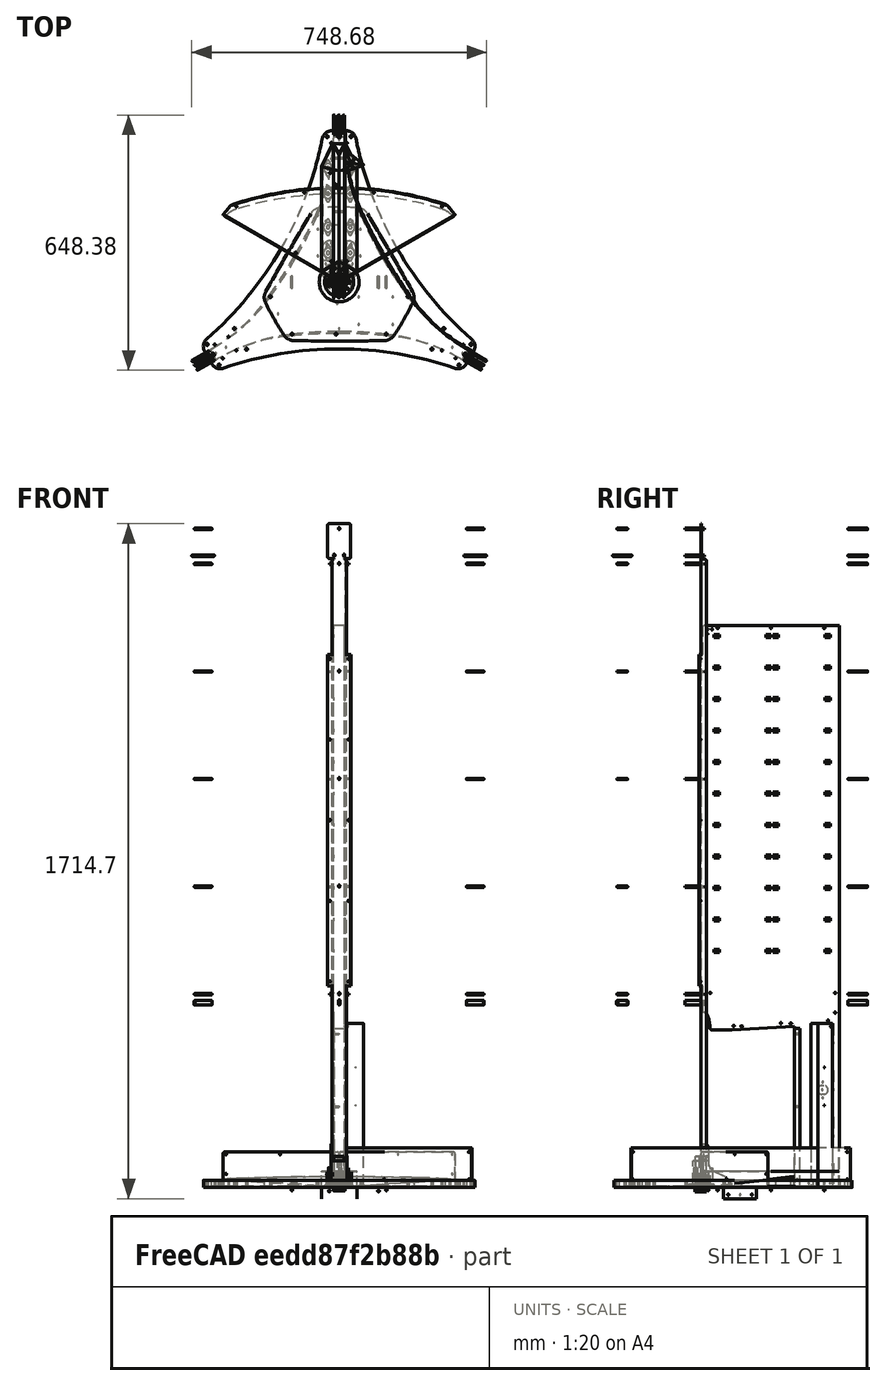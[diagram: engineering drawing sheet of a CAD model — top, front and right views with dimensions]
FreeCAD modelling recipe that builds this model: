
FCSTD DOCUMENT  (FreeCAD 1.1R38827 (Git))
Label: composit_full_size3
License: All rights reserved
LicenseURL: http://en.wikipedia.org/wiki/All_rights_reserved
objects: Part::FeaturePython×246, Sketcher::SketchObject×205, Part::Compound×101, PartDesign::SubShapeBinder×87, PartDesign::Body×73, PartDesign::Pocket×66, PartDesign::Boolean×59, App::Link×51, PartDesign::FeaturePython×49, PartDesign::CoordinateSystem×48, Part::Extrusion×45, Part::Mirroring×39, TechDraw::DrawViewDimension×38, PartDesign::Pad×37, PartDesign::Mirrored×23, App::DocumentObjectGroup×22, Part::Cylinder×18, Part::Feature×17, PartDesign::Hole×15, PartDesign::Plane×10, +28 more types
note: 1842 computed .brp shape members not serialized (recipe doc carries the construction recipe); baked Part::Feature solids carry a one-line shape summary decoded from their .brp
EXTERNAL_REF file=basin_big.FCStd obj=Spreadsheet
EXTERNAL_REF file=composit-properties.FCStd obj=Spreadsheet
EXTERNAL_REF file=module.FCStd obj=Spreadsheet
EXTERNAL_REF file=module.FCStd obj=Sketch
EXTERNAL_REF file=dropper.FCStd obj=Sketch007
EXTERNAL_REF file=dropper.FCStd obj=Sketch008
EXTERNAL_REF file=dropper.FCStd obj=Connect
EXTERNAL_REF file=hub2108.FCStd obj=Body
EXTERNAL_REF file=U-fix.FCStd obj=Body
EXTERNAL_REF file=ULY-P91-20W.FCStd obj=Sketch001
EXTERNAL_REF file=module.FCStd obj=Body
EXTERNAL_REF file=hub2108.FCStd obj=Sketch
EXTERNAL_REF file=hub2108.FCStd obj=Sketch001
EXTERNAL_REF file=U-fix.FCStd obj=Sketch002
EXTERNAL_REF file=hub2108.FCStd obj=Sketch002
EXTERNAL_REF file=hub2108.FCStd obj=Sketch003
EXTERNAL_REF file=ULZ-P02-14W.FCStd obj=Sketch
EXTERNAL_REF file=UET-VAS-060A20_12V_IP20.FCStd obj=Sketch001
EXTERNAL_REF file=composit_full_size3_composit_cut.FCStd obj=Link026
EXTERNAL_REF file=socket_fixture.FCStd obj=Sketch003
EXTERNAL_REF file=../../horec/el/horec_el3/plate_cut.FCStd obj=Clone
EXTERNAL_REF file=prima_jamb.FCStd obj=Body
EXTERNAL_REF file=filter.FCStd obj=Sketch003
EXTERNAL_REF file=filter.FCStd obj=Join
EXTERNAL_REF file=filter.FCStd obj=Join001
EXTERNAL_REF file=filter.FCStd obj=Sketch005
EXTERNAL_REF file=../../horec/el/horec_el3/plate_cut2.FCStd obj=Extrude001
EXTERNAL_REF file=filter.FCStd obj=Body003

FEATURE [Sketcher::SketchObject] Sketch
  ArcFitTolerance = 0
  FullyConstrained = true
  MakeInternals = false
  expr: Constraints[5] = <<Properties>>.endface_width
  expr: Constraints[9] = Spreadsheet.total_length
  sketch-geometry (4):
    g0: LineSegment [constr] StartX=-2.7195e-12 StartY=2.3473e-12 StartZ=0 EndX=14.5 EndY=8.37158 EndZ=0
    g1: LineSegment StartX=14.5 StartY=8.37158 StartZ=0 EndX=14.5 EndY=351.872 EndZ=0
    g2: GeomPoint [constr] X=-14.5 Y=351.872 Z=0
    g3: LineSegment StartX=14.5 StartY=351.872 StartZ=0 EndX=0 EndY=351.872 EndZ=0
  constraints (14):
    c: Coincident(g-1,g0)
    c: Coincident(g0,g1)
    c: Vertical(g1)
    c: Angle(g0) = 0.523599
    c: Symmetric(g2,g1,g-2)
    c: DistanceX(g2,g1) = 29
    c: Coincident(g3,g1)
    c: PointOnObject(g3,g-2)
    c: Horizontal(g3)
    c: DistanceY(g3) = 351.872
    c: Distance(g0,g1) = 352.17  'max_r'
    c: DistanceX(g1) = 14.5
    c: DistanceY(g1) = 8.37158
    c: Distance(g0) = 16.7432  'connection_offset'
FEATURE [Spreadsheet::Sheet] Spreadsheet  label="Properties"
  cells = B2(total_length)==22.5 mm + module#<<Properties>>.module_width + plane_middle; C2(endface_width)==29 mm; D2(rivet_d)==3.4 mm; E2(total_height)==modules_span + basin_big#<<Properties>>.height + 76 mm; F2(number_of_modules)=11; G2(module_distance_x)==2 mm; H2(modules_span)==<<module>>#<<Properties>>.module_fixture_distance_y * (number_of_modules - 1) + <<module>>#<<Properties>>.module_height; I2(top_offset)==27 mm; J2(plane_middle)==module#<<Properties>>.module_width + 25 mm + petal_offset; K2(inner_width)==endface_width - composit_properties#<<Properties>>.thickness * 2; L2(dropper_distance)==65 mm; M2(plane_width)==22.5 mm + module#<<Properties>>.module_width + plane_middle - petal_offset; N2(petal_offset)==endface_width / 2 / tan(60)
FEATURE [Part::Mirroring] Part__Mirroring  label="Sketch (Mirror #1)"
  Base = (0,0,0)
  Normal = (1,0,0)
  Source = -> Sketch
FEATURE [Part::Compound] Compound
  Links = -> [Part__Mirroring,Sketch]
FEATURE [Sketcher::SketchObject] Sketch001  label="part_main_sketch"
  ArcFitTolerance = 0
  ExternalGeometry = -> [Sketch]
  FullyConstrained = true
  MakeInternals = false
  expr: Constraints[7] = composit_properties#<<Properties>>.thickness
  sketch-geometry (3):
    g0: LineSegment StartX=0 StartY=351.872 StartZ=0 EndX=14.5 EndY=351.872 EndZ=0
    g1: LineSegment StartX=14.5 StartY=351.872 StartZ=0 EndX=14.5 EndY=4.90748 EndZ=0
    g2: LineSegment StartX=14.5 StartY=4.90748 StartZ=0 EndX=29.6554 EndY=-3.84252 EndZ=0
  constraints (9):
    c: PointOnObject(g0,g-2)
    c: Coincident(g0,g-3)
    c: Horizontal(g0)
    c: Coincident(g0,g1)
    c: PointOnObject(g1,g-3)
    c: Coincident(g1,g2)
    c: Angle(g2) = -0.523599
    c: Distance(g-3,g2) = 3
    c: Distance(g2) = 17.5
FEATURE [Part::Mirroring] Part__Mirroring001  label="part_main_sketch (Mirror #2)"
  Base = (0,0,0)
  Normal = (1,0,0)
  Source = -> Sketch001
FEATURE [Part::Compound] Compound001  label="part1_base"
  Links = -> [Part__Mirroring001,Sketch001]
FEATURE [Part::FeaturePython] Array001  label="2part_base"  # Draft array (typed FeaturePython)
  AlwaysSyncPlacement = false
  Angle = 240
  ArrayType = 1
  Axis = (0,0,1)
  Base = -> Compound
  Center = (0,0,0)
  Count = 2
  ExpandArray = false
  Fuse = false
  IntervalAxis = (0,0,0)
  IntervalX = (50,0,0)
  IntervalY = (0,50,0)
  IntervalZ = (0,0,50)
  NumberCircles = 3
  NumberPolar = 2
  NumberX = 2
  NumberY = 2
  NumberZ = 1
  PlacementList = 2 placements: [(0,0,0),(0,0,0)]
  RadialDistance = 50
  ScaleList = (2) [(1,1,1),(1,1,1)]
  Symmetry = 1
  TangentialDistance = 25
FEATURE [PartDesign::SubShapeBinder] Binder
  BindCopyOnChange = 0
  BindMode = 0
  ClaimChildren = true
  Context = -> Body [Binder.]
  Fuse = false
  MakeFace = true
  OffsetFill = false
  OffsetIntersection = false
  OffsetJoinType = 0
  OffsetOpenResult = false
  PartialLoad = false
  Relative = true
  Support = -> [Compound001]
  _Version = 2
  expr: Support = <<part1_base>>._self
FEATURE [PartDesign::SubShapeBinder] Binder001
  BindCopyOnChange = 0
  BindMode = 0
  ClaimChildren = true
  Context = -> Body001 [Binder001.]
  Fuse = false
  MakeFace = true
  OffsetFill = false
  OffsetIntersection = false
  OffsetJoinType = 0
  OffsetOpenResult = false
  PartialLoad = false
  Placement = pos=(0,0,0) rot=(0,0,1;4.18879rad)
  Relative = false
  Support = -> [Array001]
  _Version = 2
  expr: Support = <<2part_base>>._self
FEATURE [PartDesign::FeaturePython] BaseBend  # WARN: FeaturePython — macro-defined, semantics opaque (R4)
  BendSide = 1
  BendSketch = -> Binder
  MidPlane = false
  Reverse = false
  Suppressed = false
  length = 1428
  radius = 0.1
  thickness = 0.3
  expr: length = <<Properties>>.total_height
  expr: radius = composit_properties#<<Properties>>.bend_r
  expr: thickness = composit_properties#<<Properties>>.al_thickness
FEATURE [PartDesign::FeaturePython] BaseBend001  # WARN: FeaturePython — macro-defined, semantics opaque (R4)
  BendSide = 0
  BendSketch = -> Binder001
  MidPlane = false
  Reverse = false
  Suppressed = false
  length = 1428
  radius = 0.1
  thickness = 0.3
  expr: length = <<Properties>>.total_height
  expr: radius = composit_properties#<<Properties>>.bend_r
  expr: thickness = composit_properties#<<Properties>>.al_thickness
FEATURE [App::Link] Link  label="module_holes"
  LinkedObject = -> <external module.FCStd>#Sketch
  expr: LinkedObject = module#<<module_holes>>._self
FEATURE [Part::FeaturePython] LinearArray  # WARN: FeaturePython — macro-defined, semantics opaque (R4)
  Alignment = 0
  CellStart = A1
  Count = 11
  Dir = (0,-1,0)
  DirIsDriven = true
  DistributionLaw = 0
  DrivenProperty = 1
  EndInclusive = true
  ExposePlacement = false
  GeneratorMode = 1
  MarkerShape = 1
  MarkerSize = 0
  NumElements = 11
  OrientMode = 0
  Point = (0,0,0)
  PointIsDriven = true
  Reverse = false
  SpanEnd = 800
  SpanStart = 0
  Step = 80
  Type = lattice2LinearArray.LinearArray
  VSGVersion = 1
  Values = 0.0 | 80.0 | 160.0 | 240.0 | 320.0 | 400.0 | 480.0 | 560.0 | 640.0 | 720.0 | 800.0
  ValuesSource = 2
  isLattice = 1
  expr: Count = <<Properties>>.number_of_modules
  expr: SpanEnd = Step * (Count - 1)
  expr: Step = <<module>>#<<Properties>>.module_fixture_distance_y
FEATURE [Part::FeaturePython] LinearArray001  # WARN: FeaturePython — macro-defined, semantics opaque (R4)
  Alignment = 0
  CellStart = A1
  Count = 2
  Dir = (1,0,0)
  DirIsDriven = true
  DistributionLaw = 0
  DrivenProperty = 1
  EndInclusive = true
  ExposePlacement = false
  GeneratorMode = 1
  MarkerShape = 1
  MarkerSize = 0
  NumElements = 2
  OrientMode = 1
  Placement = pos=(-75,0,0) rot=(0,0,1;0rad)
  Point = (0,0,0)
  PointIsDriven = true
  Reverse = false
  SpanEnd = 150
  SpanStart = 0
  Step = 150
  Type = lattice2LinearArray.LinearArray
  VSGVersion = 1
  Values = 0.0 | 150.0
  ValuesSource = 2
  isLattice = 1
  expr: .Placement.Base.x = -SpanEnd / 2
  expr: SpanEnd = Step * (Count - 1)
  expr: Step = <<module>>#<<Properties>>.module_width + <<Properties>>.module_distance_x
FEATURE [Part::FeaturePython] Populate  label="Populate LinearArray with LinearArray001"  # WARN: FeaturePython — macro-defined, semantics opaque (R4)
  Copying = 0
  ExposePlacement = false
  MarkerShape = 1
  MarkerSize = 0
  NumElements = 22
  Object = -> LinearArray001
  OutputCompounding = 0
  PlacementsTo = -> LinearArray
  Referencing = 0
  Type = lattice2PopulateCopies.LatticePopulateCopies
  isLattice = 1
FEATURE [Part::FeaturePython] Populate001  label="Populate Populate LinearArray with LinearArray001 with module_holes"  # WARN: FeaturePython — macro-defined, semantics opaque (R4)
  Copying = 0
  ExposePlacement = false
  MarkerShape = 1
  MarkerSize = 0
  NumElements = 0
  Object = -> Link
  OutputCompounding = 1
  PlacementsTo = -> Populate
  Referencing = 0
  Type = lattice2PopulateCopies.LatticePopulateCopies
  isLattice = 0
FEATURE [Part::Extrusion] Extrude  label="modules_holes"
  Base = -> Populate001
  Dir = (0,0,1)
  DirMode = 2
  FaceMakerClass = Part::FaceMakerBullseye
  FaceMakerMode = 3
  LengthFwd = 31
  LengthRev = 0
  Placement = pos=(0,181.372,1401) rot=(0.57735,0.57735,0.57735;2.0944rad)
  Solid = true
  Symmetric = true
  expr: .Placement.Base.y = <<Properties>>.plane_middle
  expr: .Placement.Base.z = <<Properties>>.total_height - <<Properties>>.top_offset
  expr: LengthFwd = <<Properties>>.endface_width + 2 mm
FEATURE [Sketcher::SketchObject] Sketch003  label="basin_cut_sketch"
  ArcFitTolerance = 0
  ExternalGeometry = -> [Sketch]
  FullyConstrained = true
  MakeInternals = false
  Placement = pos=(0,0,0) rot=(0.57735,0.57735,0.57735;2.0944rad)
  expr: Constraints[27] = <<sink_bend_line>>.FaceAngle
  sketch-geometry (12):
    g0: LineSegment StartX=0 StartY=0 StartZ=0 EndX=238.372 EndY=0 EndZ=0
    g1: LineSegment StartX=238.372 StartY=0 StartZ=0 EndX=238.372 EndY=409.023 EndZ=0
    g2: LineSegment StartX=79.3716 StartY=400 StartZ=0 EndX=28.4155 EndY=400 EndZ=0
    g3: ArcOfCircle CenterX=28.4155 CenterY=405 CenterZ=0 NormalX=0 NormalY=0 NormalZ=1 AngleXU=0 Radius=5 StartAngle=3.17548 EndAngle=4.71239
    g4: ArcOfEllipse CenterX=9.37158 CenterY=400 CenterZ=0 NormalX=0 NormalY=0 NormalZ=1 MajorRadius=45 MinorRadius=14.1284 AngleXU=-1.5708 StartAngle=1.67835 EndAngle=3.14159
    g5: LineSegment [constr] StartX=9.37158 StartY=355 StartZ=0 EndX=9.37158 EndY=445 EndZ=0
    g6: LineSegment [constr] StartX=23.5 StartY=400 StartZ=0 EndX=-4.75684 EndY=400 EndZ=0
    g7: GeomPoint [constr] X=9.37158 Y=357.275 Z=0
    g8: GeomPoint [constr] X=9.37158 Y=442.725 Z=0
    g9: LineSegment StartX=0 StartY=0 StartZ=0 EndX=0 EndY=445 EndZ=0
    g10: LineSegment StartX=0 StartY=445 StartZ=0 EndX=9.37158 EndY=445 EndZ=0
    g11: LineSegment StartX=79.3716 StartY=400 StartZ=0 EndX=238.372 EndY=409.023 EndZ=0
  constraints (25):
    c: Coincident(g-1,g0)
    c: Horizontal(g0)
    c: Coincident(g0,g1)
    c: Vertical(g1)
    c: Horizontal(g2)
    c: Tangent(g3,g2) = 1.5708
    c: InternalAlignment(g5-g8 -> g4) x4
    c: Horizontal(g6)
    c: Tangent(g4,g3) = 1.5708
    c: Coincident(g9,g0)
    c: Coincident(g9,g10)
    c: Vertical(g9)
    c: Horizontal(g10)
    c: Tangent(g10,g4) = 1.5708
    c: DistanceX(g-3,g0) = 230
    c: DistanceY(g2) = 400
    c: DistanceY(g9) = 445
    c: DistanceX(g-3,g4) = 1
    c: Radius(g3) = 5
    c: DistanceX(g6) = 23.5
    c: PointOnObject(g4,g2)
    c: DistanceX(g-3,g2) = 71
    c: Coincident(g11,g2)
    c: Coincident(g11,g1)
    c: Angle(g11) = 0.0566865
FEATURE [Part::Extrusion] Extrude001  label="basin_cut"
  Base = -> Sketch003
  Dir = (1,0,0)
  DirMode = 2
  FaceMakerClass = Part::FaceMakerBullseye
  FaceMakerMode = 3
  LengthFwd = 30
  LengthRev = 0
  Solid = true
  Symmetric = true
FEATURE [Sketcher::SketchObject] Sketch004  label="leg_amplifier_base_sketch"
  ArcFitTolerance = 0
  ExternalGeometry = -> [Sketch003]
  FullyConstrained = true
  MakeInternals = false
  expr: Constraints[5] = <<Properties>>.endface_width / 2
  expr: Constraints[6] = composit_properties#<<Properties>>.bend_r + composit_properties#<<Properties>>.al_thickness
  expr: Constraints[7] = <<Properties>>.endface_width - composit_properties#<<Properties>>.thickness
  sketch-geometry (3):
    g0: LineSegment StartX=-11.5 StartY=-0.4 StartZ=0 EndX=14.5 EndY=-0.4 EndZ=0
    g1: LineSegment StartX=-11.5 StartY=-0.4 StartZ=0 EndX=-11.5 EndY=13 EndZ=0
    g2: LineSegment StartX=14.5 StartY=-0.4 StartZ=0 EndX=14.5 EndY=13 EndZ=0
  constraints (10):
    c: Horizontal(g0)
    c: Coincident(g1,g0)
    c: Vertical(g1)
    c: Coincident(g2,g0)
    c: Vertical(g2)
    c: DistanceX(g0) = 14.5
    c: DistanceY(g0,g-3) = 0.4
    c: DistanceX(g0,g0) = 26
    c: Horizontal(g1,g2)
    c: DistanceY(g-3,g2) = 13
FEATURE [Part::Mirroring] Part__Mirroring002  label="Sketch004 (Mirror #3)"
  Base = (0,0,0)
  Normal = (1,0,0)
  Source = -> Sketch004
FEATURE [Spreadsheet::Sheet] Spreadsheet001  label="Properties001"
  cells = B2(plane_width)==27.5 mm + module#<<Properties>>.module_width * 2 + 20 mm; C2(endface_width)==29 mm; D2(rivet_d)==3.4 mm; E2(total_height)==modules_span + basin_big#<<Properties>>.height; F2(number_of_modules)=11; G2(module_distance_x)==2 mm; H2(modules_span)==<<module>>#<<Properties>>.module_fixture_distance_y * number_of_modules + <<module>>#<<Properties>>.module_height; I2(top_offset)==30.5 mm; J2(plane_middle)==module#<<Properties>>.module_width + 25 mm; K2(inner_width)==endface_width - composit_properties#<<Properties>>.thickness * 2; L2(dropper_distance)==65 mm
FEATURE [Sketcher::SketchObject] Sketch005
  ArcFitTolerance = 0
  FullyConstrained = true
  MakeInternals = false
  expr: Constraints[5] = <<Properties001>>.endface_width
  expr: Constraints[6] = <<Properties001>>.plane_width
  sketch-geometry (4):
    g0: LineSegment [constr] StartX=5.67e-14 StartY=-9.82e-14 StartZ=0 EndX=14.5 EndY=8.37158 EndZ=0
    g1: LineSegment StartX=14.5 StartY=8.37158 StartZ=0 EndX=14.5 EndY=351.872 EndZ=0
    g2: GeomPoint [constr] X=-14.5 Y=351.872 Z=0
    g3: LineSegment StartX=14.5 StartY=351.872 StartZ=0 EndX=0 EndY=351.872 EndZ=0
  constraints (10):
    c: Coincident(g-1,g0)
    c: Coincident(g0,g1)
    c: Vertical(g1)
    c: Angle(g0) = 0.523599
    c: Symmetric(g2,g1,g-2)
    c: DistanceX(g2,g1) = 29
    c: DistanceY(g1,g1) = 343.5
    c: Coincident(g3,g1)
    c: PointOnObject(g3,g-2)
    c: Horizontal(g3)
FEATURE [Sketcher::SketchObject] Sketch006
  ArcFitTolerance = 0
  ExternalGeometry = -> [Sketch005]
  FullyConstrained = true
  MakeInternals = false
  Placement = pos=(0,0,0) rot=(0.57735,0.57735,0.57735;2.0944rad)
  sketch-geometry (12):
    g0: LineSegment StartX=0 StartY=0 StartZ=0 EndX=238.372 EndY=0 EndZ=0
    g1: LineSegment StartX=238.372 StartY=0 StartZ=0 EndX=238.372 EndY=410 EndZ=0
    g2: LineSegment StartX=238.372 StartY=410 StartZ=0 EndX=79.3716 EndY=400 EndZ=0
    g3: LineSegment StartX=79.3716 StartY=400 StartZ=0 EndX=19.9656 EndY=400 EndZ=0
    g4: ArcOfCircle CenterX=19.9656 CenterY=405 CenterZ=0 NormalX=0 NormalY=0 NormalZ=1 AngleXU=0 Radius=5 StartAngle=3.15538 EndAngle=4.71239
    g5: ArcOfEllipse CenterX=9.37158 CenterY=400 CenterZ=0 NormalX=0 NormalY=0 NormalZ=1 MajorRadius=45 MinorRadius=5.62842 AngleXU=-1.5708 StartAngle=1.6806 EndAngle=3.14159
    g6: LineSegment [constr] StartX=9.37158 StartY=355 StartZ=0 EndX=9.37158 EndY=445 EndZ=0
    g7: LineSegment [constr] StartX=15 StartY=400 StartZ=0 EndX=3.74316 EndY=400 EndZ=0
    g8: GeomPoint [constr] X=9.37158 Y=355.353 Z=0
    g9: GeomPoint [constr] X=9.37158 Y=444.647 Z=0
    g10: LineSegment StartX=0 StartY=0 StartZ=0 EndX=0 EndY=445 EndZ=0
    g11: LineSegment StartX=0 StartY=445 StartZ=0 EndX=9.37158 EndY=445 EndZ=0
  constraints (25):
    c: Coincident(g-1,g0)
    c: Horizontal(g0)
    c: Coincident(g0,g1)
    c: Vertical(g1)
    c: Coincident(g1,g2)
    c: Coincident(g2,g3)
    c: Horizontal(g3)
    c: Tangent(g4,g3) = 1.5708
    c: InternalAlignment(g6-g9 -> g5) x4
    c: Horizontal(g7)
    c: Tangent(g5,g4) = 1.5708
    c: Coincident(g10,g0)
    c: Coincident(g10,g11)
    c: Vertical(g10)
    c: Horizontal(g11)
    c: Tangent(g11,g5) = 1.5708
    c: DistanceX(g-3,g0) = 230
    c: DistanceY(g2) = 400
    c: DistanceY(g10) = 445
    c: DistanceX(g-3,g5) = 1
    c: Radius(g4) = 5
    c: DistanceX(g7) = 15
    c: PointOnObject(g5,g3)
    c: DistanceY(g1) = 410
    c: DistanceX(g-3,g2) = 71
FEATURE [Sketcher::SketchObject] Sketch007
  ArcFitTolerance = 0
  ExternalGeometry = -> [Sketch006]
  FullyConstrained = true
  MakeInternals = false
  expr: Constraints[5] = <<Properties001>>.endface_width / 2
  expr: Constraints[6] = composit_properties#<<Properties>>.bend_r + composit_properties#<<Properties>>.al_thickness
  expr: Constraints[7] = <<Properties001>>.endface_width - composit_properties#<<Properties>>.thickness
  sketch-geometry (3):
    g0: LineSegment StartX=-11.5 StartY=237.972 StartZ=0 EndX=14.5 EndY=237.972 EndZ=0
    g1: LineSegment StartX=-11.5 StartY=237.972 StartZ=0 EndX=-11.5 EndY=258.372 EndZ=0
    g2: LineSegment StartX=14.5 StartY=237.972 StartZ=0 EndX=14.5 EndY=258.372 EndZ=0
  constraints (10):
    c: Horizontal(g0)
    c: Coincident(g1,g0)
    c: Vertical(g1)
    c: Coincident(g2,g0)
    c: Vertical(g2)
    c: DistanceX(g0) = 14.5
    c: DistanceY(g0,g-3) = 0.4
    c: DistanceX(g0,g0) = 26
    c: Horizontal(g1,g2)
    c: DistanceY(g-3,g2) = 20
FEATURE [Part::FeaturePython] BaseBend003  label="BaseBend002_material_0.30ansi002"  # WARN: FeaturePython — macro-defined, semantics opaque (R4)
  BendSide = 0
  BendSketch = -> Part__Mirroring002
  MidPlane = false
  Reverse = false
  length = 403.5
  radius = 0.1
  thickness = 0.3
  expr: length = <<leg_amplifier>>.length
  expr: radius = composit_properties#<<Properties>>.bend_r
  expr: thickness = composit_properties#<<Properties>>.al_thickness
FEATURE [App::LinkGroup] CopyOnChangeGroup
  ElementList = -> [BaseBend003,Sketch007,Sketch006,Sketch005,Spreadsheet001]
  LinkMode = 1
FEATURE [App::Link] Link002  label="leg_amplifier_link"
  BendSketch = -> Part__Mirroring002
  LinkCopyOnChange = 2
  LinkCopyOnChangeGroup = -> CopyOnChangeGroup
  LinkCopyOnChangeSource = -> BaseBend002
  LinkCopyOnChangeTouched = true
  LinkPlacement = pos=(206.436,-119.186,0) rot=(0,0,1;4.18879rad)
  LinkedObject = -> BaseBend003
  Placement = pos=(206.436,-119.186,0) rot=(0,0,1;4.18879rad)
  expr: .LinkPlacement.Base.x = (<<Properties>>.petal_offset + 230 mm) * cos(-30)
  expr: .LinkPlacement.Base.y = (<<Properties>>.petal_offset + 230 mm) * sin(-30)
FEATURE [Part::Compound] Compound008
  Links = -> [Sketch004]
FEATURE [Part::FeaturePython] BaseBend002  label="leg_amplifier"  # WARN: FeaturePython — macro-defined, semantics opaque (R4)
  BendSide = 1
  BendSketch = -> Compound008
  MidPlane = false
  Placement = pos=(0,238.372,0) rot=(0,0,1;0rad)
  Reverse = false
  length = 403.5
  radius = 0.1
  thickness = 0.3
  expr: .Placement.Base.y = <<Properties>>.petal_offset + 230 mm
  expr: radius = composit_properties#<<Properties>>.bend_r
  expr: thickness = composit_properties#<<Properties>>.al_thickness
FEATURE [Part::Compound] Compound006  label="mirror_compound"
  Links = -> [BaseBend002]
  Placement = pos=(0,0,0) rot=(0,0,1;2.0944rad)
FEATURE [Part::Compound] Compound007  label="part2_fuse1"
  Links = -> [Link002,Compound006]
  expr: Links = list(<<leg_amplifier_link>>._self; <<mirror_compound>>._self)
FEATURE [App::DocumentObjectGroup] Group006  label="composit_cut"
FEATURE [App::DocumentObjectGroup] Group007  label="PP_cut"
FEATURE [App::DocumentObjectGroup] Group008  label="plywood_cut"
FEATURE [App::DocumentObjectGroup] Group002  label="cut"
  Group = -> [Group006,Group007,Group008]
FEATURE [Sketcher::SketchObject] Sketch008  label="pillar_base_sketch"
  ArcFitTolerance = 0
  FullyConstrained = true
  MakeInternals = false
  sketch-geometry (5):
    g0: LineSegment StartX=-18.3 StartY=19 StartZ=0 EndX=-18.3 EndY=-4.62e-14 EndZ=0
    g1: LineSegment StartX=-18.3 StartY=-4.62e-14 StartZ=0 EndX=18.3 EndY=-4.62e-14 EndZ=0
    g2: LineSegment StartX=18.3 StartY=-4.62e-14 StartZ=0 EndX=18.3 EndY=19 EndZ=0
    g3: LineSegment [constr] StartX=18.3 StartY=19 StartZ=0 EndX=-18.3 EndY=19 EndZ=0
    g4: GeomPoint [constr] X=8.6e-15 Y=9.5 Z=0
  constraints (13):
    c: Coincident(g0,g1)
    c: Coincident(g1,g2)
    c: Coincident(g2,g3)
    c: Coincident(g3,g0)
    c: Horizontal(g1)
    c: Horizontal(g3)
    c: Vertical(g0)
    c: Vertical(g2)
    c: Symmetric(g1,g0,g4)
    c: PointOnObject(g4,g-2)
    c: PointOnObject(g1,g-1)
    c: DistanceX(g1,g1) = 36.6  'width'
    c: DistanceY(g2,g2) = 19  'length'
FEATURE [PartDesign::SubShapeBinder] Binder002
  BindCopyOnChange = 0
  BindMode = 0
  ClaimChildren = true
  Fuse = false
  MakeFace = true
  OffsetFill = false
  OffsetIntersection = false
  OffsetJoinType = 0
  OffsetOpenResult = false
  PartialLoad = false
  Relative = false
  Support = -> [Sketch008]
  _Version = 2
FEATURE [PartDesign::FeaturePython] BaseBend004  label="pillar_BaseBend"  # WARN: FeaturePython — macro-defined, semantics opaque (R4)
  BendSide = 1
  BendSketch = -> Binder002
  MidPlane = false
  Reverse = false
  Suppressed = false
  length = 1594
  radius = 2
  thickness = 2
FEATURE [Sketcher::SketchObject] Sketch009
  ArcFitTolerance = 0
  AttachmentOffset = pos=(0,1594,0) rot=(0,0,1;0rad)
  AttachmentSupport = -> [XZ_Plane014]
  FullyConstrained = true
  MakeInternals = false
  MapMode = 5
  Placement = pos=(0,3.539e-13,1594) rot=(1,0,0;1.5708rad)
  expr: .AttachmentOffset.Base.y = BaseBend004.length
  expr: Constraints[15] = <<pillar_base_sketch>>.Constraints.width - (<<pillar_BaseBend>>.thickness + <<pillar_BaseBend>>.radius) * 2
  sketch-geometry (16):
    g0: LineSegment StartX=-14.3 StartY=0 StartZ=0 EndX=14.3 EndY=0 EndZ=0
    g1: LineSegment StartX=14.3 StartY=0 StartZ=0 EndX=14.3 EndY=2 EndZ=0
    g2: LineSegment StartX=14.3 StartY=2 StartZ=0 EndX=34.5 EndY=2 EndZ=0
    g3: LineSegment StartX=37.5 StartY=5 StartZ=0 EndX=37.5 EndY=87 EndZ=0
    g4: LineSegment StartX=34.5 StartY=90 StartZ=0 EndX=-34.5 EndY=90 EndZ=0
    g5: LineSegment StartX=-37.5 StartY=87 StartZ=0 EndX=-37.5 EndY=5 EndZ=0
    g6: LineSegment StartX=-34.5 StartY=2 StartZ=0 EndX=-14.3 EndY=2 EndZ=0
    g7: LineSegment StartX=-14.3 StartY=2 StartZ=0 EndX=-14.3 EndY=0 EndZ=0
    g8: ArcOfCircle CenterX=34.5 CenterY=5 CenterZ=0 NormalX=0 NormalY=0 NormalZ=1 AngleXU=0 Radius=3 StartAngle=4.71239 EndAngle=6.28319
    g9: GeomPoint [constr] X=37.5 Y=2 Z=0
    g10: ArcOfCircle CenterX=34.5 CenterY=87 CenterZ=0 NormalX=0 NormalY=0 NormalZ=1 AngleXU=0 Radius=3 StartAngle=1.02861e-11 EndAngle=1.5708
    g11: GeomPoint [constr] X=37.5 Y=90 Z=0
    g12: ArcOfCircle CenterX=-34.5 CenterY=87 CenterZ=0 NormalX=0 NormalY=0 NormalZ=1 AngleXU=0 Radius=3 StartAngle=1.5708 EndAngle=3.14159
    g13: GeomPoint [constr] X=-37.5 Y=90 Z=0
    g14: ArcOfCircle CenterX=-34.5 CenterY=5 CenterZ=0 NormalX=0 NormalY=0 NormalZ=1 AngleXU=0 Radius=3 StartAngle=3.14159 EndAngle=4.71239
    g15: GeomPoint [constr] X=-37.5 Y=2 Z=0
  constraints (38):
    c: PointOnObject(g0,g-1)
    c: Coincident(g0,g1)
    c: Vertical(g1)
    c: Coincident(g1,g2)
    c: Horizontal(g2)
    c: Vertical(g3)
    c: Vertical(g5)
    c: Horizontal(g6)
    c: Coincident(g6,g7)
    c: Vertical(g7)
    c: Coincident(g0,g7)
    c: Horizontal(g0)
    c: Symmetric(g6,g1,g-2)
    c: Symmetric(g11,g13,g-2)
    c: DistanceY(g1,g1) = 2
    c: DistanceX(g0,g0) = 28.6
    c: PointOnObject(g9,g2)
    c: PointOnObject(g9,g3)
    c: Tangent(g2,g8) = -1.5708
    c: Tangent(g3,g8) = -1.5708
    c: PointOnObject(g11,g3)
    c: PointOnObject(g11,g4)
    c: Tangent(g3,g10) = -1.5708
    c: Tangent(g4,g10) = -1.5708
    c: PointOnObject(g13,g4)
    c: PointOnObject(g13,g5)
    c: Tangent(g4,g12) = -1.5708
    c: Tangent(g5,g12) = -1.5708
    c: PointOnObject(g15,g5)
    c: PointOnObject(g15,g6)
    c: Tangent(g5,g14) = -1.5708
    c: Tangent(g6,g14) = -1.5708
    c: Equal(g14,g8)
    c: Equal(g14,g10)
    c: Equal(g14,g12)
    c: Radius(g14) = 3
    c: DistanceX(g13,g11) = 75
    c: DistanceY(g9,g11) = 88
FEATURE [Sketcher::SketchObject] Sketch011  label="pillar_bottom_cut_vert"
  ArcFitTolerance = 0
  AttachmentSupport = -> [XZ_Plane015]
  FullyConstrained = true
  MakeInternals = false
  MapMode = 5
  Placement = pos=(0,0,0) rot=(1,0,0;1.5708rad)
  expr: Constraints[15] = <<pillar_bottom_BaseBend>>.length
  expr: Constraints[16] = <<pillar_bottom_BaseBend>>.radius + <<pillar_bottom_BaseBend>>.thickness
  expr: Constraints[27] = <<pillar_base_sketch>>.Constraints.length - 4 mm
  sketch-geometry (15):
    g0: LineSegment StartX=-50.5 StartY=0 StartZ=0 EndX=-50.5 EndY=75 EndZ=0
    g1: LineSegment StartX=-45.5 StartY=80 StartZ=0 EndX=-40.5 EndY=80 EndZ=0
    g2: LineSegment StartX=50.5 StartY=4 StartZ=0 EndX=50.5 EndY=0 EndZ=0
    g3: LineSegment StartX=50.5 StartY=0 StartZ=0 EndX=-50.5 EndY=0 EndZ=0
    g4: ArcOfCircle CenterX=-45.5 CenterY=75 CenterZ=0 NormalX=0 NormalY=0 NormalZ=1 AngleXU=0 Radius=5 StartAngle=1.5708 EndAngle=3.14159
    g5: GeomPoint [constr] X=-50.5 Y=80 Z=0
    g6: ArcOfCircle CenterX=-40.5 CenterY=75 CenterZ=0 NormalX=0 NormalY=0 NormalZ=1 AngleXU=0 Radius=5 StartAngle=-9e-16 EndAngle=1.5708
    g7: GeomPoint [constr] X=-35.5 Y=80 Z=0
    g8: ArcOfCircle CenterX=45.5 CenterY=4 CenterZ=0 NormalX=0 NormalY=0 NormalZ=1 AngleXU=0 Radius=5 StartAngle=0 EndAngle=1.13485
    g9: GeomPoint [constr] X=50.5 Y=7.18672 Z=0
    g10: LineSegment StartX=-35.5 StartY=75 StartZ=0 EndX=-35.5 EndY=64.709 EndZ=0
    g11: LineSegment StartX=-19.6724 StartY=39.8753 StartZ=0 EndX=47.6113 EndY=8.53236 EndZ=0
    g12: ArcOfCircle CenterX=-8.10401 CenterY=64.709 CenterZ=0 NormalX=0 NormalY=0 NormalZ=1 AngleXU=0 Radius=27.396 StartAngle=3.14159 EndAngle=4.27645
    g13: GeomPoint [constr] X=-19.6724 Y=39.8753 Z=0
    g14: GeomPoint [constr] X=-13.5 Y=37 Z=0
  constraints (34):
    c: PointOnObject(g0,g-1)
    c: Vertical(g0)
    c: Horizontal(g1)
    c: Vertical(g2)
    c: Coincident(g2,g3)
    c: Coincident(g3,g0)
    c: PointOnObject(g5,g0)
    c: PointOnObject(g5,g1)
    c: Tangent(g0,g4) = 1.5708
    c: Tangent(g1,g4) = 1.5708
    c: PointOnObject(g7,g1)
    c: Tangent(g1,g6) = 1.5708
    c: PointOnObject(g9,g2)
    c: Tangent(g2,g8) = 1.5708
    c: Symmetric(g0,g2,g-2)
    c: DistanceX(g3,g3) = 101
    c: DistanceY(g2) = 4
    c: DistanceY(g5) = 80  'height'
    c: Radius(g4) = 5
    c: Radius(g8) = 5
    c: Equal(g4,g6)
    c: PointOnObject(g7,g10)
    c: PointOnObject(g9,g11)
    c: Vertical(g10)
    c: Tangent(g10,g6) = 1.5708
    c: Tangent(g12,g10) = -1.5708
    c: Tangent(g12,g11) = -1.5708
    c: DistanceX(g5,g7) = 15
    c: Tangent(g11,g8) = 1.5708
    c: Coincident(g11,g13)
    c: PointOnObject(g14,g11)
    c: DistanceY(g14) = 37
    c: DistanceX(g0,g14) = 37
    c: DistanceX(g11) = -19.6724
FEATURE [Sketcher::SketchObject] Sketch012
  ArcFitTolerance = 0
  AttachmentSupport = -> [XY_Plane015]
  FullyConstrained = true
  MakeInternals = false
  MapMode = 5
  expr: Constraints[18] = <<pillar_bottom_BaseSketch>>.Constraints.leg_length
  expr: Constraints[20] = <<pillar_bottom_BaseBend>>.radius + <<pillar_bottom_BaseBend>>.thickness
  expr: Constraints[9] = <<pillar_bottom_BaseBend>>.length
  sketch-geometry (9):
    g0: LineSegment StartX=-50.5 StartY=-4 StartZ=0 EndX=-50.5 EndY=0 EndZ=0
    g1: LineSegment StartX=-50.5 StartY=0 StartZ=0 EndX=50.5 EndY=0 EndZ=0
    g2: LineSegment StartX=50.5 StartY=0 StartZ=0 EndX=50.5 EndY=-4 EndZ=0
    g3: LineSegment StartX=29.5 StartY=-25 StartZ=0 EndX=-29.5 EndY=-25 EndZ=0
    g4: GeomPoint [constr] X=0 Y=-12.5 Z=0
    g5: ArcOfCircle CenterX=29.5 CenterY=-4 CenterZ=0 NormalX=0 NormalY=0 NormalZ=1 AngleXU=0 Radius=21 StartAngle=4.71239 EndAngle=6.28319
    g6: GeomPoint [constr] X=50.5 Y=-25 Z=0
    g7: ArcOfCircle CenterX=-29.5 CenterY=-4 CenterZ=0 NormalX=0 NormalY=0 NormalZ=1 AngleXU=0 Radius=21 StartAngle=3.14159 EndAngle=4.71239
    g8: GeomPoint [constr] X=-50.5 Y=-25 Z=0
  constraints (21):
    c: Coincident(g0,g1)
    c: Coincident(g1,g2)
    c: Horizontal(g1)
    c: Horizontal(g3)
    c: Vertical(g0)
    c: Vertical(g2)
    c: Symmetric(g1,g8,g4)
    c: PointOnObject(g4,g-2)
    c: PointOnObject(g1,g-1)
    c: DistanceX(g1,g1) = 101
    c: PointOnObject(g6,g2)
    c: PointOnObject(g6,g3)
    c: Tangent(g2,g5) = 1.5708
    c: Tangent(g3,g5) = 1.5708
    c: PointOnObject(g8,g0)
    c: PointOnObject(g8,g3)
    c: Tangent(g0,g7) = 1.5708
    c: Tangent(g3,g7) = 1.5708
    c: DistanceY(g6,g-1) = 25
    c: Equal(g7,g5)
    c: DistanceY(g2,g-1) = 4
FEATURE [Part::FeaturePython] WireFilter  # WARN: FeaturePython — macro-defined, semantics opaque (R4)
  AttacherType = Attacher::AttachEngine3D
  ClaimChildren = true
  ColorKeyCount = 8
  Colorize = true
  FaceMaker = 5
  FixNormal = false
  FollowSource = true
  InvertedFaceScale = 20
  MaxWires = 25
  Normal = (0,1,-2e-16)
  OffsetFill = false
  OffsetIntersection = false
  OffsetJoin = 0
  OffsetOpenResult = false
  Scale = (1,1,1)
  SelectEdges = false
  Source = -> Sketch011
  UniformScale = 1
  UseDefault = false
  UseSelected = true
  UseSelectedEdges = false
  Version = 0.2022.02.09
  WireOrder = [1]
FEATURE [Part::FeaturePython] WireFilter001  # WARN: FeaturePython — macro-defined, semantics opaque (R4)
  AttacherType = Attacher::AttachEngine3D
  ClaimChildren = true
  ColorKeyCount = 8
  Colorize = true
  FaceMaker = 5
  FixNormal = false
  FollowSource = true
  InvertedFaceScale = 5
  MaxWires = 25
  Normal = (0,0,1)
  OffsetFill = false
  OffsetIntersection = false
  OffsetJoin = 0
  OffsetOpenResult = false
  Scale = (1,1,1)
  SelectEdges = false
  Source = -> Sketch012
  UniformScale = 1
  UseDefault = false
  UseSelected = true
  UseSelectedEdges = false
  Version = 0.2022.02.09
  WireOrder = [1]
FEATURE [Sketcher::SketchObject] Sketch013
  ArcFitTolerance = 0
  AttachmentSupport = -> [XY_Plane016]
  FullyConstrained = true
  MakeInternals = false
  MapMode = 5
  sketch-geometry (5):
    g0: LineSegment StartX=-36 StartY=25 StartZ=0 EndX=-36 EndY=0 EndZ=0
    g1: LineSegment StartX=-36 StartY=0 StartZ=0 EndX=36 EndY=0 EndZ=0
    g2: LineSegment StartX=36 StartY=0 StartZ=0 EndX=36 EndY=25 EndZ=0
    g3: LineSegment [constr] StartX=36 StartY=25 StartZ=0 EndX=-36 EndY=25 EndZ=0
    g4: GeomPoint [constr] X=0 Y=12.5 Z=0
  constraints (13):
    c: Coincident(g0,g1)
    c: Coincident(g1,g2)
    c: Coincident(g2,g3)
    c: Coincident(g3,g0)
    c: Horizontal(g1)
    c: Horizontal(g3)
    c: Vertical(g0)
    c: Vertical(g2)
    c: Symmetric(g1,g0,g4)
    c: PointOnObject(g4,g-2)
    c: PointOnObject(g1,g-1)
    c: DistanceY(g2,g2) = 25
    c: DistanceX(g1,g1) = 72
FEATURE [PartDesign::FeaturePython] BaseBend006  # WARN: FeaturePython — macro-defined, semantics opaque (R4)
  BendSide = 1
  BendSketch = -> Sketch013
  MidPlane = false
  Reverse = false
  Suppressed = false
  length = 84
  radius = 2
  thickness = 2
FEATURE [PartDesign::FeaturePython] Bend  # WARN: FeaturePython — macro-defined, semantics opaque (R4)
  AutoMiter = true
  BaseFeature = -> BaseBend006
  BendType = 1
  LengthList = [70]
  LengthSpec = 1
  NonperforationMaxLength = 5
  Perforate = false
  PerforationAngle = 0
  PerforationInitialLength = 5
  PerforationMaxLength = 5
  ReliefFactor = 0.7
  Suppressed = false
  UseReliefFactor = false
  angle = 90
  baseObject = -> BaseBend006 [Edge26]
  bendAList = [90]
  extend1 = 0
  extend2 = 0
  gap1 = 0
  gap2 = 0
  invert = true
  kfactor = 0.5
  length = 70
  maxExtendDist = 5
  minGap = 0.1
  minReliefGap = 1
  miterangle1 = 0
  miterangle2 = 0
  offset = 0
  radius = 2
  reliefType = 0
  reliefd = 1
  reliefw = 0.8
  sketchflip = false
  sketchinvert = false
  unfold = false
  expr: radius = BaseBend006.radius
FEATURE [Sketcher::SketchObject] Sketch014  label="basement_bottom_sketch"
  ArcFitTolerance = 0
  FullyConstrained = true
  MakeInternals = false
  sketch-geometry (4):
    g0: LineSegment [constr] StartX=0 StartY=0 StartZ=0 EndX=147.224 EndY=85 EndZ=0
    g1: ArcOfCircle CenterX=930.111 CenterY=537 CenterZ=0 NormalX=0 NormalY=0 NormalZ=1 AngleXU=0 Radius=904 StartAngle=3.33435 EndAngle=3.66519
    g2: ArcOfCircle CenterX=18.317 CenterY=359.033 CenterZ=0 NormalX=0 NormalY=0 NormalZ=1 AngleXU=0 Radius=25 StartAngle=0.19276 EndAngle=1.51982
    g3: ArcOfCircle CenterX=0 CenterY=0 CenterZ=0 NormalX=0 NormalY=0 NormalZ=1 AngleXU=0 Radius=384.5 StartAngle=1.51982 EndAngle=1.5708
  constraints (13):
    c: Coincident(g0,g-1)
    c: Angle(g0) = 0.523599
    c: Coincident(g1,g0)
    c: PointOnObject(g1,g0)
    c: Tangent(g2,g1) = 1.5708
    c: Distance(g0) = 170  'min_r'
    c: Radius(g2) = 25
    c: PointOnObject(g3,g-2)
    c: PointOnObject(g3,g-2)
    c: Tangent(g3,g2) = -1.5708
    c: PointOnObject(g3,g-1)
    c: DistanceY(g3) = 384.5  'outer_r'
    c: Radius(g1) = 904
FEATURE [Sketcher::SketchObject] Sketch015  label="basement_sketch"
  ArcFitTolerance = 0
  FullyConstrained = true
  MakeInternals = false
  sketch-geometry (4):
    g0: LineSegment [constr] StartX=0 StartY=0 StartZ=0 EndX=219.104 EndY=126.5 EndZ=0
    g1: ArcOfCircle CenterX=-472.335 CenterY=-272.703 CenterZ=0 NormalX=0 NormalY=0 NormalZ=1 AngleXU=0 Radius=798.406 StartAngle=0.523599 EndAngle=0.870893
    g2: ArcOfCircle CenterX=12 CenterY=302.433 CenterZ=0 NormalX=0 NormalY=0 NormalZ=1 AngleXU=0 Radius=46.5 StartAngle=0.870893 EndAngle=1.53114
    g3: ArcOfCircle CenterX=0 CenterY=0 CenterZ=0 NormalX=0 NormalY=0 NormalZ=1 AngleXU=0 Radius=349.171 StartAngle=1.53114 EndAngle=1.5708
  constraints (13):
    c: Coincident(g1,g0)
    c: Angle(g0) = 0.523599
    c: Radius(g1) = 798.406
    c: Radius(g2) = 46.5
    c: Radius(g3) = 349.171  'max_r'
    c: Coincident(g3,g0)
    c: Coincident(g3,g-1)
    c: Tangent(g2,g1) = -1.5708
    c: Tangent(g3,g2) = -1.5708
    c: PointOnObject(g3,g-2)
    c: Distance(g0) = 253  'min_r'
    c: DistanceX(g2) = 12
    c: PointOnObject(g1,g0)
FEATURE [Part::Mirroring] Part__Mirroring003  label="Sketch014 (Mirror #4)"
  Base = (0,0,0)
  Normal = (1,0,0)
  Source = -> Sketch014
FEATURE [Part::Compound] Compound009
  Links = -> [Part__Mirroring003,Sketch014]
FEATURE [Part::FeaturePython] Array002  label="basement_bottom_2d"  # Draft array (typed FeaturePython)
  AlwaysSyncPlacement = false
  Angle = 360
  ArrayType = 1
  Axis = (0,0,1)
  Base = -> Compound009
  Center = (0,0,0)
  Count = 3
  ExpandArray = false
  Fuse = false
  IntervalAxis = (0,0,0)
  IntervalX = (50,0,0)
  IntervalY = (0,50,0)
  IntervalZ = (0,0,50)
  NumberCircles = 3
  NumberPolar = 3
  NumberX = 2
  NumberY = 2
  NumberZ = 1
  PlacementList = 3 placements: [(0,0,0),(0,0,0),(0,0,0)]
  RadialDistance = 50
  ScaleList = (3) [(1,1,1),(1,1,1),(1,1,1)]
  Symmetry = 1
  TangentialDistance = 25
FEATURE [Part::Mirroring] Part__Mirroring004  label="Sketch015 (Mirror #5)"
  Base = (0,0,0)
  Normal = (1,0,0)
  Source = -> Sketch015
FEATURE [PartDesign::SubShapeBinder] Binder003
  BindCopyOnChange = 0
  BindMode = 0
  ClaimChildren = true
  Context = -> Body007 [Binder003.]
  Fuse = false
  MakeFace = true
  OffsetFill = false
  OffsetIntersection = false
  OffsetJoinType = 0
  OffsetOpenResult = false
  PartialLoad = false
  Relative = false
  Support = -> [Array002]
  _Version = 2
FEATURE [PartDesign::SubShapeBinder] Binder004
  BindCopyOnChange = 0
  BindMode = 0
  ClaimChildren = true
  Context = -> Body009 [Binder004.]
  Fuse = false
  MakeFace = true
  Offset = 2
  OffsetFill = false
  OffsetIntersection = false
  OffsetJoinType = 0
  OffsetOpenResult = false
  PartialLoad = false
  Relative = false
  Support = -> [Array002]
  _Version = 2
FEATURE [PartDesign::SubShapeBinder] Binder005
  BindCopyOnChange = 0
  BindMode = 0
  ClaimChildren = true
  Context = -> Body006 [Binder005.]
  Fuse = false
  MakeFace = true
  OffsetFill = false
  OffsetIntersection = false
  OffsetJoinType = 0
  OffsetOpenResult = false
  PartialLoad = false
  Relative = false
  Support = -> [Array003]
  _Version = 2
FEATURE [PartDesign::SubShapeBinder] Binder006
  BindCopyOnChange = 0
  BindMode = 0
  ClaimChildren = true
  Context = -> Body008 [Binder006.]
  Fuse = false
  MakeFace = true
  Offset = 2
  OffsetFill = false
  OffsetIntersection = false
  OffsetJoinType = 0
  OffsetOpenResult = false
  PartialLoad = false
  Relative = false
  Support = -> [Array003]
  _Version = 2
FEATURE [Part::Compound] Compound010
  Links = -> [Sketch015,Part__Mirroring004]
FEATURE [Part::FeaturePython] Array003  label="basement_top_2d"  # Draft array (typed FeaturePython)
  AlwaysSyncPlacement = false
  Angle = 360
  ArrayType = 1
  Axis = (0,0,1)
  Base = -> Compound010
  Center = (0,0,0)
  Count = 3
  ExpandArray = false
  Fuse = false
  IntervalAxis = (0,0,0)
  IntervalX = (50,0,0)
  IntervalY = (0,50,0)
  IntervalZ = (0,0,50)
  NumberCircles = 3
  NumberPolar = 3
  NumberX = 2
  NumberY = 2
  NumberZ = 1
  PlacementList = 3 placements: [(0,0,0),(0,0,0),(0,0,0)]
  RadialDistance = 50
  ScaleList = (3) [(1,1,1),(1,1,1),(1,1,1)]
  Symmetry = 1
  TangentialDistance = 25
FEATURE [PartDesign::Pad] Pad001
  Direction = (0,0,1)
  Length = 18
  Length2 = 10
  Profile = -> Binder005
  Refine = true
  Suppressed = false
  Type = 0
FEATURE [PartDesign::Pad] Pad002
  Direction = (0,0,1)
  Length = 18
  Length2 = 10
  Profile = -> Binder003
  Suppressed = false
  Type = 0
FEATURE [PartDesign::Pad] Pad003
  Direction = (0,0,1)
  Length = 3
  Length2 = 10
  Profile = -> Binder006
  Suppressed = false
  Type = 0
FEATURE [PartDesign::Pad] Pad004
  Direction = (0,0,1)
  Length = 3
  Length2 = 10
  Profile = -> Binder004
  Suppressed = false
  Type = 0
FEATURE [PartDesign::SubShapeBinder] Binder007
  BindCopyOnChange = 0
  BindMode = 0
  ClaimChildren = true
  Fuse = false
  MakeFace = true
  OffsetFill = false
  OffsetIntersection = false
  OffsetJoinType = 0
  OffsetOpenResult = false
  PartialLoad = false
  Relative = false
  Support = -> [Compound011]
  _Version = 2
FEATURE [PartDesign::SubShapeBinder] Binder009  label="dropper_base"
  BindCopyOnChange = 0
  BindMode = 0
  ClaimChildren = true
  Fuse = false
  MakeFace = true
  OffsetFill = false
  OffsetIntersection = false
  OffsetJoinType = 0
  OffsetOpenResult = false
  PartialLoad = false
  Relative = true
  Support = -> [<external dropper.FCStd>#Sketch007]
  _Version = 2
  expr: Support = dropper#<<base>>._self
FEATURE [PartDesign::SubShapeBinder] Binder010  label="dropper_feed"
  BindCopyOnChange = 0
  BindMode = 0
  ClaimChildren = false
  Fuse = false
  MakeFace = true
  OffsetFill = false
  OffsetIntersection = false
  OffsetJoinType = 0
  OffsetOpenResult = false
  PartialLoad = false
  Relative = true
  Support = -> [<external dropper.FCStd>#Sketch008]
  _Version = 2
  expr: Support = dropper#<<feed>>._self
FEATURE [PartDesign::SubShapeBinder] Binder011  label="dropper_fix"
  BindCopyOnChange = 0
  BindMode = 0
  ClaimChildren = false
  Fuse = false
  MakeFace = true
  Offset = 0.5
  OffsetFill = false
  OffsetIntersection = false
  OffsetJoinType = 0
  OffsetOpenResult = false
  PartialLoad = false
  Relative = true
  Support = -> [<external dropper.FCStd>#Connect]
  _Version = 2
  expr: Support = dropper#<<fix>>._self
FEATURE [Part::FeaturePython] LinearArray002  # WARN: FeaturePython — macro-defined, semantics opaque (R4)
  Alignment = 0
  CellStart = A1
  Count = 2
  Dir = (1,0,0)
  DirIsDriven = true
  DistributionLaw = 0
  DrivenProperty = 1
  EndInclusive = true
  ExposePlacement = false
  GeneratorMode = 0
  MarkerShape = 1
  MarkerSize = 0
  NumElements = 2
  OrientMode = 1
  Placement = pos=(-32.5,0,0) rot=(0,0,1;0rad)
  Point = (0,0,0)
  PointIsDriven = true
  Reverse = false
  SpanEnd = 65
  SpanStart = 0
  Step = 65
  Type = lattice2LinearArray.LinearArray
  VSGVersion = 1
  Values = 0.0 | 65.0
  ValuesSource = 2
  isLattice = 1
  expr: .Placement.Base.x = -SpanEnd / 2
FEATURE [Part::FeaturePython] LinearArray003  # WARN: FeaturePython — macro-defined, semantics opaque (R4)
  Alignment = 0
  CellStart = A1
  Count = 2
  Dir = (1,0,0)
  DirIsDriven = true
  DistributionLaw = 0
  DrivenProperty = 1
  EndInclusive = true
  ExposePlacement = false
  GeneratorMode = 0
  MarkerShape = 1
  MarkerSize = 0
  NumElements = 2
  OrientMode = 1
  Placement = pos=(0,-75,0) rot=(0,0,1;1.5708rad)
  Point = (0,0,0)
  PointIsDriven = true
  Reverse = false
  SpanEnd = 150
  SpanStart = 0
  Step = 150
  Type = lattice2LinearArray.LinearArray
  VSGVersion = 1
  Values = 0.0 | 150.0
  ValuesSource = 2
  isLattice = 1
  expr: .Placement.Base.y = -SpanEnd / 2
FEATURE [Part::FeaturePython] LinearArray004  # WARN: FeaturePython — macro-defined, semantics opaque (R4)
  Alignment = 0
  CellStart = A1
  Count = 2
  Dir = (1,0,0)
  DirIsDriven = true
  DistributionLaw = 0
  DrivenProperty = 1
  EndInclusive = true
  ExposePlacement = false
  GeneratorMode = 0
  MarkerShape = 1
  MarkerSize = 0
  NumElements = 2
  OrientMode = 1
  Placement = pos=(-28.3,0,0) rot=(0,0,1;0rad)
  Point = (0,0,0)
  PointIsDriven = true
  Reverse = false
  SpanEnd = 56.6
  SpanStart = 0
  Step = 56.6
  Type = lattice2LinearArray.LinearArray
  VSGVersion = 1
  Values = 0.0 | 56.6
  ValuesSource = 2
  isLattice = 1
  expr: .Placement.Base.x = -SpanEnd / 2
  expr: SpanEnd = <<Properties>>.endface_width + dropper#<<base>>.Constraints.r * 2 + 4 mm
FEATURE [Part::FeaturePython] Populate002  label="Populate LinearArray004 with LinearArray003"  # WARN: FeaturePython — macro-defined, semantics opaque (R4)
  Copying = 0
  ExposePlacement = false
  MarkerShape = 1
  MarkerSize = 0
  NumElements = 4
  Object = -> LinearArray003
  OutputCompounding = 0
  PlacementsTo = -> LinearArray004
  Referencing = 0
  Type = lattice2PopulateCopies.LatticePopulateCopies
  isLattice = 1
FEATURE [Part::FeaturePython] Populate003  label="droppers placements"  # WARN: FeaturePython — macro-defined, semantics opaque (R4)
  Copying = 0
  ExposePlacement = false
  MarkerShape = 1
  MarkerSize = 0
  NumElements = 8
  Object = -> LinearArray002
  OutputCompounding = 0
  PlacementsTo = -> Populate002
  Referencing = 0
  Type = lattice2PopulateCopies.LatticePopulateCopies
  isLattice = 1
FEATURE [Part::FeaturePython] Populate004  label="populate dropper_fix"  # WARN: FeaturePython — macro-defined, semantics opaque (R4)
  Copying = 0
  ExposePlacement = false
  MarkerShape = 1
  MarkerSize = 0
  NumElements = 0
  Object = -> Binder011
  OutputCompounding = 1
  PlacementsTo = -> Populate003
  Referencing = 0
  Type = lattice2PopulateCopies.LatticePopulateCopies
  isLattice = 0
FEATURE [Part::FeaturePython] Populate005  label="Populate droppers placements with dropper_feed"  # WARN: FeaturePython — macro-defined, semantics opaque (R4)
  Copying = 0
  ExposePlacement = false
  MarkerShape = 1
  MarkerSize = 0
  NumElements = 0
  Object = -> Binder010
  OutputCompounding = 1
  PlacementsTo = -> Populate003
  Referencing = 0
  Type = lattice2PopulateCopies.LatticePopulateCopies
  isLattice = 0
FEATURE [Part::FeaturePython] Populate006  label="Populate droppers placements with dropper_base"  # WARN: FeaturePython — macro-defined, semantics opaque (R4)
  Copying = 0
  ExposePlacement = false
  MarkerShape = 1
  MarkerSize = 0
  NumElements = 0
  Object = -> Binder009
  OutputCompounding = 1
  PlacementsTo = -> Populate003
  Referencing = 0
  Type = lattice2PopulateCopies.LatticePopulateCopies
  isLattice = 0
FEATURE [Part::FeaturePython] Clone005  label="Populate droppers placements with dropper_base001"  # Draft clone (typed FeaturePython)
  AttacherType = Attacher::AttachEngine3D
  Fuse = false
  Objects = -> [Populate006]
  Placement = pos=(0,181.372,0) rot=(0,0,1;0rad)
  Scale = (1,1,1)
  expr: .Placement.Base.y = <<Properties>>.plane_middle
FEATURE [Sketcher::SketchObject] Sketch002  label="dropper_fix_sketch"
  ArcFitTolerance = 0
  ExternalGeometry = -> [Sketch,Clone005]
  FullyConstrained = true
  MakeInternals = false
  expr: Constraints[15] = composit_properties#<<Properties>>.thickness
  expr: Constraints[9] = 2 mm + <<dropper>>#<<base>>.Constraints.r * 2 + 2 mm
  sketch-geometry (8):
    g0: LineSegment StartX=42.1 StartY=292.046 StartZ=0 EndX=42.1 EndY=27.7705 EndZ=0
    g1: LineSegment StartX=0 StartY=348.872 StartZ=0 EndX=14.5 EndY=348.872 EndZ=0
    g2: LineSegment StartX=14.5 StartY=348.872 StartZ=0 EndX=42.1 EndY=292.046 EndZ=0
    g3: LineSegment StartX=0 StartY=0 StartZ=0 EndX=17 EndY=9.81495 EndZ=0
    g4: LineSegment StartX=17 StartY=9.81495 StartZ=0 EndX=15.5 EndY=12.413 EndZ=0
    g5: LineSegment StartX=15.5 StartY=12.413 StartZ=0 EndX=42.1 EndY=27.7705 EndZ=0
    g6: LineSegment [constr] StartX=28.3 StartY=288.872 StartZ=0 EndX=40.7133 EndY=294.901 EndZ=0
    g7: LineSegment [constr] StartX=28.3 StartY=288.872 StartZ=0 EndX=42.1 EndY=288.872 EndZ=0
  constraints (24):
    c: PointOnObject(g1,g-2)
    c: Coincident(g2,g0)
    c: Vertical(g0)
    c: Coincident(g3,g-1)
    c: Coincident(g5,g0)
    c: Coincident(g1,g2)
    c: Horizontal(g1)
    c: PointOnObject(g1,g-3)
    c: DistanceY(g1,g-3) = 3
    c: DistanceX(g-3,g5) = 27.6
    c: Coincident(g3,g4)
    c: PointOnObject(g-3,g3)
    c: Coincident(g4,g5)
    c: Perpendicular(g4,g3)
    c: Perpendicular(g5,g4)
    c: Distance(g4) = 3
    c: DistanceX(g-3,g4) = 1
    c: PointOnObject(g6,g2)
    c: PointOnObject(g7,g0)
    c: Perpendicular(g0,g7)
    c: Perpendicular(g2,g6)
    c: Equal(g7,g6)
    c: Coincident(g7,g-4)
    c: Coincident(g7,g6)
FEATURE [Part::Mirroring] Part__Mirroring005  label="dropper_fix_sketch (Mirror #6)"
  Base = (0,0,0)
  Normal = (1,0,0)
  Source = -> Sketch002
FEATURE [Part::Compound] Compound011  label="dropper_fix_base"
  Links = -> [Sketch002,Part__Mirroring005]
FEATURE [PartDesign::Pad] Pad005
  Direction = (0,0,1)
  Length = 3
  Length2 = 10
  Profile = -> Binder007
  Suppressed = false
  Type = 0
FEATURE [Sketcher::SketchObject] Sketch016
  ArcFitTolerance = 0
  ExternalGeometry = -> [Sketch002]
  FullyConstrained = true
  MakeInternals = false
  expr: Constraints[21] = composit_properties#<<Properties>>.thickness
  sketch-geometry (8):
    g0: LineSegment StartX=1.5 StartY=0.866025 StartZ=0 EndX=45.1 EndY=26.0385 EndZ=0
    g1: LineSegment StartX=45.1 StartY=26.0385 StartZ=0 EndX=45.1 EndY=292.736 EndZ=0
    g2: LineSegment StartX=45.1 StartY=292.736 StartZ=0 EndX=16.378 EndY=351.872 EndZ=0
    g3: LineSegment StartX=16.378 StartY=351.872 StartZ=0 EndX=0 EndY=351.872 EndZ=0
    g4: LineSegment [constr] StartX=14.5 StartY=351.872 StartZ=0 EndX=14.5 EndY=348.872 EndZ=0
    g5: LineSegment [constr] StartX=14.5 StartY=348.872 StartZ=0 EndX=17.1985 EndY=350.182 EndZ=0
    g6: LineSegment [constr] StartX=42.1 StartY=27.7705 StartZ=0 EndX=43.6 EndY=25.1725 EndZ=0
    g7: LineSegment [constr] StartX=42.1 StartY=27.7705 StartZ=0 EndX=45.1 EndY=27.7705 EndZ=0
  constraints (25):
    c: Coincident(g0,g1)
    c: Vertical(g1)
    c: Coincident(g1,g2)
    c: Coincident(g2,g3)
    c: PointOnObject(g3,g-2)
    c: Horizontal(g3)
    c: PointOnObject(g4,g3)
    c: Coincident(g4,g-4)
    c: Vertical(g4)
    c: Coincident(g4,g5)
    c: PointOnObject(g5,g2)
    c: Coincident(g-3,g6)
    c: PointOnObject(g6,g0)
    c: Coincident(g6,g7)
    c: PointOnObject(g7,g1)
    c: Horizontal(g7)
    c: Equal(g5,g4)
    c: Perpendicular(g5,g2)
    c: Perpendicular(g-4,g5)
    c: Perpendicular(g0,g6)
    c: Perpendicular(g-3,g6)
    c: DistanceY(g4,g4) = 3
    c: DistanceX(g0) = 1.5
    c: Equal(g5,g7)
    c: Equal(g7,g6)
FEATURE [Part::Mirroring] Part__Mirroring006  label="Sketch016 (Mirror #7)"
  Base = (0,0,0)
  Normal = (1,0,0)
  Source = -> Sketch016
FEATURE [Sketcher::SketchObject] Sketch017
  ArcFitTolerance = 0
  ExternalGeometry = -> [Sketch016]
  FullyConstrained = true
  MakeInternals = false
  sketch-geometry (9):
    g0: LineSegment StartX=45.1 StartY=26.0385 StartZ=0 EndX=-7.1e-15 EndY=52.077 EndZ=0
    g1: LineSegment StartX=45.1 StartY=292.736 StartZ=0 EndX=0 EndY=282.363 EndZ=0
    g2: LineSegment StartX=16.378 StartY=351.872 StartZ=0 EndX=0 EndY=325.709 EndZ=0
    g3: LineSegment [constr] StartX=0 StartY=351.872 StartZ=0 EndX=0 EndY=325.709 EndZ=0
    g4: LineSegment [constr] StartX=0 StartY=325.709 StartZ=0 EndX=23.5334 EndY=337.139 EndZ=0
    g5: LineSegment [constr] StartX=40.5682 StartY=302.066 StartZ=0 EndX=0 EndY=282.363 EndZ=0
    g6: LineSegment [constr] StartX=0 StartY=282.363 StartZ=0 EndX=45.1 EndY=282.363 EndZ=0
    g7: LineSegment [constr] StartX=22.55 StartY=13.0192 StartZ=0 EndX=-7.1e-15 EndY=52.077 EndZ=0
    g8: LineSegment [constr] StartX=-7.1e-15 StartY=52.077 StartZ=0 EndX=45.1 EndY=52.077 EndZ=0
  constraints (27):
    c: Coincident(g0,g-3)
    c: PointOnObject(g0,g-2)
    c: Coincident(g1,g-4)
    c: PointOnObject(g1,g-2)
    c: PointOnObject(g2,g-2)
    c: Coincident(g2,g-4)
    c: PointOnObject(g3,g-2)
    c: Coincident(g3,g2)
    c: Coincident(g3,g4)
    c: PointOnObject(g4,g-4)
    c: PointOnObject(g5,g-4)
    c: Coincident(g5,g1)
    c: Coincident(g5,g6)
    c: Horizontal(g6)
    c: PointOnObject(g7,g-3)
    c: Coincident(g7,g0)
    c: Coincident(g7,g8)
    c: Horizontal(g8)
    c: Vertical(g0,g8)
    c: Vertical(g8,g6)
    c: Horizontal(g3,g2)
    c: Perpendicular(g-4,g4)
    c: Perpendicular(g-4,g5)
    c: Equal(g6,g5)
    c: Equal(g4,g3)
    c: Perpendicular(g-3,g7)
    c: Equal(g7,g8)
FEATURE [Sketcher::SketchObject] Sketch018
  ArcFitTolerance = 0
  ExternalGeometry = -> [Sketch017]
  FullyConstrained = true
  MakeInternals = false
  sketch-geometry (30):
    g0: LineSegment StartX=0.05 StartY=0 StartZ=0 EndX=0.05 EndY=51.9904 EndZ=0
    g1: LineSegment StartX=0.05 StartY=51.9904 StartZ=0 EndX=44.65 EndY=26.2406 EndZ=0
    g2: LineSegment StartX=44.65 StartY=26.2406 StartZ=0 EndX=44.85 EndY=25.8942 EndZ=0
    g3: LineSegment StartX=44.85 StartY=25.8942 StartZ=0 EndX=45.1 EndY=26.0385 EndZ=0
    g4: LineSegment StartX=45.1 StartY=26.0385 StartZ=0 EndX=45.1 EndY=26.3272 EndZ=0
    g5: LineSegment StartX=45.1 StartY=26.3272 StartZ=0 EndX=44.7 EndY=26.3272 EndZ=0
    g6: LineSegment StartX=44.7 StartY=26.3272 StartZ=0 EndX=0.05 EndY=52.1059 EndZ=0
    g7: LineSegment StartX=0.05 StartY=52.1059 StartZ=0 EndX=0.05 EndY=282.323 EndZ=0
    g8: LineSegment StartX=0.05 StartY=282.323 StartZ=0 EndX=44.7 EndY=292.592 EndZ=0
    g9: LineSegment StartX=44.7 StartY=292.592 StartZ=0 EndX=45.1 EndY=292.592 EndZ=0
    g10: LineSegment StartX=45.1 StartY=292.592 StartZ=0 EndX=45.1 EndY=292.736 EndZ=0
    g11: LineSegment StartX=45.1 StartY=292.736 StartZ=0 EndX=45.0374 EndY=292.864 EndZ=0
    g12: LineSegment StartX=45.0374 StartY=292.864 StartZ=0 EndX=44.6776 EndY=292.69 EndZ=0
    g13: LineSegment StartX=44.6776 StartY=292.69 StartZ=0 EndX=0.05 EndY=282.425 EndZ=0
    g14: LineSegment StartX=0.05 StartY=282.425 StartZ=0 EndX=0.05 EndY=325.695 EndZ=0
    g15: LineSegment StartX=0.05 StartY=325.695 StartZ=0 EndX=16.1534 EndY=351.419 EndZ=0
    g16: LineSegment StartX=16.1534 StartY=351.419 StartZ=0 EndX=16.5132 EndY=351.593 EndZ=0
    g17: LineSegment StartX=16.5132 StartY=351.593 StartZ=0 EndX=16.378 EndY=351.872 EndZ=0
    g18: LineSegment StartX=16.378 StartY=351.872 StartZ=0 EndX=16.0687 EndY=351.872 EndZ=0
    g19: LineSegment StartX=16.0687 StartY=351.872 StartZ=0 EndX=16.0687 EndY=351.472 EndZ=0
    g20: LineSegment StartX=16.0687 StartY=351.472 StartZ=0 EndX=0 EndY=325.803 EndZ=0
    g21: LineSegment StartX=0.05 StartY=0 StartZ=0 EndX=0 EndY=0 EndZ=0
    g22: LineSegment [constr] StartX=0 StartY=0 StartZ=0 EndX=45.1 EndY=26.0385 EndZ=0
    g23: LineSegment [constr] StartX=45.1 StartY=26.0385 StartZ=0 EndX=45.1 EndY=292.736 EndZ=0
    g24: LineSegment [constr] StartX=45.1 StartY=292.736 StartZ=0 EndX=16.378 EndY=351.872 EndZ=0
    g25: LineSegment [constr] StartX=16.378 StartY=351.872 StartZ=0 EndX=0 EndY=351.872 EndZ=0
    g26: LineSegment [constr] StartX=-0.05 StartY=51.9904 StartZ=0 EndX=0.05 EndY=51.9904 EndZ=0
    g27: LineSegment [constr] StartX=0.05 StartY=51.9904 StartZ=0 EndX=0.1 EndY=52.077 EndZ=0
    g28: LineSegment [constr] StartX=0.05 StartY=282.425 StartZ=0 EndX=0.0724148 EndY=282.328 EndZ=0
    g29: LineSegment [constr] StartX=0.05 StartY=325.695 StartZ=0 EndX=-0.0347611 EndY=325.748 EndZ=0
  constraints (80):
    c: PointOnObject(g0,g-1)
    c: Vertical(g0)
    c: Coincident(g0,g1)
    c: Coincident(g1,g2)
    c: Coincident(g2,g3)
    c: Coincident(g3,g-5)
    c: Coincident(g3,g4)
    c: Vertical(g4)
    c: Coincident(g4,g5)
    c: Coincident(g5,g6)
    c: Coincident(g6,g7)
    c: Vertical(g7)
    c: Coincident(g7,g8)
    c: Coincident(g8,g9)
    c: Coincident(g9,g10)
    c: Coincident(g10,g-4)
    c: Vertical(g10)
    c: Coincident(g10,g11)
    c: Coincident(g11,g12)
    c: Coincident(g12,g13)
    c: Coincident(g13,g14)
    c: Vertical(g14)
    c: Coincident(g14,g15)
    c: Coincident(g15,g16)
    c: Coincident(g16,g17)
    c: Coincident(g17,g-3)
    c: Coincident(g17,g18)
    c: Horizontal(g18)
    c: Coincident(g18,g19)
    c: Vertical(g19)
    c: Coincident(g19,g20)
    c: PointOnObject(g20,g-2)
    c: Equal(g19,g16)
    c: Equal(g16,g12)
    c: Equal(g12,g9)
    c: Equal(g9,g5)
    c: Equal(g5,g2)
    c: Coincident(g21,g0)
    c: Coincident(g21,g-1)
    c: Coincident(g21,g22)
    c: Coincident(g22,g3)
    c: Coincident(g3,g23)
    c: Coincident(g23,g10)
    c: Coincident(g23,g24)
    c: Coincident(g24,g17)
    c: Coincident(g24,g25)
    c: PointOnObject(g25,g-2)
    c: Horizontal(g25)
    c: PointOnObject(g11,g24)
    c: PointOnObject(g2,g22)
    c: DistanceY(g19,g19) = 0.4
    c: Parallel(g15,g-3)
    c: Parallel(g-3,g20)
    c: Parallel(g13,g-4)
    c: Parallel(g-4,g8)
    c: Parallel(g6,g-5)
    c: Parallel(g-5,g1)
    c: Coincident(g26,g0)
    c: Coincident(g26,g27)
    c: PointOnObject(g27,g6)
    c: Symmetric(g26,g0,g-2)
    c: Vertical(g0,g6)
    c: Vertical(g7,g13)
    c: Coincident(g28,g13)
    c: PointOnObject(g28,g8)
    c: Coincident(g29,g14)
    c: PointOnObject(g29,g20)
    c: Equal(g26,g27)
    c: PointOnObject(g16,g24)
    c: Symmetric(g14,g29,g-3)
    c: DistanceX(g26,g26) = 0.1
    c: Perpendicular(g3,g2)
    c: Perpendicular(g4,g5)
    c: Equal(g27,g28)
    c: Equal(g29,g28)
    c: Perpendicular(g10,g9)
    c: Perpendicular(g11,g12)
    c: Symmetric(g0,g27,g-5)
    c: Perpendicular(g17,g16)
    c: Symmetric(g28,g13,g-4)
FEATURE [Part::Compound] Compound012
  Links = -> [Sketch016,Part__Mirroring006]
FEATURE [Part::Mirroring] Part__Mirroring007  label="Sketch018 (Mirror #8)"
  Base = (0,0,0)
  Normal = (1,0,0)
  Source = -> Sketch018
FEATURE [Part::Compound] Compound013
  Links = -> [Sketch018,Part__Mirroring007]
FEATURE [PartDesign::SubShapeBinder] Binder012
  BindCopyOnChange = 0
  BindMode = 0
  ClaimChildren = true
  Fuse = false
  MakeFace = true
  OffsetFill = false
  OffsetIntersection = false
  OffsetJoinType = 0
  OffsetOpenResult = false
  PartialLoad = false
  Placement = pos=(0,0,40) rot=(0,0,1;0rad)
  Relative = false
  Support = -> [Compound012]
  _Version = 2
FEATURE [PartDesign::SubShapeBinder] Binder013
  BindCopyOnChange = 0
  BindMode = 0
  ClaimChildren = true
  Fuse = false
  MakeFace = true
  OffsetFill = false
  OffsetIntersection = false
  OffsetJoinType = 0
  OffsetOpenResult = false
  PartialLoad = false
  Placement = pos=(0,0,40) rot=(0,0,1;0rad)
  Relative = false
  Support = -> [Compound013]
  _Version = 2
FEATURE [PartDesign::FeaturePython] BaseBend007  # WARN: FeaturePython — macro-defined, semantics opaque (R4)
  BendSide = 1
  BendSketch = -> Binder012
  MidPlane = false
  Reverse = true
  Suppressed = false
  length = 100
  radius = 0.1
  thickness = 0.3
  expr: radius = composit_properties#<<Properties>>.bend_r
  expr: thickness = composit_properties#<<Properties>>.al_thickness
FEATURE [PartDesign::FeaturePython] Bend001  # WARN: FeaturePython — macro-defined, semantics opaque (R4)
  AutoMiter = false
  BaseFeature = -> BaseBend007
  BendType = 0
  LengthList = [47]
  LengthSpec = 1
  NonperforationMaxLength = 5
  Perforate = false
  PerforationAngle = 0
  PerforationInitialLength = 5
  PerforationMaxLength = 5
  ReliefFactor = 0.7
  Suppressed = false
  UseReliefFactor = false
  angle = 90
  baseObject = -> BaseBend007 [Edge14,Edge30,Edge46,Edge62,Edge70,Edge86,Edge102,Edge116]
  bendAList = [90]
  extend1 = 0
  extend2 = 0
  gap1 = 0
  gap2 = 0
  invert = false
  kfactor = 0.5
  length = 47
  maxExtendDist = 5
  minGap = 0.1
  minReliefGap = 1
  miterangle1 = 0
  miterangle2 = 0
  offset = 0
  radius = 0.1
  reliefType = 0
  reliefd = 1
  reliefw = 0.8
  sketchflip = false
  sketchinvert = false
  unfold = false
  expr: radius = BaseBend007.radius
FEATURE [PartDesign::Pocket] Pocket002
  BaseFeature = -> Bend001
  Direction = (0,0,-1)
  Length = 5
  Length2 = 5
  Profile = -> Binder013 [Face1]
  Refine = true
  Reversed = true
  Suppressed = false
  Type = 1
FEATURE [Sketcher::SketchObject] Sketch019
  ArcFitTolerance = 0
  ExternalGeometry = -> [Sketch017]
  FullyConstrained = true
  MakeInternals = false
  expr: Constraints[12] = <<Properties>>.rivet_d
  sketch-geometry (13):
    g0: Circle [constr] CenterX=0 CenterY=325.709 CenterZ=0 NormalX=0 NormalY=0 NormalZ=1 AngleXU=0 Radius=1.7
    g1: Circle CenterX=0 CenterY=282.363 CenterZ=0 NormalX=0 NormalY=0 NormalZ=1 AngleXU=0 Radius=2
    g2: Circle CenterX=-22.55 CenterY=277.288 CenterZ=0 NormalX=0 NormalY=0 NormalZ=1 AngleXU=0 Radius=1.7
    g3: Circle CenterX=22.55 CenterY=277.288 CenterZ=0 NormalX=0 NormalY=0 NormalZ=1 AngleXU=0 Radius=1.7
    g4: Circle CenterX=0 CenterY=52.077 CenterZ=0 NormalX=0 NormalY=0 NormalZ=1 AngleXU=0 Radius=2
    g5: Circle CenterX=20 CenterY=52.077 CenterZ=0 NormalX=0 NormalY=0 NormalZ=1 AngleXU=0 Radius=1.7
    g6: Circle CenterX=10 CenterY=34.7565 CenterZ=0 NormalX=0 NormalY=0 NormalZ=1 AngleXU=0 Radius=1.7
    g7: Circle CenterX=-10 CenterY=34.7565 CenterZ=0 NormalX=0 NormalY=0 NormalZ=1 AngleXU=0 Radius=1.7
    g8: Circle CenterX=-20 CenterY=52.077 CenterZ=0 NormalX=0 NormalY=0 NormalZ=1 AngleXU=0 Radius=1.7
    g9: GeomPoint [constr] X=22.55 Y=287.549 Z=0
    g10: LineSegment [constr] StartX=0 StartY=34.7565 StartZ=0 EndX=10 EndY=34.7565 EndZ=0
    g11: LineSegment [constr] StartX=10 StartY=34.7565 StartZ=0 EndX=15 EndY=43.4167 EndZ=0
    g12: Circle CenterX=0 CenterY=325.709 CenterZ=0 NormalX=0 NormalY=0 NormalZ=1 AngleXU=0 Radius=2
  constraints (29):
    c: Coincident(g0,g-4)
    c: Coincident(g1,g-3)
    c: Coincident(g4,g-5)
    c: Symmetric(g8,g5,g-2)
    c: Symmetric(g7,g6,g-2)
    c: Symmetric(g3,g2,g-2)
    c: Equal(g0,g3)
    c: Equal(g0,g2)
    c: Equal(g0,g8)
    c: Equal(g0,g5)
    c: Equal(g0,g7)
    c: Equal(g0,g6)
    c: Diameter(g0) = 3.4
    c: Symmetric(g1,g-3,g9)
    c: Symmetric(g6,g5,g-5)
    c: PointOnObject(g10,g-2)
    c: Coincident(g10,g6)
    c: Horizontal(g10)
    c: Coincident(g10,g11)
    c: PointOnObject(g11,g-5)
    c: Perpendicular(g-5,g11)
    c: Equal(g11,g10)
    c: DistanceX(g10,g10) = 10
    c: Vertical(g3,g9)
    c: Distance(g3,g-3) = 10
    c: Coincident(g12,g0)
    c: Diameter(g12) = 4
    c: Equal(g4,g1)
    c: Equal(g1,g12)
FEATURE [PartDesign::SubShapeBinder] Binder014
  BindCopyOnChange = 0
  BindMode = 0
  ClaimChildren = true
  Context = -> Link012 [Binder014.]
  Fuse = false
  MakeFace = true
  OffsetFill = false
  OffsetIntersection = false
  OffsetJoinType = 0
  OffsetOpenResult = false
  PartialLoad = false
  Relative = true
  Support = -> [Sketch019]
  _Version = 2
FEATURE [Sketcher::SketchObject] Sketch020
  ArcFitTolerance = 0
  AttachmentSupport = -> [XY_Plane005]
  FullyConstrained = true
  MakeInternals = false
  MapMode = 5
  expr: Constraints[10] = composit_properties#<<Properties>>.bend_r + composit_properties#<<Properties>>.al_thickness
  sketch-geometry (5):
    g0: ArcOfCircle CenterX=0 CenterY=0.46188 CenterZ=0 NormalX=0 NormalY=0 NormalZ=1 AngleXU=0 Radius=5 StartAngle=0.523599 EndAngle=2.61799
    g1: LineSegment StartX=0 StartY=0 StartZ=0 EndX=4.53013 EndY=2.61547 EndZ=0
    g2: LineSegment StartX=4.53013 StartY=2.61547 StartZ=0 EndX=4.33013 EndY=2.96188 EndZ=0
    g3: LineSegment StartX=0 StartY=0 StartZ=0 EndX=-4.53013 EndY=2.61547 EndZ=0
    g4: LineSegment StartX=-4.53013 StartY=2.61547 StartZ=0 EndX=-4.33013 EndY=2.96188 EndZ=0
  constraints (13):
    c: PointOnObject(g0,g-2)
    c: Coincident(g1,g-1)
    c: Coincident(g2,g1)
    c: Coincident(g3,g1)
    c: Coincident(g4,g3)
    c: Perpendicular(g3,g4)
    c: Perpendicular(g1,g2)
    c: Tangent(g2,g0) = -1.5708
    c: Tangent(g4,g0) = 1.5708
    c: Equal(g4,g2)
    c: Distance(g2) = 0.4
    c: Diameter(g0) = 10
    c: Angle(g1,g3) = 2.0944
FEATURE [PartDesign::SubShapeBinder] Binder015
  BindCopyOnChange = 0
  BindMode = 0
  ClaimChildren = false
  Context = -> Link012 [Binder015.]
  Fuse = false
  MakeFace = true
  OffsetFill = false
  OffsetIntersection = false
  OffsetJoinType = 0
  OffsetOpenResult = false
  PartialLoad = false
  Relative = true
  Support = -> [Sketch002]
  _Version = 2
  expr: Support = <<dropper_fix_sketch>>._self
FEATURE [Sketcher::SketchObject] Sketch022  label="cap_outer_shape"
  ArcFitTolerance = 0
  AttachmentSupport = -> [YZ_Plane005]
  ExternalGeometry = -> [Binder012]
  FullyConstrained = true
  MakeInternals = false
  MapMode = 5
  Placement = pos=(0,0,0) rot=(0.57735,0.57735,0.57735;2.0944rad)
  expr: Constraints[11] = composit_properties#<<Properties>>.bend_r + composit_properties#<<Properties>>.al_thickness
  expr: Constraints[9] = composit_properties#<<Properties>>.bend_r + composit_properties#<<Properties>>.al_thickness + 0.01 mm
  sketch-geometry (5):
    g0: LineSegment StartX=351.882 StartY=40.41 StartZ=0 EndX=0 EndY=40.41 EndZ=0
    g1: LineSegment StartX=0 StartY=40.41 StartZ=0 EndX=0 EndY=0 EndZ=0
    g2: LineSegment StartX=0 StartY=0 StartZ=0 EndX=351.882 EndY=0 EndZ=0
    g3: LineSegment StartX=351.882 StartY=0 StartZ=0 EndX=351.882 EndY=40.41 EndZ=0
    g4: GeomPoint [constr] X=351.872 Y=40.4 Z=0
  constraints (14):
    c: Coincident(g0,g1)
    c: Coincident(g1,g2)
    c: Coincident(g2,g3)
    c: Coincident(g3,g0)
    c: Horizontal(g0)
    c: Horizontal(g2)
    c: Vertical(g1)
    c: Vertical(g3)
    c: Coincident(g1,g-1)
    c: DistanceY(g-3,g0) = 0.41
    c: DistanceX(g-3,g0) = 0.01
    c: DistanceY(g-3,g4) = 0.4
    c: Vertical(g-3,g4)
    c: DistanceY(g4) = 40.4  'height'
FEATURE [Part::FeaturePython] WireFilter002  # WARN: FeaturePython — macro-defined, semantics opaque (R4)
  AttacherType = Attacher::AttachEngine3D
  ClaimChildren = true
  ColorKeyCount = 8
  Colorize = true
  FaceMaker = 5
  FixNormal = false
  FollowSource = true
  InvertedFaceScale = 5
  MaxWires = 25
  Normal = (1,0,0)
  OffsetFill = false
  OffsetIntersection = false
  OffsetJoin = 0
  OffsetOpenResult = false
  Scale = (1,1,1)
  SelectEdges = false
  Source = -> Sketch022
  UniformScale = 1
  UseDefault = false
  UseSelected = true
  UseSelectedEdges = false
  Version = 0.2022.02.09
  WireOrder = [1]
FEATURE [PartDesign::SubShapeBinder] Binder016
  BindCopyOnChange = 0
  BindMode = 0
  ClaimChildren = true
  Fuse = false
  MakeFace = false
  OffsetFill = false
  OffsetIntersection = false
  OffsetJoinType = 0
  OffsetOpenResult = false
  PartialLoad = false
  Relative = false
  Support = -> [Sketch019]
  _Version = 2
FEATURE [PartDesign::SubShapeBinder] Binder018
  BindCopyOnChange = 0
  BindMode = 0
  ClaimChildren = false
  Fuse = false
  MakeFace = true
  OffsetFill = false
  OffsetIntersection = false
  OffsetJoinType = 0
  OffsetOpenResult = false
  PartialLoad = false
  Relative = false
  Support = -> [Body002[BaseBend007.Binder012.Compound012.Part__Mirroring006.Sketch016.]]
  _Version = 2
FEATURE [PartDesign::SubShapeBinder] Binder019
  BindCopyOnChange = 0
  BindMode = 0
  ClaimChildren = false
  Fuse = false
  MakeFace = false
  OffsetFill = false
  OffsetIntersection = false
  OffsetJoinType = 0
  OffsetOpenResult = false
  PartialLoad = false
  Relative = false
  Support = -> [Sketch019]
  _Version = 2
FEATURE [PartDesign::SubShapeBinder] Binder020
  BindCopyOnChange = 0
  BindMode = 0
  ClaimChildren = false
  Context = -> Link015 [Binder020.]
  Fuse = false
  MakeFace = true
  OffsetFill = false
  OffsetIntersection = false
  OffsetJoinType = 0
  OffsetOpenResult = false
  PartialLoad = false
  Relative = true
  Support = -> [Body002[BaseBend007.Binder012.Compound012.Part__Mirroring006.Sketch016.]]
  _Version = 2
FEATURE [Sketcher::SketchObject] Sketch023
  ArcFitTolerance = 0
  AttachmentSupport = -> [XY_Plane006]
  ExternalGeometry = -> [Binder020]
  FullyConstrained = true
  MakeInternals = false
  MapMode = 5
  expr: Constraints[9] = composit_properties#<<Properties>>.thickness + composit_properties#<<Properties>>.bend_r + composit_properties#<<Properties>>.al_thickness
  sketch-geometry (5):
    g0: LineSegment StartX=41.7 StartY=29.0385 StartZ=0 EndX=-41.7 EndY=29.0385 EndZ=0
    g1: LineSegment StartX=-41.7 StartY=29.0385 StartZ=0 EndX=-41.7 EndY=58.0385 EndZ=0
    g2: LineSegment StartX=-41.7 StartY=58.0385 StartZ=0 EndX=41.7 EndY=58.0385 EndZ=0
    g3: LineSegment StartX=41.7 StartY=58.0385 StartZ=0 EndX=41.7 EndY=29.0385 EndZ=0
    g4: GeomPoint [constr] X=0 Y=43.5385 Z=0
  constraints (13):
    c: Coincident(g0,g1)
    c: Coincident(g1,g2)
    c: Coincident(g2,g3)
    c: Coincident(g3,g0)
    c: Horizontal(g0)
    c: Horizontal(g2)
    c: Vertical(g1)
    c: Vertical(g3)
    c: DistanceY(g-3,g0) = 3
    c: DistanceX(g0,g-3) = 3.4
    c: PointOnObject(g4,g-2)
    c: Symmetric(g2,g0,g4)
    c: DistanceY(g3,g3) = 29
FEATURE [PartDesign::Pad] Pad007
  Direction = (0,0,1)
  Length = 0.3
  Length2 = 10
  Profile = -> Sketch023
  ReferenceAxis = -> Sketch023 [N_Axis]
  Suppressed = false
  Type = 0
  expr: Length = composit_properties#<<Properties>>.al_thickness
FEATURE [PartDesign::FeaturePython] Bend002  label="cap_inner1_bend"  # WARN: FeaturePython — macro-defined, semantics opaque (R4)
  AutoMiter = true
  BaseFeature = -> Pad007
  BendType = 0
  LengthList = [31]
  LengthSpec = 0
  NonperforationMaxLength = 5
  Perforate = false
  PerforationAngle = 0
  PerforationInitialLength = 5
  PerforationMaxLength = 5
  ReliefFactor = 0.7
  Suppressed = false
  UseReliefFactor = false
  angle = 90
  baseObject = -> Pad007 [Edge12,Edge7]
  bendAList = [90]
  extend1 = 0
  extend2 = 0
  gap1 = 0
  gap2 = 0
  invert = false
  kfactor = 0.5
  length = 31
  maxExtendDist = 5
  minGap = 0.1
  minReliefGap = 1
  miterangle1 = 0
  miterangle2 = 0
  offset = 0
  radius = 0.1
  reliefType = 0
  reliefd = 1
  reliefw = 0.8
  sketchflip = false
  sketchinvert = false
  unfold = false
  expr: length = <<cap_outer_shape>>.Constraints.height - composit_properties#<<Properties>>.thickness - composit_properties#<<Properties>>.al_thickness - composit_properties#<<Properties>>.bend_r - 6 mm
  expr: radius = BaseBend007.radius
FEATURE [Sketcher::SketchObject] Sketch024
  ArcFitTolerance = 0
  AttachmentSupport = -> [XY_Plane023]
  ExternalGeometry = -> [Binder019,Binder018]
  FullyConstrained = true
  MakeInternals = false
  MapMode = 5
  expr: Constraints[10] = composit_properties#<<Properties>>.thickness + composit_properties#<<Properties>>.al_thickness + composit_properties#<<Properties>>.bend_r
  sketch-geometry (5):
    g0: LineSegment StartX=-41.7 StartY=272.288 StartZ=0 EndX=-41.7 EndY=289.736 EndZ=0
    g1: LineSegment StartX=-41.7 StartY=289.736 StartZ=0 EndX=41.7 EndY=289.736 EndZ=0
    g2: LineSegment StartX=41.7 StartY=289.736 StartZ=0 EndX=41.7 EndY=272.288 EndZ=0
    g3: LineSegment StartX=41.7 StartY=272.288 StartZ=0 EndX=-41.7 EndY=272.288 EndZ=0
    g4: GeomPoint [constr] X=0 Y=281.012 Z=0
  constraints (13):
    c: Coincident(g0,g1)
    c: Coincident(g1,g2)
    c: Coincident(g2,g3)
    c: Coincident(g3,g0)
    c: Horizontal(g1)
    c: Horizontal(g3)
    c: Vertical(g0)
    c: Vertical(g2)
    c: Symmetric(g1,g0,g4)
    c: PointOnObject(g4,g-2)
    c: DistanceX(g1,g-4) = 3.4
    c: DistanceY(g2,g-3) = 5
    c: DistanceY(g1,g-4) = 3
FEATURE [PartDesign::FeaturePython] BaseBend008  # WARN: FeaturePython — macro-defined, semantics opaque (R4)
  BendSide = 0
  BendSketch = -> Sketch024
  MidPlane = false
  Reverse = false
  Suppressed = false
  length = 100
  radius = 0.1
  thickness = 0.3
  expr: radius = composit_properties#<<Properties>>.bend_r
  expr: thickness = composit_properties#<<Properties>>.al_thickness
FEATURE [PartDesign::Hole] Hole001
  BaseFeature = -> Bend002
  CustomThreadClearance = 0
  Depth = 25
  DepthType = 0
  Diameter = 3.4
  DrillForDepth = false
  DrillPoint = 1
  DrillPointAngle = 118
  HoleCutCountersinkAngle = 90
  HoleCutCustomValues = false
  HoleCutDepth = 0
  HoleCutDiameter = 6.1
  HoleCutType = 0
  ModelThread = false
  Profile = -> Binder016
  Reversed = true
  Suppressed = false
  Tapered = false
  TaperedAngle = 90
  ThreadClass = 0
  ThreadDepth = 25
  ThreadDepthType = 0
  ThreadDirection = 0
  ThreadFit = 0
  ThreadSize = 0
  ThreadType = 0
  Threaded = false
  UseCustomThreadClearance = false
  expr: Diameter = <<Properties>>.rivet_d
FEATURE [PartDesign::Body] Body003  label="cap_inner1_material_0.30ansi"
  AllowCompound = false
  Group = -> [Sketch023,Binder016,Binder020,Pad007,Bend002,Hole001]
  Origin = -> Origin006
  Tip = -> Hole001
FEATURE [Sketcher::SketchObject] Sketch025
  ArcFitTolerance = 0
  AttachmentSupport = -> [XY_Plane007]
  FullyConstrained = true
  MakeInternals = false
  MapMode = 5
FEATURE [Sketcher::SketchObject] Sketch026
  ArcFitTolerance = 0
  ExternalGeometry = -> [Sketch002]
  FullyConstrained = true
  MakeInternals = false
  expr: Constraints[38] = composit_properties#<<Properties>>.thickness
  sketch-geometry (16):
    g0: LineSegment [constr] StartX=42.1 StartY=27.7705 StartZ=0 EndX=42.1 EndY=292.046 EndZ=0
    g1: LineSegment [constr] StartX=14.5 StartY=348.872 StartZ=0 EndX=0 EndY=348.872 EndZ=0
    g2: LineSegment StartX=17 StartY=9.81495 StartZ=0 EndX=15.5 EndY=12.413 EndZ=0
    g3: ArcOfCircle CenterX=0 CenterY=5.53356 CenterZ=0 NormalX=0 NormalY=0 NormalZ=1 AngleXU=0 Radius=4.79221 StartAngle=4.71239 EndAngle=5.23599
    g4: LineSegment StartX=0 StartY=0 StartZ=0 EndX=2.39612 EndY=1.3834 EndZ=0
    g5: ArcOfCircle CenterX=16.8856 CenterY=13.213 CenterZ=0 NormalX=0 NormalY=0 NormalZ=1 AngleXU=0 Radius=1.6 StartAngle=0.523599 EndAngle=3.66519
    g6: LineSegment StartX=17 StartY=9.81495 StartZ=0 EndX=18.2713 EndY=14.013 EndZ=0
    g7: ArcOfCircle CenterX=37.3078 CenterY=30.5373 CenterZ=0 NormalX=0 NormalY=0 NormalZ=1 AngleXU=0 Radius=4.79221 StartAngle=5.23599 EndAngle=6.28319
    g8: LineSegment StartX=39.7039 StartY=26.3872 StartZ=0 EndX=42.1 EndY=27.7705 EndZ=0
    g9: LineSegment StartX=42.1 StartY=27.7705 StartZ=0 EndX=42.1 EndY=30.5373 EndZ=0
    g10: ArcOfCircle CenterX=29.6 CenterY=289.171 CenterZ=0 NormalX=0 NormalY=0 NormalZ=1 AngleXU=0 Radius=12.5 StartAngle=-9e-16 EndAngle=0.452137
    g11: LineSegment StartX=42.1 StartY=289.171 StartZ=0 EndX=42.1 EndY=292.046 EndZ=0
    g12: LineSegment StartX=42.1 StartY=292.046 StartZ=0 EndX=40.8439 EndY=294.632 EndZ=0
    g13: LineSegment StartX=11.5 StartY=348.872 StartZ=0 EndX=14.5 EndY=348.872 EndZ=0
    g14: LineSegment StartX=14.5 StartY=348.872 StartZ=0 EndX=15.8107 EndY=346.173 EndZ=0
    g15: ArcOfCircle CenterX=11.5 CenterY=344.079 CenterZ=0 NormalX=0 NormalY=0 NormalZ=1 AngleXU=0 Radius=4.79221 StartAngle=0.452137 EndAngle=1.5708
  constraints (42):
    c: Coincident(g0,g-4)
    c: Coincident(g0,g-5)
    c: Coincident(g1,g-5)
    c: PointOnObject(g1,g-2)
    c: Horizontal(g1)
    c: Coincident(g2,g-3)
    c: Coincident(g2,g-4)
    c: PointOnObject(g3,g-2)
    c: PointOnObject(g3,g-2)
    c: PointOnObject(g3,g-3)
    c: Coincident(g4,g-3)
    c: Coincident(g4,g3)
    c: Tangent(g4,g3)
    c: PointOnObject(g5,g-4)
    c: Coincident(g5,g2)
    c: PointOnObject(g5,g-4)
    c: Coincident(g6,g2)
    c: Coincident(g6,g5)
    c: Diameter(g5) = 3.2
    c: PointOnObject(g7,g-4)
    c: PointOnObject(g7,g0)
    c: Coincident(g8,g0)
    c: Coincident(g9,g8)
    c: Coincident(g9,g7)
    c: Tangent(g9,g7)
    c: Tangent(g8,g7) = -1.5708
    c: PointOnObject(g10,g-5)
    c: PointOnObject(g10,g0)
    c: Coincident(g11,g12)
    c: Tangent(g10,g11) = -1.5708
    c: Coincident(g11,g0)
    c: Tangent(g12,g10) = -1.5708
    c: PointOnObject(g13,g1)
    c: Coincident(g13,g1)
    c: Coincident(g13,g14)
    c: PointOnObject(g14,g-5)
    c: Tangent(g15,g13) = 1.5708
    c: Tangent(g15,g14) = 1.5708
    c: DistanceX(g13,g13) = 3
    c: Diameter(g10) = 25
    c: Equal(g3,g7)
    c: Equal(g7,g15)
FEATURE [Part::Mirroring] Part__Mirroring008  label="Sketch026 (Mirror #9)"
  Base = (0,0,0)
  Normal = (1,0,0)
  Source = -> Sketch026
FEATURE [Part::Compound] Compound014
  Links = -> [Part__Mirroring008,Sketch026]
FEATURE [PartDesign::SubShapeBinder] Binder021
  BindCopyOnChange = 0
  BindMode = 0
  ClaimChildren = true
  Fuse = false
  MakeFace = true
  OffsetFill = false
  OffsetIntersection = false
  OffsetJoinType = 0
  OffsetOpenResult = false
  PartialLoad = false
  Relative = false
  Support = -> [Compound014]
  _Version = 2
FEATURE [PartDesign::Pocket] Pocket006
  BaseFeature = -> Pad005
  Direction = (0,0,-1)
  Length = 5
  Length2 = 5
  Midplane = true
  Profile = -> Binder021
  Suppressed = false
  Type = 1
FEATURE [Sketcher::SketchObject] Sketch027
  ArcFitTolerance = 0
  AttachmentSupport = -> [XY_Plane007]
  FullyConstrained = true
  MakeInternals = false
  MapMode = 5
  sketch-geometry (1):
    g0: Circle CenterX=0 CenterY=40 CenterZ=0 NormalX=0 NormalY=0 NormalZ=1 AngleXU=0 Radius=4
  constraints (3):
    c: PointOnObject(g0,g-2)
    c: Diameter(g0) = 8
    c: DistanceY(g0) = 40
FEATURE [PartDesign::SubShapeBinder] Binder023
  BindCopyOnChange = 0
  BindMode = 0
  ClaimChildren = true
  Context = -> Body004 [Binder023.]
  Fuse = false
  MakeFace = true
  OffsetFill = false
  OffsetIntersection = false
  OffsetJoinType = 0
  OffsetOpenResult = false
  PartialLoad = false
  Relative = true
  Support = -> [Clone005]
  _Version = 2
FEATURE [Sketcher::SketchObject] Sketch028
  ArcFitTolerance = 0
  AttachmentSupport = -> [XY_Plane007]
  ExternalGeometry = -> [Binder023]
  FullyConstrained = true
  MakeInternals = false
  MapMode = 5
  expr: Constraints[9] = <<Properties>>.rivet_d
  sketch-geometry (10):
    g0: Circle CenterX=0 CenterY=59 CenterZ=0 NormalX=0 NormalY=0 NormalZ=1 AngleXU=0 Radius=1.7
    g1: Circle CenterX=0 CenterY=106.372 CenterZ=0 NormalX=0 NormalY=0 NormalZ=1 AngleXU=0 Radius=1.7
    g2: Circle CenterX=0 CenterY=181.372 CenterZ=0 NormalX=0 NormalY=0 NormalZ=1 AngleXU=0 Radius=1.7
    g3: Circle CenterX=0 CenterY=256.372 CenterZ=0 NormalX=0 NormalY=0 NormalZ=1 AngleXU=0 Radius=1.7
    g4: Circle CenterX=0 CenterY=303.743 CenterZ=0 NormalX=0 NormalY=0 NormalZ=1 AngleXU=0 Radius=1.7
    g5: LineSegment [constr] StartX=28.3 StartY=73.8716 StartZ=0 EndX=28.3 EndY=106.372 EndZ=0
    g6: LineSegment [constr] StartX=28.3 StartY=106.372 StartZ=0 EndX=28.3 EndY=138.872 EndZ=0
    g7: LineSegment [constr] StartX=28.3 StartY=138.872 StartZ=0 EndX=28.3 EndY=181.372 EndZ=0
    g8: LineSegment [constr] StartX=28.3 StartY=181.372 StartZ=0 EndX=28.3 EndY=223.872 EndZ=0
    g9: LineSegment [constr] StartX=28.3 StartY=223.872 StartZ=0 EndX=28.3 EndY=256.372 EndZ=0
  constraints (24):
    c: PointOnObject(g0,g-2)
    c: PointOnObject(g1,g-2)
    c: PointOnObject(g2,g-2)
    c: PointOnObject(g3,g-2)
    c: DistanceY(g0) = 59
    c: Equal(g0, g1-g4) x4
    c: Diameter(g0) = 3.4
    c: Coincident(g5,g-3)
    c: Vertical(g5)
    c: Coincident(g5,g6)
    c: Coincident(g6,g-4)
    c: Coincident(g6,g7)
    c: Vertical(g7)
    c: Coincident(g7,g8)
    c: Coincident(g8,g-5)
    c: Coincident(g8,g9)
    c: Vertical(g9)
    c: Equal(g5,g6)
    c: Equal(g6,g9)
    c: Equal(g7,g8)
    c: Horizontal(g2,g7)
    c: Horizontal(g1,g5)
    c: Horizontal(g3,g9)
    c: Symmetric(g0,g4,g2)
FEATURE [PartDesign::Hole] Hole003
  BaseFeature = -> Pocket006
  CustomThreadClearance = 0
  Depth = 25
  DepthType = 0
  Diameter = 3.4
  DrillForDepth = false
  DrillPoint = 1
  DrillPointAngle = 118
  HoleCutCountersinkAngle = 90
  HoleCutCustomValues = false
  HoleCutDepth = 0
  HoleCutDiameter = 6.1
  HoleCutType = 0
  ModelThread = false
  Profile = -> Sketch028
  Reversed = true
  Suppressed = false
  Tapered = false
  TaperedAngle = 90
  ThreadClass = 0
  ThreadDepth = 25
  ThreadDepthType = 0
  ThreadDirection = 0
  ThreadFit = 0
  ThreadSize = 0
  ThreadType = 0
  Threaded = false
  UseCustomThreadClearance = false
  expr: Diameter = <<Properties>>.rivet_d
FEATURE [Sketcher::SketchObject] Sketch029  label="top_connector_base_sketch"
  ArcFitTolerance = 0
  AttachmentOffset = pos=(0,0,-35) rot=(0,0,1;0rad)
  AttachmentSupport = -> [XZ_Plane024]
  FullyConstrained = true
  MakeInternals = false
  MapMode = 5
  Placement = pos=(0,35,-7.8e-15) rot=(1,0,0;1.5708rad)
  expr: .Constraints.width = <<Properties>>.inner_width
  sketch-geometry (5):
    g0: LineSegment StartX=-11.5 StartY=-13 StartZ=0 EndX=-11.5 EndY=-1.95e-14 EndZ=0
    g1: LineSegment StartX=-11.5 StartY=-1.95e-14 StartZ=0 EndX=11.5 EndY=-1.95e-14 EndZ=0
    g2: LineSegment StartX=11.5 StartY=-1.95e-14 StartZ=0 EndX=11.5 EndY=-13 EndZ=0
    g3: LineSegment [constr] StartX=11.5 StartY=-13 StartZ=0 EndX=-11.5 EndY=-13 EndZ=0
    g4: GeomPoint [constr] X=-3.6e-15 Y=-6.5 Z=0
  constraints (13):
    c: Coincident(g0,g1)
    c: Coincident(g1,g2)
    c: Coincident(g2,g3)
    c: Coincident(g3,g0)
    c: Horizontal(g1)
    c: Horizontal(g3)
    c: Vertical(g0)
    c: Vertical(g2)
    c: Symmetric(g1,g0,g4)
    c: PointOnObject(g4,g-2)
    c: PointOnObject(g1,g-1)
    c: DistanceX(g1,g1) = 23  'width'
    c: DistanceY(g2,g2) = 13  'height'
FEATURE [PartDesign::FeaturePython] BaseBend009  # WARN: FeaturePython — macro-defined, semantics opaque (R4)
  BendSide = 0
  BendSketch = -> Sketch029
  MidPlane = false
  Reverse = true
  Suppressed = false
  length = 283.743
  radius = 0.1
  thickness = 0.3
  expr: radius = composit_properties#<<Properties>>.bend_r
  expr: thickness = composit_properties#<<Properties>>.al_thickness
FEATURE [PartDesign::SubShapeBinder] Binder029
  BindCopyOnChange = 0
  BindMode = 0
  ClaimChildren = false
  Context = -> Body017 [Binder029.]
  Fuse = false
  MakeFace = true
  OffsetFill = false
  OffsetIntersection = false
  OffsetJoinType = 0
  OffsetOpenResult = false
  PartialLoad = false
  Relative = true
  Support = -> [Sketch027]
  _Version = 2
  expr: Support = Sketch027._self
FEATURE [PartDesign::SubShapeBinder] Binder030
  BindCopyOnChange = 0
  BindMode = 0
  ClaimChildren = false
  Context = -> Body017 [Binder030.]
  Fuse = false
  MakeFace = true
  OffsetFill = false
  OffsetIntersection = false
  OffsetJoinType = 0
  OffsetOpenResult = false
  PartialLoad = false
  Relative = true
  Support = -> [Sketch028]
  _Version = 2
  expr: Support = Sketch028._self
FEATURE [PartDesign::Hole] Hole004
  BaseFeature = -> BaseBend009
  CustomThreadClearance = 0
  Depth = 25
  DepthType = 0
  Diameter = 3.4
  DrillForDepth = false
  DrillPoint = 1
  DrillPointAngle = 118
  HoleCutCountersinkAngle = 90
  HoleCutCustomValues = false
  HoleCutDepth = 0
  HoleCutDiameter = 6.1
  HoleCutType = 0
  ModelThread = false
  Profile = -> Binder030
  Suppressed = false
  Tapered = false
  TaperedAngle = 90
  ThreadClass = 0
  ThreadDepth = 25
  ThreadDepthType = 0
  ThreadDirection = 0
  ThreadFit = 0
  ThreadSize = 0
  ThreadType = 0
  Threaded = false
  UseCustomThreadClearance = false
  expr: Diameter = <<Properties>>.rivet_d
FEATURE [Sketcher::SketchObject] Sketch032
  ArcFitTolerance = 0
  AttachmentSupport = -> [XZ_Plane025]
  FullyConstrained = true
  MakeInternals = false
  MapMode = 5
  Placement = pos=(0,0,0) rot=(1,0,0;1.5708rad)
  expr: Constraints[11] = <<Properties>>.inner_width
  sketch-geometry (5):
    g0: LineSegment StartX=-11.5 StartY=-12 StartZ=0 EndX=-11.5 EndY=-2.84e-14 EndZ=0
    g1: LineSegment StartX=-11.5 StartY=-2.84e-14 StartZ=0 EndX=11.5 EndY=-2.84e-14 EndZ=0
    g2: LineSegment StartX=11.5 StartY=-2.84e-14 StartZ=0 EndX=11.5 EndY=-12 EndZ=0
    g3: LineSegment [constr] StartX=11.5 StartY=-12 StartZ=0 EndX=-11.5 EndY=-12 EndZ=0
    g4: GeomPoint [constr] X=-5.1e-15 Y=-6 Z=0
  constraints (13):
    c: Coincident(g0,g1)
    c: Coincident(g1,g2)
    c: Coincident(g2,g3)
    c: Coincident(g3,g0)
    c: Horizontal(g1)
    c: Horizontal(g3)
    c: Vertical(g0)
    c: Vertical(g2)
    c: Symmetric(g1,g0,g4)
    c: PointOnObject(g4,g-2)
    c: PointOnObject(g1,g-1)
    c: DistanceX(g1,g1) = 23
    c: DistanceY(g2,g2) = 12
FEATURE [PartDesign::FeaturePython] BaseBend010  # WARN: FeaturePython — macro-defined, semantics opaque (R4)
  BendSide = 0
  BendSketch = -> Sketch032
  MidPlane = false
  Reverse = true
  Suppressed = false
  length = 35
  radius = 0.1
  thickness = 0.3
  expr: radius = composit_properties#<<Properties>>.bend_r
  expr: thickness = composit_properties#<<Properties>>.al_thickness
FEATURE [Sketcher::SketchObject] Sketch033
  ArcFitTolerance = 0
  AttachmentSupport = -> [XY_Plane025]
  FullyConstrained = true
  MakeInternals = false
  MapMode = 5
  expr: Constraints[6] = composit_properties#<<Properties>>.bend_r + composit_properties#<<Properties>>.al_thickness
  expr: Constraints[7] = <<Properties>>.inner_width / 2
  sketch-geometry (7):
    g0: LineSegment StartX=0 StartY=-1.289e-13 StartZ=0 EndX=11.1 EndY=6.40859 EndZ=0
    g1: LineSegment StartX=11.5 StartY=0 StartZ=0 EndX=0 EndY=-1.289e-13 EndZ=0
    g2: LineSegment StartX=11.1 StartY=6.40859 StartZ=0 EndX=11.1 EndY=8.33953 EndZ=0
    g3: LineSegment StartX=11.1 StartY=8.33953 StartZ=0 EndX=11.5 EndY=8.33953 EndZ=0
    g4: GeomPoint [constr] X=11.5 Y=6.63953 Z=0
    g5: LineSegment StartX=11.5 StartY=8.33953 StartZ=0 EndX=11.5 EndY=6.63953 EndZ=0
    g6: LineSegment StartX=11.5 StartY=6.63953 StartZ=0 EndX=11.5 EndY=0 EndZ=0
  constraints (18):
    c: Coincident(g-1,g0)
    c: Coincident(g0,g2)
    c: Coincident(g3,g5)
    c: PointOnObject(g6,g-1)
    c: Coincident(g6,g1)
    c: Coincident(g1,g0)
    c: DistanceX(g2,g3) = 0.4
    c: DistanceX(g1,g1) = 11.5
    c: Coincident(g2,g3)
    c: Horizontal(g3)
    c: Vertical(g2)
    c: PointOnObject(g4,g0)
    c: DistanceY(g4,g5) = 1.7
    c: Angle(g0) = 0.523599
    c: Coincident(g5,g6)
    c: Vertical(g5)
    c: Vertical(g6)
    c: Coincident(g5,g4)
FEATURE [PartDesign::Pocket] Pocket018
  BaseFeature = -> BaseBend010
  Direction = (0,0,-1)
  Length = 5
  Length2 = 5
  Profile = -> Sketch033
  ReferenceAxis = -> Sketch033 [N_Axis]
  Suppressed = false
  Type = 1
FEATURE [PartDesign::Mirrored] Mirrored001
  BaseFeature = -> Pocket018
  MirrorPlane = -> Sketch033 [V_Axis]
  Originals = -> [Pocket018]
  Suppressed = false
  TransformMode = 0
FEATURE [Sketcher::SketchObject] Sketch034
  ArcFitTolerance = 0
  AttachmentSupport = -> [YZ_Plane025]
  ExternalGeometry = -> [Sketch033]
  FullyConstrained = false
  MakeInternals = false
  MapMode = 5
  Placement = pos=(0,0,0) rot=(0.57735,0.57735,0.57735;2.0944rad)
  sketch-geometry (4):
    g0: LineSegment StartX=6.63953 StartY=-25.0734 StartZ=0 EndX=22.8156 EndY=-25.0734 EndZ=0
    g1: LineSegment StartX=22.8156 StartY=-25.0734 StartZ=0 EndX=8.57047 EndY=-0.4 EndZ=0
    g2: LineSegment StartX=6.63953 StartY=-0.4 StartZ=0 EndX=6.63953 EndY=-25.0734 EndZ=0
    g3: LineSegment StartX=6.63953 StartY=-0.4 StartZ=0 EndX=8.57047 EndY=-0.4 EndZ=0
  constraints (11):
    c: Coincident(g2,g0)
    c: Horizontal(g0)
    c: Coincident(g0,g1)
    c: Vertical(g2)
    c: Coincident(g3,g2)
    c: Coincident(g3,g1)
    c: Horizontal(g3)
    c: Angle(g1) = 2.0944
    c: DistanceY(g2) = -0.4
    c: PointOnObject(g-3,g2)
    c: PointOnObject(g-3,g1)
FEATURE [PartDesign::Pocket] Pocket019
  BaseFeature = -> Mirrored001
  Direction = (-1,0,0)
  Length = 5
  Length2 = 5
  Midplane = true
  Profile = -> Sketch034
  ReferenceAxis = -> Sketch034 [N_Axis]
  Suppressed = false
  Type = 1
FEATURE [Sketcher::SketchObject] Sketch036
  ArcFitTolerance = 0
  AttachmentSupport = -> [XY_Plane025]
  FullyConstrained = true
  MakeInternals = false
  MapMode = 5
  sketch-geometry (1):
    g0: Circle CenterX=0 CenterY=25 CenterZ=0 NormalX=0 NormalY=0 NormalZ=1 AngleXU=0 Radius=3
  constraints (3):
    c: PointOnObject(g0,g-2)
    c: DistanceY(g0) = 25
    c: Diameter(g0) = 6
FEATURE [PartDesign::Pocket] Pocket021
  BaseFeature = -> Pocket019
  Direction = (0,0,-1)
  Length = 5
  Length2 = 5
  Profile = -> Sketch036
  ReferenceAxis = -> Sketch036 [N_Axis]
  Suppressed = false
  Type = 0
FEATURE [Sketcher::SketchObject] Sketch037
  ArcFitTolerance = 0
  AttachmentSupport = -> [XY_Plane028]
  FullyConstrained = false
  MakeInternals = false
  MapMode = 5
  sketch-geometry (2):
    g0: LineSegment StartX=0 StartY=0 StartZ=0 EndX=74.4649 EndY=59.2839 EndZ=0
    g1: LineSegment StartX=0 StartY=0 StartZ=0 EndX=-93.8109 EndY=73.3435 EndZ=0
  constraints (2):
    c: Coincident(g0,g-1)
    c: Coincident(g1,g0)
FEATURE [Part::Part2DObjectPython] Line  label="sink_bend_line"  # Draft 2D object (typed FeaturePython)
  Area = 0
  AttachmentOffset = pos=(304.73,175.936,20) rot=(0,0,1;0rad)
  AttachmentSupport = -> [XY_Plane028]
  BendAngle = 6.48542
  ChamferSize = 0
  Closed = false
  End = (0,0,0)
  FaceAngle = 3.2479
  FilletRadius = 0
  Length = 352.44
  MakeFace = true
  MapMode = 5
  Placement = pos=(304.73,175.936,20) rot=(0,0,1;0rad)
  Points = (2) [(0,0,0),(-304.73,-175.936,-20)]
  Start = (304.73,175.936,20)
  Subdivisions = 0
  expr: .AttachmentOffset.Base.x = Spreadsheet.total_length * cos(30)
  expr: .AttachmentOffset.Base.y = Spreadsheet.total_length * sin(30)
  expr: BendAngle = atan2(.AttachmentOffset.Base.z; .AttachmentOffset.Base.y)
  expr: End = tuple(0; 0; 0)
  expr: FaceAngle = atan2(.AttachmentOffset.Base.z; Length)
FEATURE [PartDesign::Line] DatumLine
  AttacherType = Attacher::AttachEngineLine
  AttachmentSupport = -> [Z_Axis028]
  Length = 20
  MapMode = 29
  ResizeMode = 0
FEATURE [PartDesign::Line] DatumLine001
  AttacherType = Attacher::AttachEngineLine
  AttachmentSupport = -> [Line,X_Axis028]
  Length = 20
  MapMode = 24
  Placement = pos=(304.73,175.936,20) rot=(0.57735,-0.57735,-0.57735;2.0944rad)
  ResizeMode = 0
FEATURE [Sketcher::SketchObject] Sketch038
  ArcFitTolerance = 0
  AttachmentSupport = -> [Line]
  ExternalGeometry = -> [DatumLine001]
  FullyConstrained = false
  MakeInternals = false
  MapMode = 45
  Placement = pos=(152.365,87.9679,10) rot=(0.368581,0.6384,0.675717;2.39766rad)
  sketch-geometry (3):
    g0: LineSegment StartX=4.75e-14 StartY=4.27e-14 StartZ=0 EndX=4.75e-14 EndY=93.8582 EndZ=0
    g1: LineSegment StartX=4.75e-14 StartY=4.27e-14 StartZ=0 EndX=35.2298 EndY=3.46271 EndZ=0
    g2: ArcOfCircle CenterX=2.5 CenterY=2.75777 CenterZ=0 NormalX=0 NormalY=0 NormalZ=1 AngleXU=0 Radius=2.5 StartAngle=3.14159 EndAngle=4.81036
  constraints (9):
    c: Coincident(g0,g-1)
    c: Vertical(g0)
    c: Coincident(g1,g0)
    c: PointOnObject(g1,g-3)
    c: Angle(g-3) = 0.0979746
    c: Angle(g1,g0) = 1.47282  'bend_angle'
    c: Tangent(g2,g0) = 1.5708
    c: Tangent(g2,g1) = -1.5708
    c: Radius(g2) = 2.5
FEATURE [PartDesign::CoordinateSystem] Local_CS
  AttacherType = Attacher::AttachEngine3D
  AttachmentOffset = pos=(0,0,0) rot=(1,0,0;0.113192rad)
  AttachmentSupport = -> [XY_Plane028]
  MapMode = 5
  Placement = pos=(0,0,0) rot=(1,0,0;0.113192rad)
  expr: .AttachmentOffset.Rotation.Angle = Line.BendAngle
FEATURE [Sketcher::SketchObject] Sketch039
  ArcFitTolerance = 0
  AttachmentSupport = -> [Local_CS]
  ExternalGeometry = -> [Line,Sketch038]
  FullyConstrained = true
  MakeInternals = false
  MapMode = 5
  Placement = pos=(0,0,0) rot=(1,0,0;0.113192rad)
  sketch-geometry (3):
    g0: LineSegment StartX=2e-16 StartY=3.18954 StartZ=0 EndX=-459.172 EndY=270 EndZ=0
    g1: LineSegment StartX=2e-16 StartY=3.18954 StartZ=0 EndX=459.172 EndY=270 EndZ=0
    g2: LineSegment StartX=459.172 StartY=270 StartZ=0 EndX=-459.172 EndY=270 EndZ=0
  constraints (8):
    c: Coincident(g2,g1)
    c: DistanceY(g1) = 270
    c: Coincident(g0,g2)
    c: Symmetric(g1,g0,g-2)
    c: Coincident(g1,g0)
    c: PointOnObject(g0,g-2)
    c: Parallel(g1,g-3)
    c: PointOnObject(g-4,g1)
FEATURE [PartDesign::FeaturePython] BaseBend011  # WARN: FeaturePython — macro-defined, semantics opaque (R4)
  BendSide = 0
  BendSketch = -> Sketch039
  MidPlane = false
  Reverse = false
  Suppressed = false
  length = 100
  radius = 2
  thickness = 0.5
FEATURE [PartDesign::FeaturePython] Bend004  # WARN: FeaturePython — macro-defined, semantics opaque (R4)
  AutoMiter = false
  BaseFeature = -> BaseBend011
  BendType = 0
  LengthList = [100]
  LengthSpec = 1
  NonperforationMaxLength = 5
  Perforate = false
  PerforationAngle = 0
  PerforationInitialLength = 5
  PerforationMaxLength = 5
  ReliefFactor = 0.7
  Suppressed = false
  UseReliefFactor = false
  angle = 95.6135
  baseObject = -> BaseBend011 [Edge3,Edge8]
  bendAList = [95.6135]
  extend1 = 2
  extend2 = 0
  gap1 = 0
  gap2 = 0
  invert = true
  kfactor = 0.5
  length = 100
  maxExtendDist = 5
  minGap = 0.1
  minReliefGap = 1
  miterangle1 = 0
  miterangle2 = 0
  offset = 0
  radius = 2
  reliefType = 0
  reliefd = 1
  reliefw = 0.8
  sketchflip = false
  sketchinvert = false
  unfold = false
  expr: angle = 180 deg - Sketch038.Constraints.bend_angle
  expr: radius = BaseBend011.radius
FEATURE [Sketcher::SketchObject] Sketch040
  ArcFitTolerance = 0
  AttachmentSupport = -> [Local_CS]
  ExternalGeometry = -> [Line,Sketch038]
  FullyConstrained = true
  MakeInternals = false
  MapMode = 5
  Placement = pos=(0,0,0) rot=(1,0,0;0.113192rad)
  sketch-geometry (13):
    g0: ArcOfCircle CenterX=0 CenterY=-630 CenterZ=0 NormalX=0 NormalY=0 NormalZ=1 AngleXU=0 Radius=870 StartAngle=1.24863 EndAngle=1.89296
    g1: LineSegment [constr] StartX=0 StartY=0 StartZ=0 EndX=294.959 EndY=171.391 EndZ=0
    g2: LineSegment [constr] StartX=150.979 StartY=90.9189 StartZ=0 EndX=293.573 EndY=173.776 EndZ=0
    g3: LineSegment [constr] StartX=-294.959 StartY=171.391 StartZ=0 EndX=0 EndY=0 EndZ=0
    g4: LineSegment StartX=-294.959 StartY=171.391 StartZ=0 EndX=-464.661 EndY=270 EndZ=0
    g5: LineSegment StartX=-464.661 StartY=270 StartZ=0 EndX=464.661 EndY=270 EndZ=0
    g6: LineSegment StartX=464.661 StartY=270 StartZ=0 EndX=294.959 EndY=171.391 EndZ=0
    g7: LineSegment StartX=294.959 StartY=171.391 StartZ=0 EndX=294.075 EndY=172.911 EndZ=0
    g8: LineSegment StartX=294.075 StartY=172.911 StartZ=0 EndX=293.573 EndY=173.776 EndZ=0
    g9: LineSegment [constr] StartX=-294.959 StartY=171.391 StartZ=0 EndX=-294.959 EndY=171.391 EndZ=0
    g10: LineSegment StartX=293.573 StartY=173.776 StartZ=0 EndX=275.46 EndY=195.241 EndZ=0
    g11: LineSegment StartX=-293.573 StartY=173.776 StartZ=0 EndX=-275.46 EndY=195.241 EndZ=0
    g12: LineSegment StartX=-294.959 StartY=171.391 StartZ=0 EndX=-293.573 EndY=173.776 EndZ=0
  constraints (34):
    c: Coincident(g1,g-1)
    c: PointOnObject(g1,g-3)
    c: Coincident(g7,g1)
    c: Distance(g1) = 341.139
    c: Coincident(g2,g-4)
    c: Parallel(g2,g1)
    c: DistanceY(g0) = -630
    c: Radius(g0) = 870
    c: Coincident(g9,g3)
    c: Coincident(g3,g1)
    c: Symmetric(g9,g7,g-2)
    c: Coincident(g4,g5)
    c: Coincident(g5,g6)
    c: Parallel(g6,g2)
    c: Symmetric(g5,g4,g-2)
    c: DistanceY(g5) = 270
    c: Coincident(g2,g8)
    c: Coincident(g7,g8)
    c: Perpendicular(g1,g7)
    c: Perpendicular(g1,g8)
    c: Distance(g8) = 1
    c: Coincident(g10,g0)
    c: Coincident(g11,g0)
    c: PointOnObject(g0,g-2)
    c: Coincident(g10,g8)
    c: Coincident(g12,g9)
    c: Coincident(g4,g12)
    c: Coincident(g12,g11)
    c: Symmetric(g4,g6,g-2)
    c: Symmetric(g8,g11,g-2)
    c: Horizontal(g0,g0)
    c: Distance(g10) = 28.0862
    c: Angle(g10,g2) = 1.39626
    c: Coincident(g6,g7)
FEATURE [PartDesign::SubShapeBinder] Binder031
  BindCopyOnChange = 0
  BindMode = 0
  ClaimChildren = false
  Context = -> Part007 [Body020.Binder031.]
  Fuse = false
  MakeFace = true
  OffsetFill = false
  OffsetIntersection = false
  OffsetJoinType = 0
  OffsetOpenResult = false
  PartialLoad = false
  Relative = true
  _Version = 2
FEATURE [PartDesign::Pocket] Pocket022
  BaseFeature = -> Bend004
  Direction = (0,0.11295,-0.993601)
  Length = 2.5
  Length2 = 5
  Profile = -> Sketch040
  ReferenceAxis = -> Sketch040 [N_Axis]
  Refine = true
  Reversed = true
  Suppressed = false
  Type = 0
FEATURE [Sketcher::SketchObject] Sketch042
  ArcFitTolerance = 0
  AttachmentSupport = -> [XY_Plane028]
  FullyConstrained = true
  MakeInternals = false
  MapMode = 5
  sketch-geometry (7):
    g0: LineSegment StartX=-18.3205 StartY=-10 StartZ=0 EndX=-0.5 EndY=0.288675 EndZ=0
    g1: LineSegment StartX=18.3205 StartY=-10 StartZ=0 EndX=-18.3205 EndY=-10 EndZ=0
    g2: LineSegment [constr] StartX=1 StartY=1.5e-15 StartZ=0 EndX=-1e-16 EndY=0.57735 EndZ=0
    g3: LineSegment [constr] StartX=1.3e-15 StartY=-2.2e-15 StartZ=0 EndX=0.5 EndY=0.288675 EndZ=0
    g4: LineSegment StartX=0.5 StartY=0.288675 StartZ=0 EndX=18.3205 EndY=-10 EndZ=0
    g5: LineSegment StartX=-2.6e-15 StartY=1.1547 StartZ=0 EndX=0.5 EndY=0.288675 EndZ=0
    g6: LineSegment StartX=-0.5 StartY=0.288675 StartZ=0 EndX=-2.6e-15 EndY=1.1547 EndZ=0
  constraints (19):
    c: Coincident(g4,g1)
    c: Coincident(g1,g0)
    c: Symmetric(g4,g0,g-2)
    c: PointOnObject(g2,g-1)
    c: PointOnObject(g2,g-2)
    c: Angle(g2) = 2.61799
    c: Distance(g-1,g2) = 0.5
    c: Coincident(g3,g-1)
    c: PointOnObject(g3,g2)
    c: Angle(g3) = 0.523599
    c: PointOnObject(g2,g4)
    c: Perpendicular(g3,g5)
    c: Coincident(g4,g5)
    c: Coincident(g4,g3)
    c: PointOnObject(g5,g-2)
    c: Coincident(g6,g0)
    c: Coincident(g6,g5)
    c: Symmetric(g4,g0,g-2)
    c: DistanceY(g1) = -10
FEATURE [Sketcher::SketchObject] Sketch041
  ArcFitTolerance = 0
  AttachmentOffset = pos=(0,0,0) rot=(0,1,0;0.523599rad)
  AttachmentSupport = -> [XZ_Plane028]
  ExternalGeometry = -> [Sketch038,Sketch042,Sketch040]
  FullyConstrained = false
  MakeInternals = false
  MapMode = 5
  Placement = pos=(0,0,0) rot=(0.935113,0.250563,0.250563;1.63783rad)
  sketch-geometry (16):
    g0: LineSegment StartX=340.573 StartY=19.628 StartZ=0 EndX=340.432 EndY=22.112 EndZ=0
    g1: LineSegment [constr] StartX=175.779 StartY=12.7533 StartZ=0 EndX=340.432 EndY=22.112 EndZ=0
    g2: LineSegment StartX=0.57735 StartY=196.491 StartZ=0 EndX=638.392 EndY=196.491 EndZ=0
    g3: LineSegment StartX=638.392 StartY=196.491 StartZ=0 EndX=638.392 EndY=36.5557 EndZ=0
    g4: LineSegment StartX=638.392 StartY=36.5557 StartZ=0 EndX=340.573 EndY=19.628 EndZ=0
    g5: LineSegment StartX=340.432 StartY=22.112 StartZ=0 EndX=340.432 EndY=85 EndZ=0
    g6: LineSegment StartX=0.57735 StartY=85 StartZ=0 EndX=0.57735 EndY=196.491 EndZ=0
    g7: LineSegment StartX=335.432 StartY=90 StartZ=0 EndX=5.57735 EndY=90 EndZ=0
    g8: ArcOfCircle CenterX=5.57735 CenterY=85 CenterZ=0 NormalX=0 NormalY=0 NormalZ=1 AngleXU=0 Radius=5 StartAngle=1.5708 EndAngle=3.14159
    g9: ArcOfCircle CenterX=335.432 CenterY=85 CenterZ=0 NormalX=0 NormalY=0 NormalZ=1 AngleXU=0 Radius=5 StartAngle=2e-16 EndAngle=1.5708
    g10: GeomPoint [constr] X=340.432 Y=90 Z=0
    g11: LineSegment StartX=0.57735 StartY=0 StartZ=0 EndX=0.57735 EndY=27.6603 EndZ=0
    g12: ArcOfCircle CenterX=5 CenterY=27.6603 CenterZ=0 NormalX=0 NormalY=0 NormalZ=1 AngleXU=0 Radius=4.42265 StartAngle=3.14159 EndAngle=4.18879
    g13: ArcOfCircle CenterX=0.57735 CenterY=20 CenterZ=0 NormalX=0 NormalY=0 NormalZ=1 AngleXU=0 Radius=4.42265 StartAngle=-2.31e-14 EndAngle=1.0472
    g14: LineSegment StartX=5 StartY=20 StartZ=0 EndX=5 EndY=0 EndZ=0
    g15: LineSegment StartX=5 StartY=0 StartZ=0 EndX=0.57735 EndY=0 EndZ=0
  constraints (39):
    c: Coincident(g1,g-3)
    c: Coincident(g1,g0)
    c: Perpendicular(g-3,g1)
    c: Perpendicular(g1,g0)
    c: Coincident(g5,g0)
    c: Coincident(g6,g2)
    c: Horizontal(g2)
    c: Coincident(g2,g3)
    c: Vertical(g3)
    c: Coincident(g3,g4)
    c: Coincident(g4,g0)
    c: Parallel(g4,g1)
    c: Vertical(g5)
    c: Vertical(g6)
    c: Vertical(g6,g-4)
    c: Horizontal(g7)
    c: Tangent(g8,g7) = -1.5708
    c: Tangent(g8,g6) = 1.5708
    c: PointOnObject(g10,g5)
    c: PointOnObject(g10,g7)
    c: Tangent(g5,g9) = -1.5708
    c: Tangent(g7,g9) = -1.5708
    c: Equal(g9,g8)
    c: Coincident(g11,g-4)
    c: Vertical(g11)
    c: PointOnObject(g13,g11)
    c: PointOnObject(g14,g-1)
    c: Vertical(g14)
    c: Coincident(g15,g14)
    c: Coincident(g15,g11)
    c: Tangent(g13,g12) = 1.5708
    c: Tangent(g12,g11) = 1.5708
    c: Tangent(g14,g13) = 1.5708
    c: Equal(g13,g12)
    c: DistanceX(g14) = 5
    c: DistanceY(g13) = 20
    c: DistanceY(g7) = 90
    c: Radius(g9) = 5
    c: Coincident(g0,g-5)
FEATURE [Sketcher::SketchObject] Sketch043
  ArcFitTolerance = 0
  AttachmentSupport = -> [Local_CS]
  FullyConstrained = false
  MakeInternals = false
  MapMode = 5
  Placement = pos=(0,0,0) rot=(1,0,0;0.113192rad)
  expr: Constraints[12] = Sketch038.Constraints.bend_angle / 2
  sketch-geometry (7):
    g0: ArcOfCircle CenterX=-2.2e-14 CenterY=1.72e-14 CenterZ=0 NormalX=0 NormalY=0 NormalZ=1 AngleXU=0 Radius=19.4106 StartAngle=5.52221 EndAngle=10.1858
    g1: ArcOfCircle CenterX=17.4885 CenterY=-16.6545 CenterZ=0 NormalX=0 NormalY=0 NormalZ=1 AngleXU=0 Radius=4.73935 StartAngle=2.38062 EndAngle=3.72466
    g2: ArcOfCircle CenterX=-17.4885 CenterY=-16.6545 CenterZ=0 NormalX=0 NormalY=0 NormalZ=1 AngleXU=0 Radius=4.73935 StartAngle=5.70012 EndAngle=7.04416
    g3: LineSegment StartX=13.5322 StartY=-19.2639 StartZ=0 EndX=49.1398 EndY=-73.2508 EndZ=0
    g4: LineSegment StartX=-13.5322 StartY=-19.2639 StartZ=0 EndX=-49.1398 EndY=-73.2508 EndZ=0
    g5: LineSegment StartX=-49.1398 StartY=-73.2508 StartZ=0 EndX=49.1398 EndY=-73.2508 EndZ=0
    g6: LineSegment StartX=-86.3387 StartY=-141.994 StartZ=0 EndX=130.665 EndY=54.7259 EndZ=0
  constraints (13):
    c: Coincident(g0,g-1)
    c: Coincident(g5,g4)
    c: Coincident(g5,g3)
    c: Tangent(g3,g1) = -1.5708
    c: Tangent(g1,g0) = 1.5708
    c: Tangent(g2,g0) = 1.5708
    c: Tangent(g4,g2) = 1.5708
    c: Symmetric(g4,g3,g-2)
    c: Symmetric(g2,g1,g-2)
    c: DistanceX(g1) = 13.5322
    c: DistanceY(g1) = -19.2639
    c: Angle(g3) = -0.987729
    c: Angle(g6) = 0.736411
FEATURE [Sketcher::SketchObject] Sketch044
  ArcFitTolerance = 0
  AttachmentSupport = -> [YZ_Plane]
  ExternalGeometry = -> [Binder]
  FullyConstrained = false
  MakeInternals = false
  MapMode = 5
  Placement = pos=(0,0,0) rot=(0.57735,0.57735,0.57735;2.0944rad)
  expr: Constraints[16] = <<Properties>>.total_height
  expr: Constraints[23] = composit_properties#<<Properties>>.bend_r
  expr: Constraints[33] = <<Properties>>.petal_offset
  sketch-geometry (12):
    g0: LineSegment StartX=-41.6284 StartY=0 StartZ=0 EndX=4.96521 EndY=0 EndZ=0
    g1: LineSegment StartX=4.96521 StartY=0 StartZ=0 EndX=4.96521 EndY=512 EndZ=0
    g2: LineSegment StartX=4.96521 StartY=512 StartZ=0 EndX=-41.6284 EndY=512 EndZ=0
    g3: LineSegment StartX=-41.6284 StartY=512 StartZ=0 EndX=-41.6284 EndY=0 EndZ=0
    g4: LineSegment StartX=-41.6284 StartY=1428 StartZ=0 EndX=8.37158 EndY=1428 EndZ=0
    g5: LineSegment StartX=4.96521 StartY=1354 StartZ=0 EndX=-41.6284 EndY=1354 EndZ=0
    g6: LineSegment StartX=-41.6284 StartY=1354 StartZ=0 EndX=-41.6284 EndY=1428 EndZ=0
    g7: ArcOfCircle [constr] CenterX=4.96521 CenterY=0.1 CenterZ=0 NormalX=0 NormalY=0 NormalZ=1 AngleXU=0 Radius=0.1 StartAngle=3.66519 EndAngle=4.71239
    g8: LineSegment [constr] StartX=4.96521 StartY=0 StartZ=0 EndX=6.6679 EndY=0 EndZ=0
    g9: LineSegment [constr] StartX=4.87861 StartY=0.05 StartZ=0 EndX=2.02073 EndY=5 EndZ=0
    g10: LineSegment StartX=8.37158 StartY=1428 StartZ=0 EndX=4.96521 EndY=1424.59 EndZ=0
    g11: LineSegment StartX=4.96521 StartY=1424.59 StartZ=0 EndX=4.96521 EndY=1354 EndZ=0
  constraints (35):
    c: Coincident(g0,g1)
    c: Coincident(g1,g2)
    c: Coincident(g2,g3)
    c: Coincident(g3,g0)
    c: Horizontal(g0)
    c: Horizontal(g2)
    c: Vertical(g1)
    c: Vertical(g3)
    c: PointOnObject(g0,g-1)
    c: Coincident(g4,g10)
    c: Coincident(g11,g5)
    c: Coincident(g5,g6)
    c: Coincident(g6,g4)
    c: Horizontal(g4)
    c: Horizontal(g5)
    c: Vertical(g6)
    c: DistanceY(g4) = 1428
    c: DistanceY(g11,g10) = 74
    c: PointOnObject(g7,g-1)
    c: PointOnObject(g8,g-1)
    c: Tangent(g8,g7) = -1.5708
    c: Tangent(g9,g7) = 1.5708
    c: Angle(g9) = 2.0944
    c: Radius(g7) = 0.1
    c: PointOnObject(g-3,g9)
    c: DistanceY(g9) = 5
    c: PointOnObject(g7,g1)
    c: DistanceY(g1,g11) = 842
    c: Vertical(g2,g5)
    c: DistanceX(g4,g4) = 50
    c: Coincident(g10,g11)
    c: Vertical(g11)
    c: Angle(g10) = -2.35619
    c: DistanceX(g4) = 8.37158
    c: Vertical(g5,g1)
FEATURE [Sketcher::SketchObject] Sketch045
  ArcFitTolerance = 0
  AttachmentSupport = -> [YZ_Plane025]
  FullyConstrained = true
  MakeInternals = false
  MapMode = 5
  Placement = pos=(0,0,0) rot=(0.57735,0.57735,0.57735;2.0944rad)
  expr: Constraints[0] = <<BaseBend010>>.length
  sketch-geometry (5):
    g0: ArcOfCircle CenterX=30 CenterY=-7 CenterZ=0 NormalX=0 NormalY=0 NormalZ=1 AngleXU=0 Radius=5 StartAngle=4.71239 EndAngle=6.28319
    g1: LineSegment StartX=35 StartY=-7 StartZ=0 EndX=35 EndY=-25 EndZ=0
    g2: LineSegment StartX=30 StartY=-12 StartZ=0 EndX=0 EndY=-12 EndZ=0
    g3: LineSegment StartX=35 StartY=-25 StartZ=0 EndX=0 EndY=-25 EndZ=0
    g4: LineSegment StartX=0 StartY=-25 StartZ=0 EndX=0 EndY=-12 EndZ=0
  constraints (14):
    c: DistanceX(g0) = 35
    c: Vertical(g1)
    c: Tangent(g1,g0) = 1.5708
    c: PointOnObject(g2,g-2)
    c: Horizontal(g2)
    c: Coincident(g3,g1)
    c: PointOnObject(g3,g-2)
    c: Horizontal(g3)
    c: Coincident(g4,g3)
    c: Coincident(g4,g2)
    c: Tangent(g2,g0) = 1.5708
    c: DistanceY(g0) = -7
    c: DistanceY(g3) = -25
    c: Radius(g0) = 5
FEATURE [PartDesign::Pocket] Pocket026
  BaseFeature = -> Pocket021
  Direction = (-1,0,0)
  Length = 5
  Length2 = 5
  Midplane = true
  Profile = -> Sketch045
  ReferenceAxis = -> Sketch045 [N_Axis]
  Suppressed = false
  Type = 1
FEATURE [Part::Part2DObjectPython] Circle  label="hole3.4mm"  # Draft 2D object (typed FeaturePython)
  Area = 0
  FirstAngle = 0
  LastAngle = 0
  MakeFace = false
  Placement = pos=(0,0,0) rot=(0,0,1;1.5708rad)
  Radius = 1.7
  expr: Radius = <<Properties>>.rivet_d / 2
FEATURE [Part::FeaturePython] LinearArray005  label="leg_amplifier_fix"  # WARN: FeaturePython — macro-defined, semantics opaque (R4)
  Alignment = 0
  CellStart = A1
  Count = 3
  Dir = (1,0,0)
  DirIsDriven = true
  DistributionLaw = 0
  DrivenProperty = 1
  EndInclusive = true
  ExposePlacement = false
  GeneratorMode = 0
  MarkerShape = 1
  MarkerSize = 0
  NumElements = 3
  OrientMode = 1
  Point = (0,0,0)
  PointIsDriven = true
  Reverse = false
  SpanEnd = 390
  SpanStart = 20
  Step = 185
  Type = lattice2LinearArray.LinearArray
  VSGVersion = 1
  Values = 20.0 | 205.0 | 390.0
  ValuesSource = 2
  isLattice = 1
FEATURE [Part::FeaturePython] Populate007  label="Populate leg_amplifier_fix with hole3.4mm"  # WARN: FeaturePython — macro-defined, semantics opaque (R4)
  Copying = 0
  ExposePlacement = false
  MarkerShape = 1
  MarkerSize = 0
  NumElements = 0
  Object = -> Circle
  OutputCompounding = 1
  PlacementsTo = -> LinearArray005
  Referencing = 0
  Type = lattice2PopulateCopies.LatticePopulateCopies
  isLattice = 0
FEATURE [Part::FeaturePython] LinearArray006  label="part_connector_array"  # WARN: FeaturePython — macro-defined, semantics opaque (R4)
  Alignment = 0
  CellStart = A1
  Count = 5
  Dir = (1,0,0)
  DirIsDriven = true
  DistributionLaw = 0
  DrivenProperty = 1
  EndInclusive = true
  ExposePlacement = false
  GeneratorMode = 0
  MarkerShape = 1
  MarkerSize = 0
  NumElements = 5
  OrientMode = 1
  Point = (0,0,0)
  PointIsDriven = true
  Reverse = false
  SpanEnd = 820
  SpanStart = 0
  Step = 205
  Type = lattice2LinearArray.LinearArray
  VSGVersion = 1
  Values = 0.0 | 205.0 | 410.0 | 615.0 | 820.0
  ValuesSource = 2
  isLattice = 1
FEATURE [Part::FeaturePython] Populate008  label="Populate part_connector with hole3.4mm"  # WARN: FeaturePython — macro-defined, semantics opaque (R4)
  Copying = 0
  ExposePlacement = false
  MarkerShape = 1
  MarkerSize = 0
  NumElements = 0
  Object = -> Circle
  OutputCompounding = 1
  PlacementsTo = -> LinearArray006
  Referencing = 0
  Type = lattice2PopulateCopies.LatticePopulateCopies
  isLattice = 0
FEATURE [Part::Extrusion] Extrude002  label="part_connector_extrude"
  Base = -> Populate008
  Dir = (0,0,1)
  DirMode = 2
  FaceMakerClass = Part::FaceMakerBullseye
  FaceMakerMode = 3
  LengthFwd = 10
  LengthRev = 0
  Placement = pos=(21,-5,1343) rot=(-0.447204,0.774607,0.447204;1.82348rad)
  Solid = true
  Symmetric = false
  expr: .Placement.Base.z = <<Properties>>.total_height - 85 mm
FEATURE [Part::Mirroring] Part__Mirroring009  label="part_connector_extrude (Mirror #10)"
  Base = (0,0,0)
  Normal = (1,0,-1.19209e-07)
  Source = -> Extrude002
FEATURE [Part::Compound] Compound015  label="part_connector"
  Links = -> [Part__Mirroring009,Extrude002]
FEATURE [Part::Extrusion] Extrude003  label="star_amplifier_holes_extrude"
  Base = -> Circle
  Dir = (0,0,1)
  DirMode = 2
  FaceMakerClass = Part::FaceMakerBullseye
  FaceMakerMode = 3
  LengthFwd = 29
  LengthRev = 0
  Placement = pos=(0,19,-7) rot=(0,1,0;1.5708rad)
  Solid = true
  Symmetric = true
  expr: LengthFwd = <<Properties>>.endface_width
FEATURE [Part::Extrusion] Extrude004  label=" leg_amplifier_extrude"
  Base = -> Populate007
  Dir = (0,0,1)
  DirMode = 2
  FaceMakerClass = Part::FaceMakerBullseye
  FaceMakerMode = 3
  LengthFwd = 14.5
  LengthRev = 0
  Placement = pos=(0,245,0) rot=(0,-1,0;1.5708rad)
  Solid = true
  Symmetric = false
  expr: LengthFwd = <<Properties>>.endface_width / 2
FEATURE [Part::FeaturePython] Mirror  label="Mirror of  leg_amplifier_extrude"  # WARN: FeaturePython — macro-defined, semantics opaque (R4)
  ExposePlacement = false
  FlipX = true
  FlipY = false
  FlipZ = false
  MarkerShape = 1
  MarkerSize = 0
  NumElements = 0
  Object = -> Extrude004
  ObjectTraversal = 0
  PivotPlacement = pos=(0,0,0) rot=(0,0,1;4.18879rad)
  Type = lattice2Mirror.LatticeMirror
  isLattice = 0
FEATURE [Part::Compound] Compound018  label="leg_fix_2"
  Links = -> [Extrude004,Mirror]
  Placement = pos=(0,0,0) rot=(0,0,1;2.0944rad)
FEATURE [Part::FeaturePython] LinearArray007  label="plexiglass_bottom_fix_array"  # WARN: FeaturePython — macro-defined, semantics opaque (R4)
  Alignment = 0
  CellStart = A1
  Count = 4
  Dir = (1,0,0)
  DirIsDriven = true
  DistributionLaw = 0
  DrivenProperty = 1
  EndInclusive = true
  ExposePlacement = false
  GeneratorMode = 0
  MarkerShape = 1
  MarkerSize = 0
  NumElements = 4
  OrientMode = 1
  Point = (0,0,0)
  PointIsDriven = true
  Reverse = false
  SpanEnd = 390
  SpanStart = 35
  Step = 118.333
  Type = lattice2LinearArray.LinearArray
  VSGVersion = 1
  Values = 35.0 | 153.33333333333331 | 271.66666666666663 | 390.0
  ValuesSource = 2
  isLattice = 1
FEATURE [Sketcher::SketchObject] Sketch046  label="plexiglass_bottom_fix_sketch"
  ArcFitTolerance = 0
  FullyConstrained = true
  MakeInternals = false
  sketch-geometry (5):
    g0: LineSegment StartX=-26 StartY=1.6 StartZ=0 EndX=-26 EndY=-1.6 EndZ=0
    g1: LineSegment StartX=-26 StartY=-1.6 StartZ=0 EndX=26 EndY=-1.6 EndZ=0
    g2: LineSegment StartX=26 StartY=-1.6 StartZ=0 EndX=26 EndY=1.6 EndZ=0
    g3: LineSegment StartX=26 StartY=1.6 StartZ=0 EndX=-26 EndY=1.6 EndZ=0
    g4: GeomPoint [constr] X=0 Y=0 Z=0
  constraints (12):
    c: Coincident(g0,g1)
    c: Coincident(g1,g2)
    c: Coincident(g2,g3)
    c: Coincident(g3,g0)
    c: Horizontal(g1)
    c: Horizontal(g3)
    c: Vertical(g0)
    c: Vertical(g2)
    c: Symmetric(g1,g0,g4)
    c: Coincident(g4,g-1)
    c: DistanceY(g2,g2) = 3.2  'width'
    c: DistanceX(g3,g3) = 52  'length'
FEATURE [Part::FeaturePython] Populate009  label="Populate plexiglass_bottom_fix_array with plexiglass_bottom_fix_sketch"  # WARN: FeaturePython — macro-defined, semantics opaque (R4)
  Copying = 0
  ExposePlacement = false
  MarkerShape = 1
  MarkerSize = 0
  NumElements = 0
  Object = -> Sketch046
  OutputCompounding = 1
  PlacementsTo = -> LinearArray007
  Referencing = 0
  Type = lattice2PopulateCopies.LatticePopulateCopies
  isLattice = 0
FEATURE [Part::Extrusion] Extrude005  label="plexiglass_bottom_fix_extrude"
  Base = -> Populate009
  Dir = (0,0,1)
  DirMode = 2
  FaceMakerClass = Part::FaceMakerBullseye
  FaceMakerMode = 3
  LengthFwd = 14.5
  LengthRev = 0
  Placement = pos=(0,336,0) rot=(0,-1,0;1.5708rad)
  Solid = true
  Symmetric = false
  expr: LengthFwd = <<Properties>>.endface_width / 2
FEATURE [Part::FeaturePython] Mirror001  label="Mirror001 of plexiglass_bottom_fix_extrude"  # WARN: FeaturePython — macro-defined, semantics opaque (R4)
  ExposePlacement = false
  FlipX = true
  FlipY = false
  FlipZ = false
  MarkerShape = 1
  MarkerSize = 0
  NumElements = 0
  Object = -> Extrude005
  ObjectTraversal = 0
  PivotPlacement = pos=(0,0,0) rot=(0,0,1;2.0944rad)
  Type = lattice2Mirror.LatticeMirror
  isLattice = 0
FEATURE [Part::FeaturePython] Mirror002  label="Mirror002 of plexiglass_bottom_fix_extrude"  # WARN: FeaturePython — macro-defined, semantics opaque (R4)
  ExposePlacement = false
  FlipX = true
  FlipY = false
  FlipZ = false
  MarkerShape = 1
  MarkerSize = 0
  NumElements = 0
  Object = -> Extrude005
  ObjectTraversal = 0
  Type = lattice2Mirror.LatticeMirror
  isLattice = 0
FEATURE [Part::Compound] Compound020
  Links = -> [Extrude005]
  Placement = pos=(0,0,0) rot=(0,0,1;4.18879rad)
FEATURE [Part::Compound] Compound019  label="plexiglass_bottom_fix"
  Links = -> [Mirror001,Mirror002,Compound020]
  Placement = pos=(0,0,0) rot=(0,0,1;4.18879rad)
FEATURE [Part::FeaturePython] LinearArray008  label="top_fix_array"  # WARN: FeaturePython — macro-defined, semantics opaque (R4)
  Alignment = 0
  CellStart = A1
  Count = 3
  Dir = (1,0,0)
  DirIsDriven = true
  DistributionLaw = 0
  DrivenProperty = 1
  EndInclusive = true
  ExposePlacement = false
  GeneratorMode = 0
  MarkerShape = 1
  MarkerSize = 0
  NumElements = 3
  OrientMode = 1
  Placement = pos=(-135.5,0,0) rot=(0,0,1;0rad)
  Point = (0,0,0)
  PointIsDriven = true
  Reverse = false
  SpanEnd = 271
  SpanStart = 0
  Step = 135.5
  Type = lattice2LinearArray.LinearArray
  VSGVersion = 1
  Values = 0.0 | 135.5 | 271.0
  ValuesSource = 2
  isLattice = 1
  expr: .Placement.Base.x = -SpanEnd / 2
FEATURE [Part::FeaturePython] Populate010  label="Populate top_fix_array with hole3.4mm"  # WARN: FeaturePython — macro-defined, semantics opaque (R4)
  Copying = 0
  ExposePlacement = false
  MarkerShape = 1
  MarkerSize = 0
  NumElements = 0
  Object = -> Circle
  OutputCompounding = 1
  PlacementsTo = -> LinearArray008
  Referencing = 0
  Type = lattice2PopulateCopies.LatticePopulateCopies
  isLattice = 0
FEATURE [Part::Extrusion] Extrude006  label="top_fix_extrude"
  Base = -> Populate010
  Dir = (0,0,1)
  DirMode = 2
  FaceMakerClass = Part::FaceMakerBullseye
  FaceMakerMode = 3
  LengthFwd = 29
  LengthRev = 0
  Placement = pos=(0,178.372,-7) rot=(0.57735,0.57735,0.57735;2.0944rad)
  Solid = true
  Symmetric = true
  expr: .Placement.Base.y = <<Properties>>.plane_middle - 3 mm
  expr: LengthFwd = <<Properties>>.endface_width
FEATURE [Part::Compound] Compound022  label="top_fix2"
  Links = -> [Extrude006]
  Placement = pos=(0,0,1428) rot=(0,0,1;0rad)
  expr: .Placement.Base.z = <<Properties>>.total_height
FEATURE [Sketcher::SketchObject] Sketch047
  ArcFitTolerance = 0
  FullyConstrained = true
  MakeInternals = false
  expr: Constraints[13] = <<Properties>>.rivet_d
  sketch-geometry (10):
    g0: LineSegment [constr] StartX=22.7472 StartY=52 StartZ=0 EndX=340 EndY=52 EndZ=0
    g1: LineSegment [constr] StartX=340 StartY=52 StartZ=0 EndX=340 EndY=102 EndZ=0
    g2: LineSegment [constr] StartX=22.7472 StartY=102 StartZ=0 EndX=22.7472 EndY=52 EndZ=0
    g3: Circle [constr] CenterX=22.7472 CenterY=52 CenterZ=0 NormalX=0 NormalY=0 NormalZ=1 AngleXU=0 Radius=1.7
    g4: Circle CenterX=22.7472 CenterY=102 CenterZ=0 NormalX=0 NormalY=0 NormalZ=1 AngleXU=0 Radius=1.7
    g5: Circle CenterX=340 CenterY=102 CenterZ=0 NormalX=0 NormalY=0 NormalZ=1 AngleXU=0 Radius=1.7
    g6: Circle CenterX=340 CenterY=52 CenterZ=0 NormalX=0 NormalY=0 NormalZ=1 AngleXU=0 Radius=1.7
    g7: LineSegment [constr] StartX=340 StartY=102 StartZ=0 EndX=181.374 EndY=102 EndZ=0
    g8: LineSegment [constr] StartX=181.374 StartY=102 StartZ=0 EndX=22.7472 EndY=102 EndZ=0
    g9: Circle CenterX=181.374 CenterY=102 CenterZ=0 NormalX=0 NormalY=0 NormalZ=1 AngleXU=0 Radius=1.7
  constraints (25):
    c: Coincident(g0,g1)
    c: Coincident(g1,g7)
    c: Coincident(g8,g2)
    c: Coincident(g2,g0)
    c: Vertical(g1)
    c: Vertical(g2)
    c: Coincident(g3,g0)
    c: Coincident(g4,g8)
    c: Coincident(g5,g1)
    c: Coincident(g6,g0)
    c: Equal(g3,g4)
    c: Equal(g3,g5)
    c: Equal(g3,g6)
    c: Diameter(g3) = 3.4
    c: DistanceX(g3) = 22.7472
    c: DistanceY(g3) = 52
    c: DistanceY(g4) = 102
    c: DistanceX(g6) = 340
    c: DistanceY(g6) = 52
    c: Coincident(g7,g8)
    c: Horizontal(g7)
    c: Horizontal(g8)
    c: Equal(g8,g7)
    c: Coincident(g9,g7)
    c: Equal(g9,g3)
FEATURE [Part::Extrusion] Extrude007  label="sink_fix_extrude"
  Base = -> Sketch047
  Dir = (0,0,1)
  DirMode = 2
  FaceMakerClass = Part::FaceMakerBullseye
  FaceMakerMode = 3
  LengthFwd = 34
  LengthRev = 0
  Placement = pos=(0,0,0) rot=(0.57735,0.57735,0.57735;2.0944rad)
  Solid = true
  Symmetric = true
  expr: LengthFwd = <<Properties>>.endface_width + 5 mm
FEATURE [Part::Compound] Compound024  label="part1_cut2"
  Links = -> [Extrude004]
FEATURE [Part::Compound] Compound025  label="part2_cut2"
  Links = -> [Compound018]
FEATURE [Part::Compound] Compound026  label="part1_fuse1"
  Links = -> [BaseBend002]
FEATURE [Sketcher::SketchObject] Sketch048
  ArcFitTolerance = 0
  AttachmentSupport = -> [YZ_Plane024]
  FullyConstrained = true
  MakeInternals = false
  MapMode = 5
  Placement = pos=(0,0,0) rot=(0.57735,0.57735,0.57735;2.0944rad)
  expr: Constraints[5] = -<<top_connector_base_sketch>>.Constraints.height
  expr: Constraints[7] = -<<top_connector_base_sketch>>.AttachmentOffset.Base.z
  sketch-geometry (3):
    g0: ArcOfCircle CenterX=42 CenterY=-6 CenterZ=0 NormalX=0 NormalY=0 NormalZ=1 AngleXU=0 Radius=7 StartAngle=3.14159 EndAngle=4.71239
    g1: LineSegment StartX=42 StartY=-13 StartZ=0 EndX=35 EndY=-13 EndZ=0
    g2: LineSegment StartX=35 StartY=-6 StartZ=0 EndX=35 EndY=-13 EndZ=0
  constraints (8):
    c: Horizontal(g1)
    c: Coincident(g2,g1)
    c: Vertical(g2)
    c: Tangent(g1,g0) = 1.5708
    c: Tangent(g2,g0) = -1.5708
    c: DistanceY(g1) = -13
    c: DistanceY(g0) = -6
    c: DistanceX(g1) = 35
FEATURE [Part::FeaturePython] LinearArray009  label="bot_hor_amplifier_fix_array"  # WARN: FeaturePython — macro-defined, semantics opaque (R4)
  Alignment = 0
  CellStart = A1
  Count = 3
  Dir = (1,0,0)
  DirIsDriven = true
  DistributionLaw = 0
  DrivenProperty = 1
  EndInclusive = true
  ExposePlacement = false
  GeneratorMode = 0
  MarkerShape = 1
  MarkerSize = 0
  NumElements = 3
  OrientMode = 1
  Placement = pos=(-120,0,0) rot=(0,0,1;0rad)
  Point = (0,0,0)
  PointIsDriven = true
  Reverse = false
  SpanEnd = 240
  SpanStart = 0
  Step = 120
  Type = lattice2LinearArray.LinearArray
  VSGVersion = 1
  Values = 0.0 | 120.0 | 240.0
  ValuesSource = 2
  isLattice = 1
  expr: .Placement.Base.x = -SpanEnd / 2
FEATURE [Part::FeaturePython] Populate011  label="Populate bot_hor_amplifier_fix_array with hole3.4mm"  # WARN: FeaturePython — macro-defined, semantics opaque (R4)
  Copying = 0
  ExposePlacement = false
  MarkerShape = 1
  MarkerSize = 0
  NumElements = 0
  Object = -> Circle
  OutputCompounding = 1
  PlacementsTo = -> LinearArray009
  Referencing = 0
  Type = lattice2PopulateCopies.LatticePopulateCopies
  isLattice = 0
FEATURE [Sketcher::SketchObject] Sketch049
  ArcFitTolerance = 0
  AttachmentSupport = -> [YZ_Plane030]
  FullyConstrained = true
  MakeInternals = false
  MapMode = 5
  Placement = pos=(0,0,0) rot=(0.57735,0.57735,0.57735;2.0944rad)
  expr: Constraints[11] = <<Properties>>.inner_width
  sketch-geometry (5):
    g0: LineSegment StartX=-11.5 StartY=-14 StartZ=0 EndX=-11.5 EndY=0 EndZ=0
    g1: LineSegment StartX=-11.5 StartY=0 StartZ=0 EndX=11.5 EndY=0 EndZ=0
    g2: LineSegment StartX=11.5 StartY=0 StartZ=0 EndX=11.5 EndY=-14 EndZ=0
    g3: LineSegment [constr] StartX=11.5 StartY=-14 StartZ=0 EndX=-11.5 EndY=-14 EndZ=0
    g4: GeomPoint [constr] X=0 Y=-7 Z=0
  constraints (13):
    c: Coincident(g0,g1)
    c: Coincident(g1,g2)
    c: Coincident(g2,g3)
    c: Coincident(g3,g0)
    c: Horizontal(g1)
    c: Horizontal(g3)
    c: Vertical(g0)
    c: Vertical(g2)
    c: Symmetric(g1,g0,g4)
    c: PointOnObject(g4,g-2)
    c: PointOnObject(g1,g-1)
    c: DistanceX(g1,g1) = 23
    c: DistanceY(g2) = -14
FEATURE [Part::Extrusion] Extrude008  label="bot_hor_amplifier_extrude"
  Base = -> Populate011
  Dir = (0,0,1)
  DirMode = 2
  FaceMakerClass = Part::FaceMakerBullseye
  FaceMakerMode = 3
  LengthFwd = 30
  LengthRev = 0
  Placement = pos=(0,0,-7) rot=(1,0,0;1.5708rad)
  Solid = true
  Symmetric = true
  expr: LengthFwd = <<Properties>>.endface_width + 1 mm
FEATURE [Part::Compound] Compound027
  Links = -> [Extrude007]
  Placement = pos=(0,-16.7432,-18) rot=(0,0,1;1.0472rad)
  expr: .Placement.Base.y = -<<Properties>>.endface_width / 2 / sin(60)
FEATURE [Part::Mirroring] Part__Mirroring010  label="Compound027 (Mirror #11)"
  Base = (0,0,0)
  Normal = (1,0,0)
  Source = -> Compound027
FEATURE [Part::Compound] Compound028  label="sink_fix001"
  Links = -> [Part__Mirroring010,Compound027]
FEATURE [Part::Part2DObjectPython] Circle001  label="hole_8mm"  # Draft 2D object (typed FeaturePython)
  Area = 0
  FirstAngle = 0
  LastAngle = 0
  MakeFace = false
  Radius = 4
FEATURE [Sketcher::SketchObject] Sketch055
  ArcFitTolerance = 0
  ExternalGeometry = -> [Sketch008]
  FullyConstrained = true
  MakeInternals = false
  sketch-geometry (7):
    g0: LineSegment StartX=16.3 StartY=4 StartZ=0 EndX=16.3 EndY=19 EndZ=0
    g1: LineSegment StartX=16.3 StartY=19 StartZ=0 EndX=6.55 EndY=19 EndZ=0
    g2: LineSegment StartX=6.55 StartY=19 StartZ=0 EndX=6.55 EndY=11 EndZ=0
    g3: LineSegment StartX=6.55 StartY=11 StartZ=0 EndX=-6.55 EndY=11 EndZ=0
    g4: LineSegment StartX=-6.55 StartY=11 StartZ=0 EndX=-6.55 EndY=19 EndZ=0
    g5: LineSegment StartX=-6.55 StartY=19 StartZ=0 EndX=-16.3 EndY=19 EndZ=0
    g6: LineSegment StartX=-16.3 StartY=19 StartZ=0 EndX=-16.3 EndY=4 EndZ=0
  constraints (20):
    c: Vertical(g0)
    c: Coincident(g0,g1)
    c: Horizontal(g1)
    c: Coincident(g1,g2)
    c: Vertical(g2)
    c: Coincident(g2,g3)
    c: Coincident(g3,g4)
    c: Coincident(g4,g5)
    c: Horizontal(g5)
    c: Coincident(g5,g6)
    c: Vertical(g6)
    c: DistanceY(g0) = 4
    c: DistanceX(g0,g-3) = 2
    c: DistanceY(g0,g-3) = 0
    c: Symmetric(g0,g5,g-2)
    c: Horizontal(g6,g0)
    c: Symmetric(g2,g3,g-2)
    c: Vertical(g4)
    c: DistanceX(g3,g3) = 13.1
    c: DistanceY(g2,g2) = 8
FEATURE [Part::FeaturePython] LinearArray012  label="led_holder_fix_array"  # WARN: FeaturePython — macro-defined, semantics opaque (R4)
  Alignment = 0
  CellStart = A1
  Count = 5
  Dir = (1,0,0)
  DirIsDriven = true
  DistributionLaw = 0
  DrivenProperty = 1
  EndInclusive = true
  ExposePlacement = false
  GeneratorMode = 0
  MarkerShape = 1
  MarkerSize = 0
  NumElements = 5
  OrientMode = 1
  Point = (0,0,0)
  PointIsDriven = true
  Reverse = false
  SpanEnd = 1093
  SpanStart = 0
  Step = 273.25
  Type = lattice2LinearArray.LinearArray
  VSGVersion = 1
  Values = 0.0 | 273.25 | 546.5 | 819.75 | 1093.0
  ValuesSource = 2
  isLattice = 1
FEATURE [Part::FeaturePython] Populate015  label="Populate led_holder_fix_array with hole3.4mm"  # WARN: FeaturePython — macro-defined, semantics opaque (R4)
  Copying = 0
  ExposePlacement = false
  MarkerShape = 1
  MarkerSize = 0
  NumElements = 0
  Object = -> Circle
  OutputCompounding = 1
  PlacementsTo = -> LinearArray012
  Referencing = 0
  Type = lattice2PopulateCopies.LatticePopulateCopies
  isLattice = 0
FEATURE [Part::Extrusion] Extrude010  label="led_holder_fix_extrude"
  Base = -> Populate015
  Dir = (0,0,1)
  DirMode = 2
  FaceMakerClass = Part::FaceMakerBullseye
  FaceMakerMode = 3
  LengthFwd = 10
  LengthRev = 0
  Placement = pos=(-15,11.8848,1584) rot=(0.707107,0,-0.707107;3.14159rad)
  Solid = true
  Symmetric = false
FEATURE [Sketcher::SketchObject] Sketch056  label="pillar_dec_corner_base_sketch"
  ArcFitTolerance = 0
  ExternalGeometry = -> [Sketch008]
  FullyConstrained = true
  MakeInternals = false
  sketch-geometry (2):
    g0: LineSegment StartX=-18.3 StartY=19 StartZ=0 EndX=-18.3 EndY=-1.5 EndZ=0
    g1: LineSegment StartX=-18.3 StartY=-1.5 StartZ=0 EndX=18.3 EndY=-1.5 EndZ=0
  constraints (5):
    c: Coincident(g-3,g0)
    c: Vertical(g0)
    c: Coincident(g0,g1)
    c: Symmetric(g1,g0,g-2)
    c: DistanceY(g0) = -1.5
FEATURE [PartDesign::SubShapeBinder] Binder035
  BindCopyOnChange = 0
  BindMode = 0
  ClaimChildren = true
  Fuse = false
  MakeFace = true
  OffsetFill = false
  OffsetIntersection = false
  OffsetJoinType = 0
  OffsetOpenResult = false
  PartialLoad = false
  Relative = false
  Support = -> [Sketch056]
  _Version = 2
FEATURE [PartDesign::FeaturePython] BaseBend017  # WARN: FeaturePython — macro-defined, semantics opaque (R4)
  BendSide = 0
  BendSketch = -> Binder035
  MidPlane = false
  Placement = pos=(0,0,481) rot=(0,0,1;0rad)
  Reverse = false
  Suppressed = false
  length = 1113
  radius = 2
  thickness = 0.5
FEATURE [Part::Mirroring] Part__Mirroring011  label="led_holder_fix_extrude (Mirror #12)"
  Base = (0,0,0)
  Normal = (1,0,0)
  Source = -> Extrude010
FEATURE [Part::Compound] Compound033  label="led_holder_fix"
  Links = -> [Extrude010,Part__Mirroring011]
FEATURE [App::Link] Link004  label="hub2108"
  LinkPlacement = pos=(0,0,-90) rot=(0,0,1;0rad)
  LinkedObject = -> <external hub2108.FCStd>#Body
  Placement = pos=(0,0,-90) rot=(0,0,1;0rad)
FEATURE [App::Link] Link005  label="U_fix_material_0.50ansi"
  LinkPlacement = pos=(0,294.4,0) rot=(0,0,1;0rad)
  LinkedObject = -> <external U-fix.FCStd>#Body
  Placement = pos=(0,294.4,0) rot=(0,0,1;0rad)
FEATURE [PartDesign::SubShapeBinder] Binder036
  BindCopyOnChange = 0
  BindMode = 0
  ClaimChildren = true
  Fuse = false
  MakeFace = true
  OffsetFill = false
  OffsetIntersection = false
  OffsetJoinType = 0
  OffsetOpenResult = false
  PartialLoad = false
  Relative = false
  Support = -> [Link005[Binder.]]
  _Version = 2
FEATURE [Part::Extrusion] Extrude011  label="U-fix_vert_holes_extrude"
  Base = -> Binder036
  Dir = (0,1,2e-16)
  DirMode = 2
  FaceMakerClass = Part::FaceMakerBullseye
  FaceMakerMode = 3
  LengthFwd = 29
  LengthRev = 0
  Placement = pos=(0,294.4,0) rot=(0,0,1;1.5708rad)
  Solid = false
  Symmetric = true
  expr: LengthFwd = <<Properties>>.endface_width
FEATURE [Sketcher::SketchObject] Sketch060
  ArcFitTolerance = 0
  FullyConstrained = true
  MakeInternals = false
  expr: Constraints[11] = Sketch.Constraints.max_r + 15 mm
  sketch-geometry (4):
    g0: LineSegment [constr] StartX=0 StartY=0 StartZ=0 EndX=317.979 EndY=183.585 EndZ=0
    g1: LineSegment StartX=0 StartY=380 StartZ=0 EndX=37.5 EndY=380 EndZ=0
    g2: ArcOfCircle CenterX=-35.1249 CenterY=-20.2794 CenterZ=0 NormalX=0 NormalY=0 NormalZ=1 AngleXU=0 Radius=407.729 StartAngle=0.523599 EndAngle=1.36636
    g3: ArcOfCircle CenterX=37.5 CenterY=330 CenterZ=0 NormalX=0 NormalY=0 NormalZ=1 AngleXU=0 Radius=50 StartAngle=1.36636 EndAngle=1.5708
  constraints (12):
    c: Coincident(g0,g-1)
    c: Angle(g0) = 0.523599
    c: PointOnObject(g1,g-2)
    c: Horizontal(g1)
    c: DistanceX(g1,g1) = 37.5
    c: DistanceY(g1) = 380
    c: Coincident(g2,g0)
    c: PointOnObject(g2,g0)
    c: Tangent(g3,g1) = 1.5708
    c: Tangent(g2,g3) = -1.5708
    c: Radius(g3) = 50
    c: Distance(g0) = 367.17
FEATURE [Part::Mirroring] Mirror003  label="Sketch060 (mirrored)"
  Base = (0,0,0)
  Normal = (0.5,-0.866025,0)
  Source = -> Sketch060
  expr: .Normal.x = sin(30)
  expr: .Normal.y = -cos(30)
FEATURE [Sketcher::SketchObject] Sketch061
  ArcFitTolerance = 0
  ExternalGeometry = -> [Sketch060]
  FullyConstrained = true
  MakeInternals = false
  expr: Constraints[7] = (36.6 mm - 8 mm) / 2 + 1 mm
  sketch-geometry (3):
    g0: LineSegment [constr] StartX=0 StartY=380 StartZ=0 EndX=0 EndY=0 EndZ=0
    g1: LineSegment [constr] StartX=0 StartY=0 StartZ=0 EndX=329.09 EndY=-190 EndZ=0
    g2: LineSegment StartX=329.09 StartY=-190 StartZ=0 EndX=321.44 EndY=-203.25 EndZ=0
  constraints (8):
    c: Coincident(g-3,g0)
    c: Coincident(g0,g-1)
    c: Coincident(g0,g1)
    c: Angle(g1) = -0.523599
    c: Equal(g1,g0)
    c: Coincident(g2,g1)
    c: Perpendicular(g1,g2)
    c: Distance(g2) = 15.3
FEATURE [Part::Compound] Compound035
  Links = -> [Mirror003,Sketch061,Sketch060]
FEATURE [Part::Mirroring] Part__Mirroring012  label="Compound035 (Mirror #14)"
  Base = (0,0,0)
  Normal = (1,0,0)
  Source = -> Compound035
FEATURE [Part::Compound] Compound036
  Links = -> [Part__Mirroring012,Compound035]
FEATURE [PartDesign::SubShapeBinder] Binder037
  BindCopyOnChange = 0
  BindMode = 0
  ClaimChildren = true
  Context = -> Body072 [Binder037.]
  Fuse = false
  MakeFace = true
  OffsetFill = false
  OffsetIntersection = false
  OffsetJoinType = 0
  OffsetOpenResult = false
  PartialLoad = false
  Relative = false
  Support = -> [Compound036]
  _Version = 2
FEATURE [PartDesign::FeaturePython] BaseBend018  # WARN: FeaturePython — macro-defined, semantics opaque (R4)
  BendSide = 1
  BendSketch = -> Binder037
  MidPlane = false
  Placement = pos=(0,0,1596) rot=(0,0,1;0rad)
  Reverse = true
  Suppressed = false
  length = 1203
  radius = 1
  thickness = 1.5
FEATURE [PartDesign::FeaturePython] BaseBend019  # WARN: FeaturePython — macro-defined, semantics opaque (R4)
  BendSide = 0
  BendSketch = -> Sketch049
  MidPlane = true
  Reverse = false
  Suppressed = false
  length = 250
  radius = 0.1
  thickness = 0.3
FEATURE [Sketcher::SketchObject] Sketch062
  ArcFitTolerance = 0
  AttachmentSupport = -> [XY_Plane036]
  FullyConstrained = true
  MakeInternals = false
  MapMode = 5
  expr: Constraints[3] = <<Properties>>.endface_width / 2 + 0.5 mm
  sketch-geometry (7):
    g0: LineSegment StartX=61.9452 StartY=297.209 StartZ=0 EndX=15 EndY=280 EndZ=0
    g1: LineSegment StartX=15 StartY=280 StartZ=0 EndX=15 EndY=335 EndZ=0
    g2: LineSegment StartX=15 StartY=335 StartZ=0 EndX=62.031 EndY=297.743 EndZ=0
    g3: LineSegment [constr] StartX=61.9452 StartY=297.209 StartZ=0 EndX=62.4647 EndY=297.399 EndZ=0
    g4: LineSegment [constr] StartX=62.4647 StartY=297.399 StartZ=0 EndX=62.031 EndY=297.743 EndZ=0
    g5: LineSegment [constr] StartX=61.9452 StartY=297.209 StartZ=0 EndX=61.8385 EndY=297.5 EndZ=0
    g6: LineSegment [constr] StartX=61.8385 StartY=297.5 StartZ=0 EndX=62.031 EndY=297.743 EndZ=0
  constraints (20):
    c: Coincident(g0,g1)
    c: Vertical(g1)
    c: Coincident(g1,g2)
    c: DistanceX(g1) = 15
    c: Distance(g1) = 55
    c: Distance(g2) = 60
    c: Distance(g0) = 50
    c: Coincident(g3,g0)
    c: Coincident(g4,g3)
    c: Coincident(g4,g2)
    c: Parallel(g0,g3)
    c: Parallel(g4,g2)
    c: Equal(g3,g4)
    c: Coincident(g0,g5)
    c: Coincident(g5,g6)
    c: Coincident(g6,g2)
    c: Perpendicular(g3,g5)
    c: Perpendicular(g4,g6)
    c: Distance(g5) = 0.31
    c: DistanceY(g1) = 335
FEATURE [PartDesign::FeaturePython] BaseBend020  # WARN: FeaturePython — macro-defined, semantics opaque (R4)
  BendSide = 0
  BendSketch = -> Sketch062
  MidPlane = false
  Reverse = false
  Suppressed = false
  length = 413
  radius = 0.1
  thickness = 0.3
  expr: radius = composit_properties#<<Properties>>.bend_r
  expr: thickness = composit_properties#<<Properties>>.al_thickness
FEATURE [PartDesign::FeaturePython] Bend009  # WARN: FeaturePython — macro-defined, semantics opaque (R4)
  AutoMiter = true
  BaseFeature = -> BaseBend020
  BendType = 0
  LengthList = [15]
  LengthSpec = 0
  NonperforationMaxLength = 5
  Perforate = false
  PerforationAngle = 0
  PerforationInitialLength = 5
  PerforationMaxLength = 5
  ReliefFactor = 0.7
  Suppressed = false
  UseReliefFactor = false
  angle = 90
  baseObject = -> BaseBend020 [Edge17,Edge4,Edge33,Edge32,Edge16,Edge3]
  bendAList = [90]
  extend1 = 0
  extend2 = 0
  gap1 = 0
  gap2 = 0
  invert = true
  kfactor = 0.5
  length = 15
  maxExtendDist = 5
  minGap = 0.1
  minReliefGap = 1
  miterangle1 = 0
  miterangle2 = 0
  offset = 0
  radius = 0.1
  reliefType = 0
  reliefd = 1
  reliefw = 0.8
  sketchflip = false
  sketchinvert = false
  unfold = false
  expr: radius = BaseBend020.radius
FEATURE [Sketcher::SketchObject] Sketch063
  ArcFitTolerance = 0
  ExternalGeometry = -> [Sketch062]
  FullyConstrained = true
  MakeInternals = false
  sketch-geometry (8):
    g0: LineSegment StartX=15 StartY=281.556 StartZ=0 EndX=15 EndY=328.796 EndZ=0
    g1: LineSegment StartX=19.8629 StartY=331.148 StartZ=0 EndX=62.031 EndY=297.743 EndZ=0
    g2: LineSegment [constr] StartX=0 StartY=0 StartZ=0 EndX=212.95 EndY=122.947 EndZ=0
    g3: ArcOfCircle CenterX=-320.353 CenterY=-184.956 CenterZ=0 NormalX=0 NormalY=0 NormalZ=1 AngleXU=0 Radius=615.805 StartAngle=0.523599 EndAngle=0.900842
    g4: ArcOfCircle CenterX=-305.711 CenterY=-176.502 CenterZ=0 NormalX=0 NormalY=0 NormalZ=1 AngleXU=0 Radius=557.898 StartAngle=0.523599 EndAngle=0.955586
    g5: ArcOfCircle CenterX=18 CenterY=328.796 CenterZ=0 NormalX=0 NormalY=0 NormalZ=1 AngleXU=0 Radius=3 StartAngle=0.900842 EndAngle=3.14159
    g6: GeomPoint [constr] X=15 Y=335 Z=0
    g7: ArcOfCircle CenterX=18 CenterY=281.556 CenterZ=0 NormalX=0 NormalY=0 NormalZ=1 AngleXU=0 Radius=3 StartAngle=3.14159 EndAngle=4.09718
  constraints (20):
    c: Coincident(g6,g-4)
    c: Coincident(g1,g-3)
    c: Coincident(g2,g-1)
    c: Angle(g2) = 0.523599
    c: Coincident(g3,g2)
    c: PointOnObject(g4,g2)
    c: Perpendicular(g4,g2)
    c: Perpendicular(g3,g2)
    c: Tangent(g3,g1) = 1.5708
    c: PointOnObject(g6,g0)
    c: PointOnObject(g6,g1)
    c: Tangent(g0,g5) = 1.5708
    c: Tangent(g1,g5) = 1.5708
    c: Tangent(g4,g7) = 1.5708
    c: Tangent(g0,g7) = 1.5708
    c: PointOnObject(g-4,g4)
    c: PointOnObject(g-4,g0)
    c: Equal(g7,g5)
    c: Radius(g7) = 3
    c: Distance(g4,g3) = 41
FEATURE [Part::Mirroring] Mirror004  label="Sketch063 (mirrored)"
  Base = (0,0,0)
  Normal = (0.5,-0.866025,0)
  Source = -> Sketch063
  expr: .Normal.x = cos(-60)
  expr: .Normal.y = sin(-60)
FEATURE [Part::Compound] Compound037
  Links = -> [Sketch063,Mirror004]
FEATURE [PartDesign::SubShapeBinder] Binder038
  BindCopyOnChange = 0
  BindMode = 0
  ClaimChildren = true
  Context = -> Body074 [Binder038.]
  Fuse = false
  MakeFace = true
  OffsetFill = false
  OffsetIntersection = false
  OffsetJoinType = 0
  OffsetOpenResult = false
  PartialLoad = false
  Relative = true
  Support = -> [Compound037]
  _Version = 2
FEATURE [PartDesign::Pad] Pad008
  Direction = (0,0,1)
  Length = 3
  Length2 = 10
  Profile = -> Binder038
  Suppressed = false
  Type = 0
FEATURE [Sketcher::SketchObject] Sketch064
  ArcFitTolerance = 0
  AttachmentSupport = -> [Local_CS]
  FullyConstrained = true
  MakeInternals = false
  MapMode = 5
  Placement = pos=(0,0,0) rot=(1,0,0;0.113192rad)
  expr: Constraints[3] = <<Properties>>.rivet_d
  sketch-geometry (4):
    g0: Circle CenterX=-88.3 CenterY=228.865 CenterZ=0 NormalX=0 NormalY=0 NormalZ=1 AngleXU=0 Radius=1.7
    g1: Circle CenterX=88.3 CenterY=228.865 CenterZ=0 NormalX=0 NormalY=0 NormalZ=1 AngleXU=0 Radius=1.7
    g2: Circle CenterX=261.291 CenterY=193.3 CenterZ=0 NormalX=0 NormalY=0 NormalZ=1 AngleXU=0 Radius=1.7
    g3: Circle CenterX=-261.291 CenterY=193.3 CenterZ=0 NormalX=0 NormalY=0 NormalZ=1 AngleXU=0 Radius=1.7
  constraints (10):
    c: Equal(g2,g1)
    c: Equal(g2,g0)
    c: Equal(g2,g3)
    c: Diameter(g2) = 3.4
    c: DistanceX(g1) = 88.3
    c: DistanceY(g1) = 228.865
    c: DistanceX(g2) = 261.291
    c: DistanceY(g2) = 193.3
    c: Symmetric(g0,g1,g-2)
    c: Symmetric(g3,g2,g-2)
FEATURE [Sketcher::SketchObject] Sketch066
  ArcFitTolerance = 0
  AttachmentSupport = -> [XY_Plane016]
  FullyConstrained = true
  MakeInternals = false
  MapMode = 5
  expr: Constraints[6] = <<Properties>>.rivet_d
  sketch-geometry (3):
    g0: Circle CenterX=0 CenterY=35 CenterZ=0 NormalX=0 NormalY=0 NormalZ=1 AngleXU=0 Radius=1.7
    g1: Circle CenterX=25 CenterY=60 CenterZ=0 NormalX=0 NormalY=0 NormalZ=1 AngleXU=0 Radius=1.7
    g2: Circle CenterX=-25 CenterY=60 CenterZ=0 NormalX=0 NormalY=0 NormalZ=1 AngleXU=0 Radius=1.7
  constraints (8):
    c: PointOnObject(g0,g-2)
    c: DistanceY(g0) = 35
    c: DistanceX(g1) = 25
    c: DistanceY(g1) = 60
    c: Equal(g0,g1)
    c: Equal(g0,g2)
    c: Diameter(g0) = 3.4
    c: Symmetric(g2,g1,g-2)
FEATURE [Sketcher::SketchObject] Sketch067
  ArcFitTolerance = 0
  AttachmentSupport = -> [XY_Plane016]
  FullyConstrained = true
  MakeInternals = false
  MapMode = 5
  sketch-geometry (13):
    g0: LineSegment StartX=-8.5 StartY=28 StartZ=0 EndX=-8.5 EndY=0 EndZ=0
    g1: LineSegment StartX=-8.5 StartY=0 StartZ=0 EndX=8.5 EndY=0 EndZ=0
    g2: LineSegment StartX=8.5 StartY=28 StartZ=0 EndX=-8.5 EndY=28 EndZ=0
    g3: GeomPoint [constr] X=0 Y=14 Z=0
    g4: LineSegment StartX=8.5 StartY=0 StartZ=0 EndX=14 EndY=0 EndZ=0
    g5: LineSegment StartX=8.5 StartY=20.9904 StartZ=0 EndX=8.5 EndY=28 EndZ=0
    g6: ArcOfCircle CenterX=8.5 CenterY=8 CenterZ=0 NormalX=0 NormalY=0 NormalZ=1 AngleXU=0 Radius=7.5 StartAngle=0 EndAngle=1.0472
    g7: ArcOfCircle CenterX=16 CenterY=20.9904 CenterZ=0 NormalX=0 NormalY=0 NormalZ=1 AngleXU=0 Radius=7.5 StartAngle=3.14159 EndAngle=4.18879
    g8: LineSegment StartX=14 StartY=0 StartZ=0 EndX=14 EndY=4 EndZ=0
    g9: LineSegment [constr] StartX=14 StartY=4 StartZ=0 EndX=14 EndY=10 EndZ=0
    g10: LineSegment StartX=16 StartY=6 StartZ=0 EndX=16 EndY=8 EndZ=0
    g11: ArcOfCircle CenterX=15 CenterY=4 CenterZ=0 NormalX=0 NormalY=0 NormalZ=1 AngleXU=0 Radius=1 StartAngle=1.5708 EndAngle=3.14159
    g12: ArcOfCircle CenterX=15 CenterY=6 CenterZ=0 NormalX=0 NormalY=0 NormalZ=1 AngleXU=0 Radius=1 StartAngle=4.71239 EndAngle=6.28319
  constraints (34):
    c: Coincident(g0,g1)
    c: Coincident(g1,g4)
    c: Coincident(g5,g2)
    c: Coincident(g2,g0)
    c: Horizontal(g1)
    c: Vertical(g0)
    c: Symmetric(g1,g0,g3)
    c: PointOnObject(g3,g-2)
    c: PointOnObject(g1,g-1)
    c: DistanceX(g2,g2) = 17
    c: DistanceY(g4,g5) = 28
    c: Coincident(g4,g8)
    c: Vertical(g5)
    c: Horizontal(g4)
    c: DistanceX(g4,g4) = 5.5
    c: DistanceY(g8,g9) = 10
    c: Symmetric(g2,g0,g-2)
    c: Tangent(g7,g6) = 1.5708
    c: Tangent(g7,g5) = 1.5708
    c: PointOnObject(g6,g5)
    c: Equal(g6,g7)
    c: Coincident(g8,g9)
    c: Vertical(g8)
    c: Vertical(g9)
    c: DistanceY(g8,g8) = 4
    c: Vertical(g10)
    c: DistanceX(g10) = 16
    c: Tangent(g11,g8) = 1.5708
    c: Tangent(g12,g11) = 1.5708
    c: Tangent(g12,g10) = -1.5708
    c: Equal(g12,g11)
    c: Tangent(g6,g10) = -1.5708
    c: Vertical(g11,g11)
    c: DistanceY(g10,g10) = 2
FEATURE [Sketcher::SketchObject] Sketch068  label="hat1_sketch"
  ArcFitTolerance = 0
  FullyConstrained = true
  MakeInternals = false
  sketch-geometry (8):
    g0: LineSegment [constr] StartX=0 StartY=0 StartZ=0 EndX=112.627 EndY=65.0251 EndZ=0
    g1: GeomPoint [constr] X=36 Y=353 Z=0
    g2: ArcOfCircle CenterX=34 CenterY=351 CenterZ=0 NormalX=0 NormalY=0 NormalZ=1 AngleXU=0 Radius=2 StartAngle=-1.07e-14 EndAngle=1.80501
    g3: LineSegment StartX=0 StartY=350 StartZ=0 EndX=8.5 EndY=350 EndZ=0
    g4: ArcOfCircle CenterX=8.5 CenterY=457.875 CenterZ=0 NormalX=0 NormalY=0 NormalZ=1 AngleXU=0 Radius=107.875 StartAngle=4.71239 EndAngle=4.94661
    g5: LineSegment [constr] StartX=34 StartY=353 StartZ=0 EndX=36 EndY=353 EndZ=0
    g6: ArcOfCircle CenterX=607.95 CenterY=351 CenterZ=0 NormalX=0 NormalY=0 NormalZ=1 AngleXU=0 Radius=571.95 StartAngle=3.14159 EndAngle=3.66519
    g7: LineSegment [constr] StartX=36 StartY=351 StartZ=0 EndX=36 EndY=353 EndZ=0
  constraints (23):
    c: DistanceX(g1) = 36
    c: DistanceY(g1) = 353
    c: Coincident(g0,g-1)
    c: Angle(g0) = 0.523599
    c: PointOnObject(g3,g-2)
    c: Horizontal(g3)
    c: DistanceX(g3,g3) = 8.5
    c: DistanceY(g3) = 350
    c: Tangent(g4,g2) = 1.5708
    c: PointOnObject(g5,g2)
    c: Coincident(g5,g1)
    c: Horizontal(g5)
    c: Tangent(g5,g2)
    c: Tangent(g4,g3) = -1.5708
    c: Radius(g2) = 2
    c: Distance(g0) = 130.05
    c: Coincident(g6,g0)
    c: Tangent(g6,g2) = 1.5708
    c: Horizontal(g2,g2)
    c: Perpendicular(g6,g0)
    c: Coincident(g7,g2)
    c: Coincident(g7,g1)
    c: Vertical(g7)
FEATURE [Sketcher::SketchObject] Sketch070
  ArcFitTolerance = 0
  AttachmentSupport = -> [XY_Plane015]
  FullyConstrained = true
  MakeInternals = false
  MapMode = 5
  sketch-geometry (2):
    g0: Circle CenterX=-40 CenterY=-12 CenterZ=0 NormalX=0 NormalY=0 NormalZ=1 AngleXU=0 Radius=2.75
    g1: Circle CenterX=40 CenterY=-12 CenterZ=0 NormalX=0 NormalY=0 NormalZ=1 AngleXU=0 Radius=2.75
  constraints (5):
    c: Equal(g1,g0)
    c: Diameter(g1) = 5.5
    c: Symmetric(g0,g1,g-2)
    c: DistanceX(g0,g1) = 80
    c: DistanceY(g1) = -12
FEATURE [Part::Mirroring] Part__Mirroring013  label="Sketch068 (Mirror #16)"
  Base = (0,0,0)
  Normal = (1,0,0)
  Source = -> Sketch068
FEATURE [Part::Compound] Compound039
  Links = -> [Part__Mirroring013,Sketch068]
FEATURE [Part::FeaturePython] Array005  # Draft array (typed FeaturePython)
  AlwaysSyncPlacement = false
  Angle = 360
  ArrayType = 1
  Axis = (0,0,1)
  Base = -> Compound039
  Center = (0,0,0)
  Count = 3
  ExpandArray = false
  Fuse = false
  IntervalAxis = (0,0,0)
  IntervalX = (50,0,0)
  IntervalY = (0,50,0)
  IntervalZ = (0,0,50)
  NumberCircles = 3
  NumberPolar = 3
  NumberX = 2
  NumberY = 2
  NumberZ = 1
  PlacementList = 3 placements: [(0,0,0),(0,0,0),(0,0,0)]
  RadialDistance = 50
  ScaleList = (3) [(1,1,1),(1,1,1),(1,1,1)]
  Symmetry = 1
  TangentialDistance = 25
FEATURE [PartDesign::SubShapeBinder] Binder039
  BindCopyOnChange = 0
  BindMode = 0
  ClaimChildren = true
  Context = -> Body075 [Binder039.]
  Fuse = false
  MakeFace = true
  OffsetFill = false
  OffsetIntersection = false
  OffsetJoinType = 0
  OffsetOpenResult = false
  PartialLoad = false
  Relative = false
  Support = -> [Array005]
  _Version = 2
FEATURE [PartDesign::Pad] Pad009
  Direction = (0,0,1)
  Length = 0.3
  Length2 = 10
  Profile = -> Binder039
  Suppressed = false
  Type = 0
FEATURE [PartDesign::SubShapeBinder] Binder040
  BindCopyOnChange = 0
  BindMode = 0
  ClaimChildren = true
  Context = -> Part010 [Body075.Binder040.]
  Fuse = false
  MakeFace = true
  OffsetFill = false
  OffsetIntersection = false
  OffsetJoinType = 0
  OffsetOpenResult = false
  PartialLoad = false
  Placement = pos=(0,382,0) rot=(0,0,1;3.14159rad)
  Relative = false
  Support = -> [Sketch066]
  _Version = 2
  expr: Support = Sketch066._self
FEATURE [PartDesign::Pocket] Pocket032
  BaseFeature = -> Pad009
  Direction = (0,0,-1)
  Length = 5
  Length2 = 5
  Midplane = true
  Profile = -> Binder040
  Suppressed = false
  Type = 1
FEATURE [Sketcher::SketchObject] Sketch071  label="hat2_sketch"
  ArcFitTolerance = 0
  ExternalGeometry = -> [Sketch068]
  FullyConstrained = true
  MakeInternals = false
  sketch-geometry (13):
    g0: LineSegment StartX=36 StartY=353 StartZ=0 EndX=36 EndY=376.5 EndZ=0
    g1: LineSegment StartX=0 StartY=381.5 StartZ=0 EndX=31 EndY=381.5 EndZ=0
    g2: ArcOfCircle CenterX=31 CenterY=376.5 CenterZ=0 NormalX=0 NormalY=0 NormalZ=1 AngleXU=0 Radius=5 StartAngle=2e-15 EndAngle=1.5708
    g3: GeomPoint [constr] X=36 Y=381.5 Z=0
    g4: ArcOfEllipse CenterX=243.039 CenterY=353 CenterZ=0 NormalX=0 NormalY=0 NormalZ=1 MajorRadius=395.482 MinorRadius=207.039 AngleXU=1.5708 StartAngle=1.5708 EndAngle=2.40506
    g5: LineSegment [constr] StartX=243.039 StartY=748.482 StartZ=0 EndX=243.039 EndY=-42.4822 EndZ=0
    g6: LineSegment [constr] StartX=36 StartY=353 StartZ=0 EndX=450.077 EndY=353 EndZ=0
    g7: GeomPoint [constr] X=243.039 Y=689.959 Z=0
    g8: GeomPoint [constr] X=243.039 Y=16.0414 Z=0
    g9: LineSegment [constr] StartX=103.966 StartY=60.0251 StartZ=0 EndX=112.627 EndY=65.0251 EndZ=0
    g10: GeomPoint [constr] X=103.966 Y=60.0251 Z=0
    g11: ArcOfCircle [constr] CenterX=34 CenterY=351 CenterZ=0 NormalX=0 NormalY=0 NormalZ=1 AngleXU=0 Radius=2 StartAngle=5.8e-15 EndAngle=1.80501
    g12: LineSegment [constr] StartX=34 StartY=353 StartZ=0 EndX=36 EndY=353 EndZ=0
  constraints (26):
    c: Vertical(g0)
    c: DistanceY(g3) = 381.5
    c: PointOnObject(g1,g-2)
    c: Horizontal(g1)
    c: PointOnObject(g3,g0)
    c: PointOnObject(g3,g1)
    c: Tangent(g0,g2) = -1.5708
    c: Tangent(g1,g2) = 1.5708
    c: Radius(g2) = 5
    c: InternalAlignment(g5-g8 -> g4) x4
    c: Horizontal(g6)
    c: Coincident(g9,g4)
    c: Coincident(g9,g-4)
    c: PointOnObject(g-1,g9)
    c: PointOnObject(g10,g4)
    c: PointOnObject(g10,g9)
    c: Perpendicular(g4,g9,g10) = 1.5708
    c: Coincident(g4,g0)
    c: PointOnObject(g-4,g0)
    c: Distance(g9) = 10
    c: Coincident(g11,g-3)
    c: Tangent(g11,g-4) = 1.5708
    c: Coincident(g12,g0)
    c: Horizontal(g12)
    c: Tangent(g12,g11) = 1.5708
    c: Horizontal(g6,g0)
FEATURE [Part::Mirroring] Part__Mirroring014  label="hat2_sketch (Mirror #17)"
  Base = (0,0,0)
  Normal = (1,0,0)
  Source = -> Sketch071
FEATURE [Part::Compound] Compound040  label="hat2_sketch_compound"
  Links = -> [Part__Mirroring014,Sketch071]
FEATURE [Part::FeaturePython] Array006  label="hat2_pad_base"  # Draft array (typed FeaturePython)
  AlwaysSyncPlacement = false
  Angle = 360
  ArrayType = 1
  Axis = (0,0,1)
  Base = -> Compound040
  Center = (0,0,0)
  Count = 3
  ExpandArray = false
  Fuse = false
  IntervalAxis = (0,0,0)
  IntervalX = (50,0,0)
  IntervalY = (0,50,0)
  IntervalZ = (0,0,50)
  NumberCircles = 3
  NumberPolar = 3
  NumberX = 2
  NumberY = 2
  NumberZ = 1
  PlacementList = 3 placements: [(0,0,0),(0,0,0),(0,0,0)]
  RadialDistance = 50
  ScaleList = (3) [(1,1,1),(1,1,1),(1,1,1)]
  Symmetry = 1
  TangentialDistance = 25
FEATURE [PartDesign::SubShapeBinder] Binder041
  BindCopyOnChange = 0
  BindMode = 0
  ClaimChildren = true
  Context = -> Body076 [Binder041.]
  Fuse = false
  MakeFace = true
  OffsetFill = false
  OffsetIntersection = false
  OffsetJoinType = 0
  OffsetOpenResult = false
  PartialLoad = false
  Relative = false
  Support = -> [Array006]
  _Version = 2
FEATURE [PartDesign::Pad] Pad010
  Direction = (0,0,1)
  Length = 0.3
  Length2 = 10
  Profile = -> Binder041
  Suppressed = false
  Type = 0
FEATURE [Sketcher::SketchObject] Sketch072
  ArcFitTolerance = 0
  AttachmentSupport = -> [XY_Plane039]
  FullyConstrained = true
  MakeInternals = false
  MapMode = 5
  sketch-geometry (3):
    g0: Circle CenterX=122.567 CenterY=-102.846 CenterZ=0 NormalX=0 NormalY=0 NormalZ=1 AngleXU=0 Radius=15
    g1: Circle CenterX=-122.567 CenterY=-102.846 CenterZ=0 NormalX=0 NormalY=0 NormalZ=1 AngleXU=0 Radius=15
    g2: LineSegment [constr] StartX=0 StartY=0 StartZ=0 EndX=122.567 EndY=-102.846 EndZ=0
  constraints (7):
    c: Coincident(g2,g-1)
    c: Coincident(g2,g0)
    c: Angle(g2) = -0.698132
    c: Symmetric(g1,g0,g-2)
    c: Equal(g0,g1)
    c: Distance(g2) = 160
    c: Diameter(g0) = 30
FEATURE [Sketcher::SketchObject] Sketch073
  ArcFitTolerance = 0
  AttachmentSupport = -> [YZ_Plane016]
  FullyConstrained = true
  MakeInternals = false
  MapMode = 5
  Placement = pos=(0,0,0) rot=(0.57735,0.57735,0.57735;2.0944rad)
  expr: Constraints[5] = <<Properties>>.rivet_d
  sketch-geometry (2):
    g0: Circle CenterX=10 CenterY=80 CenterZ=0 NormalX=0 NormalY=0 NormalZ=1 AngleXU=0 Radius=1.7
    g1: Circle CenterX=10 CenterY=10 CenterZ=0 NormalX=0 NormalY=0 NormalZ=1 AngleXU=0 Radius=1.7
  constraints (6):
    c: Vertical(g1,g0)
    c: DistanceX(g1) = 10
    c: DistanceY(g0) = 80
    c: DistanceY(g1) = 10
    c: Equal(g1,g0)
    c: Diameter(g1) = 3.4
FEATURE [Part::FeaturePython] Placment002  label="top_placement"  # WARN: FeaturePython — macro-defined, semantics opaque (R4)
  AttacherType = Attacher::AttachEngine3D
  ExposePlacement = true
  MarkerShape = 1
  MarkerSize = 10
  NumElements = 1
  Type = lattice2AttachablePlacement.AttachablePlacement
  isLattice = 1
FEATURE [Part::FeaturePython] Placment004  label="pillar_dec_corner_placement"  # WARN: FeaturePython — macro-defined, semantics opaque (R4)
  AttacherType = Attacher::AttachEngine3D
  ExposePlacement = true
  MarkerShape = 1
  MarkerSize = 50
  NumElements = 1
  Type = lattice2AttachablePlacement.AttachablePlacement
  isLattice = 1
FEATURE [Part::FeaturePython] Placment005  label="pillar_top_dec_corner_placement"  # WARN: FeaturePython — macro-defined, semantics opaque (R4)
  AttacherType = Attacher::AttachEngine3D
  ExposePlacement = true
  MarkerShape = 1
  MarkerSize = 50
  NumElements = 1
  Type = lattice2AttachablePlacement.AttachablePlacement
  isLattice = 1
FEATURE [Part::FeaturePython] PolarArray  # WARN: FeaturePython — macro-defined, semantics opaque (R4)
  Alignment = 0
  AttacherType = Attacher::AttachEngine3D
  CellStart = A1
  Count = 3
  DistributionLaw = 0
  EndInclusive = false
  ExposePlacement = false
  FlipX = false
  FlipZ = false
  GeneratorMode = 0
  MarkerShape = 1
  MarkerSize = 0
  NumElements = 3
  OrientMode = 2
  Radius = 50
  Reverse = false
  SpanEnd = 360
  SpanStart = 0
  Step = 120
  Type = lattice2PolarArray2.PolarArray
  UseArcRadius = false
  UseArcRange = 0
  VSGVersion = 1
  Values = 0.0 | 120.0 | 240.0
  ValuesSource = 2
  isLattice = 1
FEATURE [PartDesign::SubShapeBinder] Binder042  label="led_holes"
  BindCopyOnChange = 0
  BindMode = 0
  ClaimChildren = true
  Fuse = false
  MakeFace = false
  OffsetFill = false
  OffsetIntersection = false
  OffsetJoinType = 0
  OffsetOpenResult = false
  PartialLoad = false
  Relative = true
  Support = -> [<external ULY-P91-20W.FCStd>#Sketch001]
  _Version = 2
FEATURE [Part::FeaturePython] Placment006  label="Custom"  # WARN: FeaturePython — macro-defined, semantics opaque (R4)
  ExposePlacement = true
  FlipZ = false
  Invert = false
  MarkerShape = 1
  MarkerSize = 20
  NumElements = 1
  Placement = pos=(-89,0,0) rot=(0,0,1;0rad)
  PlacementChoice = 0
  Type = lattice2Placement.LatticePlacement
  isLattice = 1
FEATURE [Part::FeaturePython] Join  label="plexiglass_fix_base"  # WARN: FeaturePython — macro-defined, semantics opaque (R4)
  ExposePlacement = false
  Interleave = false
  Links = -> [Placment006,LinearArray012]
  MarkerShape = 1
  MarkerSize = 0
  NumElements = 6
  Type = lattice2JoinArrays.JoinArrays
  isLattice = 1
FEATURE [Part::FeaturePython] Populate017  label="Populate plexiglass_fix_base with hole3.4mm"  # WARN: FeaturePython — macro-defined, semantics opaque (R4)
  Copying = 0
  ExposePlacement = false
  MarkerShape = 1
  MarkerSize = 0
  NumElements = 0
  Object = -> Circle
  OutputCompounding = 1
  PlacementsTo = -> Join
  Referencing = 0
  Type = lattice2PopulateCopies.LatticePopulateCopies
  isLattice = 0
FEATURE [PartDesign::SubShapeBinder] Binder043  label="plexiglass_fix"
  BindCopyOnChange = 0
  BindMode = 0
  ClaimChildren = true
  Fuse = true
  MakeFace = true
  OffsetFill = false
  OffsetIntersection = false
  OffsetJoinType = 0
  OffsetOpenResult = false
  PartialLoad = false
  Relative = false
  Support = -> [Populate017,Compound041]
  _Version = 2
FEATURE [Part::Extrusion] Extrude014  label="plexiglass_fix_extrude"
  Base = -> Binder043
  Dir = (0,0,1)
  DirMode = 2
  FaceMakerClass = Part::FaceMakerBullseye
  FaceMakerMode = 3
  LengthFwd = 50
  LengthRev = 0
  Placement = pos=(0,10,1584) rot=(0.57735,0.57735,-0.57735;2.0944rad)
  Solid = true
  Symmetric = false
FEATURE [Part::Compound] Compound034  label="pillar_common_cut"
  Links = -> [Compound033,Extrude014]
FEATURE [Part::Compound] Compound030  label="pillar_cut1"
  Links = -> [Extrude010,Compound034]
FEATURE [Part::Compound] Compound032  label="dec_corner_cut1"
  Links = -> [Compound034]
FEATURE [Sketcher::SketchObject] Sketch074
  ArcFitTolerance = 0
  ExternalGeometry = -> [Binder042]
  FullyConstrained = true
  MakeInternals = false
  sketch-geometry (1):
    g0: Circle CenterX=-12.5 CenterY=0 CenterZ=0 NormalX=0 NormalY=0 NormalZ=1 AngleXU=0 Radius=1.8
  constraints (2):
    c: Symmetric(g0,g-3,g-2)
    c: Equal(g0,g-3)
FEATURE [Part::Compound] Compound041
  Links = -> [Binder042,Sketch074]
  Placement = pos=(-21,0,0) rot=(0,0,1;1.5708rad)
FEATURE [Part::Compound] Compound042
  Links = -> [Extrude014]
  Placement = pos=(0,384,0) rot=(0,0,1;3.14159rad)
  expr: Placement = <<pillar_placement>>.Placement
FEATURE [Part::FeaturePython] Populate018  label="Populate PolarArray with Compound042"  # WARN: FeaturePython — macro-defined, semantics opaque (R4)
  Copying = 0
  ExposePlacement = false
  MarkerShape = 1
  MarkerSize = 0
  NumElements = 0
  Object = -> Compound042
  OutputCompounding = 1
  PlacementsTo = -> PolarArray
  Referencing = 1
  Type = lattice2PopulateCopies.LatticePopulateCopies
  isLattice = 0
FEATURE [Sketcher::SketchObject] Sketch075
  ArcFitTolerance = 0
  AttachmentSupport = -> [XY_Plane036]
  ExternalGeometry = -> [Sketch062]
  FullyConstrained = true
  MakeInternals = false
  MapMode = 5
  expr: Constraints[34] = <<Properties>>.rivet_d
  sketch-geometry (14):
    g0: LineSegment [constr] StartX=15 StartY=280 StartZ=0 EndX=62.4647 EndY=297.399 EndZ=0
    g1: LineSegment [constr] StartX=62.4647 StartY=297.399 StartZ=0 EndX=15 EndY=335 EndZ=0
    g2: LineSegment [constr] StartX=15 StartY=280 StartZ=0 EndX=30.7162 EndY=302.5 EndZ=0
    g3: LineSegment [constr] StartX=30.7162 StartY=302.5 StartZ=0 EndX=15 EndY=335 EndZ=0
    g4: LineSegment [constr] StartX=30.7162 StartY=302.5 StartZ=0 EndX=62.4647 EndY=297.399 EndZ=0
    g5: LineSegment [constr] StartX=15 StartY=302.5 StartZ=0 EndX=30.7162 EndY=302.5 EndZ=0
    g6: LineSegment [constr] StartX=30.7162 StartY=302.5 StartZ=0 EndX=36.1253 EndY=287.744 EndZ=0
    g7: LineSegment [constr] StartX=30.7162 StartY=302.5 StartZ=0 EndX=40.4751 EndY=314.819 EndZ=0
    g8: Circle CenterX=34.4044 CenterY=292.439 CenterZ=0 NormalX=0 NormalY=0 NormalZ=1 AngleXU=0 Radius=1.7
    g9: Circle CenterX=36.2097 CenterY=309.435 CenterZ=0 NormalX=0 NormalY=0 NormalZ=1 AngleXU=0 Radius=1.7
    g10: Circle CenterX=20.588 CenterY=302.5 CenterZ=0 NormalX=0 NormalY=0 NormalZ=1 AngleXU=0 Radius=1.7
    g11: LineSegment [constr] StartX=20.588 StartY=302.5 StartZ=0 EndX=36.2097 EndY=309.435 EndZ=0
    g12: LineSegment [constr] StartX=36.2097 StartY=309.435 StartZ=0 EndX=34.4044 EndY=292.439 EndZ=0
    g13: LineSegment [constr] StartX=34.4044 StartY=292.439 StartZ=0 EndX=20.588 EndY=302.5 EndZ=0
  constraints (36):
    c: Coincident(g-4,g0)
    c: Coincident(g0,g1)
    c: Coincident(g1,g-3)
    c: PointOnObject(g-4,g0)
    c: PointOnObject(g-3,g1)
    c: Coincident(g0,g2)
    c: Coincident(g2,g3)
    c: Coincident(g2,g4)
    c: Coincident(g4,g0)
    c: Coincident(g3,g1)
    c: Coincident(g5,g2)
    c: Horizontal(g5)
    c: Coincident(g5,g6)
    c: PointOnObject(g6,g0)
    c: Perpendicular(g0,g6)
    c: Vertical(g5,g0)
    c: Equal(g6,g5)
    c: Coincident(g7,g2)
    c: PointOnObject(g7,g1)
    c: Perpendicular(g1,g7)
    c: Equal(g6,g7)
    c: PointOnObject(g8,g6)
    c: PointOnObject(g9,g7)
    c: PointOnObject(g10,g5)
    c: Coincident(g11,g10)
    c: Coincident(g11,g9)
    c: Coincident(g11,g12)
    c: Coincident(g12,g8)
    c: Coincident(g12,g13)
    c: Coincident(g13,g11)
    c: Equal(g13,g11)
    c: Equal(g11,g12)
    c: Equal(g8,g10)
    c: Equal(g8,g9)
    c: Diameter(g8) = 3.4
    c: Distance(g8,g6) = 5
FEATURE [PartDesign::Pocket] Pocket035
  BaseFeature = -> Bend009
  Direction = (0,0,-1)
  Length = 5
  Length2 = 5
  Midplane = true
  Profile = -> Sketch075
  ReferenceAxis = -> Sketch075 [N_Axis]
  Suppressed = false
  Type = 1
FEATURE [PartDesign::SubShapeBinder] Binder044
  BindCopyOnChange = 0
  BindMode = 0
  ClaimChildren = false
  Context = -> Body074 [Binder044.]
  Fuse = false
  MakeFace = true
  OffsetFill = false
  OffsetIntersection = false
  OffsetJoinType = 0
  OffsetOpenResult = false
  PartialLoad = false
  Relative = true
  Support = -> [Body073[Pocket035.Sketch075.]]
  _Version = 2
FEATURE [PartDesign::Pocket] Pocket036
  BaseFeature = -> Pad008
  Direction = (0,0,-1)
  Length = 5
  Length2 = 5
  Midplane = true
  Profile = -> Binder044
  Suppressed = false
  Type = 1
FEATURE [PartDesign::Plane] DatumPlane
  AttachmentOffset = pos=(0,0,0) rot=(0,1,0;0.523599rad)
  AttachmentSupport = -> [XZ_Plane037]
  Length = 552.693
  MapMode = 5
  Placement = pos=(0,0,0) rot=(0.935113,0.250563,0.250563;1.63783rad)
  ResizeMode = 0
  Width = 82.2624
FEATURE [PartDesign::Mirrored] Mirrored003
  BaseFeature = -> Pocket036
  MirrorPlane = -> DatumPlane
  Originals = -> [Pocket036]
  Suppressed = false
  TransformMode = 0
FEATURE [PartDesign::SubShapeBinder] Binder045
  BindCopyOnChange = 0
  BindMode = 0
  ClaimChildren = false
  Context = -> Body077 [Binder045.]
  Fuse = false
  MakeFace = true
  OffsetFill = false
  OffsetIntersection = false
  OffsetJoinType = 0
  OffsetOpenResult = false
  PartialLoad = false
  Relative = true
  Support = -> [Body074[Binder038.Compound037.Sketch063.]]
  _Version = 2
FEATURE [Sketcher::SketchObject] Sketch076
  ArcFitTolerance = 0
  AttachmentSupport = -> [XY_Plane041]
  ExternalGeometry = -> [Binder045]
  FullyConstrained = true
  MakeInternals = false
  MapMode = 5
  sketch-geometry (5):
    g0: LineSegment StartX=15 StartY=335 StartZ=0 EndX=62.031 EndY=297.743 EndZ=0
    g1: ArcOfCircle CenterX=-320.353 CenterY=-184.956 CenterZ=0 NormalX=0 NormalY=0 NormalZ=1 AngleXU=0 Radius=615.805 StartAngle=0.146355 EndAngle=0.900842
    g2: LineSegment StartX=288.868 StartY=-95.1511 StartZ=0 EndX=297.619 EndY=-154.51 EndZ=0
    g3: LineSegment [constr] StartX=-320.353 StartY=-184.956 StartZ=0 EndX=212.95 EndY=122.947 EndZ=0
    g4: LineSegment [constr] StartX=62.031 StartY=297.743 StartZ=0 EndX=288.868 EndY=-95.1511 EndZ=0
  constraints (12):
    c: Coincident(g0,g-4)
    c: Coincident(g1,g-4)
    c: Coincident(g1,g0)
    c: Tangent(g2,g1) = 1.5708
    c: Coincident(g3,g1)
    c: Coincident(g3,g-4)
    c: Vertical(g0,g-5)
    c: Equal(g0,g2)
    c: PointOnObject(g-3,g0)
    c: Coincident(g4,g0)
    c: Coincident(g4,g1)
    c: Perpendicular(g3,g4)
FEATURE [PartDesign::FeaturePython] BaseBend021  # WARN: FeaturePython — macro-defined, semantics opaque (R4)
  BendSide = 1
  BendSketch = -> Sketch076
  MidPlane = false
  Reverse = false
  Suppressed = false
  length = 419
  radius = 1
  thickness = 1.5
  expr: length = BaseBend020.length + composit_properties#<<Properties>>.thickness * 2
FEATURE [PartDesign::Fillet] Fillet
  Base = -> BaseBend021 [Edge10,Edge8,Edge25,Edge23]
  BaseFeature = -> BaseBend021
  Radius = 3
  SupportTransform = false
  Suppressed = false
  UseAllEdges = false
FEATURE [PartDesign::Plane] DatumPlane001
  AttachmentOffset = pos=(0,0,0) rot=(0,1,0;1.5708rad)
  AttachmentSupport = -> [Sketch062]
  Length = 362.992
  MapMode = 7
  Placement = pos=(15,335,0) rot=(-0.89718,0.312304,0.312304;4.6041rad)
  ResizeMode = 0
  Width = 509.896
FEATURE [Sketcher::SketchObject] Sketch077
  ArcFitTolerance = 0
  AttachmentSupport = -> [DatumPlane001]
  FullyConstrained = true
  MakeInternals = false
  MapMode = 5
  Placement = pos=(15,335,0) rot=(0.89718,-0.312304,-0.312304;1.67908rad)
  expr: Constraints[1] = <<Properties>>.rivet_d
  expr: Constraints[3] = BaseBend020.length
  sketch-geometry (4):
    g0: Circle CenterX=10 CenterY=7 CenterZ=0 NormalX=0 NormalY=0 NormalZ=1 AngleXU=0 Radius=1.7
    g1: Circle CenterX=10 CenterY=406 CenterZ=0 NormalX=0 NormalY=0 NormalZ=1 AngleXU=0 Radius=1.7
    g2: GeomPoint [constr] X=0 Y=413 Z=0
    g3: LineSegment [constr] StartX=0 StartY=206.5 StartZ=0 EndX=10 EndY=206.5 EndZ=0
  constraints (10):
    c: Equal(g0,g1)
    c: Diameter(g0) = 3.4
    c: PointOnObject(g2,g-2)
    c: DistanceY(g2) = 413
    c: DistanceX(g0) = 10
    c: DistanceY(g0) = 7
    c: Vertical(g1,g0)
    c: Horizontal(g3)
    c: Symmetric(g-1,g2,g3)
    c: Symmetric(g1,g0,g3)
FEATURE [PartDesign::Hole] Hole006
  BaseFeature = -> Pocket035
  CustomThreadClearance = 0
  Depth = 1
  DepthType = 0
  Diameter = 3.4
  DrillForDepth = false
  DrillPoint = 1
  DrillPointAngle = 118
  HoleCutCountersinkAngle = 90
  HoleCutCustomValues = false
  HoleCutDepth = 0
  HoleCutDiameter = 6.1
  HoleCutType = 0
  ModelThread = false
  Profile = -> Sketch077
  Reversed = true
  Suppressed = false
  Tapered = false
  TaperedAngle = 90
  ThreadClass = 0
  ThreadDepth = 1
  ThreadDepthType = 0
  ThreadDirection = 0
  ThreadFit = 0
  ThreadSize = 0
  ThreadType = 0
  Threaded = false
  UseCustomThreadClearance = false
  expr: Diameter = <<Properties>>.rivet_d
FEATURE [PartDesign::SubShapeBinder] Binder046
  BindCopyOnChange = 0
  BindMode = 0
  ClaimChildren = false
  Context = -> Body077 [Binder046.]
  Fuse = false
  MakeFace = true
  OffsetFill = false
  OffsetIntersection = false
  OffsetJoinType = 0
  OffsetOpenResult = false
  PartialLoad = false
  Relative = true
  Support = -> [Body073[Hole006.Sketch077.]]
  _Version = 2
FEATURE [Sketcher::SketchObject] Sketch078  label="pillar_magnet_fix"
  ArcFitTolerance = 0
  AttachmentOffset = pos=(0,0,0) rot=(0,1,0;1.5708rad)
  AttachmentSupport = -> [Sketch062]
  FullyConstrained = true
  MakeInternals = false
  MapMode = 7
  Placement = pos=(15,280,0) rot=(0.57735,0.57735,0.57735;2.0944rad)
  expr: Constraints[11] = <<Properties>>.rivet_d
  sketch-geometry (8):
    g0: ArcOfCircle CenterX=32.5 CenterY=244.5 CenterZ=0 NormalX=0 NormalY=0 NormalZ=1 AngleXU=0 Radius=11 StartAngle=4.71239 EndAngle=7.85398
    g1: ArcOfCircle CenterX=27.5 CenterY=244.5 CenterZ=0 NormalX=0 NormalY=0 NormalZ=1 AngleXU=0 Radius=11 StartAngle=1.5708 EndAngle=4.71239
    g2: LineSegment StartX=32.5 StartY=255.5 StartZ=0 EndX=27.5 EndY=255.5 EndZ=0
    g3: LineSegment StartX=27.5 StartY=233.5 StartZ=0 EndX=32.5 EndY=233.5 EndZ=0
    g4: Circle CenterX=30 CenterY=224.5 CenterZ=0 NormalX=0 NormalY=0 NormalZ=1 AngleXU=0 Radius=1.7
    g5: Circle CenterX=30 CenterY=264.5 CenterZ=0 NormalX=0 NormalY=0 NormalZ=1 AngleXU=0 Radius=1.7
    g6: LineSegment [constr] StartX=27.5 StartY=244.5 StartZ=0 EndX=30 EndY=244.5 EndZ=0
    g7: LineSegment [constr] StartX=32.5 StartY=244.5 StartZ=0 EndX=30 EndY=244.5 EndZ=0
  constraints (20):
    c: Tangent(g0,g2) = -1.5708
    c: Tangent(g2,g1) = -1.5708
    c: Tangent(g1,g3) = -1.5708
    c: Tangent(g3,g0) = -1.5708
    c: Equal(g0,g1)
    c: Coincident(g6,g1)
    c: Coincident(g7,g0)
    c: Coincident(g7,g6)
    c: Equal(g6,g7)
    c: Symmetric(g4,g5,g6)
    c: Equal(g4,g5)
    c: Diameter(g4) = 3.4
    c: Parallel(g6,g7)
    c: Distance(g1,g0) = 5
    c: Diameter(g0) = 22
    c: Horizontal(g1,g0)
    c: DistanceY(g4,g5) = 40
    c: DistanceY(g6) = 244.5  'height'
    c: DistanceX(g6) = 30
    c: Vertical(g4,g5)
FEATURE [PartDesign::Pocket] Pocket037
  BaseFeature = -> Hole006
  Direction = (-1,2e-16,0)
  Length = 5
  Length2 = 5
  Midplane = true
  Profile = -> Sketch078
  ReferenceAxis = -> Sketch078 [N_Axis]
  Suppressed = false
  Type = 0
FEATURE [Sketcher::SketchObject] Sketch079
  ArcFitTolerance = 0
  AttachmentSupport = -> [DatumPlane001]
  FullyConstrained = true
  MakeInternals = false
  MapMode = 5
  Placement = pos=(15,335,0) rot=(0.89718,-0.312304,-0.312304;1.67908rad)
  expr: Constraints[3] = BaseBend020.length - 111.35 mm
  sketch-geometry (2):
    g0: Circle CenterX=35 CenterY=301.65 CenterZ=0 NormalX=0 NormalY=0 NormalZ=1 AngleXU=0 Radius=1.25
    g1: Circle CenterX=35 CenterY=205.65 CenterZ=0 NormalX=0 NormalY=0 NormalZ=1 AngleXU=0 Radius=1.25
  constraints (6):
    c: Vertical(g1,g0)
    c: DistanceY(g1,g0) = 96
    c: DistanceX(g1) = 35
    c: DistanceY(g0) = 301.65
    c: Equal(g1,g0)
    c: Diameter(g1) = 2.5
FEATURE [PartDesign::SubShapeBinder] Binder047
  BindCopyOnChange = 0
  BindMode = 0
  ClaimChildren = true
  Context = -> Body077 [Binder047.]
  Fuse = false
  MakeFace = true
  OffsetFill = false
  OffsetIntersection = false
  OffsetJoinType = 0
  OffsetOpenResult = false
  PartialLoad = false
  Relative = true
  Support = -> [Body073[Sketch079.]]
  _Version = 2
FEATURE [PartDesign::Hole] Hole009
  BaseFeature = -> Pocket037
  CustomThreadClearance = 0
  Depth = 25
  DepthType = 0
  Diameter = 2.5
  DrillForDepth = false
  DrillPoint = 1
  DrillPointAngle = 118
  HoleCutCountersinkAngle = 90
  HoleCutCustomValues = false
  HoleCutDepth = 0
  HoleCutDiameter = 6.1
  HoleCutType = 0
  ModelThread = false
  Profile = -> Sketch079
  Reversed = true
  Suppressed = false
  Tapered = false
  TaperedAngle = 90
  ThreadClass = 0
  ThreadDepth = 25
  ThreadDepthType = 0
  ThreadDirection = 0
  ThreadFit = 0
  ThreadSize = 0
  ThreadType = 0
  Threaded = false
  UseCustomThreadClearance = false
FEATURE [PartDesign::Body] Body073  label="tech_sector_pillar_material_0.30ansi"
  AllowCompound = false
  Group = -> [Sketch062,BaseBend020,Bend009,Sketch075,Pocket035,DatumPlane001,Sketch077,Hole006,Sketch078,Pocket037,Sketch079,Hole009]
  Origin = -> Origin036
  Placement = pos=(0,0,3) rot=(0,0,1;0rad)
  Tip = -> Hole009
FEATURE [PartDesign::FeaturePython] Extend  # WARN: FeaturePython — macro-defined, semantics opaque (R4)
  BaseFeature = -> BaseBend018
  Offset = 0.02
  Refine = true
  Suppressed = false
  UseSubtraction = false
  baseObject = -> BaseBend018 [Face32]
  gap1 = 0
  gap2 = 0
  length = 0
FEATURE [PartDesign::Boolean] Boolean013
  BaseFeature = -> Extend
  Group = -> [Populate018]
  Suppressed = false
  Type = 1
  UsePlacement = false
FEATURE [PartDesign::Body] Body072  label="plexiglass_outer_material_0.30ansi"
  AllowCompound = false
  Group = -> [Binder037,BaseBend018,Extend,Boolean013]
  Origin = -> Origin035
  Tip = -> Extend
FEATURE [PartDesign::Plane] DatumPlane002
  AttachmentOffset = pos=(0,0,0) rot=(0,1,0;0.523599rad)
  AttachmentSupport = -> [XZ_Plane041]
  Length = 622.679
  MapMode = 5
  Placement = pos=(0,0,0) rot=(0.935113,0.250563,0.250563;1.63783rad)
  ResizeMode = 0
  Width = 540.655
FEATURE [Sketcher::SketchObject] Sketch080  label="hat_plexiglass_sketch"
  ArcFitTolerance = 0
  ExternalGeometry = -> [Sketch071,Sketch068]
  FullyConstrained = true
  MakeInternals = false
  sketch-geometry (4):
    g0: ArcOfCircle CenterX=614.788 CenterY=353 CenterZ=0 NormalX=0 NormalY=0 NormalZ=1 AngleXU=0 Radius=578.788 StartAngle=3.14159 EndAngle=3.645
    g1: LineSegment StartX=36 StartY=353 StartZ=0 EndX=36 EndY=382 EndZ=0
    g2: LineSegment StartX=112.627 StartY=65.0251 StartZ=0 EndX=107.803 EndY=73.7845 EndZ=0
    g3: LineSegment [constr] StartX=0 StartY=0 StartZ=0 EndX=112.627 EndY=65.0251 EndZ=0
  constraints (11):
    c: Coincident(g0,g-3)
    c: Vertical(g1)
    c: Coincident(g2,g-5)
    c: Tangent(g2,g0) = 1.5708
    c: Tangent(g1,g0) = 1.5708
    c: Distance(g2) = 10
    c: Coincident(g3,g-1)
    c: Coincident(g3,g2)
    c: Angle(g3) = 0.523599
    c: Angle(g2,g3) = 1.59099
    c: DistanceY(g1,g1) = 29
FEATURE [PartDesign::SubShapeBinder] Binder048
  BindCopyOnChange = 0
  BindMode = 0
  ClaimChildren = true
  Context = -> Part010 [Body078.Binder048.]
  Fuse = false
  MakeFace = true
  OffsetFill = false
  OffsetIntersection = false
  OffsetJoinType = 0
  OffsetOpenResult = false
  PartialLoad = false
  Relative = false
  Support = -> [Compound043]
  _Version = 2
FEATURE [PartDesign::FeaturePython] BaseBend022  # WARN: FeaturePython — macro-defined, semantics opaque (R4)
  BendSide = 1
  BendSketch = -> Binder048
  MidPlane = false
  Reverse = false
  Suppressed = false
  length = 96
  radius = 1
  thickness = 1.5
FEATURE [PartDesign::SubShapeBinder] Binder049
  BindCopyOnChange = 0
  BindMode = 0
  ClaimChildren = true
  Context = -> Part010 [Body078.Binder049.]
  Fuse = false
  MakeFace = false
  OffsetFill = false
  OffsetIntersection = false
  OffsetJoinType = 0
  OffsetOpenResult = false
  PartialLoad = false
  Placement = pos=(0,362,6) rot=(0.57735,0.57735,0.57735;2.0944rad)
  Relative = false
  Support = -> [Sketch073]
  _Version = 2
  expr: Support = Sketch073._self
FEATURE [PartDesign::Plane] DatumPlane003
  AttachmentOffset = pos=(0,0,0) rot=(0,1,0;0.523599rad)
  AttachmentSupport = -> [XZ_Plane043]
  Length = 648.977
  MapMode = 5
  Placement = pos=(0,0,0) rot=(0.935113,0.250563,0.250563;1.63783rad)
  ResizeMode = 0
  Width = 174.677
FEATURE [Part::Mirroring] Part__Mirroring015  label="hat_plexiglass_sketch (Mirror #19)"
  Base = (0,0,0)
  Normal = (0.5,-0.866025,0)
  Source = -> Sketch080
  expr: .Normal.x = cos(-60)
  expr: .Normal.y = sin(-60)
FEATURE [Part::Compound] Compound043  label="hat_plexiglass_bend_base"
  Links = -> [Sketch080,Part__Mirroring015]
FEATURE [PartDesign::Hole] Hole010
  BaseFeature = -> BaseBend022
  CustomThreadClearance = 0
  Depth = 1303.68
  DepthType = 1
  Diameter = 3.4
  DrillForDepth = false
  DrillPoint = 1
  DrillPointAngle = 118
  HoleCutCountersinkAngle = 90
  HoleCutCustomValues = false
  HoleCutDepth = 0
  HoleCutDiameter = 6.1
  HoleCutType = 0
  ModelThread = false
  Profile = -> Binder049
  Reversed = true
  Suppressed = false
  Tapered = false
  TaperedAngle = 90
  ThreadClass = 0
  ThreadDepth = 1303.68
  ThreadDepthType = 0
  ThreadDirection = 0
  ThreadFit = 0
  ThreadSize = 0
  ThreadType = 0
  Threaded = false
  UseCustomThreadClearance = false
  expr: Diameter = <<Properties>>.rivet_d
FEATURE [Sketcher::SketchObject] Sketch081
  ArcFitTolerance = 0
  AttachmentOffset = pos=(0,0,0) rot=(0,1,0;-1.0472rad)
  AttachmentSupport = -> [XZ_Plane043]
  FullyConstrained = true
  MakeInternals = false
  MapMode = 5
  Placement = pos=(0,0,0) rot=(-0.774597,0.447214,0.447214;4.45971rad)
  expr: Constraints[2] = <<Properties>>.rivet_d
  sketch-geometry (1):
    g0: Circle CenterX=0 CenterY=19 CenterZ=0 NormalX=0 NormalY=0 NormalZ=1 AngleXU=0 Radius=1.7
  constraints (3):
    c: PointOnObject(g0,g-2)
    c: DistanceY(g0) = 19
    c: Diameter(g0) = 3.4
FEATURE [PartDesign::Mirrored] Mirrored005
  BaseFeature = -> Hole010
  MirrorPlane = -> DatumPlane003
  Originals = -> [Hole010]
  Refine = true
  Suppressed = false
  TransformMode = 0
FEATURE [PartDesign::SubShapeBinder] Binder050
  BindCopyOnChange = 0
  BindMode = 0
  ClaimChildren = true
  Context = -> Part010 [Body078.Binder050.]
  Fuse = false
  MakeFace = true
  OffsetFill = false
  OffsetIntersection = false
  OffsetJoinType = 0
  OffsetOpenResult = false
  PartialLoad = false
  Relative = false
  Support = -> [Body075[Binder039.Array005.Compound039.Sketch068.]]
  _Version = 2
FEATURE [Sketcher::SketchObject] Sketch082
  ArcFitTolerance = 0
  AttachmentSupport = -> [XY_Plane043]
  FullyConstrained = true
  MakeInternals = false
  MapMode = 5
FEATURE [Sketcher::SketchObject] Sketch083
  ArcFitTolerance = 0
  AttachmentSupport = -> [XY_Plane037]
  ExternalGeometry = -> [Binder038]
  FullyConstrained = true
  MakeInternals = false
  MapMode = 5
  expr: Constraints[4] = <<Properties>>.rivet_d
  sketch-geometry (2):
    g0: LineSegment [constr] StartX=212.95 StartY=122.947 StartZ=0 EndX=201.691 EndY=116.447 EndZ=0
    g1: Circle CenterX=201.691 CenterY=116.447 CenterZ=0 NormalX=0 NormalY=0 NormalZ=1 AngleXU=0 Radius=1.7
  constraints (5):
    c: Coincident(g0,g-3)
    c: Perpendicular(g-3,g0)
    c: Distance(g0) = 13
    c: Coincident(g1,g0)
    c: Diameter(g1) = 3.4
FEATURE [PartDesign::Hole] Hole011
  BaseFeature = -> Mirrored003
  CustomThreadClearance = 0
  Depth = 25
  DepthType = 0
  Diameter = 3.4
  DrillForDepth = false
  DrillPoint = 1
  DrillPointAngle = 118
  HoleCutCountersinkAngle = 90
  HoleCutCustomValues = false
  HoleCutDepth = 0
  HoleCutDiameter = 6.1
  HoleCutType = 0
  ModelThread = false
  Profile = -> Sketch083
  Reversed = true
  Suppressed = false
  Tapered = false
  TaperedAngle = 90
  ThreadClass = 0
  ThreadDepth = 25
  ThreadDepthType = 0
  ThreadDirection = 0
  ThreadFit = 0
  ThreadSize = 0
  ThreadType = 0
  Threaded = false
  UseCustomThreadClearance = false
  expr: Diameter = <<Properties>>.rivet_d
FEATURE [PartDesign::Body] Body074  label="tech_sector_hor"
  AllowCompound = false
  Group = -> [Binder038,Pad008,Binder044,Pocket036,DatumPlane,Mirrored003,Sketch083,Hole011]
  Origin = -> Origin037
  Tip = -> Hole011
FEATURE [Sketcher::SketchObject] Sketch084
  ArcFitTolerance = 0
  AttachmentSupport = -> [Binder046]
  ExternalGeometry = -> [Binder046]
  FullyConstrained = false
  MakeInternals = false
  MapMode = 5
  Placement = pos=(168.839,213.132,5.5e-14) rot=(0.239007,0.686613,0.686613;2.67238rad)
  sketch-geometry (3):
    g0: Circle CenterX=186.261 CenterY=409.25 CenterZ=0 NormalX=0 NormalY=0 NormalZ=1 AngleXU=0 Radius=1.69397
    g1: Circle CenterX=186.261 CenterY=9.75 CenterZ=0 NormalX=0 NormalY=0 NormalZ=1 AngleXU=0 Radius=1.72481
    g2: GeomPoint [constr] X=186.261 Y=209.5 Z=0
  constraints (4):
    c: Symmetric(g-4,g-3,g2)
    c: Symmetric(g1,g0,g2)
    c: Vertical(g-3,g0)
    c: DistanceY(g-3,g0) = 0.25
FEATURE [PartDesign::Hole] Hole007
  BaseFeature = -> Fillet
  CustomThreadClearance = 0
  Depth = 25
  DepthType = 0
  Diameter = 3.4
  DrillForDepth = false
  DrillPoint = 1
  DrillPointAngle = 118
  HoleCutCountersinkAngle = 90
  HoleCutCustomValues = false
  HoleCutDepth = 0
  HoleCutDiameter = 6.1
  HoleCutType = 0
  ModelThread = false
  Profile = -> Sketch084
  Reversed = true
  Suppressed = false
  Tapered = false
  TaperedAngle = 90
  ThreadClass = 0
  ThreadDepth = 25
  ThreadDepthType = 0
  ThreadDirection = 0
  ThreadFit = 0
  ThreadSize = 0
  ThreadType = 0
  Threaded = false
  UseCustomThreadClearance = false
  expr: Diameter = <<Properties>>.rivet_d
FEATURE [PartDesign::Hole] Hole008
  BaseFeature = -> Hole007
  CustomThreadClearance = 0
  Depth = 25
  DepthType = 0
  Diameter = 3.4
  DrillForDepth = false
  DrillPoint = 1
  DrillPointAngle = 118
  HoleCutCountersinkAngle = 90
  HoleCutCustomValues = false
  HoleCutDepth = 0
  HoleCutDiameter = 6.1
  HoleCutType = 0
  ModelThread = false
  Profile = -> Binder047
  Reversed = true
  Suppressed = false
  Tapered = false
  TaperedAngle = 90
  ThreadClass = 0
  ThreadDepth = 25
  ThreadDepthType = 0
  ThreadDirection = 0
  ThreadFit = 0
  ThreadSize = 0
  ThreadType = 0
  Threaded = false
  UseCustomThreadClearance = false
  expr: Diameter = <<Properties>>.rivet_d
FEATURE [PartDesign::Mirrored] Mirrored004
  BaseFeature = -> Hole008
  MirrorPlane = -> DatumPlane002
  Originals = -> [Hole007,Hole008]
  Suppressed = false
  TransformMode = 0
FEATURE [PartDesign::Body] Body077  label="tech_sector_plexiglass_material_0.30ansi"
  AllowCompound = false
  Group = -> [Binder045,Sketch076,BaseBend021,Fillet,Binder046,Hole007,Binder047,Hole008,DatumPlane002,Mirrored004,Sketch084]
  Origin = -> Origin041
  Tip = -> Mirrored004
FEATURE [Part::Extrusion] Extrude015  label="magnet_fix"
  Base = -> Circle
  Dir = (0,0,1)
  DirMode = 2
  FaceMakerClass = Part::FaceMakerBullseye
  FaceMakerMode = 3
  LengthFwd = 15
  LengthRev = 0
  Placement = pos=(0,308.872,248) rot=(0,1,0;1.5708rad)
  Solid = true
  Symmetric = false
  expr: .Placement.Base.y = <<Properties>>.total_length - 43 mm
FEATURE [Part::Mirroring] Part__Mirroring016  label="magnet_fix (Mirror #20)"
  Base = (0,0,0)
  Normal = (0.5,-0.866025,0)
  Source = -> Extrude015
  expr: .Normal.x = cos(-60)
  expr: .Normal.y = sin(-60)
FEATURE [Sketcher::SketchObject] Sketch098
  ArcFitTolerance = 0
  AttachmentSupport = -> [XY_Plane038]
  FullyConstrained = true
  MakeInternals = false
  MapMode = 5
  sketch-geometry (1):
    g0: Circle CenterX=0 CenterY=0 CenterZ=0 NormalX=0 NormalY=0 NormalZ=1 AngleXU=0 Radius=3.25
  constraints (2):
    c: Coincident(g0,g-1)
    c: Diameter(g0) = 6.5
FEATURE [Sketcher::SketchObject] Sketch108
  ArcFitTolerance = 0
  AttachmentSupport = -> [XY_Plane038]
  ExternalGeometry = -> [Binder039]
  FullyConstrained = true
  MakeInternals = false
  MapMode = 5
  expr: Constraints[3] = <<Properties>>.rivet_d
  sketch-geometry (2):
    g0: LineSegment [constr] StartX=112.627 StartY=65.0251 StartZ=0 EndX=101.801 EndY=58.7751 EndZ=0
    g1: Circle CenterX=101.801 CenterY=58.7751 CenterZ=0 NormalX=0 NormalY=0 NormalZ=1 AngleXU=0 Radius=1.7
  constraints (5):
    c: Coincident(g0,g-3)
    c: PointOnObject(g-1,g0)
    c: Coincident(g1,g0)
    c: Diameter(g1) = 3.4
    c: Distance(g0) = 12.5
FEATURE [PartDesign::Pocket] Pocket054
  BaseFeature = -> Pocket032
  Direction = (0,0,-1)
  Length = 5
  Length2 = 5
  Profile = -> Sketch108
  ReferenceAxis = -> Sketch108 [N_Axis]
  Reversed = true
  Suppressed = false
  Type = 0
FEATURE [PartDesign::PolarPattern] PolarPattern
  Angle = 360
  Axis = -> Z_Axis038
  BaseFeature = -> Pocket054
  Mode = 0
  Occurrences = 3
  Offset = 120
  Originals = -> [Pocket032,Pocket054]
  Suppressed = false
  TransformMode = 0
FEATURE [PartDesign::Hole] Hole015
  BaseFeature = -> PolarPattern
  CustomThreadClearance = 0
  Depth = 25
  DepthType = 0
  Diameter = 27.5
  DrillForDepth = false
  DrillPoint = 1
  DrillPointAngle = 118
  HoleCutCountersinkAngle = 90
  HoleCutCustomValues = false
  HoleCutDepth = 0
  HoleCutDiameter = 0
  HoleCutType = 0
  ModelThread = false
  Profile = -> Sketch098
  Reversed = true
  Suppressed = false
  Tapered = false
  TaperedAngle = 90
  ThreadClass = 0
  ThreadDepth = 23.5
  ThreadDepthType = 0
  ThreadDirection = 0
  ThreadFit = 0
  ThreadSize = 0
  ThreadType = 0
  Threaded = false
  UseCustomThreadClearance = false
  expr: Diameter = <<sleeve_inner_sketch>>.Constraints.outer_r * 2 + 1.5 mm
FEATURE [PartDesign::SubShapeBinder] Binder061
  BindCopyOnChange = 0
  BindMode = 0
  ClaimChildren = false
  Context = -> Part007 [Body021.Binder061.]
  Fuse = false
  MakeFace = true
  OffsetFill = false
  OffsetIntersection = false
  OffsetJoinType = 0
  OffsetOpenResult = false
  PartialLoad = false
  Relative = false
  Support = -> [Body020[Pocket022.Sketch040.]]
  _Version = 2
FEATURE [PartDesign::SubShapeBinder] Binder062
  BindCopyOnChange = 0
  BindMode = 0
  ClaimChildren = false
  Context = -> Part007 [Body021.Binder062.]
  Fuse = false
  MakeFace = true
  OffsetFill = false
  OffsetIntersection = false
  OffsetJoinType = 0
  OffsetOpenResult = false
  PartialLoad = false
  Relative = false
  Support = -> [Body020[Pocket029.Sketch064.]]
  _Version = 2
FEATURE [Sketcher::SketchObject] Sketch109
  ArcFitTolerance = 0
  AttachmentSupport = -> [XY_Plane029]
  ExternalGeometry = -> [Binder061]
  FullyConstrained = false
  MakeInternals = false
  MapMode = 5
  sketch-geometry (19):
    g0: ArcOfCircle CenterX=291.996 CenterY=172.865 CenterZ=0 NormalX=0 NormalY=0 NormalZ=1 AngleXU=0 Radius=1 StartAngle=5.23599 EndAngle=6.98132
    g1: LineSegment StartX=5.51e-14 StartY=239 StartZ=0 EndX=5.51e-14 EndY=240 EndZ=0
    g2: LineSegment StartX=292.496 StartY=171.999 StartZ=0 EndX=287.719 EndY=169.241 EndZ=0
    g3: ArcOfCircle CenterX=287.219 CenterY=170.107 CenterZ=0 NormalX=0 NormalY=0 NormalZ=1 AngleXU=0 Radius=1 StartAngle=3.90153 EndAngle=5.23599
    g4: LineSegment StartX=5.51e-14 StartY=239 StartZ=0 EndX=5.51e-14 EndY=224 EndZ=0
    g5: ArcOfCircle CenterX=243.002 CenterY=128.086 CenterZ=0 NormalX=0 NormalY=0 NormalZ=1 AngleXU=0 Radius=60 StartAngle=0.759936 EndAngle=1.27733
    g6: GeomPoint [constr] X=287.033 Y=168.845 Z=0
    g7: GeomPoint [constr] X=293.528 Y=172.595 Z=0
    g8: ArcOfCircle CenterX=1.26657 CenterY=-621.999 CenterZ=0 NormalX=0 NormalY=0 NormalZ=1 AngleXU=0 Radius=862 StartAngle=1.25533 EndAngle=1.57227
    g9: LineSegment [constr] StartX=5.28e-14 StartY=220.8 StartZ=0 EndX=5.51e-14 EndY=240 EndZ=0
    g10: ArcOfCircle [constr] CenterX=0 CenterY=-641.2 CenterZ=0 NormalX=0 NormalY=0 NormalZ=1 AngleXU=0 Radius=862 StartAngle=1.25386 EndAngle=1.5708
    g11: LineSegment [constr] StartX=5.51e-14 StartY=240 StartZ=0 EndX=268.713 EndY=197.462 EndZ=0
    g12: LineSegment [constr] StartX=5.28e-14 StartY=220.8 StartZ=0 EndX=268.65 EndY=177.867 EndZ=0
    g13: ArcOfCircle CenterX=0 CenterY=-676.059 CenterZ=0 NormalX=0 NormalY=0 NormalZ=1 AngleXU=0 Radius=900.059 StartAngle=1.27733 EndAngle=1.5708
    g14: Circle [constr] CenterX=268.65 CenterY=177.867 CenterZ=0 NormalX=0 NormalY=0 NormalZ=1 AngleXU=0 Radius=4
    g15: LineSegment [constr] StartX=0 StartY=0 StartZ=0 EndX=301.632 EndY=174.148 EndZ=0
    g16: LineSegment [constr] StartX=0 StartY=0 StartZ=0 EndX=-15 EndY=25.9808 EndZ=0
    g17: ArcOfCircle CenterX=262.507 CenterY=178.449 CenterZ=0 NormalX=0 NormalY=0 NormalZ=1 AngleXU=0 Radius=20 StartAngle=0.698132 EndAngle=1.25533
    g18: LineSegment StartX=292.762 StartY=173.508 StartZ=0 EndX=277.828 EndY=191.305 EndZ=0
  constraints (51):
    c: Tangent(g17,g8) = -1.5708
    c: Vertical(g1)
    c: PointOnObject(g1,g-2)
    c: Angle(g2) = -2.61799
    c: Tangent(g2,g0) = 1.5708
    c: DistanceY(g1,g1) = 1
    c: Tangent(g3,g2) = 1.5708
    c: Radius(g3) = 1
    c: Equal(g3,g0)
    c: Coincident(g4,g1)
    c: Vertical(g4)
    c: Distance(g4) = 15
    c: Tangent(g5,g3) = 1.5708
    c: PointOnObject(g7,g2)
    c: PointOnObject(g6,g2)
    c: PointOnObject(g6,g5)
    c: Coincident(g8,g1)
    c: PointOnObject(g9,g-2)
    c: DistanceY(g9,g4) = 3.2
    c: Coincident(g9,g1)
    c: Radius(g8) = 862  'outer_r'
    c: Distance(g6,g7) = 7.5
    c: PointOnObject(g10,g-2)
    c: Coincident(g11,g1)
    c: Coincident(g11,g17)
    c: Coincident(g12,g10)
    c: Coincident(g12,g10)
    c: Equal(g10,g8)
    c: Equal(g12,g11)
    c: Coincident(g10,g9)
    c: PointOnObject(g13,g-2)
    c: Coincident(g13,g4)
    c: Tangent(g13,g5) = -1.5708
    c: Coincident(g14,g10)
    c: Tangent(g14,g5)
    c: Radius(g14) = 4
    c: Coincident(g15,g-1)
    c: Angle(g15) = 0.523599
    c: Distance(g6,g15) = 2.7076
    c: DistanceY(g1) = 240
    c: Coincident(g16,g15)
    c: Perpendicular(g15,g16)
    c: Distance(g7,g16) = 340.5
    c: Tangent(g18,g0) = -1.5708
    c: Angle(g18) = 2.26893
    c: Tangent(g17,g18) = -1.5708
    c: PointOnObject(g8,g-5)
    c: Radius(g17) = 20
    c: PointOnObject(g7,g18)
    c: Radius(g5) = 60
    c: Distance(g16) = 30
FEATURE [PartDesign::Pad] Pad014
  Direction = (0,0,1)
  Length = 3
  Length2 = 10
  Profile = -> Sketch109
  ReferenceAxis = -> Sketch109 [N_Axis]
  Suppressed = false
  Type = 0
FEATURE [PartDesign::Mirrored] Mirrored008
  BaseFeature = -> Pad014
  MirrorPlane = -> Sketch109 [V_Axis]
  Originals = -> [Pad014]
  Refine = true
  Suppressed = false
  TransformMode = 0
FEATURE [PartDesign::Pocket] Pocket055
  BaseFeature = -> Mirrored008
  Direction = (0,0,-1)
  Length = 5
  Length2 = 5
  Profile = -> Binder062
  Reversed = true
  Suppressed = false
  Type = 0
FEATURE [PartDesign::Body] Body021
  AllowCompound = false
  Group = -> [Binder061,Binder062,Sketch109,Pad014,Mirrored008,Pocket055]
  Origin = -> Origin029
  Placement = pos=(0,0,0) rot=(1,0,0;0.116239rad)
  Tip = -> Pocket055
FEATURE [Sketcher::SketchObject] Sketch110
  ArcFitTolerance = 0
  AttachmentOffset = pos=(0,333,0) rot=(0,0,1;0rad)
  AttachmentSupport = -> [XY_Plane011]
  FullyConstrained = true
  MakeInternals = false
  MapMode = 5
  Placement = pos=(0,333,0) rot=(0,0,1;0rad)
  sketch-geometry (2):
    g0: Circle CenterX=0 CenterY=26.3 CenterZ=0 NormalX=0 NormalY=0 NormalZ=1 AngleXU=0 Radius=2.75
    g1: Circle CenterX=0 CenterY=-26.3 CenterZ=0 NormalX=0 NormalY=0 NormalZ=1 AngleXU=0 Radius=2.75
  constraints (5):
    c: PointOnObject(g0,g-2)
    c: Equal(g1,g0)
    c: Diameter(g1) = 5.5
    c: Symmetric(g1,g0,g-1)
    c: DistanceY(g1,g0) = 52.6
FEATURE [PartDesign::PolarPattern] PolarPattern002
  Angle = 360
  Axis = -> Z_Axis011
  BaseFeature = -> Pad002
  Mode = 0
  Occurrences = 3
  Offset = 120
  Suppressed = false
  TransformMode = 0
FEATURE [Sketcher::SketchObject] Sketch112
  ArcFitTolerance = 0
  AttachmentSupport = -> [XY_Plane010]
  FullyConstrained = true
  MakeInternals = false
  MapMode = 5
  sketch-geometry (2):
    g0: Circle CenterX=0 CenterY=311.872 CenterZ=0 NormalX=0 NormalY=0 NormalZ=1 AngleXU=0 Radius=2.75
    g1: Circle CenterX=0 CenterY=276.872 CenterZ=0 NormalX=0 NormalY=0 NormalZ=1 AngleXU=0 Radius=2.75
  constraints (6):
    c: PointOnObject(g0,g-2)
    c: PointOnObject(g1,g-2)
    c: Equal(g1,g0)
    c: Diameter(g1) = 5.5
    c: DistanceY(g1,g0) = 35
    c: DistanceY(g1) = 276.872
FEATURE [Sketcher::SketchObject] Sketch113
  ArcFitTolerance = 0
  AttachmentSupport = -> [XY_Plane010]
  FullyConstrained = true
  MakeInternals = false
  MapMode = 5
  sketch-geometry (9):
    g0: LineSegment [constr] StartX=-22.5 StartY=-136 StartZ=0 EndX=-22.5 EndY=-161 EndZ=0
    g1: LineSegment [constr] StartX=-22.5 StartY=-161 StartZ=0 EndX=22.5 EndY=-161 EndZ=0
    g2: LineSegment [constr] StartX=22.5 StartY=-161 StartZ=0 EndX=22.5 EndY=-136 EndZ=0
    g3: LineSegment [constr] StartX=22.5 StartY=-136 StartZ=0 EndX=-22.5 EndY=-136 EndZ=0
    g4: GeomPoint [constr] X=0 Y=-148.5 Z=0
    g5: Circle CenterX=22.5 CenterY=-161 CenterZ=0 NormalX=0 NormalY=0 NormalZ=1 AngleXU=0 Radius=2.75
    g6: Circle CenterX=22.5 CenterY=-136 CenterZ=0 NormalX=0 NormalY=0 NormalZ=1 AngleXU=0 Radius=2.75
    g7: Circle CenterX=-22.5 CenterY=-136 CenterZ=0 NormalX=0 NormalY=0 NormalZ=1 AngleXU=0 Radius=2.75
    g8: Circle CenterX=-22.5 CenterY=-161 CenterZ=0 NormalX=0 NormalY=0 NormalZ=1 AngleXU=0 Radius=2.75
  constraints (21):
    c: Coincident(g0,g1)
    c: Coincident(g1,g2)
    c: Coincident(g2,g3)
    c: Coincident(g3,g0)
    c: Horizontal(g1)
    c: Horizontal(g3)
    c: Vertical(g0)
    c: Vertical(g2)
    c: Symmetric(g1,g0,g4)
    c: PointOnObject(g4,g-2)
    c: Coincident(g5,g1)
    c: Coincident(g6,g2)
    c: Coincident(g7,g0)
    c: Coincident(g8,g0)
    c: Equal(g5,g8)
    c: Equal(g5,g7)
    c: Equal(g5,g6)
    c: Diameter(g5) = 5.5
    c: DistanceY(g2,g2) = 25
    c: DistanceX(g1,g1) = 45
    c: DistanceY(g6) = -136
FEATURE [App::Link] Link006  label="module"
  LinkedObject = -> <external module.FCStd>#Body
FEATURE [Part::FeaturePython] Populate019  label="Populate Populate LinearArray with LinearArray001 with Body084"  # WARN: FeaturePython — macro-defined, semantics opaque (R4)
  Copying = 0
  ExposePlacement = false
  MarkerShape = 1
  MarkerSize = 0
  NumElements = 0
  Object = -> Link006
  OutputCompounding = 1
  Placement = pos=(14.5,181.372,1401) rot=(0.57735,0.57735,0.57735;2.0944rad)
  PlacementsTo = -> Populate
  Referencing = 0
  Type = lattice2PopulateCopies.LatticePopulateCopies
  isLattice = 0
  expr: Placement = <<modules_holes>>.Placement * placement(vector(0; 0; 14.5); rotation(0; 0; 0))
FEATURE [Sketcher::SketchObject] Sketch118
  ArcFitTolerance = 0
  AttachmentSupport = -> [XZ_Plane015]
  FullyConstrained = true
  MakeInternals = false
  MapMode = 5
  Placement = pos=(0,0,0) rot=(1,0,0;1.5708rad)
  expr: Constraints[10] = <<pillar_base_sketch>>.Constraints.length / 2 - 2 mm
  expr: Constraints[9] = -<<pillar_bottom_BaseBend>>.length / 2
  sketch-geometry (11):
    g0: Circle CenterX=-43 CenterY=9 CenterZ=0 NormalX=0 NormalY=0 NormalZ=1 AngleXU=0 Radius=1.7
    g1: Circle CenterX=-43 CenterY=40.3333 CenterZ=0 NormalX=0 NormalY=0 NormalZ=1 AngleXU=0 Radius=1.7
    g2: Circle [constr] CenterX=-43 CenterY=103 CenterZ=0 NormalX=0 NormalY=0 NormalZ=1 AngleXU=0 Radius=1.7
    g3: LineSegment [constr] StartX=-43 StartY=9 StartZ=0 EndX=-43 EndY=40.3333 EndZ=0
    g4: GeomPoint [constr] X=-50.5 Y=0 Z=0
    g5: GeomPoint [constr] X=-43 Y=110 Z=0
    g6: LineSegment [constr] StartX=-43 StartY=103 StartZ=0 EndX=-43 EndY=110 EndZ=0
    g7: LineSegment [constr] StartX=-43 StartY=9 StartZ=0 EndX=-43 EndY=0 EndZ=0
    g8: LineSegment [constr] StartX=-43 StartY=40.3333 StartZ=0 EndX=-43 EndY=71.6667 EndZ=0
    g9: LineSegment [constr] StartX=-43 StartY=71.6667 StartZ=0 EndX=-43 EndY=103 EndZ=0
    g10: Circle CenterX=-43 CenterY=71.6667 CenterZ=0 NormalX=0 NormalY=0 NormalZ=1 AngleXU=0 Radius=1.7
  constraints (27):
    c: Equal(g0,g1)
    c: Equal(g0,g2)
    c: Diameter(g0) = 3.4
    c: Coincident(g3,g0)
    c: Coincident(g3,g1)
    c: Vertical(g3)
    c: Coincident(g8,g1)
    c: Coincident(g9,g2)
    c: PointOnObject(g4,g-1)
    c: DistanceX(g4) = -50.5
    c: DistanceX(g4,g0) = 7.5
    c: DistanceY(g5) = 110
    c: Coincident(g6,g2)
    c: Coincident(g6,g5)
    c: Vertical(g6)
    c: Coincident(g7,g0)
    c: PointOnObject(g7,g-1)
    c: Vertical(g7)
    c: DistanceY(g7,g7) = 9
    c: DistanceY(g6,g6) = 7
    c: Coincident(g8,g9)
    c: Vertical(g8)
    c: Vertical(g9)
    c: Equal(g3,g8)
    c: Equal(g8,g9)
    c: Coincident(g10,g8)
    c: Equal(g0,g10)
FEATURE [PartDesign::SubShapeBinder] Binder072
  BindCopyOnChange = 0
  BindMode = 0
  ClaimChildren = true
  Context = -> Body010 [Binder072.]
  Fuse = false
  MakeFace = true
  OffsetFill = false
  OffsetIntersection = false
  OffsetJoinType = 0
  OffsetOpenResult = false
  PartialLoad = false
  Relative = true
  Support = -> [Body011[Pocket063.Sketch118.]]
  _Version = 2
FEATURE [PartDesign::Fillet] Fillet001
  Base = -> Bend [Edge12,Edge60,Edge14,Edge64,Edge41,Edge59]
  BaseFeature = -> Bend
  Radius = 5
  SupportTransform = false
  Suppressed = false
  UseAllEdges = false
FEATURE [PartDesign::Hole] Hole005
  BaseFeature = -> Fillet001
  CustomThreadClearance = 0
  Depth = 286.27
  DepthType = 1
  Diameter = 3.4
  DrillForDepth = false
  DrillPoint = 1
  DrillPointAngle = 118
  HoleCutCountersinkAngle = 90
  HoleCutCustomValues = false
  HoleCutDepth = 0
  HoleCutDiameter = 6.1
  HoleCutType = 0
  ModelThread = false
  Profile = -> Sketch066
  Reversed = true
  Suppressed = false
  Tapered = false
  TaperedAngle = 90
  ThreadClass = 0
  ThreadDepth = 286.27
  ThreadDepthType = 0
  ThreadDirection = 0
  ThreadFit = 0
  ThreadSize = 0
  ThreadType = 0
  Threaded = false
  UseCustomThreadClearance = false
  expr: Diameter = <<Properties>>.rivet_d
FEATURE [PartDesign::Pocket] Pocket030
  BaseFeature = -> Hole005
  Direction = (0,0,-1)
  Length = 5
  Length2 = 5
  Profile = -> Sketch067
  ReferenceAxis = -> Sketch067 [N_Axis]
  Reversed = true
  Suppressed = false
  Type = 0
FEATURE [PartDesign::Pocket] Pocket034
  BaseFeature = -> Pocket030
  Direction = (-1,0,0)
  Length = 5
  Length2 = 5
  Midplane = true
  Profile = -> Sketch073
  ReferenceAxis = -> Sketch073 [N_Axis]
  Suppressed = false
  Type = 1
FEATURE [PartDesign::Fillet] Fillet002
  Base = -> BaseBend004 [Edge10,Edge39,Edge41,Edge8]
  BaseFeature = -> BaseBend004
  Radius = 5
  SupportTransform = false
  Suppressed = false
  UseAllEdges = false
FEATURE [PartDesign::Pad] Pad
  BaseFeature = -> Fillet002
  Direction = (0,-1,2e-16)
  Length = 2
  Length2 = 10
  Profile = -> Sketch009
  ReferenceAxis = -> Sketch009 [N_Axis]
  Reversed = true
  Suppressed = false
  Type = 0
  expr: Length = <<pillar_BaseBend>>.thickness
FEATURE [PartDesign::Boolean] Boolean011
  BaseFeature = -> Pad
  Group = -> [Compound030]
  Refine = true
  Suppressed = false
  Type = 1
  UsePlacement = false
  expr: Group = <<pillar_cut1>>._self
FEATURE [PartDesign::Hole] Hole019
  BaseFeature = -> Boolean011
  CustomThreadClearance = 0
  Depth = 3405.27
  DepthType = 1
  Diameter = 3.4
  DrillForDepth = false
  DrillPoint = 1
  DrillPointAngle = 118
  HoleCutCountersinkAngle = 90
  HoleCutCustomValues = false
  HoleCutDepth = 0
  HoleCutDiameter = 6.1
  HoleCutType = 0
  ModelThread = false
  Profile = -> Binder072
  Suppressed = false
  Tapered = false
  TaperedAngle = 90
  ThreadClass = 0
  ThreadDepth = 3405.27
  ThreadDepthType = 0
  ThreadDirection = 0
  ThreadFit = 0
  ThreadSize = 0
  ThreadType = 0
  Threaded = false
  UseCustomThreadClearance = false
  expr: Diameter = <<Properties>>.rivet_d
FEATURE [PartDesign::Body] Body010  label="pillar_material_0.30ansi"
  AllowCompound = false
  Group = -> [Binder002,BaseBend004,Sketch009,Fillet002,Pad,Boolean011,Binder072,Hole019]
  Origin = -> Origin014
  Tip = -> Hole019
FEATURE [PartDesign::Fillet] Fillet003
  Base = -> BaseBend017 [Edge23,Edge10,Edge25,Edge8]
  BaseFeature = -> BaseBend017
  Placement = pos=(0,0,481) rot=(0,0,1;0rad)
  Radius = 5
  SupportTransform = false
  Suppressed = false
  UseAllEdges = false
FEATURE [PartDesign::Boolean] Boolean012
  BaseFeature = -> Fillet003
  Group = -> [Compound032]
  Suppressed = false
  Type = 1
  UsePlacement = false
  expr: Group = <<dec_corner_cut1>>._self
FEATURE [PartDesign::Body] Body013  label="dec_corner_material_0.30ansi"
  AllowCompound = false
  Group = -> [Binder035,BaseBend017,Fillet003,Boolean012]
  Origin = -> Origin017
  Tip = -> Boolean012
FEATURE [Sketcher::SketchObject] Sketch119
  ArcFitTolerance = 0
  AttachmentSupport = -> [XY_Plane018]
  FullyConstrained = true
  MakeInternals = false
  MapMode = 5
  sketch-geometry (2):
    g0: LineSegment StartX=37.5 StartY=-1.5 StartZ=0 EndX=-37.5 EndY=-1.5 EndZ=0
    g1: LineSegment StartX=-37.5 StartY=-1.5 StartZ=0 EndX=-37.5 EndY=27 EndZ=0
  constraints (6):
    c: Coincident(g1,g0)
    c: Vertical(g1)
    c: DistanceY(g0) = -1.5
    c: Symmetric(g0,g0,g-2)
    c: DistanceX(g0,g0) = 75
    c: DistanceY(g1) = 27
FEATURE [PartDesign::FeaturePython] BaseBend029  # WARN: FeaturePython — macro-defined, semantics opaque (R4)
  BendSide = 1
  BendSketch = -> Sketch119
  MidPlane = false
  Placement = pos=(0,0,1588) rot=(0,0,1;0rad)
  Reverse = false
  Suppressed = false
  length = 96
  radius = 2
  thickness = 0.5
FEATURE [Sketcher::SketchObject] Sketch120
  ArcFitTolerance = 0
  AttachmentOffset = pos=(0,1588,0) rot=(0,0,1;0rad)
  AttachmentSupport = -> [XZ_Plane018]
  FullyConstrained = true
  MakeInternals = false
  MapMode = 5
  Placement = pos=(0,3.526e-13,1588) rot=(1,0,0;1.5708rad)
  expr: .AttachmentOffset.Base.y = BaseBend029.Placement.Base.z
  sketch-geometry (5):
    g0: ArcOfCircle CenterX=-35.5 CenterY=13.8267 CenterZ=0 NormalX=0 NormalY=0 NormalZ=1 AngleXU=0 Radius=13.8267 StartAngle=4.71239 EndAngle=5.38367
    g1: ArcOfCircle CenterX=-18.3 CenterY=-7.82667 CenterZ=0 NormalX=0 NormalY=0 NormalZ=1 AngleXU=0 Radius=13.8267 StartAngle=1.5708 EndAngle=2.24207
    g2: LineSegment StartX=-18.3 StartY=6 StartZ=0 EndX=40 EndY=6 EndZ=0
    g3: LineSegment StartX=40 StartY=6 StartZ=0 EndX=40 EndY=0 EndZ=0
    g4: LineSegment StartX=40 StartY=0 StartZ=0 EndX=-35.5 EndY=1.42e-14 EndZ=0
  constraints (15):
    c: PointOnObject(g0,g-1)
    c: Horizontal(g2)
    c: Coincident(g3,g2)
    c: PointOnObject(g3,g-1)
    c: Vertical(g3)
    c: Coincident(g4,g3)
    c: Coincident(g4,g0)
    c: Tangent(g4,g0)
    c: Equal(g0,g1)
    c: DistanceX(g0) = -35.5
    c: Tangent(g2,g1) = 1.5708
    c: Tangent(g1,g0) = 1.5708
    c: DistanceY(g3,g3) = 6
    c: DistanceX(g1) = -18.3
    c: DistanceX(g3) = 40
FEATURE [PartDesign::Pocket] Pocket064
  BaseFeature = -> BaseBend029
  Direction = (0,1,-2e-16)
  Length = 5
  Length2 = 5
  Midplane = true
  Placement = pos=(0,0,1588) rot=(0,0,1;0rad)
  Profile = -> Sketch120
  ReferenceAxis = -> Sketch120 [N_Axis]
  Suppressed = false
  Type = 1
FEATURE [PartDesign::Fillet] Fillet004
  Base = -> Pocket064 [Edge25,Edge31,Edge8,Edge10]
  BaseFeature = -> Pocket064
  Placement = pos=(0,0,1588) rot=(0,0,1;0rad)
  Radius = 3
  SupportTransform = false
  Suppressed = false
  UseAllEdges = false
FEATURE [Part::Compound] Compound044  label="top_dec_corner_cut1"
  Links = -> [Compound034]
FEATURE [PartDesign::Boolean] Boolean014
  BaseFeature = -> Fillet004
  Group = -> [Compound044]
  Suppressed = false
  Type = 1
  UsePlacement = false
FEATURE [PartDesign::SubShapeBinder] Binder073
  BindCopyOnChange = 0
  BindMode = 0
  ClaimChildren = false
  Context = -> Link025 [Binder073.]
  Fuse = false
  MakeFace = true
  OffsetFill = false
  OffsetIntersection = false
  OffsetJoinType = 0
  OffsetOpenResult = false
  PartialLoad = false
  Relative = true
  Support = -> [Body012[Pocket034.Sketch073.]]
  _Version = 2
FEATURE [PartDesign::Hole] Hole020
  BaseFeature = -> Boolean014
  CustomThreadClearance = 0
  Depth = 253.566
  DepthType = 1
  Diameter = 3.4
  DrillForDepth = false
  DrillPoint = 1
  DrillPointAngle = 118
  HoleCutCountersinkAngle = 90
  HoleCutCustomValues = false
  HoleCutDepth = 0
  HoleCutDiameter = 6.1
  HoleCutType = 0
  ModelThread = false
  Profile = -> Binder073
  Suppressed = false
  Tapered = false
  TaperedAngle = 90
  ThreadClass = 0
  ThreadDepth = 253.566
  ThreadDepthType = 0
  ThreadDirection = 0
  ThreadFit = 0
  ThreadSize = 0
  ThreadType = 0
  Threaded = false
  UseCustomThreadClearance = false
  expr: Diameter = <<Properties>>.rivet_d
FEATURE [PartDesign::Body] Body014  label="top_dec_corner_material_0.30ansi"
  AllowCompound = false
  Group = -> [Sketch119,BaseBend029,Sketch120,Pocket064,Fillet004,Boolean014,Binder073,Hole020]
  Origin = -> Origin018
  Tip = -> Hole020
FEATURE [PartDesign::SubShapeBinder] Binder074
  BindCopyOnChange = 0
  BindMode = 0
  ClaimChildren = false
  Context = -> Body012 [Binder074.]
  Fuse = false
  MakeFace = true
  OffsetFill = false
  OffsetIntersection = false
  OffsetJoinType = 0
  OffsetOpenResult = false
  PartialLoad = false
  Relative = true
  Support = -> [Body010[Boolean011.Edge138,Boolean011.Edge140,Boolean011.Edge152]]
  _Version = 2
FEATURE [PartDesign::Pocket] Pocket065
  BaseFeature = -> Pocket034
  Direction = (0,-1,4e-16)
  Length = 5
  Length2 = 5
  Profile = -> Binder074
  Reversed = true
  Suppressed = false
  Type = 0
FEATURE [PartDesign::Body] Body012  label="pillar_top_element_material_0.30ansi"
  AllowCompound = false
  Group = -> [Sketch013,BaseBend006,Bend,Sketch066,Fillet001,Hole005,Sketch067,Pocket030,Sketch073,Pocket034,Binder074,Pocket065]
  Origin = -> Origin016
  Placement = pos=(0,2,1594) rot=(0,0,1;0rad)
  Tip = -> Pocket065
FEATURE [Sketcher::SketchObject] Sketch121
  ArcFitTolerance = 0
  AttachmentSupport = -> [XZ_Plane054]
  FullyConstrained = true
  MakeInternals = false
  MapMode = 5
  Placement = pos=(0,0,0) rot=(1,0,0;1.5708rad)
  sketch-geometry (5):
    g0: LineSegment StartX=-18 StartY=15 StartZ=0 EndX=-18 EndY=0 EndZ=0
    g1: LineSegment StartX=-18 StartY=0 StartZ=0 EndX=18 EndY=0 EndZ=0
    g2: LineSegment StartX=18 StartY=0 StartZ=0 EndX=18 EndY=15 EndZ=0
    g3: LineSegment [constr] StartX=18 StartY=15 StartZ=0 EndX=-18 EndY=15 EndZ=0
    g4: GeomPoint [constr] X=0 Y=7.5 Z=0
  constraints (13):
    c: Coincident(g0,g1)
    c: Coincident(g1,g2)
    c: Coincident(g2,g3)
    c: Coincident(g3,g0)
    c: Horizontal(g1)
    c: Horizontal(g3)
    c: Vertical(g0)
    c: Vertical(g2)
    c: Symmetric(g1,g0,g4)
    c: PointOnObject(g4,g-2)
    c: PointOnObject(g1,g-1)
    c: DistanceY(g2,g2) = 15  'height'
    c: DistanceX(g1,g1) = 36  'width'
FEATURE [PartDesign::FeaturePython] BaseBend030  # WARN: FeaturePython — macro-defined, semantics opaque (R4)
  BendSide = 1
  BendSketch = -> Sketch121
  MidPlane = true
  Reverse = false
  Suppressed = false
  length = 245
  radius = 2
  thickness = 2
FEATURE [Sketcher::SketchObject] Sketch122
  ArcFitTolerance = 0
  AttachmentSupport = -> [YZ_Plane054]
  FullyConstrained = true
  MakeInternals = false
  MapMode = 5
  Placement = pos=(0,0,0) rot=(0.57735,0.57735,0.57735;2.0944rad)
  expr: Constraints[10] = Sketch121.Constraints.height
  expr: Constraints[12] = BaseBend030.length / 2
  expr: Constraints[9] = BaseBend030.thickness + BaseBend030.radius
  sketch-geometry (14):
    g0: ArcOfCircle CenterX=117.5 CenterY=4 CenterZ=0 NormalX=0 NormalY=0 NormalZ=1 AngleXU=0 Radius=5 StartAngle=1e-16 EndAngle=0.785398
    g1: LineSegment StartX=121.036 StartY=7.53553 StartZ=0 EndX=115.036 EndY=13.5355 EndZ=0
    g2: ArcOfCircle CenterX=111.5 CenterY=10 CenterZ=0 NormalX=0 NormalY=0 NormalZ=1 AngleXU=0 Radius=5 StartAngle=0.785398 EndAngle=1.5708
    g3: LineSegment StartX=111.5 StartY=15 StartZ=0 EndX=-111.5 EndY=15 EndZ=0
    g4: LineSegment StartX=122.5 StartY=4 StartZ=0 EndX=122.5 EndY=0 EndZ=0
    g5: LineSegment StartX=122.5 StartY=0 StartZ=0 EndX=-122.5 EndY=0 EndZ=0
    g6: LineSegment StartX=-122.5 StartY=0 StartZ=0 EndX=-122.5 EndY=4 EndZ=0
    g7: LineSegment StartX=-121.036 StartY=7.53553 StartZ=0 EndX=-115.036 EndY=13.5355 EndZ=0
    g8: ArcOfCircle CenterX=-111.5 CenterY=10 CenterZ=0 NormalX=0 NormalY=0 NormalZ=1 AngleXU=0 Radius=5 StartAngle=1.5708 EndAngle=2.35619
    g9: GeomPoint [constr] X=-113.571 Y=15 Z=0
    g10: ArcOfCircle CenterX=-117.5 CenterY=4 CenterZ=0 NormalX=0 NormalY=0 NormalZ=1 AngleXU=0 Radius=5 StartAngle=2.35619 EndAngle=3.14159
    g11: GeomPoint [constr] X=-122.5 Y=6.07107 Z=0
    g12: GeomPoint [constr] X=113.571 Y=15 Z=0
    g13: GeomPoint [constr] X=122.5 Y=6.07107 Z=0
  constraints (32):
    c: Tangent(g1,g0) = -1.5708
    c: Angle(g1) = 2.35619
    c: Tangent(g2,g1) = -1.5708
    c: Horizontal(g3)
    c: Tangent(g3,g2) = -1.5708
    c: Equal(g0,g2)
    c: Tangent(g0,g4) = 1.5708
    c: Coincident(g4,g5)
    c: Horizontal(g5)
    c: DistanceY(g0) = 4
    c: DistanceY(g9) = 15
    c: Vertical(g4)
    c: DistanceX(g4) = 122.5
    c: Radius(g0) = 5
    c: Coincident(g5,g6)
    c: Tangent(g3,g8) = -1.5708
    c: Tangent(g7,g8) = 1.5708
    c: PointOnObject(g11,g6)
    c: PointOnObject(g11,g7)
    c: Tangent(g6,g10) = 1.5708
    c: Tangent(g7,g10) = 1.5708
    c: Vertical(g6)
    c: Equal(g10,g8)
    c: Equal(g8,g2)
    c: PointOnObject(g13,g4)
    c: PointOnObject(g13,g1)
    c: PointOnObject(g12,g1)
    c: Symmetric(g13,g11,g-2)
    c: Symmetric(g9,g12,g-2)
    c: PointOnObject(g9,g3)
    c: PointOnObject(g9,g7)
    c: PointOnObject(g-1,g5)
FEATURE [Part::FeaturePython] WireFilter003  # WARN: FeaturePython — macro-defined, semantics opaque (R4)
  AttacherType = Attacher::AttachEngine3D
  ClaimChildren = true
  ColorKeyCount = 8
  Colorize = true
  FaceMaker = 5
  FixNormal = false
  FollowSource = true
  InvertedFaceScale = 5
  MaxWires = 25
  Normal = (1,0,0)
  OffsetFill = false
  OffsetIntersection = false
  OffsetJoin = 0
  OffsetOpenResult = false
  Scale = (1,1,1)
  SelectEdges = false
  Source = -> Sketch122
  UniformScale = 1
  UseDefault = false
  UseSelected = true
  UseSelectedEdges = false
  Version = 0.2022.02.09
  WireOrder = [1]
FEATURE [PartDesign::Pocket] Pocket066
  BaseFeature = -> BaseBend030
  Direction = (-1,0,0)
  Length = 5
  Length2 = 5
  Midplane = true
  Profile = -> WireFilter003
  Suppressed = false
  Type = 1
FEATURE [Sketcher::SketchObject] Sketch123
  ArcFitTolerance = 0
  AttachmentSupport = -> [XY_Plane054]
  FullyConstrained = true
  MakeInternals = false
  MapMode = 5
  expr: Constraints[1] = -BaseBend030.length / 2
  expr: Constraints[32] = BaseBend030.length - 14 mm
  sketch-geometry (15):
    g0: GeomPoint [constr] X=0 Y=-122.5 Z=0
    g1: Circle CenterX=0 CenterY=92.5 CenterZ=0 NormalX=0 NormalY=0 NormalZ=1 AngleXU=0 Radius=2.5
    g2: LineSegment [constr] StartX=9 StartY=115.5 StartZ=0 EndX=-9 EndY=115.5 EndZ=0
    g3: LineSegment [constr] StartX=-9 StartY=115.5 StartZ=0 EndX=-9 EndY=0 EndZ=0
    g4: LineSegment [constr] StartX=-9 StartY=0 StartZ=0 EndX=-9 EndY=-115.5 EndZ=0
    g5: LineSegment [constr] StartX=-9 StartY=-115.5 StartZ=0 EndX=9 EndY=-115.5 EndZ=0
    g6: LineSegment [constr] StartX=9 StartY=-115.5 StartZ=0 EndX=9 EndY=0 EndZ=0
    g7: LineSegment [constr] StartX=9 StartY=0 StartZ=0 EndX=9 EndY=115.5 EndZ=0
    g8: Circle CenterX=-9 CenterY=0 CenterZ=0 NormalX=0 NormalY=0 NormalZ=1 AngleXU=0 Radius=2.5
    g9: Circle CenterX=9 CenterY=0 CenterZ=0 NormalX=0 NormalY=0 NormalZ=1 AngleXU=0 Radius=2.5
    g10: Circle CenterX=-9 CenterY=115.5 CenterZ=0 NormalX=0 NormalY=0 NormalZ=1 AngleXU=0 Radius=2.5
    g11: Circle CenterX=9 CenterY=115.5 CenterZ=0 NormalX=0 NormalY=0 NormalZ=1 AngleXU=0 Radius=2.5
    g12: Circle CenterX=-9 CenterY=-115.5 CenterZ=0 NormalX=0 NormalY=0 NormalZ=1 AngleXU=0 Radius=2.5
    g13: Circle CenterX=9 CenterY=-115.5 CenterZ=0 NormalX=0 NormalY=0 NormalZ=1 AngleXU=0 Radius=2.5
    g14: Circle CenterX=0 CenterY=-92.5 CenterZ=0 NormalX=0 NormalY=0 NormalZ=1 AngleXU=0 Radius=4
  constraints (36):
    c: PointOnObject(g0,g-2)
    c: DistanceY(g0) = -122.5
    c: PointOnObject(g1,g-2)
    c: DistanceY(g0,g1) = 215
    c: Horizontal(g2)
    c: Coincident(g2,g3)
    c: PointOnObject(g3,g-1)
    c: Vertical(g3)
    c: Coincident(g3,g4)
    c: Vertical(g4)
    c: Coincident(g4,g5)
    c: Horizontal(g5)
    c: Coincident(g5,g6)
    c: PointOnObject(g6,g-1)
    c: Vertical(g6)
    c: Coincident(g6,g7)
    c: Coincident(g7,g2)
    c: Vertical(g7)
    c: Coincident(g8,g3)
    c: Coincident(g9,g6)
    c: Coincident(g10,g2)
    c: Coincident(g11,g2)
    c: Coincident(g12,g4)
    c: Coincident(g13,g5)
    c: Symmetric(g12,g11,g-1)
    c: Equal(g11,g10)
    c: Equal(g11,g1)
    c: Equal(g11,g8)
    c: Equal(g11,g9)
    c: Equal(g11,g12)
    c: Equal(g11,g13)
    c: Diameter(g11) = 5
    c: DistanceY(g12,g10) = 231
    c: DistanceX(g2,g2) = 18
    c: Diameter(g14) = 8
    c: Symmetric(g14,g1,g-1)
FEATURE [PartDesign::Pocket] Pocket067
  BaseFeature = -> Pocket066
  Direction = (0,0,-1)
  Length = 5
  Length2 = 5
  Profile = -> Sketch123
  ReferenceAxis = -> Sketch123 [N_Axis]
  Reversed = true
  Suppressed = false
  Type = 0
FEATURE [PartDesign::Body] Body088  label="basement_amplifier_material_0.30ansi"
  AllowCompound = false
  Group = -> [Sketch121,BaseBend030,Sketch122,WireFilter003,Pocket066,Sketch123,Pocket067]
  Origin = -> Origin054
  Tip = -> Pocket067
FEATURE [Sketcher::SketchObject] Sketch128  label="door_base_pillar_sketch"
  ArcFitTolerance = 0
  FullyConstrained = true
  MakeInternals = false
  Raduis = 2
  Thickness = 1
  expr: Constraints[2] = <<Properties>>.endface_width / 2 + 25 mm
  expr: Constraints[3] = <<Properties>>.total_length + 5 mm
  expr: Constraints[5] = <<Properties>>.total_length - 15 mm
  sketch-geometry (2):
    g0: LineSegment StartX=39.5 StartY=336.872 StartZ=0 EndX=39.5 EndY=356.872 EndZ=0
    g1: LineSegment StartX=39.5 StartY=356.872 StartZ=0 EndX=69.3858 EndY=354.257 EndZ=0
  constraints (8):
    c: Vertical(g0)
    c: Coincident(g0,g1)
    c: DistanceX(g0) = 39.5
    c: DistanceY(g0) = 356.872
    c: Distance(g0,g1) = 30  'face_side'
    c: DistanceY(g0) = 336.872
    c: Angle(g1) = -0.0872665
    c: Distance(g0) = 20  'fix_side'
FEATURE [Sketcher::SketchObject] Sketch131  label="door_base_pillar_to_hor_fix_sketch"
  ArcFitTolerance = 0
  ExternalGeometry = -> [Sketch128]
  FullyConstrained = false
  MakeInternals = false
  Raduis = 2
  Thickness = 1
  expr: Constraints[6] = <<door_base_pillar_sketch>>.Thickness + Thickness + Raduis
  sketch-geometry (10):
    g0: LineSegment StartX=43.5 StartY=336.872 StartZ=0 EndX=43.5 EndY=352.506 EndZ=0
    g1: LineSegment StartX=43.5 StartY=352.506 StartZ=0 EndX=69.0372 EndY=350.272 EndZ=0
    g2: LineSegment [constr] StartX=39.5 StartY=336.872 StartZ=0 EndX=43.5 EndY=336.872 EndZ=0
    g3: LineSegment [constr] StartX=69.0372 StartY=350.272 StartZ=0 EndX=69.3858 EndY=354.257 EndZ=0
    g4: GeomPoint [constr] X=69.0372 Y=350.272 Z=0
    g5: GeomPoint [constr] X=43.5 Y=336.872 Z=0
    g6: ArcOfCircle CenterX=62.4098 CenterY=331.608 CenterZ=0 NormalX=0 NormalY=0 NormalZ=1 AngleXU=0 Radius=6 StartAngle=4.13024 EndAngle=5.83473
    g7: ArcOfCircle CenterX=68.5143 CenterY=344.295 CenterZ=0 NormalX=0 NormalY=0 NormalZ=1 AngleXU=0 Radius=6 StartAngle=5.83473 EndAngle=7.76672
    g8: LineSegment StartX=67.8165 StartY=329.006 StartZ=0 EndX=73.921 EndY=341.694 EndZ=0
    g9: LineSegment StartX=59.1109 StartY=326.596 StartZ=0 EndX=43.5 EndY=336.872 EndZ=0
  constraints (22):
    c: Coincident(g2,g-4)
    c: Coincident(g2,g0)
    c: Perpendicular(g-4,g2)
    c: Coincident(g3,g1)
    c: Coincident(g3,g-3)
    c: Perpendicular(g1,g3)
    c: Distance(g3) = 4
    c: Equal(g3,g2)
    c: Perpendicular(g-3,g3)
    c: Perpendicular(g2,g0)
    c: Coincident(g0,g1)
    c: PointOnObject(g4,g3)
    c: PointOnObject(g5,g2)
    c: Tangent(g7,g1) = 1.5708
    c: Tangent(g8,g6) = -1.5708
    c: Tangent(g8,g7) = -1.5708
    c: DistanceX(g6) = 62.4098
    c: DistanceY(g6) = 331.608
    c: Radius(g6) = 6
    c: Radius(g7) = 6
    c: Coincident(g9,g0)
    c: Tangent(g9,g6) = 1.5708
FEATURE [Sketcher::SketchObject] Sketch133  label="door_base_pillar_to_hor_fix_holes_sketch"
  ArcFitTolerance = 0
  ExternalGeometry = -> [Sketch131]
  FullyConstrained = false
  MakeInternals = false
  sketch-geometry (7):
    g0: Circle CenterX=68.34 CenterY=342.303 CenterZ=0 NormalX=0 NormalY=0 NormalZ=1 AngleXU=0 Radius=1.7
    g1: Circle CenterX=51.5 CenterY=336.872 CenterZ=0 NormalX=0 NormalY=0 NormalZ=1 AngleXU=0 Radius=1.7
    g2: Circle CenterX=62.5438 CenterY=331.451 CenterZ=0 NormalX=0 NormalY=0 NormalZ=1 AngleXU=0 Radius=1.7
    g3: LineSegment [constr] StartX=68.34 StartY=342.303 StartZ=0 EndX=62.5438 EndY=331.451 EndZ=0
    g4: LineSegment [constr] StartX=62.5438 StartY=331.451 StartZ=0 EndX=51.5 EndY=336.872 EndZ=0
    g5: LineSegment [constr] StartX=51.5 StartY=336.872 StartZ=0 EndX=43.5 EndY=336.872 EndZ=0
    g6: LineSegment [constr] StartX=69.0372 StartY=350.272 StartZ=0 EndX=68.34 EndY=342.303 EndZ=0
  constraints (16):
    c: Equal(g0,g2)
    c: Equal(g0,g1)
    c: Diameter(g0) = 3.4
    c: Coincident(g3,g0)
    c: Coincident(g3,g2)
    c: Coincident(g4,g2)
    c: Coincident(g4,g1)
    c: Distance(g1,g-3) = 8
    c: Coincident(g5,g1)
    c: Perpendicular(g-3,g5)
    c: Coincident(g6,g0)
    c: Equal(g4,g3)
    c: Coincident(g5,g-3)
    c: Coincident(g6,g-4)
    c: Equal(g6,g5)
    c: Perpendicular(g-4,g6)
FEATURE [Sketcher::SketchObject] Sketch138
  ArcFitTolerance = 0
  FullyConstrained = true
  MakeInternals = false
  expr: Constraints[4] = <<Properties>>.endface_width / 2
  expr: Constraints[5] = Sketch.Constraints.max_r
  sketch-geometry (7):
    g0: LineSegment [constr] StartX=0 StartY=0 StartZ=0 EndX=220.836 EndY=127.5 EndZ=0
    g1: LineSegment [constr] StartX=0 StartY=0 StartZ=0 EndX=14.5 EndY=351.872 EndZ=0
    g2: ArcOfCircle CenterX=14.5 CenterY=270.372 CenterZ=0 NormalX=0 NormalY=0 NormalZ=1 AngleXU=0 Radius=80 StartAngle=0.886335 EndAngle=1.5708
    g3: ArcOfCircle CenterX=-298.923 CenterY=-113.694 CenterZ=0 NormalX=0 NormalY=0 NormalZ=1 AngleXU=0 Radius=575.722 StartAngle=0.523599 EndAngle=0.886335
    g4: LineSegment StartX=225.167 StartY=130 StartZ=0 EndX=199.667 EndY=174.167 EndZ=0
    g5: LineSegment [constr] StartX=220.836 StartY=127.5 StartZ=0 EndX=225.167 EndY=130 EndZ=0
    g6: LineSegment StartX=14.5 StartY=350.372 StartZ=0 EndX=0 EndY=350.372 EndZ=0
  constraints (20):
    c: Coincident(g0,g-1)
    c: Angle(g0) = 0.523599
    c: Distance(g0,g0) = 255
    c: Coincident(g1,g0)
    c: DistanceX(g1) = 14.5
    c: Distance(g0,g1) = 352.17
    c: Vertical(g2,g2)
    c: Tangent(g3,g2) = -1.5708
    c: Tangent(g4,g3) = -1.5708
    c: Coincident(g5,g0)
    c: Coincident(g5,g4)
    c: Parallel(g5,g0)
    c: Distance(g5) = 5
    c: Perpendicular(g5,g4)
    c: Distance(g4) = 51
    c: Radius(g2) = 80
    c: PointOnObject(g6,g-2)
    c: Tangent(g2,g6) = -1.5708
    c: Vertical(g2,g1)
    c: DistanceY(g2,g1) = 1.5
FEATURE [Part::Mirroring] Part__Mirroring021  label="Sketch138 (Mirror #25)"
  Base = (0,0,0)
  Normal = (-0.5,0.866025,0)
  Source = -> Sketch138
  expr: .Normal.x = sin(-30)
  expr: .Normal.y = cos(-30)
FEATURE [Part::Compound] Compound045
  Links = -> [Part__Mirroring021,Sketch138]
FEATURE [Part::FeaturePython] Array007  # Draft array (typed FeaturePython)
  AlwaysSyncPlacement = false
  Angle = 360
  ArrayType = 1
  Axis = (0,0,1)
  Base = -> Compound045
  Center = (0,0,0)
  Count = 3
  ExpandArray = false
  Fuse = false
  IntervalAxis = (0,0,0)
  IntervalX = (50,0,0)
  IntervalY = (0,50,0)
  IntervalZ = (0,0,50)
  NumberCircles = 3
  NumberPolar = 3
  NumberX = 2
  NumberY = 2
  NumberZ = 1
  PlacementList = 3 placements: [(0,0,0),(0,0,0),(0,0,0)]
  RadialDistance = 50
  ScaleList = (3) [(1,1,1),(1,1,1),(1,1,1)]
  Symmetry = 1
  TangentialDistance = 25
FEATURE [Part::FeaturePython] Array008  # Draft array (typed FeaturePython)
  AlwaysSyncPlacement = false
  Angle = 360
  ArrayType = 1
  Axis = (0,0,1)
  Base = -> Clone005
  Center = (0,0,0)
  Count = 3
  ExpandArray = false
  Fuse = false
  IntervalAxis = (0,0,0)
  IntervalX = (50,0,0)
  IntervalY = (0,50,0)
  IntervalZ = (0,0,50)
  NumberCircles = 3
  NumberPolar = 3
  NumberX = 2
  NumberY = 2
  NumberZ = 1
  PlacementList = 3 placements: [(0,181.372,0),(-157.072,-90.6858,0),(157.072,-90.6858,0)]
  RadialDistance = 50
  ScaleList = (3) [(1,1,1),(1,1,1),(1,1,1)]
  Symmetry = 1
  TangentialDistance = 25
FEATURE [Part::FeaturePython] Placment007  # WARN: FeaturePython — macro-defined, semantics opaque (R4)
  AttacherType = Attacher::AttachEngine3D
  AttachmentOffset = pos=(0,0,0) rot=(-0.57735,-0.57735,-0.57735;2.0944rad)
  AttachmentSupport = -> [Sketch138]
  ExposePlacement = true
  MapMode = 7
  MarkerShape = 1
  MarkerSize = 5
  NumElements = 1
  Placement = pos=(225.167,130,0) rot=(0,0,-1;1.0472rad)
  Type = lattice2AttachablePlacement.AttachablePlacement
  isLattice = 1
FEATURE [Part::FeaturePython] Placment008  # WARN: FeaturePython — macro-defined, semantics opaque (R4)
  AttacherType = Attacher::AttachEngine3D
  AttachmentOffset = pos=(0,0,0) rot=(-0.57735,-0.57735,-0.57735;2.0944rad)
  AttachmentSupport = -> [Sketch138]
  ExposePlacement = true
  MapMode = 7
  MarkerShape = 1
  MarkerSize = 20
  NumElements = 1
  Placement = pos=(0,350.372,0) rot=(0,0,1;0rad)
  Type = lattice2AttachablePlacement.AttachablePlacement
  isLattice = 1
FEATURE [Part::FeaturePython] Join001  # WARN: FeaturePython — macro-defined, semantics opaque (R4)
  ExposePlacement = false
  Interleave = false
  Links = -> [Placment007,Placment008]
  MarkerShape = 1
  MarkerSize = 0
  NumElements = 2
  Type = lattice2JoinArrays.JoinArrays
  isLattice = 1
FEATURE [Part::FeaturePython] PolarArray001  # WARN: FeaturePython — macro-defined, semantics opaque (R4)
  Alignment = 0
  AttacherType = Attacher::AttachEngine3D
  CellStart = A1
  Count = 3
  DistributionLaw = 0
  EndInclusive = false
  ExposePlacement = false
  FlipX = false
  FlipZ = false
  GeneratorMode = 0
  MarkerShape = 1
  MarkerSize = 0
  NumElements = 3
  OrientMode = 2
  Radius = 50
  Reverse = false
  SpanEnd = 360
  SpanStart = 0
  Step = 120
  Type = lattice2PolarArray2.PolarArray
  UseArcRadius = false
  UseArcRange = 0
  VSGVersion = 1
  Values = 0.0 | 120.0 | 240.0
  ValuesSource = 2
  isLattice = 1
FEATURE [Part::FeaturePython] Populate020  label="Populate PolarArray001 with Join001"  # WARN: FeaturePython — macro-defined, semantics opaque (R4)
  Copying = 0
  ExposePlacement = false
  MarkerShape = 1
  MarkerSize = 0
  NumElements = 6
  Object = -> Join001
  OutputCompounding = 0
  PlacementsTo = -> PolarArray001
  Referencing = 1
  Type = lattice2PopulateCopies.LatticePopulateCopies
  isLattice = 1
FEATURE [Sketcher::SketchObject] Sketch139
  ArcFitTolerance = 0
  FullyConstrained = true
  MakeInternals = false
  sketch-geometry (2):
    g0: Circle CenterX=-10 CenterY=-10 CenterZ=0 NormalX=0 NormalY=0 NormalZ=1 AngleXU=0 Radius=1.7
    g1: Circle CenterX=10 CenterY=-10 CenterZ=0 NormalX=0 NormalY=0 NormalZ=1 AngleXU=0 Radius=1.7
  constraints (5):
    c: Symmetric(g0,g1,g-2)
    c: Equal(g0,g1)
    c: Diameter(g0) = 3.4
    c: DistanceX(g0,g1) = 20
    c: DistanceY(g1) = -10
FEATURE [Part::FeaturePython] Populate021  label="Populate Populate PolarArray001 with Join001 with Sketch139"  # WARN: FeaturePython — macro-defined, semantics opaque (R4)
  Copying = 0
  ExposePlacement = false
  MarkerShape = 1
  MarkerSize = 0
  NumElements = 0
  Object = -> Sketch139
  OutputCompounding = 1
  PlacementsTo = -> Populate020
  Referencing = 0
  Type = lattice2PopulateCopies.LatticePopulateCopies
  isLattice = 0
FEATURE [PartDesign::SubShapeBinder] Binder083
  BindCopyOnChange = 0
  BindMode = 0
  ClaimChildren = true
  Context = -> Body095 [Binder083.]
  Fuse = false
  MakeFace = true
  OffsetFill = false
  OffsetIntersection = false
  OffsetJoinType = 0
  OffsetOpenResult = false
  PartialLoad = false
  Relative = false
  Support = -> [Sketch128]
  _Version = 2
FEATURE [PartDesign::FeaturePython] BaseBend034  label="door_base_pillar_BaseBend"  # WARN: FeaturePython — macro-defined, semantics opaque (R4)
  BendSide = 0
  BendSketch = -> Binder083
  MidPlane = false
  Reverse = false
  Suppressed = false
  length = 1200
  radius = 2
  thickness = 1
FEATURE [Sketcher::SketchObject] Sketch141
  ArcFitTolerance = 0
  FullyConstrained = true
  MakeInternals = false
  Placement = pos=(0,0,0) rot=(1,0,0;1.5708rad)
  expr: Constraints[19] = <<Properties>>.total_height - 5 mm
  sketch-geometry (8):
    g0: LineSegment StartX=0 StartY=0 StartZ=0 EndX=44 EndY=0 EndZ=0
    g1: LineSegment StartX=44 StartY=0 StartZ=0 EndX=44 EndY=440 EndZ=0
    g2: LineSegment StartX=44 StartY=440 StartZ=0 EndX=0 EndY=440 EndZ=0
    g3: LineSegment StartX=0 StartY=440 StartZ=0 EndX=0 EndY=0 EndZ=0
    g4: LineSegment StartX=0 StartY=1423 StartZ=0 EndX=44 EndY=1423 EndZ=0
    g5: LineSegment StartX=44 StartY=1423 StartZ=0 EndX=44 EndY=1623 EndZ=0
    g6: LineSegment StartX=44 StartY=1623 StartZ=0 EndX=0 EndY=1623 EndZ=0
    g7: LineSegment StartX=0 StartY=1623 StartZ=0 EndX=0 EndY=1423 EndZ=0
  constraints (23):
    c: Coincident(g0,g1)
    c: Coincident(g1,g2)
    c: Coincident(g2,g3)
    c: Coincident(g3,g0)
    c: Horizontal(g0)
    c: Horizontal(g2)
    c: Vertical(g1)
    c: Vertical(g3)
    c: Coincident(g0,g-1)
    c: Coincident(g4,g5)
    c: Coincident(g5,g6)
    c: Coincident(g6,g7)
    c: Coincident(g7,g4)
    c: Horizontal(g4)
    c: Horizontal(g6)
    c: Vertical(g5)
    c: Vertical(g7)
    c: PointOnObject(g4,g-2)
    c: Vertical(g1,g4)
    c: DistanceY(g4) = 1423
    c: DistanceX(g1) = 44
    c: DistanceY(g3,g3) = 440
    c: DistanceY(g7,g7) = 200
FEATURE [PartDesign::SubShapeBinder] Binder092
  BindCopyOnChange = 0
  BindMode = 0
  ClaimChildren = true
  Context = -> Body095 [Binder092.]
  Fuse = false
  MakeFace = true
  OffsetFill = false
  OffsetIntersection = false
  OffsetJoinType = 0
  OffsetOpenResult = false
  PartialLoad = false
  Relative = true
  Support = -> [Sketch141]
  _Version = 2
FEATURE [PartDesign::Pocket] Pocket075
  BaseFeature = -> BaseBend034
  Direction = (0,-1,0)
  Length = 5
  Length2 = 5
  Midplane = true
  Profile = -> Binder092
  Suppressed = false
  Type = 1
FEATURE [PartDesign::SubShapeBinder] Binder093
  BindCopyOnChange = 0
  BindMode = 0
  ClaimChildren = true
  Fuse = false
  MakeFace = false
  OffsetFill = false
  OffsetIntersection = false
  OffsetJoinType = 0
  OffsetOpenResult = false
  PartialLoad = false
  Relative = true
  _Version = 2
FEATURE [PartDesign::Line] DatumLine002
  AttacherType = Attacher::AttachEngineLine
  Length = 20
  Placement = pos=(0,0,0) rot=(-0.250563,0.935113,0.250563;1.63783rad)
  ResizeMode = 0
FEATURE [PartDesign::SubShapeBinder] Binder094
  BindCopyOnChange = 0
  BindMode = 0
  ClaimChildren = true
  Fuse = false
  MakeFace = false
  OffsetFill = false
  OffsetIntersection = false
  OffsetJoinType = 0
  OffsetOpenResult = false
  PartialLoad = false
  Relative = true
  _Version = 2
FEATURE [Sketcher::SketchObject] Sketch144
  ArcFitTolerance = 0
  ExternalGeometry = -> [DatumLine002]
  FullyConstrained = false
  MakeInternals = false
  sketch-geometry (4):
    g0: LineSegment StartX=235.737 StartY=134.371 StartZ=0 EndX=234.987 EndY=135.67 EndZ=0
    g1: LineSegment StartX=235.737 StartY=134.371 StartZ=0 EndX=235.987 EndY=133.938 EndZ=0
    g2: LineSegment StartX=235.987 StartY=133.938 StartZ=0 EndX=236.487 EndY=133.072 EndZ=0
    g3: LineSegment StartX=236.487 StartY=133.072 StartZ=0 EndX=237.987 EndY=130.474 EndZ=0
  constraints (12):
    c: PointOnObject(g0,g-3)
    c: Perpendicular(g0,g-3)
    c: Distance(g0) = 1.5  'rivet_length'
    c: Coincident(g0,g1)
    c: Coincident(g1,g2)
    c: Parallel(g0,g1)
    c: Parallel(g1,g2)
    c: Distance(g1) = 0.5  'dec_thickness'
    c: Distance(g2) = 1  'corner_thickness'
    c: Coincident(g3,g2)
    c: Parallel(g2,g3)
    c: Distance(g3) = 3  'composit_thickness'
FEATURE [Sketcher::SketchObject] Sketch137  label="door_led_holder_sketch"
  ArcFitTolerance = 0
  ExternalGeometry = -> [Binder094,Sketch144]
  FullyConstrained = true
  MakeInternals = false
  expr: Constraints[32] = 10
  sketch-geometry (16):
    g0: LineSegment StartX=246.282 StartY=138.727 StartZ=0 EndX=237.622 EndY=133.727 EndZ=0
    g1: LineSegment StartX=237.622 StartY=133.727 StartZ=0 EndX=243.547 EndY=123.465 EndZ=0
    g2: LineSegment StartX=243.547 StartY=123.465 StartZ=0 EndX=249.955 EndY=127.165 EndZ=0
    g3: LineSegment StartX=249.955 StartY=127.165 StartZ=0 EndX=256.605 EndY=115.646 EndZ=0
    g4: LineSegment StartX=256.605 StartY=115.646 StartZ=0 EndX=250.197 EndY=111.946 EndZ=0
    g5: LineSegment StartX=250.197 StartY=111.946 StartZ=0 EndX=256.122 EndY=101.684 EndZ=0
    g6: LineSegment [constr] StartX=267.727 StartY=108.384 StartZ=0 EndX=262.727 EndY=117.044 EndZ=0
    g7: LineSegment [constr] StartX=250.197 StartY=111.946 StartZ=0 EndX=243.547 EndY=123.465 EndZ=0
    g8: LineSegment [constr] StartX=243.547 StartY=123.465 StartZ=0 EndX=243.64 EndY=123.403 EndZ=0
    g9: LineSegment [constr] StartX=250.197 StartY=111.946 StartZ=0 EndX=250.19 EndY=112.058 EndZ=0
    g10: LineSegment [constr] StartX=249.955 StartY=127.165 StartZ=0 EndX=249.962 EndY=127.053 EndZ=0
    g11: LineSegment [constr] StartX=256.512 StartY=115.708 StartZ=0 EndX=256.605 EndY=115.646 EndZ=0
    g12: LineSegment [constr] StartX=236.487 StartY=133.072 StartZ=0 EndX=237.622 EndY=133.727 EndZ=0
    g13: LineSegment [constr] StartX=256.605 StartY=115.646 StartZ=0 EndX=261.802 EndY=118.646 EndZ=0
    g14: LineSegment StartX=256.122 StartY=101.684 StartZ=0 EndX=264.782 EndY=106.684 EndZ=0
    g15: LineSegment [constr] StartX=264.782 StartY=106.684 StartZ=0 EndX=267.727 EndY=108.384 EndZ=0
  constraints (44):
    c: Coincident(g0,g1)
    c: Coincident(g1,g2)
    c: Coincident(g2,g3)
    c: Coincident(g3,g4)
    c: Coincident(g4,g5)
    c: Coincident(g5,g14)
    c: Coincident(g15,g6)
    c: Perpendicular(g4,g5)
    c: Perpendicular(g3,g4)
    c: Perpendicular(g3,g2)
    c: Perpendicular(g0,g1)
    c: Coincident(g7,g4)
    c: Coincident(g7,g1)
    c: Parallel(g7,g3)
    c: Perpendicular(g2,g1)
    c: Distance(g6) = 10
    c: Distance(g7) = 13.3
    c: Distance(g4) = 7.4
    c: Coincident(g8,g1)
    c: Coincident(g8,g-4)
    c: Coincident(g9,g4)
    c: Coincident(g9,g-3)
    c: Coincident(g10,g2)
    c: Coincident(g10,g-4)
    c: Equal(g10,g8)
    c: Equal(g8,g9)
    c: Coincident(g11,g-3)
    c: Coincident(g11,g3)
    c: Equal(g11,g10)
    c: Coincident(g12,g-5)
    c: Coincident(g12,g0)
    c: Perpendicular(g-5,g12)
    c: Distance(g0) = 10
    c: Coincident(g13,g3)
    c: Parallel(g13,g4)
    c: PointOnObject(g13,g6)
    c: Distance(g13) = 6
    c: Distance(g5) = 11.85
    c: Coincident(g14,g15)
    c: Perpendicular(g14,g6)
    c: Perpendicular(g15,g6)
    c: Perpendicular(g5,g14)
    c: Equal(g14,g0)
    c: Equal(g5,g1)
FEATURE [Sketcher::SketchObject] Sketch146
  ArcFitTolerance = 0
  ExternalGeometry = -> [Sketch137,Binder093]
  FullyConstrained = true
  MakeInternals = false
  sketch-geometry (4):
    g0: LineSegment StartX=230.997 StartY=129.902 StartZ=0 EndX=249.227 EndY=140.427 EndZ=0
    g1: LineSegment StartX=249.227 StartY=140.427 StartZ=0 EndX=267.727 EndY=108.384 EndZ=0
    g2: LineSegment StartX=249.497 StartY=97.859 StartZ=0 EndX=267.727 EndY=108.384 EndZ=0
    g3: LineSegment [constr] StartX=235.397 StartY=122.281 StartZ=0 EndX=230.997 EndY=129.902 EndZ=0
  constraints (12):
    c: Coincident(g0,g1)
    c: Coincident(g2,g1)
    c: Coincident(g3,g-4)
    c: Coincident(g3,g0)
    c: Perpendicular(g-4,g2)
    c: Parallel(g-4,g3)
    c: PointOnObject(g-3,g0)
    c: PointOnObject(g-3,g0)
    c: Perpendicular(g0,g1)
    c: Distance(g-5,g1) = 6
    c: PointOnObject(g2,g-4)
    c: PointOnObject(g-6,g2)
FEATURE [Sketcher::SketchObject] Sketch148
  ArcFitTolerance = 0
  ExternalGeometry = -> [Sketch146]
  FullyConstrained = true
  MakeInternals = false
  sketch-geometry (4):
    g0: LineSegment StartX=230.497 StartY=130.768 StartZ=0 EndX=250.892 EndY=142.543 EndZ=0
    g1: LineSegment StartX=250.892 StartY=142.543 StartZ=0 EndX=269.892 EndY=109.634 EndZ=0
    g2: LineSegment [constr] StartX=230.997 StartY=129.902 StartZ=0 EndX=230.497 EndY=130.768 EndZ=0
    g3: LineSegment [constr] StartX=267.727 StartY=108.384 StartZ=0 EndX=269.892 EndY=109.634 EndZ=0
  constraints (11):
    c: Coincident(g0,g1)
    c: Coincident(g2,g-4)
    c: Coincident(g2,g0)
    c: Coincident(g3,g-3)
    c: Coincident(g3,g1)
    c: Perpendicular(g3,g1)
    c: Perpendicular(g-3,g3)
    c: Perpendicular(g2,g-4)
    c: Perpendicular(g0,g2)
    c: Distance(g2) = 1
    c: Distance(g3) = 2.5
FEATURE [Part::Mirroring] Part__Mirroring023  label="door_base_pillar_sketch (Mirror #27)"
  Base = (0,0,0)
  Normal = (-0.5,0.866025,0)
  Source = -> Sketch128
  expr: .Normal.x = sin(-30)
  expr: .Normal.y = cos(-30)
FEATURE [Sketcher::SketchObject] Sketch153
  ArcFitTolerance = 0
  ExternalGeometry = -> [Sketch137]
  FullyConstrained = true
  MakeInternals = false
  Placement = pos=(0,0,0) rot=(0.935113,0.250563,0.250563;1.63783rad)
  sketch-geometry (4):
    g0: LineSegment StartX=0 StartY=0 StartZ=0 EndX=272.65 EndY=-1.31e-14 EndZ=0
    g1: LineSegment StartX=272.65 StartY=-1.31e-14 StartZ=0 EndX=272.65 EndY=1116 EndZ=0
    g2: LineSegment StartX=272.65 StartY=1116 StartZ=0 EndX=0 EndY=1116 EndZ=0
    g3: LineSegment StartX=0 StartY=1116 StartZ=0 EndX=0 EndY=0 EndZ=0
  constraints (10):
    c: Coincident(g0,g1)
    c: Coincident(g1,g2)
    c: Coincident(g2,g3)
    c: Coincident(g3,g0)
    c: Horizontal(g2)
    c: Vertical(g1)
    c: Vertical(g3)
    c: Coincident(g0,g-1)
    c: Coincident(g-3,g0)
    c: DistanceY(g1,g1) = 1116
FEATURE [Sketcher::SketchObject] Sketch152
  ArcFitTolerance = 0
  ExternalGeometry = -> [Part__Mirroring023,Sketch146,Sketch153]
  FullyConstrained = true
  MakeInternals = false
  sketch-geometry (12):
    g0: LineSegment StartX=313.489 StartY=-130.764 StartZ=0 EndX=327.029 EndY=-138.581 EndZ=0
    g1: LineSegment StartX=327.029 StartY=-138.581 StartZ=0 EndX=337.863 EndY=-115.348 EndZ=0
    g2: LineSegment StartX=337.863 StartY=-115.348 StartZ=0 EndX=267.995 EndY=103.92 EndZ=0
    g3: LineSegment StartX=258.122 StartY=98.2199 StartZ=0 EndX=313.489 EndY=-130.764 EndZ=0
    g4: LineSegment [constr] StartX=251.497 StartY=94.3949 StartZ=0 EndX=249.497 EndY=97.859 EndZ=0
    g5: LineSegment [constr] StartX=269.727 StartY=104.92 StartZ=0 EndX=267.727 EndY=108.384 EndZ=0
    g6: LineSegment [constr] StartX=311.489 StartY=-134.228 StartZ=0 EndX=313.489 EndY=-130.764 EndZ=0
    g7: LineSegment [constr] StartX=337.863 StartY=-115.348 StartZ=0 EndX=341.488 EndY=-117.039 EndZ=0
    g8: LineSegment [constr] StartX=236.122 StartY=136.325 StartZ=0 EndX=258.122 EndY=98.2199 EndZ=0
    g9: LineSegment [constr] StartX=258.122 StartY=98.2199 StartZ=0 EndX=251.497 EndY=94.3949 EndZ=0
    g10: LineSegment [constr] StartX=269.727 StartY=104.92 StartZ=0 EndX=267.995 EndY=103.92 EndZ=0
    g11: LineSegment StartX=267.995 StartY=103.92 StartZ=0 EndX=258.122 EndY=98.2199 EndZ=0
  constraints (31):
    c: Coincident(g0,g1)
    c: Coincident(g1,g2)
    c: Coincident(g3,g0)
    c: Coincident(g4,g9)
    c: Coincident(g4,g-5)
    c: Coincident(g5,g-5)
    c: Perpendicular(g-5,g5)
    c: Perpendicular(g-5,g4)
    c: Distance(g4) = 4
    c: Equal(g5,g4)
    c: Parallel(g0,g-4)
    c: Parallel(g1,g-3)
    c: Coincident(g6,g-4)
    c: Coincident(g6,g0)
    c: Coincident(g7,g1)
    c: Coincident(g7,g-3)
    c: Perpendicular(g7,g-3)
    c: Perpendicular(g6,g-4)
    c: Equal(g6,g7)
    c: Equal(g7,g4)
    c: Coincident(g8,g-6)
    c: Coincident(g11,g9)
    c: Perpendicular(g9,g8)
    c: Coincident(g11,g8)
    c: Coincident(g3,g11)
    c: Coincident(g10,g5)
    c: Coincident(g10,g11)
    c: Perpendicular(g10,g8)
    c: Perpendicular(g11,g8)
    c: Distance(g10,g10) = 2
    c: Coincident(g2,g10)
FEATURE [Sketcher::SketchObject] Sketch155
  ArcFitTolerance = 0
  ExternalGeometry = -> [Sketch152]
  FullyConstrained = true
  MakeInternals = false
  sketch-geometry (4):
    g0: LineSegment StartX=266.995 StartY=105.652 StartZ=0 EndX=255.826 EndY=99.2039 EndZ=0
    g1: LineSegment StartX=255.826 StartY=99.2039 StartZ=0 EndX=258.857 EndY=86.6692 EndZ=0
    g2: LineSegment [constr] StartX=258.857 StartY=86.6692 StartZ=0 EndX=260.801 EndY=87.1392 EndZ=0
    g3: LineSegment [constr] StartX=267.995 StartY=103.92 StartZ=0 EndX=266.995 EndY=105.652 EndZ=0
  constraints (12):
    c: Coincident(g1,g0)
    c: Coincident(g2,g1)
    c: PointOnObject(g2,g-4)
    c: Coincident(g3,g-3)
    c: Coincident(g3,g0)
    c: Perpendicular(g-3,g3)
    c: Perpendicular(g0,g3)
    c: Perpendicular(g2,g-4)
    c: Perpendicular(g1,g2)
    c: Equal(g2,g3)
    c: Distance(g3) = 2
    c: Equal(g1,g0)
FEATURE [Sketcher::SketchObject] Sketch159
  ArcFitTolerance = 0
  AttachmentSupport = -> [BaseBend034]
  FullyConstrained = true
  MakeInternals = false
  MapMode = 5
  Placement = pos=(40.5,0,0) rot=(0.57735,0.57735,0.57735;2.0944rad)
  sketch-geometry (2):
    g0: Circle CenterX=345 CenterY=1094 CenterZ=0 NormalX=0 NormalY=0 NormalZ=1 AngleXU=0 Radius=1.7
    g1: Circle CenterX=345 CenterY=154 CenterZ=0 NormalX=0 NormalY=0 NormalZ=1 AngleXU=0 Radius=1.7
  constraints (6):
    c: DistanceY(g0) = 1094
    c: DistanceY(g1,g0) = 940
    c: Equal(g0,g1)
    c: Diameter(g0) = 3.4
    c: Vertical(g1,g0)
    c: DistanceX(g0) = 345
FEATURE [Sketcher::SketchObject] Sketch160
  ArcFitTolerance = 0
  AttachmentSupport = -> [BaseBend034]
  FullyConstrained = true
  MakeInternals = false
  MapMode = 5
  Placement = pos=(31.1979,356.594,0) rot=(0.998099,-0.043578,-0.043578;1.5727rad)
  sketch-geometry (8):
    g0: Circle CenterX=17.5 CenterY=1094 CenterZ=0 NormalX=0 NormalY=0 NormalZ=1 AngleXU=0 Radius=1.7
    g1: Circle CenterX=33.5 CenterY=1094 CenterZ=0 NormalX=0 NormalY=0 NormalZ=1 AngleXU=0 Radius=1.7
    g2: Circle CenterX=17.5 CenterY=154 CenterZ=0 NormalX=0 NormalY=0 NormalZ=1 AngleXU=0 Radius=1.7
    g3: Circle CenterX=33.5 CenterY=154 CenterZ=0 NormalX=0 NormalY=0 NormalZ=1 AngleXU=0 Radius=1.7
    g4: LineSegment [constr] StartX=17.5 StartY=154 StartZ=0 EndX=33.5 EndY=154 EndZ=0
    g5: LineSegment [constr] StartX=33.5 StartY=154 StartZ=0 EndX=33.5 EndY=1094 EndZ=0
    g6: LineSegment [constr] StartX=33.5 StartY=1094 StartZ=0 EndX=17.5 EndY=1094 EndZ=0
    g7: LineSegment [constr] StartX=17.5 StartY=1094 StartZ=0 EndX=17.5 EndY=154 EndZ=0
  constraints (20):
    c: Equal(g0,g1)
    c: Diameter(g0) = 3.4
    c: Equal(g2,g3)
    c: Equal(g3,g0)
    c: Coincident(g4,g5)
    c: Coincident(g5,g6)
    c: Coincident(g6,g7)
    c: Coincident(g7,g4)
    c: Horizontal(g4)
    c: Horizontal(g6)
    c: Vertical(g5)
    c: Vertical(g7)
    c: Coincident(g4,g2)
    c: Coincident(g5,g1)
    c: Coincident(g4,g3)
    c: Coincident(g6,g0)
    c: DistanceY(g0) = 1094
    c: DistanceY(g7,g7) = 940
    c: DistanceX(g6,g6) = 16
    c: DistanceX(g0) = 17.5
FEATURE [Sketcher::SketchObject] Sketch161
  ArcFitTolerance = 0
  AttachmentSupport = -> [BaseBend034]
  FullyConstrained = true
  MakeInternals = false
  MapMode = 5
  Placement = pos=(40.5,0,0) rot=(0.57735,0.57735,0.57735;2.0944rad)
  sketch-geometry (8):
    g0: Circle CenterX=343.262 CenterY=363.2 CenterZ=0 NormalX=0 NormalY=0 NormalZ=1 AngleXU=0 Radius=2
    g1: Circle CenterX=343.262 CenterY=300 CenterZ=0 NormalX=0 NormalY=0 NormalZ=1 AngleXU=0 Radius=2
    g2: Circle CenterX=343.262 CenterY=1063 CenterZ=0 NormalX=0 NormalY=0 NormalZ=1 AngleXU=0 Radius=2
    g3: Circle CenterX=343.262 CenterY=999.8 CenterZ=0 NormalX=0 NormalY=0 NormalZ=1 AngleXU=0 Radius=2
    g4: LineSegment [constr] StartX=343.262 StartY=1063 StartZ=0 EndX=343.262 EndY=999.8 EndZ=0
    g5: LineSegment [constr] StartX=343.262 StartY=999.8 StartZ=0 EndX=343.262 EndY=363.2 EndZ=0
    g6: LineSegment [constr] StartX=343.262 StartY=363.2 StartZ=0 EndX=343.262 EndY=300 EndZ=0
    g7: GeomPoint [constr] X=353.262 Y=301.263 Z=0
  constraints (21):
    c: Coincident(g4,g2)
    c: Vertical(g4)
    c: Coincident(g4,g5)
    c: Coincident(g5,g0)
    c: Vertical(g5)
    c: Coincident(g5,g6)
    c: Coincident(g6,g1)
    c: Vertical(g6)
    c: Coincident(g4,g3)
    c: Equal(g4,g6)
    c: DistanceY(g6,g6) = 63.2
    c: DistanceY(g2) = 1063
    c: DistanceY(g1) = 300
    c: Equal(g1,g0)
    c: Equal(g1,g3)
    c: Equal(g1,g2)
    c: Diameter(g1) = 4
    c: DistanceX(g1) = 343.262
    c: DistanceX(g7) = 353.262
    c: DistanceY(g7) = 301.263
    c: DistanceX(g1,g7) = 10
FEATURE [Sketcher::SketchObject] Sketch162
  ArcFitTolerance = 0
  AttachmentSupport = -> [BaseBend034]
  FullyConstrained = true
  MakeInternals = false
  MapMode = 5
  Placement = pos=(31.1979,356.594,0) rot=(0.998099,-0.043578,-0.043578;1.5727rad)
  sketch-geometry (11):
    g0: LineSegment [constr] StartX=20 StartY=15 StartZ=0 EndX=20 EndY=250 EndZ=0
    g1: LineSegment [constr] StartX=20 StartY=250 StartZ=0 EndX=20 EndY=485 EndZ=0
    g2: LineSegment [constr] StartX=20 StartY=485 StartZ=0 EndX=20 EndY=720 EndZ=0
    g3: LineSegment [constr] StartX=20 StartY=720 StartZ=0 EndX=20 EndY=955 EndZ=0
    g4: LineSegment [constr] StartX=20 StartY=955 StartZ=0 EndX=20 EndY=1190 EndZ=0
    g5: Circle CenterX=20 CenterY=15 CenterZ=0 NormalX=0 NormalY=0 NormalZ=1 AngleXU=0 Radius=1.7
    g6: Circle CenterX=20 CenterY=250 CenterZ=0 NormalX=0 NormalY=0 NormalZ=1 AngleXU=0 Radius=1.7
    g7: Circle CenterX=20 CenterY=485 CenterZ=0 NormalX=0 NormalY=0 NormalZ=1 AngleXU=0 Radius=1.7
    g8: Circle CenterX=20 CenterY=720 CenterZ=0 NormalX=0 NormalY=0 NormalZ=1 AngleXU=0 Radius=1.7
    g9: Circle CenterX=20 CenterY=955 CenterZ=0 NormalX=0 NormalY=0 NormalZ=1 AngleXU=0 Radius=1.7
    g10: Circle CenterX=20 CenterY=1190 CenterZ=0 NormalX=0 NormalY=0 NormalZ=1 AngleXU=0 Radius=1.7
  constraints (24):
    c: Vertical(g0)
    c: Coincident(g0,g1)
    c: Vertical(g1)
    c: Coincident(g1,g2)
    c: Vertical(g2)
    c: Coincident(g2,g3)
    c: Vertical(g3)
    c: Coincident(g3,g4)
    c: Vertical(g4)
    c: Equal(g0,g1)
    c: Equal(g1,g2)
    c: Equal(g2,g3)
    c: Equal(g3,g4)
    c: Coincident(g5,g0)
    c: Coincident(g6,g0)
    c: Coincident(g7,g1)
    c: Coincident(g8,g2)
    c: Coincident(g9,g3)
    c: Coincident(g10,g4)
    c: Equal(g5, g6-g10) x5
    c: Diameter(g5) = 3.4
    c: DistanceY(g10) = 1190
    c: DistanceY(g5) = 15
    c: DistanceX(g5) = 20
FEATURE [PartDesign::Pocket] Pocket095
  BaseFeature = -> Pocket075
  Direction = (0.0871557,0.996195,3e-16)
  Length = 5
  Length2 = 5
  Profile = -> Sketch162
  ReferenceAxis = -> Sketch162 [N_Axis]
  Suppressed = false
  Type = 0
FEATURE [PartDesign::Pocket] Pocket094
  BaseFeature = -> Pocket095
  Direction = (-1,0,0)
  Length = 5
  Length2 = 5
  Profile = -> Sketch161
  ReferenceAxis = -> Sketch161 [N_Axis]
  Suppressed = false
  Type = 0
FEATURE [PartDesign::Pocket] Pocket090
  BaseFeature = -> Pocket094
  Direction = (-1,0,0)
  Length = 5
  Length2 = 5
  Profile = -> Sketch159
  ReferenceAxis = -> Sketch159 [N_Axis]
  Suppressed = false
  Type = 0
FEATURE [PartDesign::Pocket] Pocket091
  BaseFeature = -> Pocket090
  Direction = (0.0871557,0.996195,3e-16)
  Length = 5
  Length2 = 5
  Profile = -> Sketch160
  ReferenceAxis = -> Sketch160 [N_Axis]
  Suppressed = false
  Type = 0
FEATURE [PartDesign::Body] Body095  label="door_base_pillar_material_0.45ansi"
  AllowCompound = false
  Group = -> [Binder083,BaseBend034,Pocket075,Binder092,Sketch159,Sketch160,Sketch161,Sketch162,Pocket095,Pocket094,Pocket090,Pocket091]
  Origin = -> Origin061
  Tip = -> Pocket091
FEATURE [Part::Compound] Compound047
  Links = -> [Body095]
FEATURE [Sketcher::SketchObject] Sketch166
  ArcFitTolerance = 0
  AttachmentOffset = pos=(349.171,0,0) rot=(0,0,1;0rad)
  AttachmentSupport = -> [YZ_Plane010]
  FullyConstrained = true
  MakeInternals = false
  MapMode = 5
  Placement = pos=(0,349.171,0) rot=(0.57735,0.57735,0.57735;2.0944rad)
  expr: .AttachmentOffset.Base.x = <<basement_sketch>>.Constraints.max_r
  sketch-geometry (3):
    g0: LineSegment StartX=-15 StartY=0 StartZ=0 EndX=0 EndY=15 EndZ=0
    g1: LineSegment StartX=0 StartY=15 StartZ=0 EndX=0 EndY=0 EndZ=0
    g2: LineSegment StartX=0 StartY=0 StartZ=0 EndX=-15 EndY=0 EndZ=0
  constraints (8):
    c: PointOnObject(g0,g-1)
    c: PointOnObject(g0,g-2)
    c: Coincident(g0,g1)
    c: Coincident(g1,g-1)
    c: Coincident(g1,g2)
    c: Coincident(g2,g0)
    c: Equal(g2,g1)
    c: DistanceY(g1,g1) = 15
FEATURE [Sketcher::SketchObject] Sketch167  label="basement_amplifier_sketch"
  ArcFitTolerance = 0
  AttachmentSupport = -> [XY_Plane078]
  FullyConstrained = true
  MakeInternals = false
  MapMode = 5
  sketch-geometry (10):
    g0: LineSegment StartX=-25 StartY=320.166 StartZ=0 EndX=25 EndY=320.166 EndZ=0
    g1: LineSegment StartX=80 StartY=46.188 StartZ=0 EndX=0 EndY=0 EndZ=0
    g2: LineSegment StartX=0 StartY=0 StartZ=0 EndX=-80 EndY=46.188 EndZ=0
    g3: LineSegment StartX=25 StartY=320.166 StartZ=0 EndX=79.5375 EndY=48.492 EndZ=0
    g4: LineSegment StartX=79.5375 StartY=48.492 StartZ=0 EndX=80 EndY=46.188 EndZ=0
    g5: LineSegment StartX=-80 StartY=46.188 StartZ=0 EndX=-79.5375 EndY=48.492 EndZ=0
    g6: LineSegment StartX=-79.5375 StartY=48.492 StartZ=0 EndX=-25 EndY=320.166 EndZ=0
    g7: LineSegment [constr] StartX=-79.7343 StartY=47.5116 StartZ=0 EndX=-83.6561 EndY=48.2988 EndZ=0
    g8: LineSegment [constr] StartX=-83.6561 StartY=48.2988 StartZ=0 EndX=-81.0134 EndY=45.2961 EndZ=0
    g9: LineSegment [constr] StartX=-81.0134 StartY=45.2961 StartZ=0 EndX=-80 EndY=46.188 EndZ=0
  constraints (27):
    c: Coincident(g2,g5)
    c: Coincident(g6,g0)
    c: Coincident(g0,g3)
    c: Coincident(g4,g1)
    c: Symmetric(g1,g2,g-2)
    c: Symmetric(g0,g6,g-2)
    c: DistanceX(g0,g0) = 50
    c: DistanceY(g6) = 320.166  'length'
    c: DistanceX(g2,g1) = 160
    c: Coincident(g1,g2)
    c: Coincident(g3,g4)
    c: Symmetric(g5,g3,g-2)
    c: Coincident(g8,g7)
    c: Perpendicular(g5,g7)
    c: Equal(g8,g7)
    c: Distance(g7) = 4
    c: PointOnObject(g7,g5)
    c: Coincident(g6,g5)
    c: Distance(g7,g5) = 1
    c: Distance(g2) = 92.376  'inner_r'
    c: Angle(g1) = -2.61799
    c: Coincident(g9,g8)
    c: Coincident(g9,g2)
    c: Symmetric(g8,g7,g2)
    c: Parallel(g5,g6)
    c: Coincident(g1,g-1)
    c: Angle(g5,g9) = 2.49062  'connection_angle'
FEATURE [PartDesign::FeaturePython] BaseBend043  # WARN: FeaturePython — macro-defined, semantics opaque (R4)
  BendSide = 0
  BendSketch = -> Sketch167
  MidPlane = false
  Reverse = false
  Suppressed = false
  length = 100
  radius = 2
  thickness = 2
FEATURE [PartDesign::FeaturePython] Bend025  # WARN: FeaturePython — macro-defined, semantics opaque (R4)
  AutoMiter = false
  BaseFeature = -> BaseBend043
  BendType = 0
  LengthList = [100]
  LengthSpec = 0
  NonperforationMaxLength = 5
  Perforate = false
  PerforationAngle = 0
  PerforationInitialLength = 5
  PerforationMaxLength = 5
  ReliefFactor = 0.7
  Suppressed = false
  UseReliefFactor = false
  angle = 90
  baseObject = -> BaseBend043 [Edge21,Edge7]
  bendAList = [90]
  extend1 = 0
  extend2 = 0
  gap1 = 0
  gap2 = 0
  invert = true
  kfactor = 0.5
  length = 100
  maxExtendDist = 5
  minGap = 0.1
  minReliefGap = 1
  miterangle1 = 18.649
  miterangle2 = 18.649
  offset = 0
  radius = 2
  reliefType = 0
  reliefd = 1
  reliefw = 0.8
  sketchflip = false
  sketchinvert = false
  unfold = false
  expr: miterangle1 = 90 deg - Sketch167.Constraints.connection_angle / 2
  expr: miterangle2 = miterangle1
  expr: radius = BaseBend043.radius
FEATURE [Sketcher::SketchObject] Sketch170
  ArcFitTolerance = 0
  AttachmentSupport = -> [YZ_Plane078]
  FullyConstrained = false
  MakeInternals = false
  MapMode = 5
  Placement = pos=(0,0,0) rot=(0.57735,0.57735,0.57735;2.0944rad)
  expr: Constraints[10] = <<basement_amplifier_sketch>>.Constraints.length
  sketch-geometry (11):
    g0: LineSegment StartX=320.166 StartY=-15 StartZ=0 EndX=320.166 EndY=2 EndZ=0
    g1: LineSegment StartX=320.166 StartY=2 StartZ=0 EndX=0 EndY=2 EndZ=0
    g2: LineSegment StartX=0 StartY=2 StartZ=0 EndX=0 EndY=-60 EndZ=0
    g3: LineSegment StartX=0 StartY=-60 StartZ=0 EndX=125.378 EndY=-25.2665 EndZ=0
    g4: LineSegment StartX=133.266 StartY=-24 StartZ=0 EndX=320.166 EndY=-15 EndZ=0
    g5: ArcOfCircle CenterX=135 CenterY=-60 CenterZ=0 NormalX=0 NormalY=0 NormalZ=1 AngleXU=0 Radius=36.0417 StartAngle=1.61891 EndAngle=1.84105
    g6: GeomPoint [constr] X=129.251 Y=-24.1933 Z=0
    g7: LineSegment StartX=-219.815 StartY=310.193 StartZ=0 EndX=564.966 EndY=310.193 EndZ=0
    g8: LineSegment StartX=564.966 StartY=310.193 StartZ=0 EndX=564.966 EndY=-309.063 EndZ=0
    g9: LineSegment StartX=564.966 StartY=-309.063 StartZ=0 EndX=-219.815 EndY=-309.063 EndZ=0
    g10: LineSegment StartX=-219.815 StartY=-309.063 StartZ=0 EndX=-219.815 EndY=310.193 EndZ=0
  constraints (27):
    c: Vertical(g0)
    c: Coincident(g0,g1)
    c: Horizontal(g1)
    c: PointOnObject(g2,g-2)
    c: Coincident(g4,g0)
    c: Coincident(g2,g1)
    c: Vertical(g2)
    c: DistanceY(g-1,g1) = 2
    c: DistanceY(g0,g1) = 17
    c: DistanceY(g2) = -60
    c: DistanceX(g1,g1) = 320.166
    c: PointOnObject(g6,g4)
    c: PointOnObject(g6,g3)
    c: Tangent(g4,g5) = 1.5708
    c: Tangent(g3,g5) = 1.5708
    c: Coincident(g7,g8)
    c: Coincident(g8,g9)
    c: Coincident(g9,g10)
    c: Coincident(g10,g7)
    c: Horizontal(g7)
    c: Horizontal(g9)
    c: Vertical(g8)
    c: Vertical(g10)
    c: DistanceY(g4) = -24
    c: DistanceX(g5) = 135
    c: Coincident(g3,g2)
    c: Horizontal(g5,g2)
FEATURE [Sketcher::SketchObject] Sketch171  label="basement2_sketch"
  ArcFitTolerance = 0
  AttachmentSupport = -> [XY_Plane080]
  FullyConstrained = true
  MakeInternals = false
  MapMode = 5
  sketch-geometry (10):
    g0: LineSegment StartX=-80 StartY=46.188 StartZ=0 EndX=2.84e-14 EndY=-4.97e-14 EndZ=0
    g1: LineSegment StartX=2.84e-14 StartY=-4.97e-14 StartZ=0 EndX=80 EndY=46.188 EndZ=0
    g2: LineSegment StartX=80 StartY=46.188 StartZ=0 EndX=79.7011 EndY=48.0916 EndZ=0
    g3: LineSegment StartX=79.7011 StartY=48.0916 StartZ=0 EndX=42.5 EndY=285 EndZ=0
    g4: LineSegment StartX=42.5 StartY=285 StartZ=0 EndX=-42.5 EndY=285 EndZ=0
    g5: LineSegment StartX=-42.5 StartY=285 StartZ=0 EndX=-79.7011 EndY=48.0916 EndZ=0
    g6: LineSegment StartX=-79.7011 StartY=48.0916 StartZ=0 EndX=-80 EndY=46.188 EndZ=0
    g7: LineSegment [constr] StartX=80 StartY=46.188 StartZ=0 EndX=81.4991 EndY=44.9774 EndZ=0
    g8: LineSegment [constr] StartX=81.4991 StartY=44.9774 StartZ=0 EndX=84.6406 EndY=48.8672 EndZ=0
    g9: LineSegment [constr] StartX=84.6406 StartY=48.8672 StartZ=0 EndX=79.7011 EndY=48.0916 EndZ=0
  constraints (26):
    c: Coincident(g0,g-1)
    c: Coincident(g0,g1)
    c: Coincident(g1,g2)
    c: Coincident(g2,g3)
    c: Coincident(g3,g4)
    c: Coincident(g4,g5)
    c: Coincident(g5,g6)
    c: Coincident(g6,g0)
    c: Symmetric(g0,g1,g-2)
    c: Symmetric(g4,g3,g-2)
    c: Symmetric(g5,g2,g-2)
    c: Parallel(g2,g3)
    c: Angle(g1) = 0.523599
    c: Coincident(g7,g1)
    c: Symmetric(g7,g2,g1)
    c: DistanceX(g4,g4) = 85
    c: DistanceY(g3) = 285
    c: Coincident(g8,g7)
    c: Coincident(g9,g8)
    c: Coincident(g9,g2)
    c: Perpendicular(g2,g9)
    c: Perpendicular(g7,g8)
    c: Distance(g9) = 5
    c: Distance(g1) = 92.376  'inner_r'
    c: Angle(g7,g2) = 2.40591  'connection_angle'
    c: DistanceX(g0,g1) = 160
FEATURE [PartDesign::FeaturePython] BaseBend044  # WARN: FeaturePython — macro-defined, semantics opaque (R4)
  BendSide = 0
  BendSketch = -> Sketch171
  MidPlane = false
  Reverse = false
  Suppressed = false
  length = 100
  radius = 2
  thickness = 2
FEATURE [PartDesign::FeaturePython] Bend026  # WARN: FeaturePython — macro-defined, semantics opaque (R4)
  AutoMiter = false
  BaseFeature = -> BaseBend044
  BendType = 0
  LengthList = [30]
  LengthSpec = 0
  NonperforationMaxLength = 5
  Perforate = false
  PerforationAngle = 0
  PerforationInitialLength = 5
  PerforationMaxLength = 5
  ReliefFactor = 0.7
  Suppressed = false
  UseReliefFactor = false
  angle = 90
  baseObject = -> BaseBend044 [Edge19,Edge13]
  bendAList = [90]
  extend1 = 0
  extend2 = 0
  gap1 = 0
  gap2 = 0
  invert = false
  kfactor = 0.5
  length = 30
  maxExtendDist = 5
  minGap = 0.1
  minReliefGap = 1
  miterangle1 = 21.0759
  miterangle2 = 21.0759
  offset = 0
  radius = 2
  reliefType = 0
  reliefd = 1
  reliefw = 0.8
  sketchflip = false
  sketchinvert = false
  unfold = false
  expr: miterangle1 = 90 deg - <<basement2_sketch>>.Constraints.connection_angle / 2
  expr: miterangle2 = miterangle1
  expr: radius = BaseBend044.radius
FEATURE [PartDesign::Plane] DatumPlane005
  AttachmentOffset = pos=(0,0,0) rot=(0,-1,0;1.5708rad)
  AttachmentSupport = -> [Sketch167]
  Length = 647.453
  MapMode = 7
  Placement = pos=(-79.5375,48.492,0) rot=(0.501242,-0.611865,-0.611865;2.21231rad)
  ResizeMode = 0
  Width = 88.0953
FEATURE [PartDesign::Line] DatumLine003
  AttacherType = Attacher::AttachEngineLine
  AttachmentOffset = pos=(0,0,0) rot=(0,1,0;1.5708rad)
  AttachmentSupport = -> [Sketch170]
  Length = 20
  MapMode = 24
  Placement = pos=(0,0,-60) rot=(0,1,0;1.5708rad)
  ResizeMode = 0
FEATURE [PartDesign::Line] DatumLine004
  AttacherType = Attacher::AttachEngineLine
  AttachmentOffset = pos=(0,0,0) rot=(0,1,0;1.5708rad)
  AttachmentSupport = -> [Sketch170]
  Length = 20
  MapMode = 24
  Placement = pos=(0,133.266,-24) rot=(0.58639,0.558832,0.58639;2.1224rad)
  ResizeMode = 0
FEATURE [Sketcher::SketchObject] Sketch173
  ArcFitTolerance = 0
  AttachmentOffset = pos=(0,0,4) rot=(0,0,1;0rad)
  AttachmentSupport = -> [DatumPlane005]
  ExternalGeometry = -> [Sketch167]
  FullyConstrained = false
  MakeInternals = false
  MapMode = 5
  Placement = pos=(-83.4592,49.2793,0) rot=(-0.501242,0.611865,0.611865;4.07087rad)
  sketch-geometry (9):
    g0: LineSegment StartX=49.4595 StartY=-30.4174 StartZ=0 EndX=49.4595 EndY=2 EndZ=0
    g1: LineSegment StartX=-86.4657 StartY=-24 StartZ=0 EndX=-277.094 EndY=-15 EndZ=0
    g2: LineSegment StartX=-277.094 StartY=-15 StartZ=0 EndX=-277.094 EndY=2 EndZ=0
    g3: LineSegment StartX=-277.094 StartY=2 StartZ=0 EndX=49.4595 EndY=2 EndZ=0
    g4: LineSegment StartX=-568.045 StartY=-343.581 StartZ=0 EndX=236.236 EndY=-343.581 EndZ=0
    g5: LineSegment StartX=236.236 StartY=-343.581 StartZ=0 EndX=236.236 EndY=220.397 EndZ=0
    g6: LineSegment StartX=236.236 StartY=220.397 StartZ=0 EndX=-568.045 EndY=220.397 EndZ=0
    g7: LineSegment StartX=-568.045 StartY=220.397 StartZ=0 EndX=-568.045 EndY=-343.581 EndZ=0
    g8: LineSegment StartX=-86.4657 StartY=-24 StartZ=0 EndX=49.4595 EndY=-30.4174 EndZ=0
  constraints (22):
    c: Coincident(g2,g1)
    c: Vertical(g2)
    c: Coincident(g3,g2)
    c: Horizontal(g3)
    c: Coincident(g3,g0)
    c: DistanceY(g0) = 2
    c: DistanceY(g1) = -15
    c: Coincident(g4,g5)
    c: Coincident(g5,g6)
    c: Coincident(g6,g7)
    c: Coincident(g7,g4)
    c: Horizontal(g4)
    c: Horizontal(g6)
    c: Vertical(g5)
    c: Vertical(g7)
    c: PointOnObject(g-5,g2)
    c: Coincident(g1,g-4) = -1.5708
    c: Coincident(g8,g1)
    c: Coincident(g8,g0)
    c: Parallel(g8,g1)
    c: Vertical(g0)
    c: PointOnObject(g-3,g0)
FEATURE [PartDesign::Pocket] Pocket104
  BaseFeature = -> Bend025
  Direction = (0.98044,-0.19682,0)
  Length = 2
  Length2 = 5
  Profile = -> Sketch173
  ReferenceAxis = -> Sketch173 [N_Axis]
  Suppressed = false
  Type = 0
FEATURE [PartDesign::Fillet] Fillet011
  Base = -> Pocket104 [Edge57,Edge56]
  BaseFeature = -> Pocket104
  Radius = 10
  SupportTransform = false
  Suppressed = false
  UseAllEdges = false
FEATURE [Sketcher::SketchObject] Sketch174
  ArcFitTolerance = 0
  AttachmentSupport = -> [XY_Plane080]
  ExternalGeometry = -> [Sketch171]
  FullyConstrained = true
  MakeInternals = false
  MapMode = 5
  sketch-geometry (7):
    g0: LineSegment StartX=44.3713 StartY=273.083 StartZ=0 EndX=49.3108 EndY=273.858 EndZ=0
    g1: LineSegment StartX=49.3108 StartY=273.858 StartZ=0 EndX=4.93947 EndY=556.429 EndZ=0
    g2: LineSegment StartX=4.93947 StartY=556.429 StartZ=0 EndX=0 EndY=555.654 EndZ=0
    g3: LineSegment StartX=42.5 StartY=285 StartZ=0 EndX=38.2239 EndY=285 EndZ=0
    g4: LineSegment StartX=43.1633 StartY=280.776 StartZ=0 EndX=44.3713 EndY=273.083 EndZ=0
    g5: LineSegment StartX=0 StartY=555.654 StartZ=0 EndX=42.5 EndY=285 EndZ=0
    g6: ArcOfCircle CenterX=38.2239 CenterY=280 CenterZ=0 NormalX=0 NormalY=0 NormalZ=1 AngleXU=0 Radius=5 StartAngle=0.155755 EndAngle=1.5708
  constraints (20):
    c: Coincident(g0,g1)
    c: Coincident(g1,g2)
    c: Coincident(g2,g5)
    c: Coincident(g4,g0)
    c: Parallel(g0,g2)
    c: Perpendicular(g1,g0)
    c: PointOnObject(g0,g-3)
    c: PointOnObject(g2,g-3)
    c: DistanceY(g0) = 273.083
    c: PointOnObject(g2,g-2)
    c: Distance(g0) = 5
    c: Coincident(g3,g-3)
    c: Horizontal(g3)
    c: Parallel(g1,g4)
    c: Parallel(g1,g5)
    c: Coincident(g5,g3)
    c: Tangent(g6,g4) = 1.5708
    c: Tangent(g6,g3) = -1.5708
    c: Radius(g6) = 5
    c: Distance(g3,g0) = 12.0632
FEATURE [PartDesign::Pocket] Pocket105
  BaseFeature = -> Bend026
  Direction = (0,0,-1)
  Length = 5
  Length2 = 5
  Midplane = true
  Profile = -> Sketch174
  ReferenceAxis = -> Sketch174 [N_Axis]
  Suppressed = false
  Type = 1
FEATURE [PartDesign::Mirrored] Mirrored011
  BaseFeature = -> Pocket105
  MirrorPlane = -> Sketch174 [V_Axis]
  Originals = -> [Pocket105]
  Refine = true
  Suppressed = false
  TransformMode = 0
FEATURE [PartDesign::SubShapeBinder] Binder117
  BindCopyOnChange = 0
  BindMode = 0
  ClaimChildren = false
  Context = -> Body107 [Binder117.]
  Fuse = false
  MakeFace = true
  OffsetFill = false
  OffsetIntersection = false
  OffsetJoinType = 0
  OffsetOpenResult = false
  PartialLoad = false
  Relative = true
  Support = -> [Body007[Binder066.Binder064.]]
  _Version = 2
FEATURE [PartDesign::SubShapeBinder] Binder118
  BindCopyOnChange = 0
  BindMode = 0
  ClaimChildren = false
  Context = -> Body105 [Binder118.]
  Fuse = false
  MakeFace = true
  OffsetFill = false
  OffsetIntersection = false
  OffsetJoinType = 0
  OffsetOpenResult = false
  PartialLoad = false
  Relative = true
  Support = -> [Body006[Binder069.]]
  _Version = 2
FEATURE [PartDesign::SubShapeBinder] Binder119
  BindCopyOnChange = 0
  BindMode = 0
  ClaimChildren = false
  Context = -> Body105 [Binder119.]
  Fuse = false
  MakeFace = true
  OffsetFill = false
  OffsetIntersection = false
  OffsetJoinType = 0
  OffsetOpenResult = false
  PartialLoad = false
  Relative = true
  Support = -> [Body006[Pocket061.Sketch112.]]
  _Version = 2
FEATURE [PartDesign::Pocket] Pocket108
  BaseFeature = -> Fillet011
  Direction = (0,0,-1)
  Length = 5
  Length2 = 5
  Midplane = true
  Profile = -> Binder119
  Suppressed = false
  Type = 1
FEATURE [Sketcher::SketchObject] Sketch175
  ArcFitTolerance = 0
  AttachmentSupport = -> [XY_Plane078]
  ExternalGeometry = -> [Sketch167]
  FullyConstrained = true
  MakeInternals = false
  MapMode = 5
  sketch-geometry (6):
    g0: Circle CenterX=43.3161 CenterY=155 CenterZ=0 NormalX=0 NormalY=0 NormalZ=1 AngleXU=0 Radius=2.55
    g1: Circle CenterX=-43.3161 CenterY=155 CenterZ=0 NormalX=0 NormalY=0 NormalZ=1 AngleXU=0 Radius=2.55
    g2: Circle CenterX=63.3907 CenterY=55 CenterZ=0 NormalX=0 NormalY=0 NormalZ=1 AngleXU=0 Radius=2.55
    g3: Circle CenterX=-63.3907 CenterY=55 CenterZ=0 NormalX=0 NormalY=0 NormalZ=1 AngleXU=0 Radius=2.55
    g4: LineSegment [constr] StartX=45.8162 StartY=155.502 StartZ=0 EndX=57.5815 EndY=157.864 EndZ=0
    g5: LineSegment [constr] StartX=65.8909 StartY=55.5019 StartZ=0 EndX=77.6561 EndY=57.8637 EndZ=0
  constraints (18):
    c: Distance(g0,g-3) = 12
    c: Diameter(g0) = 5.1
    c: Equal(g1,g0)
    c: Symmetric(g1,g0,g-2)
    c: DistanceY(g0) = 155
    c: Symmetric(g2,g3,g-2)
    c: Equal(g2,g3)
    c: Equal(g3,g0)
    c: PointOnObject(g4,g0)
    c: PointOnObject(g4,g-3)
    c: PointOnObject(g5,g2)
    c: PointOnObject(g5,g-3)
    c: Perpendicular(g5,g-3)
    c: PointOnObject(g2,g5)
    c: Equal(g5,g4)
    c: PointOnObject(g0,g4)
    c: Perpendicular(g-3,g4)
    c: DistanceY(g2) = 55
FEATURE [PartDesign::Pocket] Pocket109
  BaseFeature = -> Pocket108
  Direction = (0,0,-1)
  Length = 5
  Length2 = 5
  Midplane = true
  Profile = -> Sketch175
  ReferenceAxis = -> Sketch175 [N_Axis]
  Suppressed = false
  Type = 1
FEATURE [PartDesign::Mirrored] Mirrored010
  BaseFeature = -> Pocket109
  MirrorPlane = -> YZ_Plane078
  Originals = -> [Pocket104,Fillet011]
  Suppressed = false
  TransformMode = 0
FEATURE [PartDesign::FeatureAdditivePython] PDW_Common_Add  # link proxy (typed FeaturePython)
  BaseFeature = -> Mirrored010
  Body = Body105
  ClaimChildren = false
  EditPlacementAdjustments = false
  Enabled = 0
  LinkedObject = -> Mirrored010
  MeshTolerance = 0.1
  PatternBase = -> Pocket109
  PatternBaseOffset = 0
  PatternBaseScale = 1
  PatternBaseScaleXYZ = (1,1,1)
  PatternOffsetCut = false
  PatternOffsetIntersection = false
  PatternOffsetJoin = 0
  PatternOffsetMode = 0
  PatternOffsetSelfIntersection = false
  PatternOperation = 3
  PatternOperationDefault = Common
  PatternScaleCut = false
  PatternShapeOffset = 0
  PatternShapeScale = 1
  PatternShapeScaleXYZ = (1,1,1)
  PatternTool = -> Mirrored010
  PatternToolOffset = 0
  PatternToolScale = 1
  PatternToolScaleXYZ = (1,1,1)
  RefineMesh = true
  ShapeManagement = 0
  ShowMeshProps = false
  ShowOffsetProps = false
  ShowScaleProps = false
  ShowWarnings = true
  Suppressed = false
  TipBase = -> Mirrored010
  TipBaseOffset = 0
  TipBaseScale = 1
  TipBaseScaleXYZ = (1,1,1)
  TipOffsetCut = false
  TipOffsetIntersection = false
  TipOffsetJoin = 0
  TipOffsetMode = 0
  TipOffsetSelfIntersection = false
  TipOperation = 4
  TipOperationDefault = Common
  TipScaleCut = false
  TipShapeOffset = 0
  TipShapeScale = 1
  TipShapeScaleXYZ = (1,1,1)
  TipTool = -> Mirrored010
  TipToolOffset = 0
  TipToolScale = 1
  TipToolScaleXYZ = (1,1,1)
  Type = Additive
  UsePatternBaseAddSubShape = false
  UsePatternToolAddSubShape = true
  UseTipBaseAddSubShape = false
  UseTipToolAddSubShape = true
  Version = 0.2023.08.13
FEATURE [PartDesign::PolarPattern] PolarPattern006
  Angle = 360
  Axis = -> Z_Axis078
  BaseFeature = -> PDW_Common_Add
  Mode = 0
  Occurrences = 3
  Offset = 120
  Originals = -> [PDW_Common_Add]
  Refine = true
  Suppressed = false
  TransformMode = 0
FEATURE [PartDesign::Pocket] Pocket107
  BaseFeature = -> PolarPattern006
  Direction = (0,0,-1)
  Length = 5
  Length2 = 5
  Midplane = true
  Profile = -> Binder118
  Suppressed = false
  Type = 1
FEATURE [Sketcher::SketchObject] Sketch176
  ArcFitTolerance = 0
  AttachmentSupport = -> [XY_Plane080]
  ExternalGeometry = -> [Sketch171]
  FullyConstrained = true
  MakeInternals = false
  MapMode = 5
  sketch-geometry (5):
    g0: LineSegment StartX=42.5 StartY=285 StartZ=0 EndX=42.5 EndY=362 EndZ=0
    g1: ArcOfCircle CenterX=27.5 CenterY=362 CenterZ=0 NormalX=0 NormalY=0 NormalZ=1 AngleXU=0 Radius=15 StartAngle=-8.4623e-11 EndAngle=1.5708
    g2: LineSegment StartX=0 StartY=285 StartZ=0 EndX=42.5 EndY=285 EndZ=0
    g3: LineSegment StartX=0 StartY=377 StartZ=0 EndX=27.5 EndY=377 EndZ=0
    g4: LineSegment StartX=0 StartY=285 StartZ=0 EndX=0 EndY=377 EndZ=0
  constraints (13):
    c: Coincident(g2,g0)
    c: Vertical(g0)
    c: Coincident(g2,g-3)
    c: Tangent(g0,g1) = -1.5708
    c: PointOnObject(g2,g-2)
    c: PointOnObject(g2,g-3)
    c: PointOnObject(g3,g-2)
    c: Horizontal(g3)
    c: Tangent(g3,g1) = 1.5708
    c: Coincident(g4,g2)
    c: Coincident(g4,g3)
    c: DistanceY(g4,g4) = 92
    c: Radius(g1) = 15
FEATURE [PartDesign::SubShapeBinder] Binder120
  BindCopyOnChange = 0
  BindMode = 0
  ClaimChildren = false
  Context = -> Body107 [Binder120.]
  Fuse = false
  MakeFace = true
  OffsetFill = false
  OffsetIntersection = false
  OffsetJoinType = 0
  OffsetOpenResult = false
  PartialLoad = false
  Relative = true
  Support = -> [Body007[Binder063.]]
  _Version = 2
FEATURE [PartDesign::Pocket] Pocket110
  BaseFeature = -> Mirrored011
  Direction = (0,0,-1)
  Length = 5
  Length2 = 5
  Profile = -> Binder120
  Suppressed = false
  Type = 1
FEATURE [PartDesign::SubShapeBinder] Binder121
  BindCopyOnChange = 0
  BindMode = 0
  ClaimChildren = false
  Context = -> Body107 [Binder121.]
  Fuse = false
  MakeFace = true
  OffsetFill = false
  OffsetIntersection = false
  OffsetJoinType = 0
  OffsetOpenResult = false
  PartialLoad = false
  Relative = true
  Support = -> [Body007[Pocket057.Sketch110.,Pocket058.Sketch111.]]
  _Version = 2
FEATURE [PartDesign::Pocket] Pocket111
  BaseFeature = -> Pocket110
  Direction = (0,0,-1)
  Length = 5
  Length2 = 5
  Midplane = true
  Profile = -> Binder121
  Suppressed = false
  Type = 1
FEATURE [PartDesign::Mirrored] Mirrored012
  BaseFeature = -> Pocket111
  MirrorPlane = -> YZ_Plane080
  Originals = -> [Pocket110]
  Suppressed = false
  TransformMode = 0
FEATURE [PartDesign::FeatureAdditivePython] PDW_Add  # link proxy (typed FeaturePython)
  BaseFeature = -> Mirrored012
  Body = Body107
  ClaimChildren = false
  EditPlacementAdjustments = false
  Enabled = 1
  LinkedObject = -> Mirrored011
  MeshTolerance = 0.1
  PatternBase = -> Mirrored012
  PatternBaseOffset = 0
  PatternBaseScale = 1
  PatternBaseScaleXYZ = (1,1,1)
  PatternOffsetCut = false
  PatternOffsetIntersection = false
  PatternOffsetJoin = 0
  PatternOffsetMode = 0
  PatternOffsetSelfIntersection = false
  PatternOperation = 0
  PatternOperationDefault = None
  PatternScaleCut = false
  PatternShapeOffset = 0
  PatternShapeScale = 1
  PatternShapeScaleXYZ = (1,1,1)
  PatternTool = -> Mirrored011
  PatternToolOffset = 0
  PatternToolScale = 1
  PatternToolScaleXYZ = (1,1,1)
  RefineMesh = true
  ShapeManagement = 0
  ShowMeshProps = false
  ShowOffsetProps = false
  ShowScaleProps = false
  ShowWarnings = true
  Suppressed = false
  TipBase = -> Mirrored012
  TipBaseOffset = 0
  TipBaseScale = 1
  TipBaseScaleXYZ = (1,1,1)
  TipOffsetCut = false
  TipOffsetIntersection = false
  TipOffsetJoin = 0
  TipOffsetMode = 0
  TipOffsetSelfIntersection = false
  TipOperation = 0
  TipOperationDefault = Fuse
  TipScaleCut = false
  TipShapeOffset = 0
  TipShapeScale = 1
  TipShapeScaleXYZ = (1,1,1)
  TipTool = -> Mirrored011
  TipToolOffset = 0
  TipToolScale = 1
  TipToolScaleXYZ = (1,1,1)
  Type = Additive
  UsePatternBaseAddSubShape = false
  UsePatternToolAddSubShape = true
  UseTipBaseAddSubShape = false
  UseTipToolAddSubShape = true
  Version = 0.2023.08.13
FEATURE [PartDesign::FeatureAdditivePython] PDW_Common_Add001  # link proxy (typed FeaturePython)
  BaseFeature = -> PDW_Add
  Body = Body107
  ClaimChildren = false
  EditPlacementAdjustments = false
  Enabled = 1
  LinkedObject = -> Mirrored012
  MeshTolerance = 0.1
  PatternBase = -> PDW_Add
  PatternBaseOffset = 0
  PatternBaseScale = 1
  PatternBaseScaleXYZ = (1,1,1)
  PatternOffsetCut = false
  PatternOffsetIntersection = false
  PatternOffsetJoin = 0
  PatternOffsetMode = 0
  PatternOffsetSelfIntersection = false
  PatternOperation = 3
  PatternOperationDefault = Common
  PatternScaleCut = false
  PatternShapeOffset = 0
  PatternShapeScale = 1
  PatternShapeScaleXYZ = (1,1,1)
  PatternTool = -> Mirrored012
  PatternToolOffset = 0
  PatternToolScale = 1
  PatternToolScaleXYZ = (1,1,1)
  RefineMesh = true
  ShapeManagement = 0
  ShowMeshProps = false
  ShowOffsetProps = false
  ShowScaleProps = false
  ShowWarnings = true
  Suppressed = false
  TipBase = -> PDW_Add
  TipBaseOffset = 0
  TipBaseScale = 1
  TipBaseScaleXYZ = (1,1,1)
  TipOffsetCut = false
  TipOffsetIntersection = false
  TipOffsetJoin = 0
  TipOffsetMode = 0
  TipOffsetSelfIntersection = false
  TipOperation = 2
  TipOperationDefault = Common
  TipScaleCut = false
  TipShapeOffset = 0
  TipShapeScale = 1
  TipShapeScaleXYZ = (1,1,1)
  TipTool = -> Mirrored012
  TipToolOffset = 0
  TipToolScale = 1
  TipToolScaleXYZ = (1,1,1)
  Type = Additive
  UsePatternBaseAddSubShape = false
  UsePatternToolAddSubShape = true
  UseTipBaseAddSubShape = false
  UseTipToolAddSubShape = true
  Version = 0.2023.08.13
FEATURE [PartDesign::PolarPattern] PolarPattern007
  Angle = 360
  Axis = -> Z_Axis080
  BaseFeature = -> PDW_Common_Add001
  Mode = 0
  Occurrences = 3
  Offset = 120
  Originals = -> [PDW_Common_Add001]
  Refine = true
  Suppressed = false
  TransformMode = 0
FEATURE [PartDesign::Pocket] Pocket106
  BaseFeature = -> PolarPattern007
  Direction = (0,0,-1)
  Length = 5
  Length2 = 5
  Midplane = true
  Profile = -> Binder117
  Suppressed = false
  Type = 1
FEATURE [Spreadsheet::Sheet] Spreadsheet002  label="material_stainlessSteel"
  cells = A1='Radius / Thickness ; B1='K-factor (ANSI); A2=1; B2=0.38; A3=3; B3=0.43; A4=99; B4=0.5
FEATURE [App::DocumentObjectGroup] Group001  label="tables"
  Group = -> [Spreadsheet,Spreadsheet002]
FEATURE [PartDesign::Body] Body109  label="dummy_body"
  AllowCompound = false
  Origin = -> Origin082
FEATURE [Sketcher::SketchObject] Sketch178
  ArcFitTolerance = 0
  AttachmentSupport = -> [XY_Plane011]
  FullyConstrained = true
  MakeInternals = false
  MapMode = 5
  sketch-geometry (4):
    g0: Circle CenterX=29 CenterY=-145.633 CenterZ=0 NormalX=0 NormalY=0 NormalZ=1 AngleXU=0 Radius=4.25
    g1: LineSegment [constr] StartX=0 StartY=0 StartZ=0 EndX=84.8108 EndY=-48.9655 EndZ=0
    g2: Circle CenterX=140.622 CenterY=47.7016 CenterZ=0 NormalX=0 NormalY=0 NormalZ=1 AngleXU=0 Radius=4.25
    g3: LineSegment [constr] StartX=140.622 StartY=47.7016 StartZ=0 EndX=29 EndY=-145.633 EndZ=0
  constraints (10):
    c: Diameter(g0) = 8.5
    c: DistanceX(g0) = 29
    c: DistanceY(g0) = -145.633
    c: Coincident(g1,g-1)
    c: Angle(g1) = -0.523599
    c: Symmetric(g2,g0,g1)
    c: Equal(g2,g0)
    c: Coincident(g3,g2)
    c: Coincident(g3,g0)
    c: PointOnObject(g1,g3)
FEATURE [Part::Extrusion] Extrude016  label="Populate droppers placements with dropper_base_extrude"
  Base = -> Populate006
  Dir = (0,0,1)
  DirMode = 2
  FaceMakerClass = Part::FaceMakerBullseye
  FaceMakerMode = 3
  LengthFwd = 10
  LengthRev = 0
  Placement = pos=(0,181.372,0) rot=(0,0,1;0rad)
  Solid = false
  Symmetric = false
  expr: .Placement.Base.y = <<Properties>>.plane_middle
FEATURE [App::Link] Link010  label="top_top001"
  LinkedObject = -> Body110
  expr: LinkedObject = <<dropper_fix_top>>._self
FEATURE [App::Link] Link011  label="top_bottom001"
  LinkedObject = -> Body004
FEATURE [App::Link] Link012  label="cap_outer_material_0.30ansi001"
  LinkedObject = -> Body002
FEATURE [App::Link] Link013  label="cap_inner2_material_0.30ansi001"
  LinkedObject = -> Body016
FEATURE [App::Link] Link014  label="top_connector_material_0.30ansi001"
  LinkedObject = -> Body017
FEATURE [App::Link] Link015  label="cap_inner1_material_0.30ansi001"
  LinkedObject = -> Body003
FEATURE [App::Link] Link016  label="part1_material_0.30ansi001"
  LinkedObject = -> Body
FEATURE [App::Link] Link017  label="part2_material_0.30ansi001"
  LinkedObject = -> Body001
FEATURE [App::Link] Link018  label="bot_hor_amplifier_material_0.30ansi001"
  LinkedObject = -> Body068
FEATURE [App::Link] Link019  label="star_material_0.30ansi001"
  LinkedObject = -> Body018
FEATURE [App::Link] Link020  label="plexiglass_outer_material_0.30ansi001"
  LinkedObject = -> Body072
FEATURE [App::Link] Link021  label="pillar_bottom_material_0.30ansi001"
  LinkedObject = -> Body011
FEATURE [App::Link] Link022  label="pillar_material_0.30ansi001"
  LinkedObject = -> Body010
FEATURE [App::Link] Link023  label="pillar_top_element_material_0.30ansi001"
  LinkedObject = -> Body012
FEATURE [App::Link] Link025  label="top_dec_corner_material_0.30ansi001"
  LinkedObject = -> Body014
FEATURE [App::Link] Link026  label="dec_corner_material_0.30ansi001"
  LinkedObject = -> Body013
FEATURE [App::Link] Link027  label="basement_amplifier_material_0.30ansi002"
  LinkedObject = -> Body105
FEATURE [App::Link] Link028  label="basement_proxy001"
  LinkedObject = -> Body008
FEATURE [App::Link] Link029  label="basement_plywood001"
  LinkedObject = -> Body006
FEATURE [App::Link] Link030  label="basement2_amplifier_material_stainlessSteel001"
  LinkedObject = -> Body107
FEATURE [App::Link] Link031  label="basement2_plywood001"
  LinkedObject = -> Body007
FEATURE [App::Link] Link032  label="basement2_proxy001"
  LinkedObject = -> Body009
FEATURE [App::Link] Link033  label="sink_material_0.30ansi001"
  LinkedObject = -> Body020
FEATURE [App::Link] Link034  label="Body110"
  LinkedObject = -> Body021
FEATURE [App::Link] Link035  label="hat003"
  LinkedObject = -> Body076
FEATURE [App::Link] Link036  label="hat004"
  LinkedObject = -> Body075
FEATURE [App::Link] Link037  label="hat_plexiglass_material_0.30ansi001"
  LinkedObject = -> Body078
FEATURE [Part::Extrusion] Extrude017  label="populate dropper_fix_extrude"
  Base = -> Populate004
  Dir = (0,0,1)
  DirMode = 2
  FaceMakerClass = Part::FaceMakerBullseye
  FaceMakerMode = 3
  LengthFwd = 10
  LengthRev = 0
  Placement = pos=(0,181.372,1.5) rot=(0,0,1;0rad)
  Solid = false
  Symmetric = false
  expr: .Placement.Base.y = <<Properties>>.plane_middle
FEATURE [Part::Compound] Compound048  label="top_bottom_cut1"
  Links = -> [Extrude016,Extrude017]
FEATURE [Part::Extrusion] Extrude018  label="Populate droppers placements with dropper_feed_extrude"
  Base = -> Populate005
  Dir = (0,0,1)
  DirMode = 2
  FaceMakerClass = Part::FaceMakerBullseye
  FaceMakerMode = 3
  LengthFwd = 10
  LengthRev = 0
  Placement = pos=(0,181.372,0) rot=(0,0,1;0rad)
  Solid = false
  Symmetric = false
  expr: .Placement.Base.y = <<Properties>>.plane_middle
FEATURE [Part::Compound] Compound049  label="top_top_cut1"
  Links = -> [Extrude017,Extrude018]
FEATURE [Part::FeaturePython] Connect  label="top_bottom_cut1_refined"  # WARN: FeaturePython — macro-defined, semantics opaque (R4)
  Objects = -> [Compound048]
  Refine = true
  Tolerance = 0
FEATURE [Part::FeaturePython] Connect001  label="top_top_cut1_refined"  # WARN: FeaturePython — macro-defined, semantics opaque (R4)
  Objects = -> [Compound049]
  Refine = true
  Tolerance = 0
FEATURE [PartDesign::FeatureBase] BaseFeature
  BaseFeature = -> Hole003
  Suppressed = false
  expr: BaseFeature = <<Hole003>>._self
FEATURE [PartDesign::FeatureSubtractivePython] PDW_Sub  # link proxy (typed FeaturePython)
  BaseFeature = -> BaseFeature
  Body = Body110
  ClaimChildren = true
  EditPlacementAdjustments = false
  Enabled = 1
  LinkedObject = -> Connect001
  MeshTolerance = 0.1
  PatternBase = -> Connect001
  PatternBaseOffset = 0
  PatternBaseScale = 1
  PatternBaseScaleXYZ = (1,1,1)
  PatternOffsetCut = false
  PatternOffsetIntersection = false
  PatternOffsetJoin = 0
  PatternOffsetMode = 0
  PatternOffsetSelfIntersection = false
  PatternOperation = 0
  PatternOperationDefault = None
  PatternScaleCut = false
  PatternShapeOffset = 0
  PatternShapeScale = 1
  PatternShapeScaleXYZ = (1,1,1)
  PatternToolOffset = 0
  PatternToolScale = 1
  PatternToolScaleXYZ = (1,1,1)
  RefineMesh = true
  ShapeManagement = 0
  ShowMeshProps = false
  ShowOffsetProps = false
  ShowScaleProps = false
  ShowWarnings = true
  Suppressed = false
  TipBase = -> BaseFeature
  TipBaseOffset = 0
  TipBaseScale = 1
  TipBaseScaleXYZ = (1,1,1)
  TipOffsetCut = false
  TipOffsetIntersection = false
  TipOffsetJoin = 0
  TipOffsetMode = 0
  TipOffsetSelfIntersection = false
  TipOperation = 1
  TipOperationDefault = Cut
  TipScaleCut = false
  TipShapeOffset = 0
  TipShapeScale = 1
  TipShapeScaleXYZ = (1,1,1)
  TipTool = -> Connect001
  TipToolOffset = 0
  TipToolScale = 1
  TipToolScaleXYZ = (1,1,1)
  Type = Subtractive
  UsePatternBaseAddSubShape = false
  UsePatternToolAddSubShape = false
  UseTipBaseAddSubShape = false
  UseTipToolAddSubShape = false
  Version = 0.2023.08.13
FEATURE [Part::Extrusion] Extrude019  label="hole_3.4mm_extrude"
  Base = -> Circle
  Dir = (0,0,1)
  DirMode = 2
  FaceMakerClass = Part::FaceMakerBullseye
  FaceMakerMode = 3
  LengthFwd = 10
  LengthRev = 10
  Solid = true
  Symmetric = false
FEATURE [Part::FeaturePython] LinearArray014  label="pillar_bottom_hor_fix_holes"  # WARN: FeaturePython — macro-defined, semantics opaque (R4)
  Alignment = 0
  CellStart = A1
  Count = 2
  Dir = (1,0,0)
  DirIsDriven = true
  DistributionLaw = 0
  DrivenProperty = 1
  EndInclusive = true
  ExposePlacement = false
  GeneratorMode = 0
  MarkerShape = 1
  MarkerSize = 0
  NumElements = 2
  OrientMode = 1
  Placement = pos=(-40,-12,0) rot=(0,0,1;0rad)
  Point = (0,0,0)
  PointIsDriven = true
  Reverse = false
  SpanEnd = 80
  SpanStart = 0
  Step = 80
  Type = lattice2LinearArray.LinearArray
  VSGVersion = 1
  Values = 0.0 | 80.0
  ValuesSource = 2
  isLattice = 1
  expr: .Placement.Base.x = -SpanEnd / 2
FEATURE [Part::Part2DObjectPython] Circle002  label="hole_5.5mm"  # Draft 2D object (typed FeaturePython)
  Area = 0
  FirstAngle = 0
  LastAngle = 0
  MakeFace = false
  Placement = pos=(0,0,0) rot=(0,0,1;1e-06rad)
  Radius = 2.75
FEATURE [Part::Extrusion] Extrude021  label="hole_5.5mm_extrude"
  Base = -> Circle002
  Dir = (2.1e-14,-2.56e-13,1)
  DirMode = 2
  FaceMakerClass = Part::FaceMakerBullseye
  FaceMakerMode = 3
  LengthFwd = 30
  LengthRev = 0
  Solid = true
  Symmetric = false
FEATURE [Part::FeaturePython] Populate024  label="Populate pillar_bottom_hor_fix_holes with hole_5.5mm_extrude"  # WARN: FeaturePython — macro-defined, semantics opaque (R4)
  Copying = 0
  ExposePlacement = false
  MarkerShape = 1
  MarkerSize = 0
  NumElements = 0
  Object = -> Extrude021
  OutputCompounding = 1
  PlacementsTo = -> LinearArray014
  Referencing = 0
  Type = lattice2PopulateCopies.LatticePopulateCopies
  isLattice = 0
FEATURE [Part::FeaturePython] Mirror006  label="pillar_bottom_mirror_hor_fix_holes"  # WARN: FeaturePython — macro-defined, semantics opaque (R4)
  ExposePlacement = false
  FlipX = false
  FlipY = true
  FlipZ = false
  MarkerShape = 1
  MarkerSize = 0
  NumElements = 2
  Object = -> LinearArray014
  ObjectTraversal = 0
  Type = lattice2Mirror.LatticeMirror
  isLattice = 1
FEATURE [Part::FeaturePython] Placment017  # WARN: FeaturePython — macro-defined, semantics opaque (R4)
  AttacherType = Attacher::AttachEngine3D
  ExposePlacement = true
  MarkerShape = 1
  MarkerSize = 20
  NumElements = 1
  Placement = pos=(-18.3,329.5,0) rot=(0,0,1;4.71239rad)
  Type = lattice2AttachablePlacement.AttachablePlacement
  isLattice = 1
  expr: Placement = <<pillar_placement>>.AttachmentOffset * <<pillar_bottom_placement>>.AttachmentOffset
FEATURE [Part::FeaturePython] Placment018  label="basement2_placement"  # WARN: FeaturePython — macro-defined, semantics opaque (R4)
  AttacherType = Attacher::AttachEngine3D
  AttachmentOffset = pos=(0,0,-88) rot=(0,0,1;0rad)
  ExposePlacement = true
  MarkerShape = 1
  MarkerSize = 20
  NumElements = 1
  Type = lattice2AttachablePlacement.AttachablePlacement
  isLattice = 1
FEATURE [Part::FeaturePython] Placment  label="pillar_placement"  # WARN: FeaturePython — macro-defined, semantics opaque (R4)
  AttacherType = Attacher::AttachEngine3D
  AttachmentOffset = pos=(0,384,0) rot=(0,0,1;3.14159rad)
  AttachmentSupport = -> [Placment018]
  ExposePlacement = true
  MapMode = 2
  MarkerShape = 1
  MarkerSize = 10
  NumElements = 1
  Placement = pos=(0,384,0) rot=(0,0,1;3.14159rad)
  Type = lattice2AttachablePlacement.AttachablePlacement
  isLattice = 1
FEATURE [Part::FeaturePython] Placment001  label="pillar_top_part_placement"  # WARN: FeaturePython — macro-defined, semantics opaque (R4)
  AttacherType = Attacher::AttachEngine3D
  AttachmentSupport = -> [Placment]
  ExposePlacement = true
  MapMode = 2
  MarkerShape = 1
  MarkerSize = 10
  NumElements = 1
  Placement = pos=(0,384,0) rot=(0,0,1;3.14159rad)
  Type = lattice2AttachablePlacement.AttachablePlacement
  isLattice = 1
FEATURE [Part::FeaturePython] Placment003  label="pillar_bottom_placement"  # WARN: FeaturePython — macro-defined, semantics opaque (R4)
  AttacherType = Attacher::AttachEngine3D
  AttachmentOffset = pos=(18.3,54.5,0) rot=(0,0,1;1.5708rad)
  AttachmentSupport = -> [Placment]
  ExposePlacement = true
  MapMode = 2
  MarkerShape = 1
  MarkerSize = 50
  NumElements = 1
  Placement = pos=(-18.3,329.5,0) rot=(0,0,1;4.71239rad)
  Type = lattice2AttachablePlacement.AttachablePlacement
  isLattice = 1
FEATURE [Part::FeaturePython] Mirror007  label="Mirror007 of Placment017"  # WARN: FeaturePython — macro-defined, semantics opaque (R4)
  ExposePlacement = false
  FlipX = true
  FlipY = false
  FlipZ = false
  MarkerShape = 1
  MarkerSize = 10
  NumElements = 1
  Object = -> Placment017
  ObjectTraversal = 0
  Type = lattice2Mirror.LatticeMirror
  isLattice = 1
FEATURE [Part::FeaturePython] Populate025  label="Populate Mirror007 of Placment017 with pillar_bottom_mirror_hor_fix_holes"  # WARN: FeaturePython — macro-defined, semantics opaque (R4)
  Copying = 0
  ExposePlacement = false
  MarkerShape = 1
  MarkerSize = 0
  NumElements = 2
  Object = -> Mirror006
  OutputCompounding = 0
  PlacementsTo = -> Mirror007
  Referencing = 0
  Type = lattice2PopulateCopies.LatticePopulateCopies
  isLattice = 1
FEATURE [Part::FeaturePython] Populate026  label="Populate Placment017 with pillar_bottom_hor_fix_holes"  # WARN: FeaturePython — macro-defined, semantics opaque (R4)
  Copying = 0
  ExposePlacement = false
  MarkerShape = 1
  MarkerSize = 0
  NumElements = 2
  Object = -> LinearArray014
  OutputCompounding = 0
  PlacementsTo = -> Placment017
  Referencing = 0
  Type = lattice2PopulateCopies.LatticePopulateCopies
  isLattice = 1
FEATURE [Part::FeaturePython] Join004  # WARN: FeaturePython — macro-defined, semantics opaque (R4)
  ExposePlacement = false
  Interleave = false
  Links = -> [Populate025,Populate026]
  MarkerShape = 1
  MarkerSize = 0
  NumElements = 4
  Type = lattice2JoinArrays.JoinArrays
  isLattice = 1
FEATURE [Part::FeaturePython] PolarArray002  # WARN: FeaturePython — macro-defined, semantics opaque (R4)
  Alignment = 0
  AttacherType = Attacher::AttachEngine3D
  CellStart = A1
  Count = 3
  DistributionLaw = 0
  EndInclusive = false
  ExposePlacement = false
  FlipX = false
  FlipZ = false
  GeneratorMode = 0
  MarkerShape = 1
  MarkerSize = 0
  NumElements = 3
  OrientMode = 2
  Radius = 25
  Reverse = false
  SpanEnd = 360
  SpanStart = 0
  Step = 120
  Type = lattice2PolarArray2.PolarArray
  UseArcRadius = false
  UseArcRange = 0
  VSGVersion = 1
  Values = 0.0 | 120.0 | 240.0
  ValuesSource = 2
  isLattice = 1
FEATURE [Part::FeaturePython] Populate027  label="Populate PolarArray002 with Join004"  # WARN: FeaturePython — macro-defined, semantics opaque (R4)
  Copying = 0
  ExposePlacement = false
  MarkerShape = 1
  MarkerSize = 0
  NumElements = 12
  Object = -> Join004
  OutputCompounding = 0
  PlacementsTo = -> PolarArray002
  Referencing = 1
  Type = lattice2PopulateCopies.LatticePopulateCopies
  isLattice = 1
FEATURE [Part::FeaturePython] Populate028  label="Populate Populate PolarArray002 with Join004 with hole_5.5mm_extrude"  # WARN: FeaturePython — macro-defined, semantics opaque (R4)
  Copying = 0
  ExposePlacement = false
  MarkerShape = 1
  MarkerSize = 0
  NumElements = 0
  Object = -> Extrude021
  OutputCompounding = 1
  PlacementsTo = -> Populate027
  Referencing = 0
  Type = lattice2PopulateCopies.LatticePopulateCopies
  isLattice = 0
FEATURE [Sketcher::SketchObject] Sketch180
  ArcFitTolerance = 0
  AttachmentSupport = -> [YZ_Plane085]
  FullyConstrained = true
  MakeInternals = false
  MapMode = 5
  Placement = pos=(0,0,0) rot=(0.57735,0.57735,0.57735;2.0944rad)
  sketch-geometry (4):
    g0: ArcOfCircle CenterX=-4 CenterY=4 CenterZ=0 NormalX=0 NormalY=0 NormalZ=1 AngleXU=0 Radius=4 StartAngle=4.71239 EndAngle=6.28319
    g1: ArcOfCircle CenterX=-4 CenterY=4 CenterZ=0 NormalX=0 NormalY=0 NormalZ=1 AngleXU=0 Radius=2 StartAngle=4.71239 EndAngle=6.28319
    g2: LineSegment StartX=-4 StartY=0 StartZ=0 EndX=-4 EndY=2 EndZ=0
    g3: LineSegment StartX=-2 StartY=4 StartZ=0 EndX=0 EndY=4 EndZ=0
  constraints (13):
    c: PointOnObject(g0,g-1)
    c: PointOnObject(g0,g-2)
    c: Coincident(g1,g0)
    c: Coincident(g2,g0)
    c: Coincident(g2,g1)
    c: Coincident(g3,g1)
    c: Coincident(g3,g0)
    c: Perpendicular(g1,g3)
    c: Perpendicular(g1,g2)
    c: Vertical(g2)
    c: Horizontal(g3)
    c: Radius(g1) = 2  'r'
    c: Distance(g2) = 2  'thickness'
FEATURE [PartDesign::Pad] Pad020
  Direction = (1,0,0)
  Length = 101
  Length2 = 10
  Midplane = true
  Placement = pos=(0,0,0) rot=(1,1,1;2.0944rad)
  Profile = -> Sketch180
  ReferenceAxis = -> Sketch180 [N_Axis]
  Suppressed = false
  Type = 0
FEATURE [Sketcher::SketchObject] Sketch181
  ArcFitTolerance = 0
  AttachmentSupport = -> [XY_Plane085]
  FullyConstrained = true
  MakeInternals = false
  MapMode = 5
  expr: Constraints[2] = Pad020.Length
  sketch-geometry (4):
    g0: LineSegment StartX=-50.5 StartY=-4 StartZ=0 EndX=50.5 EndY=-4 EndZ=0
    g1: LineSegment StartX=29.5 StartY=-25 StartZ=0 EndX=-29.5 EndY=-25 EndZ=0
    g2: ArcOfCircle CenterX=29.5 CenterY=-4 CenterZ=0 NormalX=0 NormalY=0 NormalZ=1 AngleXU=0 Radius=21 StartAngle=4.71239 EndAngle=6.28319
    g3: ArcOfCircle CenterX=-29.5 CenterY=-4 CenterZ=0 NormalX=0 NormalY=0 NormalZ=1 AngleXU=0 Radius=21 StartAngle=3.14159 EndAngle=4.71239
  constraints (11):
    c: Horizontal(g1)
    c: DistanceY(g0) = -4
    c: DistanceX(g0,g0) = 101
    c: DistanceY(g1,g-1) = 25
    c: PointOnObject(g2,g0)
    c: Coincident(g2,g0)
    c: PointOnObject(g3,g0)
    c: Coincident(g3,g0)
    c: Tangent(g3,g1) = 1.5708
    c: Tangent(g2,g1) = 1.5708
    c: Symmetric(g0,g0,g-2)
FEATURE [Sketcher::SketchObject] Sketch182
  ArcFitTolerance = 0
  AttachmentSupport = -> [XZ_Plane085]
  FullyConstrained = true
  MakeInternals = false
  MapMode = 5
  Placement = pos=(0,0,0) rot=(1,0,0;1.5708rad)
  expr: Constraints[17] = <<pillar2_base_sketch>>.Constraints.length + 3 mm
  expr: Constraints[8] = Pad020.Length
  sketch-geometry (13):
    g0: LineSegment StartX=-50.5 StartY=4 StartZ=0 EndX=-50.5 EndY=110 EndZ=0
    g1: LineSegment StartX=-35.5 StartY=110 StartZ=0 EndX=-35.5 EndY=66.1722 EndZ=0
    g2: LineSegment StartX=-18.1011 StartY=38.947 StartZ=0 EndX=47.6002 EndY=8.53754 EndZ=0
    g3: ArcOfCircle CenterX=45.5 CenterY=4 CenterZ=0 NormalX=0 NormalY=0 NormalZ=1 AngleXU=0 Radius=5 StartAngle=2.92426e-11 EndAngle=1.13731
    g4: ArcOfCircle CenterX=-5.5 CenterY=66.1722 CenterZ=0 NormalX=0 NormalY=0 NormalZ=1 AngleXU=0 Radius=30 StartAngle=3.14159 EndAngle=4.27891
    g5: GeomPoint [constr] X=-35.5 Y=47 Z=0
    g6: GeomPoint [constr] X=-35.5 Y=110 Z=0
    g7: GeomPoint [constr] X=-52.5 Y=110 Z=0
    g8: LineSegment StartX=50.5 StartY=4 StartZ=0 EndX=-48.5 EndY=4 EndZ=0
    g9: LineSegment StartX=-48.5 StartY=4 StartZ=0 EndX=-50.5 EndY=4 EndZ=0
    g10: LineSegment StartX=-50.5 StartY=110 StartZ=0 EndX=-48.5 EndY=110 EndZ=0
    g11: LineSegment StartX=-48.5 StartY=110 StartZ=0 EndX=-35.5 EndY=110 EndZ=0
    g12: LineSegment [constr] StartX=-48.5 StartY=4 StartZ=0 EndX=-48.5 EndY=110 EndZ=0
  constraints (32):
    c: Vertical(g0)
    c: Coincident(g0,g10)
    c: Vertical(g1)
    c: Coincident(g9,g0)
    c: Coincident(g3,g8)
    c: Tangent(g3,g2) = 1.5708
    c: DistanceY(g8) = 4
    c: Symmetric(g0,g8,g-2)
    c: DistanceX(g9,g8) = 101
    c: DistanceY(g0) = 110  'total_height'
    c: PointOnObject(g5,g1)
    c: PointOnObject(g5,g2)
    c: Tangent(g1,g4) = -1.5708
    c: Tangent(g2,g4) = -1.5708
    c: Radius(g4) = 30
    c: Radius(g3) = 5
    c: DistanceX(g7,g0) = 2
    c: DistanceX(g7,g6) = 17
    c: Coincident(g8,g9)
    c: PointOnObject(g3,g8)
    c: Coincident(g10,g11)
    c: Horizontal(g10)
    c: Horizontal(g11)
    c: PointOnObject(g7,g10)
    c: Coincident(g12,g8)
    c: Coincident(g12,g11)
    c: Vertical(g12)
    c: DistanceX(g0,g11) = 2
    c: Horizontal(g9)
    c: DistanceY(g5) = 47
    c: Coincident(g1,g11)
    c: Coincident(g1,g6)
FEATURE [PartDesign::Pad] Pad021
  BaseFeature = -> Pad020
  Direction = (0,0,1)
  Length = 2
  Length2 = 10
  Placement = pos=(0,0,0) rot=(1,1,1;2.0944rad)
  Profile = -> Sketch181
  ReferenceAxis = -> Sketch181 [N_Axis]
  Suppressed = false
  Type = 0
FEATURE [PartDesign::Pad] Pad022
  BaseFeature = -> Pad021
  Direction = (0,-1,2e-16)
  Length = 2
  Length2 = 10
  Placement = pos=(0,0,0) rot=(1,1,1;2.0944rad)
  Profile = -> Sketch182
  ReferenceAxis = -> Sketch182 [N_Axis]
  Suppressed = false
  Type = 0
FEATURE [Sketcher::SketchObject] Sketch183
  ArcFitTolerance = 0
  AttachmentOffset = pos=(-52.5,2,0) rot=(0,0,1;0rad)
  AttachmentSupport = -> [XY_Plane085]
  FullyConstrained = true
  MakeInternals = false
  MapMode = 5
  Placement = pos=(-52.5,2,0) rot=(0,0,1;0rad)
  expr: .AttachmentOffset.Base.x = -Pad020.Length / 2 - 2 mm
  expr: Constraints[16] = <<pillar2_base_sketch>>.Constraints.width / 2 - 1 mm
  sketch-geometry (9):
    g0: ArcOfCircle CenterX=-5.92e-14 CenterY=4.503e-13 CenterZ=0 NormalX=0 NormalY=0 NormalZ=1 AngleXU=0 Radius=2 StartAngle=3.14159 EndAngle=4.71239
    g1: ArcOfCircle CenterX=-5.92e-14 CenterY=4.503e-13 CenterZ=0 NormalX=0 NormalY=0 NormalZ=1 AngleXU=0 Radius=4 StartAngle=3.14159 EndAngle=4.71239
    g2: LineSegment StartX=-2 StartY=-4.474e-13 StartZ=0 EndX=-2 EndY=15.3 EndZ=0
    g3: LineSegment StartX=-2 StartY=15.3 StartZ=0 EndX=-4 EndY=15.3 EndZ=0
    g4: LineSegment StartX=-4 StartY=15.3 StartZ=0 EndX=-4 EndY=0 EndZ=0
    g5: LineSegment [constr] StartX=5e-16 StartY=-4 StartZ=0 EndX=8e-16 EndY=-2 EndZ=0
    g6: LineSegment StartX=5e-16 StartY=-4 StartZ=0 EndX=2 EndY=-4 EndZ=0
    g7: LineSegment StartX=2 StartY=-4 StartZ=0 EndX=2 EndY=-2 EndZ=0
    g8: LineSegment StartX=2 StartY=-2 StartZ=0 EndX=9e-16 EndY=-2 EndZ=0
  constraints (25):
    c: Coincident(g0,g-1)
    c: PointOnObject(g0,g-2)
    c: PointOnObject(g0,g-1)
    c: Coincident(g1,g0)
    c: PointOnObject(g1,g-2)
    c: PointOnObject(g1,g-1)
    c: Tangent(g0,g2) = 1.5708
    c: Coincident(g2,g3)
    c: Horizontal(g3)
    c: Coincident(g3,g4)
    c: Coincident(g4,g1)
    c: Vertical(g4)
    c: Coincident(g5,g1)
    c: Coincident(g5,g0)
    c: Radius(g0) = 2
    c: DistanceY(g5,g5) = 2
    c: DistanceY(g0,g2) = 17.3
    c: Coincident(g6,g7)
    c: Coincident(g7,g8)
    c: Horizontal(g6)
    c: Horizontal(g8)
    c: Vertical(g7)
    c: Coincident(g6,g1)
    c: Coincident(g0,g8)
    c: DistanceX(g6,g6) = 2
FEATURE [Sketcher::SketchObject] Sketch184
  ArcFitTolerance = 0
  AttachmentSupport = -> [YZ_Plane085]
  ExternalGeometry = -> [Sketch183]
  FullyConstrained = true
  MakeInternals = false
  MapMode = 5
  Placement = pos=(0,0,0) rot=(0.57735,0.57735,0.57735;2.0944rad)
  expr: Constraints[12] = Sketch182.Constraints.total_height
  sketch-geometry (9):
    g0: ArcOfCircle CenterX=15.3 CenterY=2 CenterZ=0 NormalX=0 NormalY=0 NormalZ=1 AngleXU=0 Radius=2 StartAngle=4.71239 EndAngle=6.28319
    g1: LineSegment StartX=17.3 StartY=2 StartZ=0 EndX=17.3 EndY=1.47e-14 EndZ=0
    g2: LineSegment StartX=17.3 StartY=1.47e-14 StartZ=0 EndX=15.3 EndY=1.95e-14 EndZ=0
    g3: LineSegment StartX=17.3 StartY=108 StartZ=0 EndX=17.3 EndY=110 EndZ=0
    g4: LineSegment StartX=17.3 StartY=110 StartZ=0 EndX=15.3 EndY=110 EndZ=0
    g5: ArcOfCircle CenterX=15.3 CenterY=108 CenterZ=0 NormalX=0 NormalY=0 NormalZ=1 AngleXU=0 Radius=2 StartAngle=-5.3e-15 EndAngle=1.5708
    g6: ArcOfCircle CenterX=4 CenterY=2 CenterZ=0 NormalX=0 NormalY=0 NormalZ=1 AngleXU=0 Radius=2 StartAngle=3.14159 EndAngle=4.71239
    g7: LineSegment StartX=2 StartY=2 StartZ=0 EndX=2 EndY=1.11e-14 EndZ=0
    g8: LineSegment StartX=2 StartY=1.11e-14 StartZ=0 EndX=4 EndY=3.55e-14 EndZ=0
  constraints (22):
    c: Coincident(g1,g2)
    c: Vertical(g3)
    c: Coincident(g3,g4)
    c: Horizontal(g4)
    c: Tangent(g5,g4) = -1.5708
    c: Tangent(g5,g3) = -1.5708
    c: Vertical(g1)
    c: Tangent(g0,g1) = 1.5708
    c: Tangent(g2,g0) = 1.5708
    c: Vertical(g3,g1)
    c: Equal(g5,g0)
    c: Radius(g5) = 2
    c: DistanceY(g3) = 110
    c: Coincident(g7,g8)
    c: Vertical(g7)
    c: Tangent(g6,g7) = -1.5708
    c: Tangent(g8,g6) = -1.5708
    c: Equal(g6,g0)
    c: Coincident(g1,g-3)
    c: Coincident(g7,g-3)
    c: PointOnObject(g6,g-3)
    c: PointOnObject(g0,g-1)
FEATURE [Sketcher::SketchObject] Sketch185
  ArcFitTolerance = 0
  AttachmentOffset = pos=(-52.5,2,0) rot=(0,0,1;0rad)
  AttachmentSupport = -> [XY_Plane085]
  FullyConstrained = true
  MakeInternals = false
  MapMode = 5
  Placement = pos=(-52.5,2,0) rot=(0,0,1;0rad)
  expr: AttachmentOffset = <<Sketch183>>.AttachmentOffset
  sketch-geometry (6):
    g0: ArcOfCircle CenterX=-1.4879e-12 CenterY=3.7497e-12 CenterZ=0 NormalX=0 NormalY=0 NormalZ=1 AngleXU=0 Radius=4 StartAngle=3.14159 EndAngle=4.71239
    g1: ArcOfCircle CenterX=-1.4879e-12 CenterY=3.7497e-12 CenterZ=0 NormalX=0 NormalY=0 NormalZ=1 AngleXU=0 Radius=2 StartAngle=3.14159 EndAngle=4.71239
    g2: LineSegment StartX=-4 StartY=-4.94e-14 StartZ=0 EndX=-2 EndY=-2.158e-13 EndZ=0
    g3: LineSegment StartX=1.1155e-12 StartY=-4 StartZ=0 EndX=2 EndY=-4 EndZ=0
    g4: LineSegment StartX=2 StartY=-4 StartZ=0 EndX=2 EndY=-2 EndZ=0
    g5: LineSegment StartX=2 StartY=-2 StartZ=0 EndX=1.583e-13 EndY=-2 EndZ=0
  constraints (17):
    c: Coincident(g0,g-1)
    c: PointOnObject(g0,g-2)
    c: PointOnObject(g0,g-1)
    c: Coincident(g1,g0)
    c: PointOnObject(g1,g-2)
    c: PointOnObject(g1,g-1)
    c: Coincident(g2,g0)
    c: Coincident(g2,g1)
    c: Radius(g1) = 2
    c: Radius(g0) = 4
    c: Tangent(g0,g3) = -1.5708
    c: Coincident(g3,g4)
    c: Vertical(g4)
    c: Coincident(g4,g5)
    c: Coincident(g5,g1)
    c: Horizontal(g5)
    c: DistanceX(g5,g5) = 2
FEATURE [Sketcher::SketchObject] Sketch186  label="pillar2_base_sketch"
  ArcFitTolerance = 0
  AttachmentSupport = -> [XY_Plane086]
  FullyConstrained = true
  MakeInternals = false
  MapMode = 5
  expr: .Constraints.length = <<pillar2_Properties>>.outer_length
  sketch-geometry (5):
    g0: LineSegment StartX=-18.3 StartY=14 StartZ=0 EndX=-18.3 EndY=0 EndZ=0
    g1: LineSegment StartX=-18.3 StartY=0 StartZ=0 EndX=18.3 EndY=0 EndZ=0
    g2: LineSegment StartX=18.3 StartY=0 StartZ=0 EndX=18.3 EndY=14 EndZ=0
    g3: LineSegment [constr] StartX=18.3 StartY=14 StartZ=0 EndX=-18.3 EndY=14 EndZ=0
    g4: GeomPoint [constr] X=0 Y=7 Z=0
  constraints (13):
    c: Coincident(g0,g1)
    c: Coincident(g1,g2)
    c: Coincident(g2,g3)
    c: Coincident(g3,g0)
    c: Horizontal(g1)
    c: Horizontal(g3)
    c: Vertical(g0)
    c: Vertical(g2)
    c: Symmetric(g1,g0,g4)
    c: PointOnObject(g4,g-2)
    c: PointOnObject(g1,g-1)
    c: DistanceX(g1,g1) = 36.6  'width'
    c: DistanceY(g2,g2) = 14  'length'
FEATURE [PartDesign::FeaturePython] BaseBend045  # WARN: FeaturePython — macro-defined, semantics opaque (R4)
  BendSide = 1
  BendSketch = -> Sketch186
  MidPlane = false
  Reverse = false
  Suppressed = false
  length = 1596
  radius = 2
  thickness = 2
FEATURE [Part::FeaturePython] Placment019  # WARN: FeaturePython — macro-defined, semantics opaque (R4)
  AttacherType = Attacher::AttachEngine3D
  ExposePlacement = true
  MarkerShape = 1
  MarkerSize = 10
  NumElements = 1
  Placement = pos=(16.3,8,0) rot=(0.707107,0,0.707107;3.14159rad)
  Type = lattice2AttachablePlacement.AttachablePlacement
  isLattice = 1
  expr: .Placement.Base.x = <<pillar2_base_sketch>>.Constraints.width / 2 - 2 mm
FEATURE [Part::FeaturePython] LinearArray015  # WARN: FeaturePython — macro-defined, semantics opaque (R4)
  Alignment = 0
  CellStart = A1
  Count = 4
  Dir = (0,0,1)
  DirIsDriven = true
  DistributionLaw = 0
  DrivenProperty = 1
  EndInclusive = true
  ExposePlacement = false
  GeneratorMode = 0
  MarkerShape = 1
  MarkerSize = 0
  NumElements = 4
  OrientMode = 0
  Point = (0,0,0)
  PointIsDriven = true
  Reverse = false
  SpanEnd = 100
  SpanStart = 10
  Step = 30
  Type = lattice2LinearArray.LinearArray
  VSGVersion = 1
  Values = 10.0 | 40.0 | 70.0 | 100.0
  ValuesSource = 2
  isLattice = 1
FEATURE [Part::Part2DObjectPython] Join006  # Draft 2D object (typed FeaturePython)
  AttacherType = Attacher::AttachEngine3D
  ExposePlacement = false
  Interleave = false
  Links = -> [Placment019]
  MarkerShape = 1
  MarkerSize = 2
  NumElements = 1
  Type = lattice2JoinArrays.JoinArrays
  isLattice = 1
FEATURE [Part::FeaturePython] Mirror008  label="Mirror008 of Placment019"  # WARN: FeaturePython — macro-defined, semantics opaque (R4)
  ExposePlacement = false
  FlipX = true
  FlipY = false
  FlipZ = false
  MarkerShape = 1
  MarkerSize = 5
  NumElements = 1
  Object = -> Join006
  ObjectTraversal = 0
  Type = lattice2Mirror.LatticeMirror
  isLattice = 1
FEATURE [Part::FeaturePython] Join005  # WARN: FeaturePython — macro-defined, semantics opaque (R4)
  ExposePlacement = false
  Interleave = false
  Links = -> [Mirror008,Join006]
  MarkerShape = 1
  MarkerSize = 0
  NumElements = 2
  Type = lattice2JoinArrays.JoinArrays
  isLattice = 1
FEATURE [Part::FeaturePython] Populate029  label="Populate LinearArray015 with Join005"  # WARN: FeaturePython — macro-defined, semantics opaque (R4)
  Copying = 0
  ExposePlacement = false
  MarkerShape = 1
  MarkerSize = 0
  NumElements = 8
  Object = -> Join005
  OutputCompounding = 0
  PlacementsTo = -> LinearArray015
  Referencing = 0
  Type = lattice2PopulateCopies.LatticePopulateCopies
  isLattice = 1
FEATURE [Part::FeaturePython] Populate030  label="Populate Populate LinearArray015 with Join005 with hole_3.4mm_extrude"  # WARN: FeaturePython — macro-defined, semantics opaque (R4)
  Copying = 0
  ExposePlacement = false
  MarkerShape = 1
  MarkerSize = 0
  NumElements = 0
  Object = -> Extrude019
  OutputCompounding = 1
  PlacementsTo = -> Populate029
  Referencing = 0
  Type = lattice2PopulateCopies.LatticePopulateCopies
  isLattice = 0
FEATURE [Part::Compound] Compound053
  Links = -> [Populate030]
  Placement = pos=(-54.5,18.3,0) rot=(0,0,-1;1.5708rad)
FEATURE [Part::Compound] Compound054  label="pillar2_bottom_cut1"
  Links = -> [Compound053,Populate024]
FEATURE [Spreadsheet::Sheet] Spreadsheet003  label="pillar2_Properties"
  cells = B2(thickness)==2 mm; C2(default_bend_r)==2 mm; D2(outer_width)==36.6 mm; E2(outer_length)==14 mm
FEATURE [Spreadsheet::Sheet] Spreadsheet004  label="pillar2_bottom_Properties"
  cells = B2(thickness)==2 mm; C2(default_bend_r)==2 mm; D2(outer_width)==101 mm; E2(outer_length)==10 mm
FEATURE [Sketcher::SketchObject] Sketch187
  ArcFitTolerance = 0
  AttachmentOffset = pos=(0,1598,0) rot=(0,0,1;0rad)
  AttachmentSupport = -> [XZ_Plane086]
  FullyConstrained = true
  MakeInternals = false
  MapMode = 5
  Placement = pos=(0,3.548e-13,1598) rot=(1,0,0;1.5708rad)
  expr: .AttachmentOffset.Base.y = BaseBend045.length + Sketch188.Constraints.length
  expr: Constraints[11] = <<pillar2_Properties>>.outer_width - 4 mm * 2 + (<<pillar2_Properties>>.outer_length - 4 mm) * 2 + 9.42 mm
  sketch-geometry (5):
    g0: LineSegment StartX=-29.01 StartY=88 StartZ=0 EndX=-29.01 EndY=0 EndZ=0
    g1: LineSegment StartX=-29.01 StartY=0 StartZ=0 EndX=29.01 EndY=0 EndZ=0
    g2: LineSegment StartX=29.01 StartY=0 StartZ=0 EndX=29.01 EndY=88 EndZ=0
    g3: LineSegment StartX=29.01 StartY=88 StartZ=0 EndX=-29.01 EndY=88 EndZ=0
    g4: GeomPoint [constr] X=0 Y=44 Z=0
  constraints (13):
    c: Coincident(g0,g1)
    c: Coincident(g1,g2)
    c: Coincident(g2,g3)
    c: Coincident(g3,g0)
    c: Horizontal(g1)
    c: Horizontal(g3)
    c: Vertical(g0)
    c: Vertical(g2)
    c: Symmetric(g1,g0,g4)
    c: PointOnObject(g4,g-2)
    c: PointOnObject(g1,g-1)
    c: DistanceX(g1,g1) = 58.02
    c: DistanceY(g2,g2) = 88
FEATURE [Sketcher::SketchObject] Sketch188
  ArcFitTolerance = 0
  AttachmentOffset = pos=(0,1596,0) rot=(0,0,1;0rad)
  AttachmentSupport = -> [XZ_Plane086]
  FullyConstrained = true
  MakeInternals = false
  MapMode = 5
  Placement = pos=(0,3.544e-13,1596) rot=(1,0,0;1.5708rad)
  expr: .AttachmentOffset.Base.y = BaseBend045.length
  expr: Constraints[11] = <<pillar2_Properties>>.outer_width - (<<pillar2_Properties>>.thickness + <<pillar2_Properties>>.default_bend_r) * 2
  sketch-geometry (7):
    g0: LineSegment [constr] StartX=-14.3 StartY=2 StartZ=0 EndX=-14.3 EndY=-4e-16 EndZ=0
    g1: LineSegment StartX=-14.3 StartY=-4e-16 StartZ=0 EndX=14.3 EndY=-4e-16 EndZ=0
    g2: LineSegment [constr] StartX=14.3 StartY=-4e-16 StartZ=0 EndX=14.3 EndY=2 EndZ=0
    g3: LineSegment StartX=14.3 StartY=2 StartZ=0 EndX=-14.3 EndY=2 EndZ=0
    g4: GeomPoint [constr] X=-2.547e-12 Y=1 Z=0
    g5: ArcOfCircle CenterX=14.3 CenterY=1 CenterZ=0 NormalX=0 NormalY=0 NormalZ=1 AngleXU=0 Radius=1 StartAngle=1.5708 EndAngle=4.71239
    g6: ArcOfCircle CenterX=-14.3 CenterY=1 CenterZ=0 NormalX=0 NormalY=0 NormalZ=1 AngleXU=0 Radius=1 StartAngle=4.71239 EndAngle=7.85398
  constraints (19):
    c: Coincident(g0,g1)
    c: Coincident(g1,g2)
    c: Coincident(g2,g3)
    c: Coincident(g3,g0)
    c: Horizontal(g1)
    c: Horizontal(g3)
    c: Vertical(g0)
    c: Vertical(g2)
    c: Symmetric(g1,g0,g4)
    c: PointOnObject(g4,g-2)
    c: PointOnObject(g1,g-1)
    c: DistanceX(g1,g1) = 28.6
    c: DistanceY(g2) = 2  'length'
    c: PointOnObject(g5,g2)
    c: Coincident(g5,g1)
    c: Coincident(g5,g3)
    c: PointOnObject(g6,g0)
    c: Coincident(g6,g1)
    c: Coincident(g6,g3)
FEATURE [PartDesign::Pad] Pad024
  BaseFeature = -> BaseBend045
  Direction = (0,-1,2e-16)
  Length = 2
  Length2 = 10
  Profile = -> Sketch188
  ReferenceAxis = -> Sketch188 [N_Axis]
  Reversed = true
  Suppressed = false
  Type = 0
FEATURE [PartDesign::Pad] Pad025
  BaseFeature = -> Pad024
  Direction = (0,-1,2e-16)
  Length = 2
  Length2 = 10
  Profile = -> Sketch187
  ReferenceAxis = -> Sketch187 [N_Axis]
  Reversed = true
  Suppressed = false
  Type = 0
FEATURE [Sketcher::SketchObject] Sketch189
  ArcFitTolerance = 0
  AttachmentSupport = -> [XZ_Plane086]
  ExternalGeometry = -> [Sketch187]
  FullyConstrained = true
  MakeInternals = false
  MapMode = 5
  Placement = pos=(0,0,0) rot=(1,0,0;1.5708rad)
  sketch-geometry (12):
    g0: LineSegment StartX=26.01 StartY=1598 StartZ=0 EndX=29.01 EndY=1598 EndZ=0
    g1: LineSegment StartX=29.01 StartY=1598 StartZ=0 EndX=29.01 EndY=1601 EndZ=0
    g2: LineSegment StartX=29.01 StartY=1683 StartZ=0 EndX=29.01 EndY=1686 EndZ=0
    g3: LineSegment StartX=29.01 StartY=1686 StartZ=0 EndX=26.01 EndY=1686 EndZ=0
    g4: LineSegment StartX=-26.01 StartY=1686 StartZ=0 EndX=-29.01 EndY=1686 EndZ=0
    g5: LineSegment StartX=-29.01 StartY=1686 StartZ=0 EndX=-29.01 EndY=1683 EndZ=0
    g6: LineSegment StartX=-29.01 StartY=1601 StartZ=0 EndX=-29.01 EndY=1598 EndZ=0
    g7: LineSegment StartX=-29.01 StartY=1598 StartZ=0 EndX=-26.01 EndY=1598 EndZ=0
    g8: ArcOfCircle CenterX=26.01 CenterY=1601 CenterZ=0 NormalX=0 NormalY=0 NormalZ=1 AngleXU=0 Radius=3 StartAngle=4.71239 EndAngle=6.28319
    g9: ArcOfCircle CenterX=26.01 CenterY=1683 CenterZ=0 NormalX=0 NormalY=0 NormalZ=1 AngleXU=0 Radius=3 StartAngle=-2.04e-14 EndAngle=1.5708
    g10: ArcOfCircle CenterX=-26.01 CenterY=1683 CenterZ=0 NormalX=0 NormalY=0 NormalZ=1 AngleXU=0 Radius=3 StartAngle=1.5708 EndAngle=3.14159
    g11: ArcOfCircle CenterX=-26.01 CenterY=1601 CenterZ=0 NormalX=0 NormalY=0 NormalZ=1 AngleXU=0 Radius=3 StartAngle=3.14159 EndAngle=4.71239
  constraints (29):
    c: Coincident(g0,g-3)
    c: Horizontal(g0)
    c: Coincident(g0,g1)
    c: PointOnObject(g1,g-3)
    c: PointOnObject(g2,g-3)
    c: Coincident(g2,g-3)
    c: Coincident(g2,g3)
    c: Horizontal(g3)
    c: Coincident(g4,g-4)
    c: Horizontal(g4)
    c: Coincident(g4,g5)
    c: PointOnObject(g5,g-4)
    c: PointOnObject(g6,g-4)
    c: Coincident(g6,g-4)
    c: Coincident(g6,g7)
    c: Horizontal(g7)
    c: Coincident(g9,g3)
    c: Tangent(g8,g0) = -1.5708
    c: Tangent(g8,g1) = -1.5708
    c: Tangent(g9,g2) = -1.5708
    c: Tangent(g9,g3,g3) = -1.5708
    c: Tangent(g10,g4) = -1.5708
    c: Tangent(g10,g5) = -1.5708
    c: Tangent(g11,g7) = -1.5708
    c: Tangent(g11,g6) = -1.5708
    c: Equal(g8,g9)
    c: Equal(g8,g10)
    c: Equal(g8,g11)
    c: Radius(g8) = 3
FEATURE [PartDesign::Pocket] Pocket115
  BaseFeature = -> Pad025
  Direction = (0,1,-2e-16)
  Length = 5
  Length2 = 5
  Profile = -> Sketch189
  ReferenceAxis = -> Sketch189 [N_Axis]
  Suppressed = false
  Type = 1
FEATURE [Part::Extrusion] Extrude022
  Base = -> Compound041
  Dir = (0,0,1)
  DirMode = 2
  FaceMakerClass = Part::FaceMakerBullseye
  FaceMakerMode = 3
  LengthFwd = 30
  LengthRev = 0
  Placement = pos=(0,10,1586) rot=(0.57735,0.57735,-0.57735;2.0944rad)
  Solid = true
  Symmetric = false
FEATURE [Sketcher::SketchObject] Sketch190
  ArcFitTolerance = 0
  AttachmentOffset = pos=(14,0,0) rot=(0,0,1;0rad)
  AttachmentSupport = -> [YZ_Plane086]
  FullyConstrained = true
  MakeInternals = false
  MapMode = 5
  Placement = pos=(0,14,0) rot=(0.57735,0.57735,0.57735;2.0944rad)
  expr: .AttachmentOffset.Base.x = <<pillar2_Properties>>.outer_length
  sketch-geometry (3):
    g0: ArcOfCircle CenterX=-3 CenterY=3 CenterZ=0 NormalX=0 NormalY=0 NormalZ=1 AngleXU=0 Radius=3 StartAngle=4.71239 EndAngle=6.28319
    g1: LineSegment StartX=-5.6e-14 StartY=3 StartZ=0 EndX=-5.6e-14 EndY=0 EndZ=0
    g2: LineSegment StartX=-5.6e-14 StartY=0 StartZ=0 EndX=-3 EndY=6.7e-15 EndZ=0
  constraints (7):
    c: PointOnObject(g0,g-1)
    c: Coincident(g2,g1)
    c: Vertical(g1)
    c: Tangent(g0,g1) = 1.5708
    c: Tangent(g2,g0) = 1.5708
    c: Coincident(g1,g-1)
    c: Radius(g0) = 3
FEATURE [PartDesign::Pocket] Pocket116
  BaseFeature = -> Pocket115
  Direction = (-1,0,0)
  Length = 5
  Length2 = 5
  Midplane = true
  Profile = -> Sketch190
  ReferenceAxis = -> Sketch190 [N_Axis]
  Suppressed = false
  Type = 1
FEATURE [PartDesign::Plane] DatumPlane006
  AttachmentOffset = pos=(0,0,798) rot=(1,0,0;0rad)
  AttachmentSupport = -> [XY_Plane086]
  Length = 68.7922
  MapMode = 5
  Placement = pos=(0,0,798) rot=(0,0,1;0rad)
  ResizeMode = 0
  Width = 60.7722
  expr: .AttachmentOffset.Base.z = BaseBend045.length / 2
FEATURE [PartDesign::Mirrored] Mirrored013
  BaseFeature = -> Pocket116
  MirrorPlane = -> DatumPlane006
  Originals = -> [Pocket116]
  Suppressed = false
  TransformMode = 0
FEATURE [Sketcher::SketchObject] Sketch191  label="top_corner_base_sketch"
  ArcFitTolerance = 0
  AttachmentSupport = -> [XY_Plane087]
  FullyConstrained = true
  MakeInternals = false
  MapMode = 5
  sketch-geometry (2):
    g0: LineSegment StartX=-23.3827 StartY=13.5 StartZ=0 EndX=-5.116e-13 EndY=-3.109e-13 EndZ=0
    g1: LineSegment StartX=-5.116e-13 StartY=-3.109e-13 StartZ=0 EndX=23.3827 EndY=13.5 EndZ=0
  constraints (5):
    c: Coincident(g0,g-1)
    c: Coincident(g0,g1)
    c: Symmetric(g0,g1,g-2)
    c: Angle(g1,g0) = 2.0944
    c: Distance(g1) = 27  'length'
FEATURE [PartDesign::FeaturePython] BaseBend046  # WARN: FeaturePython — macro-defined, semantics opaque (R4)
  BendSide = 0
  BendSketch = -> Sketch191
  MidPlane = false
  Reverse = false
  Suppressed = false
  length = 30
  radius = 2
  thickness = 2
FEATURE [Part::FeaturePython] Placment021  # WARN: FeaturePython — macro-defined, semantics opaque (R4)
  AttacherType = Attacher::AttachEngine3D
  AttachmentOffset = pos=(0,24,-10) rot=(0,1,0;1.5708rad)
  AttachmentSupport = -> [Sketch191]
  ExposePlacement = true
  MapMode = 7
  MarkerShape = 1
  MarkerSize = 2
  NumElements = 1
  Placement = pos=(8.66025,5,24) rot=(0.935113,0.250563,0.250563;1.63783rad)
  Type = lattice2AttachablePlacement.AttachablePlacement
  isLattice = 1
FEATURE [Part::FeaturePython] Placment022  # WARN: FeaturePython — macro-defined, semantics opaque (R4)
  AttacherType = Attacher::AttachEngine3D
  AttachmentOffset = pos=(0,24,-22) rot=(0,1,0;1.5708rad)
  AttachmentSupport = -> [Sketch191]
  ExposePlacement = true
  MapMode = 7
  MarkerShape = 1
  MarkerSize = 2
  NumElements = 1
  Placement = pos=(19.0526,11,24) rot=(0.935113,0.250563,0.250563;1.63783rad)
  Type = lattice2AttachablePlacement.AttachablePlacement
  isLattice = 1
  expr: .AttachmentOffset.Base.z = -(<<top_corner_base_sketch>>.Constraints.length - 5 mm)
FEATURE [PartDesign::Pocket] Pocket117
  BaseFeature = -> Mirrored005
  Direction = (0.866025,0.5,-1e-16)
  Length = 5
  Length2 = 5
  Midplane = true
  Profile = -> Sketch081
  ReferenceAxis = -> Sketch081 [N_Axis]
  Refine = true
  Suppressed = false
  Type = 1
FEATURE [PartDesign::Body] Body078  label="hat_plexiglass_material_0.30ansi"
  AllowCompound = false
  Group = -> [Binder048,BaseBend022,Binder049,DatumPlane003,Hole010,Sketch081,Mirrored005,Binder050,Sketch082,Pocket117]
  Origin = -> Origin043
  Placement = pos=(0,0,-3) rot=(0,0,1;0rad)
  Tip = -> Pocket117
FEATURE [Sketcher::SketchObject] Sketch192
  ArcFitTolerance = 0
  AttachmentSupport = -> [XZ_Plane085]
  FullyConstrained = true
  MakeInternals = false
  MapMode = 5
  Placement = pos=(0,0,0) rot=(1,0,0;1.5708rad)
  sketch-geometry (4):
    g0: LineSegment StartX=-46.5 StartY=-2.18e-14 StartZ=0 EndX=-50.5 EndY=-2.18e-14 EndZ=0
    g1: LineSegment StartX=-50.5 StartY=-2.18e-14 StartZ=0 EndX=-50.5 EndY=4 EndZ=0
    g2: LineSegment StartX=-50.5 StartY=4 StartZ=0 EndX=-46.5 EndY=4 EndZ=0
    g3: LineSegment StartX=-46.5 StartY=4 StartZ=0 EndX=-46.5 EndY=-2.18e-14 EndZ=0
  constraints (12):
    c: Coincident(g0,g1)
    c: Coincident(g1,g2)
    c: Coincident(g2,g3)
    c: Coincident(g3,g0)
    c: Horizontal(g0)
    c: Horizontal(g2)
    c: Vertical(g1)
    c: Vertical(g3)
    c: PointOnObject(g0,g-1)
    c: DistanceX(g0,g0) = 4
    c: Equal(g1,g0)
    c: DistanceX(g0) = -50.5
FEATURE [Sketcher::SketchObject] Sketch193
  ArcFitTolerance = 0
  AttachmentOffset = pos=(0,0,0) rot=(0,1,0;0.523599rad)
  AttachmentSupport = -> [XZ_Plane087]
  FullyConstrained = true
  MakeInternals = false
  MapMode = 5
  Placement = pos=(0,0,0) rot=(0.935113,0.250563,0.250563;1.63783rad)
  expr: Constraints[6] = <<top_corner_base_sketch>>.Constraints.length
  sketch-geometry (9):
    g0: LineSegment StartX=27 StartY=20 StartZ=0 EndX=27 EndY=0 EndZ=0
    g1: LineSegment StartX=27 StartY=0 StartZ=0 EndX=4 EndY=0 EndZ=0
    g2: ArcOfCircle CenterX=24 CenterY=21.3669 CenterZ=0 NormalX=0 NormalY=0 NormalZ=1 AngleXU=0 Radius=3 StartAngle=5.42813 EndAngle=6.28319
    g3: ArcOfCircle CenterX=2.87807 CenterY=3 CenterZ=0 NormalX=0 NormalY=0 NormalZ=1 AngleXU=0 Radius=3 StartAngle=4.71239 EndAngle=5.42813
    g4: LineSegment [constr] StartX=25.9685 StartY=19.1031 StartZ=0 EndX=27 EndY=20 EndZ=0
    g5: LineSegment [constr] StartX=4 StartY=0 StartZ=0 EndX=4.84661 EndY=0.736183 EndZ=0
    g6: LineSegment StartX=4.84661 StartY=0.736183 StartZ=0 EndX=25.9685 EndY=19.1031 EndZ=0
    g7: LineSegment StartX=2.87807 StartY=0 StartZ=0 EndX=4 EndY=0 EndZ=0
    g8: LineSegment StartX=27 StartY=20 StartZ=0 EndX=27 EndY=21.3669 EndZ=0
  constraints (24):
    c: PointOnObject(g5,g-1)
    c: Coincident(g4,g0)
    c: PointOnObject(g0,g-1)
    c: Vertical(g0)
    c: Coincident(g0,g1)
    c: Coincident(g1,g5)
    c: DistanceX(g0) = 27
    c: DistanceX(g5) = 4
    c: Tangent(g2,g0)
    c: Coincident(g5,g6)
    c: Coincident(g7,g1)
    c: Horizontal(g7)
    c: Coincident(g8,g0)
    c: Coincident(g8,g2)
    c: Vertical(g8)
    c: Equal(g3,g2)
    c: Radius(g3) = 3
    c: Tangent(g3,g6) = -1.5708
    c: Tangent(g6,g2) = -1.5708
    c: Coincident(g2,g4)
    c: Parallel(g4,g6)
    c: Parallel(g5,g6)
    c: Tangent(g7,g3) = -1.5708
    c: DistanceY(g0) = 20
FEATURE [Part::FeaturePython] Placment023  # WARN: FeaturePython — macro-defined, semantics opaque (R4)
  AttacherType = Attacher::AttachEngine3D
  AttachmentOffset = pos=(0,12,-10) rot=(0,1,0;1.5708rad)
  AttachmentSupport = -> [Sketch191]
  ExposePlacement = true
  MapMode = 7
  MarkerShape = 1
  MarkerSize = 20
  NumElements = 1
  Placement = pos=(8.66025,5,12) rot=(0.935113,0.250563,0.250563;1.63783rad)
  Type = lattice2AttachablePlacement.AttachablePlacement
  isLattice = 1
FEATURE [Part::FeaturePython] Join007  # WARN: FeaturePython — macro-defined, semantics opaque (R4)
  ExposePlacement = false
  Interleave = false
  Links = -> [Placment021,Placment022,Placment023]
  MarkerShape = 1
  MarkerSize = 0
  NumElements = 3
  Type = lattice2JoinArrays.JoinArrays
  isLattice = 1
FEATURE [Part::FeaturePython] Mirror009  label="Mirror009 of Join007"  # WARN: FeaturePython — macro-defined, semantics opaque (R4)
  ExposePlacement = false
  FlipX = true
  FlipY = false
  FlipZ = false
  MarkerShape = 1
  MarkerSize = 0
  NumElements = 3
  Object = -> Join007
  ObjectTraversal = 0
  Type = lattice2Mirror.LatticeMirror
  isLattice = 1
FEATURE [Part::FeaturePython] Join008  # WARN: FeaturePython — macro-defined, semantics opaque (R4)
  ExposePlacement = false
  Interleave = false
  Links = -> [Mirror009,Join007]
  MarkerShape = 1
  MarkerSize = 0
  NumElements = 6
  Type = lattice2JoinArrays.JoinArrays
  isLattice = 1
FEATURE [Part::FeaturePython] Populate031  label="Populate Join008 with hole_3.4mm_extrude"  # WARN: FeaturePython — macro-defined, semantics opaque (R4)
  Copying = 0
  ExposePlacement = false
  MarkerShape = 1
  MarkerSize = 0
  NumElements = 0
  Object = -> Extrude019
  OutputCompounding = 1
  PlacementsTo = -> Join008
  Referencing = 0
  Type = lattice2PopulateCopies.LatticePopulateCopies
  isLattice = 0
FEATURE [Sketcher::SketchObject] Sketch194
  ArcFitTolerance = 0
  AttachmentSupport = -> [XZ_Plane085]
  FullyConstrained = true
  MakeInternals = false
  MapMode = 5
  Placement = pos=(0,0,0) rot=(1,0,0;1.5708rad)
  sketch-geometry (6):
    g0: LineSegment StartX=-50.5 StartY=108 StartZ=0 EndX=-50.5 EndY=110 EndZ=0
    g1: LineSegment StartX=-50.5 StartY=110 StartZ=0 EndX=-48.5 EndY=110 EndZ=0
    g2: LineSegment StartX=-43.5 StartY=110 StartZ=0 EndX=-35.5 EndY=110 EndZ=0
    g3: LineSegment StartX=-35.5 StartY=110 StartZ=0 EndX=-35.5 EndY=102 EndZ=0
    g4: ArcOfCircle CenterX=-43.5 CenterY=102 CenterZ=0 NormalX=0 NormalY=0 NormalZ=1 AngleXU=0 Radius=8 StartAngle=8.302e-13 EndAngle=1.5708
    g5: ArcOfCircle CenterX=-48.5 CenterY=108 CenterZ=0 NormalX=0 NormalY=0 NormalZ=1 AngleXU=0 Radius=2 StartAngle=1.5708 EndAngle=3.14159
  constraints (16):
    c: Vertical(g0)
    c: Coincident(g0,g1)
    c: Horizontal(g1)
    c: Horizontal(g2)
    c: Coincident(g2,g3)
    c: Vertical(g3)
    c: Horizontal(g0,g2)
    c: DistanceY(g0) = 110
    c: Tangent(g5,g0) = 1.5708
    c: DistanceX(g0) = -50.5
    c: Tangent(g5,g1) = 1.5708
    c: Tangent(g4,g3) = 1.5708
    c: Tangent(g4,g2) = 1.5708
    c: DistanceX(g0,g2) = 15
    c: DistanceX(g0,g2) = 7
    c: Radius(g5) = 2
FEATURE [PartDesign::Pocket] Pocket119
  BaseFeature = -> Pad022
  Direction = (0,1,-2e-16)
  Length = 5
  Length2 = 5
  Midplane = true
  Placement = pos=(0,0,0) rot=(1,1,1;2.0944rad)
  Profile = -> Sketch194
  ReferenceAxis = -> Sketch194 [N_Axis]
  Suppressed = false
  Type = 1
FEATURE [PartDesign::Boolean] Boolean015
  BaseFeature = -> Pocket119
  Group = -> [Compound054]
  Refine = true
  Suppressed = false
  Type = 1
  UsePlacement = false
FEATURE [PartDesign::Body] Body111  label="pillar2_bottom_material_0.50ansi"
  AllowCompound = false
  Group = -> [Sketch180,Pad020,Sketch181,Sketch182,Sketch192,Pad021,Pad022,Sketch183,Sketch184,Sketch185,Pocket119,Boolean015,Sketch194]
  Origin = -> Origin085
  Placement = pos=(18.3,54.5,0) rot=(0,0,1;1.5708rad)
  Tip = -> Boolean015
FEATURE [Part::Mirroring] Part__Mirroring026  label="pillar2_bottom_material_0.50ansi (Mirror #27)"
  Base = (0,0,0)
  Normal = (0,1,0)
  Placement = pos=(0,0,0) rot=(0,0,1;3.14159rad)
  Source = -> Body111
FEATURE [Sketcher::SketchObject] Sketch195
  ArcFitTolerance = 0
  AttachmentSupport = -> [XY_Plane080]
  ExternalGeometry = -> [Sketch174,Sketch171]
  FullyConstrained = true
  MakeInternals = false
  MapMode = 5
  sketch-geometry (9):
    g0: LineSegment StartX=6.08e-14 StartY=555.654 StartZ=0 EndX=42.5 EndY=285 EndZ=0
    g1: LineSegment StartX=42.5 StartY=285 StartZ=0 EndX=0 EndY=285 EndZ=0
    g2: LineSegment StartX=6.08e-14 StartY=555.654 StartZ=0 EndX=0 EndY=555.654 EndZ=0
    g3: LineSegment StartX=0 StartY=555.654 StartZ=0 EndX=0 EndY=285 EndZ=0
    g4: Circle CenterX=36 CenterY=265 CenterZ=0 NormalX=0 NormalY=0 NormalZ=1 AngleXU=0 Radius=2.5
    g5: Circle CenterX=68.9742 CenterY=55.7258 CenterZ=0 NormalX=0 NormalY=0 NormalZ=1 AngleXU=0 Radius=2.5
    g6: Circle CenterX=56.173 CenterY=140.207 CenterZ=0 NormalX=0 NormalY=0 NormalZ=1 AngleXU=0 Radius=2.5
    g7: LineSegment [constr] StartX=68.9742 StartY=55.7258 StartZ=0 EndX=56.173 EndY=140.207 EndZ=0
    g8: LineSegment [constr] StartX=56.173 StartY=140.207 StartZ=0 EndX=36 EndY=265 EndZ=0
  constraints (24):
    c: Coincident(g-3,g0)
    c: Coincident(g0,g-4)
    c: Coincident(g0,g1)
    c: Coincident(g0,g2)
    c: PointOnObject(g2,g-2)
    c: Horizontal(g2)
    c: Coincident(g2,g3)
    c: PointOnObject(g3,g-4)
    c: Vertical(g3)
    c: Coincident(g1,g3)
    c: Diameter(g4) = 5
    c: DistanceX(g-1,g4) = 36
    c: DistanceY(g-1,g4) = 265
    c: Equal(g5,g6)
    c: Equal(g6,g4)
    c: Block(g5)
    c: Block(g6)
    c: Coincident(g7,g5)
    c: Coincident(g7,g6)
    c: Coincident(g8,g6)
    c: Coincident(g8,g4)
    c: DistanceX(g5) = 68.9742
    c: DistanceY(g5) = 55.7258
    c: Distance(g6,g-3) = 419.132
FEATURE [Sketcher::SketchObject] Sketch196
  ArcFitTolerance = 0
  ExternalGeometry = -> [Sketch015]
  FullyConstrained = true
  MakeInternals = false
  sketch-geometry (8):
    g0: LineSegment [constr] StartX=0 StartY=0 StartZ=0 EndX=129.904 EndY=75 EndZ=0
    g1: ArcOfCircle CenterX=0 CenterY=-545.406 CenterZ=0 NormalX=0 NormalY=0 NormalZ=1 AngleXU=0 Radius=735.406 StartAngle=1.50554 EndAngle=1.5708
    g2: ArcOfCircle CenterX=46 CenterY=158.499 CenterZ=0 NormalX=0 NormalY=0 NormalZ=1 AngleXU=0 Radius=30 StartAngle=0.539589 EndAngle=1.50554
    g3: ArcOfCircle CenterX=-6084.95 CenterY=-3513.15 CenterZ=0 NormalX=0 NormalY=0 NormalZ=1 AngleXU=0 Radius=7176.3 StartAngle=0.523599 EndAngle=0.539589
    g4: Circle [constr] CenterX=0 CenterY=0 CenterZ=0 NormalX=0 NormalY=0 NormalZ=1 AngleXU=0 Radius=545.406
    g5: LineSegment [constr] StartX=0 StartY=0 StartZ=0 EndX=219.104 EndY=126.5 EndZ=0
    g6: LineSegment [constr] StartX=0 StartY=0 StartZ=0 EndX=4.89e-14 EndY=253 EndZ=0
    g7: ArcOfCircle [constr] CenterX=0 CenterY=-545.406 CenterZ=0 NormalX=0 NormalY=0 NormalZ=1 AngleXU=0 Radius=798.406 StartAngle=0.821161 EndAngle=1.5708
  constraints (23):
    c: Angle(g0) = 0.523599
    c: Tangent(g2,g1) = -1.5708
    c: Distance(g0) = 150
    c: PointOnObject(g1,g-2)
    c: PointOnObject(g1,g-2)
    c: DistanceY(g1) = 190
    c: Coincident(g3,g0)
    c: Coincident(g0,g-1)
    c: Coincident(g4,g0)
    c: Coincident(g5,g0)
    c: Coincident(g5,g-3)
    c: PointOnObject(g6,g-2)
    c: Coincident(g6,g0)
    c: Equal(g6,g5)
    c: PointOnObject(g7,g4)
    c: Coincident(g7,g6)
    c: PointOnObject(g7,g4)
    c: PointOnObject(g-3,g4)
    c: Coincident(g1,g7)
    c: Tangent(g3,g2) = -1.5708
    c: Perpendicular(g3,g5)
    c: Radius(g2) = 30
    c: DistanceX(g2) = 46
FEATURE [Sketcher::SketchObject] Sketch197  label="hole_5_mm"
  ArcFitTolerance = 0
  FullyConstrained = true
  MakeInternals = false
  sketch-geometry (1):
    g0: Circle CenterX=0 CenterY=0 CenterZ=0 NormalX=0 NormalY=0 NormalZ=1 AngleXU=0 Radius=2.5
  constraints (2):
    c: Coincident(g0,g-1)
    c: Diameter(g0) = 5
FEATURE [Part::Extrusion] Extrude023  label="hole_5_mm_extrude"
  Base = -> Sketch197
  Dir = (0,0,1)
  DirMode = 2
  FaceMakerClass = Part::FaceMakerBullseye
  FaceMakerMode = 3
  LengthFwd = 30
  LengthRev = 0
  Solid = true
  Symmetric = false
FEATURE [Part::FeaturePython] PolarArray003  # WARN: FeaturePython — macro-defined, semantics opaque (R4)
  Alignment = 0
  AttacherType = Attacher::AttachEngine3D
  CellStart = A1
  Count = 9
  DistributionLaw = 0
  EndInclusive = false
  ExposePlacement = false
  FlipX = false
  FlipZ = false
  GeneratorMode = 0
  MarkerShape = 1
  MarkerSize = 0
  NumElements = 9
  OrientMode = 2
  Radius = 137.5
  Reverse = false
  SpanEnd = 360
  SpanStart = 0
  Step = 40
  Type = lattice2PolarArray2.PolarArray
  UseArcRadius = false
  UseArcRange = 0
  VSGVersion = 1
  Values = 0.0 | 40.0 | 80.0 | 120.0 | 160.0 | 200.0 | 240.0 | 280.0 | 320.0
  ValuesSource = 2
  isLattice = 1
FEATURE [Part::Mirroring] Part__Mirroring027  label="Sketch196 (Mirror #28)"
  Base = (0,0,0)
  Normal = (1,0,0)
  Source = -> Sketch196
FEATURE [Part::Compound] Compound055
  Links = -> [Sketch196,Part__Mirroring027]
FEATURE [Part::FeaturePython] Array009  # Draft array (typed FeaturePython)
  AlwaysSyncPlacement = false
  Angle = 360
  ArrayType = 1
  Axis = (0,0,1)
  Base = -> Compound055
  Center = (0,0,0)
  Count = 3
  ExpandArray = false
  Fuse = false
  IntervalAxis = (0,0,0)
  IntervalX = (50,0,0)
  IntervalY = (0,50,0)
  IntervalZ = (0,0,50)
  NumberCircles = 3
  NumberPolar = 3
  NumberX = 2
  NumberY = 2
  NumberZ = 1
  PlacementList = 3 placements: [(0,0,0),(0,0,0),(0,0,0)]
  RadialDistance = 50
  ScaleList = (3) [(1,1,1),(1,1,1),(1,1,1)]
  Symmetry = 1
  TangentialDistance = 25
FEATURE [PartDesign::SubShapeBinder] Binder123
  BindCopyOnChange = 0
  BindMode = 0
  ClaimChildren = true
  Context = -> Part020 [Body114.Binder123.]
  Fuse = false
  MakeFace = true
  OffsetFill = false
  OffsetIntersection = false
  OffsetJoinType = 0
  OffsetOpenResult = false
  PartialLoad = false
  Relative = true
  Support = -> [Array009]
  _Version = 2
FEATURE [PartDesign::Pad] Pad026
  Direction = (0,0,1)
  Length = 18
  Length2 = 10
  Profile = -> Binder123
  Refine = true
  Suppressed = false
  Type = 0
FEATURE [Sketcher::SketchObject] Sketch198  label="hole_10.5mm"
  ArcFitTolerance = 0
  FullyConstrained = true
  MakeInternals = false
  sketch-geometry (1):
    g0: Circle CenterX=0 CenterY=0 CenterZ=0 NormalX=0 NormalY=0 NormalZ=1 AngleXU=0 Radius=5.25
  constraints (2):
    c: Coincident(g0,g-1)
    c: Diameter(g0) = 10.5
FEATURE [Part::Extrusion] Extrude024  label="hole_10.5mm_extrude"
  Base = -> Sketch198
  Dir = (0,0,1)
  DirMode = 2
  FaceMakerClass = Part::FaceMakerBullseye
  FaceMakerMode = 3
  LengthFwd = 30
  LengthRev = 0
  Solid = true
  Symmetric = false
FEATURE [PartDesign::SubShapeBinder] Binder124
  BindCopyOnChange = 0
  BindMode = 0
  ClaimChildren = true
  Context = -> Part020 [Body116.Binder124.]
  Fuse = false
  MakeFace = true
  OffsetFill = false
  OffsetIntersection = false
  OffsetJoinType = 0
  OffsetOpenResult = false
  PartialLoad = false
  Relative = true
  Support = -> [Array003]
  _Version = 2
  expr: Support = Array003._self
FEATURE [PartDesign::Pad] Pad027
  Direction = (0,0,1)
  Length = 18
  Length2 = 10
  Profile = -> Binder124
  Suppressed = false
  Type = 0
FEATURE [PartDesign::SubShapeBinder] Binder125
  BindCopyOnChange = 0
  BindMode = 0
  ClaimChildren = true
  Context = -> Part020 [Body117.Binder125.]
  Fuse = false
  MakeFace = true
  OffsetFill = false
  OffsetIntersection = false
  OffsetJoinType = 0
  OffsetOpenResult = false
  PartialLoad = false
  Relative = false
  Support = -> [Array002]
  _Version = 2
FEATURE [PartDesign::Pad] Pad028
  Direction = (0,0,1)
  Length = 18
  Length2 = 10
  Profile = -> Binder125
  Suppressed = false
  Type = 0
FEATURE [Sketcher::SketchObject] Sketch201  label="basement_v3_bottom_sketch"
  ArcFitTolerance = 0
  FullyConstrained = false
  MakeInternals = false
  sketch-geometry (3):
    g0: LineSegment StartX=0 StartY=383.246 StartZ=0 EndX=33.1532 EndY=383.246 EndZ=0
    g1: LineSegment StartX=33.1532 StartY=383.246 StartZ=0 EndX=190.815 EndY=110.167 EndZ=0
    g2: LineSegment [constr] StartX=0 StartY=0 StartZ=0 EndX=190.815 EndY=110.167 EndZ=0
  constraints (9):
    c: Horizontal(g0)
    c: Coincident(g0,g1)
    c: Coincident(g2,g-1)
    c: Coincident(g2,g1)
    c: Angle(g2) = 0.523599
    c: Perpendicular(g1,g2)
    c: DistanceX(g0) = 33.1532
    c: DistanceY(g0) = 383.246
    c: PointOnObject(g0,g-2)
FEATURE [Part::Mirroring] Part__Mirroring028  label="basement_v3_bottom_sketch (Mirror #29)"
  Base = (0,0,0)
  Normal = (1,0,0)
  Source = -> Sketch201
FEATURE [Part::Compound] Compound057
  Links = -> [Sketch201,Part__Mirroring028]
FEATURE [Part::FeaturePython] Array010  # Draft array (typed FeaturePython)
  AlwaysSyncPlacement = false
  Angle = 360
  ArrayType = 1
  Axis = (0,0,1)
  Base = -> Compound057
  Center = (0,0,0)
  Count = 3
  ExpandArray = false
  Fuse = false
  IntervalAxis = (0,0,0)
  IntervalX = (50,0,0)
  IntervalY = (0,50,0)
  IntervalZ = (0,0,50)
  NumberCircles = 3
  NumberPolar = 3
  NumberX = 2
  NumberY = 2
  NumberZ = 1
  PlacementList = 3 placements: [(0,0,0),(0,0,0),(0,0,0)]
  RadialDistance = 50
  ScaleList = (3) [(1,1,1),(1,1,1),(1,1,1)]
  Symmetry = 1
  TangentialDistance = 25
FEATURE [Sketcher::SketchObject] Sketch202  label="basement_v3_top_sketch"
  ArcFitTolerance = 0
  FullyConstrained = false
  MakeInternals = false
  sketch-geometry (3):
    g0: LineSegment [constr] StartX=9.16e-14 StartY=1.21e-14 StartZ=0 EndX=177.196 EndY=102.304 EndZ=0
    g1: LineSegment StartX=177.196 StartY=102.304 StartZ=0 EndX=37.3483 EndY=344.528 EndZ=0
    g2: LineSegment StartX=37.3483 StartY=344.528 StartZ=0 EndX=0 EndY=344.528 EndZ=0
  constraints (8):
    c: Coincident(g-1,g0)
    c: Coincident(g0,g1)
    c: Coincident(g1,g2)
    c: PointOnObject(g2,g-2)
    c: Horizontal(g2)
    c: Angle(g0) = 0.523599
    c: Perpendicular(g1,g0)
    c: Distance(g0) = 204.609
FEATURE [Part::Mirroring] Part__Mirroring029  label="basement_v3_top_sketch (Mirror #30)"
  Base = (0,0,0)
  Normal = (1,0,0)
  Source = -> Sketch202
FEATURE [Part::Compound] Compound058
  Links = -> [Part__Mirroring029,Sketch202]
FEATURE [Part::FeaturePython] Array011  # Draft array (typed FeaturePython)
  AlwaysSyncPlacement = false
  Angle = 360
  ArrayType = 1
  Axis = (0,0,1)
  Base = -> Compound058
  Center = (0,0,0)
  Count = 3
  ExpandArray = false
  Fuse = false
  IntervalAxis = (0,0,0)
  IntervalX = (50,0,0)
  IntervalY = (0,50,0)
  IntervalZ = (0,0,50)
  NumberCircles = 3
  NumberPolar = 3
  NumberX = 2
  NumberY = 2
  NumberZ = 1
  PlacementList = 3 placements: [(0,0,0),(0,0,0),(0,0,0)]
  RadialDistance = 50
  ScaleList = (3) [(1,1,1),(1,1,1),(1,1,1)]
  Symmetry = 1
  TangentialDistance = 25
FEATURE [Sketcher::SketchObject] Sketch203  label="wheel_holes"
  ArcFitTolerance = 0
  FullyConstrained = true
  MakeInternals = false
  sketch-geometry (9):
    g0: LineSegment [constr] StartX=-20 StartY=-20 StartZ=0 EndX=-20 EndY=20 EndZ=0
    g1: LineSegment [constr] StartX=-20 StartY=20 StartZ=0 EndX=20 EndY=20 EndZ=0
    g2: LineSegment [constr] StartX=20 StartY=20 StartZ=0 EndX=20 EndY=-20 EndZ=0
    g3: LineSegment [constr] StartX=20 StartY=-20 StartZ=0 EndX=-20 EndY=-20 EndZ=0
    g4: GeomPoint [constr] X=0 Y=0 Z=0
    g5: Circle CenterX=20 CenterY=20 CenterZ=0 NormalX=0 NormalY=0 NormalZ=1 AngleXU=0 Radius=1.6
    g6: Circle CenterX=-20 CenterY=20 CenterZ=0 NormalX=0 NormalY=0 NormalZ=1 AngleXU=0 Radius=1.6
    g7: Circle CenterX=-20 CenterY=-20 CenterZ=0 NormalX=0 NormalY=0 NormalZ=1 AngleXU=0 Radius=1.6
    g8: Circle CenterX=20 CenterY=-20 CenterZ=0 NormalX=0 NormalY=0 NormalZ=1 AngleXU=0 Radius=1.6
  constraints (20):
    c: Coincident(g0,g1)
    c: Coincident(g1,g2)
    c: Coincident(g2,g3)
    c: Coincident(g3,g0)
    c: Horizontal(g1)
    c: Horizontal(g3)
    c: Vertical(g0)
    c: Vertical(g2)
    c: Symmetric(g1,g0,g4)
    c: Coincident(g4,g-1)
    c: Equal(g2,g1)
    c: DistanceX(g1,g1) = 40
    c: Coincident(g5,g1)
    c: Coincident(g6,g0)
    c: Coincident(g7,g0)
    c: Coincident(g8,g2)
    c: Equal(g8,g5)
    c: Equal(g5,g7)
    c: Equal(g7,g6)
    c: Diameter(g5) = 3.2
FEATURE [Part::FeaturePython] PolarArray004  label="wheel_holes_placements"  # WARN: FeaturePython — macro-defined, semantics opaque (R4)
  Alignment = 0
  AttacherType = Attacher::AttachEngine3D
  CellStart = A1
  Count = 3
  DistributionLaw = 0
  EndInclusive = false
  ExposePlacement = false
  FlipX = false
  FlipZ = false
  GeneratorMode = 0
  MarkerShape = 1
  MarkerSize = 0
  NumElements = 3
  OrientMode = 2
  Placement = pos=(0,0,0) rot=(0,0,1;1.5708rad)
  Radius = 333
  Reverse = false
  SpanEnd = 360
  SpanStart = 0
  Step = 120
  Type = lattice2PolarArray2.PolarArray
  UseArcRadius = false
  UseArcRange = 0
  VSGVersion = 1
  Values = 0.0 | 120.0 | 240.0
  ValuesSource = 2
  isLattice = 1
FEATURE [Part::Extrusion] Extrude025  label="wheel_holes_extrude"
  Base = -> Sketch203
  Dir = (0,0,1)
  DirMode = 2
  FaceMakerClass = Part::FaceMakerBullseye
  FaceMakerMode = 3
  LengthFwd = 30
  LengthRev = 0
  Solid = true
  Symmetric = false
FEATURE [Part::FeaturePython] Populate033  label="Populate wheel_holes_placements with wheel_holes_extrude"  # WARN: FeaturePython — macro-defined, semantics opaque (R4)
  Copying = 0
  ExposePlacement = false
  MarkerShape = 1
  MarkerSize = 0
  NumElements = 0
  Object = -> Extrude025
  OutputCompounding = 1
  PlacementsTo = -> PolarArray004
  Referencing = 0
  Type = lattice2PopulateCopies.LatticePopulateCopies
  isLattice = 0
FEATURE [Part::Cylinder] Cylinder  label="hole_7.5_mm_extrude"
  Angle = 360
  AttacherType = Attacher::AttachEngine3D
  FirstAngle = 0
  Height = 30
  Radius = 3.5
  SecondAngle = 0
FEATURE [Part::FeaturePython] Populate034  label="Populate PolarArray003 with hole_7.5_mm_extrude"  # WARN: FeaturePython — macro-defined, semantics opaque (R4)
  Copying = 0
  ExposePlacement = false
  MarkerShape = 1
  MarkerSize = 0
  NumElements = 0
  Object = -> Cylinder
  OutputCompounding = 1
  PlacementsTo = -> PolarArray003
  Referencing = 0
  Type = lattice2PopulateCopies.LatticePopulateCopies
  isLattice = 0
FEATURE [Part::Cylinder] Cylinder001  label="hole_3.2_mm_extrude"
  Angle = 360
  AttacherType = Attacher::AttachEngine3D
  FirstAngle = 0
  Height = 30
  Radius = 1.6
  SecondAngle = 0
FEATURE [Part::FeaturePython] Populate035  label="Populate PolarArray003 with hole_3.2_mm"  # WARN: FeaturePython — macro-defined, semantics opaque (R4)
  Copying = 0
  ExposePlacement = false
  MarkerShape = 1
  MarkerSize = 0
  NumElements = 0
  Object = -> Cylinder001
  OutputCompounding = 1
  PlacementsTo = -> PolarArray003
  Referencing = 0
  Type = lattice2PopulateCopies.LatticePopulateCopies
  isLattice = 0
FEATURE [Sketcher::SketchObject] Sketch204
  ArcFitTolerance = 0
  AttachmentOffset = pos=(0,370,0) rot=(0,0,1;0rad)
  AttachmentSupport = -> [XY_Plane092]
  FullyConstrained = true
  MakeInternals = false
  MapMode = 5
  Placement = pos=(0,370,0) rot=(0,0,1;0rad)
  sketch-geometry (1):
    g0: Circle CenterX=0 CenterY=0 CenterZ=0 NormalX=0 NormalY=0 NormalZ=1 AngleXU=0 Radius=4
  constraints (2):
    c: Coincident(g0,g-1)
    c: Diameter(g0) = 8
FEATURE [PartDesign::Hole] Hole021
  BaseFeature = -> Pad028
  CustomThreadClearance = 0
  Depth = 25
  DepthType = 0
  Diameter = 8
  DrillForDepth = false
  DrillPoint = 1
  DrillPointAngle = 118
  HoleCutCountersinkAngle = 90
  HoleCutCustomValues = false
  HoleCutDepth = 0
  HoleCutDiameter = 6.1
  HoleCutType = 0
  ModelThread = false
  Profile = -> Sketch204
  Reversed = true
  Suppressed = false
  Tapered = false
  TaperedAngle = 90
  ThreadClass = 0
  ThreadDepth = 25
  ThreadDepthType = 0
  ThreadDirection = 0
  ThreadFit = 0
  ThreadSize = 0
  ThreadType = 0
  Threaded = false
  UseCustomThreadClearance = false
FEATURE [PartDesign::PolarPattern] PolarPattern011
  Angle = 360
  Axis = -> Z_Axis092
  BaseFeature = -> Hole021
  Mode = 0
  Occurrences = 3
  Offset = 120
  Originals = -> [Hole021]
  Suppressed = false
  TransformMode = 0
FEATURE [Sketcher::SketchObject] Sketch205
  ArcFitTolerance = 0
  AttachmentSupport = -> [XZ_Plane096]
  FullyConstrained = true
  MakeInternals = false
  MapMode = 5
  Placement = pos=(0,0,0) rot=(1,0,0;1.5708rad)
  sketch-geometry (4):
    g0: LineSegment StartX=0.1 StartY=485 StartZ=0 EndX=-14 EndY=485 EndZ=0
    g1: LineSegment StartX=-14 StartY=485 StartZ=0 EndX=-14 EndY=1590 EndZ=0
    g2: LineSegment StartX=-14 StartY=1590 StartZ=0 EndX=0.1 EndY=1590 EndZ=0
    g3: LineSegment StartX=0.1 StartY=1590 StartZ=0 EndX=0.1 EndY=485 EndZ=0
  constraints (13):
    c: Coincident(g0,g1)
    c: Coincident(g1,g2)
    c: Coincident(g2,g3)
    c: Coincident(g3,g0)
    c: Horizontal(g0)
    c: Horizontal(g2)
    c: Vertical(g1)
    c: Vertical(g3)
    c: DistanceY(g2) = 1590
    c: DistanceX(g2) = 0.1
    c: DistanceX(g1) = -14
    c: DistanceY(g0) = 485
    c: DistanceY(g3,g3) = 1105
FEATURE [Part::Cylinder] Cylinder002  label="hole_7_mm_extrude"
  Angle = 360
  AttacherType = Attacher::AttachEngine3D
  FirstAngle = 0
  Height = 20
  Radius = 5.5
  SecondAngle = 0
FEATURE [Part::FeaturePython] Populate036  label="Populate led_holder_fix_array with hole_7_mm_extrude"  # WARN: FeaturePython — macro-defined, semantics opaque (R4)
  Copying = 0
  ExposePlacement = false
  MarkerShape = 1
  MarkerSize = 0
  NumElements = 0
  Object = -> Cylinder002
  OutputCompounding = 1
  Placement = pos=(0,11.8848,1584) rot=(0.57735,0.57735,-0.57735;2.0944rad)
  PlacementsTo = -> LinearArray012
  Referencing = 0
  Type = lattice2PopulateCopies.LatticePopulateCopies
  isLattice = 0
FEATURE [Part::Compound] Compound060  label="led_holder_2_cut1"
  Links = -> [Populate036]
FEATURE [PartDesign::Pad] Pad029
  Direction = (0,-1,2e-16)
  Length = 3
  Length2 = 10
  Placement = pos=(0,0,0) rot=(1,0,0;1.5708rad)
  Profile = -> Sketch205
  ReferenceAxis = -> Sketch205 [N_Axis]
  Suppressed = false
  Type = 0
FEATURE [PartDesign::Boolean] Boolean020
  BaseFeature = -> Pad029
  Group = -> [Compound060]
  Suppressed = false
  Type = 1
  UsePlacement = false
FEATURE [Sketcher::SketchObject] Sketch206
  ArcFitTolerance = 0
  AttachmentSupport = -> [XZ_Plane096]
  ExternalGeometry = -> [Sketch205]
  FullyConstrained = true
  MakeInternals = false
  MapMode = 5
  Placement = pos=(0,0,0) rot=(1,0,0;1.5708rad)
  sketch-geometry (13):
    g0: LineSegment [constr] StartX=-14 StartY=1590 StartZ=0 EndX=-6.95 EndY=1570 EndZ=0
    g1: LineSegment [constr] StartX=-6.95 StartY=1570 StartZ=0 EndX=0.1 EndY=1590 EndZ=0
    g2: LineSegment [constr] StartX=-14 StartY=485 StartZ=0 EndX=-6.95 EndY=505 EndZ=0
    g3: LineSegment [constr] StartX=-6.95 StartY=505 StartZ=0 EndX=0.1 EndY=485 EndZ=0
    g4: Circle CenterX=-6.95 CenterY=1570 CenterZ=0 NormalX=0 NormalY=0 NormalZ=1 AngleXU=0 Radius=1.7
    g5: Circle CenterX=-6.95 CenterY=1057.5 CenterZ=0 NormalX=0 NormalY=0 NormalZ=1 AngleXU=0 Radius=1.7
    g6: Circle CenterX=-6.95 CenterY=505 CenterZ=0 NormalX=0 NormalY=0 NormalZ=1 AngleXU=0 Radius=1.7
    g7: Circle CenterX=-6.95 CenterY=786.25 CenterZ=0 NormalX=0 NormalY=0 NormalZ=1 AngleXU=0 Radius=1.7
    g8: Circle CenterX=-6.95 CenterY=1288.75 CenterZ=0 NormalX=0 NormalY=0 NormalZ=1 AngleXU=0 Radius=1.7
    g9: LineSegment [constr] StartX=-6.95 StartY=505 StartZ=0 EndX=-6.95 EndY=771.25 EndZ=0
    g10: LineSegment [constr] StartX=-6.95 StartY=771.25 StartZ=0 EndX=-6.95 EndY=1037.5 EndZ=0
    g11: LineSegment [constr] StartX=-6.95 StartY=1037.5 StartZ=0 EndX=-6.95 EndY=1303.75 EndZ=0
    g12: LineSegment [constr] StartX=-6.95 StartY=1303.75 StartZ=0 EndX=-6.95 EndY=1570 EndZ=0
  constraints (34):
    c: Coincident(g-4,g0)
    c: Coincident(g0,g1)
    c: Coincident(g1,g-4)
    c: Coincident(g-3,g2)
    c: Coincident(g2,g3)
    c: Coincident(g3,g-3)
    c: Equal(g2,g3)
    c: Equal(g3,g0)
    c: Equal(g0,g1)
    c: DistanceY(g2,g2) = 20
    c: Coincident(g9,g2)
    c: Coincident(g11,g10)
    c: Coincident(g12,g0)
    c: Coincident(g4,g0)
    c: Coincident(g6,g2)
    c: Equal(g6,g5)
    c: Equal(g6,g4)
    c: Diameter(g6) = 3.4
    c: DistanceY(g10,g5) = 20
    c: Equal(g8,g7)
    c: Equal(g7,g6)
    c: Coincident(g9,g10)
    c: Vertical(g9)
    c: Vertical(g10)
    c: PointOnObject(g7,g9)
    c: Equal(g9,g10)
    c: Coincident(g11,g12)
    c: PointOnObject(g5,g11)
    c: PointOnObject(g8,g11)
    c: Equal(g11,g12)
    c: Equal(g10,g11)
    c: DistanceY(g8,g11) = 15
    c: DistanceY(g9,g7) = 15
    c: Vertical(g11)
FEATURE [PartDesign::Pocket] Pocket123
  BaseFeature = -> Boolean020
  Direction = (0,1,-2e-16)
  Length = 5
  Length2 = 5
  Midplane = true
  Profile = -> Sketch206
  ReferenceAxis = -> Sketch206 [N_Axis]
  Suppressed = false
  Type = 1
FEATURE [PartDesign::Body] Body120  label="led_holder2"
  AllowCompound = false
  Group = -> [Sketch205,Pad029,Boolean020,Sketch206,Pocket123]
  Origin = -> Origin096
  Placement = pos=(0,3.2,0) rot=(0,0,1;3.14159rad)
  Tip = -> Pocket123
FEATURE [Sketcher::SketchObject] Sketch207  label="sector_plexiglass_sketch"
  ArcFitTolerance = 0
  FullyConstrained = true
  MakeInternals = false
  expr: .Constraints.offset = <<plexiglass_bottom_fix_extrude>>.Placement.Base.y + <<plexiglass_bottom_fix_sketch>>.Constraints.width / 2
  expr: Constraints[3] = <<Properties>>.endface_width / 2
  sketch-geometry (5):
    g0: ArcOfCircle CenterX=0 CenterY=549.544 CenterZ=0 NormalX=0 NormalY=0 NormalZ=1 AngleXU=0 Radius=784.544 StartAngle=4.71239 EndAngle=5.08305
    g1: LineSegment [constr] StartX=-7.25 StartY=-12.5574 StartZ=0 EndX=285.12 EndY=-181.357 EndZ=0
    g2: LineSegment [constr] StartX=-7.25 StartY=-12.5574 StartZ=0 EndX=0 EndY=0 EndZ=0
    g3: LineSegment StartX=284.188 StartY=-181.72 StartZ=0 EndX=295.373 EndY=-177.373 EndZ=0
    g4: LineSegment [constr] StartX=295.373 StartY=-177.373 StartZ=0 EndX=751.783 EndY=0 EndZ=0
  constraints (17):
    c: PointOnObject(g0,g-2)
    c: PointOnObject(g0,g-2)
    c: Angle(g1) = -0.523599
    c: Distance(g-1,g1) = 14.5
    c: Coincident(g2,g1)
    c: Coincident(g2,g-1)
    c: Perpendicular(g2,g1)
    c: Distance(g1) = 337.6  'offset'
    c: PointOnObject(g4,g-1)
    c: Coincident(g3,g4)
    c: Parallel(g3,g4)
    c: Tangent(g3,g0) = -1.5708
    c: Distance(g3) = 12
    c: PointOnObject(g1,g3)
    c: Distance(g0,g1) = 1
    c: Angle(g4) = 0.370663
    c: DistanceY(g0) = -235
FEATURE [Part::Mirroring] Part__Mirroring030  label="sector_plexiglass_sketch (Mirror #31)"
  Base = (0,0,0)
  Normal = (1,0,0)
  Source = -> Sketch207
FEATURE [Part::Compound] Compound061
  Links = -> [Sketch207,Part__Mirroring030]
FEATURE [PartDesign::SubShapeBinder] Binder128
  BindCopyOnChange = 0
  BindMode = 0
  ClaimChildren = true
  Context = -> Body121 [Binder128.]
  Fuse = false
  MakeFace = true
  OffsetFill = false
  OffsetIntersection = false
  OffsetJoinType = 0
  OffsetOpenResult = false
  PartialLoad = false
  Relative = false
  Support = -> [Compound061]
  _Version = 2
FEATURE [PartDesign::FeaturePython] BaseBend049  label="sector_plexiglass_BaseBend"  # WARN: FeaturePython — macro-defined, semantics opaque (R4)
  BendSide = 1
  BendSketch = -> Binder128
  MidPlane = false
  Reverse = false
  Suppressed = false
  length = 425
  radius = 1
  thickness = 1
FEATURE [PartDesign::CoordinateSystem] Local_CS004
  AttacherType = Attacher::AttachEngine3D
  AttachmentOffset = pos=(0,0,0) rot=(0,-1,0;1.5708rad)
  AttachmentSupport = -> [Binder128]
  MapMode = 7
  Placement = pos=(284.188,-181.72,0) rot=(0.131421,-0.700974,-0.700974;2.88025rad)
FEATURE [Sketcher::SketchObject] Sketch208
  ArcFitTolerance = 0
  AttachmentSupport = -> [Local_CS004]
  FullyConstrained = true
  MakeInternals = false
  MapMode = 5
  Placement = pos=(284.188,-181.72,0) rot=(-0.131421,0.700974,0.700974;3.40294rad)
  expr: Constraints[4] = <<plexiglass_bottom_fix_array>>.Step * 1 mm - <<plexiglass_bottom_fix_sketch>>.Constraints.length + 2 mm
  expr: Constraints[6] = <<plexiglass_bottom_fix_array>>.SpanStart - <<plexiglass_bottom_fix_array>>.Step * 1 mm / 2
  sketch-geometry (7):
    g0: LineSegment StartX=-12 StartY=-63.3333 StartZ=0 EndX=-12 EndY=15 EndZ=0
    g1: LineSegment StartX=-1 StartY=10 StartZ=0 EndX=-1 EndY=-58.3333 EndZ=0
    g2: GeomPoint [constr] X=-1 Y=-24.1667 Z=0
    g3: LineSegment StartX=-7 StartY=10 StartZ=0 EndX=-1 EndY=10 EndZ=0
    g4: LineSegment StartX=-1 StartY=-58.3333 StartZ=0 EndX=-7 EndY=-58.3333 EndZ=0
    g5: ArcOfCircle CenterX=-7 CenterY=15 CenterZ=0 NormalX=0 NormalY=0 NormalZ=1 AngleXU=0 Radius=5 StartAngle=3.14159 EndAngle=4.71239
    g6: ArcOfCircle CenterX=-7 CenterY=-63.3333 CenterZ=0 NormalX=0 NormalY=0 NormalZ=1 AngleXU=0 Radius=5 StartAngle=1.5708 EndAngle=3.14159
  constraints (17):
    c: Coincident(g3,g1)
    c: Coincident(g1,g4)
    c: Vertical(g0)
    c: Vertical(g1)
    c: DistanceY(g1,g1) = 68.3333
    c: Symmetric(g4,g3,g2)
    c: DistanceY(g2) = -24.1667
    c: Horizontal(g3)
    c: Horizontal(g4)
    c: Tangent(g5,g3) = -1.5708
    c: Tangent(g5,g0) = 1.5708
    c: Tangent(g6,g4) = -1.5708
    c: Tangent(g6,g0) = 1.5708
    c: Equal(g6,g5)
    c: Radius(g6) = 5
    c: Distance(g-1,g0) = 12
    c: Distance(g-1,g1) = 1
FEATURE [PartDesign::Pocket] Pocket124
  BaseFeature = -> BaseBend049
  Direction = (0.362233,-0.932087,0)
  Length = 5
  Length2 = 5
  Midplane = true
  Profile = -> Sketch208
  ReferenceAxis = -> Sketch208 [N_Axis]
  Suppressed = false
  Type = 1
FEATURE [PartDesign::LinearPattern] LinearPattern
  Direction = -> Z_Axis097
  Length = 591.667
  Mode = 1
  Occurrences = 6
  Offset = 118.333
  Suppressed = false
  TransformMode = 0
  expr: Length = <<plexiglass_bottom_fix_array>>.Step
  expr: Offset = <<plexiglass_bottom_fix_array>>.Step
FEATURE [PartDesign::Mirrored] Mirrored015
  MirrorPlane = -> YZ_Plane097
  Suppressed = false
  TransformMode = 0
FEATURE [PartDesign::MultiTransform] MultiTransform001
  BaseFeature = -> Pocket124
  Originals = -> [Pocket124]
  Suppressed = false
  TransformMode = 0
  Transformations = -> [LinearPattern,Mirrored015]
FEATURE [App::Link] Link039  label="top_fix_holes"
  LinkedObject = -> <external hub2108.FCStd>#Sketch
FEATURE [App::Link] Link040  label="top_center_hole"
  LinkedObject = -> <external hub2108.FCStd>#Sketch001
FEATURE [PartDesign::SubShapeBinder] Binder129
  BindCopyOnChange = 0
  BindMode = 0
  ClaimChildren = false
  Context = -> Link028 [Binder129.]
  Fuse = false
  MakeFace = true
  OffsetFill = false
  OffsetIntersection = false
  OffsetJoinType = 0
  OffsetOpenResult = false
  PartialLoad = false
  Relative = true
  Support = -> [Link005[Hole.Binder001.]]
  _Version = 2
FEATURE [PartDesign::SubShapeBinder] Binder130  label="U-fix_bottom_holes"
  BindCopyOnChange = 0
  BindMode = 0
  ClaimChildren = false
  Fuse = false
  MakeFace = true
  OffsetFill = false
  OffsetIntersection = false
  OffsetJoinType = 0
  OffsetOpenResult = false
  PartialLoad = false
  Placement = pos=(0,0,0) rot=(0,0,1;1.5708rad)
  Relative = false
  Support = -> [<external U-fix.FCStd>#Sketch002]
  _Version = 2
  expr: Support = <<U-fix>>#<<holes_bottom>>._self
FEATURE [Part::Extrusion] Extrude027  label="U-fix_bottom_holes_extrude"
  Base = -> Binder130
  Dir = (0,0,1)
  DirMode = 2
  FaceMakerClass = Part::FaceMakerBullseye
  FaceMakerMode = 3
  LengthFwd = 20
  LengthRev = 0
  Solid = false
  Symmetric = false
FEATURE [Part::FeaturePython] PolarArray005  label="U-fix_bottom_array"  # WARN: FeaturePython — macro-defined, semantics opaque (R4)
  Alignment = 0
  AttacherType = Attacher::AttachEngine3D
  CellStart = A1
  Count = 3
  DistributionLaw = 0
  EndInclusive = false
  ExposePlacement = false
  FlipX = false
  FlipZ = false
  GeneratorMode = 0
  MarkerShape = 1
  MarkerSize = 0
  NumElements = 3
  OrientMode = 2
  Placement = pos=(0,0,0) rot=(0,0,1;1.5708rad)
  Radius = 294.4
  Reverse = false
  SpanEnd = 360
  SpanStart = 0
  Step = 120
  Type = lattice2PolarArray2.PolarArray
  UseArcRadius = false
  UseArcRange = 0
  VSGVersion = 1
  Values = 0.0 | 120.0 | 240.0
  ValuesSource = 2
  isLattice = 1
  expr: Radius = <<U-fix_vert_holes_extrude>>.Placement.Base.y
FEATURE [Part::FeaturePython] Populate037  label="Populate U-fix_bottom_array with U-fix_bottom_holes_extrude"  # WARN: FeaturePython — macro-defined, semantics opaque (R4)
  Copying = 0
  ExposePlacement = false
  MarkerShape = 1
  MarkerSize = 0
  NumElements = 0
  Object = -> Extrude027
  OutputCompounding = 1
  PlacementsTo = -> PolarArray005
  Referencing = 0
  Type = lattice2PopulateCopies.LatticePopulateCopies
  isLattice = 0
FEATURE [Sketcher::SketchObject] Sketch209  label="basin_stop_sketch"
  ArcFitTolerance = 0
  FullyConstrained = true
  MakeInternals = false
  sketch-geometry (5):
    g0: ArcOfCircle CenterX=152.272 CenterY=-105.063 CenterZ=0 NormalX=0 NormalY=0 NormalZ=1 AngleXU=0 Radius=15 StartAngle=1.20141 EndAngle=2.53763
    g1: ArcOfCircle CenterX=156.785 CenterY=-93.4065 CenterZ=0 NormalX=0 NormalY=0 NormalZ=1 AngleXU=0 Radius=2.5 StartAngle=5.74589 EndAngle=7.48459
    g2: ArcOfCircle CenterX=0 CenterY=0 CenterZ=0 NormalX=0 NormalY=0 NormalZ=1 AngleXU=0 Radius=170 StartAngle=4.71239 EndAngle=5.67922
    g3: ArcOfCircle CenterX=0 CenterY=0 CenterZ=0 NormalX=0 NormalY=0 NormalZ=1 AngleXU=0 Radius=185 StartAngle=4.71239 EndAngle=5.74589
    g4: LineSegment [constr] StartX=0 StartY=0 StartZ=0 EndX=158.035 EndY=-91.2414 EndZ=0
  constraints (14):
    c: PointOnObject(g2,g-2)
    c: PointOnObject(g3,g-2)
    c: DistanceY(g3) = -185
    c: DistanceY(g2) = -170
    c: Radius(g1) = 2.5
    c: Tangent(g2,g0) = 1.5708
    c: Tangent(g3,g1) = -1.5708
    c: Tangent(g0,g1) = -1.5708
    c: PointOnObject(g0,g3)
    c: Coincident(g3,g2)
    c: Coincident(g2,g-1)
    c: Coincident(g4,g2)
    c: Tangent(g4,g1) = 1.5708
    c: Angle(g4) = -0.523599
FEATURE [Part::Mirroring] Part__Mirroring031  label="basin_stop_sketch (Mirror #32)"
  Base = (0,0,0)
  Normal = (1,0,0)
  Source = -> Sketch209
FEATURE [Part::Compound] Compound064
  Links = -> [Part__Mirroring031,Sketch209]
FEATURE [PartDesign::SubShapeBinder] Binder131
  BindCopyOnChange = 0
  BindMode = 0
  ClaimChildren = true
  Fuse = false
  MakeFace = true
  OffsetFill = false
  OffsetIntersection = false
  OffsetJoinType = 0
  OffsetOpenResult = false
  PartialLoad = false
  Placement = pos=(0,0,0) rot=(0,0,1;3.14159rad)
  Relative = false
  Support = -> [Compound064]
  _Version = 2
FEATURE [PartDesign::Pad] Pad030
  Direction = (0,0,1)
  Length = 3
  Length2 = 10
  Placement = pos=(0,0,0) rot=(0,0,1;3.14159rad)
  Profile = -> Binder131
  Refine = true
  Suppressed = false
  Type = 0
FEATURE [Sketcher::SketchObject] Sketch210
  ArcFitTolerance = 0
  ExternalGeometry = -> [Sketch209]
  FullyConstrained = false
  MakeInternals = false
  sketch-geometry (4):
    g0: LineSegment StartX=51.5032 StartY=-169.937 StartZ=0 EndX=56.2455 EndY=-168.353 EndZ=0
    g1: LineSegment StartX=56.2455 StartY=-168.353 StartZ=0 EndX=49.908 EndY=-149.384 EndZ=0
    g2: LineSegment StartX=143.621 StartY=-105.272 StartZ=0 EndX=146.462 EndY=-101.158 EndZ=0
    g3: LineSegment StartX=146.462 StartY=-101.158 StartZ=0 EndX=130.006 EndY=-89.7916 EndZ=0
  constraints (12):
    c: Coincident(g1,g0)
    c: Coincident(g3,g2)
    c: Perpendicular(g1,g0)
    c: Perpendicular(g3,g2)
    c: Equal(g0,g2)
    c: Equal(g1,g3)
    c: Distance(g0) = 5
    c: Distance(g1) = 20
    c: DistanceX(g0) = 56.2455
    c: DistanceY(g0) = -168.353
    c: DistanceX(g2) = 146.462
    c: DistanceY(g2) = -101.158
FEATURE [Part::FeaturePython] Placment024  # WARN: FeaturePython — macro-defined, semantics opaque (R4)
  AttacherType = Attacher::AttachEngine3D
  AttachmentOffset = pos=(0,0,0) rot=(0,0,1;1.5708rad)
  AttachmentSupport = -> [Sketch210]
  ExposePlacement = true
  MapMode = 49
  MarkerShape = 1
  MarkerSize = 10
  NumElements = 1
  Placement = pos=(56.2455,-168.353,0) rot=(0,0,1;1.89323rad)
  Type = lattice2AttachablePlacement.AttachablePlacement
  isLattice = 1
FEATURE [Part::FeaturePython] PlacementSubsequence  # WARN: FeaturePython — macro-defined, semantics opaque (R4)
  Base = -> Placment024
  CycleMode = 0
  ExposePlacement = false
  MarkerShape = 1
  MarkerSize = 0
  NumElements = 2
  Type = lattice2AttachablePlacement.AttachedPlacementSubsequence
  isLattice = 1
FEATURE [Part::FeaturePython] Mirror010  label="Mirror010 of PlacementSubsequence"  # WARN: FeaturePython — macro-defined, semantics opaque (R4)
  ExposePlacement = false
  FlipX = true
  FlipY = false
  FlipZ = false
  MarkerShape = 1
  MarkerSize = 0
  NumElements = 2
  Object = -> PlacementSubsequence
  ObjectTraversal = 0
  Type = lattice2Mirror.LatticeMirror
  isLattice = 1
FEATURE [Part::FeaturePython] Join009  label="basin_limiter_placements"  # WARN: FeaturePython — macro-defined, semantics opaque (R4)
  ExposePlacement = false
  Interleave = false
  Links = -> [Mirror010,PlacementSubsequence]
  MarkerShape = 1
  MarkerSize = 0
  NumElements = 4
  Type = lattice2JoinArrays.JoinArrays
  isLattice = 1
FEATURE [Part::FeaturePython] Populate038  label="Populate basin_limiter_placements with hole_3.4mm_extrude"  # WARN: FeaturePython — macro-defined, semantics opaque (R4)
  Copying = 0
  ExposePlacement = false
  MarkerShape = 1
  MarkerSize = 0
  NumElements = 0
  Object = -> Extrude019
  OutputCompounding = 1
  Placement = pos=(0,0,0) rot=(0,0,1;3.14159rad)
  PlacementsTo = -> Join009
  Referencing = 0
  Type = lattice2PopulateCopies.LatticePopulateCopies
  isLattice = 0
FEATURE [Part::Compound] Compound063  label="basement_proxy_cut1"
  Links = -> [Populate037,Populate038]
FEATURE [PartDesign::Boolean] Boolean021
  BaseFeature = -> Pad003
  Group = -> [Compound063]
  Suppressed = false
  Type = 1
  UsePlacement = false
FEATURE [Part::Compound] Compound065  label="basin_limiter_cut1"
  Links = -> [Populate038]
FEATURE [PartDesign::Boolean] Boolean022
  BaseFeature = -> Pad030
  Group = -> [Compound065]
  Refine = true
  Suppressed = false
  Type = 1
  UsePlacement = false
FEATURE [PartDesign::SubShapeBinder] Binder132
  BindCopyOnChange = 0
  BindMode = 0
  ClaimChildren = true
  Fuse = false
  MakeFace = true
  OffsetFill = false
  OffsetIntersection = false
  OffsetJoinType = 0
  OffsetOpenResult = false
  PartialLoad = false
  Relative = false
  Support = -> [Sketch017]
  _Version = 2
FEATURE [PartDesign::SubShapeBinder] Binder133
  BindCopyOnChange = 0
  BindMode = 0
  ClaimChildren = true
  Context = -> Body122 [Binder133.]
  Fuse = false
  MakeFace = true
  OffsetFill = false
  OffsetIntersection = false
  OffsetJoinType = 0
  OffsetOpenResult = false
  PartialLoad = false
  Relative = true
  Support = -> [Sketch210]
  _Version = 2
FEATURE [PartDesign::Body] Body122  label="basin_limiter"
  AllowCompound = false
  Group = -> [Binder131,Pad030,Boolean022,Binder133]
  Origin = -> Origin098
  Placement = pos=(0,0,21) rot=(0,0,1;0rad)
  Tip = -> Boolean022
FEATURE [PartDesign::Pocket] Pocket125
  BaseFeature = -> Pocket002
  Direction = (0,0,-1)
  Length = 5
  Length2 = 5
  Midplane = true
  Profile = -> Binder014
  Suppressed = false
  Type = 1
FEATURE [PartDesign::Pocket] Pocket003
  BaseFeature = -> Pocket125
  Direction = (0,0,-1)
  Length = 5
  Length2 = 5
  Midplane = true
  Profile = -> Sketch020
  ReferenceAxis = -> Sketch020 [N_Axis]
  Suppressed = false
  Type = 1
FEATURE [PartDesign::Mirrored] Mirrored
  BaseFeature = -> Pocket003
  MirrorPlane = -> YZ_Plane005
  Suppressed = false
  TransformMode = 0
FEATURE [PartDesign::Pocket] Pocket005
  BaseFeature = -> Mirrored
  Direction = (-1,0,0)
  Length = 5
  Length2 = 5
  Midplane = true
  Profile = -> WireFilter002
  Suppressed = false
  Type = 1
FEATURE [Part::Extrusion] Extrude028
  Base = -> Populate017
  Dir = (0,0,1)
  DirMode = 2
  FaceMakerClass = Part::FaceMakerBullseye
  FaceMakerMode = 3
  LengthFwd = 10
  LengthRev = 0
  Placement = pos=(0,10,1586) rot=(0.57735,0.57735,-0.57735;2.0944rad)
  Solid = true
  Symmetric = false
  expr: Placement = <<Extrude022>>.Placement
FEATURE [Part::Compound] Compound052  label="pillar2_cut1"
  Links = -> [Populate030,Extrude022,Extrude028]
FEATURE [PartDesign::Boolean] Boolean016
  BaseFeature = -> Mirrored013
  Group = -> [Compound052]
  Refine = true
  Suppressed = false
  Type = 1
  UsePlacement = false
FEATURE [PartDesign::Body] Body112  label="pillar2_material_0.50ansi"
  AllowCompound = false
  Group = -> [Sketch186,BaseBend045,Sketch187,Sketch188,Pad024,Pad025,Sketch189,Pocket115,Sketch190,Pocket116,DatumPlane006,Mirrored013,Boolean016]
  Origin = -> Origin086
  Tip = -> Boolean016
FEATURE [App::Part] Part019  label="pillar2"
  Group = -> [Body111,Body112,Spreadsheet003,Spreadsheet004,Part__Mirroring026]
  Origin = -> Origin084
  Placement = pos=(0,384,0) rot=(0,0,1;3.14159rad)
FEATURE [Part::FeaturePython] Connect003  # WARN: FeaturePython — macro-defined, semantics opaque (R4)
  Objects = -> [Array011]
  Tolerance = 0
FEATURE [PartDesign::FeaturePython] Bend029  # WARN: FeaturePython — macro-defined, semantics opaque (R4)
  AutoMiter = true
  BaseFeature = -> BaseBend046
  BendType = 0
  LengthList = [20]
  LengthSpec = 1
  NonperforationMaxLength = 5
  Perforate = false
  PerforationAngle = 0
  PerforationInitialLength = 5
  PerforationMaxLength = 5
  ReliefFactor = 0.7
  Suppressed = false
  UseReliefFactor = false
  angle = 90
  baseObject = -> BaseBend046 [Edge17]
  bendAList = [90]
  extend1 = 0
  extend2 = 0
  gap1 = 0
  gap2 = 0
  invert = true
  kfactor = 0.5
  length = 20
  maxExtendDist = 5
  minGap = 0.1
  minReliefGap = 1
  miterangle1 = 0
  miterangle2 = 0
  offset = 0
  radius = 2
  reliefType = 0
  reliefd = 1
  reliefw = 0.8
  sketchflip = false
  sketchinvert = false
  unfold = false
  expr: radius = BaseBend046.radius
FEATURE [PartDesign::Fillet] Fillet014
  Base = -> Bend029 [Edge8,Edge40,Edge42]
  BaseFeature = -> Bend029
  Radius = 2
  SupportTransform = false
  Suppressed = false
  UseAllEdges = false
FEATURE [PartDesign::Pocket] Pocket118
  BaseFeature = -> Fillet014
  Direction = (-0.5,0.866025,-1e-16)
  Length = 5
  Length2 = 5
  Midplane = true
  Profile = -> Sketch193
  ReferenceAxis = -> Sketch193 [N_Axis]
  Suppressed = false
  Type = 1
FEATURE [PartDesign::Mirrored] Mirrored014
  BaseFeature = -> Pocket118
  MirrorPlane = -> YZ_Plane087
  Originals = -> [Pocket118]
  Suppressed = false
  TransformMode = 0
FEATURE [Part::FeaturePython] Placment025  # WARN: FeaturePython — macro-defined, semantics opaque (R4)
  AttacherType = Attacher::AttachEngine3D
  ExposePlacement = true
  MarkerShape = 1
  MarkerSize = 50
  NumElements = 1
  Placement = pos=(68.9742,55.7258,0) rot=(0,0,1;1.5708rad)
  Type = lattice2AttachablePlacement.AttachablePlacement
  isLattice = 1
FEATURE [Part::FeaturePython] Placment026  # WARN: FeaturePython — macro-defined, semantics opaque (R4)
  AttacherType = Attacher::AttachEngine3D
  ExposePlacement = true
  MarkerShape = 1
  MarkerSize = 5
  NumElements = 1
  Placement = pos=(56.173,140.207,0) rot=(0,0,1;1.5708rad)
  Type = lattice2AttachablePlacement.AttachablePlacement
  isLattice = 1
FEATURE [Part::FeaturePython] Placment027  # WARN: FeaturePython — macro-defined, semantics opaque (R4)
  AttacherType = Attacher::AttachEngine3D
  ExposePlacement = true
  MarkerShape = 1
  MarkerSize = 5
  NumElements = 1
  Placement = pos=(36,265,0) rot=(0,0,1;1.5708rad)
  Type = lattice2AttachablePlacement.AttachablePlacement
  isLattice = 1
FEATURE [Part::FeaturePython] Join011  # WARN: FeaturePython — macro-defined, semantics opaque (R4)
  ExposePlacement = false
  Interleave = false
  Links = -> [Placment025,Placment026,Placment027]
  MarkerShape = 1
  MarkerSize = 0
  NumElements = 3
  Type = lattice2JoinArrays.JoinArrays
  isLattice = 1
FEATURE [Part::FeaturePython] Mirror011  label="Mirror011 of Join011"  # WARN: FeaturePython — macro-defined, semantics opaque (R4)
  ExposePlacement = false
  FlipX = true
  FlipY = false
  FlipZ = false
  MarkerShape = 1
  MarkerSize = 0
  NumElements = 3
  Object = -> Join011
  ObjectTraversal = 0
  Type = lattice2Mirror.LatticeMirror
  isLattice = 1
FEATURE [Part::FeaturePython] Join012  # WARN: FeaturePython — macro-defined, semantics opaque (R4)
  ExposePlacement = false
  Interleave = false
  Links = -> [Mirror011,Join011]
  MarkerShape = 1
  MarkerSize = 0
  NumElements = 6
  Type = lattice2JoinArrays.JoinArrays
  isLattice = 1
FEATURE [Part::FeaturePython] PolarArray006  label="3_elem_polar_array"  # WARN: FeaturePython — macro-defined, semantics opaque (R4)
  Alignment = 0
  AttacherType = Attacher::AttachEngine3D
  CellStart = A1
  Count = 3
  DistributionLaw = 0
  EndInclusive = false
  ExposePlacement = false
  FlipX = false
  FlipZ = false
  GeneratorMode = 0
  MarkerShape = 1
  MarkerSize = 0
  NumElements = 3
  OrientMode = 2
  Radius = 100
  Reverse = false
  SpanEnd = 360
  SpanStart = 0
  Step = 120
  Type = lattice2PolarArray2.PolarArray
  UseArcRadius = false
  UseArcRange = 0
  VSGVersion = 1
  Values = 0.0 | 120.0 | 240.0
  ValuesSource = 2
  isLattice = 1
FEATURE [Part::FeaturePython] Populate039  label="Populate PolarArray006 with Join012"  # WARN: FeaturePython — macro-defined, semantics opaque (R4)
  Copying = 0
  ExposePlacement = false
  MarkerShape = 1
  MarkerSize = 0
  NumElements = 18
  Object = -> Join012
  OutputCompounding = 0
  PlacementsTo = -> PolarArray006
  Referencing = 1
  Type = lattice2PopulateCopies.LatticePopulateCopies
  isLattice = 1
FEATURE [Part::Cylinder] Cylinder003  label="hole_3.2mm_extrude"
  Angle = 360
  AttacherType = Attacher::AttachEngine3D
  FirstAngle = 0
  Height = 20
  Radius = 1.6
  SecondAngle = 0
FEATURE [Part::FeaturePython] Populate040  label="Populate Populate PolarArray006 with Join012 with hole_3.2mm_extrude"  # WARN: FeaturePython — macro-defined, semantics opaque (R4)
  Copying = 0
  ExposePlacement = false
  MarkerShape = 1
  MarkerSize = 0
  NumElements = 0
  Object = -> Cylinder003
  OutputCompounding = 1
  PlacementsTo = -> Populate039
  Referencing = 0
  Type = lattice2PopulateCopies.LatticePopulateCopies
  isLattice = 0
FEATURE [Part::FeaturePython] Populate041  label="Populate Populate PolarArray006 with Join012 with hole_5_mm_extrude"  # WARN: FeaturePython — macro-defined, semantics opaque (R4)
  Copying = 0
  ExposePlacement = false
  MarkerShape = 1
  MarkerSize = 0
  NumElements = 0
  Object = -> Extrude023
  OutputCompounding = 1
  PlacementsTo = -> Populate039
  Referencing = 0
  Type = lattice2PopulateCopies.LatticePopulateCopies
  isLattice = 0
FEATURE [Part::FeaturePython] Placment028  # WARN: FeaturePython — macro-defined, semantics opaque (R4)
  AttacherType = Attacher::AttachEngine3D
  ExposePlacement = true
  MapMode = 11
  MarkerShape = 1
  MarkerSize = 10
  NumElements = 1
  Placement = pos=(63.3907,55,0) rot=(0,0,1;1.5708rad)
  Type = lattice2AttachablePlacement.AttachablePlacement
  isLattice = 1
FEATURE [Part::FeaturePython] Placment029  # WARN: FeaturePython — macro-defined, semantics opaque (R4)
  AttacherType = Attacher::AttachEngine3D
  ExposePlacement = true
  MapMode = 11
  MarkerShape = 1
  MarkerSize = 10
  NumElements = 1
  Placement = pos=(43.3161,155,0) rot=(0,0,1;1.5708rad)
  Type = lattice2AttachablePlacement.AttachablePlacement
  isLattice = 1
FEATURE [Part::FeaturePython] Join013  # WARN: FeaturePython — macro-defined, semantics opaque (R4)
  ExposePlacement = false
  Interleave = false
  Links = -> [Placment028,Placment029]
  MarkerShape = 1
  MarkerSize = 0
  NumElements = 2
  Type = lattice2JoinArrays.JoinArrays
  isLattice = 1
FEATURE [Part::FeaturePython] Mirror012  label="Mirror012 of Join013"  # WARN: FeaturePython — macro-defined, semantics opaque (R4)
  ExposePlacement = false
  FlipX = true
  FlipY = false
  FlipZ = false
  MarkerShape = 1
  MarkerSize = 0
  NumElements = 2
  Object = -> Join013
  ObjectTraversal = 0
  Type = lattice2Mirror.LatticeMirror
  isLattice = 1
FEATURE [Part::FeaturePython] Join014  # WARN: FeaturePython — macro-defined, semantics opaque (R4)
  ExposePlacement = false
  Interleave = false
  Links = -> [Mirror012,Join013]
  MarkerShape = 1
  MarkerSize = 0
  NumElements = 4
  Type = lattice2JoinArrays.JoinArrays
  isLattice = 1
FEATURE [Part::FeaturePython] Populate042  label="Populate 3_elem_polar_array with Join014"  # WARN: FeaturePython — macro-defined, semantics opaque (R4)
  Copying = 0
  ExposePlacement = false
  MarkerShape = 1
  MarkerSize = 0
  NumElements = 12
  Object = -> Join014
  OutputCompounding = 0
  PlacementsTo = -> PolarArray006
  Referencing = 1
  Type = lattice2PopulateCopies.LatticePopulateCopies
  isLattice = 1
FEATURE [Part::FeaturePython] Populate043  label="Populate Populate 3_elem_polar_array with Join014 with hole_3.2_mm_extrude"  # WARN: FeaturePython — macro-defined, semantics opaque (R4)
  Copying = 0
  ExposePlacement = false
  MarkerShape = 1
  MarkerSize = 0
  NumElements = 0
  Object = -> Cylinder001
  OutputCompounding = 1
  PlacementsTo = -> Populate042
  Referencing = 0
  Type = lattice2PopulateCopies.LatticePopulateCopies
  isLattice = 0
FEATURE [Part::FeaturePython] Populate044  label="Populate Populate 3_elem_polar_array with Join014 with hole_5_mm_extrude"  # WARN: FeaturePython — macro-defined, semantics opaque (R4)
  Copying = 0
  ExposePlacement = false
  MarkerShape = 1
  MarkerSize = 0
  NumElements = 0
  Object = -> Extrude023
  OutputCompounding = 1
  PlacementsTo = -> Populate042
  Referencing = 0
  Type = lattice2PopulateCopies.LatticePopulateCopies
  isLattice = 0
FEATURE [Part::Compound] Compound070  label="basement_top_amplifier_cut1"
  Links = -> [Populate044]
FEATURE [PartDesign::Boolean] Boolean028
  BaseFeature = -> Pocket107
  Group = -> [Compound070]
  Suppressed = false
  Type = 1
  UsePlacement = false
FEATURE [PartDesign::SubShapeBinder] Binder134
  BindCopyOnChange = 0
  BindMode = 0
  ClaimChildren = false
  Context = -> Body009 [Binder134.]
  Fuse = false
  MakeFace = true
  OffsetFill = false
  OffsetIntersection = false
  OffsetJoinType = 0
  OffsetOpenResult = false
  PartialLoad = false
  Relative = true
  Support = -> [Body007[Pocket112.Sketch178.]]
  _Version = 2
FEATURE [App::Link] Link041  label="hub2108_bottom_fix"
  LinkedObject = -> <external hub2108.FCStd>#Sketch002
  expr: LinkedObject = <<hub2108>>#<<bottom_fix_holes>>._self
FEATURE [App::Link] Link042  label="hub2108_bottom_center"
  LinkedObject = -> <external hub2108.FCStd>#Sketch003
  expr: LinkedObject = <<hub2108>>#<<bottom_center_hole>>._self
FEATURE [Part::Extrusion] Extrude029  label="hub2108_bottom_fix_extrude"
  Base = -> Link041
  Dir = (0,0,1)
  DirMode = 2
  FaceMakerClass = Part::FaceMakerBullseye
  FaceMakerMode = 3
  LengthFwd = 20
  LengthRev = 0
  Solid = true
  Symmetric = false
FEATURE [Part::Extrusion] Extrude030  label="hub2108_bottom_center_extrude"
  Base = -> Link042
  Dir = (0,0,1)
  DirMode = 2
  FaceMakerClass = Part::FaceMakerBullseye
  FaceMakerMode = 3
  LengthFwd = 20
  LengthRev = 0
  Solid = true
  Symmetric = false
FEATURE [Sketcher::SketchObject] Sketch216
  ArcFitTolerance = 0
  AttachmentOffset = pos=(350,0,0) rot=(0,0,1;0rad)
  AttachmentSupport = -> [YZ_Plane010]
  FullyConstrained = true
  MakeInternals = false
  MapMode = 5
  Placement = pos=(0,350,0) rot=(0.57735,0.57735,0.57735;2.0944rad)
  sketch-geometry (3):
    g0: LineSegment StartX=0 StartY=15 StartZ=0 EndX=-15 EndY=0 EndZ=0
    g1: LineSegment StartX=-15 StartY=0 StartZ=0 EndX=0 EndY=0 EndZ=0
    g2: LineSegment StartX=0 StartY=15 StartZ=0 EndX=0 EndY=0 EndZ=0
  constraints (8):
    c: PointOnObject(g0,g-2)
    c: PointOnObject(g0,g-1)
    c: Coincident(g0,g1)
    c: Coincident(g1,g-1)
    c: Coincident(g2,g0)
    c: Coincident(g2,g1)
    c: Equal(g1,g2)
    c: DistanceY(g2,g2) = 15
FEATURE [PartDesign::SubtractivePipe] SubtractivePipe
  AuxilleryCurvelinear = true
  AuxillerySpineTangent = false
  BaseFeature = -> Pad001
  Binormal = (0,0,0)
  Mode = 0
  Profile = -> Sketch216
  Spine = -> Binder005 [Edge1,Edge2,Edge3,Edge4,Edge5,Edge6,Edge7,Edge8,Edge9,Edge10,Edge11,Edge12,Edge13,Edge14,Edge15,Edge16,Edge17,Edge18]
  SpineTangent = false
  Suppressed = false
  Transformation = 0
  Transition = 0
FEATURE [PartDesign::Pocket] Pocket062
  BaseFeature = -> SubtractivePipe
  Direction = (0,0,-1)
  Length = 5
  Length2 = 5
  Midplane = true
  Profile = -> Sketch113
  ReferenceAxis = -> Sketch113 [N_Axis]
  Suppressed = false
  Type = 1
FEATURE [Part::FeaturePython] PolarArray007  # WARN: FeaturePython — macro-defined, semantics opaque (R4)
  Alignment = 0
  AttacherType = Attacher::AttachEngine3D
  CellStart = A1
  Count = 3
  DistributionLaw = 0
  EndInclusive = false
  ExposePlacement = false
  FlipX = false
  FlipZ = false
  GeneratorMode = 0
  MarkerShape = 1
  MarkerSize = 0
  NumElements = 3
  OrientMode = 2
  Placement = pos=(0,0,0) rot=(0,0,1;1.5708rad)
  Radius = 370
  Reverse = false
  SpanEnd = 360
  SpanStart = 0
  Step = 120
  Type = lattice2PolarArray2.PolarArray
  UseArcRadius = false
  UseArcRange = 0
  VSGVersion = 1
  Values = 0.0 | 120.0 | 240.0
  ValuesSource = 2
  isLattice = 1
FEATURE [Part::Extrusion] Extrude031  label="hole_8mm_extrude"
  Base = -> Circle001
  Dir = (0,0,1)
  DirMode = 2
  FaceMakerClass = Part::FaceMakerBullseye
  FaceMakerMode = 3
  LengthFwd = 20
  LengthRev = 0
  Solid = true
  Symmetric = false
FEATURE [Part::FeaturePython] Populate045  label="Populate PolarArray007 with hole_8mm_extrude"  # WARN: FeaturePython — macro-defined, semantics opaque (R4)
  Copying = 0
  ExposePlacement = false
  MarkerShape = 1
  MarkerSize = 0
  NumElements = 0
  Object = -> Extrude031
  OutputCompounding = 1
  PlacementsTo = -> PolarArray007
  Referencing = 0
  Type = lattice2PopulateCopies.LatticePopulateCopies
  isLattice = 0
FEATURE [Part::FeaturePython] Populate046  label="Populate Mirror009 of Join007 with hole_3.4mm_extrude"  # WARN: FeaturePython — macro-defined, semantics opaque (R4)
  Copying = 0
  ExposePlacement = false
  MarkerShape = 1
  MarkerSize = 0
  NumElements = 0
  Object = -> Extrude019
  OutputCompounding = 1
  PlacementsTo = -> Mirror009
  Referencing = 0
  Type = lattice2PopulateCopies.LatticePopulateCopies
  isLattice = 0
FEATURE [Part::Compound] Compound073
  Links = -> [Populate046]
  Placement = pos=(11.5,6.63953,1394) rot=(0,0,-1;1.0472rad)
  expr: .Placement.Base.x = Sketch.Constraints.connection_offset * cos(30) - 3 mm
  expr: .Placement.Base.y = Sketch.Constraints.connection_offset * sin(30) - 1.5 mm / sin(60)
  expr: .Placement.Base.z = <<Properties>>.total_height - 34 mm
FEATURE [Part::Mirroring] Part__Mirroring032  label="Compound073 (Mirror #32)"
  Base = (0,0,0)
  Normal = (1,0,0)
  Source = -> Compound073
FEATURE [Part::Compound] Compound074
  Links = -> [Part__Mirroring032,Compound073]
FEATURE [Part::Compound] Compound077  label="star_amplifier_cut1"
  Links = -> [Extrude003]
FEATURE [PartDesign::Boolean] Boolean004
  BaseFeature = -> Pocket026
  Group = -> [Compound077]
  Suppressed = false
  Type = 1
  UsePlacement = false
  expr: Group = <<star_amplifier_cut1>>._self
FEATURE [PartDesign::FeatureAdditivePython] PDW_Common_Add002  # link proxy (typed FeaturePython)
  BaseFeature = -> Boolean004
  Body = Body018
  ClaimChildren = false
  EditPlacementAdjustments = false
  Enabled = 1
  LinkedObject = -> Boolean004
  MeshTolerance = 0.1
  PatternBase = -> Pocket026
  PatternBaseOffset = 0
  PatternBaseScale = 1
  PatternBaseScaleXYZ = (1,1,1)
  PatternOffsetCut = false
  PatternOffsetIntersection = false
  PatternOffsetJoin = 0
  PatternOffsetMode = 0
  PatternOffsetSelfIntersection = false
  PatternOperation = 3
  PatternOperationDefault = Common
  PatternScaleCut = false
  PatternShapeOffset = 0
  PatternShapeScale = 1
  PatternShapeScaleXYZ = (1,1,1)
  PatternTool = -> Boolean004
  PatternToolOffset = 0
  PatternToolScale = 1
  PatternToolScaleXYZ = (1,1,1)
  RefineMesh = true
  ShapeManagement = 0
  ShowMeshProps = false
  ShowOffsetProps = false
  ShowScaleProps = false
  ShowWarnings = true
  Suppressed = false
  TipBase = -> Pocket026
  TipBaseOffset = 0
  TipBaseScale = 1
  TipBaseScaleXYZ = (1,1,1)
  TipOffsetCut = false
  TipOffsetIntersection = false
  TipOffsetJoin = 0
  TipOffsetMode = 0
  TipOffsetSelfIntersection = false
  TipOperation = 2
  TipOperationDefault = Common
  TipScaleCut = false
  TipShapeOffset = 0
  TipShapeScale = 1
  TipShapeScaleXYZ = (1,1,1)
  TipTool = -> Boolean004
  TipToolOffset = 0
  TipToolScale = 1
  TipToolScaleXYZ = (1,1,1)
  Type = Additive
  UsePatternBaseAddSubShape = false
  UsePatternToolAddSubShape = true
  UseTipBaseAddSubShape = false
  UseTipToolAddSubShape = true
  Version = 0.2023.08.13
FEATURE [PartDesign::PolarPattern] PolarPattern008
  Angle = 360
  Axis = -> Z_Axis025
  BaseFeature = -> PDW_Common_Add002
  Mode = 0
  Occurrences = 3
  Offset = 120
  Originals = -> [PDW_Common_Add002]
  Refine = true
  Suppressed = false
  TransformMode = 0
FEATURE [PartDesign::Body] Body018  label="star_material_0.30ansi"
  AllowCompound = false
  Group = -> [Sketch032,BaseBend010,Sketch033,Pocket018,Mirrored001,Sketch034,Pocket019,Sketch036,Pocket021,Sketch045,Pocket026,Boolean004,PDW_Common_Add002,PolarPattern008]
  Origin = -> Origin025
  Placement = pos=(0,0,1428) rot=(0,0,1;0rad)
  Tip = -> PolarPattern008
  expr: .Placement.Base.z = <<Properties>>.total_height
FEATURE [Part::Compound] Compound078  label="top_connector_cut1"
  Links = -> [Extrude006]
FEATURE [PartDesign::Boolean] Boolean007
  BaseFeature = -> Hole004
  Group = -> [Compound078]
  Suppressed = false
  Type = 1
  UsePlacement = false
  expr: Group = <<top_connector_cut1>>._self
FEATURE [PartDesign::Pocket] Pocket027
  BaseFeature = -> Boolean007
  Direction = (-1,0,0)
  Length = 5
  Length2 = 5
  Midplane = true
  Profile = -> Sketch048
  ReferenceAxis = -> Sketch048 [N_Axis]
  Suppressed = false
  Type = 1
FEATURE [PartDesign::Body] Body017  label="top_connector_material_0.30ansi"
  AllowCompound = false
  Group = -> [Sketch029,BaseBend009,Binder029,Binder030,Hole004,Boolean007,Sketch048,Pocket027]
  Origin = -> Origin024
  Tip = -> Pocket027
FEATURE [Sketcher::SketchObject] Sketch217
  ArcFitTolerance = 0
  AttachmentSupport = -> [XY_Plane023]
  ExternalGeometry = -> [Sketch024,Binder018]
  FullyConstrained = true
  MakeInternals = false
  MapMode = 5
  sketch-geometry (6):
    g0: LineSegment StartX=41.7 StartY=289.736 StartZ=0 EndX=14.25 EndY=348.472 EndZ=0
    g1: LineSegment StartX=0 StartY=348.472 StartZ=0 EndX=14.25 EndY=348.472 EndZ=0
    g2: LineSegment [constr] StartX=14.25 StartY=351.872 StartZ=0 EndX=14.25 EndY=348.472 EndZ=0
    g3: LineSegment [constr] StartX=14.25 StartY=348.472 StartZ=0 EndX=17.3302 EndY=349.911 EndZ=0
    g4: LineSegment StartX=0 StartY=348.472 StartZ=0 EndX=0 EndY=289.736 EndZ=0
    g5: LineSegment StartX=0 StartY=289.736 StartZ=0 EndX=41.7 EndY=289.736 EndZ=0
  constraints (17):
    c: Coincident(g0,g-3)
    c: PointOnObject(g1,g-2)
    c: Coincident(g1,g0)
    c: Horizontal(g1)
    c: Coincident(g2,g0)
    c: Coincident(g2,g3)
    c: PointOnObject(g3,g-4)
    c: Perpendicular(g0,g3)
    c: Perpendicular(g1,g2)
    c: Equal(g3,g2)
    c: DistanceY(g2,g2) = 3.4
    c: Horizontal(g2,g-4)
    c: Coincident(g4,g1)
    c: PointOnObject(g4,g-3)
    c: Vertical(g4)
    c: Coincident(g5,g4)
    c: Coincident(g5,g0)
FEATURE [PartDesign::Pad] Pad033
  BaseFeature = -> BaseBend008
  Direction = (0,0,1)
  Length = 0.3
  Length2 = 10
  Profile = -> Sketch217
  ReferenceAxis = -> Sketch217 [N_Axis]
  Suppressed = false
  Type = 0
FEATURE [PartDesign::Mirrored] Mirrored016
  BaseFeature = -> Pad033
  MirrorPlane = -> Sketch217 [V_Axis]
  Originals = -> [Pad033]
  Suppressed = false
  TransformMode = 0
FEATURE [PartDesign::Hole] Hole002
  BaseFeature = -> Mirrored016
  CustomThreadClearance = 0
  Depth = 25
  DepthType = 0
  Diameter = 3.4
  DrillForDepth = false
  DrillPoint = 1
  DrillPointAngle = 118
  HoleCutCountersinkAngle = 90
  HoleCutCustomValues = false
  HoleCutDepth = 0
  HoleCutDiameter = 6.1
  HoleCutType = 0
  ModelThread = false
  Profile = -> Binder019
  Refine = true
  Reversed = true
  Suppressed = false
  Tapered = false
  TaperedAngle = 90
  ThreadClass = 0
  ThreadDepth = 25
  ThreadDepthType = 0
  ThreadDirection = 0
  ThreadFit = 0
  ThreadSize = 0
  ThreadType = 0
  Threaded = false
  UseCustomThreadClearance = false
  expr: Diameter = <<Properties>>.rivet_d
FEATURE [PartDesign::Body] Body016  label="cap_inner2_material_0.30ansi"
  AllowCompound = false
  Group = -> [Binder018,Binder019,Sketch024,BaseBend008,Sketch217,Pad033,Mirrored016,Hole002]
  Origin = -> Origin023
  Tip = -> Hole002
FEATURE [Sketcher::SketchObject] Sketch218
  ArcFitTolerance = 0
  AttachmentOffset = pos=(0,0,18) rot=(0,0,1;0rad)
  AttachmentSupport = -> [XY_Plane011]
  FullyConstrained = false
  MakeInternals = false
  MapMode = 5
  Placement = pos=(0,0,18) rot=(0,0,1;0rad)
  sketch-geometry (4):
    g0: LineSegment StartX=93.4507 StartY=-44.023 StartZ=0 EndX=107.489 EndY=-44.023 EndZ=0
    g1: LineSegment StartX=107.489 StartY=-44.023 StartZ=0 EndX=107.489 EndY=-29.1068 EndZ=0
    g2: LineSegment StartX=107.489 StartY=-29.1068 StartZ=0 EndX=93.4507 EndY=-29.1068 EndZ=0
    g3: LineSegment StartX=93.4507 StartY=-29.1068 StartZ=0 EndX=93.4507 EndY=-44.023 EndZ=0
  constraints (8):
    c: Coincident(g0,g1)
    c: Coincident(g1,g2)
    c: Coincident(g2,g3)
    c: Coincident(g3,g0)
    c: Horizontal(g0)
    c: Horizontal(g2)
    c: Vertical(g1)
    c: Vertical(g3)
FEATURE [Sketcher::SketchObject] Sketch219
  ArcFitTolerance = 0
  FullyConstrained = false
  MakeInternals = false
  MapMode = 5
  Placement = pos=(0,8e-15,-6.7e-14) rot=(1,0,0;3.25479rad)
  sketch-geometry (6):
    g0: LineSegment StartX=297.803 StartY=-177.345 StartZ=0 EndX=303.917 EndY=-182.504 EndZ=0
    g1: LineSegment StartX=303.917 StartY=-182.504 StartZ=0 EndX=285.803 EndY=-203.969 EndZ=0
    g2: LineSegment StartX=285.803 StartY=-203.969 StartZ=0 EndX=276.608 EndY=-196.209 EndZ=0
    g3: LineSegment StartX=279.192 StartY=-196.205 StartZ=0 EndX=297.807 EndY=-180.398 EndZ=0
    g4: ArcOfCircle CenterX=296.513 CenterY=-178.873 CenterZ=0 NormalX=0 NormalY=0 NormalZ=1 AngleXU=0 Radius=2 StartAngle=5.41641 EndAngle=7.15307
    g5: ArcOfCircle CenterX=277.898 CenterY=-194.681 CenterZ=0 NormalX=0 NormalY=0 NormalZ=1 AngleXU=0 Radius=2 StartAngle=4.01147 EndAngle=5.41641
  constraints (13):
    c: Coincident(g0,g1)
    c: Coincident(g1,g2)
    c: Perpendicular(g1,g2)
    c: Perpendicular(g0,g1)
    c: Tangent(g4,g0) = 1.5708
    c: Tangent(g5,g2) = 1.5708
    c: Tangent(g5,g3) = -1.5708
    c: Tangent(g4,g3) = -1.5708
    c: Equal(g4,g5)
    c: Radius(g4) = 2
    c: Distance(g0) = 8
    c: Distance(g2) = 12.0319
    c: Distance(g3,g1) = 10.0593
FEATURE [Sketcher::SketchObject] Sketch220  label="sleeve_outer_sketch"
  ArcFitTolerance = 0
  AttachmentSupport = -> [XZ_Plane100]
  FullyConstrained = true
  MakeInternals = false
  MapMode = 5
  Placement = pos=(0,0,0) rot=(1,0,0;1.5708rad)
  expr: Constraints[13] = <<sleeve_inner_sketch>>.Constraints.outer_r + 0.25 mm
  sketch-geometry (6):
    g0: LineSegment StartX=13.25 StartY=67 StartZ=0 EndX=13.25 EndY=0 EndZ=0
    g1: LineSegment StartX=13.25 StartY=0 StartZ=0 EndX=35.25 EndY=0 EndZ=0
    g2: LineSegment StartX=35.25 StartY=0 StartZ=0 EndX=35.25 EndY=7 EndZ=0
    g3: LineSegment StartX=35.25 StartY=7 StartZ=0 EndX=20.25 EndY=7 EndZ=0
    g4: LineSegment StartX=20.25 StartY=7 StartZ=0 EndX=20.25 EndY=67 EndZ=0
    g5: LineSegment StartX=20.25 StartY=67 StartZ=0 EndX=13.25 EndY=67 EndZ=0
  constraints (20):
    c: PointOnObject(g0,g-1)
    c: Vertical(g0)
    c: Coincident(g0,g1)
    c: PointOnObject(g1,g-1)
    c: Coincident(g1,g2)
    c: Vertical(g2)
    c: Coincident(g2,g3)
    c: Horizontal(g3)
    c: Coincident(g3,g4)
    c: Vertical(g4)
    c: Coincident(g4,g5)
    c: Coincident(g5,g0)
    c: Horizontal(g5)
    c: DistanceX(g0) = 13.25
    c: DistanceX(g5,g5) = 7
    c: DistanceX(g3,g3) = 15
    c: DistanceY(g2,g2) = 7  'flange_height'
    c: DistanceY(g0,g0) = 67
    c: DistanceX(g3) = 20.25  'max_r'
    c: DistanceX(g1) = 35.25  'flange_max_r'
FEATURE [Sketcher::SketchObject] Sketch221  label="sleeve_inner_sketch"
  ArcFitTolerance = 0
  AttachmentSupport = -> [XZ_Plane101]
  FullyConstrained = true
  MakeInternals = false
  MapMode = 5
  Placement = pos=(0,0,0) rot=(1,0,0;1.5708rad)
  sketch-geometry (6):
    g0: LineSegment StartX=5 StartY=79 StartZ=0 EndX=5 EndY=0 EndZ=0
    g1: LineSegment StartX=5 StartY=0 StartZ=0 EndX=33 EndY=0 EndZ=0
    g2: LineSegment StartX=33 StartY=0 StartZ=0 EndX=33 EndY=8 EndZ=0
    g3: LineSegment StartX=33 StartY=8 StartZ=0 EndX=13 EndY=8 EndZ=0
    g4: LineSegment StartX=13 StartY=8 StartZ=0 EndX=13 EndY=79 EndZ=0
    g5: LineSegment StartX=13 StartY=79 StartZ=0 EndX=5 EndY=79 EndZ=0
  constraints (19):
    c: PointOnObject(g0,g-1)
    c: Vertical(g0)
    c: Coincident(g0,g1)
    c: PointOnObject(g1,g-1)
    c: Coincident(g1,g2)
    c: Vertical(g2)
    c: Coincident(g2,g3)
    c: Horizontal(g3)
    c: Coincident(g3,g4)
    c: Vertical(g4)
    c: Coincident(g4,g5)
    c: Coincident(g5,g0)
    c: Horizontal(g5)
    c: DistanceX(g0) = 5  'inner_r'
    c: DistanceX(g0,g3) = 8
    c: DistanceY(g2,g2) = 8
    c: DistanceX(g3,g3) = 20
    c: DistanceX(g3) = 13  'outer_r'
    c: DistanceY(g4,g4) = 71
FEATURE [PartDesign::Revolution] Revolution
  Angle = 360
  Angle2 = 60
  Axis = (0,2e-16,1)
  Base = (0,0,0)
  Placement = pos=(0,0,0) rot=(1,0,0;1.5708rad)
  Profile = -> Sketch221
  ReferenceAxis = -> Sketch221 [V_Axis]
  Reversed = true
  Suppressed = false
  Type = 0
FEATURE [PartDesign::Revolution] Revolution001
  Angle = 360
  Angle2 = 60
  Axis = (0,2e-16,1)
  Base = (0,0,0)
  Placement = pos=(0,0,0) rot=(1,0,0;1.5708rad)
  Profile = -> Sketch220
  ReferenceAxis = -> Sketch220 [V_Axis]
  Reversed = true
  Suppressed = false
  Type = 0
FEATURE [App::Link] Link043  label="top_amplifier_cornrer_material_0.50ansi001"
  LinkedObject = -> Body113
FEATURE [Part::Cylinder] Cylinder004  label="Cylinder"
  Angle = 360
  AttacherType = Attacher::AttachEngine3D
  FirstAngle = 0
  Height = 50
  Placement = pos=(-21.5035,3.75481,0) rot=(0,0,-1;0.523599rad)
  Radius = 2.05
  SecondAngle = 0
  expr: Placement = placement(vector(0; 0; 0); rotation(-30; 0; -0)) * placement(vector(-20.5; -<<Properties>>.inner_width / 2 + 4 mm; 0); rotation(0; 0; 0))
FEATURE [Part::Compound] Compound072  label="top_amplifier_cornrer_cut1"
  Links = -> [Populate031,Cylinder004]
FEATURE [PartDesign::Boolean] Boolean017
  BaseFeature = -> Mirrored014
  Group = -> [Compound072]
  Refine = true
  Suppressed = false
  Type = 1
  UsePlacement = false
FEATURE [PartDesign::Body] Body113  label="top_amplifier_cornrer_material_0.50ansi"
  AllowCompound = false
  Group = -> [Sketch191,BaseBend046,Sketch193,Bend029,Fillet014,Pocket118,Mirrored014,Boolean017]
  Origin = -> Origin087
  Tip = -> Boolean017
FEATURE [Part::FeaturePython] Placment030  label="top_amplifier_placement"  # WARN: FeaturePython — macro-defined, semantics opaque (R4)
  AttacherType = Attacher::AttachEngine3D
  ExposePlacement = true
  MarkerShape = 1
  MarkerSize = 10
  NumElements = 1
  Placement = pos=(11.5,6.63953,1394) rot=(0,0,-1;1.0472rad)
  Type = lattice2AttachablePlacement.AttachablePlacement
  isLattice = 1
  expr: .Placement.Base.x = <<Properties>>.inner_width / 2
  expr: .Placement.Base.y = Sketch.Constraints.connection_offset * sin(30) - 1.5 mm / sin(60)
  expr: .Placement.Base.z = <<Properties>>.total_height - BaseBend046.length - 4 mm
FEATURE [App::DocumentObjectGroup] Group009  label="placements"
  Group = -> [Placment,Placment001,Placment002,Placment003,Placment004,Placment005,Placment018,Placment030]
FEATURE [Part::FeaturePython] Placment031  # WARN: FeaturePython — macro-defined, semantics opaque (R4)
  AttacherType = Attacher::AttachEngine3D
  AttachmentOffset = pos=(0,0,-1394) rot=(0,0,1;0rad)
  AttachmentSupport = -> [Placment030]
  ExposePlacement = true
  MapMode = 2
  MarkerShape = 1
  MarkerSize = 10
  NumElements = 1
  Placement = pos=(11.5,6.63953,0) rot=(0,0,-1;1.0472rad)
  Type = lattice2AttachablePlacement.AttachablePlacement
  isLattice = 1
  expr: .AttachmentOffset.Base.z = -<<top_amplifier_placement>>.Placement.Base.z
FEATURE [Part::FeaturePython] Populate047  label="Populate Placment031 with Cylinder"  # WARN: FeaturePython — macro-defined, semantics opaque (R4)
  Copying = 0
  ExposePlacement = false
  MarkerShape = 1
  MarkerSize = 0
  NumElements = 0
  Object = -> Cylinder004
  OutputCompounding = 2
  PlacementsTo = -> Placment031
  Referencing = 0
  Type = lattice2PopulateCopies.LatticePopulateCopies
  isLattice = 0
FEATURE [Part::FeaturePython] Array012  # Draft array (typed FeaturePython)
  Angle = 360
  ArrayType = 1
  Axis = (0,0,1)
  Base = -> Populate047
  Center = (0,0,0)
  Count = 3
  Fuse = true
  IntervalAxis = (0,0,0)
  IntervalX = (50,0,0)
  IntervalY = (0,50,0)
  IntervalZ = (0,0,50)
  NumberCircles = 3
  NumberPolar = 3
  NumberX = 2
  NumberY = 2
  NumberZ = 1
  RadialDistance = 50
  Symmetry = 1
  TangentialDistance = 25
FEATURE [Part::Compound] Compound079  label="sleeve_outer_cut1"
  Links = -> [Array012]
FEATURE [PartDesign::Boolean] Boolean030
  BaseFeature = -> Revolution001
  Group = -> [Compound079]
  Suppressed = false
  Type = 1
  UsePlacement = false
FEATURE [Sketcher::SketchObject] Sketch222
  ArcFitTolerance = 0
  FullyConstrained = true
  MakeInternals = false
  sketch-geometry (10):
    g0: LineSegment [constr] StartX=22.5167 StartY=-13 StartZ=0 EndX=-22.5167 EndY=-13 EndZ=0
    g1: LineSegment [constr] StartX=-22.5167 StartY=-13 StartZ=0 EndX=0 EndY=26 EndZ=0
    g2: LineSegment [constr] StartX=0 StartY=26 StartZ=0 EndX=22.5167 EndY=-13 EndZ=0
    g3: GeomPoint [constr] X=0 Y=0 Z=0
    g4: Circle CenterX=0 CenterY=26 CenterZ=0 NormalX=0 NormalY=0 NormalZ=1 AngleXU=0 Radius=2
    g5: Circle CenterX=-22.5167 CenterY=-13 CenterZ=0 NormalX=0 NormalY=0 NormalZ=1 AngleXU=0 Radius=2
    g6: Circle CenterX=22.5167 CenterY=-13 CenterZ=0 NormalX=0 NormalY=0 NormalZ=1 AngleXU=0 Radius=2
    g7: LineSegment [constr] StartX=-22.5167 StartY=-13 StartZ=0 EndX=0 EndY=0 EndZ=0
    g8: LineSegment [constr] StartX=0 StartY=0 StartZ=0 EndX=0 EndY=26 EndZ=0
    g9: LineSegment [constr] StartX=0 StartY=0 StartZ=0 EndX=22.5167 EndY=-13 EndZ=0
  constraints (22):
    c: Coincident(g0,g1)
    c: Coincident(g2,g0)
    c: Coincident(g3,g-1)
    c: Coincident(g4,g1)
    c: Coincident(g5,g0)
    c: Coincident(g6,g0)
    c: Distance(g3,g4) = 26
    c: Equal(g4,g5)
    c: Equal(g4,g6)
    c: Diameter(g4) = 4
    c: Coincident(g2,g4)
    c: Equal(g1,g2)
    c: Equal(g2,g0)
    c: Coincident(g7,g5)
    c: Coincident(g7,g3)
    c: Coincident(g7,g8)
    c: Coincident(g8,g4)
    c: Coincident(g9,g3)
    c: Coincident(g9,g6)
    c: PointOnObject(g4,g-2)
    c: Equal(g9,g8)
    c: Equal(g9,g7)
FEATURE [Part::Extrusion] Extrude032
  Base = -> Sketch222
  Dir = (0,0,1)
  DirMode = 2
  FaceMakerClass = Part::FaceMakerBullseye
  FaceMakerMode = 3
  LengthFwd = 10
  LengthRev = 0
  Placement = pos=(0,0,0) rot=(0,0,1;3.14159rad)
  Solid = true
  Symmetric = false
FEATURE [TechDraw::DrawSVGTemplate] Template
  Height = 210
  Orientation = 1
  Template = <path>
  Width = 297
FEATURE [App::Link] Link044  label="sleeve_outer001"
  LinkedObject = -> Body123
FEATURE [App::Link] Link045  label="sleeve_inner001"
  LinkedObject = -> Body124
FEATURE [App::DocumentObjectGroup] Group010  label="links"
  Group = -> [Link011,Link010,Link015,Link014,Link013,Link012,Link019,Link018,Link017,Link020,Link016,Link025,Link022,Link026,Link021,Link023,Link029,Link027,Link028,Link032,Link031,Link030,Link034,Link033,Link036,Link035,Link037,Link043,Link044,Link045]
FEATURE [Sketcher::SketchObject] Sketch223
  ArcFitTolerance = 0
  AttachmentOffset = pos=(0,0,0) rot=(0,1,0;0.523599rad)
  AttachmentSupport = -> [XZ_Plane102]
  FullyConstrained = true
  MakeInternals = false
  MapMode = 5
  Placement = pos=(0,0,0) rot=(0.935113,0.250563,0.250563;1.63783rad)
  expr: Constraints[15] = <<sleeve_outer_sketch>>.Constraints.flange_max_r + 1 mm
  expr: Constraints[16] = <<sleeve_outer_sketch>>.Constraints.max_r + 1 mm
  sketch-geometry (8):
    g0: ArcOfCircle CenterX=39.25 CenterY=3 CenterZ=0 NormalX=0 NormalY=0 NormalZ=1 AngleXU=0 Radius=3 StartAngle=3.14159 EndAngle=4.71239
    g1: LineSegment StartX=36.25 StartY=3 StartZ=0 EndX=36.25 EndY=48.4 EndZ=0
    g2: LineSegment StartX=36.25 StartY=48.4 StartZ=0 EndX=21.25 EndY=48.4 EndZ=0
    g3: LineSegment StartX=21.25 StartY=48.4 StartZ=0 EndX=21.25 EndY=40.4 EndZ=0
    g4: LineSegment StartX=0 StartY=0 StartZ=0 EndX=39.25 EndY=0 EndZ=0
    g5: LineSegment StartX=21.25 StartY=40.4 StartZ=0 EndX=0 EndY=40.4 EndZ=0
    g6: LineSegment StartX=0 StartY=40.4 StartZ=0 EndX=0 EndY=0 EndZ=0
    g7: GeomPoint [constr] X=21.25 Y=48.4 Z=0
  constraints (21):
    c: PointOnObject(g0,g-1)
    c: Vertical(g1)
    c: Coincident(g2,g1)
    c: Horizontal(g2)
    c: Vertical(g3)
    c: Tangent(g1,g0) = 1.5708
    c: Coincident(g4,g-1)
    c: Tangent(g4,g0) = -1.5708
    c: Radius(g0) = 3
    c: Coincident(g5,g3)
    c: PointOnObject(g5,g-2)
    c: Horizontal(g5)
    c: Coincident(g6,g5)
    c: Coincident(g6,g4)
    c: DistanceY(g6,g6) = 40.4
    c: DistanceX(g1) = 36.25
    c: DistanceX(g7) = 21.25
    c: DistanceY(g7,g3) = -8
    c: PointOnObject(g7,g2)
    c: PointOnObject(g7,g3)
    c: Coincident(g2,g3)
FEATURE [Sketcher::SketchObject] Sketch224
  ArcFitTolerance = 0
  AttachmentSupport = -> [XY_Plane102]
  FullyConstrained = true
  MakeInternals = false
  MapMode = 5
  expr: Constraints[10] = <<sleeve_outer_sketch>>.Constraints.max_r + 1 mm
  sketch-geometry (7):
    g0: LineSegment StartX=1.3e-15 StartY=21.4809 StartZ=0 EndX=0 EndY=0.46188 EndZ=0
    g1: LineSegment StartX=0 StartY=0.46188 StartZ=0 EndX=18.203 EndY=10.9714 EndZ=0
    g2: LineSegment [constr] StartX=0 StartY=0 StartZ=0 EndX=-0.2 EndY=0.34641 EndZ=0
    g3: LineSegment [constr] StartX=-0.2 StartY=0.34641 StartZ=0 EndX=0 EndY=0.46188 EndZ=0
    g4: ArcOfCircle CenterX=0 CenterY=0.46188 CenterZ=0 NormalX=0 NormalY=0 NormalZ=1 AngleXU=0 Radius=21.0191 StartAngle=0.648827 EndAngle=1.5708
    g5: ArcOfCircle CenterX=19.1382 CenterY=14.9754 CenterZ=0 NormalX=0 NormalY=0 NormalZ=1 AngleXU=0 Radius=3 StartAngle=3.79042 EndAngle=5.23599
    g6: LineSegment StartX=18.203 StartY=10.9714 StartZ=0 EndX=20.6382 EndY=12.3774 EndZ=0
  constraints (19):
    c: PointOnObject(g0,g-2)
    c: PointOnObject(g0,g-2)
    c: Coincident(g0,g1)
    c: Angle(g1) = 0.523599
    c: Distance(g-1,g1) = 0.4
    c: Coincident(g4,g0)
    c: Coincident(g2,g3)
    c: Coincident(g3,g0)
    c: Perpendicular(g3,g2)
    c: Parallel(g3,g1)
    c: Distance(g2,g1) = 21.25
    c: Coincident(g6,g1)
    c: Parallel(g6,g1)
    c: Tangent(g5,g4) = 1.5708
    c: PointOnObject(g1,g4)
    c: Coincident(g-1,g2)
    c: Coincident(g4,g0)
    c: Tangent(g6,g5) = -1.5708
    c: Radius(g5) = 3
FEATURE [PartDesign::Pad] Pad034
  Direction = (0.5,-0.866025,1e-16)
  Length = 0.4
  Length2 = 10
  Placement = pos=(0,0,0) rot=(1,0,0;1.5708rad)
  Profile = -> Sketch223
  ReferenceAxis = -> Sketch223 [N_Axis]
  Reversed = true
  Suppressed = false
  Type = 0
FEATURE [PartDesign::Pad] Pad035
  BaseFeature = -> Pad034
  Direction = (0,0,1)
  Length = 50
  Length2 = 10
  Placement = pos=(0,0,0) rot=(1,0,0;1.5708rad)
  Profile = -> Sketch224
  ReferenceAxis = -> Sketch224 [N_Axis]
  Suppressed = false
  Type = 0
FEATURE [PartDesign::Mirrored] Mirrored018
  BaseFeature = -> Pad035
  MirrorPlane = -> YZ_Plane102
  Originals = -> [Pad034,Pad035]
  Placement = pos=(0,0,0) rot=(1,0,0;1.5708rad)
  Suppressed = false
  TransformMode = 0
FEATURE [PartDesign::Body] Body125  label="Body"
  AllowCompound = false
  Group = -> [Sketch223,Sketch224,Pad034,Pad035,Mirrored018]
  Origin = -> Origin102
  Tip = -> Mirrored018
FEATURE [Part::Compound] Compound080
  Links = -> [Body125]
FEATURE [PartDesign::Boolean] Boolean032
  BaseFeature = -> Pocket005
  Group = -> [Compound080]
  Suppressed = false
  Type = 1
  UsePlacement = false
FEATURE [PartDesign::Body] Body002  label="cap_outer_material_0.30ansi"
  AllowCompound = false
  Group = -> [Binder012,Binder013,BaseBend007,Bend001,Pocket002,Binder014,Sketch020,Pocket125,Pocket003,Binder015,Mirrored,Sketch022,WireFilter002,Pocket005,Binder132,Boolean032]
  Origin = -> Origin005
  Tip = -> Boolean032
FEATURE [Part::FeaturePython] Placment032  # WARN: FeaturePython — macro-defined, semantics opaque (R4)
  AttacherType = Attacher::AttachEngine3D
  ExposePlacement = true
  MarkerShape = 1
  MarkerSize = 10
  NumElements = 1
  Placement = pos=(0,0,6) rot=(0,1,0;3.14159rad)
  Type = lattice2AttachablePlacement.AttachablePlacement
  isLattice = 1
FEATURE [Part::FeaturePython] Populate048  label="Populate Placment032 with Populate Placment031 with Cylinder"  # WARN: FeaturePython — macro-defined, semantics opaque (R4)
  Copying = 0
  ExposePlacement = false
  MarkerShape = 1
  MarkerSize = 0
  NumElements = 0
  Object = -> Populate047
  OutputCompounding = 2
  PlacementsTo = -> Placment032
  Referencing = 0
  Type = lattice2PopulateCopies.LatticePopulateCopies
  isLattice = 0
FEATURE [Part::Cylinder] Cylinder005
  Angle = 360
  AttacherType = Attacher::AttachEngine3D
  FirstAngle = 0
  Height = 10
  Radius = 13.5
  SecondAngle = 0
FEATURE [Part::Compound] Compound082
  Links = -> [Populate048,Cylinder005]
FEATURE [PartDesign::Boolean] Boolean034
  BaseFeature = -> PDW_Sub
  Group = -> [Compound082]
  Suppressed = false
  Type = 1
  UsePlacement = false
FEATURE [Part::Cylinder] Cylinder006
  Angle = 360
  AttacherType = Attacher::AttachEngine3D
  FirstAngle = 0
  Height = 10
  Radius = 7.5
  SecondAngle = 0
FEATURE [Part::Compound] Compound081
  Links = -> [Populate047,Cylinder006]
FEATURE [PartDesign::Boolean] Boolean033
  BaseFeature = -> Hole003
  Group = -> [Compound081]
  Suppressed = false
  Type = 1
  UsePlacement = false
FEATURE [PartDesign::FeatureSubtractivePython] PDW_Common_Sub  # link proxy (typed FeaturePython)
  BaseFeature = -> Boolean033
  Body = Body004
  ClaimChildren = true
  EditPlacementAdjustments = false
  Enabled = 1
  LinkedObject = -> Connect
  MeshTolerance = 0.1
  PatternBaseOffset = 0
  PatternBaseScale = 1
  PatternBaseScaleXYZ = (1,1,1)
  PatternOffsetCut = false
  PatternOffsetIntersection = false
  PatternOffsetJoin = 0
  PatternOffsetMode = 0
  PatternOffsetSelfIntersection = false
  PatternOperation = 3
  PatternOperationDefault = Common
  PatternScaleCut = false
  PatternShapeOffset = 0
  PatternShapeScale = 1
  PatternShapeScaleXYZ = (1,1,1)
  PatternTool = -> Compound048
  PatternToolOffset = 0
  PatternToolScale = 1
  PatternToolScaleXYZ = (1,1,1)
  Refine = true
  RefineMesh = true
  ShapeManagement = 1
  ShowMeshProps = false
  ShowOffsetProps = false
  ShowScaleProps = false
  ShowWarnings = true
  Suppressed = false
  TipBase = -> Boolean033
  TipBaseOffset = 0
  TipBaseScale = 1
  TipBaseScaleXYZ = (1,1,1)
  TipOffsetCut = false
  TipOffsetIntersection = false
  TipOffsetJoin = 0
  TipOffsetMode = 0
  TipOffsetSelfIntersection = false
  TipOperation = 1
  TipOperationDefault = Common
  TipScaleCut = false
  TipShapeOffset = 0
  TipShapeScale = 1
  TipShapeScaleXYZ = (1,1,1)
  TipTool = -> Connect
  TipToolOffset = 0
  TipToolScale = 1
  TipToolScaleXYZ = (1,1,1)
  Type = Subtractive
  UsePatternBaseAddSubShape = false
  UsePatternToolAddSubShape = false
  UseTipBaseAddSubShape = true
  UseTipToolAddSubShape = true
  Version = 0.2023.08.13
FEATURE [Sketcher::SketchObject] Sketch225  label="UV_driver_holder_base_Sketch"
  ArcFitTolerance = 0
  FullyConstrained = true
  MakeInternals = false
  MapMode = 5
  sketch-geometry (5):
    g0: LineSegment StartX=-31.5 StartY=3 StartZ=0 EndX=-15.5 EndY=3 EndZ=0
    g1: LineSegment StartX=-15.5 StartY=3 StartZ=0 EndX=-15.5 EndY=52 EndZ=0
    g2: LineSegment StartX=-15.5 StartY=52 StartZ=0 EndX=15.5 EndY=52 EndZ=0
    g3: LineSegment StartX=15.5 StartY=52 StartZ=0 EndX=15.5 EndY=3 EndZ=0
    g4: LineSegment StartX=15.5 StartY=3 StartZ=0 EndX=31.5 EndY=3 EndZ=0
  constraints (15):
    c: Horizontal(g0)
    c: Coincident(g0,g1)
    c: Vertical(g1)
    c: Coincident(g1,g2)
    c: Coincident(g2,g3)
    c: Vertical(g3)
    c: Coincident(g3,g4)
    c: Horizontal(g4)
    c: Symmetric(g1,g2,g-2)
    c: Symmetric(g4,g0,g-2)
    c: DistanceX(g2,g2) = 31
    c: DistanceY(g4) = 3
    c: DistanceY(g2) = 52
    c: DistanceX(g4,g4) = 16
    c: DistanceX(g0,g4) = 63  'total_width'
FEATURE [Sketcher::SketchObject] Sketch226  label="UV_driver_holder_holes_Sketch"
  ArcFitTolerance = 0
  ExternalGeometry = -> [Sketch225]
  FullyConstrained = true
  MakeInternals = false
  sketch-geometry (2):
    g0: Circle CenterX=26.5 CenterY=0 CenterZ=0 NormalX=0 NormalY=0 NormalZ=1 AngleXU=0 Radius=1.7
    g1: Circle CenterX=-26.5 CenterY=0 CenterZ=0 NormalX=0 NormalY=0 NormalZ=1 AngleXU=0 Radius=1.7
  constraints (5):
    c: PointOnObject(g0,g-1)
    c: Diameter(g0) = 3.4
    c: DistanceX(g0,g-3) = 5
    c: Equal(g1,g0)
    c: Symmetric(g1,g0,g-2)
FEATURE [Part::Compound] Compound083  label="sleeve_inner_cut1"
  Links = -> [Extrude032]
FEATURE [PartDesign::Boolean] Boolean031
  BaseFeature = -> Revolution
  Group = -> [Compound083]
  Suppressed = false
  Type = 1
  UsePlacement = false
FEATURE [Sketcher::SketchObject] Sketch228
  ArcFitTolerance = 0
  AttachmentSupport = -> [XZ_Plane105]
  FullyConstrained = true
  MakeInternals = false
  MapMode = 5
  Placement = pos=(0,0,0) rot=(1,0,0;1.5708rad)
  expr: Constraints[12] = <<bottom_bearing_Sketch>>.Constraints.inner_r - 0.5 mm
  expr: Constraints[13] = <<bottom_bearing_Sketch>>.Constraints.outer_r
  expr: Constraints[16] = 61.3 mm - <<bottom_bearing_Sketch>>.Constraints.height
  sketch-geometry (6):
    g0: LineSegment StartX=37 StartY=0 StartZ=0 EndX=37 EndY=5 EndZ=0
    g1: LineSegment StartX=37 StartY=5 StartZ=0 EndX=50 EndY=5 EndZ=0
    g2: LineSegment StartX=50 StartY=5 StartZ=0 EndX=50 EndY=47.3 EndZ=0
    g3: LineSegment StartX=50 StartY=47.3 StartZ=0 EndX=0 EndY=47.3 EndZ=0
    g4: LineSegment StartX=0 StartY=47.3 StartZ=0 EndX=0 EndY=0 EndZ=0
    g5: LineSegment StartX=0 StartY=0 StartZ=0 EndX=37 EndY=0 EndZ=0
  constraints (17):
    c: Vertical(g0)
    c: Coincident(g0,g1)
    c: Coincident(g1,g2)
    c: Vertical(g2)
    c: Coincident(g2,g3)
    c: Horizontal(g3)
    c: Coincident(g3,g4)
    c: Vertical(g4)
    c: Coincident(g4,g5)
    c: Coincident(g5,g0)
    c: Horizontal(g5)
    c: DistanceY(g0,g0) = 5
    c: DistanceX(g0) = 37
    c: DistanceX(g1) = 50
    c: Horizontal(g1)
    c: Coincident(g4,g-1)
    c: DistanceY(g2,g2) = 42.3
FEATURE [PartDesign::Revolution] Revolution003
  Angle = 360
  Angle2 = 60
  Axis = (0,2e-16,1)
  Base = (0,0,0)
  Placement = pos=(0,0,0) rot=(1,0,0;1.5708rad)
  Profile = -> Sketch228
  ReferenceAxis = -> Sketch228 [V_Axis]
  Reversed = true
  Suppressed = false
  Type = 0
FEATURE [Part::Cylinder] Cylinder007  label="hole_6.5mm"
  Angle = 360
  AttacherType = Attacher::AttachEngine3D
  FirstAngle = 0
  Height = 100
  Radius = 3.25
  SecondAngle = 0
FEATURE [Part::FeaturePython] PolarArray008  label="bottom_sleeve_to_basement_placement"  # WARN: FeaturePython — macro-defined, semantics opaque (R4)
  Alignment = 0
  AttacherType = Attacher::AttachEngine3D
  CellStart = A1
  Count = 3
  DistributionLaw = 0
  EndInclusive = false
  ExposePlacement = false
  FlipX = false
  FlipZ = false
  GeneratorMode = 0
  MarkerShape = 1
  MarkerSize = 0
  NumElements = 3
  OrientMode = 2
  Radius = 28.4
  Reverse = false
  SpanEnd = 360
  SpanStart = 0
  Step = 120
  Type = lattice2PolarArray2.PolarArray
  UseArcRadius = false
  UseArcRange = 0
  VSGVersion = 1
  Values = 0.0 | 120.0 | 240.0
  ValuesSource = 2
  isLattice = 1
  expr: Radius = <<bottom_bearing_Sketch>>.Constraints.inner_r - 18.2 mm / 2
FEATURE [Part::FeaturePython] Populate049  label="Populate bottom_sleeve_to_basement_placement with hole_6.5mm"  # WARN: FeaturePython — macro-defined, semantics opaque (R4)
  Copying = 0
  ExposePlacement = false
  MarkerShape = 1
  MarkerSize = 0
  NumElements = 0
  Object = -> Cylinder007
  OutputCompounding = 1
  Placement = pos=(0,0,-10) rot=(0,0,1;0rad)
  PlacementsTo = -> PolarArray008
  Referencing = 0
  Type = lattice2PopulateCopies.LatticePopulateCopies
  isLattice = 0
FEATURE [Part::Cylinder] Cylinder008  label="hole_12.5mm"
  Angle = 360
  AttacherType = Attacher::AttachEngine3D
  FirstAngle = 0
  Height = 100
  Radius = 6.25
  SecondAngle = 0
FEATURE [Part::Compound] Compound085  label="bottom_caprolon_cut1"
  Links = -> [Populate049,Cylinder008]
FEATURE [PartDesign::Boolean] Boolean036
  BaseFeature = -> Revolution003
  Group = -> [Compound085]
  Suppressed = false
  Type = 1
  UsePlacement = false
FEATURE [PartDesign::Body] Body128  label="bottom_caprolon"
  AllowCompound = false
  Group = -> [Sketch228,Revolution003,Boolean036]
  Origin = -> Origin105
  Placement = pos=(0,0,14) rot=(0,0,1;0rad)
  Tip = -> Boolean036
FEATURE [Sketcher::SketchObject] Sketch229
  ArcFitTolerance = 0
  AttachmentSupport = -> [XY_Plane106]
  FullyConstrained = true
  MakeInternals = false
  MapMode = 5
  sketch-geometry (13):
    g0: LineSegment [constr] StartX=-15.05 StartY=-24.05 StartZ=0 EndX=-15.05 EndY=24.05 EndZ=0
    g1: LineSegment [constr] StartX=-15.05 StartY=24.05 StartZ=0 EndX=15.05 EndY=24.05 EndZ=0
    g2: LineSegment [constr] StartX=15.05 StartY=24.05 StartZ=0 EndX=15.05 EndY=-24.05 EndZ=0
    g3: LineSegment [constr] StartX=15.05 StartY=-24.05 StartZ=0 EndX=-15.05 EndY=-24.05 EndZ=0
    g4: GeomPoint [constr] X=2e-16 Y=0 Z=0
    g5: Circle CenterX=15.05 CenterY=24.05 CenterZ=0 NormalX=0 NormalY=0 NormalZ=1 AngleXU=0 Radius=3.15
    g6: Circle CenterX=-15.05 CenterY=24.05 CenterZ=0 NormalX=0 NormalY=0 NormalZ=1 AngleXU=0 Radius=3.15
    g7: Circle CenterX=-15.05 CenterY=-24.05 CenterZ=0 NormalX=0 NormalY=0 NormalZ=1 AngleXU=0 Radius=3.15
    g8: Circle CenterX=15.05 CenterY=-24.05 CenterZ=0 NormalX=0 NormalY=0 NormalZ=1 AngleXU=0 Radius=3.15
    g9: GeomPoint [constr] X=-18.2 Y=24.05 Z=0
    g10: GeomPoint [constr] X=18.2 Y=24.05 Z=0
    g11: GeomPoint [constr] X=15.05 Y=-27.2 Z=0
    g12: GeomPoint [constr] X=15.05 Y=27.2 Z=0
  constraints (28):
    c: Coincident(g0,g1)
    c: Coincident(g1,g2)
    c: Coincident(g2,g3)
    c: Coincident(g3,g0)
    c: Horizontal(g1)
    c: Horizontal(g3)
    c: Vertical(g0)
    c: Vertical(g2)
    c: Symmetric(g1,g0,g4)
    c: Coincident(g4,g-1)
    c: Coincident(g5,g1)
    c: Coincident(g6,g0)
    c: Coincident(g7,g0)
    c: Coincident(g8,g2)
    c: PointOnObject(g9,g6)
    c: PointOnObject(g10,g5)
    c: PointOnObject(g11,g8)
    c: PointOnObject(g12,g5)
    c: Vertical(g5,g12)
    c: Horizontal(g5,g10)
    c: Horizontal(g6,g9)
    c: Vertical(g8,g11)
    c: Equal(g5,g6)
    c: Equal(g6,g7)
    c: Equal(g7,g8)
    c: DistanceX(g9,g10) = 36.4
    c: DistanceY(g11,g12) = 54.4
    c: Diameter(g5) = 6.3
FEATURE [Sketcher::SketchObject] Sketch230
  ArcFitTolerance = 0
  AttachmentSupport = -> [XY_Plane106]
  FullyConstrained = true
  MakeInternals = false
  MapMode = 5
  sketch-geometry (5):
    g0: LineSegment StartX=-22.5 StartY=-30 StartZ=0 EndX=-22.5 EndY=30 EndZ=0
    g1: LineSegment StartX=-22.5 StartY=30 StartZ=0 EndX=22.5 EndY=30 EndZ=0
    g2: LineSegment StartX=22.5 StartY=30 StartZ=0 EndX=22.5 EndY=-30 EndZ=0
    g3: LineSegment StartX=22.5 StartY=-30 StartZ=0 EndX=-22.5 EndY=-30 EndZ=0
    g4: GeomPoint [constr] X=0 Y=0 Z=0
  constraints (12):
    c: Coincident(g0,g1)
    c: Coincident(g1,g2)
    c: Coincident(g2,g3)
    c: Coincident(g3,g0)
    c: Horizontal(g1)
    c: Horizontal(g3)
    c: Vertical(g0)
    c: Vertical(g2)
    c: Symmetric(g1,g0,g4)
    c: Coincident(g4,g-1)
    c: DistanceY(g2,g2) = 60
    c: DistanceX(g1,g1) = 45
FEATURE [PartDesign::Pad] Pad036
  Direction = (0,0,1)
  Length = 60.3
  Length2 = 10
  Profile = -> Sketch230
  ReferenceAxis = -> Sketch230 [N_Axis]
  Suppressed = false
  Type = 0
FEATURE [PartDesign::Body] Body129  label="wheel"
  AllowCompound = false
  Group = -> [Sketch229,Sketch230,Pad036]
  Origin = -> Origin106
  Tip = -> Pad036
FEATURE [Sketcher::SketchObject] Sketch231
  ArcFitTolerance = 0
  FullyConstrained = true
  MakeInternals = false
  expr: .Constraints.outer_r = <<basement_bottom_sketch>>.Constraints.min_r - 2 mm
  sketch-geometry (5):
    g0: ArcOfCircle CenterX=0 CenterY=0 CenterZ=0 NormalX=0 NormalY=0 NormalZ=1 AngleXU=0 Radius=148 StartAngle=0.543468 EndAngle=1.5708
    g1: ArcOfCircle CenterX=0 CenterY=0 CenterZ=0 NormalX=0 NormalY=0 NormalZ=1 AngleXU=0 Radius=168 StartAngle=0.541782 EndAngle=1.5708
    g2: ArcOfCircle CenterX=129.244 CenterY=78.0832 CenterZ=0 NormalX=0 NormalY=0 NormalZ=1 AngleXU=0 Radius=3 StartAngle=3.68506 EndAngle=5.23599
    g3: ArcOfCircle CenterX=141.371 CenterY=85.0844 CenterZ=0 NormalX=0 NormalY=0 NormalZ=1 AngleXU=0 Radius=3 StartAngle=5.23599 EndAngle=6.82497
    g4: LineSegment StartX=130.744 StartY=75.4851 StartZ=0 EndX=142.871 EndY=82.4864 EndZ=0
  constraints (15):
    c: Coincident(g0,g-1)
    c: PointOnObject(g0,g-2)
    c: Coincident(g1,g0)
    c: PointOnObject(g1,g-2)
    c: Tangent(g3,g1) = -1.5708
    c: Tangent(g4,g3) = -1.5708
    c: Tangent(g4,g2) = -1.5708
    c: Tangent(g2,g0) = 1.5708
    c: Equal(g2,g3)
    c: Radius(g2) = 3
    c: DistanceY(g0,g1) = 20
    c: PointOnObject(g0,g4)
    c: Angle(g4) = 0.523599
    c: DistanceY(g1) = 168  'outer_r'
    c: DistanceY(g0) = 148  'inner_r'
FEATURE [Part::Mirroring] Part__Mirroring033  label="Sketch231 (Mirror #30)"
  Base = (0,0,0)
  Normal = (1,0,0)
  Source = -> Sketch231
FEATURE [Part::FeaturePython] Connect004  # WARN: FeaturePython — macro-defined, semantics opaque (R4)
  Objects = -> [Sketch231,Part__Mirroring033]
  Tolerance = 0
FEATURE [Part::FeaturePython] PolarArray009  # WARN: FeaturePython — macro-defined, semantics opaque (R4)
  Alignment = 0
  AttacherType = Attacher::AttachEngine3D
  CellStart = A1
  Count = 3
  DistributionLaw = 0
  EndInclusive = true
  ExposePlacement = false
  FlipX = false
  FlipZ = false
  GeneratorMode = 0
  MarkerShape = 1
  MarkerSize = 0
  NumElements = 3
  OrientMode = 2
  Placement = pos=(0,0,0) rot=(0,0,1;1.5708rad)
  Radius = 140
  Reverse = false
  SpanEnd = 50
  SpanStart = -50
  Step = 50
  Type = lattice2PolarArray2.PolarArray
  UseArcRadius = false
  UseArcRange = 0
  VSGVersion = 1
  Values = -50.0 | 0.0 | 50.0
  ValuesSource = 2
  isLattice = 1
  expr: Radius = <<Sketch231>>.Constraints.inner_r - 8 mm
FEATURE [Sketcher::SketchObject] Sketch232
  ArcFitTolerance = 0
  FullyConstrained = true
  MakeInternals = false
  sketch-geometry (4):
    g0: ArcOfCircle CenterX=0 CenterY=0 CenterZ=0 NormalX=0 NormalY=0 NormalZ=1 AngleXU=0 Radius=5 StartAngle=1.5708 EndAngle=4.71239
    g1: LineSegment StartX=8 StartY=-13 StartZ=0 EndX=8 EndY=13 EndZ=0
    g2: ArcOfCircle CenterX=0 CenterY=13 CenterZ=0 NormalX=0 NormalY=0 NormalZ=1 AngleXU=0 Radius=8 StartAngle=4.71239 EndAngle=6.28319
    g3: ArcOfCircle CenterX=0 CenterY=-13 CenterZ=0 NormalX=0 NormalY=0 NormalZ=1 AngleXU=0 Radius=8 StartAngle=0 EndAngle=1.5708
  constraints (12):
    c: Coincident(g0,g-1)
    c: PointOnObject(g0,g-2)
    c: PointOnObject(g0,g-2)
    c: Vertical(g1)
    c: PointOnObject(g2,g-2)
    c: Coincident(g2,g0)
    c: PointOnObject(g3,g-2)
    c: Coincident(g3,g0)
    c: Diameter(g0) = 10
    c: Tangent(g2,g1) = -1.5708
    c: Tangent(g3,g1) = -1.5708
    c: DistanceX(g1) = 8
FEATURE [Part::Extrusion] Extrude034
  Base = -> Sketch232
  Dir = (0,0,1)
  DirMode = 2
  FaceMakerClass = Part::FaceMakerBullseye
  FaceMakerMode = 3
  LengthFwd = 1
  LengthRev = 0
  Solid = true
  Symmetric = false
FEATURE [Part::FeaturePython] Populate050  label="Populate PolarArray009 with Extrude034"  # WARN: FeaturePython — macro-defined, semantics opaque (R4)
  Copying = 0
  ExposePlacement = false
  MarkerShape = 1
  MarkerSize = 0
  NumElements = 0
  Object = -> Extrude034
  OutputCompounding = 1
  PlacementsTo = -> PolarArray009
  Referencing = 0
  Type = lattice2PopulateCopies.LatticePopulateCopies
  isLattice = 0
FEATURE [PartDesign::SubShapeBinder] Binder136
  BindCopyOnChange = 0
  BindMode = 0
  ClaimChildren = true
  Context = -> Body130 [Binder136.]
  Fuse = false
  MakeFace = true
  OffsetFill = false
  OffsetIntersection = false
  OffsetJoinType = 0
  OffsetOpenResult = false
  PartialLoad = false
  Relative = false
  Support = -> [Connect004]
  _Version = 2
FEATURE [PartDesign::Pad] Pad037
  Direction = (0,0,1)
  Length = 1
  Length2 = 10
  Profile = -> Binder136
  Suppressed = false
  Type = 0
FEATURE [Part::Compound] Compound086
  Links = -> [Populate050]
FEATURE [PartDesign::Boolean] Boolean037
  BaseFeature = -> Pad037
  Group = -> [Compound086]
  Refine = true
  Suppressed = false
  Type = 0
  UsePlacement = false
FEATURE [Part::FeaturePython] Populate051  label="Populate 3_elem_polar_array with PolarArray009"  # WARN: FeaturePython — macro-defined, semantics opaque (R4)
  Copying = 0
  ExposePlacement = false
  MarkerShape = 1
  MarkerSize = 0
  NumElements = 9
  Object = -> PolarArray009
  OutputCompounding = 0
  PlacementsTo = -> PolarArray006
  Referencing = 1
  Type = lattice2PopulateCopies.LatticePopulateCopies
  isLattice = 1
FEATURE [Part::FeaturePython] Populate052  label="Populate Populate 3_elem_polar_array with PolarArray009 with hole_3.2_mm_extrude"  # WARN: FeaturePython — macro-defined, semantics opaque (R4)
  Copying = 0
  ExposePlacement = false
  MarkerShape = 1
  MarkerSize = 0
  NumElements = 0
  Object = -> Cylinder001
  OutputCompounding = 1
  PlacementsTo = -> Populate051
  Referencing = 0
  Type = lattice2PopulateCopies.LatticePopulateCopies
  isLattice = 0
FEATURE [Part::FeaturePython] Populate053  label="Populate PolarArray009 with hole_5_mm_extrude"  # WARN: FeaturePython — macro-defined, semantics opaque (R4)
  Copying = 0
  ExposePlacement = false
  MarkerShape = 1
  MarkerSize = 0
  NumElements = 0
  Object = -> Extrude023
  OutputCompounding = 1
  PlacementsTo = -> PolarArray009
  Referencing = 0
  Type = lattice2PopulateCopies.LatticePopulateCopies
  isLattice = 0
FEATURE [PartDesign::Boolean] Boolean038
  BaseFeature = -> Boolean037
  Group = -> [Populate053]
  Suppressed = false
  Type = 1
  UsePlacement = false
FEATURE [PartDesign::Body] Body130
  AllowCompound = false
  Group = -> [Binder136,Pad037,Boolean037,Boolean038]
  Origin = -> Origin107
  Tip = -> Boolean038
FEATURE [Sketcher::SketchObject] Sketch233  label="small_bearing_Sketch"
  ArcFitTolerance = 0
  AttachmentSupport = -> [XZ_Plane108]
  FullyConstrained = true
  MakeInternals = false
  MapMode = 5
  Placement = pos=(0,0,0) rot=(1,0,0;1.5708rad)
  sketch-geometry (4):
    g0: LineSegment StartX=6 StartY=0 StartZ=0 EndX=13 EndY=0 EndZ=0
    g1: LineSegment StartX=13 StartY=0 StartZ=0 EndX=13 EndY=8.9 EndZ=0
    g2: LineSegment StartX=13 StartY=8.9 StartZ=0 EndX=6 EndY=8.9 EndZ=0
    g3: LineSegment StartX=6 StartY=8.9 StartZ=0 EndX=6 EndY=0 EndZ=0
  constraints (12):
    c: Coincident(g0,g1)
    c: Coincident(g1,g2)
    c: Coincident(g2,g3)
    c: Coincident(g3,g0)
    c: Horizontal(g0)
    c: Horizontal(g2)
    c: Vertical(g1)
    c: Vertical(g3)
    c: PointOnObject(g0,g-1)
    c: DistanceY(g3,g3) = 8.9
    c: DistanceX(g0) = 6
    c: DistanceX(g0) = 13
FEATURE [PartDesign::Revolution] Revolution004
  Angle = 360
  Angle2 = 60
  Axis = (0,2e-16,1)
  Base = (0,0,0)
  Placement = pos=(0,0,0) rot=(1,0,0;1.5708rad)
  Profile = -> Sketch233
  ReferenceAxis = -> Sketch233 [V_Axis]
  Reversed = true
  Suppressed = false
  Type = 0
FEATURE [PartDesign::Body] Body131  label="small_bearing"
  AllowCompound = false
  Group = -> [Sketch233,Revolution004]
  Origin = -> Origin108
  Tip = -> Revolution004
FEATURE [TechDraw::DrawViewPart] View004
  CoarseView = false
  Direction = (0,0,1)
  Focus = 100
  HardHidden = false
  IsoCount = 0
  IsoHidden = false
  IsoVisible = false
  LockPosition = false
  Perspective = false
  Rotation = 0
  ScaleType = 0
  ScrubCount = 0
  SeamHidden = false
  SeamVisible = true
  SmoothHidden = false
  SmoothVisible = true
  Source = -> [Body128]
  X = 78.5
  XDirection = (1,0,0)
  Y = 105
FEATURE [TechDraw::DrawViewPart] View005
  CoarseView = false
  Direction = (0,-1,0)
  Focus = 100
  HardHidden = false
  IsoCount = 0
  IsoHidden = false
  IsoVisible = false
  LockPosition = false
  Perspective = false
  Rotation = 0
  ScaleType = 0
  ScrubCount = 0
  SeamHidden = false
  SeamVisible = true
  SmoothHidden = false
  SmoothVisible = true
  Source = -> [Body128]
  X = 228.5
  XDirection = (1,0,0)
  Y = 155
FEATURE [TechDraw::DrawViewSection] SectionView002  label="Section002  - "
  BaseView = -> View005
  CoarseView = false
  CutSurfaceDisplay = 1
  Direction = (1,0,0)
  FileGeomPattern = <path>
  FileHatchPattern = <path>
  Focus = 100
  FuseBeforeCut = false
  HardHidden = false
  HatchOffset = (0,0,0)
  HatchRotation = 0
  HatchScale = 1
  IsoCount = 0
  IsoHidden = false
  IsoVisible = false
  LockPosition = false
  NameGeomPattern = Diamond
  Perspective = false
  Rotation = 90
  ScaleType = 0
  ScrubCount = 0
  SeamHidden = false
  SeamVisible = true
  SectionDirection = 4
  SectionLineStretch = 1
  SectionNormal = (1,0,0)
  SectionOrigin = (0,0,37.65)
  SmoothHidden = false
  SmoothVisible = true
  Source = -> [Body128]
  TrimAfterCut = false
  UsePreviousCut = false
  X = 228.5
  XDirection = (0,0,1)
  Y = 55
FEATURE [TechDraw::DrawViewDimension] Dimension016
  AngleOverride = false
  Arbitrary = false
  ArbitraryTolerances = false
  EqualTolerance = true
  ExtensionAngle = 0
  FormatSpec = %.2w
  FormatSpecOverTolerance = %+.2w
  FormatSpecUnderTolerance = %+.2w
  Inverted = false
  LineAngle = 0
  LockPosition = false
  MeasureType = 1
  OverTolerance = 0
  References2D = -> [View005]
  Rotation = 0
  ScaleType = 0
  TheoreticalExact = false
  Type = 2
  UnderTolerance = 0
  X = -63.5214
  Y = -28.8688
FEATURE [TechDraw::DrawViewDimension] Dimension017
  AngleOverride = false
  Arbitrary = false
  ArbitraryTolerances = false
  EqualTolerance = true
  ExtensionAngle = 0
  FormatSpec = %.2w
  FormatSpecOverTolerance = %+.2w
  FormatSpecUnderTolerance = %+.2w
  Inverted = false
  LineAngle = 0
  LockPosition = false
  MeasureType = 1
  OverTolerance = 0
  References2D = -> [View005]
  Rotation = 0
  ScaleType = 0
  TheoreticalExact = false
  Type = 2
  UnderTolerance = 0
  X = -69.3536
  Y = 5.37948
FEATURE [TechDraw::DrawViewDimension] Dimension018
  AngleOverride = false
  Arbitrary = false
  ArbitraryTolerances = false
  EqualTolerance = true
  ExtensionAngle = 0
  FormatSpec = ⌀%.2w
  FormatSpecOverTolerance = %+.2w
  FormatSpecUnderTolerance = %+.2w
  Inverted = false
  LineAngle = 0
  LockPosition = false
  MeasureType = 1
  OverTolerance = 0
  References2D = -> [View004]
  Rotation = 0
  ScaleType = 0
  TheoreticalExact = false
  Type = 5
  UnderTolerance = 0
  X = -23.9762
  Y = 6.63298
FEATURE [TechDraw::DrawViewDimension] Dimension019
  AngleOverride = false
  Arbitrary = false
  ArbitraryTolerances = false
  EqualTolerance = true
  ExtensionAngle = 0
  FormatSpec = ⌀%.2w
  FormatSpecOverTolerance = %+.2w
  FormatSpecUnderTolerance = %+.2w
  Inverted = false
  LineAngle = 0
  LockPosition = false
  MeasureType = 1
  OverTolerance = 0
  References2D = -> [View004]
  Rotation = 0
  ScaleType = 0
  TheoreticalExact = false
  Type = 5
  UnderTolerance = 0
  X = 8.66891
  Y = 33.3069
FEATURE [TechDraw::DrawViewDimension] Dimension020
  AngleOverride = false
  Arbitrary = false
  ArbitraryTolerances = false
  EqualTolerance = true
  ExtensionAngle = 0
  FormatSpec = %.2w
  FormatSpecOverTolerance = %+.2w
  FormatSpecUnderTolerance = %+.2w
  Inverted = false
  LineAngle = 0
  LockPosition = false
  MeasureType = 1
  OverTolerance = 0
  References2D = -> [View004]
  Rotation = 0
  ScaleType = 0
  TheoreticalExact = false
  Type = 1
  UnderTolerance = 0
  X = 13.41
  Y = -12.6373
FEATURE [TechDraw::DrawViewDimension] Dimension021
  AngleOverride = false
  Arbitrary = false
  ArbitraryTolerances = false
  EqualTolerance = true
  ExtensionAngle = 0
  FormatSpec = %.2w
  FormatSpecOverTolerance = %+.2w
  FormatSpecUnderTolerance = %+.2w
  Inverted = false
  LineAngle = 0
  LockPosition = false
  MeasureType = 1
  OverTolerance = 0
  References2D = -> [View005]
  Rotation = 0
  ScaleType = 0
  TheoreticalExact = false
  Type = 1
  UnderTolerance = 0
  X = -11.0078
  Y = 36.7782
FEATURE [TechDraw::DrawViewDimension] Dimension022
  AngleOverride = false
  Arbitrary = false
  ArbitraryTolerances = false
  EqualTolerance = true
  ExtensionAngle = 0
  FormatSpec = %.2w
  FormatSpecOverTolerance = %+.2w
  FormatSpecUnderTolerance = %+.2w
  Inverted = false
  LineAngle = 0
  LockPosition = false
  MeasureType = 1
  OverTolerance = 0
  References2D = -> [View005]
  Rotation = 0
  ScaleType = 0
  TheoreticalExact = false
  Type = 1
  UnderTolerance = 0
  X = -1.13845
  Y = -46.1959
FEATURE [TechDraw::DrawViewDimension] Dimension023
  AngleOverride = false
  Arbitrary = false
  ArbitraryTolerances = false
  EqualTolerance = true
  ExtensionAngle = 0
  FormatSpec = %.2w
  FormatSpecOverTolerance = %+.2w
  FormatSpecUnderTolerance = %+.2w
  Inverted = false
  LineAngle = 0
  LockPosition = false
  MeasureType = 1
  OverTolerance = 0
  References2D = -> [SectionView002]
  Rotation = 0
  ScaleType = 0
  TheoreticalExact = false
  Type = 1
  UnderTolerance = 0
  X = 0
  Y = -27.26
FEATURE [Sketcher::SketchObject] Sketch234  label="sleeve_outer_sketch001"
  ArcFitTolerance = 0
  AttachmentSupport = -> [XZ_Plane110]
  FullyConstrained = true
  MakeInternals = false
  MapMode = 5
  Placement = pos=(0,0,0) rot=(1,0,0;1.5708rad)
  expr: Constraints[13] = <<sleeve_inner_sketch001>>.Constraints.outer_r + 0.25 mm
  sketch-geometry (6):
    g0: LineSegment StartX=13.25 StartY=74.7 StartZ=0 EndX=13.25 EndY=0 EndZ=0
    g1: LineSegment StartX=13.25 StartY=0 StartZ=0 EndX=35.25 EndY=0 EndZ=0
    g2: LineSegment StartX=35.25 StartY=0 StartZ=0 EndX=35.25 EndY=7 EndZ=0
    g3: LineSegment StartX=35.25 StartY=7 StartZ=0 EndX=20.25 EndY=7 EndZ=0
    g4: LineSegment StartX=20.25 StartY=7 StartZ=0 EndX=20.25 EndY=74.7 EndZ=0
    g5: LineSegment StartX=20.25 StartY=74.7 StartZ=0 EndX=13.25 EndY=74.7 EndZ=0
  constraints (20):
    c: PointOnObject(g0,g-1)
    c: Vertical(g0)
    c: Coincident(g0,g1)
    c: PointOnObject(g1,g-1)
    c: Coincident(g1,g2)
    c: Vertical(g2)
    c: Coincident(g2,g3)
    c: Horizontal(g3)
    c: Coincident(g3,g4)
    c: Vertical(g4)
    c: Coincident(g4,g5)
    c: Coincident(g5,g0)
    c: Horizontal(g5)
    c: DistanceX(g0) = 13.25
    c: DistanceX(g5,g5) = 7
    c: DistanceX(g3,g3) = 15
    c: DistanceY(g2,g2) = 7  'flange_height'
    c: DistanceY(g0,g0) = 74.7
    c: DistanceX(g3) = 20.25  'max_r'
    c: DistanceX(g1) = 35.25  'flange_max_r'
FEATURE [Sketcher::SketchObject] Sketch235  label="sleeve_inner_sketch001"
  ArcFitTolerance = 0
  AttachmentSupport = -> [XZ_Plane101]
  FullyConstrained = true
  MakeInternals = false
  MapMode = 5
  Placement = pos=(0,0,0) rot=(1,0,0;1.5708rad)
  sketch-geometry (6):
    g0: LineSegment StartX=5 StartY=83.7 StartZ=0 EndX=5 EndY=0 EndZ=0
    g1: LineSegment StartX=5 StartY=0 StartZ=0 EndX=33 EndY=0 EndZ=0
    g2: LineSegment StartX=33 StartY=0 StartZ=0 EndX=33 EndY=5 EndZ=0
    g3: LineSegment StartX=33 StartY=5 StartZ=0 EndX=13 EndY=5 EndZ=0
    g4: LineSegment StartX=13 StartY=5 StartZ=0 EndX=13 EndY=83.7 EndZ=0
    g5: LineSegment StartX=13 StartY=83.7 StartZ=0 EndX=5 EndY=83.7 EndZ=0
  constraints (19):
    c: PointOnObject(g0,g-1)
    c: Vertical(g0)
    c: Coincident(g0,g1)
    c: PointOnObject(g1,g-1)
    c: Coincident(g1,g2)
    c: Vertical(g2)
    c: Coincident(g2,g3)
    c: Horizontal(g3)
    c: Coincident(g3,g4)
    c: Vertical(g4)
    c: Coincident(g4,g5)
    c: Coincident(g5,g0)
    c: Horizontal(g5)
    c: DistanceX(g0) = 5  'inner_r'
    c: DistanceX(g0,g3) = 8
    c: DistanceY(g2,g2) = 5
    c: DistanceX(g3,g3) = 20
    c: DistanceX(g3) = 13  'outer_r'
    c: DistanceY(g0) = 83.7
FEATURE [PartDesign::Revolution] Revolution005
  Angle = 360
  Angle2 = 60
  Axis = (0,2e-16,1)
  Base = (0,0,0)
  Placement = pos=(0,0,0) rot=(1,0,0;1.5708rad)
  Profile = -> Sketch235
  ReferenceAxis = -> Sketch235 [V_Axis]
  Reversed = true
  Suppressed = false
  Type = 0
FEATURE [PartDesign::Revolution] Revolution006
  Angle = 360
  Angle2 = 60
  Axis = (0,2e-16,1)
  Base = (0,0,0)
  Placement = pos=(0,0,0) rot=(1,0,0;1.5708rad)
  Profile = -> Sketch234
  ReferenceAxis = -> Sketch234 [V_Axis]
  Reversed = true
  Suppressed = false
  Type = 0
FEATURE [Part::Compound] Compound087  label="sleeve_outer_cut002"
  Links = -> [Array012]
FEATURE [PartDesign::Boolean] Boolean039
  BaseFeature = -> Revolution006
  Group = -> [Compound087]
  Suppressed = false
  Type = 1
  UsePlacement = false
FEATURE [Part::Compound] Compound088  label="sleeve_inner_cut002"
  Links = -> [Extrude032]
FEATURE [PartDesign::Boolean] Boolean040
  BaseFeature = -> Revolution005
  Group = -> [Compound088]
  Suppressed = false
  Type = 1
  UsePlacement = false
FEATURE [TechDraw::DrawViewAnnotation] Annotation
  Font = osifont
  LineSpace = 100
  LockPosition = false
  MaxWidth = -1
  Rotation = 0
  ScaleType = 0
  Text = 1 шт.
  TextSize = 5
  TextStyle = 0
  X = 81.8233
  Y = 167.816
FEATURE [TechDraw::DrawViewAnnotation] Annotation001
  Font = osifont
  LineSpace = 100
  LockPosition = false
  MaxWidth = -1
  Rotation = 0
  ScaleType = 0
  Text = 1 шт.
  TextSize = 5
  TextStyle = 0
  X = 81.8233
  Y = 167.816
FEATURE [TechDraw::DrawViewAnnotation] Annotation004
  Font = osifont
  LineSpace = 100
  LockPosition = false
  MaxWidth = -1
  Rotation = 0
  ScaleType = 0
  Text = 1 шт.
  TextSize = 5
  TextStyle = 0
  X = 73.0733
  Y = 186.077
FEATURE [TechDraw::DrawPage] Page002  label="bottom_sleeve_Page"
  KeepUpdated = true
  NextBalloonIndex = 1
  ProjectionType = 0
  Template = -> Template
  Views = -> [View004,View005,SectionView002,Dimension016,Dimension017,Dimension018,Dimension019,Dimension020,Dimension021,Dimension022,Dimension023,Annotation004]
FEATURE [Sketcher::SketchObject] Sketch236
  ArcFitTolerance = 0
  FullyConstrained = true
  MakeInternals = false
  expr: Constraints[10] = <<pillar_base_sketch>>.Constraints.length - <<led_holder_fix_extrude>>.Placement.Base.y
  sketch-geometry (5):
    g0: LineSegment StartX=-3 StartY=-3.5 StartZ=0 EndX=-3 EndY=7.1152 EndZ=0
    g1: LineSegment StartX=-3 StartY=7.1152 StartZ=0 EndX=3 EndY=7.1152 EndZ=0
    g2: LineSegment StartX=3 StartY=7.1152 StartZ=0 EndX=3 EndY=-3.5 EndZ=0
    g3: LineSegment [constr] StartX=3 StartY=-3.5 StartZ=0 EndX=-3 EndY=-3.5 EndZ=0
    g4: GeomPoint [constr] X=0 Y=1.8076 Z=0
  constraints (13):
    c: Coincident(g0,g1)
    c: Coincident(g1,g2)
    c: Coincident(g2,g3)
    c: Coincident(g3,g0)
    c: Horizontal(g1)
    c: Horizontal(g3)
    c: Vertical(g0)
    c: Vertical(g2)
    c: Symmetric(g1,g0,g4)
    c: PointOnObject(g4,g-2)
    c: DistanceY(g1) = 7.1152
    c: DistanceY(g2) = -3.5
    c: DistanceX(g1,g1) = 6
FEATURE [PartDesign::SubShapeBinder] Binder137
  BindCopyOnChange = 0
  BindMode = 0
  ClaimChildren = true
  Context = -> Body134 [Binder137.]
  Fuse = false
  MakeFace = true
  OffsetFill = false
  OffsetIntersection = false
  OffsetJoinType = 0
  OffsetOpenResult = false
  PartialLoad = false
  Relative = false
  Support = -> [Sketch236]
  _Version = 2
FEATURE [PartDesign::FeaturePython] BaseBend051  # WARN: FeaturePython — macro-defined, semantics opaque (R4)
  BendSide = 0
  BendSketch = -> Binder137
  MidPlane = false
  Reverse = false
  Suppressed = false
  length = 830
  radius = 0.1
  thickness = 0.3
FEATURE [App::Link] Link046  label="led_holder_fix_extrude001"
  LinkPlacement = pos=(4,0,5) rot=(0,1,0;-1.5708rad)
  LinkedObject = -> Extrude010
  Placement = pos=(4,0,5) rot=(0,1,0;-1.5708rad)
FEATURE [Part::Compound] Compound089
  Links = -> [Link046]
FEATURE [PartDesign::Boolean] Boolean041
  BaseFeature = -> BaseBend051
  Group = -> [Compound089]
  Suppressed = false
  Type = 1
  UsePlacement = false
FEATURE [PartDesign::Body] Body134  label="wire_holder_material_0.30ansi"
  AllowCompound = false
  Group = -> [Binder137,BaseBend051,Boolean041]
  Origin = -> Origin112
  Tip = -> Boolean041
FEATURE [Sketcher::SketchObject] Sketch237
  ArcFitTolerance = 0
  FullyConstrained = true
  MakeInternals = false
  expr: Constraints[11] = <<pillar_base_sketch>>.Constraints.length - <<led_holder_fix_extrude>>.Placement.Base.y - 1.5 mm
  sketch-geometry (5):
    g0: LineSegment StartX=-4 StartY=-3.5 StartZ=0 EndX=4 EndY=-3.5 EndZ=0
    g1: LineSegment StartX=4 StartY=-3.5 StartZ=0 EndX=4 EndY=5.6152 EndZ=0
    g2: LineSegment StartX=4 StartY=5.6152 StartZ=0 EndX=-4 EndY=5.6152 EndZ=0
    g3: LineSegment StartX=-4 StartY=5.6152 StartZ=0 EndX=-4 EndY=-3.5 EndZ=0
    g4: GeomPoint [constr] X=0 Y=1.0576 Z=0
  constraints (13):
    c: Coincident(g0,g1)
    c: Coincident(g1,g2)
    c: Coincident(g2,g3)
    c: Coincident(g3,g0)
    c: Horizontal(g0)
    c: Horizontal(g2)
    c: Vertical(g1)
    c: Vertical(g3)
    c: Symmetric(g2,g0,g4)
    c: PointOnObject(g4,g-2)
    c: DistanceX(g0,g0) = 8
    c: DistanceY(g1) = 5.6152
    c: DistanceY(g0) = -3.5
FEATURE [PartDesign::SubShapeBinder] Binder138
  BindCopyOnChange = 0
  BindMode = 0
  ClaimChildren = true
  Context = -> Body135 [Binder138.]
  Fuse = false
  MakeFace = true
  OffsetFill = false
  OffsetIntersection = false
  OffsetJoinType = 0
  OffsetOpenResult = false
  PartialLoad = false
  Relative = true
  Support = -> [Sketch237]
  _Version = 2
FEATURE [PartDesign::Pad] Pad038
  Direction = (0,0,1)
  Length = 10
  Length2 = 10
  Profile = -> Binder138 [Face1]
  Suppressed = false
  Type = 0
FEATURE [Part::Compound] Compound090
  Links = -> [Link046]
FEATURE [PartDesign::Boolean] Boolean042
  BaseFeature = -> Pad038
  Group = -> [Compound090]
  Suppressed = false
  Type = 1
  UsePlacement = false
FEATURE [PartDesign::Body] Body135  label="wire_holder"
  AllowCompound = false
  Group = -> [Binder138,Pad038,Boolean042]
  Origin = -> Origin113
  Tip = -> Boolean042
FEATURE [Sketcher::SketchObject] Sketch238
  ArcFitTolerance = 0
  AttachmentSupport = -> [XY_Plane113]
  FullyConstrained = true
  MakeInternals = false
  MapMode = 5
  sketch-geometry (10):
    g0: LineSegment StartX=-10 StartY=-23.5 StartZ=0 EndX=10 EndY=-23.5 EndZ=0
    g1: LineSegment StartX=15 StartY=-18.5 StartZ=0 EndX=15 EndY=18.5 EndZ=0
    g2: LineSegment StartX=10 StartY=23.5 StartZ=0 EndX=-10 EndY=23.5 EndZ=0
    g3: LineSegment StartX=-15 StartY=18.5 StartZ=0 EndX=-15 EndY=-18.5 EndZ=0
    g4: ArcOfCircle CenterX=-10 CenterY=-18.5 CenterZ=0 NormalX=0 NormalY=0 NormalZ=1 AngleXU=0 Radius=5 StartAngle=3.14159 EndAngle=4.71239
    g5: ArcOfCircle CenterX=10 CenterY=-18.5 CenterZ=0 NormalX=0 NormalY=0 NormalZ=1 AngleXU=0 Radius=5 StartAngle=4.71239 EndAngle=6.28319
    g6: ArcOfCircle CenterX=10 CenterY=18.5 CenterZ=0 NormalX=0 NormalY=0 NormalZ=1 AngleXU=0 Radius=5 StartAngle=2.76279e-11 EndAngle=1.5708
    g7: ArcOfCircle CenterX=-10 CenterY=18.5 CenterZ=0 NormalX=0 NormalY=0 NormalZ=1 AngleXU=0 Radius=5 StartAngle=1.5708 EndAngle=3.14159
    g8: GeomPoint [constr] X=-15 Y=-23.5 Z=0
    g9: GeomPoint [constr] X=15 Y=23.5 Z=0
  constraints (23):
    c: Tangent(g0,g4) = -1.5708
    c: Tangent(g0,g5) = -1.5708
    c: Tangent(g1,g5) = -1.5708
    c: Tangent(g1,g6) = -1.5708
    c: Tangent(g2,g6) = -1.5708
    c: Tangent(g2,g7) = -1.5708
    c: Tangent(g3,g7) = -1.5708
    c: Tangent(g3,g4) = -1.5708
    c: Horizontal(g0)
    c: Horizontal(g2)
    c: Vertical(g1)
    c: Vertical(g3)
    c: Equal(g4,g5)
    c: Equal(g5,g6)
    c: Equal(g6,g7)
    c: PointOnObject(g8,g0)
    c: PointOnObject(g8,g3)
    c: PointOnObject(g9,g1)
    c: PointOnObject(g9,g2)
    c: Distance(g1,g3) = 30
    c: Distance(g0,g2) = 47
    c: Radius(g5) = 5
    c: Symmetric(g8,g9,g-1)
FEATURE [PartDesign::Pad] Pad039
  Direction = (0,0,1)
  Length = 1.5
  Length2 = 10
  Profile = -> Sketch238
  ReferenceAxis = -> Sketch238 [N_Axis]
  Suppressed = false
  Type = 0
FEATURE [Sketcher::SketchObject] Sketch239
  ArcFitTolerance = 0
  FullyConstrained = true
  MakeInternals = false
  sketch-geometry (2):
    g0: Circle CenterX=0 CenterY=-20 CenterZ=0 NormalX=0 NormalY=0 NormalZ=1 AngleXU=0 Radius=1.7
    g1: Circle CenterX=0 CenterY=20 CenterZ=0 NormalX=0 NormalY=0 NormalZ=1 AngleXU=0 Radius=1.7
  constraints (5):
    c: PointOnObject(g0,g-2)
    c: Symmetric(g1,g0,g-1)
    c: DistanceY(g0,g1) = 40
    c: Equal(g1,g0)
    c: Diameter(g1) = 3.4
FEATURE [PartDesign::SubShapeBinder] Binder139
  BindCopyOnChange = 0
  BindMode = 0
  ClaimChildren = true
  Fuse = false
  MakeFace = true
  OffsetFill = false
  OffsetIntersection = false
  OffsetJoinType = 0
  OffsetOpenResult = false
  PartialLoad = false
  Relative = false
  Support = -> [Sketch239]
  _Version = 2
FEATURE [PartDesign::Pocket] Pocket133
  BaseFeature = -> Pad039
  Direction = (0,0,-1)
  Length = 5
  Length2 = 5
  Midplane = true
  Profile = -> Binder139
  Suppressed = false
  Type = 1
FEATURE [PartDesign::Body] Body136
  AllowCompound = false
  Group = -> [Sketch238,Pad039,Binder139,Pocket133]
  Origin = -> Origin114
  Tip = -> Pocket133
FEATURE [Part::Part2DObjectPython] Rectangle  # Draft 2D object (typed FeaturePython)
  Area = 2e+06
  ChamferSize = 0
  Columns = 1
  FilletRadius = 0
  Height = 1000
  Length = 2000
  MakeFace = true
  Placement = pos=(-1000,-1000,0) rot=(0,0,1;0rad)
  Rows = 1
FEATURE [Part::Extrusion] Extrude035
  Base = -> Rectangle
  Dir = (0,0,1)
  DirMode = 2
  FaceMakerClass = Part::FaceMakerBullseye
  FaceMakerMode = 3
  LengthFwd = 100
  LengthRev = 0
  Solid = false
  Symmetric = false
FEATURE [Part::Cut] Cut
  Base = -> Populate045
  Tool = -> Extrude035
FEATURE [Sketcher::SketchObject] Sketch240
  ArcFitTolerance = 0
  FullyConstrained = true
  MakeInternals = false
  sketch-geometry (10):
    g0: LineSegment StartX=-22.5 StartY=-20 StartZ=0 EndX=22.5 EndY=-20 EndZ=0
    g1: LineSegment StartX=30 StartY=-12.5 StartZ=0 EndX=30 EndY=12.5 EndZ=0
    g2: LineSegment StartX=22.5 StartY=20 StartZ=0 EndX=-22.5 EndY=20 EndZ=0
    g3: LineSegment StartX=-30 StartY=12.5 StartZ=0 EndX=-30 EndY=-12.5 EndZ=0
    g4: ArcOfCircle CenterX=-22.5 CenterY=-12.5 CenterZ=0 NormalX=0 NormalY=0 NormalZ=1 AngleXU=0 Radius=7.5 StartAngle=3.14159 EndAngle=4.71239
    g5: ArcOfCircle CenterX=22.5 CenterY=-12.5 CenterZ=0 NormalX=0 NormalY=0 NormalZ=1 AngleXU=0 Radius=7.5 StartAngle=4.71239 EndAngle=6.28319
    g6: ArcOfCircle CenterX=22.5 CenterY=12.5 CenterZ=0 NormalX=0 NormalY=0 NormalZ=1 AngleXU=0 Radius=7.5 StartAngle=-7.9e-14 EndAngle=1.5708
    g7: ArcOfCircle CenterX=-22.5 CenterY=12.5 CenterZ=0 NormalX=0 NormalY=0 NormalZ=1 AngleXU=0 Radius=7.5 StartAngle=1.5708 EndAngle=3.14159
    g8: GeomPoint [constr] X=-30 Y=-20 Z=0
    g9: GeomPoint [constr] X=30 Y=20 Z=0
  constraints (23):
    c: Tangent(g0,g4) = -1.5708
    c: Tangent(g0,g5) = -1.5708
    c: Tangent(g1,g5) = -1.5708
    c: Tangent(g1,g6) = -1.5708
    c: Tangent(g2,g6) = -1.5708
    c: Tangent(g2,g7) = -1.5708
    c: Tangent(g3,g7) = -1.5708
    c: Tangent(g3,g4) = -1.5708
    c: Horizontal(g0)
    c: Horizontal(g2)
    c: Vertical(g1)
    c: Vertical(g3)
    c: Equal(g4,g5)
    c: Equal(g5,g6)
    c: Equal(g6,g7)
    c: PointOnObject(g8,g0)
    c: PointOnObject(g8,g3)
    c: PointOnObject(g9,g1)
    c: PointOnObject(g9,g2)
    c: Distance(g1,g3) = 60
    c: Distance(g0,g2) = 40
    c: Radius(g5) = 7.5
    c: Symmetric(g8,g9,g-1)
FEATURE [Sketcher::SketchObject] Sketch241
  ArcFitTolerance = 0
  FullyConstrained = true
  MakeInternals = false
  sketch-geometry (9):
    g0: LineSegment [constr] StartX=-22.5 StartY=-12.5 StartZ=0 EndX=22.5 EndY=-12.5 EndZ=0
    g1: LineSegment [constr] StartX=22.5 StartY=-12.5 StartZ=0 EndX=22.5 EndY=12.5 EndZ=0
    g2: LineSegment [constr] StartX=22.5 StartY=12.5 StartZ=0 EndX=-22.5 EndY=12.5 EndZ=0
    g3: LineSegment [constr] StartX=-22.5 StartY=12.5 StartZ=0 EndX=-22.5 EndY=-12.5 EndZ=0
    g4: GeomPoint [constr] X=0 Y=0 Z=0
    g5: Circle CenterX=22.5 CenterY=12.5 CenterZ=0 NormalX=0 NormalY=0 NormalZ=1 AngleXU=0 Radius=2.75
    g6: Circle CenterX=22.5 CenterY=-12.5 CenterZ=0 NormalX=0 NormalY=0 NormalZ=1 AngleXU=0 Radius=2.75
    g7: Circle CenterX=-22.5 CenterY=-12.5 CenterZ=0 NormalX=0 NormalY=0 NormalZ=1 AngleXU=0 Radius=2.75
    g8: Circle CenterX=-22.5 CenterY=12.5 CenterZ=0 NormalX=0 NormalY=0 NormalZ=1 AngleXU=0 Radius=2.75
  constraints (20):
    c: Coincident(g0,g1)
    c: Coincident(g1,g2)
    c: Coincident(g2,g3)
    c: Coincident(g3,g0)
    c: Horizontal(g0)
    c: Horizontal(g2)
    c: Vertical(g1)
    c: Vertical(g3)
    c: Symmetric(g2,g0,g4)
    c: Distance(g1,g3) = 45
    c: Distance(g0,g2) = 25
    c: Coincident(g4,g-1)
    c: Coincident(g5,g1)
    c: Coincident(g6,g0)
    c: Coincident(g7,g0)
    c: Coincident(g8,g2)
    c: Equal(g7,g8)
    c: Equal(g7,g5)
    c: Equal(g7,g6)
    c: Diameter(g7) = 5.5
FEATURE [Part::Extrusion] Extrude036
  Base = -> Sketch241
  Dir = (0,0,1)
  DirMode = 2
  FaceMakerClass = Part::FaceMakerBullseye
  FaceMakerMode = 3
  LengthFwd = 10
  LengthRev = 0
  Placement = pos=(0,0,-1) rot=(0,0,1;0rad)
  Solid = true
  Symmetric = false
FEATURE [Sketcher::SketchObject] Sketch242
  ArcFitTolerance = 0
  AttachmentOffset = pos=(0,35,0) rot=(0,0,1;0rad)
  AttachmentSupport = -> [Local_CS004]
  FullyConstrained = true
  MakeInternals = false
  MapMode = 5
  Placement = pos=(284.188,-181.72,35) rot=(-0.131421,0.700974,0.700974;3.40294rad)
  sketch-geometry (3):
    g0: Circle CenterX=-6.5 CenterY=0 CenterZ=0 NormalX=0 NormalY=0 NormalZ=1 AngleXU=0 Radius=1.7
    g1: GeomPoint [constr] X=-12 Y=0 Z=0
    g2: GeomPoint [constr] X=-1 Y=0 Z=0
  constraints (6):
    c: Diameter(g0) = 3.4
    c: PointOnObject(g1,g-1)
    c: PointOnObject(g2,g-1)
    c: DistanceX(g2) = -1
    c: DistanceX(g1) = -12
    c: Symmetric(g2,g1,g0)
FEATURE [PartDesign::Pocket] Pocket134
  BaseFeature = -> MultiTransform001
  Direction = (0.362233,-0.932087,0)
  Length = 5
  Length2 = 5
  Midplane = true
  Profile = -> Sketch242
  ReferenceAxis = -> Sketch242 [N_Axis]
  Suppressed = false
  Type = 1
FEATURE [PartDesign::LinearPattern] LinearPattern001
  Direction = -> Z_Axis097
  Length = 355
  Mode = 0
  Occurrences = 2
  Offset = 355
  Suppressed = false
  TransformMode = 0
FEATURE [PartDesign::Mirrored] Mirrored019
  MirrorPlane = -> YZ_Plane097
  Suppressed = false
  TransformMode = 0
FEATURE [PartDesign::MultiTransform] MultiTransform
  BaseFeature = -> Pocket134
  Originals = -> [Pocket134]
  Suppressed = false
  TransformMode = 0
  Transformations = -> [LinearPattern001,Mirrored019]
FEATURE [PartDesign::Body] Body121  label="sector_plexiglass_material_0.30ansi"
  AllowCompound = false
  Group = -> [Binder128,BaseBend049,Sketch208,Local_CS004,Pocket124,MultiTransform001,LinearPattern,Mirrored015,Sketch242,Pocket134,MultiTransform,LinearPattern001,Mirrored019]
  Origin = -> Origin097
  Tip = -> MultiTransform
FEATURE [Sketcher::SketchObject] Sketch246
  ArcFitTolerance = 0
  AttachmentSupport = -> [XY_Plane116]
  FullyConstrained = true
  MakeInternals = false
  MapMode = 5
  sketch-geometry (7):
    g0: LineSegment StartX=7.50555 StartY=0 StartZ=0 EndX=3.75278 EndY=6.5 EndZ=0
    g1: LineSegment StartX=3.75278 StartY=6.5 StartZ=0 EndX=-3.75278 EndY=6.5 EndZ=0
    g2: LineSegment StartX=-3.75278 StartY=6.5 StartZ=0 EndX=-7.50555 EndY=4.3228e-12 EndZ=0
    g3: LineSegment StartX=-7.50555 StartY=4.3229e-12 StartZ=0 EndX=-3.75278 EndY=-6.5 EndZ=0
    g4: LineSegment StartX=-3.75278 StartY=-6.5 StartZ=0 EndX=3.75278 EndY=-6.5 EndZ=0
    g5: LineSegment StartX=3.75278 StartY=-6.5 StartZ=0 EndX=7.50555 EndY=0 EndZ=0
    g6: Circle [constr] CenterX=0 CenterY=0 CenterZ=0 NormalX=0 NormalY=0 NormalZ=1 AngleXU=0 Radius=7.50555
  constraints (16):
    c: Coincident(g0,g1)
    c: Coincident(g1,g2)
    c: Coincident(g2,g3)
    c: Coincident(g3,g4)
    c: Coincident(g4,g5)
    c: Coincident(g5,g0)
    c: Equal(g0, g1-g5) x5
    c: PointOnObject(g0,g6)
    c: PointOnObject(g1,g6)
    c: PointOnObject(g2,g6)
    c: PointOnObject(g3,g6)
    c: PointOnObject(g4,g6)
    c: PointOnObject(g5,g6)
    c: Coincident(g6,g-1)
    c: PointOnObject(g5,g-1)
    c: DistanceY(g4,g0) = 13
FEATURE [PartDesign::Pad] Pad042
  Direction = (0,0,1)
  Length = 5
  Length2 = 10
  Profile = -> Sketch246
  ReferenceAxis = -> Sketch246 [N_Axis]
  Suppressed = false
  Type = 0
FEATURE [Sketcher::SketchObject] Sketch247
  ArcFitTolerance = 0
  AttachmentSupport = -> [XY_Plane116]
  FullyConstrained = true
  MakeInternals = false
  MapMode = 5
  sketch-geometry (1):
    g0: Circle CenterX=0 CenterY=0 CenterZ=0 NormalX=0 NormalY=0 NormalZ=1 AngleXU=0 Radius=4.25
  constraints (2):
    c: Coincident(g0,g-1)
    c: Diameter(g0) = 8.5
FEATURE [PartDesign::Pad] Pad043
  BaseFeature = -> Pad042
  Direction = (0,0,1)
  Length = 20
  Length2 = 10
  Profile = -> Sketch247
  ReferenceAxis = -> Sketch247 [N_Axis]
  Suppressed = false
  Type = 0
FEATURE [PartDesign::Body] Body139
  AllowCompound = false
  Group = -> [Sketch246,Pad042,Sketch247,Pad043]
  Origin = -> Origin117
  Placement = pos=(60,0,0) rot=(0,0,1;0rad)
  Tip = -> Pad043
  expr: .Placement.Base.x = <<bottom_bearing_Sketch>>.Constraints.outer_r + 10 mm
FEATURE [Part::FeaturePython] PolarArray010  # WARN: FeaturePython — macro-defined, semantics opaque (R4)
  Alignment = 0
  AttacherType = Attacher::AttachEngine3D
  CellStart = A1
  Count = 5
  DistributionLaw = 0
  EndInclusive = false
  ExposePlacement = false
  FlipX = false
  FlipZ = false
  GeneratorMode = 0
  MarkerShape = 1
  MarkerSize = 0
  NumElements = 5
  OrientMode = 2
  Placement = pos=(0,0,0) rot=(0,0,1;0.628319rad)
  Radius = 64
  Reverse = false
  SpanEnd = 360
  SpanStart = 0
  Step = 72
  Type = lattice2PolarArray2.PolarArray
  UseArcRadius = false
  UseArcRange = 0
  VSGVersion = 1
  Values = 0.0 | 72.0 | 144.0 | 216.0 | 288.0
  ValuesSource = 2
  isLattice = 1
  expr: .Placement.Rotation.Angle = 360 deg / (Count * 2)
  expr: Radius = <<bottom_bearing_Sketch>>.Constraints.outer_r + 14 mm
FEATURE [Part::Cylinder] Cylinder009  label="hole_4mm"
  Angle = 360
  AttacherType = Attacher::AttachEngine3D
  FirstAngle = 0
  Height = 40
  Radius = 2
  SecondAngle = 0
FEATURE [Part::FeaturePython] Populate054  label="Populate PolarArray010 with hole_4mm"  # WARN: FeaturePython — macro-defined, semantics opaque (R4)
  Copying = 0
  ExposePlacement = false
  MarkerShape = 1
  MarkerSize = 0
  NumElements = 0
  Object = -> Cylinder009
  OutputCompounding = 1
  PlacementsTo = -> PolarArray010
  Referencing = 0
  Type = lattice2PopulateCopies.LatticePopulateCopies
  isLattice = 0
FEATURE [Part::Cylinder] Cylinder010
  Angle = 360
  AttacherType = Attacher::AttachEngine3D
  FirstAngle = 0
  Height = 20
  Radius = 5.5
  SecondAngle = 0
FEATURE [Part::Cylinder] Cylinder011
  Angle = 360
  AttacherType = Attacher::AttachEngine3D
  FirstAngle = 0
  Height = 10
  Radius = 13.5
  SecondAngle = 0
FEATURE [Part::Cylinder] Cylinder012
  Angle = 360
  AttacherType = Attacher::AttachEngine3D
  FirstAngle = 0
  Height = 30
  Placement = pos=(8.9e-15,-145.633,0) rot=(0,0,1;0rad)
  Radius = 4.25
  SecondAngle = 0
  expr: .Placement.Base.x = 145.6327 * cos(-90 deg)
  expr: .Placement.Base.y = 145.6327 * sin(-90 deg)
FEATURE [PartDesign::Boolean] Boolean027
  BaseFeature = -> Pocket106
  Group = -> [Populate041,Cylinder012]
  Suppressed = false
  Type = 1
  UsePlacement = false
FEATURE [Part::Compound] Compound069  label="basement_bottom_cut1"
  Links = -> [Populate040,Populate033,Populate028,Extrude029,Extrude030,Populate045,Cylinder012]
FEATURE [PartDesign::Boolean] Boolean026
  BaseFeature = -> Pad002
  Group = -> [Compound069]
  Suppressed = false
  Type = 1
  UsePlacement = false
FEATURE [Part::Compound] Compound071  label="basement_bottom_proxy_cut1"
  Links = -> [Populate028,Extrude029,Extrude030,Cut,Cylinder012]
FEATURE [PartDesign::Boolean] Boolean029
  BaseFeature = -> Pad004
  Group = -> [Compound071]
  Suppressed = false
  Type = 1
  UsePlacement = false
FEATURE [Part::Offset2D] Offset2D
  Fill = false
  Intersection = false
  Join = 0
  Mode = 1
  SelfIntersection = false
  Source = -> Link040
  Value = 0.15
FEATURE [Part::Compound] Compound062  label="hub_top"
  Links = -> [Link039,Offset2D]
FEATURE [Part::Extrusion] Extrude026  label="hub_top_extrude"
  Base = -> Compound062
  Dir = (0,0,1)
  DirMode = 2
  FaceMakerClass = Part::FaceMakerBullseye
  FaceMakerMode = 3
  LengthFwd = 20
  LengthRev = 0
  Solid = true
  Symmetric = false
FEATURE [Sketcher::SketchObject] Sketch251
  ArcFitTolerance = 0
  FullyConstrained = true
  MakeInternals = false
  expr: Constraints[6] = <<pillar3_BaseBend>>.length - <<pillar3_hat_fix_placement>>.Placement.Base.z - 6 mm
  sketch-geometry (3):
    g0: LineSegment StartX=0 StartY=70 StartZ=0 EndX=1e-16 EndY=0 EndZ=0
    g1: LineSegment StartX=1e-16 StartY=0 StartZ=0 EndX=84 EndY=0 EndZ=0
    g2: LineSegment StartX=84 StartY=0 StartZ=0 EndX=84 EndY=30 EndZ=0
  constraints (9):
    c: PointOnObject(g0,g-2)
    c: Coincident(g0,g-1)
    c: Coincident(g0,g1)
    c: PointOnObject(g1,g-1)
    c: Coincident(g1,g2)
    c: Vertical(g2)
    c: Distance(g1) = 84
    c: DistanceY(g0,g0) = 70
    c: DistanceY(g2,g2) = 30
FEATURE [PartDesign::SubShapeBinder] Binder141
  BindCopyOnChange = 0
  BindMode = 0
  ClaimChildren = true
  Fuse = false
  MakeFace = true
  OffsetFill = false
  OffsetIntersection = false
  OffsetJoinType = 0
  OffsetOpenResult = false
  PartialLoad = false
  Relative = false
  Support = -> [Sketch008]
  _Version = 2
  expr: Support = <<pillar_base_sketch>>._self
FEATURE [PartDesign::FeaturePython] BaseBend052  label="pillar3_BaseBend"  # WARN: FeaturePython — macro-defined, semantics opaque (R4)
  BendSide = 1
  BendSketch = -> Binder141
  MidPlane = false
  Reverse = false
  Suppressed = false
  length = 1684
  radius = 2
  thickness = 2
FEATURE [Sketcher::SketchObject] Sketch252
  ArcFitTolerance = 0
  FullyConstrained = false
  MakeInternals = false
  expr: Constraints[7] = <<pillar_base_sketch>>.Constraints.width / 2 - 2 mm - 1.5 mm
  sketch-geometry (8):
    g0: LineSegment [constr] StartX=0 StartY=0 StartZ=0 EndX=112.583 EndY=65 EndZ=0
    g1: LineSegment StartX=112.583 StartY=65 StartZ=0 EndX=111.083 EndY=67.5981 EndZ=0
    g2: ArcOfCircle CenterX=343.601 CenterY=370 CenterZ=0 NormalX=0 NormalY=0 NormalZ=1 AngleXU=0 Radius=328.801 StartAngle=3.14159 EndAngle=3.34165
    g3: LineSegment StartX=14.8 StartY=370 StartZ=0 EndX=14.8 EndY=378 EndZ=0
    g4: LineSegment StartX=12.8 StartY=380 StartZ=0 EndX=0 EndY=380 EndZ=0
    g5: ArcOfCircle CenterX=12.8 CenterY=378 CenterZ=0 NormalX=0 NormalY=0 NormalZ=1 AngleXU=0 Radius=2 StartAngle=-8e-15 EndAngle=1.5708
    g6: GeomPoint [constr] X=14.8 Y=380 Z=0
    g7: ArcOfCircle CenterX=792.523 CenterY=461.028 CenterZ=0 NormalX=0 NormalY=0 NormalZ=1 AngleXU=0 Radius=786.859 StartAngle=3.34165 EndAngle=3.66519
  constraints (20):
    c: Coincident(g0,g-1)
    c: Coincident(g1,g0)
    c: Angle(g0) = 0.523599
    c: Perpendicular(g0,g1)
    c: Tangent(g3,g2) = 1.5708
    c: Vertical(g3)
    c: Distance(g1) = 3
    c: DistanceX(g2) = 14.8
    c: DistanceY(g2) = 370
    c: DistanceY(g3,g6) = 10
    c: PointOnObject(g4,g-2)
    c: Horizontal(g4)
    c: PointOnObject(g6,g3)
    c: PointOnObject(g6,g4)
    c: Tangent(g3,g5) = -1.5708
    c: Tangent(g4,g5) = -1.5708
    c: Radius(g5) = 2
    c: Distance(g0) = 130
    c: Tangent(g7,g1) = 1.5708
    c: Tangent(g7,g2) = -1.5708
FEATURE [Sketcher::SketchObject] Sketch253
  ArcFitTolerance = 0
  AttachmentSupport = -> [YZ_Plane121]
  ExternalGeometry = -> [Binder141]
  FullyConstrained = true
  MakeInternals = false
  MapMode = 5
  Placement = pos=(0,0,0) rot=(0.57735,0.57735,0.57735;2.0944rad)
  sketch-geometry (3):
    g0: LineSegment StartX=14 StartY=0 StartZ=0 EndX=19 EndY=0 EndZ=0
    g1: LineSegment StartX=19 StartY=0 StartZ=0 EndX=19 EndY=5 EndZ=0
    g2: ArcOfCircle CenterX=14 CenterY=5 CenterZ=0 NormalX=0 NormalY=0 NormalZ=1 AngleXU=0 Radius=5 StartAngle=4.71239 EndAngle=6.28319
  constraints (7):
    c: PointOnObject(g0,g-3)
    c: Coincident(g0,g-3)
    c: Coincident(g1,g0)
    c: Vertical(g1)
    c: Tangent(g2,g1) = -1.5708
    c: Tangent(g2,g0) = -1.5708
    c: Radius(g2) = 5
FEATURE [PartDesign::Pocket] Pocket137
  BaseFeature = -> BaseBend052
  Direction = (-1,0,0)
  Length = 5
  Length2 = 5
  Midplane = true
  Profile = -> Sketch253
  ReferenceAxis = -> Sketch253 [N_Axis]
  Suppressed = false
  Type = 1
FEATURE [PartDesign::SubShapeBinder] Binder142
  BindCopyOnChange = 0
  BindMode = 0
  ClaimChildren = true
  Context = -> Body142 [Binder142.]
  Fuse = false
  MakeFace = true
  OffsetFill = false
  OffsetIntersection = false
  OffsetJoinType = 0
  OffsetOpenResult = false
  PartialLoad = false
  Relative = true
  Support = -> [Connect005]
  _Version = 2
FEATURE [PartDesign::Pad] Pad045
  Direction = (0,0,1)
  Length = 3
  Length2 = 10
  Profile = -> Binder142
  Refine = true
  Suppressed = false
  Type = 0
FEATURE [Sketcher::SketchObject] Sketch254  label="hat3_border"
  ArcFitTolerance = 0
  FullyConstrained = true
  MakeInternals = false
  expr: Constraints[7] = 365
  sketch-geometry (7):
    g0: LineSegment [constr] StartX=0 StartY=0 StartZ=0 EndX=113.449 EndY=65.5 EndZ=0
    g1: LineSegment StartX=113.449 StartY=65.5 StartZ=0 EndX=111.949 EndY=68.0981 EndZ=0
    g2: ArcOfCircle CenterX=1199.51 CenterY=696.004 CenterZ=0 NormalX=0 NormalY=0 NormalZ=1 AngleXU=0 Radius=1255.81 StartAngle=3.57233 EndAngle=3.66519
    g3: GeomPoint [constr] X=14.8 Y=365 Z=0
    g4: LineSegment [constr] StartX=14.8 StartY=365 StartZ=0 EndX=14.8 EndY=0 EndZ=0
    g5: ArcOfCircle CenterX=464.8 CenterY=365 CenterZ=0 NormalX=0 NormalY=0 NormalZ=1 AngleXU=0 Radius=450 StartAngle=3.14159 EndAngle=3.57233
    g6: LineSegment StartX=58.4082 StartY=171.657 StartZ=0 EndX=55.903 EndY=177.109 EndZ=0
  constraints (18):
    c: Coincident(g-1,g0)
    c: Coincident(g0,g1)
    c: Angle(g0) = 0.523599
    c: Perpendicular(g1,g0)
    c: Distance(g0) = 131  'min_r'
    c: Distance(g1) = 3
    c: DistanceX(g3) = 14.8
    c: DistanceY(g3) = 365
    c: Coincident(g4,g3)
    c: PointOnObject(g4,g-1)
    c: Vertical(g4)
    c: Coincident(g5,g3)
    c: Tangent(g2,g1) = 1.5708
    c: Radius(g5) = 450
    c: Distance(g6) = 6
    c: Tangent(g6,g2) = 1.5708
    c: Tangent(g6,g5) = 1.5708
    c: Tangent(g5,g4)
FEATURE [Sketcher::SketchObject] Sketch255
  ArcFitTolerance = 0
  FullyConstrained = true
  MakeInternals = false
  expr: Constraints[3] = <<pillar_base_sketch>>.Constraints.width / 2 - 2 mm - 1.5 mm
  expr: Constraints[4] = <<pillar_placement>>.Placement.Base.y - <<pillar_base_sketch>>.Constraints.length
  expr: Constraints[7] = <<pillar_placement>>.Placement.Base.y - 15 mm
  sketch-geometry (4):
    g0: LineSegment StartX=0 StartY=369 StartZ=0 EndX=11.8 EndY=369 EndZ=0
    g1: LineSegment StartX=14.8 StartY=366 StartZ=0 EndX=14.8 EndY=365 EndZ=0
    g2: GeomPoint [constr] X=14.8 Y=369 Z=0
    g3: ArcOfCircle CenterX=11.8 CenterY=366 CenterZ=0 NormalX=0 NormalY=0 NormalZ=1 AngleXU=0 Radius=3 StartAngle=4.81e-14 EndAngle=1.5708
  constraints (11):
    c: Horizontal(g0)
    c: Vertical(g1)
    c: PointOnObject(g0,g-2)
    c: DistanceX(g1) = 14.8
    c: DistanceY(g1) = 365
    c: PointOnObject(g2,g0)
    c: PointOnObject(g2,g1)
    c: DistanceY(g0) = 369
    c: Tangent(g3,g0) = 1.5708
    c: Tangent(g3,g1) = 1.5708
    c: Radius(g3) = 3
FEATURE [Part::Compound] Compound093
  Links = -> [Sketch254,Sketch255]
FEATURE [Part::Mirroring] Part__Mirroring034  label="Sketch252 (Mirror #31)"
  Base = (0,0,0)
  Normal = (1,0,0)
  Source = -> Compound093
FEATURE [Part::Compound] Compound092
  Links = -> [Part__Mirroring034,Compound093]
FEATURE [Part::FeaturePython] Array013  # Draft array (typed FeaturePython)
  Angle = 360
  ArrayType = 1
  Axis = (0,0,1)
  Base = -> Compound092
  Center = (0,0,0)
  Count = 3
  Fuse = true
  IntervalAxis = (0,0,0)
  IntervalX = (50,0,0)
  IntervalY = (0,50,0)
  IntervalZ = (0,0,50)
  NumberCircles = 3
  NumberPolar = 3
  NumberX = 2
  NumberY = 2
  NumberZ = 1
  RadialDistance = 50
  Symmetry = 1
  TangentialDistance = 25
FEATURE [Part::FeaturePython] Connect005  # WARN: FeaturePython — macro-defined, semantics opaque (R4)
  Objects = -> [Array013]
  Tolerance = 0
FEATURE [PartDesign::SubShapeBinder] Binder143
  BindCopyOnChange = 0
  BindMode = 0
  ClaimChildren = true
  Fuse = false
  MakeFace = true
  OffsetFill = false
  OffsetIntersection = false
  OffsetJoinType = 0
  OffsetOpenResult = false
  PartialLoad = false
  Placement = pos=(0,0,0) rot=(0,-1,0;1.5708rad)
  Relative = false
  Support = -> [Sketch251]
  _Version = 2
FEATURE [PartDesign::FeaturePython] BaseBend053  label="pillar3_hat_fix_BaseBend"  # WARN: FeaturePython — macro-defined, semantics opaque (R4)
  BendSide = 1
  BendSketch = -> Binder143
  MidPlane = true
  Reverse = false
  Suppressed = false
  length = 28.6
  radius = 2
  thickness = 1.5
  expr: length = <<pillar_base_sketch>>.Constraints.width - 8 mm
FEATURE [Sketcher::SketchObject] Sketch256
  ArcFitTolerance = 0
  AttachmentSupport = -> [XY_Plane124]
  ExternalGeometry = -> [Binder143]
  FullyConstrained = true
  MakeInternals = false
  MapMode = 5
  expr: Constraints[12] = <<pillar3_hat_fix_BaseBend>>.length
  sketch-geometry (6):
    g0: LineSegment StartX=9.3 StartY=70 StartZ=0 EndX=14.3 EndY=70 EndZ=0
    g1: LineSegment StartX=14.3 StartY=70 StartZ=0 EndX=14.3 EndY=65 EndZ=0
    g2: LineSegment StartX=-14.3 StartY=65 StartZ=0 EndX=-14.3 EndY=70 EndZ=0
    g3: LineSegment StartX=-14.3 StartY=70 StartZ=0 EndX=-9.3 EndY=70 EndZ=0
    g4: ArcOfCircle CenterX=9.3 CenterY=65 CenterZ=0 NormalX=0 NormalY=0 NormalZ=1 AngleXU=0 Radius=5 StartAngle=4e-16 EndAngle=1.5708
    g5: ArcOfCircle CenterX=-9.3 CenterY=65 CenterZ=0 NormalX=0 NormalY=0 NormalZ=1 AngleXU=0 Radius=5 StartAngle=1.5708 EndAngle=3.14159
  constraints (15):
    c: Coincident(g0,g1)
    c: Coincident(g2,g3)
    c: Tangent(g5,g2) = 1.5708
    c: Tangent(g5,g3) = 1.5708
    c: Tangent(g4,g1) = 1.5708
    c: Tangent(g4,g0) = 1.5708
    c: Equal(g4,g5)
    c: Radius(g5) = 5
    c: Parallel(g1,g-3)
    c: Perpendicular(g-3,g0)
    c: Perpendicular(g-3,g3)
    c: Parallel(g2,g-3)
    c: DistanceX(g2,g0) = 28.6
    c: Horizontal(g2,g0)
    c: Symmetric(g0,g2,g-3)
FEATURE [Sketcher::SketchObject] Sketch257
  ArcFitTolerance = 0
  AttachmentOffset = pos=(0,0,4) rot=(0,0,1;0rad)
  AttachmentSupport = -> [XY_Plane124]
  ExternalGeometry = -> [Binder143]
  FullyConstrained = true
  MakeInternals = false
  MapMode = 5
  Placement = pos=(0,0,4) rot=(0,0,1;0rad)
  expr: Constraints[13] = <<pillar3_hat_fix_BaseBend>>.length
  sketch-geometry (6):
    g0: LineSegment StartX=9.3 StartY=30 StartZ=0 EndX=14.3 EndY=30 EndZ=0
    g1: LineSegment StartX=14.3 StartY=30 StartZ=0 EndX=14.3 EndY=25 EndZ=0
    g2: LineSegment StartX=-14.3 StartY=25 StartZ=0 EndX=-14.3 EndY=30 EndZ=0
    g3: LineSegment StartX=-14.3 StartY=30 StartZ=0 EndX=-9.3 EndY=30 EndZ=0
    g4: ArcOfCircle CenterX=9.3 CenterY=25 CenterZ=0 NormalX=0 NormalY=0 NormalZ=1 AngleXU=0 Radius=5 StartAngle=3e-16 EndAngle=1.5708
    g5: ArcOfCircle CenterX=-9.3 CenterY=25 CenterZ=0 NormalX=0 NormalY=0 NormalZ=1 AngleXU=0 Radius=5 StartAngle=1.5708 EndAngle=3.14159
  constraints (15):
    c: Coincident(g0,g1)
    c: Coincident(g2,g3)
    c: Tangent(g5,g2) = 1.5708
    c: Tangent(g5,g3) = 1.5708
    c: Tangent(g4,g1) = 1.5708
    c: Tangent(g4,g0) = 1.5708
    c: Equal(g4,g5)
    c: Radius(g4) = 5
    c: Symmetric(g2,g0,g-3)
    c: Parallel(g2,g-3)
    c: Parallel(g-3,g1)
    c: Perpendicular(g0,g1)
    c: Horizontal(g0,g-3)
    c: DistanceX(g2,g0) = 28.6
    c: Perpendicular(g-3,g3)
FEATURE [PartDesign::CoordinateSystem] Local_CS005
  AttacherType = Attacher::AttachEngine3D
  AttachmentSupport = -> [XY_Plane124]
  MapMode = 5
FEATURE [PartDesign::CoordinateSystem] Local_CS006  label="pillar3_base"
  AttacherType = Attacher::AttachEngine3D
  AttachmentSupport = -> [XY_Plane121]
  MapMode = 5
FEATURE [PartDesign::CoordinateSystem] Local_CS007  label="pillar3_hat_fix_Local_CS"
  AttacherType = Attacher::AttachEngine3D
  AttachmentOffset = pos=(0,2,1594) rot=(0,0,1;0rad)
  AttachmentSupport = -> [XY_Plane121]
  MapMode = 5
  Placement = pos=(0,2,1594) rot=(0,0,1;0rad)
  expr: AttachmentOffset = <<pillar3_hat_fix_placement>>.Placement
FEATURE [Sketcher::SketchObject] Sketch258
  ArcFitTolerance = 0
  FullyConstrained = true
  MakeInternals = false
  sketch-geometry (2):
    g0: Circle CenterX=0 CenterY=10 CenterZ=0 NormalX=0 NormalY=0 NormalZ=1 AngleXU=0 Radius=1.7
    g1: Circle CenterX=0 CenterY=78 CenterZ=0 NormalX=0 NormalY=0 NormalZ=1 AngleXU=0 Radius=1.7
  constraints (6):
    c: PointOnObject(g0,g-2)
    c: PointOnObject(g1,g-2)
    c: Equal(g1,g0)
    c: Diameter(g1) = 3.4
    c: DistanceY(g0) = 10
    c: DistanceY(g1) = 78
FEATURE [Part::Extrusion] Extrude037
  Base = -> Sketch258
  Dir = (0,0,1)
  DirMode = 2
  FaceMakerClass = Part::FaceMakerBullseye
  FaceMakerMode = 3
  LengthFwd = 10
  LengthRev = 0
  Solid = true
  Symmetric = true
FEATURE [Part::FeaturePython] Placment033  # WARN: FeaturePython — macro-defined, semantics opaque (R4)
  AttacherType = Attacher::AttachEngine3D
  ExposePlacement = true
  MarkerShape = 1
  MarkerSize = 5
  NumElements = 1
  Placement = pos=(0,0,0) rot=(0,0.707107,0.707107;3.14159rad)
  Type = lattice2AttachablePlacement.AttachablePlacement
  isLattice = 1
FEATURE [Part::FeaturePython] Populate055  label="Populate Placment033 with Extrude037"  # WARN: FeaturePython — macro-defined, semantics opaque (R4)
  Copying = 0
  ExposePlacement = false
  MarkerShape = 1
  MarkerSize = 0
  NumElements = 0
  Object = -> Extrude037
  OutputCompounding = 2
  PlacementsTo = -> Placment033
  Referencing = 0
  Type = lattice2PopulateCopies.LatticePopulateCopies
  isLattice = 0
FEATURE [PartDesign::Plane] DatumPlane007
  AttachmentOffset = pos=(0,0,842) rot=(0,0,1;0rad)
  AttachmentSupport = -> [XY_Plane121]
  Length = 60
  MapMode = 5
  Placement = pos=(0,0,842) rot=(0,0,1;0rad)
  ResizeMode = 0
  Width = 60
  expr: .AttachmentOffset.Base.z = <<pillar3_BaseBend>>.length / 2
FEATURE [PartDesign::Mirrored] Mirrored020
  BaseFeature = -> Pocket137
  MirrorPlane = -> DatumPlane007
  Originals = -> [Pocket137]
  Suppressed = false
  TransformMode = 0
FEATURE [Sketcher::SketchObject] Sketch259
  ArcFitTolerance = 0
  FullyConstrained = true
  MakeInternals = false
FEATURE [PartDesign::SubShapeBinder] Binder144
  BindCopyOnChange = 0
  BindMode = 0
  ClaimChildren = true
  Context = -> Body145 [Binder144.]
  Fuse = false
  MakeFace = true
  OffsetFill = false
  OffsetIntersection = false
  OffsetJoinType = 0
  OffsetOpenResult = false
  PartialLoad = false
  Relative = true
  Support = -> [Sketch056]
  _Version = 2
  expr: Support = <<pillar_dec_corner_base_sketch>>._self
FEATURE [PartDesign::FeaturePython] BaseBend054  label="pillar3_dec_corner_BaseBend"  # WARN: FeaturePython — macro-defined, semantics opaque (R4)
  BendSide = 0
  BendSketch = -> Binder144
  MidPlane = false
  Reverse = false
  Suppressed = false
  length = 1214
  radius = 2
  thickness = 0.5
  expr: length = <<pillar3_BaseBend>>.length - <<pillar3_dec_corner_placement>>.Placement.Base.z
FEATURE [Sketcher::SketchObject] Sketch260
  ArcFitTolerance = 0
  AttachmentSupport = -> [XZ_Plane125]
  ExternalGeometry = -> [Binder144]
  FullyConstrained = true
  MakeInternals = false
  MapMode = 5
  Placement = pos=(0,0,0) rot=(1,0,0;1.5708rad)
  sketch-geometry (3):
    g0: LineSegment StartX=13.3 StartY=0 StartZ=0 EndX=18.3 EndY=-3e-16 EndZ=0
    g1: LineSegment StartX=18.3 StartY=-3e-16 StartZ=0 EndX=18.3 EndY=5 EndZ=0
    g2: ArcOfCircle CenterX=13.3 CenterY=5 CenterZ=0 NormalX=0 NormalY=0 NormalZ=1 AngleXU=0 Radius=5 StartAngle=4.71239 EndAngle=6.28319
  constraints (7):
    c: PointOnObject(g0,g-3)
    c: Coincident(g0,g-3)
    c: Coincident(g0,g1)
    c: Vertical(g1)
    c: Tangent(g2,g1) = -1.5708
    c: Tangent(g2,g0) = -1.5708
    c: Radius(g2) = 5
FEATURE [Sketcher::SketchObject] Sketch261
  ArcFitTolerance = 0
  AttachmentSupport = -> [YZ_Plane125]
  ExternalGeometry = -> [Binder144]
  FullyConstrained = true
  MakeInternals = false
  MapMode = 5
  Placement = pos=(0,0,0) rot=(0.57735,0.57735,0.57735;2.0944rad)
  sketch-geometry (3):
    g0: LineSegment StartX=14 StartY=9e-16 StartZ=0 EndX=19 EndY=0 EndZ=0
    g1: LineSegment StartX=19 StartY=0 StartZ=0 EndX=19 EndY=5 EndZ=0
    g2: ArcOfCircle CenterX=14 CenterY=5 CenterZ=0 NormalX=0 NormalY=0 NormalZ=1 AngleXU=0 Radius=5 StartAngle=4.71239 EndAngle=6.28319
  constraints (7):
    c: PointOnObject(g0,g-3)
    c: Coincident(g0,g-3)
    c: Coincident(g0,g1)
    c: Vertical(g1)
    c: Tangent(g2,g1) = -1.5708
    c: Tangent(g2,g0) = -1.5708
    c: Radius(g2) = 5
FEATURE [PartDesign::Pocket] Pocket140
  BaseFeature = -> BaseBend054
  Direction = (0,1,-2e-16)
  Length = 5
  Length2 = 5
  Midplane = true
  Profile = -> Sketch260
  ReferenceAxis = -> Sketch260 [N_Axis]
  Suppressed = false
  Type = 1
FEATURE [PartDesign::Pocket] Pocket141
  BaseFeature = -> Pocket140
  Direction = (-1,0,0)
  Length = 5
  Length2 = 5
  Midplane = true
  Profile = -> Sketch261
  ReferenceAxis = -> Sketch261 [N_Axis]
  Suppressed = false
  Type = 1
FEATURE [PartDesign::Plane] DatumPlane008
  AttachmentOffset = pos=(0,0,607) rot=(0,0,1;0rad)
  AttachmentSupport = -> [XY_Plane125]
  Length = 60
  MapMode = 5
  Placement = pos=(0,0,607) rot=(0,0,1;0rad)
  ResizeMode = 0
  Width = 60
  expr: .AttachmentOffset.Base.z = <<pillar3_dec_corner_BaseBend>>.length / 2
FEATURE [PartDesign::Mirrored] Mirrored021
  BaseFeature = -> Pocket141
  MirrorPlane = -> DatumPlane008
  Originals = -> [Pocket140,Pocket141]
  Suppressed = false
  TransformMode = 0
FEATURE [Part::FeaturePython] Placment034  label="pillar3_hat_fix_placement"  # WARN: FeaturePython — macro-defined, semantics opaque (R4)
  AttacherType = Attacher::AttachEngine3D
  ExposePlacement = true
  MarkerShape = 1
  MarkerSize = 50
  NumElements = 1
  Placement = pos=(0,2,1594) rot=(0,0,1;0rad)
  Type = lattice2AttachablePlacement.AttachablePlacement
  isLattice = 1
  expr: .Placement.Base.z = <<pillar3_Properties>>.hat_offset
FEATURE [Part::FeaturePython] Placment035  label="pillar3_dec_corner_placement"  # WARN: FeaturePython — macro-defined, semantics opaque (R4)
  AttacherType = Attacher::AttachEngine3D
  ExposePlacement = true
  MarkerShape = 1
  MarkerSize = 50
  NumElements = 1
  Placement = pos=(0,0,470) rot=(0,0,1;0rad)
  Type = lattice2AttachablePlacement.AttachablePlacement
  isLattice = 1
FEATURE [PartDesign::SubShapeBinder] Binder145
  BindCopyOnChange = 0
  BindMode = 0
  ClaimChildren = true
  Context = -> Body146 [Binder145.]
  Fuse = false
  MakeFace = true
  OffsetFill = false
  OffsetIntersection = false
  OffsetJoinType = 0
  OffsetOpenResult = false
  PartialLoad = false
  Relative = false
  Support = -> [Connect006]
  _Version = 2
FEATURE [PartDesign::FeaturePython] BaseBend055  # WARN: FeaturePython — macro-defined, semantics opaque (R4)
  BendSide = 1
  BendSketch = -> Binder145
  MidPlane = false
  Reverse = false
  Suppressed = false
  length = 100
  radius = 1
  thickness = 1.5
FEATURE [Sketcher::SketchObject] Sketch262
  ArcFitTolerance = 0
  FullyConstrained = true
  MakeInternals = false
  expr: Constraints[1] = <<pillar_placement>>.Placement.Base.y - 4 mm
  expr: Constraints[2] = <<pillar_placement>>.Placement.Base.y - <<pillar_base_sketch>>.Constraints.length
  expr: Constraints[3] = <<pillar_base_sketch>>.Constraints.width / 2 - 2 mm - 1.5 mm
  sketch-geometry (1):
    g0: LineSegment StartX=14.8 StartY=365 StartZ=0 EndX=14.8 EndY=380 EndZ=0
  constraints (4):
    c: Vertical(g0)
    c: DistanceY(g0) = 380
    c: DistanceY(g0) = 365
    c: DistanceX(g0) = 14.8
FEATURE [Part::Compound] Compound095
  Links = -> [Sketch254,Sketch262]
FEATURE [Part::Mirroring] Part__Mirroring035  label="hat3_border (Mirror #32)"
  Base = (0,0,0)
  Normal = (-0.5,0.866025,0)
  Source = -> Compound095
  expr: .Normal.x = cos(120 deg)
  expr: .Normal.y = sin(120)
FEATURE [Part::FeaturePython] Connect006  # WARN: FeaturePython — macro-defined, semantics opaque (R4)
  Objects = -> [Part__Mirroring035,Compound095]
  Tolerance = 0
FEATURE [PartDesign::FeaturePython] Extend002  # WARN: FeaturePython — macro-defined, semantics opaque (R4)
  BaseFeature = -> BaseBend055
  Offset = 0.02
  Refine = true
  Suppressed = false
  UseSubtraction = false
  baseObject = -> BaseBend055 [Face1]
  gap1 = 0
  gap2 = 0
  length = 0
FEATURE [Part::FeaturePython] Placment036  label="hat3_pillar_fix_placement"  # WARN: FeaturePython — macro-defined, semantics opaque (R4)
  AttacherType = Attacher::AttachEngine3D
  ExposePlacement = true
  MarkerShape = 1
  MarkerSize = 50
  NumElements = 1
  Placement = pos=(18.8,372,10) rot=(0,0,1;0rad)
  Type = lattice2AttachablePlacement.AttachablePlacement
  isLattice = 1
  expr: .Placement.Base.x = <<pillar_base_sketch>>.Constraints.width / 2 + 0.5 mm
  expr: .Placement.Base.y = <<pillar_placement>>.Placement.Base.y - 4 mm - 8 mm
FEATURE [Part::FeaturePython] Mirror013  label="Mirror013 of hat3_pillar_fix_placement"  # WARN: FeaturePython — macro-defined, semantics opaque (R4)
  ExposePlacement = false
  FlipX = false
  FlipY = true
  FlipZ = false
  MarkerShape = 1
  MarkerSize = 100
  NumElements = 1
  Object = -> Placment036
  ObjectTraversal = 0
  PivotPlacement = pos=(0,0,0) rot=(0,0,1;0.523599rad)
  Type = lattice2Mirror.LatticeMirror
  isLattice = 1
FEATURE [Part::FeaturePython] Join015  # WARN: FeaturePython — macro-defined, semantics opaque (R4)
  ExposePlacement = false
  Interleave = false
  Links = -> [Mirror013,Placment036]
  MarkerShape = 1
  MarkerSize = 0
  NumElements = 2
  Type = lattice2JoinArrays.JoinArrays
  isLattice = 1
FEATURE [Part::FeaturePython] LinearArray016  # WARN: FeaturePython — macro-defined, semantics opaque (R4)
  Alignment = 0
  CellStart = A1
  Count = 2
  Dir = (1,0,0)
  DirIsDriven = true
  DistributionLaw = 0
  DrivenProperty = 1
  EndInclusive = true
  ExposePlacement = false
  GeneratorMode = 0
  MarkerShape = 1
  MarkerSize = 0
  NumElements = 2
  OrientMode = 1
  Placement = pos=(0,0,0) rot=(0,-1,0;1.5708rad)
  Point = (0,0,0)
  PointIsDriven = true
  Reverse = false
  SpanEnd = 80
  SpanStart = 10
  Step = 70
  Type = lattice2LinearArray.LinearArray
  VSGVersion = 1
  Values = 10.0 | 80.0
  ValuesSource = 2
  isLattice = 1
  expr: SpanEnd = <<pillar3_Properties>>.hat_height - 10 mm
FEATURE [Part::FeaturePython] Populate056  label="Populate Join015 with LinearArray016"  # WARN: FeaturePython — macro-defined, semantics opaque (R4)
  Copying = 0
  ExposePlacement = false
  MarkerShape = 1
  MarkerSize = 0
  NumElements = 4
  Object = -> LinearArray016
  OutputCompounding = 0
  PlacementsTo = -> Join015
  Referencing = 0
  Type = lattice2PopulateCopies.LatticePopulateCopies
  isLattice = 1
FEATURE [Part::FeaturePython] Populate057  label="Populate Populate Join015 with LinearArray016 with hole_3.4mm_extrude"  # WARN: FeaturePython — macro-defined, semantics opaque (R4)
  Copying = 0
  ExposePlacement = false
  MarkerShape = 1
  MarkerSize = 0
  NumElements = 0
  Object = -> Extrude019
  OutputCompounding = 1
  PlacementsTo = -> Populate056
  Referencing = 0
  Type = lattice2PopulateCopies.LatticePopulateCopies
  isLattice = 0
FEATURE [Part::Compound] Compound096
  Links = -> [Populate057]
FEATURE [PartDesign::Boolean] Boolean047
  BaseFeature = -> Extend002
  Group = -> [Compound096]
  Suppressed = false
  Type = 1
  UsePlacement = true
FEATURE [Sketcher::SketchObject] Sketch263  label="hat3_top_base_sketch"
  ArcFitTolerance = 0
  FullyConstrained = false
  MakeInternals = false
  expr: Constraints[12] = <<hat3_border>>.Constraints.min_r - 5 mm
  expr: Constraints[5] = <<pillar_base_sketch>>.Constraints.width / 2 - 2 mm - 1.5 mm - 0.2 mm
  expr: Constraints[6] = <<pillar_placement>>.Placement.Base.y - <<pillar_base_sketch>>.Constraints.length
  expr: Constraints[8] = <<pillar_placement>>.Placement.Base.y - 5 mm
  sketch-geometry (7):
    g0: LineSegment StartX=0 StartY=379 StartZ=0 EndX=9.6 EndY=379 EndZ=0
    g1: LineSegment StartX=14.6 StartY=374 StartZ=0 EndX=14.6 EndY=365 EndZ=0
    g2: ArcOfCircle CenterX=1008.94 CenterY=582.513 CenterZ=0 NormalX=0 NormalY=0 NormalZ=1 AngleXU=0 Radius=1039.03 StartAngle=3.54682 EndAngle=3.66519
    g3: ArcOfCircle CenterX=501.877 CenterY=365 CenterZ=0 NormalX=0 NormalY=0 NormalZ=1 AngleXU=0 Radius=487.277 StartAngle=3.14159 EndAngle=3.54682
    g4: LineSegment [constr] StartX=0 StartY=0 StartZ=0 EndX=109.119 EndY=63 EndZ=0
    g5: ArcOfCircle CenterX=9.6 CenterY=374 CenterZ=0 NormalX=0 NormalY=0 NormalZ=1 AngleXU=0 Radius=5 StartAngle=-5.3e-15 EndAngle=1.5708
    g6: GeomPoint [constr] X=14.6 Y=379 Z=0
  constraints (18):
    c: Horizontal(g0)
    c: Vertical(g1)
    c: Coincident(g-1,g4)
    c: Coincident(g4,g2)
    c: Angle(g4) = 0.523599
    c: DistanceX(g1) = 14.6
    c: DistanceY(g1) = 365
    c: PointOnObject(g0,g-2)
    c: DistanceY(g6) = 379
    c: Tangent(g3,g1) = -1.5708
    c: Tangent(g3,g2) = -1.5708
    c: Perpendicular(g2,g4)
    c: Distance(g4) = 126
    c: PointOnObject(g6,g0)
    c: PointOnObject(g6,g1)
    c: Tangent(g0,g5) = 1.5708
    c: Tangent(g1,g5) = 1.5708
    c: Radius(g5) = 5
FEATURE [Part::Mirroring] Part__Mirroring036  label="hat3_top_base_sketch (Mirror #33)"
  Base = (0,0,0)
  Normal = (1,0,0)
  Source = -> Sketch263
FEATURE [Part::Compound] Compound097
  Links = -> [Part__Mirroring036,Sketch263]
FEATURE [Part::FeaturePython] Array014  # Draft array (typed FeaturePython)
  Angle = 360
  ArrayType = 1
  Axis = (0,0,1)
  Base = -> Compound097
  Center = (0,0,0)
  Count = 3
  Fuse = true
  IntervalAxis = (0,0,0)
  IntervalX = (50,0,0)
  IntervalY = (0,50,0)
  IntervalZ = (0,0,50)
  NumberCircles = 3
  NumberPolar = 3
  NumberX = 2
  NumberY = 2
  NumberZ = 1
  RadialDistance = 50
  Symmetry = 1
  TangentialDistance = 25
FEATURE [Part::FeaturePython] Connect007  # WARN: FeaturePython — macro-defined, semantics opaque (R4)
  Objects = -> [Array014]
  Tolerance = 0
FEATURE [PartDesign::SubShapeBinder] Binder146
  BindCopyOnChange = 0
  BindMode = 0
  ClaimChildren = true
  Context = -> Body143 [Binder146.]
  Fuse = false
  MakeFace = true
  OffsetFill = false
  OffsetIntersection = false
  OffsetJoinType = 0
  OffsetOpenResult = false
  PartialLoad = false
  Relative = false
  Support = -> [Connect007]
  _Version = 2
FEATURE [PartDesign::CoordinateSystem] Local_CS008  label="pilllar3_dec_corner_base_local_cs"
  AttacherType = Attacher::AttachEngine3D
  AttachmentSupport = -> [XY_Plane125]
  MapMode = 5
FEATURE [Part::FeaturePython] Placment037  # WARN: FeaturePython — macro-defined, semantics opaque (R4)
  AttacherType = Attacher::AttachEngine3D
  ExposePlacement = true
  MarkerShape = 1
  MarkerSize = 20
  NumElements = 1
  Placement = pos=(-18.8,10,0) rot=(0,0,1;0rad)
  Type = lattice2AttachablePlacement.AttachablePlacement
  isLattice = 1
  expr: .Placement.Base.x = -(<<pillar_base_sketch>>.Constraints.width / 2 + 0.5 mm)
FEATURE [Part::FeaturePython] LinearArray017  label="dec_corner_pillar_fix"  # WARN: FeaturePython — macro-defined, semantics opaque (R4)
  Alignment = 0
  CellStart = A1
  Count = 5
  Dir = (1,0,0)
  DirIsDriven = true
  DistributionLaw = 0
  DrivenProperty = 1
  EndInclusive = true
  ExposePlacement = false
  GeneratorMode = 0
  MarkerShape = 1
  MarkerSize = 0
  NumElements = 5
  OrientMode = 1
  Placement = pos=(0,0,0) rot=(0.707107,0,0.707107;3.14159rad)
  Point = (0,0,0)
  PointIsDriven = true
  Reverse = false
  SpanEnd = 1104
  SpanStart = 20
  Step = 271
  Type = lattice2LinearArray.LinearArray
  VSGVersion = 1
  Values = 20.0 | 291.0 | 562.0 | 833.0 | 1104.0
  ValuesSource = 2
  isLattice = 1
  expr: SpanEnd = <<pillar3_hat_fix_placement>>.Placement.Base.z - <<pillar3_dec_corner_placement>>.Placement.Base.z - 20 mm
FEATURE [PartDesign::CoordinateSystem] Local_CS009  label="pillar3_dec_corner_LCS"
  AttacherType = Attacher::AttachEngine3D
  AttachmentOffset = pos=(0,0,470) rot=(0,0,1;0rad)
  AttachmentSupport = -> [XY_Plane121]
  MapMode = 5
  Placement = pos=(0,0,470) rot=(0,0,1;0rad)
  expr: AttachmentOffset = <<pillar3_dec_corner_placement>>.Placement
FEATURE [Part::FeaturePython] Populate058  label="Populate Placment037 with dec_corner_pillar_fix"  # WARN: FeaturePython — macro-defined, semantics opaque (R4)
  Copying = 0
  ExposePlacement = false
  MarkerShape = 1
  MarkerSize = 0
  NumElements = 5
  Object = -> LinearArray017
  OutputCompounding = 0
  PlacementsTo = -> Placment037
  Referencing = 0
  Type = lattice2PopulateCopies.LatticePopulateCopies
  isLattice = 1
FEATURE [Part::FeaturePython] Populate060  label="Populate Populate Placment037 with dec_corner_pillar_fix with hole_3.4mm_extrude"  # WARN: FeaturePython — macro-defined, semantics opaque (R4)
  Copying = 0
  ExposePlacement = false
  MarkerShape = 1
  MarkerSize = 0
  NumElements = 0
  Object = -> Extrude019
  OutputCompounding = 1
  PlacementsTo = -> Populate058
  Referencing = 0
  Type = lattice2PopulateCopies.LatticePopulateCopies
  isLattice = 0
FEATURE [Part::FeaturePython] Populate062  label="Populate pillar3_hat_fix_placement with Populate Placment033 with Extrude037"  # WARN: FeaturePython — macro-defined, semantics opaque (R4)
  Copying = 0
  ExposePlacement = false
  MarkerShape = 1
  MarkerSize = 0
  NumElements = 0
  Object = -> Populate055
  OutputCompounding = 2
  PlacementsTo = -> Placment034
  Referencing = 0
  Type = lattice2PopulateCopies.LatticePopulateCopies
  isLattice = 0
FEATURE [Part::FeaturePython] Placment038  # WARN: FeaturePython — macro-defined, semantics opaque (R4)
  AttacherType = Attacher::AttachEngine3D
  ExposePlacement = true
  MarkerShape = 1
  MarkerSize = 10
  NumElements = 1
  Placement = pos=(18.8,10,0) rot=(0,0,1;0rad)
  Type = lattice2AttachablePlacement.AttachablePlacement
  isLattice = 1
  expr: .Placement.Base.x = <<pillar_base_sketch>>.Constraints.width / 2 + 0.5 mm
FEATURE [Part::FeaturePython] Mirror014  label="Mirror014 of Placment038"  # WARN: FeaturePython — macro-defined, semantics opaque (R4)
  ExposePlacement = false
  FlipX = true
  FlipY = false
  FlipZ = false
  MarkerShape = 1
  MarkerSize = 50
  NumElements = 1
  Object = -> Placment038
  ObjectTraversal = 0
  Type = lattice2Mirror.LatticeMirror
  isLattice = 1
FEATURE [Part::FeaturePython] Join016  # WARN: FeaturePython — macro-defined, semantics opaque (R4)
  ExposePlacement = false
  Interleave = false
  Links = -> [Mirror014,Placment038]
  MarkerShape = 1
  MarkerSize = 0
  NumElements = 2
  Type = lattice2JoinArrays.JoinArrays
  isLattice = 1
FEATURE [Part::FeaturePython] Populate063  label="Populate Join016 with LinearArray016"  # WARN: FeaturePython — macro-defined, semantics opaque (R4)
  Copying = 0
  ExposePlacement = false
  MarkerShape = 1
  MarkerSize = 0
  NumElements = 4
  Object = -> LinearArray016
  OutputCompounding = 0
  PlacementsTo = -> Join016
  Referencing = 0
  Type = lattice2PopulateCopies.LatticePopulateCopies
  isLattice = 1
FEATURE [Part::FeaturePython] Populate067  label="Populate pillar3_hat_fix_placement with Populate Join016 with LinearArray016"  # WARN: FeaturePython — macro-defined, semantics opaque (R4)
  Copying = 0
  ExposePlacement = false
  MarkerShape = 1
  MarkerSize = 0
  NumElements = 4
  Object = -> Populate063
  OutputCompounding = 0
  PlacementsTo = -> Placment034
  Referencing = 0
  Type = lattice2PopulateCopies.LatticePopulateCopies
  isLattice = 1
FEATURE [Part::FeaturePython] Populate064  label="Populate Populate Join016 with LinearArray016 with hole_3.4mm_extrude"  # WARN: FeaturePython — macro-defined, semantics opaque (R4)
  Copying = 0
  ExposePlacement = false
  MarkerShape = 1
  MarkerSize = 0
  NumElements = 0
  Object = -> Extrude019
  OutputCompounding = 1
  PlacementsTo = -> Populate067
  Referencing = 0
  Type = lattice2PopulateCopies.LatticePopulateCopies
  isLattice = 0
FEATURE [Part::FeaturePython] LinearArray018  # WARN: FeaturePython — macro-defined, semantics opaque (R4)
  Alignment = 0
  CellStart = A1
  Count = 5
  Dir = (1,0,0)
  DirIsDriven = true
  DistributionLaw = 0
  DrivenProperty = 1
  EndInclusive = true
  ExposePlacement = false
  GeneratorMode = 0
  MarkerShape = 1
  MarkerSize = 0
  NumElements = 5
  OrientMode = 1
  Placement = pos=(0,-2,470) rot=(0.57735,0.57735,0.57735;4.18879rad)
  Point = (0,0,0)
  PointIsDriven = true
  Reverse = false
  SpanEnd = 1104
  SpanStart = 20
  Step = 271
  Type = lattice2LinearArray.LinearArray
  VSGVersion = 1
  Values = 20.0 | 291.0 | 562.0 | 833.0 | 1104.0
  ValuesSource = 2
  isLattice = 1
  expr: .Placement.Base.z = <<pillar3_Properties>>.dec_corner_offset
  expr: SpanEnd = <<pillar3_Properties>>.dec_corner_height - <<pillar3_Properties>>.hat_height - 20 mm
FEATURE [Spreadsheet::Sheet] Spreadsheet005  label="pillar3_Properties"
  cells = B2(total_height)==1684 mm; C2(dec_corner_height)==total_height - dec_corner_offset; D2(dec_corner_offset)==470 mm; E2(hat_offset)==total_height - hat_height; F2(hat_height)==90 mm; G2(width)=36.6; H2(length)=
FEATURE [Part::Compound] Compound101  label="pillar3_hat_fix_common"
FEATURE [PartDesign::SubShapeBinder] Binder147
  BindCopyOnChange = 0
  BindMode = 0
  ClaimChildren = false
  Fuse = false
  MakeFace = false
  OffsetFill = false
  OffsetIntersection = false
  OffsetJoinType = 0
  OffsetOpenResult = false
  PartialLoad = false
  Relative = true
  Support = -> [<external ULZ-P02-14W.FCStd>#Sketch]
  _Version = 2
FEATURE [Sketcher::SketchObject] Sketch264
  ArcFitTolerance = 0
  ExternalGeometry = -> [Binder147]
  FullyConstrained = true
  MakeInternals = false
  sketch-geometry (6):
    g0: ArcOfCircle CenterX=4.15 CenterY=-445.9 CenterZ=0 NormalX=0 NormalY=0 NormalZ=1 AngleXU=0 Radius=1.6 StartAngle=3.14159 EndAngle=6.28319
    g1: ArcOfCircle CenterX=4.15 CenterY=-444.1 CenterZ=0 NormalX=0 NormalY=0 NormalZ=1 AngleXU=0 Radius=1.6 StartAngle=1.21e-14 EndAngle=3.14159
    g2: LineSegment StartX=2.55 StartY=-445.9 StartZ=0 EndX=2.55 EndY=-444.1 EndZ=0
    g3: LineSegment StartX=5.75 StartY=-445.9 StartZ=0 EndX=5.75 EndY=-444.1 EndZ=0
    g4: LineSegment [constr] StartX=4.15 StartY=-442.5 StartZ=0 EndX=4.15 EndY=-447.5 EndZ=0
    g5: Circle CenterX=-4.15 CenterY=445 CenterZ=0 NormalX=0 NormalY=0 NormalZ=1 AngleXU=0 Radius=1.6
  constraints (15):
    c: Tangent(g0,g2) = 1.5708
    c: Tangent(g0,g3) = -1.5708
    c: Tangent(g1,g2) = 1.5708
    c: Tangent(g1,g3) = -1.5708
    c: Equal(g0,g1)
    c: Vertical(g2)
    c: Symmetric(g0,g1,g-4)
    c: Equal(g1,g-4)
    c: PointOnObject(g4,g1)
    c: PointOnObject(g4,g0)
    c: Vertical(g4)
    c: PointOnObject(g1,g4)
    c: DistanceY(g4,g4) = 5
    c: Coincident(g5,g-3)
    c: Equal(g5,g-3)
FEATURE [App::Link] Link047  label="pillar3_pillar3_dec_corner_common001"
  LinkPlacement = pos=(0,0,-470) rot=(0,0,1;0rad)
  LinkedObject = -> Compound100
  Placement = pos=(0,0,-470) rot=(0,0,1;0rad)
  expr: Placement = <<pillar3_dec_corner_placement>>.Placement ^ -1
FEATURE [Part::Compound] Compound098
  Links = -> [Link047]
FEATURE [PartDesign::Boolean] Boolean048
  BaseFeature = -> Mirrored021
  Group = -> [Compound098]
  Suppressed = false
  Type = 1
  UsePlacement = true
FEATURE [PartDesign::Body] Body145  label="pilllar3_dec_corner"
  AllowCompound = false
  Group = -> [Binder144,BaseBend054,Sketch260,Sketch261,Pocket140,Pocket141,DatumPlane008,Mirrored021,Local_CS008,Boolean048]
  Origin = -> Origin126
  Tip = -> Boolean048
FEATURE [Part::FeaturePython] Populate068  label="Populate LinearArray018 with hole_3.4mm_extrude"  # WARN: FeaturePython — macro-defined, semantics opaque (R4)
  Copying = 0
  ExposePlacement = false
  MarkerShape = 1
  MarkerSize = 0
  NumElements = 0
  Object = -> Extrude019
  OutputCompounding = 1
  PlacementsTo = -> LinearArray018
  Referencing = 0
  Type = lattice2PopulateCopies.LatticePopulateCopies
  isLattice = 0
FEATURE [PartDesign::CoordinateSystem] Local_CS010  label="basement_bottom_plywood_bottom"
  AttacherType = Attacher::AttachEngine3D
  AttachmentSupport = -> [XY_Plane011]
  MapMode = 5
FEATURE [PartDesign::CoordinateSystem] Local_CS011  label="basement_bottom_plywood_top"
  AttacherType = Attacher::AttachEngine3D
  AttachmentOffset = pos=(0,0,18) rot=(0,0,1;0rad)
  AttachmentSupport = -> [XY_Plane011]
  MapMode = 5
  Placement = pos=(0,0,18) rot=(0,0,1;0rad)
FEATURE [PartDesign::Body] Body007  label="basement_bottom_plywood"
  AllowCompound = false
  Group = -> [Binder003,Pad002,Sketch110,PolarPattern002,Sketch178,Boolean026,Sketch218,Local_CS010,Local_CS011]
  Origin = -> Origin011
  Tip = -> Boolean026
FEATURE [PartDesign::CoordinateSystem] Local_CS012  label="basement_bottom_proxy_bottom"
  AttacherType = Attacher::AttachEngine3D
  AttachmentSupport = -> [XY_Plane013]
  MapMode = 5
FEATURE [PartDesign::CoordinateSystem] Local_CS013  label="basement_bottom_proxy_top"
  AttacherType = Attacher::AttachEngine3D
  AttachmentOffset = pos=(0,0,3) rot=(0,0,1;0rad)
  AttachmentSupport = -> [XY_Plane013]
  MapMode = 5
  Placement = pos=(0,0,3) rot=(0,0,1;0rad)
FEATURE [PartDesign::CoordinateSystem] Local_CS014  label="basement_bottom_amplifier_bottom_LCS"
  AttacherType = Attacher::AttachEngine3D
  AttachmentSupport = -> [XY_Plane080]
  MapMode = 5
FEATURE [PartDesign::CoordinateSystem] Local_CS015  label="basement_bottom_amplifier_top_LCS"
  AttacherType = Attacher::AttachEngine3D
  AttachmentOffset = pos=(0,0,2) rot=(0,0,1;0rad)
  AttachmentSupport = -> [XY_Plane080]
  MapMode = 5
  Placement = pos=(0,0,2) rot=(0,0,1;0rad)
FEATURE [PartDesign::CoordinateSystem] Local_CS016  label="basement_bottom_proxy_pillar_back_LCS"
  AttacherType = Attacher::AttachEngine3D
  AttachmentOffset = pos=(0,384,3) rot=(0,0,-1;3.14159rad)
  AttachmentSupport = -> [XY_Plane013]
  MapMode = 5
  Placement = pos=(0,384,3) rot=(0,0,-1;3.14159rad)
  expr: .AttachmentOffset.Base.y = <<pillar_placement>>.Placement.Base.y
FEATURE [PartDesign::CoordinateSystem] Local_CS017  label="basement_top_proxy_bottom_LCS"
  AttacherType = Attacher::AttachEngine3D
  AttachmentSupport = -> [XY_Plane012]
  MapMode = 5
FEATURE [PartDesign::CoordinateSystem] Local_CS018  label="basement_top_proxy_top_LCS"
  AttacherType = Attacher::AttachEngine3D
  AttachmentOffset = pos=(0,0,3) rot=(0,0,1;0rad)
  AttachmentSupport = -> [XY_Plane012]
  MapMode = 5
  Placement = pos=(0,0,3) rot=(0,0,1;0rad)
FEATURE [PartDesign::Body] Body008  label="basement_top_proxy"
  AllowCompound = false
  Group = -> [Binder006,Pad003,Boolean021,Binder129,Local_CS017,Local_CS018]
  Origin = -> Origin012
  Placement = pos=(0,0,18) rot=(0,0,1;0rad)
  Tip = -> Boolean021
FEATURE [PartDesign::CoordinateSystem] Local_CS019  label="basement_top_plywood_bottom_LCS"
  AttacherType = Attacher::AttachEngine3D
  AttachmentSupport = -> [XY_Plane010]
  MapMode = 5
FEATURE [PartDesign::CoordinateSystem] Local_CS020  label="basement_top_plywood_top_LCS"
  AttacherType = Attacher::AttachEngine3D
  AttachmentOffset = pos=(0,0,18) rot=(0,0,1;0rad)
  AttachmentSupport = -> [XY_Plane010]
  MapMode = 5
  Placement = pos=(0,0,18) rot=(0,0,1;0rad)
FEATURE [PartDesign::CoordinateSystem] Local_CS021  label="basement_top_amplifier_bottom_LCS"
  AttacherType = Attacher::AttachEngine3D
  AttachmentSupport = -> [XY_Plane078]
  MapMode = 5
FEATURE [PartDesign::CoordinateSystem] Local_CS022  label="basement_top_amplifier_top_LCS"
  AttacherType = Attacher::AttachEngine3D
  AttachmentOffset = pos=(0,0,2) rot=(0,0,1;0rad)
  AttachmentSupport = -> [XY_Plane078]
  MapMode = 5
  Placement = pos=(0,0,2) rot=(0,0,1;0rad)
FEATURE [PartDesign::Body] Body105  label="basement_top_amplifier_material_0.50ansi"
  AllowCompound = false
  Group = -> [Sketch167,BaseBend043,Bend025,Pocket104,Fillet011,Binder119,Sketch170,DatumPlane005,DatumLine003,DatumLine004,Sketch173,Pocket108,Sketch175,Pocket109,Mirrored010,PDW_Common_Add,PolarPattern006,Binder118,Pocket107,Boolean028,Local_CS021,Local_CS022]
  Origin = -> Origin078
  Tip = -> Boolean028
FEATURE [PartDesign::CoordinateSystem] Local_CS023  label="basement_bottom_proxy_pillar_left_LCS"
  AttacherType = Attacher::AttachEngine3D
  AttachmentOffset = pos=(-332.554,-192,3) rot=(0,0,-1;1.0472rad)
  AttachmentSupport = -> [XY_Plane013]
  MapMode = 5
  Placement = pos=(-332.554,-192,3) rot=(0,0,-1;1.0472rad)
  expr: .AttachmentOffset.Base.x = <<pillar_placement>>.Placement.Base.y * cos(210)
  expr: .AttachmentOffset.Base.y = <<pillar_placement>>.Placement.Base.y * sin(210)
FEATURE [PartDesign::CoordinateSystem] Local_CS024  label="basement_bottom_proxy_pillar_right_LCS"
  AttacherType = Attacher::AttachEngine3D
  AttachmentOffset = pos=(332.554,-192,3) rot=(0,0,1;1.0472rad)
  AttachmentSupport = -> [XY_Plane013]
  MapMode = 5
  Placement = pos=(332.554,-192,3) rot=(0,0,1;1.0472rad)
  expr: .AttachmentOffset.Base.x = <<pillar_placement>>.Placement.Base.y * cos(330)
  expr: .AttachmentOffset.Base.y = <<pillar_placement>>.Placement.Base.y * sin(330)
FEATURE [PartDesign::Body] Body009  label="basement_bottom_proxy"
  AllowCompound = false
  Group = -> [Binder004,Pad004,Binder134,Boolean029,Local_CS012,Local_CS013,Local_CS016,Local_CS023,Local_CS024]
  Origin = -> Origin013
  Tip = -> Boolean029
FEATURE [PartDesign::CoordinateSystem] Local_CS025  label="part1_bottom_LCS"
  AttacherType = Attacher::AttachEngine3D
  AttachmentSupport = -> [XY_Plane]
  MapMode = 5
FEATURE [PartDesign::CoordinateSystem] Local_CS026  label="part1_top_LCS"
  AttacherType = Attacher::AttachEngine3D
  AttachmentOffset = pos=(0,0,1428) rot=(0,0,1;0rad)
  AttachmentSupport = -> [XY_Plane]
  MapMode = 5
  Placement = pos=(0,0,1428) rot=(0,0,1;0rad)
  expr: .AttachmentOffset.Base.z = <<Properties>>.total_height
FEATURE [PartDesign::CoordinateSystem] Local_CS027  label="part2_bottom"
  AttacherType = Attacher::AttachEngine3D
  AttachmentOffset = pos=(0,0,0) rot=(0,0,1;2.0944rad)
  AttachmentSupport = -> [XY_Plane001]
  MapMode = 5
  Placement = pos=(0,0,0) rot=(0,0,1;2.0944rad)
FEATURE [PartDesign::CoordinateSystem] Local_CS028
  AttacherType = Attacher::AttachEngine3D
  AttachmentOffset = pos=(0,0,1428) rot=(0,0,1;0rad)
  AttachmentSupport = -> [Local_CS027]
  MapMode = 5
  Placement = pos=(0,0,1428) rot=(0,0,1;2.0944rad)
  expr: .AttachmentOffset.Base.z = <<Properties>>.total_height
FEATURE [App::DocumentObjectGroup] Group017  label="cap_Group"
  Group = -> [Body002,Body003,Body016]
FEATURE [PartDesign::CoordinateSystem] Local_CS029  label="dropper_fix_bottom_outer_LCS"
  AttacherType = Attacher::AttachEngine3D
  AttachmentSupport = -> [XY_Plane007]
  MapMode = 5
FEATURE [PartDesign::CoordinateSystem] Local_CS030  label="dropper_fix_bottom_inner_LCS"
  AttacherType = Attacher::AttachEngine3D
  AttachmentOffset = pos=(0,0,3) rot=(0,0,1;0rad)
  AttachmentSupport = -> [XY_Plane007]
  MapMode = 5
  Placement = pos=(0,0,3) rot=(0,0,1;0rad)
FEATURE [PartDesign::Body] Body004  label="dropper_fix_bottom"
  AllowCompound = false
  Group = -> [Binder007,Pad005,Sketch025,Binder021,Pocket006,Sketch027,Sketch028,Binder023,Hole003,Boolean033,PDW_Common_Sub,Compound048,Connect,Local_CS029,Local_CS030]
  Origin = -> Origin007
  Tip = -> PDW_Common_Sub
FEATURE [PartDesign::CoordinateSystem] Local_CS031  label="dropper_fix_top_outer_LCS"
  AttacherType = Attacher::AttachEngine3D
  AttachmentSupport = -> [XY_Plane083]
  MapMode = 5
FEATURE [PartDesign::CoordinateSystem] Local_CS032  label="dropper_fix_top_inner_LCS"
  AttacherType = Attacher::AttachEngine3D
  AttachmentOffset = pos=(0,0,3) rot=(0,0,1;0rad)
  AttachmentSupport = -> [XY_Plane083]
  MapMode = 5
  Placement = pos=(0,0,3) rot=(0,0,1;0rad)
FEATURE [PartDesign::Body] Body110  label="dropper_fix_top"
  AllowCompound = false
  Group = -> [BaseFeature,PDW_Sub,Connect001,Boolean034,Local_CS031,Local_CS032]
  Origin = -> Origin083
  Tip = -> Boolean034
FEATURE [App::DocumentObjectGroup] Group019  label="dropper_fix_Group"
  Group = -> [Body004,Body110]
FEATURE [App::DocumentObjectGroup] Group018  label="top_Group"
  Group = -> [Group017,Body017,Group019]
FEATURE [PartDesign::CoordinateSystem] Local_CS033  label="sleeve_inner2_flange_top_LCS"
  AttacherType = Attacher::AttachEngine3D
  AttachmentOffset = pos=(0,0,5) rot=(0,0,1;0rad)
  AttachmentSupport = -> [XY_Plane101]
  MapMode = 5
  Placement = pos=(0,0,5) rot=(0,0,1;0rad)
FEATURE [PartDesign::CoordinateSystem] Local_CS034  label="sleeve_inner2_end_LCS"
  AttacherType = Attacher::AttachEngine3D
  AttachmentOffset = pos=(0,0,83.7) rot=(0,0,1;0rad)
  AttachmentSupport = -> [XY_Plane101]
  MapMode = 5
  Placement = pos=(0,0,83.7) rot=(0,0,1;0rad)
FEATURE [PartDesign::Body] Body133  label="sleeve_inner2"
  AllowCompound = false
  Group = -> [Sketch235,Revolution005,Boolean040,Local_CS033,Local_CS034]
  Origin = -> Origin111
  Tip = -> Boolean040
FEATURE [TechDraw::DrawViewPart] View008
  CoarseView = false
  Direction = (0,-1,0)
  Focus = 100
  HardHidden = false
  IsoCount = 0
  IsoHidden = false
  IsoVisible = false
  LockPosition = false
  Perspective = false
  Rotation = 180
  ScaleType = 0
  ScrubCount = 0
  SeamHidden = false
  SeamVisible = true
  SmoothHidden = false
  SmoothVisible = true
  Source = -> [Body133]
  X = 142.629
  XDirection = (1,0,0)
  Y = 105
  expr: Y = Template.Height / 2
FEATURE [TechDraw::DrawViewDimension] Dimension036
  AngleOverride = false
  Arbitrary = false
  ArbitraryTolerances = false
  EqualTolerance = true
  ExtensionAngle = 0
  FormatSpec = %.2w
  FormatSpecOverTolerance = %+.2w
  FormatSpecUnderTolerance = %+.2w
  Inverted = false
  LineAngle = 0
  LockPosition = false
  MeasureType = 1
  OverTolerance = 0
  References2D = -> [View008]
  Rotation = 0
  ScaleType = 0
  TheoreticalExact = false
  Type = 1
  UnderTolerance = 0
  X = -0.138556
  Y = -52.356
FEATURE [TechDraw::DrawViewDimension] Dimension037
  AngleOverride = false
  Arbitrary = false
  ArbitraryTolerances = false
  EqualTolerance = true
  ExtensionAngle = 0
  FormatSpec = %.2w
  FormatSpecOverTolerance = %+.2w
  FormatSpecUnderTolerance = %+.2w
  Inverted = false
  LineAngle = 0
  LockPosition = false
  MeasureType = 1
  OverTolerance = 0
  References2D = -> [View008]
  Rotation = 0
  ScaleType = 0
  TheoreticalExact = false
  Type = 2
  UnderTolerance = 0
  X = 21.4492
  Y = 4.5306
FEATURE [TechDraw::DrawViewDimension] Dimension038
  AngleOverride = false
  Arbitrary = false
  ArbitraryTolerances = false
  EqualTolerance = true
  ExtensionAngle = 0
  FormatSpec = %.2w
  FormatSpecOverTolerance = %+.2w
  FormatSpecUnderTolerance = %+.2w
  Inverted = false
  LineAngle = 0
  LockPosition = false
  MeasureType = 1
  OverTolerance = 0
  References2D = -> [View008]
  Rotation = 0
  ScaleType = 0
  TheoreticalExact = false
  Type = 2
  UnderTolerance = 0
  X = 43.4564
  Y = -40.9108
FEATURE [TechDraw::DrawViewSection] SectionView004  label="Section001  - 001"
  BaseView = -> View008
  CoarseView = false
  CutSurfaceDisplay = 1
  Direction = (-1,0,-1e-16)
  FileGeomPattern = <path>
  FileHatchPattern = <path>
  Focus = 100
  FuseBeforeCut = false
  HardHidden = false
  HatchOffset = (0,0,0)
  HatchRotation = 0
  HatchScale = 1
  IsoCount = 0
  IsoHidden = false
  IsoVisible = false
  LockPosition = false
  NameGeomPattern = Diamond
  Perspective = false
  Rotation = 90
  ScaleType = 0
  ScrubCount = 0
  SeamHidden = false
  SeamVisible = true
  SectionDirection = 4
  SectionLineStretch = 1
  SectionNormal = (-1,0,-1e-16)
  SectionOrigin = (0,0,1473)
  SmoothHidden = false
  SmoothVisible = true
  Source = -> [Body133]
  TrimAfterCut = false
  UsePreviousCut = false
  X = 244.783
  XDirection = (1e-16,0,-1)
  Y = 105
  expr: Y = Template.Height / 2
FEATURE [TechDraw::DrawViewDimension] Dimension035
  AngleOverride = false
  Arbitrary = false
  ArbitraryTolerances = false
  EqualTolerance = true
  ExtensionAngle = 0
  FormatSpec = %.2w
  FormatSpecOverTolerance = %+.2w
  FormatSpecUnderTolerance = %+.2w
  Inverted = false
  LineAngle = 0
  LockPosition = false
  MeasureType = 1
  OverTolerance = 0
  References2D = -> [SectionView004]
  Rotation = 0
  ScaleType = 0
  TheoreticalExact = false
  Type = 1
  UnderTolerance = 0
  X = -0.625347
  Y = 50.1929
FEATURE [TechDraw::DrawViewPart] View009
  CoarseView = false
  Direction = (0,0,1)
  Focus = 100
  HardHidden = false
  IsoCount = 0
  IsoHidden = false
  IsoVisible = false
  LockPosition = false
  Perspective = false
  Rotation = 0
  ScaleType = 0
  ScrubCount = 0
  SeamHidden = false
  SeamVisible = true
  SmoothHidden = false
  SmoothVisible = true
  Source = -> [Body133]
  X = 54.9249
  XDirection = (1,0,0)
  Y = 105
  expr: Y = Template.Height / 2
FEATURE [TechDraw::DrawViewDimension] Dimension032
  AngleOverride = false
  Arbitrary = false
  ArbitraryTolerances = false
  EqualTolerance = true
  ExtensionAngle = 0
  FormatSpec = %.2w
  FormatSpecOverTolerance = %+.2w
  FormatSpecUnderTolerance = %+.2w
  Inverted = false
  LineAngle = 0
  LockPosition = false
  MeasureType = 1
  OverTolerance = 0
  References2D = -> [View009]
  Rotation = 0
  ScaleType = 0
  TheoreticalExact = false
  Type = 0
  UnderTolerance = 0
  X = 4.06158
  Y = 22.1008
FEATURE [TechDraw::DrawViewDimension] Dimension039
  AngleOverride = false
  Arbitrary = true
  ArbitraryTolerances = false
  EqualTolerance = true
  ExtensionAngle = 0
  FormatSpec = ⌀4,2
  FormatSpecOverTolerance = %+.2w
  FormatSpecUnderTolerance = %+.2w
  Inverted = false
  LineAngle = 0
  LockPosition = false
  MeasureType = 1
  OverTolerance = 0
  References2D = -> [View009]
  Rotation = 0
  ScaleType = 0
  TheoreticalExact = false
  Type = 5
  UnderTolerance = 0
  X = 17.5529
  Y = -0.907274
FEATURE [TechDraw::DrawViewDimension] Dimension040
  AngleOverride = false
  Arbitrary = false
  ArbitraryTolerances = false
  EqualTolerance = true
  ExtensionAngle = 0
  FormatSpec = %.2w
  FormatSpecOverTolerance = %+.2w
  FormatSpecUnderTolerance = %+.2w
  Inverted = false
  LineAngle = 0
  LockPosition = false
  MeasureType = 1
  OverTolerance = 0
  References2D = -> [View009]
  Rotation = 0
  ScaleType = 0
  TheoreticalExact = false
  Type = 0
  UnderTolerance = 0
  X = 43.7493
  Y = 16.411
FEATURE [TechDraw::DrawPage] Page004  label="sleeve_inner_Page001"
  KeepUpdated = true
  NextBalloonIndex = 1
  ProjectionType = 0
  Template = -> Template
  Views = -> [View008,View009,SectionView004,Dimension032,Dimension035,Dimension036,Dimension037,Dimension038,Dimension039,Annotation001,Dimension040]
FEATURE [PartDesign::CoordinateSystem] Local_CS035  label="sleeve2_outer_flange_LCS"
  AttacherType = Attacher::AttachEngine3D
  AttachmentSupport = -> [XY_Plane110]
  MapMode = 5
FEATURE [PartDesign::CoordinateSystem] Local_CS036  label="sleeve2_outer_end_LCS"
  AttacherType = Attacher::AttachEngine3D
  AttachmentOffset = pos=(0,0,74.7) rot=(0,0,1;0rad)
  AttachmentSupport = -> [XY_Plane110]
  MapMode = 5
  Placement = pos=(0,0,74.7) rot=(0,0,1;0rad)
FEATURE [PartDesign::Body] Body132  label="sleeve_outer2"
  AllowCompound = false
  Group = -> [Sketch234,Revolution006,Boolean039,Local_CS035,Local_CS036]
  Origin = -> Origin110
  Tip = -> Boolean039
FEATURE [TechDraw::DrawViewPart] View006
  CoarseView = false
  Direction = (0,-1,0)
  Focus = 100
  HardHidden = false
  IsoCount = 0
  IsoHidden = false
  IsoVisible = false
  LockPosition = false
  Perspective = false
  Rotation = 0
  ScaleType = 0
  ScrubCount = 0
  SeamHidden = false
  SeamVisible = true
  SmoothHidden = false
  SmoothVisible = true
  Source = -> [Body132]
  X = 237.932
  XDirection = (1,0,0)
  Y = 105
  expr: Y = Template.Height / 2
FEATURE [TechDraw::DrawViewDimension] Dimension024
  AngleOverride = false
  Arbitrary = false
  ArbitraryTolerances = false
  EqualTolerance = true
  ExtensionAngle = 0
  FormatSpec = %.2w
  FormatSpecOverTolerance = %+.2w
  FormatSpecUnderTolerance = %+.2w
  Inverted = false
  LineAngle = 0
  LockPosition = false
  MeasureType = 1
  OverTolerance = 0
  References2D = -> [View006]
  Rotation = 0
  ScaleType = 0
  TheoreticalExact = false
  Type = 2
  UnderTolerance = 0
  X = 42.4652
  Y = -38.9306
FEATURE [TechDraw::DrawViewDimension] Dimension025
  AngleOverride = false
  Arbitrary = false
  ArbitraryTolerances = false
  EqualTolerance = true
  ExtensionAngle = 0
  FormatSpec = %.2w
  FormatSpecOverTolerance = %+.2w
  FormatSpecUnderTolerance = %+.2w
  Inverted = false
  LineAngle = 0
  LockPosition = false
  MeasureType = 1
  OverTolerance = 0
  References2D = -> [View006]
  Rotation = 0
  ScaleType = 0
  TheoreticalExact = false
  Type = 2
  UnderTolerance = 0
  X = 45.1946
  Y = 8.61143
FEATURE [TechDraw::DrawViewSection] SectionView003  label="Section  - 001"
  BaseView = -> View006
  CoarseView = false
  CutSurfaceDisplay = 1
  Direction = (1,0,0)
  FileGeomPattern = <path>
  FileHatchPattern = <path>
  Focus = 100
  FuseBeforeCut = false
  HardHidden = false
  HatchOffset = (0,0,0)
  HatchRotation = 0
  HatchScale = 1
  IsoCount = 0
  IsoHidden = false
  IsoVisible = false
  LockPosition = false
  NameGeomPattern = Diamond
  Perspective = false
  Rotation = 90
  ScaleType = 0
  ScrubCount = 0
  SeamHidden = false
  SeamVisible = true
  SectionDirection = 4
  SectionLineStretch = 1
  SectionNormal = (1,0,0)
  SectionOrigin = (0,0,1467.5)
  SmoothHidden = false
  SmoothVisible = true
  Source = -> [Body132]
  TrimAfterCut = false
  UsePreviousCut = false
  X = 157.277
  XDirection = (0,0,1)
  Y = 105
  expr: Y = Template.Height / 2
FEATURE [TechDraw::DrawViewDimension] Dimension026
  AngleOverride = false
  Arbitrary = false
  ArbitraryTolerances = false
  EqualTolerance = true
  ExtensionAngle = 0
  FormatSpec = %.2w
  FormatSpecOverTolerance = %+.2w
  FormatSpecUnderTolerance = %+.2w
  Inverted = false
  LineAngle = 0
  LockPosition = false
  MeasureType = 1
  OverTolerance = 0
  References2D = -> [SectionView003]
  Rotation = 0
  ScaleType = 0
  TheoreticalExact = false
  Type = 1
  UnderTolerance = 0
  X = 0.683682
  Y = 55.2929
FEATURE [TechDraw::DrawViewDimension] Dimension027
  AngleOverride = false
  Arbitrary = false
  ArbitraryTolerances = false
  EqualTolerance = true
  ExtensionAngle = 0
  FormatSpec = %.2w
  FormatSpecOverTolerance = %+.2w
  FormatSpecUnderTolerance = %+.2w
  Inverted = false
  LineAngle = 0
  LockPosition = false
  MeasureType = 1
  OverTolerance = 0
  References2D = -> [SectionView003]
  Rotation = 0
  ScaleType = 0
  TheoreticalExact = false
  Type = 1
  UnderTolerance = 0
  X = 0.158865
  Y = 68.5155
FEATURE [TechDraw::DrawViewDimension] Dimension028
  AngleOverride = false
  Arbitrary = false
  ArbitraryTolerances = false
  EqualTolerance = true
  ExtensionAngle = 0
  FormatSpec = %.2w
  FormatSpecOverTolerance = %+.2w
  FormatSpecUnderTolerance = %+.2w
  Inverted = false
  LineAngle = 0
  LockPosition = false
  MeasureType = 1
  OverTolerance = 0
  References2D = -> [SectionView003]
  Rotation = 0
  ScaleType = 0
  TheoreticalExact = false
  Type = 1
  UnderTolerance = 0
  X = -3.16566
  Y = -53.4728
FEATURE [TechDraw::DrawViewDimension] Dimension029
  AngleOverride = false
  Arbitrary = false
  ArbitraryTolerances = false
  EqualTolerance = true
  ExtensionAngle = 0
  FormatSpec = %.2w
  FormatSpecOverTolerance = %+.2w
  FormatSpecUnderTolerance = %+.2w
  Inverted = false
  LineAngle = 0
  LockPosition = false
  MeasureType = 1
  OverTolerance = 0
  References2D = -> [SectionView003]
  Rotation = 0
  ScaleType = 0
  TheoreticalExact = false
  Type = 1
  UnderTolerance = 0
  X = -25.9778
  Y = 46.3177
FEATURE [TechDraw::DrawViewPart] View007
  CoarseView = false
  Direction = (0,0,1)
  Focus = 100
  HardHidden = false
  IsoCount = 0
  IsoHidden = false
  IsoVisible = false
  LockPosition = false
  Perspective = false
  Rotation = 0
  ScaleType = 0
  ScrubCount = 0
  SeamHidden = false
  SeamVisible = true
  SmoothHidden = false
  SmoothVisible = true
  Source = -> [Body132]
  X = 65.7116
  XDirection = (1,0,0)
  Y = 105
  expr: Y = Template.Height / 2
FEATURE [TechDraw::DrawViewDimension] Dimension030
  AngleOverride = false
  Arbitrary = true
  ArbitraryTolerances = false
  EqualTolerance = true
  ExtensionAngle = 0
  FormatSpec = ⌀5,0
  FormatSpecOverTolerance = %+.2w
  FormatSpecUnderTolerance = %+.2w
  Inverted = false
  LineAngle = 0
  LockPosition = false
  MeasureType = 1
  OverTolerance = 0
  References2D = -> [View007]
  Rotation = 0
  ScaleType = 0
  TheoreticalExact = false
  Type = 5
  UnderTolerance = 0
  X = 47.8244
  Y = -19.4044
FEATURE [TechDraw::DrawViewDimension] Dimension031
  AngleOverride = false
  Arbitrary = false
  ArbitraryTolerances = false
  EqualTolerance = true
  ExtensionAngle = 0
  FormatSpec = %.2w
  FormatSpecOverTolerance = %+.2w
  FormatSpecUnderTolerance = %+.2w
  Inverted = false
  LineAngle = 0
  LockPosition = false
  MeasureType = 1
  OverTolerance = 0
  References2D = -> [View007]
  Rotation = 0
  ScaleType = 0
  TheoreticalExact = false
  Type = 0
  UnderTolerance = 0
  X = -12.6028
  Y = 21.5334
FEATURE [TechDraw::DrawPage] Page003  label="sleeve_outer_Page001"
  KeepUpdated = true
  NextBalloonIndex = 1
  ProjectionType = 0
  Template = -> Template
  Views = -> [View006,View007,Dimension024,Dimension025,SectionView003,Dimension026,Dimension027,Dimension028,Dimension029,Dimension030,Dimension031,Annotation]
FEATURE [App::DocumentObjectGroup] Group020  label="sleeve2_Group"
  Group = -> [Body133,Body132]
FEATURE [Sketcher::SketchObject] Sketch265
  ArcFitTolerance = 0
  AttachmentSupport = -> [XY_Plane124]
  FullyConstrained = true
  MakeInternals = false
  MapMode = 5
  expr: Constraints[4] = <<pillar3_hat_fix_BaseBend>>.length / 2
  sketch-geometry (8):
    g0: LineSegment StartX=11.3 StartY=14 StartZ=0 EndX=10 EndY=14 EndZ=0
    g1: ArcOfCircle CenterX=10 CenterY=9 CenterZ=0 NormalX=0 NormalY=0 NormalZ=1 AngleXU=0 Radius=5 StartAngle=1.5708 EndAngle=3.14159
    g2: LineSegment StartX=5 StartY=9 StartZ=0 EndX=5 EndY=1 EndZ=0
    g3: LineSegment StartX=14.3 StartY=17 StartZ=0 EndX=14.3 EndY=-7 EndZ=0
    g4: ArcOfCircle CenterX=10 CenterY=1 CenterZ=0 NormalX=0 NormalY=0 NormalZ=1 AngleXU=0 Radius=5 StartAngle=3.14159 EndAngle=4.71239
    g5: ArcOfCircle CenterX=11.3 CenterY=-7 CenterZ=0 NormalX=0 NormalY=0 NormalZ=1 AngleXU=0 Radius=3 StartAngle=-7.46e-14 EndAngle=1.5708
    g6: ArcOfCircle CenterX=11.3 CenterY=17 CenterZ=0 NormalX=0 NormalY=0 NormalZ=1 AngleXU=0 Radius=3 StartAngle=4.71239 EndAngle=6.28319
    g7: LineSegment StartX=10 StartY=-4 StartZ=0 EndX=11.3 EndY=-4 EndZ=0
  constraints (20):
    c: Horizontal(g0)
    c: Vertical(g2)
    c: Vertical(g3)
    c: Radius(g1) = 5
    c: DistanceX(g3) = 14.3
    c: Tangent(g1,g0) = -1.5708
    c: Tangent(g2,g1) = -1.5708
    c: DistanceX(g2) = 5
    c: Tangent(g0,g6) = 1.5708
    c: Tangent(g3,g6) = 1.5708
    c: Horizontal(g7)
    c: Tangent(g3,g5) = 1.5708
    c: Tangent(g4,g2) = -1.5708
    c: Tangent(g7,g4) = -1.5708
    c: Tangent(g7,g5) = 1.5708
    c: Radius(g6) = 3
    c: Equal(g6,g5)
    c: Equal(g4,g1)
    c: DistanceY(g0) = 14
    c: DistanceY(g4) = -4
FEATURE [PartDesign::FeaturePython] SketchOnSheet  # WARN: FeaturePython — macro-defined, semantics opaque (R4)
  BaseFeature = -> BaseBend053
  Sketch = -> Sketch265
  Suppressed = false
  baseObject = -> BaseBend053 [Face22]
  kfactor = 0.5
FEATURE [PartDesign::Pocket] Pocket138
  BaseFeature = -> SketchOnSheet
  Direction = (0,0,-1)
  Length = 5
  Length2 = 5
  Profile = -> Sketch256
  ReferenceAxis = -> Sketch256 [N_Axis]
  Reversed = true
  Suppressed = false
  Type = 0
FEATURE [PartDesign::Pocket] Pocket139
  BaseFeature = -> Pocket138
  Direction = (0,0,-1)
  Length = 5
  Length2 = 5
  Profile = -> Sketch257
  ReferenceAxis = -> Sketch257 [N_Axis]
  Reversed = true
  Suppressed = false
  Type = 1
FEATURE [Part::FeaturePython] LinearArray019  label="hat_hat_fix_placements"  # WARN: FeaturePython — macro-defined, semantics opaque (R4)
  Alignment = 0
  CellStart = A1
  Count = 2
  Dir = (1,0,0)
  DirIsDriven = true
  DistributionLaw = 0
  DrivenProperty = 1
  EndInclusive = true
  ExposePlacement = false
  GeneratorMode = 0
  MarkerShape = 1
  MarkerSize = 0
  NumElements = 2
  OrientMode = 1
  Placement = pos=(0,0,0) rot=(0,0,1;1.5708rad)
  Point = (0,0,0)
  PointIsDriven = true
  Reverse = false
  SpanEnd = 50
  SpanStart = 20
  Step = 30
  Type = lattice2LinearArray.LinearArray
  VSGVersion = 1
  Values = 20.0 | 50.0
  ValuesSource = 2
  isLattice = 1
FEATURE [Part::FeaturePython] Populate069  label="Populate LinearArray019 with hole_3.4mm_extrude"  # WARN: FeaturePython — macro-defined, semantics opaque (R4)
  Copying = 0
  ExposePlacement = false
  MarkerShape = 1
  MarkerSize = 0
  NumElements = 0
  Object = -> Extrude019
  OutputCompounding = 1
  PlacementsTo = -> LinearArray019
  Referencing = 0
  Type = lattice2PopulateCopies.LatticePopulateCopies
  isLattice = 0
FEATURE [Part::Compound] Compound094  label="pillar3_hat_fix_cut1"
  Links = -> [Populate055,Populate069]
FEATURE [PartDesign::Boolean] Boolean046
  BaseFeature = -> Pocket139
  Group = -> [Compound094]
  Suppressed = false
  Type = 1
  UsePlacement = true
FEATURE [PartDesign::Body] Body144  label="pillar3_hat_fix"
  AllowCompound = false
  Group = -> [Binder143,BaseBend053,Sketch256,Sketch257,SketchOnSheet,Pocket138,Pocket139,Local_CS005,Boolean046,Sketch265]
  Origin = -> Origin125
  Tip = -> Boolean046
FEATURE [Part::FeaturePython] PolarArray011  # WARN: FeaturePython — macro-defined, semantics opaque (R4)
  Alignment = 0
  AttacherType = Attacher::AttachEngine3D
  CellStart = A1
  Count = 3
  DistributionLaw = 0
  EndInclusive = false
  ExposePlacement = false
  FlipX = false
  FlipZ = false
  GeneratorMode = 0
  MarkerShape = 1
  MarkerSize = 0
  NumElements = 3
  OrientMode = 3
  Placement = pos=(0,0,0) rot=(0,0,1;1.5708rad)
  Radius = 382
  Reverse = false
  SpanEnd = 360
  SpanStart = 0
  Step = 120
  Type = lattice2PolarArray2.PolarArray
  UseArcRadius = false
  UseArcRange = 0
  VSGVersion = 1
  Values = 0.0 | 120.0 | 240.0
  ValuesSource = 2
  isLattice = 1
  expr: Radius = <<pillar_placement>>.Placement.Base.y - 2 mm
FEATURE [Part::FeaturePython] Populate070  label="Populate PolarArray011 with hat_hat_fix_placements"  # WARN: FeaturePython — macro-defined, semantics opaque (R4)
  Copying = 0
  ExposePlacement = false
  MarkerShape = 1
  MarkerSize = 0
  NumElements = 6
  Object = -> LinearArray019
  OutputCompounding = 0
  PlacementsTo = -> PolarArray011
  Referencing = 0
  Type = lattice2PopulateCopies.LatticePopulateCopies
  isLattice = 1
FEATURE [Part::FeaturePython] Populate071  label="Populate Populate PolarArray011 with hat_hat_fix_placements with hole_3.4mm_extrude"  # WARN: FeaturePython — macro-defined, semantics opaque (R4)
  Copying = 0
  ExposePlacement = false
  MarkerShape = 1
  MarkerSize = 0
  NumElements = 0
  Object = -> Extrude019
  OutputCompounding = 1
  PlacementsTo = -> Populate070
  Referencing = 0
  Type = lattice2PopulateCopies.LatticePopulateCopies
  isLattice = 0
FEATURE [PartDesign::CoordinateSystem] Local_CS037  label="hat3_bottom_bottom_LCS"
  AttacherType = Attacher::AttachEngine3D
  AttachmentSupport = -> [XY_Plane122]
  MapMode = 2
FEATURE [PartDesign::CoordinateSystem] Local_CS038  label="hat3_bottom_top_LCS"
  AttacherType = Attacher::AttachEngine3D
  AttachmentOffset = pos=(0,0,3) rot=(0,0,1;0rad)
  AttachmentSupport = -> [XY_Plane122]
  MapMode = 5
  Placement = pos=(0,0,3) rot=(0,0,1;0rad)
FEATURE [Part::FeaturePython] Mirror015  label="Mirror015 of Populate Placment037 with dec_corner_pillar_fix"  # WARN: FeaturePython — macro-defined, semantics opaque (R4)
  ExposePlacement = false
  FlipX = true
  FlipY = false
  FlipZ = false
  MarkerShape = 1
  MarkerSize = 0
  NumElements = 5
  Object = -> Populate058
  ObjectTraversal = 0
  Type = lattice2Mirror.LatticeMirror
  isLattice = 1
FEATURE [Part::FeaturePython] Join017  # WARN: FeaturePython — macro-defined, semantics opaque (R4)
  ExposePlacement = false
  Interleave = false
  Links = -> [Mirror015,Populate058]
  MarkerShape = 1
  MarkerSize = 0
  NumElements = 10
  Type = lattice2JoinArrays.JoinArrays
  isLattice = 1
FEATURE [Part::FeaturePython] Populate059  label="Populate pillar3_dec_corner_placement with Populate Placment037 with dec_corner_pillar_fix"  # WARN: FeaturePython — macro-defined, semantics opaque (R4)
  Copying = 0
  ExposePlacement = false
  MarkerShape = 1
  MarkerSize = 0
  NumElements = 10
  Object = -> Join017
  OutputCompounding = 0
  PlacementsTo = -> Placment035
  Referencing = 0
  Type = lattice2PopulateCopies.LatticePopulateCopies
  isLattice = 1
FEATURE [Part::FeaturePython] Populate061  label="Populate Populate pillar3_dec_corner_placement with Populate Placment037 with dec_corner_pillar_fix with hole_3.4mm_extrude"  # WARN: FeaturePython — macro-defined, semantics opaque (R4)
  Copying = 0
  ExposePlacement = false
  MarkerShape = 1
  MarkerSize = 0
  NumElements = 0
  Object = -> Extrude019
  OutputCompounding = 1
  PlacementsTo = -> Populate059
  Referencing = 0
  Type = lattice2PopulateCopies.LatticePopulateCopies
  isLattice = 0
FEATURE [PartDesign::CoordinateSystem] Local_CS039  label="sleeve_outer_flange_bottom_LCS"
  AttacherType = Attacher::AttachEngine3D
  AttachmentSupport = -> [XY_Plane100]
  MapMode = 5
FEATURE [PartDesign::CoordinateSystem] Local_CS040  label="sleeve_outer_end_LCS"
  AttacherType = Attacher::AttachEngine3D
  AttachmentOffset = pos=(0,0,67) rot=(0,0,1;0rad)
  AttachmentSupport = -> [XY_Plane100]
  MapMode = 5
  Placement = pos=(0,0,67) rot=(0,0,1;0rad)
FEATURE [PartDesign::Body] Body123  label="sleeve_outer"
  AllowCompound = false
  Group = -> [Sketch220,Revolution001,Boolean030,Local_CS039,Local_CS040]
  Origin = -> Origin100
  Tip = -> Boolean030
FEATURE [TechDraw::DrawViewPart] View
  CoarseView = false
  Direction = (0,-1,0)
  Focus = 100
  HardHidden = false
  IsoCount = 0
  IsoHidden = false
  IsoVisible = false
  LockPosition = false
  Perspective = false
  Rotation = 0
  ScaleType = 0
  ScrubCount = 0
  SeamHidden = false
  SeamVisible = true
  SmoothHidden = false
  SmoothVisible = true
  Source = -> [Body123]
  X = 238
  XDirection = (1,0,0)
  Y = 105
  expr: Y = Template.Height / 2
FEATURE [TechDraw::DrawViewPart] View001
  CoarseView = false
  Direction = (0,0,1)
  Focus = 100
  HardHidden = false
  IsoCount = 0
  IsoHidden = false
  IsoVisible = false
  LockPosition = false
  Perspective = false
  Rotation = 0
  ScaleType = 0
  ScrubCount = 0
  SeamHidden = false
  SeamVisible = true
  SmoothHidden = false
  SmoothVisible = true
  Source = -> [Body123]
  X = 65.7116
  XDirection = (1,0,0)
  Y = 105
  expr: Y = Template.Height / 2
FEATURE [TechDraw::DrawViewDimension] Dimension006
  AngleOverride = false
  Arbitrary = true
  ArbitraryTolerances = false
  EqualTolerance = true
  ExtensionAngle = 0
  FormatSpec = ⌀5,0
  FormatSpecOverTolerance = %+.2w
  FormatSpecUnderTolerance = %+.2w
  Inverted = false
  LineAngle = 0
  LockPosition = false
  MeasureType = 1
  OverTolerance = 0
  References2D = -> [View001]
  Rotation = 0
  ScaleType = 0
  TheoreticalExact = false
  Type = 5
  UnderTolerance = 0
  X = 25.4999
  Y = -5.33296
FEATURE [TechDraw::DrawViewDimension] Dimension007
  AngleOverride = false
  Arbitrary = false
  ArbitraryTolerances = false
  EqualTolerance = true
  ExtensionAngle = 0
  FormatSpec = %.2w
  FormatSpecOverTolerance = %+.2w
  FormatSpecUnderTolerance = %+.2w
  Inverted = false
  LineAngle = 0
  LockPosition = false
  MeasureType = 1
  OverTolerance = 0
  References2D = -> [View001]
  Rotation = 0
  ScaleType = 0
  TheoreticalExact = false
  Type = 0
  UnderTolerance = 0
  X = -12.6028
  Y = 21.5334
FEATURE [PartDesign::CoordinateSystem] Local_CS041  label="sleeve_inner_flange_top_LCS"
  AttacherType = Attacher::AttachEngine3D
  AttachmentOffset = pos=(0,0,8) rot=(0,0,1;0rad)
  AttachmentSupport = -> [XY_Plane101]
  MapMode = 5
  Placement = pos=(0,0,8) rot=(0,0,1;0rad)
FEATURE [PartDesign::CoordinateSystem] Local_CS042  label="sleeve_inner_end_LCS"
  AttacherType = Attacher::AttachEngine3D
  AttachmentOffset = pos=(0,0,79) rot=(0,0,1;0rad)
  AttachmentSupport = -> [XY_Plane101]
  MapMode = 5
  Placement = pos=(0,0,79) rot=(0,0,1;0rad)
FEATURE [PartDesign::Body] Body124  label="sleeve_inner"
  AllowCompound = false
  Group = -> [Sketch221,Revolution,Boolean031,Local_CS041,Local_CS042]
  Origin = -> Origin101
  Tip = -> Boolean031
FEATURE [TechDraw::DrawViewPart] View002
  CoarseView = false
  Direction = (0,-1,0)
  Focus = 100
  HardHidden = false
  IsoCount = 0
  IsoHidden = false
  IsoVisible = false
  LockPosition = false
  Perspective = false
  Rotation = 180
  ScaleType = 0
  ScrubCount = 0
  SeamHidden = false
  SeamVisible = true
  SmoothHidden = false
  SmoothVisible = true
  Source = -> [Body124]
  X = 242.629
  XDirection = (1,0,0)
  Y = 105
  expr: Y = Template.Height / 2
FEATURE [TechDraw::DrawViewPart] View003
  CoarseView = false
  Direction = (0,0,1)
  Focus = 100
  HardHidden = false
  IsoCount = 0
  IsoHidden = false
  IsoVisible = false
  LockPosition = false
  Perspective = false
  Rotation = 0
  ScaleType = 0
  ScrubCount = 0
  SeamHidden = false
  SeamVisible = true
  SmoothHidden = false
  SmoothVisible = true
  Source = -> [Body124]
  X = 54.9249
  XDirection = (1,0,0)
  Y = 105
  expr: Y = Template.Height / 2
FEATURE [TechDraw::DrawViewDimension] Dimension008
  AngleOverride = false
  Arbitrary = false
  ArbitraryTolerances = false
  EqualTolerance = true
  ExtensionAngle = 0
  FormatSpec = %.2w
  FormatSpecOverTolerance = %+.2w
  FormatSpecUnderTolerance = %+.2w
  Inverted = false
  LineAngle = 0
  LockPosition = false
  MeasureType = 1
  OverTolerance = 0
  References2D = -> [View003]
  Rotation = 0
  ScaleType = 0
  TheoreticalExact = false
  Type = 0
  UnderTolerance = 0
  X = 4.06158
  Y = 22.1008
FEATURE [TechDraw::DrawViewDimension] Dimension012
  AngleOverride = false
  Arbitrary = false
  ArbitraryTolerances = false
  EqualTolerance = true
  ExtensionAngle = 0
  FormatSpec = %.2w
  FormatSpecOverTolerance = %+.2w
  FormatSpecUnderTolerance = %+.2w
  Inverted = false
  LineAngle = 0
  LockPosition = false
  MeasureType = 1
  OverTolerance = 0
  References2D = -> [View002]
  Rotation = 0
  ScaleType = 0
  TheoreticalExact = false
  Type = 1
  UnderTolerance = 0
  X = -0.138556
  Y = -52.356
FEATURE [TechDraw::DrawViewDimension] Dimension013
  AngleOverride = false
  Arbitrary = false
  ArbitraryTolerances = false
  EqualTolerance = true
  ExtensionAngle = 0
  FormatSpec = %.2w
  FormatSpecOverTolerance = %+.2w
  FormatSpecUnderTolerance = %+.2w
  Inverted = false
  LineAngle = 0
  LockPosition = false
  MeasureType = 1
  OverTolerance = 0
  References2D = -> [View002]
  Rotation = 0
  ScaleType = 0
  TheoreticalExact = false
  Type = 2
  UnderTolerance = 0
  X = 21.4492
  Y = 4.5306
FEATURE [TechDraw::DrawViewDimension] Dimension014
  AngleOverride = false
  Arbitrary = false
  ArbitraryTolerances = false
  EqualTolerance = true
  ExtensionAngle = 0
  FormatSpec = %.2w
  FormatSpecOverTolerance = %+.2w
  FormatSpecUnderTolerance = %+.2w
  Inverted = false
  LineAngle = 0
  LockPosition = false
  MeasureType = 1
  OverTolerance = 0
  References2D = -> [View002]
  Rotation = 0
  ScaleType = 0
  TheoreticalExact = false
  Type = 2
  UnderTolerance = 0
  X = 43.4564
  Y = -40.9108
FEATURE [TechDraw::DrawViewDimension] Dimension015
  AngleOverride = false
  Arbitrary = true
  ArbitraryTolerances = false
  EqualTolerance = true
  ExtensionAngle = 0
  FormatSpec = ⌀4,2
  FormatSpecOverTolerance = %+.2w
  FormatSpecUnderTolerance = %+.2w
  Inverted = false
  LineAngle = 0
  LockPosition = false
  MeasureType = 1
  OverTolerance = 0
  References2D = -> [View003]
  Rotation = 0
  ScaleType = 0
  TheoreticalExact = false
  Type = 5
  UnderTolerance = 0
  X = 17.5529
  Y = -0.907274
FEATURE [App::DocumentObjectGroup] Group021  label="sleeve_Group"
  Group = -> [Body124,Body123]
FEATURE [Part::Mirroring] Part__Mirroring037  label="pillar_dec_corner_base_sketch (Mirror #34)"
  Base = (0,0,0)
  Normal = (1,0,0)
  Source = -> Sketch056
FEATURE [PartDesign::SubShapeBinder] Binder148
  BindCopyOnChange = 0
  BindMode = 0
  ClaimChildren = true
  Context = -> Body147 [Binder148.]
  Fuse = false
  MakeFace = true
  OffsetFill = false
  OffsetIntersection = false
  OffsetJoinType = 0
  OffsetOpenResult = false
  PartialLoad = false
  Relative = false
  Support = -> [Part__Mirroring037]
  _Version = 2
FEATURE [PartDesign::FeaturePython] BaseBend056  label="pilllar3_dec_corner_mirror_BaseBend"  # WARN: FeaturePython — macro-defined, semantics opaque (R4)
  BendSide = 1
  BendSketch = -> Binder148
  MidPlane = false
  Reverse = false
  Suppressed = false
  length = 1214
  radius = 2
  thickness = 0.5
  expr: length = <<pillar3_dec_corner_BaseBend>>.length
  expr: radius = <<pillar3_dec_corner_BaseBend>>.radius
  expr: thickness = <<pillar3_dec_corner_BaseBend>>.thickness
FEATURE [Sketcher::SketchObject] Sketch266
  ArcFitTolerance = 0
  AttachmentSupport = -> [XZ_Plane127]
  ExternalGeometry = -> [Binder148]
  FullyConstrained = true
  MakeInternals = false
  MapMode = 5
  Placement = pos=(0,0,0) rot=(1,0,0;1.5708rad)
  sketch-geometry (3):
    g0: ArcOfCircle CenterX=-13.3 CenterY=5 CenterZ=0 NormalX=0 NormalY=0 NormalZ=1 AngleXU=0 Radius=5 StartAngle=3.14159 EndAngle=4.71239
    g1: LineSegment StartX=-18.3 StartY=5 StartZ=0 EndX=-18.3 EndY=0 EndZ=0
    g2: LineSegment StartX=-18.3 StartY=0 StartZ=0 EndX=-13.3 EndY=0 EndZ=0
  constraints (7):
    c: PointOnObject(g0,g-3)
    c: Coincident(g1,g2)
    c: Vertical(g1)
    c: Coincident(g1,g-3)
    c: Tangent(g0,g1) = -1.5708
    c: Radius(g0) = 5
    c: Tangent(g2,g0) = -1.5708
FEATURE [Sketcher::SketchObject] Sketch267
  ArcFitTolerance = 0
  AttachmentSupport = -> [YZ_Plane127]
  ExternalGeometry = -> [Binder148]
  FullyConstrained = true
  MakeInternals = false
  MapMode = 5
  Placement = pos=(0,0,0) rot=(0.57735,0.57735,0.57735;2.0944rad)
  sketch-geometry (3):
    g0: LineSegment StartX=14 StartY=6.04e-13 StartZ=0 EndX=19 EndY=0 EndZ=0
    g1: LineSegment StartX=19 StartY=0 StartZ=0 EndX=19 EndY=5 EndZ=0
    g2: ArcOfCircle CenterX=14 CenterY=5 CenterZ=0 NormalX=0 NormalY=0 NormalZ=1 AngleXU=0 Radius=5 StartAngle=4.71239 EndAngle=6.28319
  constraints (7):
    c: PointOnObject(g0,g-1)
    c: Coincident(g0,g1)
    c: Vertical(g1)
    c: Coincident(g0,g-3)
    c: Tangent(g2,g1) = -1.5708
    c: Tangent(g2,g0) = -1.5708
    c: Radius(g2) = 5
FEATURE [PartDesign::Pocket] Pocket142
  BaseFeature = -> BaseBend056
  Direction = (0,1,-2e-16)
  Length = 5
  Length2 = 5
  Midplane = true
  Profile = -> Sketch266
  ReferenceAxis = -> Sketch266 [N_Axis]
  Suppressed = false
  Type = 1
FEATURE [PartDesign::Pocket] Pocket143
  BaseFeature = -> Pocket142
  Direction = (-1,0,0)
  Length = 5
  Length2 = 5
  Midplane = true
  Profile = -> Sketch267
  ReferenceAxis = -> Sketch267 [N_Axis]
  Suppressed = false
  Type = 1
FEATURE [PartDesign::Plane] DatumPlane009
  AttachmentOffset = pos=(0,0,607) rot=(0,0,1;0rad)
  AttachmentSupport = -> [XY_Plane127]
  Length = 60
  MapMode = 5
  Placement = pos=(0,0,607) rot=(0,0,1;0rad)
  ResizeMode = 0
  Width = 60
  expr: .AttachmentOffset.Base.z = <<pilllar3_dec_corner_mirror_BaseBend>>.length / 2
FEATURE [PartDesign::Mirrored] Mirrored022
  BaseFeature = -> Pocket143
  MirrorPlane = -> DatumPlane009
  Originals = -> [Pocket142,Pocket143]
  Suppressed = false
  TransformMode = 0
FEATURE [Part::Compound] Compound103
  Links = -> [Link047]
FEATURE [PartDesign::Boolean] Boolean051
  BaseFeature = -> Mirrored022
  Group = -> [Compound103]
  Suppressed = false
  Type = 1
  UsePlacement = true
FEATURE [PartDesign::CoordinateSystem] Local_CS043
  AttacherType = Attacher::AttachEngine3D
  AttachmentSupport = -> [XY_Plane127]
  MapMode = 5
FEATURE [PartDesign::Body] Body147  label="pilllar3_dec_corner_mirror"
  AllowCompound = false
  Group = -> [Binder148,BaseBend056,Sketch266,Sketch267,Pocket142,Pocket143,DatumPlane009,Mirrored022,Boolean051,Local_CS043]
  Origin = -> Origin128
  Tip = -> Boolean051
FEATURE [PartDesign::CoordinateSystem] Local_CS044  label="hat3_cap_bottom_LCS"
  AttacherType = Attacher::AttachEngine3D
  AttachmentSupport = -> [XY_Plane123]
  MapMode = 5
FEATURE [PartDesign::CoordinateSystem] Local_CS045  label="hat3_cap_top_LCS"
  AttacherType = Attacher::AttachEngine3D
  AttachmentOffset = pos=(0,0,3) rot=(0,0,1;0rad)
  AttachmentSupport = -> [XY_Plane123]
  MapMode = 5
  Placement = pos=(0,0,3) rot=(0,0,1;0rad)
FEATURE [Part::FeaturePython] PolarArray012  # WARN: FeaturePython — macro-defined, semantics opaque (R4)
  Alignment = 0
  AttacherType = Attacher::AttachEngine3D
  CellStart = A1
  Count = 3
  DistributionLaw = 0
  EndInclusive = false
  ExposePlacement = false
  FlipX = false
  FlipZ = false
  GeneratorMode = 0
  MarkerShape = 1
  MarkerSize = 0
  NumElements = 3
  OrientMode = 2
  Placement = pos=(0,0,0) rot=(0,0,1;0.523599rad)
  Radius = 118.5
  Reverse = false
  SpanEnd = 360
  SpanStart = 0
  Step = 120
  Type = lattice2PolarArray2.PolarArray
  UseArcRadius = false
  UseArcRange = 0
  VSGVersion = 1
  Values = 0.0 | 120.0 | 240.0
  ValuesSource = 2
  isLattice = 1
  expr: Radius = <<hat3_border>>.Constraints.min_r - 12.5 mm
FEATURE [Part::FeaturePython] Populate072  label="Populate PolarArray012 with hole_3.4mm_extrude"  # WARN: FeaturePython — macro-defined, semantics opaque (R4)
  Copying = 0
  ExposePlacement = false
  MarkerShape = 1
  MarkerSize = 0
  NumElements = 0
  Object = -> Extrude019
  OutputCompounding = 1
  PlacementsTo = -> PolarArray012
  Referencing = 0
  Type = lattice2PopulateCopies.LatticePopulateCopies
  isLattice = 0
FEATURE [Sketcher::SketchObject] Sketch268
  ArcFitTolerance = 0
  AttachmentSupport = -> [YZ_Plane121]
  FullyConstrained = false
  MakeInternals = false
  MapMode = 5
  Placement = pos=(0,0,0) rot=(0.57735,0.57735,0.57735;2.0944rad)
  sketch-geometry (7):
    g0: Circle CenterX=11.5 CenterY=9 CenterZ=0 NormalX=0 NormalY=0 NormalZ=1 AngleXU=0 Radius=1.7
    g1: Circle CenterX=11.5 CenterY=40.3333 CenterZ=0 NormalX=0 NormalY=0 NormalZ=1 AngleXU=0 Radius=1.7
    g2: Circle CenterX=11.5 CenterY=71.6667 CenterZ=0 NormalX=0 NormalY=0 NormalZ=1 AngleXU=0 Radius=1.7
    g3: LineSegment [constr] StartX=11.5 StartY=9 StartZ=0 EndX=11.5 EndY=40.3333 EndZ=0
    g4: LineSegment [constr] StartX=11.5 StartY=40.3333 StartZ=0 EndX=11.5 EndY=71.6667 EndZ=0
    g5: Circle [constr] CenterX=11.5 CenterY=103 CenterZ=0 NormalX=0 NormalY=0 NormalZ=1 AngleXU=0 Radius=1.86607
    g6: LineSegment [constr] StartX=11.5 StartY=103 StartZ=0 EndX=11.5 EndY=71.6667 EndZ=0
  constraints (17):
    c: Equal(g0,g1)
    c: Equal(g0,g2)
    c: Diameter(g0) = 3.4
    c: Coincident(g3,g0)
    c: Coincident(g3,g1)
    c: Coincident(g3,g4)
    c: Coincident(g4,g2)
    c: Vertical(g4)
    c: Vertical(g3)
    c: Equal(g3,g4)
    c: Coincident(g6,g5)
    c: Coincident(g6,g2)
    c: Vertical(g6)
    c: DistanceY(g0) = 9
    c: DistanceX(g0) = 11.5
    c: Equal(g6,g4)
    c: DistanceY(g5) = 103
FEATURE [PartDesign::CoordinateSystem] Local_CS047  label="pillar3_bottom_LCS"
  AttacherType = Attacher::AttachEngine3D
  AttachmentOffset = pos=(18.3,4,0) rot=(0,0,1;1.5708rad)
  AttachmentSupport = -> [XY_Plane121]
  MapMode = 5
  Placement = pos=(18.3,4,0) rot=(0,0,1;1.5708rad)
FEATURE [PartDesign::CoordinateSystem] pillar_bottom_LCS
  AttacherType = Attacher::AttachEngine3D
  AttachmentOffset = pos=(-50.5,0,0) rot=(0,0,1;0rad)
  AttachmentSupport = -> [XY_Plane015]
  MapMode = 5
  Placement = pos=(-50.5,0,0) rot=(0,0,1;0rad)
FEATURE [App::Link] Link048  label="PSU_holes"
  LinkedObject = -> <external UET-VAS-060A20_12V_IP20.FCStd>#Sketch001
FEATURE [Part::Extrusion] Extrude039  label="PSU_holes_Extrude"
  Base = -> Link048
  Dir = (0,0,1)
  DirMode = 2
  FaceMakerClass = Part::FaceMakerBullseye
  FaceMakerMode = 3
  LengthFwd = 10
  LengthRev = 0
  Solid = true
  Symmetric = false
FEATURE [Part::FeaturePython] Placment039  label="hat3_PSU_placement"  # WARN: FeaturePython — macro-defined, semantics opaque (R4)
  AttacherType = Attacher::AttachEngine3D
  ExposePlacement = true
  MarkerShape = 1
  MarkerSize = 50
  NumElements = 1
  Placement = pos=(-80,-68,0) rot=(0,0,1;1.5708rad)
  Type = lattice2AttachablePlacement.AttachablePlacement
  isLattice = 1
FEATURE [Part::FeaturePython] Populate073  label="Populate hat3_PSU_placement with PSU_holes_Extrude"  # WARN: FeaturePython — macro-defined, semantics opaque (R4)
  Copying = 0
  ExposePlacement = false
  MarkerShape = 1
  MarkerSize = 0
  NumElements = 0
  Object = -> Extrude039
  OutputCompounding = 2
  PlacementsTo = -> Placment039
  Referencing = 0
  Type = lattice2PopulateCopies.LatticePopulateCopies
  isLattice = 0
FEATURE [Part::Cylinder] Cylinder013
  Angle = 360
  AttacherType = Attacher::AttachEngine3D
  FirstAngle = 0
  Height = 10
  Radius = 13.25
  SecondAngle = 0
  expr: Radius = <<sleeve_inner_sketch>>.Constraints.outer_r + 0.25 mm
FEATURE [PartDesign::SubShapeBinder] Binder149
  BindCopyOnChange = 0
  BindMode = 0
  ClaimChildren = true
  Context = -> <external composit_full_size3_composit_cut.FCStd>#Link026 [Binder149.]
  Fuse = false
  MakeFace = true
  OffsetFill = false
  OffsetIntersection = false
  OffsetJoinType = 0
  OffsetOpenResult = false
  PartialLoad = false
  Placement = pos=(0,0,0) rot=(1,0,0;1.5708rad)
  Relative = false
  Support = -> [Sketch225]
  _Version = 2
  expr: Support = <<UV_driver_holder_base_Sketch>>._self
FEATURE [PartDesign::FeaturePython] BaseBend050  label="UV_driver_holder_BaseBend"  # WARN: FeaturePython — macro-defined, semantics opaque (R4)
  BendSide = 0
  BendSketch = -> Binder149
  MidPlane = true
  Reverse = false
  Suppressed = false
  length = 20
  radius = 0.1
  thickness = 0.3
FEATURE [Sketcher::SketchObject] Sketch269
  ArcFitTolerance = 0
  AttachmentOffset = pos=(31.5,10,0) rot=(0,0,1;0rad)
  AttachmentSupport = -> [XY_Plane103]
  FullyConstrained = true
  MakeInternals = false
  MapMode = 5
  Placement = pos=(31.5,10,0) rot=(0,0,1;0rad)
  expr: .AttachmentOffset.Base.x = <<UV_driver_holder_base_Sketch>>.Constraints.total_width / 2
  expr: .AttachmentOffset.Base.y = <<UV_driver_holder_BaseBend>>.length / 2
  sketch-geometry (3):
    g0: LineSegment StartX=-3 StartY=0 StartZ=0 EndX=0 EndY=0 EndZ=0
    g1: LineSegment StartX=0 StartY=0 StartZ=0 EndX=0 EndY=-3 EndZ=0
    g2: ArcOfCircle CenterX=-3 CenterY=-3 CenterZ=0 NormalX=0 NormalY=0 NormalZ=1 AngleXU=0 Radius=3 StartAngle=1e-16 EndAngle=1.5708
  constraints (7):
    c: PointOnObject(g0,g-1)
    c: Coincident(g0,g-1)
    c: Coincident(g0,g1)
    c: PointOnObject(g1,g-2)
    c: Tangent(g2,g0) = 1.5708
    c: Tangent(g2,g1) = 1.5708
    c: Radius(g2) = 3
FEATURE [PartDesign::Pocket] Pocket145
  BaseFeature = -> BaseBend050
  Direction = (0,0,-1)
  Length = 5
  Length2 = 5
  Profile = -> Sketch269
  ReferenceAxis = -> Sketch269 [N_Axis]
  Reversed = true
  Suppressed = false
  Type = 0
FEATURE [PartDesign::Mirrored] Mirrored023
  MirrorPlane = -> YZ_Plane103
  Suppressed = false
  TransformMode = 0
FEATURE [PartDesign::Mirrored] Mirrored024
  MirrorPlane = -> XZ_Plane103
  Suppressed = false
  TransformMode = 0
FEATURE [PartDesign::MultiTransform] MultiTransform002
  BaseFeature = -> Pocket145
  Originals = -> [Pocket145]
  Suppressed = false
  TransformMode = 0
  Transformations = -> [Mirrored023,Mirrored024]
FEATURE [Part::Extrusion] Extrude040
  Base = -> Sketch226
  Dir = (0,0,1)
  DirMode = 2
  FaceMakerClass = Part::FaceMakerBullseye
  FaceMakerMode = 3
  LengthFwd = 10
  LengthRev = 0
  Solid = true
  Symmetric = false
FEATURE [Part::Compound] Compound104
  Links = -> [Extrude040]
FEATURE [PartDesign::Boolean] Boolean052
  BaseFeature = -> MultiTransform002
  Group = -> [Compound104]
  Suppressed = false
  Type = 1
  UsePlacement = true
FEATURE [PartDesign::Body] Body126  label="UV_driver_holder_material_0.30ansi"
  AllowCompound = false
  Group = -> [BaseBend050,Binder149,Sketch269,Pocket145,MultiTransform002,Mirrored023,Mirrored024,Boolean052]
  Origin = -> Origin103
  Tip = -> Boolean052
FEATURE [Part::FeaturePython] Placment040  # WARN: FeaturePython — macro-defined, semantics opaque (R4)
  AttacherType = Attacher::AttachEngine3D
  ExposePlacement = true
  MarkerShape = 1
  MarkerSize = 20
  NumElements = 1
  Placement = pos=(35,130,0) rot=(0,0,1;0rad)
  Type = lattice2AttachablePlacement.AttachablePlacement
  isLattice = 1
FEATURE [Part::FeaturePython] Populate074  label="Populate Placment040 with Extrude040"  # WARN: FeaturePython — macro-defined, semantics opaque (R4)
  Copying = 0
  ExposePlacement = false
  MarkerShape = 1
  MarkerSize = 0
  NumElements = 0
  Object = -> Extrude040
  OutputCompounding = 2
  PlacementsTo = -> Placment040
  Referencing = 0
  Type = lattice2PopulateCopies.LatticePopulateCopies
  isLattice = 0
FEATURE [App::Link] Link049  label="fix_holes"
  LinkedObject = -> <external socket_fixture.FCStd>#Sketch003
FEATURE [Part::FeaturePython] Placment041  # WARN: FeaturePython — macro-defined, semantics opaque (R4)
  AttacherType = Attacher::AttachEngine3D
  ExposePlacement = true
  MarkerShape = 1
  MarkerSize = 10
  NumElements = 1
  Placement = pos=(-69,35,0) rot=(0,0,1;0rad)
  Type = lattice2AttachablePlacement.AttachablePlacement
  isLattice = 1
FEATURE [Part::FeaturePython] Placment042  # WARN: FeaturePython — macro-defined, semantics opaque (R4)
  AttacherType = Attacher::AttachEngine3D
  ExposePlacement = true
  MarkerShape = 1
  MarkerSize = 10
  NumElements = 1
  Placement = pos=(69,35,0) rot=(0,0,1;0rad)
  Type = lattice2AttachablePlacement.AttachablePlacement
  isLattice = 1
  expr: .Placement.Base.x = -<<Placment041>>.Placement.Base.x
  expr: .Placement.Base.y = <<Placment041>>.Placement.Base.y
FEATURE [Part::FeaturePython] Join018  # WARN: FeaturePython — macro-defined, semantics opaque (R4)
  ExposePlacement = false
  Interleave = false
  Links = -> [Placment041,Placment042]
  MarkerShape = 1
  MarkerSize = 0
  NumElements = 2
  Type = lattice2JoinArrays.JoinArrays
  isLattice = 1
FEATURE [Part::Extrusion] Extrude041  label="fix_holes_Extrude"
  Base = -> Link049
  Dir = (0,0,1)
  DirMode = 2
  FaceMakerClass = Part::FaceMakerBullseye
  FaceMakerMode = 3
  LengthFwd = 10
  LengthRev = 0
  Solid = true
  Symmetric = false
FEATURE [Part::FeaturePython] Populate075  label="Populate Join018 with fix_holes_Extrude"  # WARN: FeaturePython — macro-defined, semantics opaque (R4)
  Copying = 0
  ExposePlacement = false
  MarkerShape = 1
  MarkerSize = 0
  NumElements = 0
  Object = -> Extrude041
  OutputCompounding = 1
  PlacementsTo = -> Join018
  Referencing = 0
  Type = lattice2PopulateCopies.LatticePopulateCopies
  isLattice = 0
FEATURE [Part::Mirroring] Part__Mirroring038  label="tech_sector_pillar_material_0.30ansi (Mirror #35)"
  Base = (0,0,0)
  Normal = (-0.5,0.866025,0)
  Source = -> Body073
  expr: .Normal.x = cos(120 deg)
  expr: .Normal.y = sin(120 deg)
FEATURE [App::DocumentObjectGroup] Group024  label="tech_sector"
  Group = -> [Body074,Body077,Body073,Part__Mirroring038]
FEATURE [Sketcher::SketchObject] Sketch270
  ArcFitTolerance = 0
  FullyConstrained = true
  MakeInternals = false
  sketch-geometry (13):
    g0: Circle CenterX=0 CenterY=20 CenterZ=0 NormalX=0 NormalY=0 NormalZ=1 AngleXU=0 Radius=1.7
    g1: Circle CenterX=0 CenterY=-20 CenterZ=0 NormalX=0 NormalY=0 NormalZ=1 AngleXU=0 Radius=1.7
    g2: GeomPoint [constr] X=0 Y=0 Z=0
    g3: LineSegment StartX=-10 StartY=-24 StartZ=0 EndX=10 EndY=-24 EndZ=0
    g4: LineSegment StartX=15 StartY=-19 StartZ=0 EndX=15 EndY=19 EndZ=0
    g5: LineSegment StartX=10 StartY=24 StartZ=0 EndX=-10 EndY=24 EndZ=0
    g6: LineSegment StartX=-15 StartY=19 StartZ=0 EndX=-15 EndY=-19 EndZ=0
    g7: ArcOfCircle CenterX=-10 CenterY=-19 CenterZ=0 NormalX=0 NormalY=0 NormalZ=1 AngleXU=0 Radius=5 StartAngle=3.14159 EndAngle=4.71239
    g8: ArcOfCircle CenterX=10 CenterY=-19 CenterZ=0 NormalX=0 NormalY=0 NormalZ=1 AngleXU=0 Radius=5 StartAngle=4.71239 EndAngle=6.28319
    g9: ArcOfCircle CenterX=10 CenterY=19 CenterZ=0 NormalX=0 NormalY=0 NormalZ=1 AngleXU=0 Radius=5 StartAngle=5e-16 EndAngle=1.5708
    g10: ArcOfCircle CenterX=-10 CenterY=19 CenterZ=0 NormalX=0 NormalY=0 NormalZ=1 AngleXU=0 Radius=5 StartAngle=1.5708 EndAngle=3.14159
    g11: GeomPoint [constr] X=-15 Y=-24 Z=0
    g12: GeomPoint [constr] X=15 Y=24 Z=0
  constraints (29):
    c: PointOnObject(g0,g-2)
    c: Equal(g1,g0)
    c: Diameter(g1) = 3.4
    c: Symmetric(g1,g0,g-1)
    c: DistanceY(g1,g0) = 40
    c: Coincident(g2,g-1)
    c: Tangent(g3,g7) = -1.5708
    c: Tangent(g3,g8) = -1.5708
    c: Tangent(g4,g8) = -1.5708
    c: Tangent(g4,g9) = -1.5708
    c: Tangent(g5,g9) = -1.5708
    c: Tangent(g5,g10) = -1.5708
    c: Tangent(g6,g10) = -1.5708
    c: Tangent(g6,g7) = -1.5708
    c: Horizontal(g3)
    c: Horizontal(g5)
    c: Vertical(g4)
    c: Vertical(g6)
    c: Equal(g7,g8)
    c: Equal(g8,g9)
    c: Equal(g9,g10)
    c: PointOnObject(g11,g3)
    c: PointOnObject(g11,g6)
    c: PointOnObject(g12,g4)
    c: PointOnObject(g12,g5)
    c: Radius(g9) = 5
    c: Symmetric(g12,g11,g-1)
    c: DistanceY(g3,g5) = 48
    c: DistanceX(g6,g4) = 30
FEATURE [Sketcher::SketchObject] Sketch271
  ArcFitTolerance = 0
  ExternalGeometry = -> [Sketch047]
  FullyConstrained = true
  MakeInternals = false
  sketch-geometry (3):
    g0: Circle CenterX=22.9472 CenterY=102 CenterZ=0 NormalX=0 NormalY=0 NormalZ=1 AngleXU=0 Radius=1.7
    g1: Circle CenterX=340.4 CenterY=102 CenterZ=0 NormalX=0 NormalY=0 NormalZ=1 AngleXU=0 Radius=1.7
    g2: Circle CenterX=340.4 CenterY=52 CenterZ=0 NormalX=0 NormalY=0 NormalZ=1 AngleXU=0 Radius=1.7
  constraints (9):
    c: Horizontal(g-5,g2)
    c: Vertical(g2,g1)
    c: Horizontal(g1,g-4)
    c: DistanceX(g-4,g1) = 0.4
    c: Equal(g1,g-4)
    c: Horizontal(g0,g-3)
    c: DistanceX(g-3,g0) = 0.2
    c: Equal(g0,g-3)
    c: Equal(g2,g-5)
FEATURE [Part::Extrusion] Extrude042
  Base = -> Sketch271
  Dir = (0,0,1)
  DirMode = 2
  FaceMakerClass = Part::FaceMakerBullseye
  FaceMakerMode = 3
  LengthFwd = 30
  LengthRev = 0
  Placement = pos=(0,0,0) rot=(0.57735,0.57735,0.57735;2.0944rad)
  Solid = true
  Symmetric = true
FEATURE [Part::Compound] Compound023  label="sink_fix"
  Links = -> [Extrude042]
  Placement = pos=(0,1,392) rot=(0,0,1;0rad)
  expr: .Placement.Base.z = basin_big#<<Properties>>.height
FEATURE [PartDesign::CoordinateSystem] Local_CS048
  AttacherType = Attacher::AttachEngine3D
  AttachmentOffset = pos=(0,0,0) rot=(0,1,0;1.5708rad)
  AttachmentSupport = -> [Sketch171]
  MapMode = 7
  Placement = pos=(42.5,285,0) rot=(0.517473,0.605071,0.605071;2.18654rad)
FEATURE [Sketcher::SketchObject] Sketch272
  ArcFitTolerance = 0
  AttachmentSupport = -> [Local_CS048]
  FullyConstrained = true
  MakeInternals = false
  MapMode = 5
  Placement = pos=(42.5,285,0) rot=(0.517473,0.605071,0.605071;2.18654rad)
FEATURE [PartDesign::Body] Body107  label="basement_bottom_amplifier_material_0.50ansi"
  AllowCompound = false
  Group = -> [Sketch171,BaseBend044,Bend026,Sketch174,Binder117,Pocket105,Sketch176,Binder120,Local_CS048,Sketch272,Mirrored011,Pocket110,Binder121,Pocket111,Sketch195,Mirrored012,PDW_Add,PDW_Common_Add001,PolarPattern007,Pocket106,Boolean027,Local_CS014,Local_CS015]
  Origin = -> Origin080
  Tip = -> Boolean027
FEATURE [App::DocumentObjectGroup] Group015  label="basement_bottom_Group"
  Group = -> [Body009,Body007,Body107]
FEATURE [Sketcher::SketchObject] Sketch273  label="basement_v4_bottom_amplifier_Sketch"
  ArcFitTolerance = 0
  FullyConstrained = true
  MakeInternals = false
  expr: Constraints[4] = 285 mm - 5 mm
  sketch-geometry (6):
    g0: LineSegment [constr] StartX=0 StartY=0 StartZ=0 EndX=142.894 EndY=82.5 EndZ=0
    g1: LineSegment StartX=0 StartY=280 StartZ=0 EndX=52.4359 EndY=280 EndZ=0
    g2: ArcOfCircle CenterX=52.4359 CenterY=270 CenterZ=0 NormalX=0 NormalY=0 NormalZ=1 AngleXU=0 Radius=10 StartAngle=0.280016 EndAngle=1.5708
    g3: ArcOfCircle CenterX=879.708 CenterY=507.9 CenterZ=0 NormalX=0 NormalY=0 NormalZ=1 AngleXU=0 Radius=850.799 StartAngle=3.42161 EndAngle=3.66519
    g4: LineSegment [constr] StartX=140.485 StartY=0 StartZ=0 EndX=62.0464 EndY=272.764 EndZ=0
    g5: GeomPoint [constr] X=60 Y=280 Z=0
  constraints (17):
    c: Coincident(g0,g-1)
    c: Angle(g0) = 0.523599
    c: PointOnObject(g1,g-2)
    c: Horizontal(g1)
    c: DistanceY(g1) = 280
    c: Coincident(g3,g0)
    c: Tangent(g2,g1) = 1.5708
    c: Tangent(g3,g2) = 1.5708
    c: Perpendicular(g3,g0)
    c: Radius(g2) = 10
    c: PointOnObject(g4,g-1)
    c: Tangent(g4,g2) = -1.5708
    c: Angle(g4) = 1.85081
    c: PointOnObject(g5,g3)
    c: PointOnObject(g5,g1)
    c: DistanceX(g5) = 60
    c: Distance(g0) = 165
FEATURE [Part::Mirroring] Part__Mirroring039  label="basement_v4_bottom_amplifier_Sketch (Mirror #36)"
  Base = (0,0,0)
  Normal = (1,0,0)
  Source = -> Sketch273
FEATURE [Part::Compound] Compound105
  Links = -> [Part__Mirroring039,Sketch273]
FEATURE [Part::FeaturePython] Array015  # Draft array (typed FeaturePython)
  Angle = 360
  ArrayType = 1
  Axis = (0,0,1)
  Base = -> Compound105
  Center = (0,0,0)
  Count = 3
  Fuse = true
  IntervalAxis = (0,0,0)
  IntervalX = (50,0,0)
  IntervalY = (0,50,0)
  IntervalZ = (0,0,50)
  NumberCircles = 3
  NumberPolar = 3
  NumberX = 2
  NumberY = 2
  NumberZ = 1
  RadialDistance = 50
  Symmetry = 1
  TangentialDistance = 25
FEATURE [Part::FeaturePython] Connect008  # WARN: FeaturePython — macro-defined, semantics opaque (R4)
  Objects = -> [Array015]
  Tolerance = 0
FEATURE [PartDesign::SubShapeBinder] Binder150
  BindCopyOnChange = 0
  BindMode = 0
  ClaimChildren = true
  Context = -> Body148 [Binder150.]
  Fuse = false
  MakeFace = true
  OffsetFill = false
  OffsetIntersection = false
  OffsetJoinType = 0
  OffsetOpenResult = false
  PartialLoad = false
  Relative = false
  Support = -> [Connect008]
  _Version = 2
FEATURE [PartDesign::Pad] Pad047
  Direction = (0,0,1)
  Length = 18
  Length2 = 10
  Profile = -> Binder150
  Suppressed = false
  Type = 0
FEATURE [Part::MultiFuse] Fusion002
  Placement = pos=(0,0,0) rot=(0,0,1;1.5708rad)
  Shapes = -> [Populate054]
FEATURE [PartDesign::SubShapeBinder] Binder151
  BindCopyOnChange = 0
  BindMode = 0
  ClaimChildren = false
  Context = -> Body149 [Binder151.]
  Fuse = false
  MakeFace = true
  OffsetFill = false
  OffsetIntersection = false
  OffsetJoinType = 0
  OffsetOpenResult = false
  PartialLoad = false
  Relative = true
  Support = -> [Array002]
  _Version = 2
  expr: Support = <<basement_bottom_2d>>._self
FEATURE [PartDesign::Pad] Pad048
  Direction = (0,0,1)
  Length = 18
  Length2 = 10
  Profile = -> Binder151
  Suppressed = false
  Type = 0
FEATURE [Sketcher::SketchObject] Sketch274
  ArcFitTolerance = 0
  ExternalGeometry = -> [Sketch273]
  FullyConstrained = true
  MakeInternals = false
  sketch-geometry (5):
    g0: Circle CenterX=110.493 CenterY=121.528 CenterZ=0 NormalX=0 NormalY=0 NormalZ=1 AngleXU=0 Radius=2
    g1: Circle CenterX=52.4359 CenterY=270 CenterZ=0 NormalX=0 NormalY=0 NormalZ=1 AngleXU=0 Radius=2
    g2: LineSegment [constr] StartX=0 StartY=0 StartZ=0 EndX=142.894 EndY=82.5 EndZ=0
    g3: LineSegment [constr] StartX=52.4359 StartY=280 StartZ=0 EndX=52.4359 EndY=270 EndZ=0
    g4: LineSegment [constr] StartX=52.4359 StartY=270 StartZ=0 EndX=62.0464 EndY=272.764 EndZ=0
  constraints (14):
    c: Coincident(g2,g-1)
    c: Coincident(g2,g-3)
    c: Distance(g0,g2) = 50
    c: Distance(g0,g-3) = 10
    c: PointOnObject(g3,g-4)
    c: Coincident(g3,g1)
    c: Coincident(g3,g4)
    c: PointOnObject(g4,g-3)
    c: Perpendicular(g-3,g4)
    c: Equal(g3,g4)
    c: Perpendicular(g-4,g3)
    c: Distance(g3) = 10
    c: Equal(g1,g0)
    c: Diameter(g0) = 4
FEATURE [Part::Extrusion] Extrude043
  Base = -> Sketch274
  Dir = (0,0,1)
  DirMode = 2
  FaceMakerClass = Part::FaceMakerBullseye
  FaceMakerMode = 3
  LengthFwd = 20
  LengthRev = 0
  Solid = true
  Symmetric = false
FEATURE [Part::Mirroring] Part__Mirroring040  label="Extrude043 (Mirror #37)"
  Base = (0,0,0)
  Normal = (1,0,0)
  Source = -> Extrude043
FEATURE [Part::Compound] Compound108
  Links = -> [Part__Mirroring040,Extrude043]
FEATURE [Part::FeaturePython] Array016  # Draft array (typed FeaturePython)
  Angle = 360
  ArrayType = 1
  Axis = (0,0,1)
  Base = -> Compound108
  Center = (0,0,0)
  Count = 3
  Fuse = true
  IntervalAxis = (0,0,0)
  IntervalX = (50,0,0)
  IntervalY = (0,50,0)
  IntervalZ = (0,0,50)
  NumberCircles = 3
  NumberPolar = 3
  NumberX = 2
  NumberY = 2
  NumberZ = 1
  RadialDistance = 50
  Symmetry = 1
  TangentialDistance = 25
FEATURE [Part::Compound] Compound107
  Links = -> [Populate033,Populate028,Populate045,Cylinder012,Fusion002,Array016]
FEATURE [PartDesign::Boolean] Boolean054
  BaseFeature = -> Pad048
  Group = -> [Compound107]
  Suppressed = false
  Type = 1
  UsePlacement = true
FEATURE [PartDesign::Body] Body149  label="basement_v4_bottom"
  AllowCompound = false
  Group = -> [Binder151,Pad048,Boolean054]
  Origin = -> Origin130
  Tip = -> Boolean054
FEATURE [PartDesign::SubShapeBinder] Binder152
  BindCopyOnChange = 0
  BindMode = 0
  ClaimChildren = true
  Context = -> Body151 [Binder152.]
  Fuse = true
  MakeFace = false
  OffsetFill = false
  OffsetIntersection = false
  OffsetJoinType = 0
  OffsetOpenResult = false
  PartialLoad = false
  Relative = false
  Support = -> [Connect010]
  _Version = 2
  expr: Support = <<Connect010>>._self
FEATURE [PartDesign::Pad] Pad049
  Direction = (0,0,1)
  Length = 18
  Length2 = 10
  Profile = -> Binder152
  Refine = true
  Suppressed = false
  Type = 0
FEATURE [Sketcher::SketchObject] Sketch275
  ArcFitTolerance = 0
  ExternalGeometry = -> [Sketch015]
  FullyConstrained = true
  MakeInternals = false
  expr: Constraints[9] = <<U-fix_bottom_array>>.Radius - 17.4 mm - 15 mm
  sketch-geometry (4):
    g0: ArcOfCircle CenterX=-472.335 CenterY=-272.703 CenterZ=0 NormalX=0 NormalY=0 NormalZ=1 AngleXU=0 Radius=748.406 StartAngle=0.523599 EndAngle=0.779626
    g1: ArcOfCircle CenterX=52.8018 CenterY=246.406 CenterZ=0 NormalX=0 NormalY=0 NormalZ=1 AngleXU=0 Radius=10 StartAngle=0.779626 EndAngle=1.3597
    g2: LineSegment [constr] StartX=0 StartY=0 StartZ=0 EndX=219.104 EndY=126.5 EndZ=0
    g3: ArcOfCircle CenterX=0 CenterY=0 CenterZ=0 NormalX=0 NormalY=0 NormalZ=1 AngleXU=0 Radius=262 StartAngle=1.3597 EndAngle=1.5708
  constraints (11):
    c: Tangent(g1,g0) = -1.5708
    c: Coincident(g2,g-1)
    c: Coincident(g2,g-3)
    c: PointOnObject(g0,g2)
    c: Radius(g1) = 10
    c: Distance(g0,g2) = 50
    c: Coincident(g-3,g0)
    c: Coincident(g3,g2)
    c: PointOnObject(g3,g-2)
    c: DistanceY(g3) = 262
    c: Tangent(g3,g1) = -1.5708
FEATURE [Part::FeaturePython] Placment043  # WARN: FeaturePython — macro-defined, semantics opaque (R4)
  AttacherType = Attacher::AttachEngine3D
  ExposePlacement = true
  MarkerShape = 1
  MarkerSize = 20
  NumElements = 1
  Type = lattice2AttachablePlacement.AttachablePlacement
  isLattice = 1
FEATURE [Part::FeaturePython] Placment044  # WARN: FeaturePython — macro-defined, semantics opaque (R4)
  AttacherType = Attacher::AttachEngine3D
  ExposePlacement = true
  MarkerShape = 1
  MarkerSize = 20
  NumElements = 1
  Placement = pos=(0,0,0) rot=(0,1,0;3.14159rad)
  Type = lattice2AttachablePlacement.AttachablePlacement
  isLattice = 1
FEATURE [Part::FeaturePython] Join019  # WARN: FeaturePython — macro-defined, semantics opaque (R4)
  ExposePlacement = false
  Interleave = false
  Links = -> [Placment043,Placment044]
  MarkerShape = 1
  MarkerSize = 10
  NumElements = 2
  Type = lattice2JoinArrays.JoinArrays
  isLattice = 1
FEATURE [Part::FeaturePython] PolarArray013  # WARN: FeaturePython — macro-defined, semantics opaque (R4)
  Alignment = 0
  AttacherType = Attacher::AttachEngine3D
  CellStart = A1
  Count = 3
  DistributionLaw = 0
  EndInclusive = false
  ExposePlacement = false
  FlipX = false
  FlipZ = false
  GeneratorMode = 0
  MarkerShape = 1
  MarkerSize = 10
  NumElements = 3
  OrientMode = 2
  Radius = 0
  Reverse = false
  SpanEnd = 360
  SpanStart = 0
  Step = 120
  Type = lattice2PolarArray2.PolarArray
  UseArcRadius = false
  UseArcRange = 0
  VSGVersion = 1
  Values = 0.0 | 120.0 | 240.0
  ValuesSource = 2
  isLattice = 1
FEATURE [Part::FeaturePython] Populate076  label="mirrorYZ_and_populate_3_placements"  # WARN: FeaturePython — macro-defined, semantics opaque (R4)
  Copying = 0
  ExposePlacement = false
  MarkerShape = 1
  MarkerSize = 10
  NumElements = 6
  Object = -> PolarArray013
  OutputCompounding = 0
  PlacementsTo = -> Join019
  Referencing = 0
  Type = lattice2PopulateCopies.LatticePopulateCopies
  isLattice = 1
FEATURE [Part::FeaturePython] Populate077  label="Populate Populate Join019 with PolarArray013 with Sketch275"  # WARN: FeaturePython — macro-defined, semantics opaque (R4)
  Copying = 0
  ExposePlacement = false
  MarkerShape = 1
  MarkerSize = 0
  NumElements = 0
  Object = -> Sketch275
  OutputCompounding = 1
  PlacementsTo = -> Populate076
  Referencing = 0
  Type = lattice2PopulateCopies.LatticePopulateCopies
  isLattice = 0
FEATURE [Part::FeaturePython] Connect009  # WARN: FeaturePython — macro-defined, semantics opaque (R4)
  Objects = -> [Populate077]
  Tolerance = 0
FEATURE [PartDesign::SubShapeBinder] Binder153
  BindCopyOnChange = 0
  BindMode = 0
  ClaimChildren = true
  Context = -> Body150 [Binder153.]
  Fuse = false
  MakeFace = true
  OffsetFill = false
  OffsetIntersection = false
  OffsetJoinType = 0
  OffsetOpenResult = false
  PartialLoad = false
  Relative = false
  Support = -> [Connect009]
  _Version = 2
FEATURE [PartDesign::Pad] Pad050
  Direction = (0,0,1)
  Length = 18
  Length2 = 10
  Profile = -> Binder153
  Suppressed = false
  Type = 0
FEATURE [Sketcher::SketchObject] Sketch276
  ArcFitTolerance = 0
  ExternalGeometry = -> [Sketch275]
  FullyConstrained = false
  MakeInternals = false
  sketch-geometry (3):
    g0: Circle CenterX=42.8252 CenterY=228.013 CenterZ=0 NormalX=0 NormalY=0 NormalZ=1 AngleXU=0 Radius=2
    g1: Circle CenterX=123.314 CenterY=128.93 CenterZ=0 NormalX=0 NormalY=0 NormalZ=1 AngleXU=0 Radius=2
    g2: LineSegment [constr] StartX=0 StartY=0 StartZ=0 EndX=204.597 EndY=118.124 EndZ=0
  constraints (8):
    c: Coincident(g2,g-1)
    c: Equal(g1,g0)
    c: Diameter(g1) = 4
    c: Distance(g1,g2) = 50
    c: PointOnObject(g-3,g2)
    c: Distance(g1,g-3) = 30
    c: Distance(g0,g-4) = 30
    c: Distance(g0,g-3) = 30
FEATURE [Part::Extrusion] Extrude044
  Base = -> Sketch276
  Dir = (0,0,1)
  DirMode = 2
  FaceMakerClass = Part::FaceMakerBullseye
  FaceMakerMode = 3
  LengthFwd = 40
  LengthRev = 0
  Solid = true
  Symmetric = true
FEATURE [Part::FeaturePython] Populate078  label="Populate mirrorYZ_and_populate_3_placements with Extrude044"  # WARN: FeaturePython — macro-defined, semantics opaque (R4)
  Copying = 0
  ExposePlacement = false
  MarkerShape = 1
  MarkerSize = 0
  NumElements = 0
  Object = -> Extrude044
  OutputCompounding = 1
  PlacementsTo = -> Populate076
  Referencing = 0
  Type = lattice2PopulateCopies.LatticePopulateCopies
  isLattice = 0
FEATURE [Part::Cylinder] Cylinder014
  Angle = 360
  AttacherType = Attacher::AttachEngine3D
  FirstAngle = 0
  Height = 30
  Radius = 12
  SecondAngle = 0
FEATURE [Part::Compound] Compound109
  Links = -> [Populate078,Fusion002,Cylinder014]
FEATURE [PartDesign::Boolean] Boolean055
  BaseFeature = -> Pad050
  Group = -> [Compound109]
  Suppressed = false
  Type = 1
  UsePlacement = true
FEATURE [PartDesign::Body] Body150  label="basement_v4_top_amplifier"
  AllowCompound = false
  Group = -> [Binder153,Pad050,Boolean055]
  Origin = -> Origin131
  Tip = -> Boolean055
FEATURE [Part::Compound] Compound110
  Links = -> [Populate078,Fusion002,Cylinder014,Populate037]
FEATURE [Sketcher::SketchObject] Sketch277
  ArcFitTolerance = 0
  AttachmentOffset = pos=(-253,0,0) rot=(0,0,1;0rad)
  AttachmentSupport = -> [YZ_Plane131]
  FullyConstrained = true
  MakeInternals = false
  MapMode = 5
  Placement = pos=(0,-253,0) rot=(0.57735,0.57735,0.57735;2.0944rad)
  sketch-geometry (3):
    g0: LineSegment StartX=0 StartY=15 StartZ=0 EndX=0 EndY=0 EndZ=0
    g1: LineSegment StartX=0 StartY=0 StartZ=0 EndX=15 EndY=0 EndZ=0
    g2: LineSegment StartX=15 StartY=0 StartZ=0 EndX=0 EndY=15 EndZ=0
  constraints (8):
    c: PointOnObject(g0,g-2)
    c: Coincident(g0,g-1)
    c: Coincident(g0,g1)
    c: PointOnObject(g1,g-1)
    c: Coincident(g1,g2)
    c: Coincident(g2,g0)
    c: Angle(g2) = 2.35619
    c: DistanceY(g0,g0) = 15
FEATURE [PartDesign::SubtractivePipe] SubtractivePipe001
  AuxilleryCurvelinear = true
  AuxillerySpineTangent = false
  BaseFeature = -> Pad049
  Binormal = (0,0,0)
  Mode = 0
  Profile = -> Sketch277
  Spine = -> Binder152 [Edge14,Edge13,Edge12,Edge11,Edge10,Edge9,Edge8,Edge7,Edge6,Edge5,Edge4,Edge3,Edge2,Edge1,Edge18,Edge17,Edge16,Edge15]
  SpineTangent = false
  Suppressed = false
  Transformation = 0
  Transition = 0
FEATURE [PartDesign::Boolean] Boolean056
  BaseFeature = -> SubtractivePipe001
  Group = -> [Compound110]
  Refine = true
  Suppressed = false
  Type = 1
  UsePlacement = true
FEATURE [PartDesign::Body] Body151  label="basement_v4_top"
  AllowCompound = false
  Group = -> [Binder152,Pad049,SubtractivePipe001,Boolean056,Sketch277]
  Origin = -> Origin132
  Tip = -> SubtractivePipe001
FEATURE [Part::FeaturePython] Connect010  # WARN: FeaturePython — macro-defined, semantics opaque (R4)
  Objects = -> [Array003]
  Tolerance = 0
FEATURE [Part::Cylinder] Cylinder015
  Angle = 360
  AttacherType = Attacher::AttachEngine3D
  FirstAngle = 0
  Height = 20
  Radius = 10
  SecondAngle = 0
FEATURE [Part::Compound] Compound106
  Links = -> [Fusion002,Array016,Cylinder015]
FEATURE [PartDesign::Boolean] Boolean053
  BaseFeature = -> Pad047
  Group = -> [Compound106]
  Suppressed = false
  Type = 1
  UsePlacement = true
FEATURE [PartDesign::Body] Body148  label="basement_v4_bottom_amplifier"
  AllowCompound = false
  Group = -> [Binder150,Pad047,Boolean053]
  Origin = -> Origin129
  Tip = -> Boolean053
FEATURE [App::DocumentObjectGroup] Group025  label="basement_v4_Group"
  Group = -> [Body148,Body149,Body150,Body151]
FEATURE [Sketcher::SketchObject] Sketch278
  ArcFitTolerance = 0
  AttachmentOffset = pos=(0,0,0) rot=(0,1,0;1.5708rad)
  AttachmentSupport = -> [Binder145]
  FullyConstrained = true
  MakeInternals = false
  MapMode = 7
  Placement = pos=(113.449,65.5,0) rot=(-0.774597,0.447214,0.447214;4.45971rad)
  sketch-geometry (1):
    g0: Circle CenterX=0 CenterY=22 CenterZ=0 NormalX=0 NormalY=0 NormalZ=1 AngleXU=0 Radius=1.7
  constraints (3):
    c: PointOnObject(g0,g-2)
    c: Diameter(g0) = 3.4
    c: DistanceY(g0) = 22
FEATURE [PartDesign::Pocket] Pocket146
  BaseFeature = -> Boolean047
  Direction = (0.866025,0.5,0)
  Length = 5
  Length2 = 5
  Midplane = true
  Profile = -> Sketch278
  ReferenceAxis = -> Sketch278 [N_Axis]
  Suppressed = false
  Type = 1
FEATURE [Part::FeaturePython] Connect011  # WARN: FeaturePython — macro-defined, semantics opaque (R4)
  Objects = -> [Array003]
  Tolerance = 0
FEATURE [Part::Offset2D] Offset2D001
  Fill = false
  Intersection = false
  Join = 0
  Mode = 1
  SelfIntersection = false
  Source = -> Connect011
  Value = -23
FEATURE [Part::Offset2D] Offset2D002
  Fill = false
  Intersection = false
  Join = 0
  Mode = 1
  SelfIntersection = false
  Source = -> Offset2D001
  Value = -5
FEATURE [Part::Face] Face
  FaceMakerClass = Part::FaceMakerBullseye
  Sources = -> [Offset2D001]
FEATURE [Part::Face] Face001
  FaceMakerClass = Part::FaceMakerBullseye
  Sources = -> [Offset2D002]
FEATURE [Part::Cut] Cut001
  Base = -> Face
  Tool = -> Face001
FEATURE [Part::Extrusion] Extrude045
  Base = -> Cut001
  Dir = (0,0,1)
  DirMode = 2
  FaceMakerClass = Part::FaceMakerBullseye
  FaceMakerMode = 3
  LengthFwd = 5
  LengthRev = 0
  Solid = false
  Symmetric = false
FEATURE [Part::Compound] Compound066  label="basement_top_plywood_cut1"
  Links = -> [Populate037,Extrude026,Populate043,Extrude045]
FEATURE [PartDesign::Boolean] Boolean023
  BaseFeature = -> Pocket062
  Group = -> [Compound066]
  Refine = true
  Suppressed = false
  Type = 1
  UsePlacement = false
FEATURE [PartDesign::Body] Body006  label="basement_top_plywood"
  AllowCompound = false
  Group = -> [Binder005,Pad001,Sketch112,Sketch113,SubtractivePipe,Pocket062,Sketch166,Sketch216,Boolean023,Local_CS019,Local_CS020]
  Origin = -> Origin010
  Tip = -> Boolean023
FEATURE [App::DocumentObjectGroup] Group014  label="basement_top_Group"
  Group = -> [Body006,Body008,Body122,Body105]
FEATURE [App::DocumentObjectGroup] Group016  label="basement_Group"
  Group = -> [Group014,Group015,Link004]
FEATURE [Sketcher::SketchObject] Sketch280
  ArcFitTolerance = 0
  FullyConstrained = true
  MakeInternals = false
  expr: Constraints[0] = <<pillar_placement>>.Placement.Base.y
  sketch-geometry (1):
    g0: LineSegment StartX=-14.3 StartY=384 StartZ=0 EndX=14.3 EndY=384 EndZ=0
  constraints (3):
    c: DistanceY(g0) = 384
    c: DistanceX(g0,g0) = 28.6
    c: Symmetric(g0,g0,g-2)
FEATURE [Sketcher::SketchObject] Sketch279
  ArcFitTolerance = 0
  ExternalGeometry = -> [Sketch280]
  FullyConstrained = true
  MakeInternals = false
  sketch-geometry (4):
    g0: LineSegment [constr] StartX=0 StartY=0 StartZ=0 EndX=317.831 EndY=183.5 EndZ=0
    g1: ArcOfCircle CenterX=-67.55 CenterY=-39 CenterZ=0 NormalX=0 NormalY=0 NormalZ=1 AngleXU=0 Radius=445 StartAngle=0.523599 EndAngle=0.976538
    g2: ArcOfCircle CenterX=14.3 CenterY=99.9868 CenterZ=0 NormalX=0 NormalY=0 NormalZ=1 AngleXU=0 Radius=284.013 StartAngle=0.976538 EndAngle=1.5708
    g3: LineSegment StartX=173.317 StartY=335.31 StartZ=0 EndX=181.603 EndY=329.711 EndZ=0
  constraints (10):
    c: Coincident(g0,g-1)
    c: Coincident(g0,g1)
    c: Angle(g0) = 0.523599
    c: Tangent(g2,g-3) = 1.5708
    c: Perpendicular(g1,g0)
    c: Distance(g0) = 367
    c: Radius(g1) = 445
    c: Tangent(g3,g1) = 1.5708
    c: Distance(g3) = 10
    c: Tangent(g3,g2) = 1.5708
FEATURE [Part::Mirroring] Part__Mirroring041  label="Sketch279 (Mirror #38)"
  Base = (0,0,0)
  Normal = (-0.5,0.866025,0)
  Source = -> Sketch279
  expr: .Normal.x = sin(-30 deg)
  expr: .Normal.y = cos(-30 deg)
FEATURE [Part::FeaturePython] Populate079  label="Populate 3_elem_polar_array with Sketch280"  # WARN: FeaturePython — macro-defined, semantics opaque (R4)
  Copying = 0
  ExposePlacement = false
  MarkerShape = 1
  MarkerSize = 0
  NumElements = 0
  Object = -> Sketch280
  OutputCompounding = 1
  PlacementsTo = -> PolarArray006
  Referencing = 1
  Type = lattice2PopulateCopies.LatticePopulateCopies
  isLattice = 0
FEATURE [Part::Compound] Compound111
  Links = -> [Part__Mirroring041,Sketch279]
FEATURE [Part::Mirroring] Part__Mirroring042  label="Compound111 (Mirror #39)"
  Base = (0,0,0)
  Normal = (1,0,0)
  Source = -> Compound111
FEATURE [Part::Compound] Compound112
  Links = -> [Populate079,Part__Mirroring042,Compound111]
FEATURE [Part::FeaturePython] Connect012  # WARN: FeaturePython — macro-defined, semantics opaque (R4)
  Objects = -> [Compound112]
  Tolerance = 0
FEATURE [PartDesign::SubShapeBinder] Binder154
  BindCopyOnChange = 0
  BindMode = 0
  ClaimChildren = true
  Context = -> Body152 [Binder154.]
  Fuse = false
  MakeFace = true
  OffsetFill = false
  OffsetIntersection = false
  OffsetJoinType = 0
  OffsetOpenResult = false
  PartialLoad = false
  Relative = true
  Support = -> [Connect012]
  _Version = 2
FEATURE [PartDesign::FeaturePython] BaseBend057  # WARN: FeaturePython — macro-defined, semantics opaque (R4)
  BendSide = 1
  BendSketch = -> Binder154
  MidPlane = false
  Reverse = false
  Suppressed = false
  length = 1214
  radius = 1
  thickness = 1.5
FEATURE [Part::FeaturePython] PolarArray014  # WARN: FeaturePython — macro-defined, semantics opaque (R4)
  Alignment = 0
  AttacherType = Attacher::AttachEngine3D
  CellStart = A1
  Count = 3
  DistributionLaw = 0
  EndInclusive = false
  ExposePlacement = false
  FlipX = false
  FlipZ = false
  GeneratorMode = 0
  MarkerShape = 1
  MarkerSize = 0
  NumElements = 3
  OrientMode = 3
  Placement = pos=(0,0,0) rot=(0,0,1;1.5708rad)
  Radius = 384
  Reverse = false
  SpanEnd = 360
  SpanStart = 0
  Step = 120
  Type = lattice2PolarArray2.PolarArray
  UseArcRadius = false
  UseArcRange = 0
  VSGVersion = 1
  Values = 0.0 | 120.0 | 240.0
  ValuesSource = 2
  isLattice = 1
  expr: Radius = <<pillar_placement>>.Placement.Base.y
FEATURE [Part::FeaturePython] Populate080  label="Populate PolarArray014 with pillar3_pillar3_dec_corner_common001"  # WARN: FeaturePython — macro-defined, semantics opaque (R4)
  Copying = 0
  ExposePlacement = false
  MarkerShape = 1
  MarkerSize = 0
  NumElements = 0
  Object = -> Link047
  OutputCompounding = 1
  PlacementsTo = -> PolarArray014
  Referencing = 0
  Type = lattice2PopulateCopies.LatticePopulateCopies
  isLattice = 0
FEATURE [Part::Compound] Compound113
  Links = -> [Populate080]
FEATURE [PartDesign::Boolean] Boolean057
  BaseFeature = -> BaseBend057
  Group = -> [Compound113]
  Refine = true
  Suppressed = false
  Type = 1
  UsePlacement = true
FEATURE [PartDesign::CoordinateSystem] Local_CS049
  AttacherType = Attacher::AttachEngine3D
  AttachmentSupport = -> [XY_Plane132]
  MapMode = 5
FEATURE [PartDesign::Body] Body152  label="pillar3_plexiglass_outer"
  AllowCompound = false
  Group = -> [Binder154,BaseBend057,Boolean057,Local_CS049]
  Origin = -> Origin133
  Tip = -> Boolean057
FEATURE [PartDesign::CoordinateSystem] Local_CS050  label="hat3_plexiglass_LCS"
  AttacherType = Attacher::AttachEngine3D
  AttachmentSupport = -> [XY_Plane126]
  MapMode = 5
FEATURE [PartDesign::Body] Body146  label="hat3_plexiglass"
  AllowCompound = false
  Group = -> [Binder145,BaseBend055,Extend002,Boolean047,Sketch278,Pocket146,Local_CS050]
  Origin = -> Origin127
  Tip = -> Pocket146
FEATURE [Part::Mirroring] Part__Mirroring043  label="Sketch264 (Mirror #40)"
  Base = (0,0,0)
  Normal = (1,0,0)
  Source = -> Sketch264
FEATURE [Part::Compound] Compound114
  Links = -> [Sketch264,Part__Mirroring043]
FEATURE [Part::Extrusion] Extrude038
  Base = -> Compound114
  Dir = (0,0,1)
  DirMode = 2
  FaceMakerClass = Part::FaceMakerBullseye
  FaceMakerMode = 3
  LengthFwd = 10
  LengthRev = 0
  Placement = pos=(0,-5,1060) rot=(0,0.707107,0.707107;3.14159rad)
  Solid = true
  Symmetric = false
FEATURE [Part::Compound] Compound100  label="pillar3_pillar3_dec_corner_common"
  Links = -> [Extrude038,Populate064,Populate062,Populate061,Populate068]
FEATURE [Part::Compound] Compound099
  Links = -> [Compound100]
FEATURE [PartDesign::Boolean] Boolean049
  BaseFeature = -> Mirrored020
  Group = -> [Compound099]
  Suppressed = false
  Type = 1
  UsePlacement = true
FEATURE [PartDesign::Pocket] Pocket144
  BaseFeature = -> Boolean049
  Direction = (-1,0,0)
  Length = 5
  Length2 = 5
  Midplane = true
  Profile = -> Sketch268
  ReferenceAxis = -> Sketch268 [N_Axis]
  Suppressed = false
  Type = 1
FEATURE [PartDesign::Body] Body141  label="pillar3"
  AllowCompound = false
  Group = -> [Binder141,BaseBend052,Sketch253,Pocket137,Local_CS006,Local_CS007,DatumPlane007,Mirrored020,Local_CS009,Boolean049,Sketch268,Local_CS047,Pocket144]
  Origin = -> Origin122
  Tip = -> Pocket144
FEATURE [Sketcher::SketchObject] Sketch281
  ArcFitTolerance = 0
  AttachmentSupport = -> [XY_Plane123]
  FullyConstrained = true
  MakeInternals = false
  MapMode = 5
  sketch-geometry (2):
    g0: Circle CenterX=100 CenterY=-90 CenterZ=0 NormalX=0 NormalY=0 NormalZ=1 AngleXU=0 Radius=15
    g1: Circle CenterX=-100 CenterY=-90 CenterZ=0 NormalX=0 NormalY=0 NormalZ=1 AngleXU=0 Radius=15
  constraints (5):
    c: Equal(g1,g0)
    c: Diameter(g0) = 30
    c: DistanceX(g0) = 100
    c: DistanceY(g0) = -90
    c: Symmetric(g1,g0,g-2)
FEATURE [Sketcher::SketchObject] Sketch227  label="bottom_bearing_Sketch"
  ArcFitTolerance = 0
  AttachmentSupport = -> [XZ_Plane104]
  FullyConstrained = true
  MakeInternals = false
  MapMode = 5
  Placement = pos=(0,0,0) rot=(1,0,0;1.5708rad)
  sketch-geometry (4):
    g0: LineSegment StartX=37.5 StartY=0 StartZ=0 EndX=50 EndY=0 EndZ=0
    g1: LineSegment StartX=50 StartY=0 StartZ=0 EndX=50 EndY=19 EndZ=0
    g2: LineSegment StartX=50 StartY=19 StartZ=0 EndX=37.5 EndY=19 EndZ=0
    g3: LineSegment StartX=37.5 StartY=19 StartZ=0 EndX=37.5 EndY=0 EndZ=0
  constraints (12):
    c: Coincident(g0,g1)
    c: Coincident(g1,g2)
    c: Coincident(g2,g3)
    c: Coincident(g3,g0)
    c: Horizontal(g0)
    c: Horizontal(g2)
    c: Vertical(g1)
    c: Vertical(g3)
    c: PointOnObject(g0,g-1)
    c: DistanceY(g3,g3) = 19  'height'
    c: DistanceX(g0) = 37.5  'inner_r'
    c: DistanceX(g0) = 50  'outer_r'
FEATURE [PartDesign::Revolution] Revolution002
  Angle = 360
  Angle2 = 60
  Axis = (0,2e-16,1)
  Base = (0,0,0)
  Placement = pos=(0,0,0) rot=(1,0,0;1.5708rad)
  Profile = -> Sketch227
  ReferenceAxis = -> Sketch227 [V_Axis]
  Reversed = true
  Suppressed = false
  Type = 0
FEATURE [PartDesign::Body] Body127  label="bottom_bearing"
  AllowCompound = false
  Group = -> [Sketch227,Revolution002]
  Origin = -> Origin104
  Tip = -> Revolution002
FEATURE [Sketcher::SketchObject] Sketch282
  ArcFitTolerance = 0
  AttachmentSupport = -> [XY_Plane133]
  FullyConstrained = true
  MakeInternals = false
  MapMode = 5
  sketch-geometry (7):
    g0: LineSegment StartX=10.9697 StartY=0 StartZ=0 EndX=5.48483 EndY=9.5 EndZ=0
    g1: LineSegment StartX=5.48483 StartY=9.5 StartZ=0 EndX=-5.48483 EndY=9.5 EndZ=0
    g2: LineSegment StartX=-5.48483 StartY=9.5 StartZ=0 EndX=-10.9697 EndY=0 EndZ=0
    g3: LineSegment StartX=-10.9697 StartY=7e-16 StartZ=0 EndX=-5.48483 EndY=-9.5 EndZ=0
    g4: LineSegment StartX=-5.48483 StartY=-9.5 StartZ=0 EndX=5.48483 EndY=-9.5 EndZ=0
    g5: LineSegment StartX=5.48483 StartY=-9.5 StartZ=0 EndX=10.9697 EndY=0 EndZ=0
    g6: Circle [constr] CenterX=0 CenterY=0 CenterZ=0 NormalX=0 NormalY=0 NormalZ=1 AngleXU=0 Radius=10.9697
  constraints (16):
    c: Coincident(g0,g1)
    c: Coincident(g1,g2)
    c: Coincident(g2,g3)
    c: Coincident(g3,g4)
    c: Coincident(g4,g5)
    c: Coincident(g5,g0)
    c: Equal(g0, g1-g5) x5
    c: PointOnObject(g0,g6)
    c: PointOnObject(g1,g6)
    c: PointOnObject(g2,g6)
    c: PointOnObject(g3,g6)
    c: PointOnObject(g4,g6)
    c: PointOnObject(g5,g6)
    c: Coincident(g6,g-1)
    c: PointOnObject(g5,g-1)
    c: DistanceY(g4,g0) = 19
FEATURE [PartDesign::Pad] Pad051
  Direction = (0,0,1)
  Length = 7
  Length2 = 10
  Profile = -> Sketch282
  ReferenceAxis = -> Sketch282 [N_Axis]
  Suppressed = false
  Type = 0
FEATURE [PartDesign::AdditiveCylinder] Cylinder016
  Angle = 360
  AttacherType = Attacher::AttachEngine3D
  BaseFeature = -> Pad051
  FirstAngle = 0
  Height = 40
  Radius = 6
  SecondAngle = 0
  Suppressed = false
FEATURE [PartDesign::Body] Body153
  AllowCompound = false
  Group = -> [Sketch282,Pad051,Cylinder016]
  Origin = -> Origin134
  Tip = -> Cylinder016
FEATURE [Sketcher::SketchObject] Sketch283
  ArcFitTolerance = 0
  AttachmentSupport = -> [XZ_Plane134]
  FullyConstrained = true
  MakeInternals = false
  MapMode = 5
  Placement = pos=(0,0,0) rot=(1,0,0;1.5708rad)
  sketch-geometry (6):
    g0: LineSegment StartX=9 StartY=0 StartZ=0 EndX=19.35 EndY=0 EndZ=0
    g1: LineSegment StartX=19.35 StartY=0 StartZ=0 EndX=20.35 EndY=7 EndZ=0
    g2: LineSegment StartX=20.35 StartY=7 StartZ=0 EndX=18.15 EndY=22.25 EndZ=0
    g3: LineSegment StartX=18.15 StartY=22.25 StartZ=0 EndX=18.15 EndY=25.5 EndZ=0
    g4: LineSegment StartX=18.15 StartY=25.5 StartZ=0 EndX=9 EndY=25.5 EndZ=0
    g5: LineSegment StartX=9 StartY=25.5 StartZ=0 EndX=9 EndY=0 EndZ=0
  constraints (18):
    c: PointOnObject(g0,g-1)
    c: PointOnObject(g0,g-1)
    c: Coincident(g0,g1)
    c: Coincident(g1,g2)
    c: Coincident(g2,g3)
    c: Vertical(g3)
    c: Coincident(g3,g4)
    c: Horizontal(g4)
    c: Coincident(g4,g5)
    c: Coincident(g5,g0)
    c: Vertical(g5)
    c: DistanceX(g0) = 9
    c: DistanceY(g4) = 25.5
    c: DistanceX(g0) = 19.35
    c: DistanceX(g3) = 18.15
    c: DistanceY(g1) = 7
    c: DistanceY(g3,g3) = 3.25
    c: DistanceX(g1) = 20.35
FEATURE [PartDesign::Revolution] Revolution007
  Angle = 360
  Angle2 = 60
  Axis = (0,2e-16,1)
  Base = (0,0,0)
  Placement = pos=(0,0,0) rot=(1,0,0;1.5708rad)
  Profile = -> Sketch283
  ReferenceAxis = -> Sketch283 [V_Axis]
  Reversed = true
  Suppressed = false
  Type = 0
FEATURE [PartDesign::Plane] DatumPlane010
  AttachmentOffset = pos=(0,0,25.5) rot=(0,0,1;0rad)
  AttachmentSupport = -> [XY_Plane134]
  Length = 60
  MapMode = 5
  Placement = pos=(0,0,25.5) rot=(0,0,1;0rad)
  ResizeMode = 0
  Width = 60
FEATURE [PartDesign::Mirrored] Mirrored025
  BaseFeature = -> Revolution007
  MirrorPlane = -> DatumPlane010
  Originals = -> [Revolution007]
  Placement = pos=(0,0,0) rot=(1,0,0;1.5708rad)
  Refine = true
  Suppressed = false
  TransformMode = 0
FEATURE [PartDesign::Body] Body154
  AllowCompound = false
  Group = -> [Sketch283,Revolution007,DatumPlane010,Mirrored025]
  Origin = -> Origin135
  Tip = -> Mirrored025
FEATURE [Part::Cylinder] Cylinder017  label="hole_5mm"
  Angle = 360
  AttacherType = Attacher::AttachEngine3D
  FirstAngle = 0
  Height = 20
  Radius = 2.5
  SecondAngle = 0
FEATURE [Part::FeaturePython] Populate082  label="Populate PolarArray010 with hole_5mm"  # WARN: FeaturePython — macro-defined, semantics opaque (R4)
  Copying = 0
  ExposePlacement = false
  MarkerShape = 1
  MarkerSize = 0
  NumElements = 0
  Object = -> Cylinder017
  OutputCompounding = 1
  PlacementsTo = -> PolarArray010
  Referencing = 0
  Type = lattice2PopulateCopies.LatticePopulateCopies
  isLattice = 0
FEATURE [Part::FeaturePython] Placment045  # WARN: FeaturePython — macro-defined, semantics opaque (R4)
  AttacherType = Attacher::AttachEngine3D
  ExposePlacement = true
  MarkerShape = 1
  MarkerSize = 20
  NumElements = 1
  Placement = pos=(0,0,0) rot=(0,0,1;0.628319rad)
  Type = lattice2AttachablePlacement.AttachablePlacement
  isLattice = 1
  expr: .Placement.Rotation.Angle = <<PolarArray010>>.Step / 2 * 1 deg
FEATURE [Part::FeaturePython] Populate083  label="Populate Placment045 with PolarArray010"  # WARN: FeaturePython — macro-defined, semantics opaque (R4)
  Copying = 0
  ExposePlacement = false
  MarkerShape = 1
  MarkerSize = 0
  NumElements = 5
  Object = -> PolarArray010
  OutputCompounding = 0
  PlacementsTo = -> Placment045
  Referencing = 0
  Type = lattice2PopulateCopies.LatticePopulateCopies
  isLattice = 1
FEATURE [Part::FeaturePython] Join020  # WARN: FeaturePython — macro-defined, semantics opaque (R4)
  ExposePlacement = false
  Interleave = false
  Links = -> [Populate083,PolarArray010]
  MarkerShape = 1
  MarkerSize = 0
  NumElements = 10
  Type = lattice2JoinArrays.JoinArrays
  isLattice = 1
FEATURE [Part::FeaturePython] Populate084  label="Populate Join020 with hole_3.2mm_extrude"  # WARN: FeaturePython — macro-defined, semantics opaque (R4)
  Copying = 0
  ExposePlacement = false
  MarkerShape = 1
  MarkerSize = 0
  NumElements = 0
  Object = -> Cylinder003
  OutputCompounding = 1
  PlacementsTo = -> Join020
  Referencing = 0
  Type = lattice2PopulateCopies.LatticePopulateCopies
  isLattice = 0
FEATURE [Sketcher::SketchObject] Sketch284
  ArcFitTolerance = 0
  FullyConstrained = true
  MakeInternals = false
  Placement = pos=(0,349.171,0) rot=(0.57735,0.57735,0.57735;2.0944rad)
  expr: .Placement.Base.y = <<basement_sketch>>.Constraints.max_r
  sketch-geometry (5):
    g0: LineSegment StartX=-15 StartY=-1.8e-15 StartZ=0 EndX=0 EndY=0 EndZ=0
    g1: LineSegment StartX=0 StartY=15 StartZ=0 EndX=-15 EndY=-1.8e-15 EndZ=0
    g2: LineSegment StartX=0 StartY=0 StartZ=0 EndX=5 EndY=0 EndZ=0
    g3: LineSegment StartX=5 StartY=0 StartZ=0 EndX=5 EndY=15 EndZ=0
    g4: LineSegment StartX=5 StartY=15 StartZ=0 EndX=0 EndY=15 EndZ=0
  constraints (14):
    c: PointOnObject(g0,g-1)
    c: Coincident(g0,g-1)
    c: PointOnObject(g1,g-2)
    c: Coincident(g1,g0)
    c: DistanceY(g0,g1) = 15
    c: Coincident(g0,g2)
    c: PointOnObject(g2,g-1)
    c: Coincident(g2,g3)
    c: Vertical(g3)
    c: Coincident(g3,g4)
    c: Coincident(g4,g1)
    c: Equal(g0,g3)
    c: Horizontal(g4)
    c: DistanceX(g2,g2) = 5
FEATURE [Part::FeaturePython] Populate085  label="Populate PolarArray with Compound010"  # WARN: FeaturePython — macro-defined, semantics opaque (R4)
  Copying = 0
  ExposePlacement = false
  MarkerShape = 1
  MarkerSize = 0
  NumElements = 0
  Object = -> Compound010
  OutputCompounding = 1
  PlacementsTo = -> PolarArray
  Referencing = 1
  Type = lattice2PopulateCopies.LatticePopulateCopies
  isLattice = 0
FEATURE [Part::FeaturePython] Connect013  # WARN: FeaturePython — macro-defined, semantics opaque (R4)
  Objects = -> [Populate085]
  Tolerance = 0
FEATURE [Part::Sweep] Sweep
  Frenet = true
  Sections = -> [Sketch284]
  Solid = true
  Spine = -> Connect013 [Edge1,Edge2,Edge3,Edge4,Edge5,Edge6,Edge7,Edge8,Edge9,Edge10,Edge11,Edge12,Edge13,Edge14,Edge15,Edge16,Edge17,Edge18]
  Transition = 1
FEATURE [Part::FeaturePython] Populate086  label="Populate PolarArray010 with hole_3.2mm_extrude"  # WARN: FeaturePython — macro-defined, semantics opaque (R4)
  Copying = 0
  ExposePlacement = false
  MarkerShape = 1
  MarkerSize = 0
  NumElements = 0
  Object = -> Cylinder003
  OutputCompounding = 1
  PlacementsTo = -> PolarArray010
  Referencing = 0
  Type = lattice2PopulateCopies.LatticePopulateCopies
  isLattice = 0
FEATURE [Sketcher::SketchObject] Sketch285
  ArcFitTolerance = 0
  AttachmentOffset = pos=(0,370,0) rot=(0,0,1;0rad)
  AttachmentSupport = -> [XY_Plane123]
  FullyConstrained = true
  MakeInternals = false
  MapMode = 5
  Placement = pos=(0,370,0) rot=(0,0,1;0rad)
  sketch-geometry (1):
    g0: Circle CenterX=0 CenterY=0 CenterZ=0 NormalX=0 NormalY=0 NormalZ=1 AngleXU=0 Radius=1.7
  constraints (2):
    c: Coincident(g0,g-1)
    c: Diameter(g0) = 3.4
FEATURE [Sketcher::SketchObject] Sketch286
  ArcFitTolerance = 0
  AttachmentOffset = pos=(0,0,512) rot=(0,0,1;0rad)
  AttachmentSupport = -> [XY_Plane135]
  FullyConstrained = true
  MakeInternals = false
  MapMode = 5
  Placement = pos=(0,0,512) rot=(0,0,1;0rad)
  sketch-geometry (8):
    g0: LineSegment [constr] StartX=0 StartY=0 StartZ=0 EndX=14.5 EndY=8.37158 EndZ=0
    g1: LineSegment [constr] StartX=14.5 StartY=8.37158 StartZ=0 EndX=14.5 EndY=4.90748 EndZ=0
    g2: LineSegment [constr] StartX=14.5 StartY=4.90748 StartZ=0 EndX=29.6554 EndY=-3.84252 EndZ=0
    g3: LineSegment StartX=28.1554 StartY=-6.4406 StartZ=0 EndX=11.5 EndY=3.17543 EndZ=0
    g4: LineSegment StartX=11.5 StartY=3.17543 StartZ=0 EndX=11.5 EndY=22.4075 EndZ=0
    g5: LineSegment [constr] StartX=14.5 StartY=4.90748 StartZ=0 EndX=11.5 EndY=4.90748 EndZ=0
    g6: LineSegment [constr] StartX=14.5 StartY=4.90748 StartZ=0 EndX=13 EndY=2.3094 EndZ=0
    g7: LineSegment [constr] StartX=28.1554 StartY=-6.4406 StartZ=0 EndX=29.6554 EndY=-3.84252 EndZ=0
  constraints (24):
    c: Coincident(g-1,g0)
    c: DistanceX(g0) = 14.5
    c: Angle(g0) = 0.523599
    c: Coincident(g0,g1)
    c: Vertical(g1)
    c: Coincident(g1,g2)
    c: Angle(g2) = -0.523599
    c: Distance(g0,g2) = 3
    c: Distance(g2) = 17.5
    c: Coincident(g3,g4)
    c: Vertical(g4)
    c: Parallel(g3,g2)
    c: Distance(g1,g4) = 3
    c: Coincident(g1,g5)
    c: PointOnObject(g5,g4)
    c: Horizontal(g5)
    c: Coincident(g1,g6)
    c: PointOnObject(g6,g3)
    c: Perpendicular(g3,g6)
    c: Equal(g6,g5)
    c: Equal(g3,g4)
    c: Coincident(g7,g2)
    c: Coincident(g7,g3)
    c: Perpendicular(g3,g7)
FEATURE [PartDesign::FeaturePython] BaseBend058  # WARN: FeaturePython — macro-defined, semantics opaque (R4)
  BendSide = 0
  BendSketch = -> Sketch286
  MidPlane = false
  Reverse = false
  Suppressed = false
  length = 842
  radius = 0.1
  thickness = 0.3
FEATURE [Part::MultiFuse] Fusion006
  Shapes = -> [Compound015]
FEATURE [PartDesign::Boolean] Boolean059
  BaseFeature = -> BaseBend058
  Group = -> [Fusion006]
  Suppressed = false
  Type = 1
  UsePlacement = true
FEATURE [PartDesign::Body] Body155
  AllowCompound = false
  Group = -> [Sketch286,BaseBend058,Boolean059]
  Origin = -> Origin136
  Tip = -> Boolean059
FEATURE [Sketcher::SketchObject] Sketch287
  ArcFitTolerance = 0
  FullyConstrained = true
  MakeInternals = false
  Placement = pos=(0,0,0) rot=(1,0,0;1.5708rad)
  sketch-geometry (14):
    g0: ArcOfCircle CenterX=99.1 CenterY=-9.3 CenterZ=0 NormalX=0 NormalY=0 NormalZ=1 AngleXU=0 Radius=1.6 StartAngle=1.5708 EndAngle=4.71239
    g1: ArcOfCircle CenterX=100.9 CenterY=-9.3 CenterZ=0 NormalX=0 NormalY=0 NormalZ=1 AngleXU=0 Radius=1.6 StartAngle=4.71239 EndAngle=7.85398
    g2: LineSegment StartX=99.1 StartY=-7.7 StartZ=0 EndX=100.9 EndY=-7.7 EndZ=0
    g3: LineSegment StartX=99.1 StartY=-10.9 StartZ=0 EndX=100.9 EndY=-10.9 EndZ=0
    g4: GeomPoint [constr] X=97.5 Y=-9.3 Z=0
    g5: GeomPoint [constr] X=102.5 Y=-9.3 Z=0
    g6: ArcOfCircle CenterX=-25.9 CenterY=-9.3 CenterZ=0 NormalX=0 NormalY=0 NormalZ=1 AngleXU=0 Radius=1.6 StartAngle=1.5708 EndAngle=4.71239
    g7: ArcOfCircle CenterX=-24.1 CenterY=-9.3 CenterZ=0 NormalX=0 NormalY=0 NormalZ=1 AngleXU=0 Radius=1.6 StartAngle=4.71239 EndAngle=7.85398
    g8: LineSegment StartX=-25.9 StartY=-7.7 StartZ=0 EndX=-24.1 EndY=-7.7 EndZ=0
    g9: LineSegment StartX=-25.9 StartY=-10.9 StartZ=0 EndX=-24.1 EndY=-10.9 EndZ=0
    g10: GeomPoint [constr] X=-25 Y=-9.3 Z=0
    g11: GeomPoint [constr] X=100 Y=-9.3 Z=0
    g12: LineSegment [constr] StartX=97.5 StartY=-9.3 StartZ=0 EndX=102.5 EndY=-9.3 EndZ=0
    g13: LineSegment [constr] StartX=-27.5 StartY=-9.3 StartZ=0 EndX=-22.5 EndY=-9.3 EndZ=0
  constraints (32):
    c: Tangent(g0,g2) = 1.5708
    c: Tangent(g0,g3) = -1.5708
    c: Tangent(g1,g2) = 1.5708
    c: Tangent(g1,g3) = -1.5708
    c: Equal(g0,g1)
    c: Horizontal(g2)
    c: PointOnObject(g4,g0)
    c: PointOnObject(g5,g1)
    c: DistanceX(g4,g5) = 5
    c: Diameter(g1) = 3.2
    c: Tangent(g6,g8) = 1.5708
    c: Tangent(g6,g9) = -1.5708
    c: Tangent(g7,g8) = 1.5708
    c: Tangent(g7,g9) = -1.5708
    c: Equal(g6,g7)
    c: Horizontal(g8)
    c: Diameter(g7) = 3.2
    c: DistanceX(g10) = -25
    c: DistanceY(g10) = -9.3
    c: Symmetric(g0,g1,g11)
    c: Coincident(g12,g4)
    c: Coincident(g12,g5)
    c: Horizontal(g12)
    c: PointOnObject(g11,g12)
    c: PointOnObject(g13,g6)
    c: PointOnObject(g13,g7)
    c: Horizontal(g13)
    c: Equal(g13,g12)
    c: Symmetric(g6,g7,g10)
    c: DistanceX(g11) = 100
    c: DistanceY(g11) = -9.3
    c: PointOnObject(g6,g13)
FEATURE [Part::Extrusion] Extrude046
  Base = -> Sketch287
  Dir = (0,-1,2e-16)
  DirMode = 2
  FaceMakerClass = Part::FaceMakerBullseye
  FaceMakerMode = 3
  LengthFwd = 30
  LengthRev = 0
  Solid = true
  Symmetric = true
FEATURE [Part::MultiFuse] Fusion007
  Shapes = -> [Extrude008,Extrude046]
FEATURE [Part::Compound] Compound029
  Links = -> [Fusion007]
  Placement = pos=(0,203.2,424.1) rot=(0.028328,0.028328,-0.999197;1.5716rad)
  expr: .Placement.Rotation.Pitch = <<sink_bend_line>>.FaceAngle
FEATURE [Part::Compound] Compound005  label="part1_part2_common_cut"
  Links = -> [Extrude,Extrude001,Compound022,Compound023,Compound029,Extrude011,Compound074]
FEATURE [Part::FeaturePython] Array  # Draft array (typed FeaturePython)
  AlwaysSyncPlacement = false
  Angle = 240
  ArrayType = 1
  Axis = (0,0,1)
  Base = -> Compound005
  Center = (0,0,0)
  Count = 2
  ExpandArray = false
  Fuse = true
  IntervalAxis = (0,0,0)
  IntervalX = (50,0,0)
  IntervalY = (0,50,0)
  IntervalZ = (0,0,50)
  NumberCircles = 3
  NumberPolar = 2
  NumberX = 2
  NumberY = 2
  NumberZ = 1
  Placement = pos=(0,0,0) rot=(0,0,1;4.18879rad)
  PlacementList = 2 placements: [(0,0,0),(0,0,0)]
  RadialDistance = 50
  ScaleList = (2) [(1,1,1),(1,1,1)]
  Symmetry = 1
  TangentialDistance = 25
FEATURE [Part::Compound] Compound016  label="part1_cut1"
  Links = -> [Compound015,Compound005,Extrude005,Extrude015]
FEATURE [PartDesign::Boolean] Boolean001
  BaseFeature = -> BaseBend
  Group = -> [Compound016]
  Suppressed = false
  Type = 1
  UsePlacement = false
  expr: Group = <<part1_cut1>>._self
FEATURE [PartDesign::Boolean] Boolean002
  BaseFeature = -> Boolean001
  Group = -> [Compound026]
  Refine = true
  Suppressed = false
  Type = 0
  UsePlacement = false
  expr: Group = <<part1_fuse1>>._self
FEATURE [PartDesign::Pocket] Pocket025
  BaseFeature = -> Boolean002
  Direction = (-1,0,0)
  Length = 5
  Length2 = 5
  Midplane = true
  Profile = -> Sketch044
  ReferenceAxis = -> Sketch044 [N_Axis]
  Suppressed = false
  Type = 1
FEATURE [PartDesign::Boolean] Boolean005
  BaseFeature = -> Pocket025
  Group = -> [Compound024]
  Suppressed = false
  Type = 1
  UsePlacement = false
  expr: Group = <<part1_cut2>>._self
FEATURE [PartDesign::Body] Body  label="part1_material_0.30ansi"
  AllowCompound = false
  Group = -> [Binder,BaseBend,Boolean001,Boolean002,Sketch044,Pocket025,Boolean005,Local_CS025,Local_CS026]
  Origin = -> Origin
  Tip = -> Boolean005
FEATURE [Part::Compound] Compound021  label="part2_cut1"
  Links = -> [Array,Compound019,Compound015,Part__Mirroring016]
FEATURE [PartDesign::Boolean] Boolean
  BaseFeature = -> BaseBend001
  Group = -> [Compound021]
  Refine = true
  Suppressed = false
  Type = 1
  UsePlacement = false
  expr: Group = <<part2_cut1>>._self
FEATURE [PartDesign::Boolean] Boolean003
  BaseFeature = -> Boolean
  Group = -> [Compound007]
  Refine = true
  Suppressed = false
  Type = 0
  UsePlacement = false
  expr: Group = <<part2_fuse1>>._self
FEATURE [PartDesign::Boolean] Boolean006
  BaseFeature = -> Boolean003
  Group = -> [Compound025]
  Suppressed = false
  Type = 1
  UsePlacement = false
  expr: Group = <<part2_cut2>>._self
FEATURE [PartDesign::Body] Body001  label="part2_material_0.30ansi"
  AllowCompound = false
  Group = -> [Binder001,BaseBend001,Boolean,Boolean003,Boolean006,Local_CS027,Local_CS028]
  Origin = -> Origin001
  Tip = -> Boolean006
FEATURE [Part::MultiFuse] Fusion008
  Shapes = -> [Fusion007]
FEATURE [PartDesign::Boolean] Boolean009
  BaseFeature = -> BaseBend019
  Group = -> [Fusion008]
  Suppressed = false
  Type = 1
  UsePlacement = false
FEATURE [PartDesign::Body] Body068  label="bot_hor_amplifier_material_0.30ansi"
  AllowCompound = false
  Group = -> [BaseBend019,Sketch049,Boolean009]
  Origin = -> Origin030
  Tip = -> Boolean009
FEATURE [Part::FeaturePython] Placment046  # WARN: FeaturePython — macro-defined, semantics opaque (R4)
  AttacherType = Attacher::AttachEngine3D
  ExposePlacement = true
  MarkerShape = 1
  MarkerSize = 20
  NumElements = 1
  Placement = pos=(47.3,-39.14,0) rot=(0,0,1;0rad)
  Type = lattice2AttachablePlacement.AttachablePlacement
  isLattice = 1
FEATURE [Part::FeaturePython] Placment047  # WARN: FeaturePython — macro-defined, semantics opaque (R4)
  AttacherType = Attacher::AttachEngine3D
  ExposePlacement = true
  MarkerShape = 1
  MarkerSize = 20
  NumElements = 1
  Placement = pos=(136.64,-38.93,0) rot=(0,0,1;0rad)
  Type = lattice2AttachablePlacement.AttachablePlacement
  isLattice = 1
FEATURE [App::Link] Link050  label="Pcb_334e001"
  LinkPlacement = pos=(201.05,53.6,1.6) rot=(0,0,1;-1.5708rad)
  LinkedObject = -> <external ../../horec/el/horec_el3/plate_cut.FCStd>#Clone
  Placement = pos=(201.05,53.6,1.6) rot=(0,0,1;-1.5708rad)
FEATURE [Part::FeaturePython] Placment048  # WARN: FeaturePython — macro-defined, semantics opaque (R4)
  AttacherType = Attacher::AttachEngine3D
  ExposePlacement = true
  MarkerShape = 1
  MarkerSize = 20
  NumElements = 1
  Placement = pos=(57.41,-105.74,0) rot=(0,0,1;0rad)
  Type = lattice2AttachablePlacement.AttachablePlacement
  isLattice = 1
FEATURE [Part::FeaturePython] Placment049  # WARN: FeaturePython — macro-defined, semantics opaque (R4)
  AttacherType = Attacher::AttachEngine3D
  ExposePlacement = true
  MarkerShape = 1
  MarkerSize = 20
  NumElements = 1
  Placement = pos=(136.5,-105.81,0) rot=(0,0,1;0rad)
  Type = lattice2AttachablePlacement.AttachablePlacement
  isLattice = 1
FEATURE [Part::FeaturePython] Join021  # WARN: FeaturePython — macro-defined, semantics opaque (R4)
  ExposePlacement = false
  Interleave = false
  Links = -> [Placment046,Placment049,Placment047,Placment048]
  MarkerShape = 1
  MarkerSize = 20
  NumElements = 4
  Type = lattice2JoinArrays.JoinArrays
  isLattice = 1
FEATURE [Part::FeaturePython] Populate087  label="Populate Join021 with hole_3.4mm_extrude"  # WARN: FeaturePython — macro-defined, semantics opaque (R4)
  Copying = 0
  ExposePlacement = false
  MarkerShape = 1
  MarkerSize = 0
  NumElements = 0
  Object = -> Extrude019
  OutputCompounding = 1
  PlacementsTo = -> Join021
  Referencing = 0
  Type = lattice2PopulateCopies.LatticePopulateCopies
  isLattice = 0
FEATURE [Part::FeaturePython] Placment050  # WARN: FeaturePython — macro-defined, semantics opaque (R4)
  AttacherType = Attacher::AttachEngine3D
  ExposePlacement = true
  MarkerShape = 1
  MarkerSize = 20
  NumElements = 1
  Placement = pos=(55,170,0) rot=(0,0,1;0rad)
  Type = lattice2AttachablePlacement.AttachablePlacement
  isLattice = 1
FEATURE [Part::FeaturePython] Placment051  # WARN: FeaturePython — macro-defined, semantics opaque (R4)
  AttacherType = Attacher::AttachEngine3D
  ExposePlacement = true
  MarkerShape = 1
  MarkerSize = 20
  NumElements = 1
  Placement = pos=(119,59.5,0) rot=(0,0,1;0rad)
  Type = lattice2AttachablePlacement.AttachablePlacement
  isLattice = 1
  expr: .Placement.Base.y = .Placement.Base.x * sin(30 deg)
FEATURE [Part::FeaturePython] Mirror016  label="Mirror016 of Placment050"  # WARN: FeaturePython — macro-defined, semantics opaque (R4)
  ExposePlacement = false
  FlipX = false
  FlipY = true
  FlipZ = false
  MarkerShape = 1
  MarkerSize = 20
  NumElements = 1
  Object = -> Placment050
  ObjectTraversal = 0
  Placement = pos=(0,0,0) rot=(0,0,1;1.0472rad)
  Type = lattice2Mirror.LatticeMirror
  isLattice = 1
FEATURE [Part::FeaturePython] Join022  # WARN: FeaturePython — macro-defined, semantics opaque (R4)
  ExposePlacement = false
  Interleave = false
  Links = -> [Placment050,Placment051,Mirror016]
  MarkerShape = 1
  MarkerSize = 0
  NumElements = 3
  Type = lattice2JoinArrays.JoinArrays
  isLattice = 1
FEATURE [Part::FeaturePython] Populate088  label="Populate 3_elem_polar_array with Join022"  # WARN: FeaturePython — macro-defined, semantics opaque (R4)
  Copying = 0
  ExposePlacement = false
  MarkerShape = 1
  MarkerSize = 0
  NumElements = 9
  Object = -> Join022
  OutputCompounding = 0
  PlacementsTo = -> PolarArray006
  Referencing = 1
  Type = lattice2PopulateCopies.LatticePopulateCopies
  isLattice = 1
FEATURE [Part::FeaturePython] Populate089  label="Populate Populate 3_elem_polar_array with Join022 with hole_5_mm_extrude"  # WARN: FeaturePython — macro-defined, semantics opaque (R4)
  Copying = 0
  ExposePlacement = false
  MarkerShape = 1
  MarkerSize = 0
  NumElements = 0
  Object = -> Extrude023
  OutputCompounding = 1
  PlacementsTo = -> Populate088
  Referencing = 0
  Type = lattice2PopulateCopies.LatticePopulateCopies
  isLattice = 0
FEATURE [Part::MultiFuse] Fusion003  label="basement_spacer_cut1"
  Shapes = -> [Populate089,Body153]
FEATURE [PartDesign::Boolean] Boolean018
  BaseFeature = -> Pad026
  Group = -> [Fusion003]
  Suppressed = false
  Type = 1
  UsePlacement = false
FEATURE [PartDesign::Body] Body114  label="basement_v2_spacer"
  AllowCompound = false
  Group = -> [Binder123,Pad026,Boolean018]
  Origin = -> Origin089
  Tip = -> Boolean018
FEATURE [PartDesign::SubShapeBinder] Binder155
  BindCopyOnChange = 0
  BindMode = 0
  ClaimChildren = true
  Context = -> Part020 [Body156.Binder155.]
  Fuse = false
  MakeFace = true
  OffsetFill = false
  OffsetIntersection = false
  OffsetJoinType = 0
  OffsetOpenResult = false
  PartialLoad = false
  Relative = true
  Support = -> [Array009]
  _Version = 2
FEATURE [PartDesign::Pad] Pad052
  Direction = (0,0,1)
  Length = 18
  Length2 = 10
  Profile = -> Binder155
  Refine = true
  Suppressed = false
  Type = 0
FEATURE [Part::FeaturePython] Tube  # WARN: FeaturePython — macro-defined, semantics opaque (R4)
  AttacherType = Attacher::AttachEngine3D
  Height = 10
  InnerRadius = 37
  OuterRadius = 50.5
  Placement = pos=(0,0,16) rot=(0,0,1;0rad)
FEATURE [Part::Cylinder] Cylinder018  label="hole_12mm"
  Angle = 360
  AttacherType = Attacher::AttachEngine3D
  FirstAngle = 0
  Height = 20
  Radius = 6
  SecondAngle = 0
FEATURE [Part::MultiFuse] Fusion009  label="basement_spacer_cut002"
  Shapes = -> [Populate089,Tube,Cylinder018]
FEATURE [PartDesign::Boolean] Boolean060
  BaseFeature = -> Pad052
  Group = -> [Fusion009]
  Suppressed = false
  Type = 1
  UsePlacement = false
FEATURE [PartDesign::Body] Body156  label="basement_v2_spacer001"
  AllowCompound = false
  Group = -> [Binder155,Pad052,Boolean060]
  Origin = -> Origin137
  Tip = -> Boolean060
FEATURE [Part::FeaturePython] Populate090  label="Populate Populate 3_elem_polar_array with Join022 with hole_3.2_mm_extrude"  # WARN: FeaturePython — macro-defined, semantics opaque (R4)
  Copying = 0
  ExposePlacement = false
  MarkerShape = 1
  MarkerSize = 0
  NumElements = 0
  Object = -> Cylinder001
  OutputCompounding = 1
  PlacementsTo = -> Populate088
  Referencing = 0
  Type = lattice2PopulateCopies.LatticePopulateCopies
  isLattice = 0
FEATURE [Part::MultiFuse] Fusion004
  Shapes = -> [Populate037,Extrude045,Sweep,Populate090]
FEATURE [PartDesign::Boolean] Boolean058
  BaseFeature = -> Pad027
  Group = -> [Fusion004]
  Suppressed = false
  Type = 1
  UsePlacement = true
FEATURE [PartDesign::Body] Body116  label="basement_v2_top"
  AllowCompound = false
  Group = -> [Binder124,Pad027,Boolean058]
  Origin = -> Origin091
  Tip = -> Boolean058
FEATURE [App::Link] Link051  label="Body156"
  LinkPlacement = pos=(0,232,0) rot=(0,0,1;0rad)
  LinkedObject = -> <external prima_jamb.FCStd>#Body
  Placement = pos=(0,232,0) rot=(0,0,1;0rad)
FEATURE [Part::FeaturePython] Placment052  # WARN: FeaturePython — macro-defined, semantics opaque (R4)
  AttacherType = Attacher::AttachEngine3D
  ExposePlacement = true
  MarkerShape = 1
  MarkerSize = 10
  NumElements = 1
  Placement = pos=(0,232,0) rot=(0,0,1;0rad)
  Type = lattice2AttachablePlacement.AttachablePlacement
  isLattice = 1
FEATURE [Part::FeaturePython] Populate091  label="Populate Placment052 with hole_8mm_extrude"  # WARN: FeaturePython — macro-defined, semantics opaque (R4)
  Copying = 0
  ExposePlacement = false
  MarkerShape = 1
  MarkerSize = 0
  NumElements = 0
  Object = -> Extrude031
  OutputCompounding = 2
  PlacementsTo = -> Placment052
  Referencing = 0
  Type = lattice2PopulateCopies.LatticePopulateCopies
  isLattice = 0
FEATURE [Part::MultiFuse] Fusion005
  Shapes = -> [Populate033,Populate028,Cylinder011,Cylinder018,Populate090,Populate091]
FEATURE [PartDesign::Boolean] Boolean019
  BaseFeature = -> PolarPattern011
  Group = -> [Fusion005]
  Suppressed = false
  Type = 1
  UsePlacement = false
FEATURE [PartDesign::Body] Body117  label="basement_v2_bottom"
  AllowCompound = false
  Group = -> [Binder125,Pad028,Sketch204,Hole021,PolarPattern011,Boolean019]
  Origin = -> Origin092
  Tip = -> Boolean019
FEATURE [App::Part] Part020  label="basement_v2"
  Group = -> [Body114,Body116,Body117,Body156]
  Origin = -> Origin088
FEATURE [Part::FeaturePython] Placment053  label="filter_placement"  # WARN: FeaturePython — macro-defined, semantics opaque (R4)
  AttacherType = Attacher::AttachEngine3D
  ExposePlacement = true
  MarkerShape = 1
  MarkerSize = 50
  NumElements = 1
  Placement = pos=(0,100,0) rot=(0,0,1;0rad)
  Type = lattice2AttachablePlacement.AttachablePlacement
  isLattice = 1
FEATURE [PartDesign::FeaturePython] BaseBend059  # WARN: FeaturePython — macro-defined, semantics opaque (R4)
  BendSide = 0
  BendSketch = -> Binder146
  MidPlane = false
  Reverse = false
  Suppressed = false
  length = 100
  radius = 0.1
  thickness = 0.3
FEATURE [PartDesign::Pocket] Pocket147
  BaseFeature = -> BaseBend059
  Direction = (0,0,-1)
  Length = 5
  Length2 = 5
  Profile = -> Sketch285
  ReferenceAxis = -> Sketch285 [N_Axis]
  Reversed = true
  Suppressed = false
  Type = 0
FEATURE [PartDesign::PolarPattern] PolarPattern012
  Angle = 360
  Axis = -> Z_Axis123
  BaseFeature = -> Pocket147
  Mode = 0
  Occurrences = 3
  Offset = 120
  Originals = -> [Pocket147]
  Suppressed = false
  TransformMode = 0
FEATURE [PartDesign::SubShapeBinder] Binder156
  BindCopyOnChange = 0
  BindMode = 0
  ClaimChildren = false
  Fuse = false
  MakeFace = true
  OffsetFill = false
  OffsetIntersection = false
  OffsetJoinType = 0
  OffsetOpenResult = false
  PartialLoad = false
  Relative = true
  Support = -> [<external filter.FCStd>#Sketch003]
  _Version = 2
FEATURE [Part::Extrusion] Extrude047
  Base = -> Binder156
  Dir = (0,0,1)
  DirMode = 2
  FaceMakerClass = Part::FaceMakerBullseye
  FaceMakerMode = 3
  LengthFwd = 10
  LengthRev = 0
  Solid = false
  Symmetric = false
FEATURE [Part::FeaturePython] Placment054  # WARN: FeaturePython — macro-defined, semantics opaque (R4)
  AttacherType = Attacher::AttachEngine3D
  ExposePlacement = true
  MarkerShape = 1
  MarkerSize = 20
  NumElements = 1
  Placement = pos=(0,0,-28.7) rot=(0,0,1;0rad)
  Type = lattice2AttachablePlacement.AttachablePlacement
  isLattice = 1
FEATURE [Part::FeaturePython] Populate093  label="Populate filter_placement with Placment054"  # WARN: FeaturePython — macro-defined, semantics opaque (R4)
  Copying = 0
  ExposePlacement = false
  MarkerShape = 1
  MarkerSize = 10
  NumElements = 1
  Object = -> Placment054
  OutputCompounding = 0
  PlacementsTo = -> Placment053
  Referencing = 0
  Type = lattice2PopulateCopies.LatticePopulateCopies
  isLattice = 1
FEATURE [App::Link] Link052  label="Join"
  LinkedObject = -> <external filter.FCStd>#Join
FEATURE [Part::FeaturePython] Populate094  label="Populate Populate filter_placement with Placment054 with Join"  # WARN: FeaturePython — macro-defined, semantics opaque (R4)
  Copying = 0
  ExposePlacement = false
  MarkerShape = 1
  MarkerSize = 0
  NumElements = 3
  Object = -> Link052
  OutputCompounding = 0
  PlacementsTo = -> Populate093
  Referencing = 0
  Type = lattice2PopulateCopies.LatticePopulateCopies
  isLattice = 1
FEATURE [Part::FeaturePython] Populate095  label="Populate Populate Populate filter_placement with Placment054 with Join with hole_3.4mm_extrude"  # WARN: FeaturePython — macro-defined, semantics opaque (R4)
  Copying = 0
  ExposePlacement = false
  MarkerShape = 1
  MarkerSize = 0
  NumElements = 0
  Object = -> Extrude019
  OutputCompounding = 1
  PlacementsTo = -> Populate094
  Referencing = 0
  Type = lattice2PopulateCopies.LatticePopulateCopies
  isLattice = 0
FEATURE [Part::MultiFuse] Fusion010
  Shapes = -> [Populate095]
FEATURE [Part::Box] Box  label="Cube"
  AttacherType = Attacher::AttachEngine3D
  Height = 50
  Length = 120
  Placement = pos=(-60,40,-30) rot=(0,0,1;0rad)
  Width = 120
  expr: .Placement.Base.x = -Length / 2
FEATURE [App::Link] Link053  label="Join023"
  LinkedObject = -> <external filter.FCStd>#Join001
FEATURE [Part::FeaturePython] PolarArray015  # WARN: FeaturePython — macro-defined, semantics opaque (R4)
  Alignment = 0
  AttacherType = Attacher::AttachEngine3D
  CellStart = A1
  Count = 4
  DistributionLaw = 0
  EndInclusive = false
  ExposePlacement = false
  FlipX = false
  FlipZ = false
  GeneratorMode = 0
  MarkerShape = 1
  MarkerSize = 0
  NumElements = 4
  OrientMode = 2
  Radius = 50
  Reverse = false
  SpanEnd = 360
  SpanStart = 0
  Step = 90
  Type = lattice2PolarArray2.PolarArray
  UseArcRadius = false
  UseArcRange = 0
  VSGVersion = 1
  Values = 0.0 | 90.0 | 180.0 | 270.0
  ValuesSource = 2
  isLattice = 1
FEATURE [Part::FeaturePython] Populate096  label="Populate PolarArray015 with Join023"  # WARN: FeaturePython — macro-defined, semantics opaque (R4)
  Copying = 0
  ExposePlacement = false
  MarkerShape = 1
  MarkerSize = 0
  NumElements = 8
  Object = -> Link053
  OutputCompounding = 0
  PlacementsTo = -> PolarArray015
  Referencing = 1
  Type = lattice2PopulateCopies.LatticePopulateCopies
  isLattice = 1
FEATURE [Part::FeaturePython] Populate097  label="Populate filter_placement with Populate PolarArray015 with Join023"  # WARN: FeaturePython — macro-defined, semantics opaque (R4)
  Copying = 0
  ExposePlacement = false
  MarkerShape = 1
  MarkerSize = 0
  NumElements = 8
  Object = -> Populate096
  OutputCompounding = 0
  PlacementsTo = -> Placment053
  Referencing = 0
  Type = lattice2PopulateCopies.LatticePopulateCopies
  isLattice = 1
FEATURE [Part::FeaturePython] Populate098  label="Populate Populate filter_placement with Populate PolarArray015 with Join023 with hole_3.4mm_extrude"  # WARN: FeaturePython — macro-defined, semantics opaque (R4)
  Copying = 0
  ExposePlacement = false
  MarkerShape = 1
  MarkerSize = 0
  NumElements = 0
  Object = -> Extrude019
  OutputCompounding = 1
  PlacementsTo = -> Populate097
  Referencing = 0
  Type = lattice2PopulateCopies.LatticePopulateCopies
  isLattice = 0
FEATURE [App::Link] Link054  label="bottom_cut_sketch"
  LinkedObject = -> <external filter.FCStd>#Sketch005
FEATURE [Part::Extrusion] Extrude048
  Base = -> Link054
  Dir = (0,0,1)
  DirMode = 2
  FaceMakerClass = Part::FaceMakerBullseye
  FaceMakerMode = 3
  LengthFwd = 10
  LengthRev = 0
  Solid = true
  Symmetric = false
FEATURE [Part::FeaturePython] Populate092  label="Populate filter_placement with Extrude047"  # WARN: FeaturePython — macro-defined, semantics opaque (R4)
  Copying = 0
  ExposePlacement = false
  MarkerShape = 1
  MarkerSize = 0
  NumElements = 0
  Object = -> Extrude048
  OutputCompounding = 2
  PlacementsTo = -> Placment053
  Referencing = 0
  Type = lattice2PopulateCopies.LatticePopulateCopies
  isLattice = 0
FEATURE [Part::Compound] Compound115
  Links = -> [Populate092]
FEATURE [PartDesign::Boolean] Boolean061
  BaseFeature = -> PolarPattern012
  Group = -> [Compound115]
  Suppressed = false
  Type = 1
  UsePlacement = true
FEATURE [PartDesign::FeaturePython] Bend031  # WARN: FeaturePython — macro-defined, semantics opaque (R4)
  AutoMiter = true
  BaseFeature = -> Boolean061
  BendType = 0
  LengthList = [29]
  LengthSpec = 1
  NonperforationMaxLength = 5
  Perforate = false
  PerforationAngle = 0
  PerforationInitialLength = 5
  PerforationMaxLength = 5
  ReliefFactor = 0.7
  Suppressed = false
  UseReliefFactor = false
  angle = 90
  baseObject = -> Boolean061 [Edge41,Edge43]
  bendAList = [90]
  extend1 = 0
  extend2 = 0
  gap1 = 3.2
  gap2 = 3.2
  invert = false
  kfactor = 0.5
  length = 29
  maxExtendDist = 5
  minGap = 0.2
  minReliefGap = 1
  miterangle1 = 0
  miterangle2 = 0
  offset = 0
  radius = 0.1
  reliefType = 0
  reliefd = 1
  reliefw = 0.8
  sketchflip = false
  sketchinvert = false
  unfold = false
  expr: radius = BaseBend059.radius
FEATURE [PartDesign::Boolean] Boolean062
  BaseFeature = -> Bend031
  Group = -> [Fusion010]
  Suppressed = false
  Type = 1
  UsePlacement = true
FEATURE [PartDesign::Body] Body143  label="hat3_cap"
  AllowCompound = false
  Group = -> [Binder146,Local_CS044,Local_CS045,Sketch281,Sketch285,BaseBend059,Pocket147,PolarPattern012,Boolean061,Bend031,Boolean062]
  Origin = -> Origin124
  Tip = -> Boolean062
FEATURE [Part::MultiCommon] Common
  Shapes = -> [Box,Body143]
FEATURE [PartDesign::SubShapeBinder] Binder054  label="socket_fixture"
  BindCopyOnChange = 0
  BindMode = 0
  ClaimChildren = false
  Context = -> Part010 [Body075.Binder054.]
  Fuse = false
  MakeFace = true
  OffsetFill = false
  OffsetIntersection = false
  OffsetJoinType = 0
  OffsetOpenResult = false
  PartialLoad = false
  Placement = pos=(69,65,0) rot=(0,0,1;3.14159rad)
  Relative = false
  Support = -> [<external socket_fixture.FCStd>#Sketch003]
  _Version = 2
  expr: Support = socket_fixture#<<fix_holes>>._self
FEATURE [PartDesign::SubShapeBinder] Binder055  label="driver_fixture"
  BindCopyOnChange = 0
  BindMode = 0
  ClaimChildren = false
  Context = -> Part010 [Body075.Binder055.]
  Fuse = false
  MakeFace = true
  OffsetFill = false
  OffsetIntersection = false
  OffsetJoinType = 0
  OffsetOpenResult = false
  PartialLoad = false
  Placement = pos=(-24,152,0) rot=(0,0,1;0rad)
  Relative = false
  Support = -> [<external UET-VAS-060A20_12V_IP20.FCStd>#Sketch001]
  _Version = 2
  expr: Support = <<UET-VAS-060A20_12V_IP20>>#<<holes>>._self
FEATURE [PartDesign::SubShapeBinder] Binder135
  BindCopyOnChange = 0
  BindMode = 0
  ClaimChildren = false
  Context = -> Part010 [Body075.Binder135.]
  Fuse = false
  MakeFace = true
  OffsetFill = false
  OffsetIntersection = false
  OffsetJoinType = 0
  OffsetOpenResult = false
  PartialLoad = false
  Placement = pos=(35,150,0) rot=(0,0,1;0rad)
  Relative = false
  Support = -> [Sketch226]
  _Version = 2
  expr: Support = <<UV_driver_holder_holes_Sketch>>._self
FEATURE [App::Link] Link055  label="PCB_fix_holes"
  LinkPlacement = pos=(99,-71,0) rot=(0,0,1;1.5708rad)
  LinkedObject = -> <external ../../horec/el/horec_el3/plate_cut2.FCStd>#Extrude001
  Placement = pos=(99,-71,0) rot=(0,0,1;1.5708rad)
FEATURE [Part::Compound] Compound084  label="hat1_cut1"
  Links = -> [Extrude032,Populate092,Populate098,Populate073,Link055]
FEATURE [PartDesign::Boolean] Boolean035
  BaseFeature = -> Hole015
  Group = -> [Compound084]
  Suppressed = false
  Type = 1
  UsePlacement = false
FEATURE [PartDesign::Body] Body075  label="hat_bottom_material_0.30ansi"
  AllowCompound = false
  Group = -> [Binder039,Pad009,Binder040,Pocket032,Pocket054,PolarPattern,Sketch098,Hole015,Binder054,Binder055,Sketch108,Binder135,Boolean035]
  Origin = -> Origin038
  Tip = -> Boolean035
FEATURE [Sketcher::SketchObject] Sketch288
  ArcFitTolerance = 0
  FullyConstrained = true
  MakeInternals = false
  sketch-geometry (5):
    g0: LineSegment StartX=-44.5 StartY=-44.5 StartZ=0 EndX=44.5 EndY=-44.5 EndZ=0
    g1: LineSegment StartX=44.5 StartY=-44.5 StartZ=0 EndX=44.5 EndY=44.5 EndZ=0
    g2: LineSegment StartX=44.5 StartY=44.5 StartZ=0 EndX=-44.5 EndY=44.5 EndZ=0
    g3: LineSegment StartX=-44.5 StartY=44.5 StartZ=0 EndX=-44.5 EndY=-44.5 EndZ=0
    g4: GeomPoint [constr] X=0 Y=0 Z=0
  constraints (12):
    c: Coincident(g0,g1)
    c: Coincident(g1,g2)
    c: Coincident(g2,g3)
    c: Coincident(g3,g0)
    c: Horizontal(g0)
    c: Horizontal(g2)
    c: Vertical(g1)
    c: Vertical(g3)
    c: Symmetric(g2,g0,g4)
    c: Coincident(g4,g-1)
    c: DistanceX(g0,g0) = 89
    c: Equal(g1,g0)
FEATURE [Part::Extrusion] Extrude049
  Base = -> Sketch288
  Dir = (0,0,1)
  DirMode = 2
  FaceMakerClass = Part::FaceMakerBullseye
  FaceMakerMode = 3
  LengthFwd = 10
  LengthRev = 0
  Solid = true
  Symmetric = false
FEATURE [Part::FeaturePython] Populate099  label="Populate filter_placement with Extrude049"  # WARN: FeaturePython — macro-defined, semantics opaque (R4)
  Copying = 0
  ExposePlacement = false
  MarkerShape = 1
  MarkerSize = 0
  NumElements = 0
  Object = -> Extrude049
  OutputCompounding = 2
  PlacementsTo = -> Placment053
  Referencing = 0
  Type = lattice2PopulateCopies.LatticePopulateCopies
  isLattice = 0
FEATURE [Part::Compound] Compound116
  Links = -> [Populate099]
FEATURE [PartDesign::Boolean] Boolean063
  BaseFeature = -> Pad010
  Group = -> [Compound116]
  Suppressed = false
  Type = 1
  UsePlacement = false
FEATURE [PartDesign::FeaturePython] Bend032  # WARN: FeaturePython — macro-defined, semantics opaque (R4)
  AutoMiter = true
  BaseFeature = -> Boolean063
  BendType = 0
  LengthList = [25]
  LengthSpec = 0
  NonperforationMaxLength = 5
  Perforate = false
  PerforationAngle = 0
  PerforationInitialLength = 5
  PerforationMaxLength = 5
  ReliefFactor = 0.7
  Suppressed = false
  UseReliefFactor = false
  angle = 90
  baseObject = -> Boolean063 [Edge33,Edge35]
  bendAList = [90]
  extend1 = 0
  extend2 = 0
  gap1 = 3.2
  gap2 = 3.2
  invert = false
  kfactor = 0.5
  length = 25
  maxExtendDist = 5
  minGap = 0.2
  minReliefGap = 1
  miterangle1 = 0
  miterangle2 = 0
  offset = 0
  radius = 0.1
  reliefType = 0
  reliefd = 1
  reliefw = 0.8
  sketchflip = false
  sketchinvert = false
  unfold = false
FEATURE [Part::MultiFuse] Fusion011
  Shapes = -> [Populate095]
FEATURE [PartDesign::Boolean] Boolean064
  BaseFeature = -> Bend032
  Group = -> [Fusion011]
  Suppressed = false
  Type = 1
  UsePlacement = false
FEATURE [PartDesign::Body] Body076  label="hat_top"
  AllowCompound = false
  Group = -> [Binder041,Pad010,Sketch072,Boolean063,Bend032,Boolean064]
  Origin = -> Origin039
  Placement = pos=(0,0,87) rot=(0,0,1;0rad)
  Tip = -> Boolean064
FEATURE [App::Part] Part010  label="hat"
  Group = -> [Body075,Body076,Body078]
  Origin = -> Origin042
  Placement = pos=(0,0,1503) rot=(0,0,1;0rad)
FEATURE [App::Link] Link056  label="air_duct"
  LinkedObject = -> <external filter.FCStd>#Body003
FEATURE [Part::FeaturePython] Populate100  label="Populate Populate filter_placement with Placment054 with air_duct"  # WARN: FeaturePython — macro-defined, semantics opaque (R4)
  Copying = 0
  ExposePlacement = false
  MarkerShape = 1
  MarkerSize = 0
  NumElements = 0
  Object = -> Link056
  OutputCompounding = 1
  PlacementsTo = -> Populate093
  Referencing = 0
  Type = lattice2PopulateCopies.LatticePopulateCopies
  isLattice = 0
FEATURE [App::Link] Link057  label="fix_holes001"
  LinkPlacement = pos=(93,-73,0) rot=(0,0,1;1.5708rad)
  LinkedObject = -> <external ../../horec/el/horec_el3/plate_cut2.FCStd>#Extrude001
  Placement = pos=(93,-73,0) rot=(0,0,1;1.5708rad)
FEATURE [Part::Compound] Compound102
  Links = -> [Populate071,Populate072,Populate073,Extrude032,Cylinder013,Populate092,Populate098,Link057]
FEATURE [PartDesign::Boolean] Boolean050
  BaseFeature = -> Pad045
  Group = -> [Compound102]
  Suppressed = false
  Type = 1
  UsePlacement = true
FEATURE [PartDesign::Body] Body142  label="hat3_base"
  AllowCompound = false
  Group = -> [Binder142,Pad045,Boolean050,Local_CS037,Local_CS038]
  Origin = -> Origin123
  Tip = -> Boolean050
FEATURE [Part::MultiCommon] Common001
  Shapes = -> [Body142,Box]
FEATURE [App::DocumentObjectGroup] Group013  label="pillar3_hat_Group"
  Group = -> [Body146,Common,Common001]
FEATURE [App::DocumentObjectGroup] Group012  label="pillar3_Group"
  Group = -> [Body141,Body144,Group013,Body145,Body147,Spreadsheet005,Body152]
FEATURE [TechDraw::DrawViewDimension] Dimension
  AngleOverride = false
  Arbitrary = false
  ArbitraryTolerances = false
  BoxCorners = (2) [(-35.25,-33.5,-1e-07),(35.25,33.5,1e-07)]
  EqualTolerance = true
  ExtensionAngle = 0
  FormatSpec = %.2w
  FormatSpecOverTolerance = %+.2w
  FormatSpecUnderTolerance = %+.2w
  Inverted = false
  LineAngle = 0
  LockPosition = false
  MeasureType = 1
  OverTolerance = 0
  References2D = -> [View]
  Rotation = 0
  ScaleType = 0
  TheoreticalExact = false
  Type = 2
  UnderTolerance = 0
  X = 43.1019
  Y = -36.6605
FEATURE [TechDraw::DrawViewDimension] Dimension041
  AngleOverride = false
  Arbitrary = false
  ArbitraryTolerances = false
  BoxCorners = (2) [(-35.25,-33.5,-1e-07),(35.25,33.5,1e-07)]
  EqualTolerance = true
  ExtensionAngle = 0
  FormatSpec = %.2w
  FormatSpecOverTolerance = %+.2w
  FormatSpecUnderTolerance = %+.2w
  Inverted = false
  LineAngle = 0
  LockPosition = false
  MeasureType = 1
  OverTolerance = 0
  References2D = -> [View]
  Rotation = 0
  ScaleType = 0
  TheoreticalExact = false
  Type = 2
  UnderTolerance = 0
  X = 43.0406
  Y = 4.08304
FEATURE [TechDraw::DrawViewSection] SectionView  label="Section  - "
  BaseView = -> View
  CoarseView = false
  CutSurfaceDisplay = 2
  Direction = (-1,0,-1e-16)
  FileGeomPattern = <path>
  FileHatchPattern = <path>
  Focus = 100
  FuseBeforeCut = false
  HardHidden = false
  HatchOffset = (0,0,0)
  HatchRotation = 0
  HatchScale = 1
  IsoCount = 0
  IsoHidden = false
  IsoVisible = false
  LockPosition = false
  NameGeomPattern = Diamond
  Perspective = false
  Rotation = -90
  ScaleType = 0
  ScrubCount = 0
  SeamHidden = false
  SeamVisible = true
  SectionDirection = 4
  SectionLineStretch = 1
  SectionNormal = (-1,0,-1e-16)
  SectionOrigin = (0,0,33.5)
  SmoothHidden = false
  SmoothVisible = true
  Source = -> [Body123]
  TrimAfterCut = false
  UsePreviousCut = false
  X = 148.5
  XDirection = (1e-16,0,-1)
  Y = 105
FEATURE [TechDraw::DrawViewDimension] Dimension042
  AngleOverride = false
  Arbitrary = false
  ArbitraryTolerances = false
  BoxCorners = (2) [(-35.25,-33.5,-1e-07),(35.25,33.5,1e-07)]
  EqualTolerance = true
  ExtensionAngle = 0
  FormatSpec = %.2w
  FormatSpecOverTolerance = %+.2w
  FormatSpecUnderTolerance = %+.2w
  Inverted = false
  LineAngle = 0
  LockPosition = false
  MeasureType = 1
  OverTolerance = 0
  References2D = -> [SectionView]
  Rotation = 0
  ScaleType = 0
  TheoreticalExact = false
  Type = 1
  UnderTolerance = 0
  X = -0.680992
  Y = 43.2963
FEATURE [TechDraw::DrawViewDimension] Dimension043
  AngleOverride = false
  Arbitrary = false
  ArbitraryTolerances = false
  BoxCorners = (2) [(-35.25,-33.5,-1e-07),(35.25,33.5,1e-07)]
  EqualTolerance = true
  ExtensionAngle = 0
  FormatSpec = %.2w
  FormatSpecOverTolerance = %+.2w
  FormatSpecUnderTolerance = %+.2w
  Inverted = false
  LineAngle = 0
  LockPosition = false
  MeasureType = 1
  OverTolerance = 0
  References2D = -> [SectionView]
  Rotation = 0
  ScaleType = 0
  TheoreticalExact = false
  Type = 1
  UnderTolerance = 0
  X = -1.07013
  Y = 53.2194
FEATURE [TechDraw::DrawViewDimension] Dimension044
  AngleOverride = false
  Arbitrary = false
  ArbitraryTolerances = false
  BoxCorners = (2) [(-35.25,-33.5,-1e-07),(35.25,33.5,1e-07)]
  EqualTolerance = true
  ExtensionAngle = 0
  FormatSpec = %.2w
  FormatSpecOverTolerance = %+.2w
  FormatSpecUnderTolerance = %+.2w
  Inverted = false
  LineAngle = 0
  LockPosition = false
  MeasureType = 1
  OverTolerance = 0
  References2D = -> [View]
  Rotation = 0
  ScaleType = 0
  TheoreticalExact = false
  Type = 1
  UnderTolerance = 0
  X = 2.64667
  Y = -61.1961
FEATURE [TechDraw::DrawPage] Page  label="sleeve_outer_Page"
  KeepUpdated = true
  NextBalloonIndex = 1
  ProjectionType = 0
  Template = -> Template
  Views = -> [View,View001,Dimension006,Dimension007,Dimension,Dimension041,SectionView,Dimension042,Dimension043,Dimension044]
FEATURE [TechDraw::DrawViewSection] SectionView005  label="Section005  - "
  BaseView = -> View002
  CoarseView = false
  CutSurfaceDisplay = 2
  Direction = (-1,0,-1e-16)
  FileGeomPattern = <path>
  FileHatchPattern = <path>
  Focus = 100
  FuseBeforeCut = false
  HardHidden = false
  HatchOffset = (0,0,0)
  HatchRotation = 0
  HatchScale = 1
  IsoCount = 0
  IsoHidden = false
  IsoVisible = false
  LockPosition = false
  NameGeomPattern = Diamond
  Perspective = false
  Rotation = -90
  ScaleType = 0
  ScrubCount = 0
  SeamHidden = false
  SeamVisible = true
  SectionDirection = 4
  SectionLineStretch = 1
  SectionNormal = (-1,0,-1e-16)
  SectionOrigin = (0,0,39.5)
  SmoothHidden = false
  SmoothVisible = true
  Source = -> [Body124]
  TrimAfterCut = false
  UsePreviousCut = false
  X = 148.5
  XDirection = (1e-16,0,-1)
  Y = 105
FEATURE [TechDraw::DrawViewDimension] Dimension045
  AngleOverride = false
  Arbitrary = false
  ArbitraryTolerances = false
  BoxCorners = (2) [(-33,-39.5,-1e-07),(33,39.5,1e-07)]
  EqualTolerance = true
  ExtensionAngle = 0
  FormatSpec = %.2w
  FormatSpecOverTolerance = %+.2w
  FormatSpecUnderTolerance = %+.2w
  Inverted = false
  LineAngle = 0
  LockPosition = false
  MeasureType = 1
  OverTolerance = 0
  References2D = -> [SectionView005]
  Rotation = 0
  ScaleType = 0
  TheoreticalExact = false
  Type = 1
  UnderTolerance = 0
  X = 0.083504
  Y = 50.0999
FEATURE [TechDraw::DrawViewDimension] Dimension046
  AngleOverride = false
  Arbitrary = false
  ArbitraryTolerances = false
  BoxCorners = (2) [(-33,-39.5,-1e-07),(33,39.5,1e-07)]
  EqualTolerance = true
  ExtensionAngle = 0
  FormatSpec = %.2w
  FormatSpecOverTolerance = %+.2w
  FormatSpecUnderTolerance = %+.2w
  Inverted = false
  LineAngle = 0
  LockPosition = false
  MeasureType = 1
  OverTolerance = 0
  References2D = -> [SectionView005]
  Rotation = 0
  ScaleType = 0
  TheoreticalExact = false
  Type = 1
  UnderTolerance = 0
  X = -0.501023
  Y = 57.9492
FEATURE [TechDraw::DrawViewDimension] Dimension047
  AngleOverride = false
  Arbitrary = false
  ArbitraryTolerances = false
  BoxCorners = (2) [(-33,-39.5,-1e-07),(33,39.5,1e-07)]
  EqualTolerance = true
  ExtensionAngle = 0
  FormatSpec = %.2w
  FormatSpecOverTolerance = %+.2w
  FormatSpecUnderTolerance = %+.2w
  Inverted = false
  LineAngle = 0
  LockPosition = false
  MeasureType = 1
  OverTolerance = 0
  References2D = -> [View002]
  Rotation = 0
  ScaleType = 0
  TheoreticalExact = false
  Type = 1
  UnderTolerance = 0
  X = -4.03246
  Y = 77.14
FEATURE [TechDraw::DrawPage] Page001  label="sleeve_inner_Page"
  KeepUpdated = true
  NextBalloonIndex = 1
  ProjectionType = 0
  Template = -> Template
  Views = -> [View002,View003,Dimension008,Dimension012,Dimension013,Dimension014,Dimension015,SectionView005,Dimension045,Dimension046,Dimension047]
FEATURE [App::DocumentObjectGroup] Group011  label="blueprints"
  Group = -> [Page,Page001,Page002,Page004,Page003]
FEATURE [PartDesign::FeaturePython] Bend033  # WARN: FeaturePython — macro-defined, semantics opaque (R4)
  AutoMiter = true
  BaseFeature = -> Pocket022
  BendType = 0
  LengthList = [10]
  LengthSpec = 0
  NonperforationMaxLength = 5
  Perforate = false
  PerforationAngle = 0
  PerforationInitialLength = 5
  PerforationMaxLength = 5
  ReliefFactor = 0.7
  Suppressed = false
  UseReliefFactor = false
  angle = 90
  baseObject = -> Pocket022 [Edge64,Edge69]
  bendAList = [90]
  extend1 = 0
  extend2 = 0
  gap1 = 0
  gap2 = 0
  invert = false
  kfactor = 0.5
  length = 10
  maxExtendDist = 5
  minGap = 0.2
  minReliefGap = 1
  miterangle1 = 0
  miterangle2 = 0
  offset = 0
  radius = 2
  reliefType = 0
  reliefd = 1
  reliefw = 0.8
  sketchflip = false
  sketchinvert = false
  unfold = true
  expr: radius = BaseBend011.radius
FEATURE [PartDesign::Pocket] Pocket131
  BaseFeature = -> Bend033
  Direction = (0,-0.11295,0.993601)
  Length = 5
  Length2 = 5
  Profile = -> Sketch219
  ReferenceAxis = -> Sketch219 [N_Axis]
  Suppressed = false
  Type = 0
FEATURE [PartDesign::Mirrored] Mirrored017
  BaseFeature = -> Pocket131
  MirrorPlane = -> YZ_Plane028
  Originals = -> [Pocket131]
  Suppressed = false
  TransformMode = 0
FEATURE [PartDesign::Pocket] Pocket024
  BaseFeature = -> Mirrored017
  Direction = (0,0,-1)
  Length = 5
  Length2 = 5
  Midplane = true
  Profile = -> Sketch042
  ReferenceAxis = -> Sketch042 [N_Axis]
  Suppressed = false
  Type = 1
FEATURE [PartDesign::FeaturePython] CornerRelief  # WARN: FeaturePython — macro-defined, semantics opaque (R4)
  BaseFeature = -> Pocket024
  ReliefSketch = 0
  Size = 6
  SizeRatio = 1.5
  Sketch = -> Sketch043
  Suppressed = false
  XOffset = 0
  YOffset = 0
  baseObject = -> Pocket024 [Edge35,Edge16]
  kfactor = 0.5
FEATURE [PartDesign::Pocket] Pocket023
  BaseFeature = -> CornerRelief
  Direction = (-0.5,0.866025,-1e-16)
  Length = 0.6
  Length2 = 5
  Profile = -> Sketch041
  ReferenceAxis = -> Sketch041 [N_Axis]
  Suppressed = false
  Type = 0
FEATURE [PartDesign::Mirrored] Mirrored002
  BaseFeature = -> Pocket023
  MirrorPlane = -> YZ_Plane028
  Originals = -> [Pocket023]
  Refine = true
  Suppressed = false
  TransformMode = 0
FEATURE [PartDesign::Boolean] Boolean008
  BaseFeature = -> Mirrored002
  Group = -> [Compound028]
  Suppressed = false
  Type = 1
  UsePlacement = false
  expr: Group = <<sink_fix001>>._self
FEATURE [PartDesign::Pocket] Pocket029
  BaseFeature = -> Boolean008
  Direction = (0,0.11295,-0.993601)
  Length = 5
  Length2 = 5
  Profile = -> Sketch064
  ReferenceAxis = -> Sketch064 [N_Axis]
  Reversed = true
  Suppressed = false
  Type = 1
FEATURE [PartDesign::Body] Body020  label="sink_material_0.30ansi"
  AllowCompound = false
  Group = -> [Sketch037,Line,DatumLine,Sketch038,DatumLine001,Sketch039,BaseBend011,Bend004,Local_CS,Sketch040,Binder031,Pocket022,Sketch041,Sketch042,Sketch219,Bend033,Pocket131,Mirrored017,Pocket024,Sketch043,CornerRelief,Pocket023,Mirrored002,Boolean008,Sketch064,Pocket029]
  Origin = -> Origin028
  Tip = -> Pocket029
FEATURE [App::Part] Part007  label="sink"
  Group = -> [Body020,Body021]
  Origin = -> Origin027
  Placement = pos=(14.5,8.37158,410) rot=(0,0,1;-1.0472rad)
  expr: .Placement.Base.x = <<Properties>>.endface_width / 2
  expr: .Placement.Base.y = <<Properties>>.petal_offset
  expr: .Placement.Base.z = basin_big#<<Properties>>.height + 18 mm
FEATURE [Sketcher::SketchObject] Sketch289  label="pillar_bottom_BaseSketch"
  ArcFitTolerance = 0
  AttacherType = Attacher::AttachEngine3D
  AttachmentSupport = -> [XY_Plane015]
  FullyConstrained = true
  MakeInternals = false
  MapMode = 5
  sketch-geometry (2):
    g0: LineSegment StartX=0 StartY=110 StartZ=0 EndX=0 EndY=0 EndZ=0
    g1: LineSegment StartX=0 StartY=0 StartZ=0 EndX=-25 EndY=0 EndZ=0
  constraints (7):
    c: PointOnObject(g0,g-2)
    c: Vertical(g0)
    c: Coincident(g0,g1)
    c: PointOnObject(g1,g-1)
    c: Horizontal(g1)
    c: DistanceX(g1,g1) = 25  'leg_length'
    c: DistanceY(g0,g0) = 110  'height'
FEATURE [PartDesign::FeaturePython] BaseBend060  label="pillar_bottom_BaseBend"  # WARN: FeaturePython — macro-defined, semantics opaque (R4)
  BendSide = 0
  BendSketch = -> Sketch289
  MidPlane = true
  Placement = pos=(0,0,0) rot=(0.57735,0.57735,0.57735;2.0944rad)
  Reverse = false
  Suppressed = false
  length = 101
  radius = 2
  thickness = 2
FEATURE [PartDesign::Pocket] Pocket
  BaseFeature = -> BaseBend060
  Direction = (0,-1,2e-16)
  Length = 5
  Length2 = 5
  Placement = pos=(0,0,0) rot=(0.57735,0.57735,0.57735;2.0944rad)
  Profile = -> WireFilter
  Suppressed = false
  Type = 1
FEATURE [PartDesign::Pocket] Pocket001
  BaseFeature = -> Pocket
  Direction = (0,0,-1)
  Length = 5
  Length2 = 5
  Placement = pos=(0,0,0) rot=(0.57735,0.57735,0.57735;2.0944rad)
  Profile = -> WireFilter001
  Reversed = true
  Suppressed = false
  Type = 1
FEATURE [PartDesign::Pocket] Pocket031
  BaseFeature = -> Pocket001
  Direction = (0,0,-1)
  Length = 5
  Length2 = 5
  Midplane = true
  Placement = pos=(0,0,0) rot=(0.57735,0.57735,0.57735;2.0944rad)
  Profile = -> Sketch070
  ReferenceAxis = -> Sketch070 [N_Axis]
  Suppressed = false
  Type = 1
FEATURE [PartDesign::Pocket] Pocket063
  BaseFeature = -> Pocket031
  Direction = (0,1,-2e-16)
  Length = 5
  Length2 = 5
  Placement = pos=(0,0,0) rot=(0.57735,0.57735,0.57735;2.0944rad)
  Profile = -> Sketch118
  ReferenceAxis = -> Sketch118 [N_Axis]
  Reversed = true
  Suppressed = false
  Type = 0
FEATURE [PartDesign::Body] Body011  label="pillar_bottom_material_0.30ansi"
  AllowCompound = false
  Group = -> [BaseBend060,Sketch011,Sketch012,WireFilter,WireFilter001,Pocket,Pocket001,Sketch070,Pocket031,Sketch118,Pocket063,pillar_bottom_LCS,Sketch289]
  Origin = -> Origin015
  Placement = pos=(18.3,54.5,0) rot=(0,0,1;1.5708rad)
  Tip = -> Pocket063
  expr: Placement = <<pillar_bottom_placement>>.AttachmentOffset
FEATURE [App::DocumentObjectGroup] Group022  label="pillar_Group"
  Group = -> [Body010,Body011,Body012,Body013,Body014]
FEATURE [App::DocumentObjectGroup] Group  label="parts"
  Group = -> [Part007,Body068,Link005,Part010,Body072,Body018,Part019,Body113,Part020,Body121,Body088,Body126,Body127,Body128,Body129,Group012,Group016,Body,Body001,Group018,Group020,Group021,Group022,Group024]
FEATURE [Part::Feature] Body157
  shape: bbox 586 x 70.89 x 3 mm, 21 faces (baked)
FEATURE [Part::FeaturePython] aCircle  # WARN: FeaturePython — macro-defined, semantics opaque (R4)
FEATURE [Part::FeaturePython] Radius  # WARN: FeaturePython — macro-defined, semantics opaque (R4)
FEATURE [App::AnnotationLabel] MeasureLbl
  BasePosition = (30.3,17.25,0)
  LabelText = R = 2,7500 mm
  TextPosition = (0,0,0)
FEATURE [App::AnnotationLabel] MeasureLbl001
  BasePosition = (30.3,14.5,0)
  LabelText = Coordinates : | X : 30.300 | Y : 14.500 | Z : 0.000
  TextPosition = (0,0,0)
FEATURE [Part::FeaturePython] aCircle001  # WARN: FeaturePython — macro-defined, semantics opaque (R4)
FEATURE [Part::FeaturePython] Radius001  # WARN: FeaturePython — macro-defined, semantics opaque (R4)
FEATURE [App::AnnotationLabel] MeasureLbl002
  BasePosition = (30.3,97.25,0)
  LabelText = R = 2,7500 mm
  TextPosition = (0,0,0)
FEATURE [Part::FeaturePython] PtS  # WARN: FeaturePython — macro-defined, semantics opaque (R4)
FEATURE [App::AnnotationLabel] MeasureLbl003
  BasePosition = (30.3,94.5,0)
  LabelText = Coordinates : | X : 30.300 | Y : 94.500 | Z : 0.000
  TextPosition = (0,0,0)
FEATURE [Part::Feature] Body158  label="hat3_cap001"
  shape: bbox 667.4 x 579.3 x 29 mm, 74 faces (baked)
FEATURE [Part::Feature] Body159  label="part1_material_0.30ansi002"
  shape: bbox 59.31 x 356 x 1428 mm, 498 faces (baked)
FEATURE [Part::Feature] Body160  label="tech_sector_plexiglass_material_0.30ansi001"
  shape: bbox 284.3 x 490.8 x 419 mm, 26 faces (baked)
FEATURE [Part::Feature] Body161  label="tech_sector_pillar_material_0.30ansi001"
  Placement = pos=(0,0,3) rot=(0,0,1;0rad)
  shape: bbox 92.99 x 107.7 x 413.8 mm, 92 faces (baked)
FEATURE [Part::Feature] Body162  label="tech_sector_pillar_material_0.30ansi002"
  Placement = pos=(0,0,3) rot=(0,0,1;0rad)
  shape: bbox 47.03 x 54.45 x 413.8 mm, 98 faces (baked)
FEATURE [Part::Feature] Body163  label="pillar_bottom_material_0.30ansi002"
  Placement = pos=(18.3,54.5,0) rot=(0,0,1;1.5708rad)
  shape: bbox 25 x 100 x 80 mm, 23 faces (baked)
FEATURE [Part::Feature] Body164  label="pillar004"
  shape: bbox 36.6 x 19 x 1684 mm, 63 faces (baked)
FEATURE [Part::Feature] Body165  label="pillar3_hat_fix001"
  shape: bbox 28.6 x 70 x 84 mm, 38 faces (baked)
FEATURE [Part::Feature] Body166  label="dropper_fix_bottom001"
  shape: bbox 84.2 x 345.1 x 3 mm, 100 faces (baked)
FEATURE [Part::Feature] Body167  label="dropper_fix_top001"
  shape: bbox 84.2 x 342.1 x 3 mm, 109 faces (baked)
FEATURE [Part::Feature] Body168  label="cap_outer_material_0.30ansi002"
  shape: bbox 90.2 x 339.9 x 40.4 mm, 133 faces (baked)
FEATURE [Part::Feature] Body169  label="sleeve_inner002"
  shape: bbox 66 x 66 x 79 mm, 9 faces (baked)
FEATURE [Part::Feature] Body170  label="sleeve_outer002"
  shape: bbox 70.5 x 70.5 x 67 mm, 9 faces (baked)
FEATURE [Part::Feature] Body171  label="top_amplifier_cornrer_material_0.50ansi002"
  shape: bbox 57.09 x 29.62 x 34 mm, 35 faces (baked)
FEATURE [Part::Feature] Body172  label="hat3_plexiglass001"
  shape: bbox 322.4 x 557.2 x 100 mm, 43 faces (baked)
FEATURE [Part::Feature] Body173  label="hat3_base001"
  shape: bbox 651.7 x 565.2 x 3 mm, 69 faces (baked)
note: 11 file-system paths scrubbed to <path> (originals preserved in the JSON sidecar)

RESOLVED EXTERNAL PARTS (link-assembly join: the EXTERNAL_REF files above that resolve inside this repo's crawl, each included once):
---- part U-fix.FCStd = doc fcstd_8b42821c5992 ----
FCSTD DOCUMENT  (FreeCAD 1.1R38827 (Git))
Label: U-fix
License: All rights reserved
LicenseURL: http://en.wikipedia.org/wiki/All_rights_reserved
objects: Sketcher::SketchObject×7, TechDraw::DrawViewDimension×4, TechDraw::DrawViewPart×3, PartDesign::SubShapeBinder×2, PartDesign::Pocket×2, PartDesign::FeaturePython×1, PartDesign::Mirrored×1, TechDraw::DrawSVGTemplate×1, Part::Feature×1, PartDesign::Hole×1, PartDesign::Body×1, TechDraw::DrawPage×1, App::DocumentObjectGroup×1
note: 37 computed .brp shape members not serialized (recipe doc carries the construction recipe); baked Part::Feature solids carry a one-line shape summary decoded from their .brp
EXTERNAL_REF file=ugol90degX40mm.FCStd obj=Binder002
EXTERNAL_REF file=wheel50mm.FCStd obj=Populate001

FEATURE [Sketcher::SketchObject] Sketch
  ArcFitTolerance = 0
  AttachmentSupport = -> [XZ_Plane]
  FullyConstrained = true
  MakeInternals = false
  MapMode = 5
  Placement = pos=(0,0,0) rot=(1,0,0;1.5708rad)
  sketch-geometry (5):
    g0: LineSegment StartX=-11.5 StartY=16 StartZ=0 EndX=-11.5 EndY=0 EndZ=0
    g1: LineSegment StartX=-11.5 StartY=0 StartZ=0 EndX=11.5 EndY=0 EndZ=0
    g2: LineSegment StartX=11.5 StartY=0 StartZ=0 EndX=11.5 EndY=16 EndZ=0
    g3: LineSegment [constr] StartX=11.5 StartY=16 StartZ=0 EndX=-11.5 EndY=16 EndZ=0
    g4: GeomPoint [constr] X=0 Y=8 Z=0
  constraints (13):
    c: Coincident(g0,g1)
    c: Coincident(g1,g2)
    c: Coincident(g2,g3)
    c: Coincident(g3,g0)
    c: Horizontal(g1)
    c: Horizontal(g3)
    c: Vertical(g0)
    c: Vertical(g2)
    c: Symmetric(g1,g0,g4)
    c: PointOnObject(g4,g-2)
    c: PointOnObject(g1,g-1)
    c: DistanceX(g1,g1) = 23  'width'
    c: DistanceY(g2) = 16  'height'
FEATURE [PartDesign::FeaturePython] BaseBend  # WARN: FeaturePython — macro-defined, semantics opaque (R4)
  BendSide = 1
  BendSketch = -> Sketch
  MidPlane = true
  Reverse = false
  Suppressed = false
  length = 65
  radius = 2
  thickness = 1
FEATURE [PartDesign::SubShapeBinder] Binder  label="U-fix_vert_holes"
  BindCopyOnChange = 0
  BindMode = 0
  ClaimChildren = false
  Context = -> Body [Binder.]
  Fuse = false
  MakeFace = true
  OffsetFill = false
  OffsetIntersection = false
  OffsetJoinType = 0
  OffsetOpenResult = false
  PartialLoad = false
  Placement = pos=(0,0,0) rot=(0,0,1;1.5708rad)
  Relative = true
  Support = -> [<external ugol90degX40mm.FCStd>#Binder002]
  _Version = 2
  expr: Support = <<ugol90degX40mm>>#<<vert>>._self
FEATURE [PartDesign::Pocket] Pocket
  BaseFeature = -> BaseBend
  Direction = (1,-2e-16,0)
  Length = 5
  Length2 = 5
  Midplane = true
  Profile = -> Binder
  Suppressed = false
  Type = 1
FEATURE [Sketcher::SketchObject] Sketch001
  ArcFitTolerance = 0
  AttachmentOffset = pos=(32.5,16,0) rot=(0,0,1;0rad)
  AttachmentSupport = -> [YZ_Plane]
  FullyConstrained = true
  MakeInternals = false
  MapMode = 5
  Placement = pos=(0,32.5,16) rot=(0.57735,0.57735,0.57735;2.0944rad)
  expr: .AttachmentOffset.Base.x = BaseBend.length / 2
  expr: .AttachmentOffset.Base.y = Sketch.Constraints.height
  sketch-geometry (3):
    g0: ArcOfCircle CenterX=-5 CenterY=-5 CenterZ=0 NormalX=0 NormalY=0 NormalZ=1 AngleXU=0 Radius=5 StartAngle=0 EndAngle=1.5708
    g1: LineSegment StartX=-9e-16 StartY=-5 StartZ=0 EndX=0 EndY=0 EndZ=0
    g2: LineSegment StartX=0 StartY=0 StartZ=0 EndX=-5.00003 EndY=-4.65468e-11 EndZ=0
  constraints (8):
    c: PointOnObject(g0,g-1)
    c: PointOnObject(g0,g-2)
    c: Coincident(g1,g2)
    c: Coincident(g2,g0)
    c: Tangent(g2,g0)
    c: Tangent(g0,g1) = -1.5708
    c: Coincident(g1,g-1)
    c: Diameter(g0) = 10
FEATURE [PartDesign::Pocket] Pocket001
  BaseFeature = -> Pocket
  Direction = (-1,0,0)
  Length = 5
  Length2 = 5
  Midplane = true
  Profile = -> Sketch001
  ReferenceAxis = -> Sketch001 [N_Axis]
  Suppressed = false
  Type = 1
FEATURE [PartDesign::Mirrored] Mirrored
  BaseFeature = -> Pocket001
  MirrorPlane = -> XZ_Plane
  Originals = -> [Pocket001]
  Suppressed = false
  TransformMode = 0
FEATURE [Sketcher::SketchObject] Sketch002  label="holes_bottom"
  ArcFitTolerance = 0
  AttachmentSupport = -> [XY_Plane]
  FullyConstrained = true
  MakeInternals = false
  MapMode = 5
  sketch-geometry (2):
    g0: Circle CenterX=0 CenterY=17.5 CenterZ=0 NormalX=0 NormalY=0 NormalZ=1 AngleXU=0 Radius=2.5
    g1: Circle CenterX=0 CenterY=-17.5 CenterZ=0 NormalX=0 NormalY=0 NormalZ=1 AngleXU=0 Radius=2.5
  constraints (5):
    c: PointOnObject(g0,g-2)
    c: Symmetric(g1,g0,g-1)
    c: Equal(g1,g0)
    c: Diameter(g1) = 5
    c: DistanceY(g1,g0) = 35
FEATURE [TechDraw::DrawSVGTemplate] Template
  Height = 210
  Orientation = 1
  Template = <path>
  Width = 297
FEATURE [Part::Feature] Unfold
  Placement = pos=(0,0,0) rot=(0,0,1;1.5708rad)
  shape: bbox 53 x 50.85 x 1 mm, 16 faces (baked)
FEATURE [Sketcher::SketchObject] Unfold_Sketch_Outline
  ArcFitTolerance = 0
  FullyConstrained = false
  MakeInternals = false
  sketch-geometry (8):
    g0: ArcOfCircle CenterX=21.5 CenterY=-20.427 CenterZ=0 NormalX=0 NormalY=0 NormalZ=1 AngleXU=4e-16 Radius=5 StartAngle=4.71238 EndAngle=6.28319
    g1: LineSegment StartX=26.5 StartY=20.427 StartZ=0 EndX=26.5 EndY=-20.427 EndZ=0
    g2: ArcOfCircle CenterX=21.5 CenterY=20.427 CenterZ=0 NormalX=0 NormalY=0 NormalZ=1 AngleXU=-4e-16 Radius=5 StartAngle=0 EndAngle=1.5708
    g3: LineSegment StartX=21.5 StartY=25.427 StartZ=0 EndX=-21.5 EndY=25.427 EndZ=0
    g4: ArcOfCircle CenterX=-21.5 CenterY=20.427 CenterZ=0 NormalX=0 NormalY=0 NormalZ=1 AngleXU=-3.14159 Radius=5 StartAngle=4.71238 EndAngle=6.28319
    g5: LineSegment StartX=-26.5 StartY=20.427 StartZ=0 EndX=-26.5 EndY=-20.427 EndZ=0
    g6: ArcOfCircle CenterX=-21.5 CenterY=-20.427 CenterZ=0 NormalX=0 NormalY=0 NormalZ=1 AngleXU=3.14159 Radius=5 StartAngle=0 EndAngle=1.5708
    g7: LineSegment StartX=21.5 StartY=-25.427 StartZ=0 EndX=-21.5 EndY=-25.427 EndZ=0
FEATURE [Sketcher::SketchObject] Unfold_Sketch_Internal
  ArcFitTolerance = 0
  FullyConstrained = false
  MakeInternals = false
  sketch-geometry (6):
    g0: Circle CenterX=17.5 CenterY=0 CenterZ=0 NormalX=0 NormalY=0 NormalZ=1 AngleXU=1.5708 Radius=2.75
    g1: Circle CenterX=-17.5 CenterY=0 CenterZ=0 NormalX=0 NormalY=0 NormalZ=1 AngleXU=1.5708 Radius=2.75
    g2: Circle CenterX=20 CenterY=-19.927 CenterZ=0 NormalX=0 NormalY=0 NormalZ=1 AngleXU=2e-16 Radius=1.7
    g3: Circle CenterX=-20 CenterY=-19.927 CenterZ=0 NormalX=0 NormalY=0 NormalZ=1 AngleXU=2e-16 Radius=1.7
    g4: Circle CenterX=20 CenterY=19.927 CenterZ=0 NormalX=0 NormalY=0 NormalZ=-1 AngleXU=-3.14159 Radius=1.7
    g5: Circle CenterX=-20 CenterY=19.927 CenterZ=0 NormalX=0 NormalY=0 NormalZ=-1 AngleXU=-3.14159 Radius=1.7
FEATURE [Sketcher::SketchObject] Unfold_Sketch_bends
  ArcFitTolerance = 0
  FullyConstrained = false
  MakeInternals = false
  sketch-geometry (2):
    g0: LineSegment StartX=-26.5 StartY=10.4635 StartZ=0 EndX=26.5 EndY=10.4635 EndZ=0
    g1: LineSegment StartX=-26.5 StartY=-10.4635 StartZ=0 EndX=26.5 EndY=-10.4635 EndZ=0
FEATURE [Sketcher::SketchObject] Unfold_Sketch
  ArcFitTolerance = 0
  ExternalGeometry = -> [Unfold_Sketch_bends]
  FullyConstrained = false
  MakeInternals = false
  sketch-geometry (18):
    g0: ArcOfCircle CenterX=21.5 CenterY=-20.427 CenterZ=0 NormalX=0 NormalY=0 NormalZ=1 AngleXU=4e-16 Radius=5 StartAngle=4.71238 EndAngle=6.28319
    g1: LineSegment StartX=21.5 StartY=-25.427 StartZ=0 EndX=-21.5 EndY=-25.427 EndZ=0
    g2: ArcOfCircle CenterX=-21.5 CenterY=-20.427 CenterZ=0 NormalX=0 NormalY=0 NormalZ=1 AngleXU=3.14159 Radius=5 StartAngle=0 EndAngle=1.5708
    g3: ArcOfCircle CenterX=-21.5 CenterY=20.427 CenterZ=0 NormalX=0 NormalY=0 NormalZ=1 AngleXU=-3.14159 Radius=5 StartAngle=4.71238 EndAngle=6.28319
    g4: LineSegment StartX=21.5 StartY=25.427 StartZ=0 EndX=-21.5 EndY=25.427 EndZ=0
    g5: ArcOfCircle CenterX=21.5 CenterY=20.427 CenterZ=0 NormalX=0 NormalY=0 NormalZ=1 AngleXU=-4e-16 Radius=5 StartAngle=0 EndAngle=1.5708
    g6: Circle CenterX=-17.5 CenterY=0 CenterZ=0 NormalX=0 NormalY=0 NormalZ=1 AngleXU=1.5708 Radius=2.75
    g7: Circle CenterX=17.5 CenterY=0 CenterZ=0 NormalX=0 NormalY=0 NormalZ=1 AngleXU=1.5708 Radius=2.75
    g8: Circle CenterX=-20 CenterY=19.927 CenterZ=0 NormalX=0 NormalY=0 NormalZ=-1 AngleXU=-3.14159 Radius=1.7
    g9: Circle CenterX=20 CenterY=19.927 CenterZ=0 NormalX=0 NormalY=0 NormalZ=-1 AngleXU=-3.14159 Radius=1.7
    g10: Circle CenterX=-20 CenterY=-19.927 CenterZ=0 NormalX=0 NormalY=0 NormalZ=1 AngleXU=2e-16 Radius=1.7
    g11: Circle CenterX=20 CenterY=-19.927 CenterZ=0 NormalX=0 NormalY=0 NormalZ=1 AngleXU=2e-16 Radius=1.7
    g12: LineSegment StartX=26.5 StartY=20.427 StartZ=0 EndX=26.5 EndY=-20.427 EndZ=0
    g13: LineSegment StartX=-26.5 StartY=20.427 StartZ=0 EndX=-26.5 EndY=-20.427 EndZ=0
    g14: LineSegment StartX=26.5 StartY=-10.4635 StartZ=0 EndX=24.5 EndY=-10.4635 EndZ=0
    g15: LineSegment StartX=26.5 StartY=10.4635 StartZ=0 EndX=24.5 EndY=10.4635 EndZ=0
    g16: LineSegment StartX=-26.5 StartY=10.4635 StartZ=0 EndX=-24.5 EndY=10.4635 EndZ=0
    g17: LineSegment StartX=-26.5 StartY=-10.4635 StartZ=0 EndX=-24.5 EndY=-10.4635 EndZ=0
  constraints (20):
    c: Coincident(g2,g13)
    c: Coincident(g3,g13)
    c: Coincident(g1,g2)
    c: Coincident(g3,g4)
    c: Coincident(g0,g1)
    c: Coincident(g4,g5)
    c: Coincident(g0,g12)
    c: Coincident(g5,g12)
    c: Coincident(g14,g-4)
    c: Coincident(g15,g-3)
    c: Coincident(g16,g-3)
    c: Coincident(g17,g-4)
    c: PointOnObject(g17,g-4)
    c: PointOnObject(g16,g-3)
    c: PointOnObject(g15,g-3)
    c: PointOnObject(g14,g-4)
    c: Equal(g14,g15)
    c: Equal(g15,g16)
    c: Equal(g16,g17)
    c: Distance(g17) = 2
FEATURE [PartDesign::SubShapeBinder] Binder001
  BindCopyOnChange = 0
  BindMode = 0
  ClaimChildren = false
  Context = -> Body [Binder001.]
  Fuse = false
  MakeFace = true
  OffsetFill = false
  OffsetIntersection = false
  OffsetJoinType = 0
  OffsetOpenResult = false
  PartialLoad = false
  Placement = pos=(0,0,0) rot=(0,0,1;0.785398rad)
  Relative = true
  Support = -> [<external wheel50mm.FCStd>#Populate001]
  _Version = 2
  expr: Support = wheel50mm#<<holes_max>>._self
FEATURE [PartDesign::Hole] Hole
  BaseFeature = -> Mirrored
  CustomThreadClearance = 0
  Depth = 25
  DepthType = 0
  Diameter = 5.5
  DrillForDepth = false
  DrillPoint = 1
  DrillPointAngle = 118
  HoleCutCountersinkAngle = 90
  HoleCutCustomValues = false
  HoleCutDepth = 0
  HoleCutDiameter = 6.1
  HoleCutType = 0
  ModelThread = false
  Profile = -> Binder001
  Reversed = true
  Suppressed = false
  Tapered = false
  TaperedAngle = 90
  ThreadClass = 0
  ThreadDepth = 25
  ThreadDepthType = 0
  ThreadDirection = 0
  ThreadFit = 0
  ThreadSize = 0
  ThreadType = 0
  Threaded = false
  UseCustomThreadClearance = false
FEATURE [PartDesign::Body] Body  label="U_fix_material_0.50ansi"
  AllowCompound = false
  Group = -> [Sketch,BaseBend,Binder,Pocket,Sketch001,Pocket001,Mirrored,Sketch002,Hole,Binder001]
  Origin = -> Origin
  Tip = -> Hole
FEATURE [TechDraw::DrawViewPart] View
  CoarseView = false
  Direction = (0,-1,0)
  Focus = 100
  HardHidden = false
  IsoCount = 0
  IsoHidden = false
  IsoVisible = false
  LockPosition = false
  Perspective = false
  Rotation = 0
  ScaleType = 0
  ScrubCount = 0
  SeamHidden = false
  SeamVisible = true
  SmoothHidden = false
  SmoothVisible = true
  Source = -> [Body]
  X = 69.5
  XDirection = (1,0,0)
  Y = 105
  expr: Y = Template.Height / 2
FEATURE [TechDraw::DrawViewPart] View001
  CoarseView = false
  Direction = (1,0,0)
  Focus = 100
  HardHidden = false
  IsoCount = 0
  IsoHidden = false
  IsoVisible = false
  LockPosition = false
  Perspective = false
  Rotation = 0
  ScaleType = 0
  ScrubCount = 0
  SeamHidden = false
  SeamVisible = true
  SmoothHidden = false
  SmoothVisible = true
  Source = -> [Body]
  X = 226.5
  XDirection = (0,1,-1.19209e-07)
  Y = 105
  expr: Y = Template.Height / 2
FEATURE [TechDraw::DrawViewPart] View002
  CoarseView = false
  Direction = (0,0,1)
  Focus = 100
  HardHidden = false
  IsoCount = 0
  IsoHidden = false
  IsoVisible = false
  LockPosition = false
  Perspective = false
  Rotation = 0
  ScaleType = 0
  ScrubCount = 0
  SeamHidden = false
  SeamVisible = true
  SmoothHidden = false
  SmoothVisible = true
  Source = -> [Body]
  X = 148.5
  XDirection = (1,0,0)
  Y = 105
  expr: Y = Template.Height / 2
FEATURE [TechDraw::DrawViewDimension] Dimension004
  AngleOverride = false
  Arbitrary = false
  ArbitraryTolerances = false
  EqualTolerance = true
  ExtensionAngle = 0
  FormatSpec = R%.2w
  FormatSpecOverTolerance = %+.2w
  FormatSpecUnderTolerance = %+.2w
  Inverted = false
  LineAngle = 0
  LockPosition = false
  MeasureType = 1
  OverTolerance = 0
  References2D = -> [View]
  Rotation = 0
  ScaleType = 0
  TheoreticalExact = false
  Type = 4
  UnderTolerance = 0
  X = -23.1952
  Y = -5.48414
FEATURE [TechDraw::DrawViewDimension] Dimension005
  AngleOverride = false
  Arbitrary = false
  ArbitraryTolerances = false
  EqualTolerance = true
  ExtensionAngle = 0
  FormatSpec = R%.2w
  FormatSpecOverTolerance = %+.2w
  FormatSpecUnderTolerance = %+.2w
  Inverted = false
  LineAngle = 0
  LockPosition = false
  MeasureType = 1
  OverTolerance = 0
  References2D = -> [View]
  Rotation = 0
  ScaleType = 0
  TheoreticalExact = false
  Type = 4
  UnderTolerance = 0
  X = 1.1181
  Y = 3.75976
FEATURE [TechDraw::DrawViewDimension] Dimension
  AngleOverride = false
  Arbitrary = false
  ArbitraryTolerances = false
  BoxCorners = (2) [(-11.5,-8,-1e-07),(11.5,8,1e-07)]
  EqualTolerance = true
  ExtensionAngle = 0
  FormatSpec = %.2w
  FormatSpecOverTolerance = %+.2w
  FormatSpecUnderTolerance = %+.2w
  Inverted = false
  LineAngle = 0
  LockPosition = false
  MeasureType = 1
  OverTolerance = 0
  References2D = -> [View]
  Rotation = 0
  ScaleType = 0
  TheoreticalExact = false
  Type = 1
  UnderTolerance = 0
  X = -0.401552
  Y = 25.4578
FEATURE [TechDraw::DrawViewDimension] Dimension006
  AngleOverride = false
  Arbitrary = false
  ArbitraryTolerances = false
  BoxCorners = (2) [(-11.5,-8,-1e-07),(11.5,8,1e-07)]
  EqualTolerance = true
  ExtensionAngle = 0
  FormatSpec = %.2w
  FormatSpecOverTolerance = %+.2w
  FormatSpecUnderTolerance = %+.2w
  Inverted = false
  LineAngle = 0
  LockPosition = false
  MeasureType = 1
  OverTolerance = 0
  References2D = -> [View]
  Rotation = 0
  ScaleType = 0
  TheoreticalExact = false
  Type = 2
  UnderTolerance = 0
  X = 18.6275
  Y = 2.60039
FEATURE [TechDraw::DrawPage] Page
  KeepUpdated = true
  NextBalloonIndex = 1
  ProjectionType = 0
  Template = -> Template
  Views = -> [View,View001,View002,Dimension004,Dimension005,Dimension,Dimension006]
FEATURE [App::DocumentObjectGroup] Group  label="unfold_Group"
  Group = -> [Page,Unfold,Unfold_Sketch,Unfold_Sketch_Outline,Unfold_Sketch_Internal,Unfold_Sketch_bends]
note: 1 file-system path scrubbed to <path> (originals preserved in the JSON sidecar)
---- part UET-VAS-060A20_12V_IP20.FCStd = doc fcstd_68e2274b13cf ----
FCSTD DOCUMENT  (FreeCAD 1.1R38827 (Git))
Label: UET-VAS-060A20_12V_IP20
License: All rights reserved
LicenseURL: http://en.wikipedia.org/wiki/All_rights_reserved
objects: PartDesign::AdditiveBox×1, PartDesign::Body×1, Sketcher::SketchObject×1
note: 6 computed .brp shape members not serialized (recipe doc carries the construction recipe); baked Part::Feature solids carry a one-line shape summary decoded from their .brp

FEATURE [PartDesign::AdditiveBox] Box
  AttacherType = Attacher::AttachEngine3D
  AttachmentOffset = pos=(-20.15,-80,0) rot=(0,0,1;0rad)
  AttachmentSupport = -> [XY_Plane]
  Height = 35.5
  Length = 40.3
  MapMode = 5
  Placement = pos=(-20.15,-80,0) rot=(0,0,1;0rad)
  Suppressed = false
  Width = 160
  expr: .AttachmentOffset.Base.x = -Length / 2
  expr: .AttachmentOffset.Base.y = -Width / 2
FEATURE [PartDesign::Body] Body
  AllowCompound = false
  Group = -> [Box]
  Origin = -> Origin
  Tip = -> Box
FEATURE [Sketcher::SketchObject] Sketch001  label="holes"
  ArcFitTolerance = 0
  FullyConstrained = true
  MakeInternals = false
  sketch-geometry (2):
    g0: Circle CenterX=13.2 CenterY=-75.0683 CenterZ=0 NormalX=0 NormalY=0 NormalZ=1 AngleXU=0 Radius=1.7
    g1: Circle CenterX=-13.2 CenterY=75.0683 CenterZ=0 NormalX=0 NormalY=0 NormalZ=1 AngleXU=0 Radius=1.7
  constraints (5):
    c: Symmetric(g1,g0,g-1)
    c: Distance(g0,g1) = 152.44
    c: Equal(g0,g1)
    c: Diameter(g0) = 3.4
    c: DistanceX(g1) = -13.2
---- part ULY-P91-20W.FCStd = doc fcstd_bf5f0575c407 ----
FCSTD DOCUMENT  (FreeCAD 1.1R38827 (Git))
Label: ULY-P91-20W
License: All rights reserved
LicenseURL: http://en.wikipedia.org/wiki/All_rights_reserved
objects: Sketcher::SketchObject×7, PartDesign::Pad×4, PartDesign::SubShapeBinder×1, PartDesign::Body×1
note: 28 computed .brp shape members not serialized (recipe doc carries the construction recipe); baked Part::Feature solids carry a one-line shape summary decoded from their .brp

FEATURE [Sketcher::SketchObject] Sketch001  label="holes"
  ArcFitTolerance = 0
  FullyConstrained = true
  MakeInternals = false
  sketch-geometry (6):
    g0: Circle [constr] CenterX=0 CenterY=-1135 CenterZ=0 NormalX=0 NormalY=0 NormalZ=1 AngleXU=0 Radius=1.8
    g1: Circle CenterX=12.5 CenterY=0 CenterZ=0 NormalX=0 NormalY=0 NormalZ=1 AngleXU=0 Radius=1.8
    g2: ArcOfCircle CenterX=0 CenterY=-1132 CenterZ=0 NormalX=0 NormalY=0 NormalZ=1 AngleXU=0 Radius=1.8 StartAngle=4.48e-14 EndAngle=3.14159
    g3: ArcOfCircle CenterX=0 CenterY=-1140 CenterZ=0 NormalX=0 NormalY=0 NormalZ=1 AngleXU=0 Radius=1.8 StartAngle=3.14159 EndAngle=6.28319
    g4: LineSegment StartX=-1.8 StartY=-1132 StartZ=0 EndX=-1.8 EndY=-1140 EndZ=0
    g5: LineSegment StartX=1.8 StartY=-1140 StartZ=0 EndX=1.8 EndY=-1132 EndZ=0
  constraints (16):
    c: DistanceX(g1) = 12.5
    c: Equal(g0,g1)
    c: Diameter(g0) = 3.6
    c: PointOnObject(g1,g-1)
    c: PointOnObject(g0,g-2)
    c: DistanceY(g0) = -1135
    c: Tangent(g2,g4) = -1.5708
    c: Tangent(g4,g3) = -1.5708
    c: Tangent(g3,g5) = -1.5708
    c: Tangent(g5,g2) = -1.5708
    c: Equal(g2,g3)
    c: PointOnObject(g2,g-2)
    c: PointOnObject(g3,g-2)
    c: DistanceY(g0,g2) = 3
    c: DistanceY(g3,g0) = 5
    c: Equal(g2,g0)
FEATURE [Sketcher::SketchObject] Sketch002  label="body"
  ArcFitTolerance = 0
  ExternalGeometry = -> [Sketch001]
  FullyConstrained = true
  MakeInternals = false
  sketch-geometry (4):
    g0: LineSegment StartX=-9 StartY=0 StartZ=0 EndX=31.6 EndY=0 EndZ=0
    g1: LineSegment StartX=31.6 StartY=0 StartZ=0 EndX=31.6 EndY=42.6 EndZ=0
    g2: LineSegment StartX=31.6 StartY=42.6 StartZ=0 EndX=-9 EndY=42.6 EndZ=0
    g3: LineSegment StartX=-9 StartY=42.6 StartZ=0 EndX=-9 EndY=0 EndZ=0
  constraints (12):
    c: Coincident(g0,g1)
    c: Coincident(g1,g2)
    c: Coincident(g2,g3)
    c: Coincident(g3,g0)
    c: Horizontal(g0)
    c: Horizontal(g2)
    c: Vertical(g1)
    c: Vertical(g3)
    c: DistanceX(g0,g0) = 40.6
    c: DistanceY(g1,g1) = 42.6
    c: PointOnObject(g0,g-1)
    c: DistanceX(g0) = 31.6
FEATURE [Sketcher::SketchObject] Sketch
  ArcFitTolerance = 0
  AttachmentOffset = pos=(11.1,0,0) rot=(0,0,1;3.14159rad)
  AttachmentSupport = -> [XY_Plane]
  FullyConstrained = true
  MakeInternals = false
  MapMode = 5
  Placement = pos=(11.1,0,0) rot=(0,0,1;3.14159rad)
  sketch-geometry (5):
    g0: ArcOfCircle CenterX=0 CenterY=4 CenterZ=0 NormalX=0 NormalY=0 NormalZ=1 AngleXU=0 Radius=4.5 StartAngle=2.68873e-11 EndAngle=3.14159
    g1: Circle CenterX=0 CenterY=4 CenterZ=0 NormalX=0 NormalY=0 NormalZ=1 AngleXU=0 Radius=1.8
    g2: LineSegment StartX=-4.5 StartY=4 StartZ=0 EndX=-4.5 EndY=0 EndZ=0
    g3: LineSegment StartX=-4.5 StartY=0 StartZ=0 EndX=4.5 EndY=0 EndZ=0
    g4: LineSegment StartX=4.5 StartY=0 StartZ=0 EndX=4.5 EndY=4 EndZ=0
  constraints (13):
    c: PointOnObject(g0,g-2)
    c: Coincident(g1,g0)
    c: Tangent(g0,g2) = -1.5708
    c: Coincident(g2,g3)
    c: PointOnObject(g3,g-1)
    c: Horizontal(g3)
    c: Coincident(g3,g4)
    c: Vertical(g4)
    c: Tangent(g4,g0) = -1.5708
    c: Vertical(g2)
    c: Diameter(g0) = 9
    c: Diameter(g1) = 3.6
    c: DistanceY(g0) = 4
FEATURE [Sketcher::SketchObject] Sketch003
  ArcFitTolerance = 0
  AttachmentSupport = -> [XY_Plane]
  FullyConstrained = true
  MakeInternals = false
  MapMode = 5
  sketch-geometry (5):
    g0: LineSegment StartX=-6.55 StartY=-1114 StartZ=0 EndX=-6.55 EndY=0 EndZ=0
    g1: LineSegment StartX=-6.55 StartY=0 StartZ=0 EndX=6.55 EndY=0 EndZ=0
    g2: LineSegment StartX=6.55 StartY=0 StartZ=0 EndX=6.55 EndY=-1114 EndZ=0
    g3: LineSegment StartX=6.55 StartY=-1114 StartZ=0 EndX=-6.55 EndY=-1114 EndZ=0
    g4: GeomPoint [constr] X=0 Y=-557 Z=0
  constraints (13):
    c: Coincident(g0,g1)
    c: Coincident(g1,g2)
    c: Coincident(g2,g3)
    c: Coincident(g3,g0)
    c: Horizontal(g1)
    c: Horizontal(g3)
    c: Vertical(g0)
    c: Vertical(g2)
    c: Symmetric(g1,g0,g4)
    c: PointOnObject(g4,g-2)
    c: PointOnObject(g1,g-1)
    c: DistanceX(g1,g1) = 13.1
    c: DistanceY(g2,g2) = 1114
FEATURE [PartDesign::SubShapeBinder] Binder
  BindCopyOnChange = 0
  BindMode = 0
  ClaimChildren = true
  Context = -> Body [Binder.]
  Fuse = false
  MakeFace = true
  OffsetFill = false
  OffsetIntersection = false
  OffsetJoinType = 0
  OffsetOpenResult = false
  PartialLoad = false
  Relative = false
  Support = -> [Sketch002]
  _Version = 2
FEATURE [PartDesign::Pad] Pad002
  Direction = (0,0,1)
  Length = 16.3
  Length2 = 10
  Profile = -> Binder
  Suppressed = false
  Type = 0
FEATURE [PartDesign::Pad] Pad
  BaseFeature = -> Pad002
  Direction = (0,0,1)
  Length = 2
  Length2 = 10
  Profile = -> Sketch
  ReferenceAxis = -> Sketch [N_Axis]
  Suppressed = false
  Type = 0
FEATURE [PartDesign::Pad] Pad001
  BaseFeature = -> Pad
  Direction = (0,0,1)
  Length = 7.3
  Length2 = 10
  Profile = -> Sketch003
  ReferenceAxis = -> Sketch003 [N_Axis]
  Suppressed = false
  Type = 0
FEATURE [Sketcher::SketchObject] Sketch004
  ArcFitTolerance = 0
  AttachmentSupport = -> [XY_Plane]
  ExternalGeometry = -> [Sketch003]
  FullyConstrained = true
  MakeInternals = false
  MapMode = 5
  sketch-geometry (5):
    g0: LineSegment StartX=-7.5 StartY=-1134 StartZ=0 EndX=-7.5 EndY=-1114 EndZ=0
    g1: LineSegment StartX=-7.5 StartY=-1114 StartZ=0 EndX=7.5 EndY=-1114 EndZ=0
    g2: LineSegment StartX=7.5 StartY=-1114 StartZ=0 EndX=7.5 EndY=-1134 EndZ=0
    g3: LineSegment StartX=7.5 StartY=-1134 StartZ=0 EndX=-7.5 EndY=-1134 EndZ=0
    g4: GeomPoint [constr] X=0 Y=-1124 Z=0
  constraints (13):
    c: Coincident(g0,g1)
    c: Coincident(g1,g2)
    c: Coincident(g2,g3)
    c: Coincident(g3,g0)
    c: Horizontal(g1)
    c: Horizontal(g3)
    c: Vertical(g0)
    c: Vertical(g2)
    c: Symmetric(g1,g0,g4)
    c: PointOnObject(g4,g-2)
    c: PointOnObject(g-3,g1)
    c: DistanceX(g1,g1) = 15
    c: DistanceY(g2,g2) = 20
FEATURE [PartDesign::Pad] Pad003
  BaseFeature = -> Pad001
  Direction = (0,0,1)
  Length = 8.3
  Length2 = 1
  Profile = -> Sketch004
  ReferenceAxis = -> Sketch004 [N_Axis]
  Suppressed = false
  Type = 4
FEATURE [Sketcher::SketchObject] Sketch005  label="driver_slice_sketch"
  ArcFitTolerance = 0
  AttachmentSupport = -> [XZ_Plane]
  FullyConstrained = true
  MakeInternals = false
  MapMode = 5
  Placement = pos=(0,0,0) rot=(1,0,0;1.5708rad)
  sketch-geometry (4):
    g0: LineSegment StartX=-9.7 StartY=-1 StartZ=0 EndX=30.9 EndY=-1 EndZ=0
    g1: LineSegment StartX=30.9 StartY=-1 StartZ=0 EndX=30.9 EndY=15 EndZ=0
    g2: LineSegment StartX=30.9 StartY=15 StartZ=0 EndX=-9.7 EndY=15 EndZ=0
    g3: LineSegment StartX=-9.7 StartY=15 StartZ=0 EndX=-9.7 EndY=-1 EndZ=0
  constraints (12):
    c: Coincident(g0,g1)
    c: Coincident(g1,g2)
    c: Coincident(g2,g3)
    c: Coincident(g3,g0)
    c: Horizontal(g0)
    c: Horizontal(g2)
    c: Vertical(g1)
    c: Vertical(g3)
    c: DistanceY(g0) = -1
    c: DistanceY(g1) = 15
    c: DistanceX(g0) = 30.9
    c: DistanceX(g2,g2) = 40.6
FEATURE [Sketcher::SketchObject] Sketch006  label="led_slice_sketch"
  ArcFitTolerance = 0
  AttachmentSupport = -> [XZ_Plane]
  FullyConstrained = true
  MakeInternals = false
  MapMode = 5
  Placement = pos=(0,0,0) rot=(1,0,0;1.5708rad)
  sketch-geometry (5):
    g0: LineSegment StartX=-6.55 StartY=7.3 StartZ=0 EndX=-6.55 EndY=0 EndZ=0
    g1: LineSegment StartX=-6.55 StartY=0 StartZ=0 EndX=6.55 EndY=0 EndZ=0
    g2: LineSegment StartX=6.55 StartY=0 StartZ=0 EndX=6.55 EndY=7.3 EndZ=0
    g3: LineSegment StartX=6.55 StartY=7.3 StartZ=0 EndX=-6.55 EndY=7.3 EndZ=0
    g4: GeomPoint [constr] X=0 Y=3.65 Z=0
  constraints (13):
    c: Coincident(g0,g1)
    c: Coincident(g1,g2)
    c: Coincident(g2,g3)
    c: Coincident(g3,g0)
    c: Horizontal(g1)
    c: Horizontal(g3)
    c: Vertical(g0)
    c: Vertical(g2)
    c: Symmetric(g1,g0,g4)
    c: PointOnObject(g4,g-2)
    c: PointOnObject(g1,g-1)
    c: DistanceX(g1,g1) = 13.1
    c: DistanceY(g2,g2) = 7.3
FEATURE [PartDesign::Body] Body
  AllowCompound = false
  Group = -> [Sketch,Pad002,Pad,Sketch003,Pad001,Binder,Sketch004,Pad003,Sketch005,Sketch006]
  Origin = -> Origin
  Tip = -> Pad003
---- part ULZ-P02-14W.FCStd = doc fcstd_d946428e1785 ----
FCSTD DOCUMENT  (FreeCAD 1.1R38827 (Git))
Label: ULZ-P02-14W
License: All rights reserved
LicenseURL: http://en.wikipedia.org/wiki/All_rights_reserved
objects: Sketcher::SketchObject×4, Part::FeaturePython×4, App::DocumentObjectGroup×3, Path::FeaturePython×3, App::FeaturePython×1, Part::Part2DObjectPython×1, PartDesign::SubShapeBinder×1, PartDesign::Pad×1, PartDesign::CoordinateSystem×1, PartDesign::Body×1
note: 20 computed .brp shape members not serialized (recipe doc carries the construction recipe); baked Part::Feature solids carry a one-line shape summary decoded from their .brp

FEATURE [Sketcher::SketchObject] Sketch  label="holes"
  ArcFitTolerance = 0
  FullyConstrained = true
  MakeInternals = false
  sketch-geometry (3):
    g0: Circle CenterX=-4.15 CenterY=445 CenterZ=0 NormalX=0 NormalY=0 NormalZ=1 AngleXU=0 Radius=1.6
    g1: Circle CenterX=4.15 CenterY=-445 CenterZ=0 NormalX=0 NormalY=0 NormalZ=1 AngleXU=0 Radius=1.6
    g2: GeomPoint [constr] X=-9.05 Y=0 Z=0
  constraints (8):
    c: Symmetric(g1,g0,g-1)
    c: Distance(g0,g1) = 890.039
    c: PointOnObject(g2,g-1)
    c: DistanceX(g2,g0) = 4.9
    c: DistanceX(g2) = -9.05
    c: DistanceY(g1,g0) = 890
    c: Equal(g1,g0)
    c: Diameter(g1) = 3.2
FEATURE [App::FeaturePython] SetupSheet  # Path/CAM operation (typed FeaturePython)
  ClearanceHeightExpression = OpStockZMax+SetupSheet.ClearanceHeightOffset
  ClearanceHeightOffset = 5
  CoolantMode = 0
  CoolantModes = None | Flood | Mist
  FinalDepthExpression = -0.1 mm
  HorizRapid = 0
  ProfileDirection = 1
  ProfileSide = 0
  ProfileUseComp = true
  ProfileprocessCircles = true
  ProfileprocessHoles = true
  ProfileprocessPerimeter = true
  SafeHeightExpression = OpStockZMax+SetupSheet.SafeHeightOffset
  SafeHeightOffset = 3
  StartDepthExpression = 3 mm
  StepDownExpression = 4 mm
  VertRapid = 0
FEATURE [Part::Part2DObjectPython] Clone2D  label="Model-Sketch"  # Draft 2D object (typed FeaturePython)
  Fuse = false
  Objects = -> [Sketch]
  PathResource = Model
  Placement = pos=(-5.75,446.581,0) rot=(0,0,1;0rad)
  Scale = (1,1,1)
FEATURE [App::DocumentObjectGroup] Model
  Group = -> [Clone2D]
FEATURE [Part::FeaturePython] ToolBit  label="3.175mm Endmill"  # Path/CAM toolbit (typed FeaturePython)
  BitPropertyNames = Chipload | CuttingEdgeHeight | Diameter | Flutes | Length | Material | ShankDiameter | SpindleDirection
  BitShape = <path>
  Chipload = 0
  CuttingEdgeHeight = 30
  Diameter = 3.175
  Flutes = 0
  Length = 10
  Material = 0
  ShankDiameter = 3
  ShapeName = endmill
  SpindleDirection = 0
FEATURE [Path::FeaturePython] __175mm_Endmill  label="3.175mm Endmill001"  # Path/CAM operation (typed FeaturePython)
  HorizFeed = 33.3333
  HorizRapid = 0
  SpindleDir = 0
  SpindleSpeed = 18000
  Tool = -> ToolBit
  ToolNumber = 1
  VertFeed = 8.33333
  VertRapid = 0
  expr: HorizRapid = SetupSheet.HorizRapid
  expr: VertRapid = SetupSheet.VertRapid
FEATURE [App::DocumentObjectGroup] Tools
  Group = -> [__175mm_Endmill]
FEATURE [Part::FeaturePython] Stock  # WARN: FeaturePython — macro-defined, semantics opaque (R4)
  Base = -> Model
  ExtXneg = 1
  ExtXpos = 1
  ExtYneg = 1
  ExtYpos = 1
  ExtZneg = 0
  ExtZpos = 1
  Placement = pos=(-5.89217,-448.284,0) rot=(0,0,1;0rad)
  StockType = FromBase
FEATURE [Path::FeaturePython] Profile  # Path/CAM operation (typed FeaturePython)
  Active = true
  AreaParams:
    Tolerance = 1e-07
    FitArcs = True
    Simplify = False
    CleanDistance = 0.0
    Accuracy = 0.01
    Unit = 1.0
    MinArcPoints = 4
    MaxArcPoints = 100
    ClipperScale = 10000000.0
    Fill = 0
    Coplanar = 0
    Reorient = True
    Outline = False
    Explode = False
    OpenMode = 0
    Deflection = 0.01
    SubjectFill = 0
    ClipFill = 0
    Offset = -1.5875
    ExtraPass = 0
    Stepover = 0.0
    LastStepover = 0.0
    JoinType = 0
    EndType = 0
    MiterLimit = 2.0
    RoundPrecision = 0.0
    PocketMode = 0
    ToolRadius = 1.0
    PocketExtraOffset = 0.0
    PocketStepover = 0.0
    PocketLastStepover = 0.0
    FromCenter = False
    Angle = 45.0
    AngleShift = 0.0
    Shift = 0.0
    Thicken = False
    SectionCount = -1
    Stepdown = 1.0
    SectionOffset = 0.0
    SectionTolerance = 1e-06
    SectionMode = 2
    Project = False
  ClearanceHeight = 6
  CoolantMode = 0
  CycleTime = 00:00:57
  Direction = 1
  FinalDepth = -0.1
  HandleMultipleFeatures = 0
  JoinType = 0
  MiterLimit = 0.1
  OffsetExtra = 0
  OpFinalDepth = 0
  OpStartDepth = 1
  OpStockZMax = 1
  OpStockZMin = 0
  OpToolDiameter = 3.175
  PathParams = {'orientation': 1, 'feedrate': 33.333333333333336, 'feedrate_v': 8.333333333333334, 'verbose': True, 'resume_height': 4.0, 'retraction': 6.0, 'return_end': True, 'preamble': False}
  SafeHeight = 4
  Side = 1
  SplitArcs = false
  StartDepth = 3
  StartPoint = (0,0,0)
  StepDown = 4
  ToolController = -> __175mm_Endmill
  UseComp = true
  UseStartPoint = false
  processCircles = true
  processHoles = true
  processPerimeter = true
  expr: ClearanceHeight = OpStockZMax + SetupSheet.ClearanceHeightOffset
  expr: FinalDepth = -0.1 mm
  expr: SafeHeight = OpStockZMax + SetupSheet.SafeHeightOffset
  expr: StartDepth = 3 mm
  expr: StepDown = 4 mm
FEATURE [App::DocumentObjectGroup] Operations
  Group = -> [Profile]
FEATURE [Path::FeaturePython] Job  # Path/CAM operation (typed FeaturePython)
  CycleTime = 00:00:57
  Fixtures = G54
  GeometryTolerance = 0.01
  JobType = 0
  LastPostProcessDate = 2023-12-11 14:23:56.391449
  LastPostProcessOutput = <userpath>/2CAF-B51C/Job-0.tap
  Model = -> Model
  Operations = -> Operations
  OrderOutputBy = 2
  PostProcessor = 3
  PostProcessorOutputFile = %j.tap
  SetupSheet = -> SetupSheet
  SplitOutput = true
  Stock = -> Stock
  Tools = -> Tools
FEATURE [Part::FeaturePython] BoundBox  label="BoundBox of Model-Sketch"  # WARN: FeaturePython — macro-defined, semantics opaque (R4)
  Center = (-5.75,446.581,0)
  CompoundTraversal = 0
  OrientMode = 0
  Padding = 0
  Precision = false
  ScaleFactor = 1
  ShapeLink = -> Clone2D
  Size = (11.5,893.177,0)
FEATURE [Sketcher::SketchObject] Sketch001
  ArcFitTolerance = 0
  FullyConstrained = true
  MakeInternals = false
  Placement = pos=(0,0,0) rot=(1,0,0;1.5708rad)
  sketch-geometry (7):
    g0: LineSegment StartX=-7.3 StartY=1.25 StartZ=0 EndX=7.3 EndY=1.25 EndZ=0
    g1: GeomPoint [constr] X=0 Y=9.25 Z=0
    g2: ArcOfEllipse CenterX=5.1e-15 CenterY=1.25 CenterZ=0 NormalX=0 NormalY=0 NormalZ=1 MajorRadius=8 MinorRadius=7.3 AngleXU=-1.5708 StartAngle=1.5708 EndAngle=4.71239
    g3: LineSegment [constr] StartX=1e-14 StartY=-6.75 StartZ=0 EndX=0 EndY=9.25 EndZ=0
    g4: LineSegment [constr] StartX=7.3 StartY=1.25 StartZ=0 EndX=-7.3 EndY=1.25 EndZ=0
    g5: GeomPoint [constr] X=7.7e-15 Y=-2.02261 Z=0
    g6: GeomPoint [constr] X=3e-15 Y=4.52261 Z=0
  constraints (9):
    c: DistanceX(g0,g0) = 14.6
    c: PointOnObject(g1,g-2)
    c: InternalAlignment(g3-g6 -> g2) x4
    c: Coincident(g3,g1)
    c: Perpendicular(g2,g0) = 4.71239
    c: Perpendicular(g2,g0) = 1.5708
    c: Horizontal(g0)
    c: DistanceY(g2,g1) = 8
    c: DistanceY(g-1,g2) = 1.25
FEATURE [Sketcher::SketchObject] Sketch002
  ArcFitTolerance = 0
  FullyConstrained = true
  MakeInternals = false
  Placement = pos=(0,0,0) rot=(1,0,0;1.5708rad)
  sketch-geometry (8):
    g0: LineSegment StartX=-9 StartY=-5e-16 StartZ=0 EndX=9 EndY=-5e-16 EndZ=0
    g1: LineSegment [constr] StartX=-9 StartY=-5e-16 StartZ=0 EndX=0 EndY=11 EndZ=0
    g2: LineSegment [constr] StartX=7e-16 StartY=11 StartZ=0 EndX=9 EndY=0 EndZ=0
    g3: ArcOfEllipse CenterX=0 CenterY=0 CenterZ=0 NormalX=0 NormalY=0 NormalZ=1 MajorRadius=11 MinorRadius=9 AngleXU=1.5708 StartAngle=4.71239 EndAngle=7.85398
    g4: LineSegment [constr] StartX=7e-16 StartY=11 StartZ=0 EndX=-7e-16 EndY=-11 EndZ=0
    g5: LineSegment [constr] StartX=-9 StartY=6e-16 StartZ=0 EndX=9 EndY=-6e-16 EndZ=0
    g6: GeomPoint [constr] X=7e-16 Y=6.32456 Z=0
    g7: GeomPoint [constr] X=-4e-16 Y=-6.32456 Z=0
  constraints (12):
    c: DistanceX(g0,g0) = 18
    c: Coincident(g0,g1)
    c: Coincident(g1,g2)
    c: Coincident(g2,g0)
    c: Distance(g1,g0) = 11
    c: InternalAlignment(g4-g7 -> g3) x4
    c: Perpendicular(g3,g0) = 1.5708
    c: Equal(g1,g2)
    c: Horizontal(g0)
    c: Coincident(g3,g0)
    c: Coincident(g4,g1)
    c: Coincident(g3,g-1)
FEATURE [PartDesign::SubShapeBinder] Binder
  BindCopyOnChange = 0
  BindMode = 0
  ClaimChildren = true
  Context = -> Body [Binder.]
  Fuse = false
  MakeFace = true
  OffsetFill = false
  OffsetIntersection = false
  OffsetJoinType = 0
  OffsetOpenResult = false
  PartialLoad = false
  Relative = true
  Support = -> [Sketch001]
  _Version = 2
FEATURE [PartDesign::Pad] Pad
  Direction = (0,1,0)
  Length = 820
  Length2 = 10
  Midplane = true
  Profile = -> Binder
  Suppressed = false
  Type = 0
FEATURE [PartDesign::CoordinateSystem] Local_CS
  AttacherType = Attacher::AttachEngine3D
  AttachmentSupport = -> [XY_Plane]
  MapMode = 5
FEATURE [PartDesign::Body] Body
  AllowCompound = false
  Group = -> [Binder,Pad,Local_CS]
  Origin = -> Origin
  Tip = -> Pad
FEATURE [Sketcher::SketchObject] Sketch003
  ArcFitTolerance = 0
  FullyConstrained = true
  MakeInternals = false
  Placement = pos=(0,416,0) rot=(0,0,1;0rad)
  sketch-geometry (8):
    g0: LineSegment StartX=-9 StartY=29.05 StartZ=0 EndX=-9 EndY=0 EndZ=0
    g1: LineSegment StartX=-9 StartY=0 StartZ=0 EndX=9 EndY=0 EndZ=0
    g2: LineSegment StartX=9 StartY=0 StartZ=0 EndX=9 EndY=21.4 EndZ=0
    g3: LineSegment StartX=9 StartY=21.4 StartZ=0 EndX=0.256748 EndY=32.3031 EndZ=0
    g4: ArcOfCircle CenterX=-3.8 CenterY=29.05 CenterZ=0 NormalX=0 NormalY=0 NormalZ=1 AngleXU=0 Radius=5.2 StartAngle=0.675901 EndAngle=3.14159
    g5: GeomPoint [constr] X=-9 Y=43.8466 Z=0
    g6: LineSegment [constr] StartX=0 StartY=34.25 StartZ=0 EndX=-3.8 EndY=34.25 EndZ=0
    g7: Circle CenterX=-3.8 CenterY=29.05 CenterZ=0 NormalX=0 NormalY=0 NormalZ=1 AngleXU=0 Radius=2
  constraints (20):
    c: Vertical(g0)
    c: Coincident(g0,g1)
    c: PointOnObject(g1,g-1)
    c: Coincident(g1,g2)
    c: Vertical(g2)
    c: Coincident(g2,g3)
    c: Symmetric(g0,g1,g-2)
    c: PointOnObject(g5,g0)
    c: PointOnObject(g5,g3)
    c: Tangent(g0,g4) = -1.5708
    c: Tangent(g3,g4) = -1.5708
    c: PointOnObject(g6,g-2)
    c: Tangent(g6,g4) = -1.5708
    c: Horizontal(g6)
    c: DistanceY(g6) = 34.25
    c: DistanceX(g0,g1) = 18
    c: DistanceY(g2,g2) = 21.4
    c: Radius(g4) = 5.2
    c: Coincident(g7,g4)
    c: Diameter(g7) = 4
FEATURE [Part::FeaturePython] Array  # Draft array (typed FeaturePython)
  Angle = 360
  ArrayType = 1
  Axis = (0,0,1)
  Base = -> Sketch003
  Center = (0,0,0)
  Count = 2
  Fuse = true
  IntervalAxis = (0,0,0)
  IntervalX = (50,0,0)
  IntervalY = (0,50,0)
  IntervalZ = (0,0,50)
  NumberCircles = 3
  NumberPolar = 2
  NumberX = 2
  NumberY = 2
  NumberZ = 1
  RadialDistance = 50
  Symmetry = 1
  TangentialDistance = 25
note: 1 file-system path scrubbed to <path> (originals preserved in the JSON sidecar)
---- part basin_big.FCStd = doc fcstd_3c131922ee46 ----
FCSTD DOCUMENT  (FreeCAD 1.1R38827 (Git))
Label: basin_big
License: All rights reserved
LicenseURL: http://en.wikipedia.org/wiki/All_rights_reserved
objects: Part::FeaturePython×4, Sketcher::SketchObject×2, PartDesign::Revolution×2, App::AnnotationLabel×2, PartDesign::Mirrored×1, PartDesign::CoordinateSystem×1, PartDesign::Body×1, Spreadsheet::Sheet×1, App::DocumentObjectGroup×1
note: 18 computed .brp shape members not serialized (recipe doc carries the construction recipe); baked Part::Feature solids carry a one-line shape summary decoded from their .brp

FEATURE [Sketcher::SketchObject] Sketch067  label="basin_sketch"
  ArcFitTolerance = 0
  AttachmentSupport = -> [XZ_Plane034]
  FullyConstrained = true
  MakeInternals = false
  MapMode = 5
  Placement = pos=(0,0,0) rot=(1,0,0;1.5708rad)
  sketch-geometry (10):
    g0: LineSegment StartX=0 StartY=0 StartZ=0 EndX=160 EndY=0 EndZ=0
    g1: LineSegment StartX=160 StartY=0 StartZ=0 EndX=177.5 EndY=357 EndZ=0
    g2: LineSegment StartX=177.5 StartY=357 StartZ=0 EndX=185 EndY=357 EndZ=0
    g3: LineSegment StartX=185 StartY=357 StartZ=0 EndX=185 EndY=369 EndZ=0
    g4: LineSegment StartX=185 StartY=369 StartZ=0 EndX=177.5 EndY=369 EndZ=0
    g5: LineSegment StartX=177.5 StartY=369 StartZ=0 EndX=177.5 EndY=392 EndZ=0
    g6: LineSegment StartX=177.5 StartY=392 StartZ=0 EndX=175.5 EndY=392 EndZ=0
    g7: LineSegment StartX=0 StartY=2 StartZ=0 EndX=0 EndY=0 EndZ=0
    g8: LineSegment StartX=175.5 StartY=392 StartZ=0 EndX=158 EndY=2 EndZ=0
    g9: LineSegment StartX=158 StartY=2 StartZ=0 EndX=0 EndY=2 EndZ=0
  constraints (29):
    c: Coincident(g-1,g0)
    c: PointOnObject(g0,g-1)
    c: Coincident(g0,g1)
    c: Coincident(g1,g2)
    c: Horizontal(g2)
    c: Coincident(g2,g3)
    c: Vertical(g3)
    c: Coincident(g3,g4)
    c: Horizontal(g4)
    c: Coincident(g4,g5)
    c: Coincident(g5,g6)
    c: Horizontal(g6)
    c: Coincident(g7,g0)
    c: DistanceX(g0) = 160  'basin_bottom_r'
    c: DistanceX(g1) = 177.5
    c: Vertical(g4,g1)
    c: Vertical(g5,g4)
    c: DistanceX(g2) = 185
    c: DistanceY(g1) = 357
    c: DistanceY(g2,g3) = 12
    c: Coincident(g9,g8)
    c: Horizontal(g9)
    c: DistanceY(g0,g9) = 2
    c: DistanceX(g8,g0) = 2
    c: DistanceX(g8,g5) = 2
    c: Coincident(g6,g8)
    c: DistanceY(g6) = 392
    c: Coincident(g7,g9)
    c: Vertical(g7)
FEATURE [Sketcher::SketchObject] Sketch068
  ArcFitTolerance = 0
  AttachmentSupport = -> [XZ_Plane034]
  FullyConstrained = true
  MakeInternals = false
  MapMode = 5
  Placement = pos=(0,0,0) rot=(1,0,0;1.5708rad)
  expr: Constraints[13] = Sketch067.Constraints.basin_bottom_r
  expr: Constraints[14] = Sketch067.Constraints[14]
  expr: Constraints[17] = Sketch067.Constraints[17]
  expr: Constraints[18] = Sketch067.Constraints[18]
  expr: Constraints[19] = Sketch067.Constraints[19]
  expr: Constraints[22] = Sketch067.Constraints[22]
  expr: Constraints[23] = Sketch067.Constraints[23]
  expr: Constraints[24] = Sketch067.Constraints[24]
  expr: Constraints[26] = Sketch067.Constraints[26]
  sketch-geometry (14):
    g0: LineSegment [constr] StartX=0 StartY=0 StartZ=0 EndX=160 EndY=0 EndZ=0
    g1: LineSegment [constr] StartX=160 StartY=0 StartZ=0 EndX=177.5 EndY=357 EndZ=0
    g2: LineSegment StartX=177.5 StartY=357 StartZ=0 EndX=185 EndY=357 EndZ=0
    g3: LineSegment StartX=185 StartY=357 StartZ=0 EndX=185 EndY=369 EndZ=0
    g4: LineSegment [constr] StartX=185 StartY=369 StartZ=0 EndX=177.5 EndY=369 EndZ=0
    g5: LineSegment [constr] StartX=177.5 StartY=369 StartZ=0 EndX=177.5 EndY=392 EndZ=0
    g6: LineSegment [constr] StartX=177.5 StartY=392 StartZ=0 EndX=175.5 EndY=392 EndZ=0
    g7: LineSegment [constr] StartX=0 StartY=2 StartZ=0 EndX=0 EndY=0 EndZ=0
    g8: LineSegment [constr] StartX=175.5 StartY=392 StartZ=0 EndX=158 EndY=2 EndZ=0
    g9: LineSegment [constr] StartX=158 StartY=2 StartZ=0 EndX=0 EndY=2 EndZ=0
    g10: LineSegment StartX=185 StartY=369 StartZ=0 EndX=202.5 EndY=369 EndZ=0
    g11: LineSegment StartX=202.5 StartY=369 StartZ=0 EndX=202.5 EndY=319 EndZ=0
    g12: LineSegment StartX=202.5 StartY=319 StartZ=0 EndX=175.637 EndY=319 EndZ=0
    g13: LineSegment StartX=175.637 StartY=319 StartZ=0 EndX=177.5 EndY=357 EndZ=0
  constraints (40):
    c: Coincident(g-1,g0)
    c: PointOnObject(g0,g-1)
    c: Coincident(g0,g1)
    c: Coincident(g1,g2)
    c: Horizontal(g2)
    c: Coincident(g2,g3)
    c: Vertical(g3)
    c: Coincident(g3,g4)
    c: Horizontal(g4)
    c: Coincident(g4,g5)
    c: Coincident(g5,g6)
    c: Horizontal(g6)
    c: Coincident(g7,g0)
    c: DistanceX(g0) = 160
    c: DistanceX(g1) = 177.5
    c: Vertical(g4,g1)
    c: Vertical(g5,g4)
    c: DistanceX(g2) = 185
    c: DistanceY(g1) = 357
    c: DistanceY(g2,g3) = 12
    c: Coincident(g9,g8)
    c: Horizontal(g9)
    c: DistanceY(g0,g9) = 2
    c: DistanceX(g8,g0) = 2
    c: DistanceX(g8,g5) = 2
    c: Coincident(g6,g8)
    c: DistanceY(g6) = 392
    c: Coincident(g7,g9)
    c: Vertical(g7)
    c: Coincident(g10,g3)
    c: Horizontal(g10)
    c: Coincident(g11,g10)
    c: Vertical(g11)
    c: Coincident(g12,g11)
    c: PointOnObject(g12,g1)
    c: Horizontal(g12)
    c: Coincident(g13,g12)
    c: Coincident(g13,g2)
    c: DistanceX(g10) = 202.5
    c: DistanceY(g11,g10) = 50
FEATURE [PartDesign::Revolution] Revolution
  Angle = 360
  Angle2 = 60
  Axis = (0,2e-16,1)
  Base = (0,0,0)
  Placement = pos=(0,0,0) rot=(1,0,0;1.5708rad)
  Profile = -> Sketch067
  ReferenceAxis = -> Sketch067 [V_Axis]
  Reversed = true
  Suppressed = false
  Type = 0
FEATURE [PartDesign::Revolution] Revolution001
  Angle = 34
  Angle2 = 60
  Axis = (0,2e-16,1)
  Base = (0,0,0)
  BaseFeature = -> Revolution
  Midplane = true
  Placement = pos=(0,0,0) rot=(1,0,0;1.5708rad)
  Profile = -> Sketch068
  ReferenceAxis = -> Sketch068 [V_Axis]
  Reversed = true
  Suppressed = false
  Type = 0
FEATURE [PartDesign::Mirrored] Mirrored023
  BaseFeature = -> Revolution001
  MirrorPlane = -> Sketch068 [V_Axis]
  Originals = -> [Revolution001]
  Placement = pos=(0,0,0) rot=(1,0,0;1.5708rad)
  Suppressed = false
  TransformMode = 0
FEATURE [PartDesign::CoordinateSystem] LCS_021  label="base_LCS"
  AttacherType = Attacher::AttachEngine3D
  AttachmentSupport = -> [X_Axis034]
  MapMode = 2
FEATURE [PartDesign::Body] Body_7  label="basin"
  AllowCompound = false
  Group = -> [LCS_021,Sketch067,Revolution,Sketch068,Revolution001,Mirrored023]
  Origin = -> Origin034
  Tip = -> Mirrored023
FEATURE [Spreadsheet::Sheet] Spreadsheet  label="Properties"
  cells = B2(height)==392 mm; C2(bottom_d)==320 mm; D2(max_r)==405 mm
FEATURE [Part::FeaturePython] aCircle  # WARN: FeaturePython — macro-defined, semantics opaque (R4)
FEATURE [Part::FeaturePython] Radius  # WARN: FeaturePython — macro-defined, semantics opaque (R4)
FEATURE [App::AnnotationLabel] MeasureLbl
  BasePosition = (160,0,0)
  LabelText = R = 160.00 mm
  TextPosition = (0,0,0)
FEATURE [Part::FeaturePython] aCircle001  # WARN: FeaturePython — macro-defined, semantics opaque (R4)
FEATURE [Part::FeaturePython] Radius001  # WARN: FeaturePython — macro-defined, semantics opaque (R4)
FEATURE [App::AnnotationLabel] MeasureLbl001
  BasePosition = (193.652,-59.2053,369)
  LabelText = R = 202.50 mm
  TextPosition = (0,0,0)
FEATURE [App::DocumentObjectGroup] Measures
  Group = -> [aCircle,Radius,MeasureLbl,aCircle001,Radius001,MeasureLbl001]
---- part composit-properties.FCStd = doc fcstd_d99993d4ac97 ----
FCSTD DOCUMENT  (FreeCAD 1.1R38827 (Git))
Label: composit-properties
License: All rights reserved
LicenseURL: http://en.wikipedia.org/wiki/All_rights_reserved
objects: Spreadsheet::Sheet×1

FEATURE [Spreadsheet::Sheet] Spreadsheet  label="Properties"
  cells = B2(thickness)==3 mm; C2(al_thickness)==0.3 mm; D2(bend_r)==0.1 mm
---- part dropper.FCStd = doc fcstd_03601a3bb068 ----
FCSTD DOCUMENT  (FreeCAD 1.1R38827 (Git))
Label: dropper
License: All rights reserved
LicenseURL: http://en.wikipedia.org/wiki/All_rights_reserved
objects: Sketcher::SketchObject×9, Part::FeaturePython×4, PartDesign::Revolution×3, PartDesign::Body×2, PartDesign::CoordinateSystem×1, Spreadsheet::Sheet×1, PartDesign::SubShapeBinder×1, PartDesign::Pad×1, PartDesign::Pocket×1, PartDesign::Groove×1, App::Part×1
note: 44 computed .brp shape members not serialized (recipe doc carries the construction recipe); baked Part::Feature solids carry a one-line shape summary decoded from their .brp

FEATURE [Sketcher::SketchObject] Sketch005
  ArcFitTolerance = 0
  AttachmentSupport = -> [YZ_Plane001]
  FullyConstrained = true
  MakeInternals = false
  MapMode = 5
  Placement = pos=(0,0,0) rot=(0.57735,0.57735,0.57735;2.0944rad)
  sketch-geometry (14):
    g0: LineSegment StartX=11.3 StartY=0 StartZ=0 EndX=11.3 EndY=1 EndZ=0
    g1: LineSegment StartX=11.3 StartY=1 StartZ=0 EndX=10.7 EndY=1 EndZ=0
    g2: LineSegment StartX=10.7 StartY=1 StartZ=0 EndX=10.7 EndY=9.9 EndZ=0
    g3: LineSegment StartX=10.7 StartY=9.9 StartZ=0 EndX=6.6 EndY=9.9 EndZ=0
    g4: LineSegment StartX=6.6 StartY=9.9 StartZ=0 EndX=6.6 EndY=3 EndZ=0
    g5: LineSegment StartX=6.6 StartY=3 StartZ=0 EndX=2.5 EndY=3 EndZ=0
    g6: LineSegment StartX=2.5 StartY=3 StartZ=0 EndX=2.5 EndY=20 EndZ=0
    g7: LineSegment StartX=2.5 StartY=20 StartZ=0 EndX=1.45 EndY=20 EndZ=0
    g8: LineSegment StartX=1.45 StartY=20 StartZ=0 EndX=1.45 EndY=2.5 EndZ=0
    g9: LineSegment StartX=1.45 StartY=2.5 StartZ=0 EndX=7 EndY=-0.6 EndZ=0
    g10: LineSegment StartX=7 StartY=-0.6 StartZ=0 EndX=7 EndY=8.85 EndZ=0
    g11: LineSegment StartX=7 StartY=8.85 StartZ=0 EndX=9.5 EndY=8.85 EndZ=0
    g12: LineSegment StartX=9.5 StartY=8.85 StartZ=0 EndX=9.5 EndY=0 EndZ=0
    g13: LineSegment StartX=9.5 StartY=0 StartZ=0 EndX=11.3 EndY=0 EndZ=0
  constraints (43):
    c: PointOnObject(g0,g-1)
    c: Vertical(g0)
    c: Coincident(g0,g1)
    c: Horizontal(g1)
    c: Coincident(g1,g2)
    c: Vertical(g2)
    c: Coincident(g2,g3)
    c: Horizontal(g3)
    c: Coincident(g3,g4)
    c: Vertical(g4)
    c: Coincident(g4,g5)
    c: Coincident(g5,g6)
    c: Vertical(g6)
    c: Coincident(g6,g7)
    c: Horizontal(g7)
    c: Coincident(g7,g8)
    c: Vertical(g8)
    c: Coincident(g8,g9)
    c: Coincident(g9,g10)
    c: Vertical(g10)
    c: Coincident(g10,g11)
    c: Horizontal(g11)
    c: Coincident(g11,g12)
    c: Vertical(g12)
    c: Coincident(g12,g13)
    c: Coincident(g13,g0)
    c: Horizontal(g13)
    c: DistanceX(g0) = 11.3  'outer_r'
    c: DistanceY(g0) = 1
    c: DistanceY(g2) = 9.9
    c: DistanceX(g1,g0) = 0.6
    c: DistanceX(g3,g2) = 4.1
    c: DistanceY(g4,g3) = 6.9
    c: DistanceX(g6) = 2.5
    c: DistanceX(g7) = 1.45
    c: DistanceY(g9,g3) = 10.5
    c: DistanceX(g12,g0) = 1.8
    c: DistanceY(g11) = 8.85
    c: DistanceX(g9) = 7
    c: DistanceY(g9,g6) = 20.6
    c: Horizontal(g5)
    c: DistanceY(g8,g5) = 0.5
    c: DistanceY(g7) = 20
FEATURE [PartDesign::Revolution] Revolution002
  Angle = 360
  Angle2 = 60
  Axis = (0,0,1)
  Base = (0,0,0)
  Placement = pos=(0,0,0) rot=(1,1,1;2.0944rad)
  Profile = -> Sketch005
  ReferenceAxis = -> Sketch005 [V_Axis]
  Reversed = true
  Suppressed = false
  Type = 0
FEATURE [Sketcher::SketchObject] Sketch006
  ArcFitTolerance = 0
  AttachmentSupport = -> [YZ_Plane001]
  FullyConstrained = true
  MakeInternals = false
  MapMode = 5
  Placement = pos=(0,0,0) rot=(0.57735,0.57735,0.57735;2.0944rad)
  expr: Constraints[27] = Sketch005.Constraints.outer_r
  expr: Constraints[28] = Sketch005.Constraints[28]
  expr: Constraints[29] = Sketch005.Constraints[29]
  expr: Constraints[30] = Sketch005.Constraints[30]
  expr: Constraints[31] = Sketch005.Constraints[31]
  expr: Constraints[32] = Sketch005.Constraints[32]
  expr: Constraints[33] = Sketch005.Constraints[33]
  expr: Constraints[34] = Sketch005.Constraints[34]
  expr: Constraints[35] = Sketch005.Constraints[35]
  expr: Constraints[36] = Sketch005.Constraints[36]
  expr: Constraints[37] = Sketch005.Constraints[37]
  expr: Constraints[38] = Sketch005.Constraints[38]
  expr: Constraints[39] = Sketch005.Constraints[39]
  expr: Constraints[41] = Sketch005.Constraints[41]
  expr: Constraints[69] = Sketch005.Constraints.outer_r
  expr: Constraints[70] = Sketch005.Constraints[28]
  expr: Constraints[71] = Sketch005.Constraints[29]
  expr: Constraints[72] = Sketch005.Constraints[30]
  expr: Constraints[73] = Sketch005.Constraints[31]
  expr: Constraints[74] = Sketch005.Constraints[32]
  expr: Constraints[75] = Sketch005.Constraints[33]
  expr: Constraints[76] = Sketch005.Constraints[34]
  expr: Constraints[77] = Sketch005.Constraints[35]
  expr: Constraints[78] = Sketch005.Constraints[36]
  expr: Constraints[79] = Sketch005.Constraints[37]
  expr: Constraints[80] = Sketch005.Constraints[38]
  expr: Constraints[81] = Sketch005.Constraints[39]
  expr: Constraints[83] = Sketch005.Constraints[41]
  sketch-geometry (32):
    g0: LineSegment [constr] StartX=11.3 StartY=0 StartZ=0 EndX=11.3 EndY=1 EndZ=0
    g1: LineSegment [constr] StartX=11.3 StartY=1 StartZ=0 EndX=10.7 EndY=1 EndZ=0
    g2: LineSegment [constr] StartX=10.7 StartY=1 StartZ=0 EndX=10.7 EndY=9.9 EndZ=0
    g3: LineSegment [constr] StartX=10.7 StartY=9.9 StartZ=0 EndX=6.6 EndY=9.9 EndZ=0
    g4: LineSegment StartX=6.6 StartY=9.9 StartZ=0 EndX=6.6 EndY=3 EndZ=0
    g5: LineSegment StartX=6.6 StartY=3 StartZ=0 EndX=2.5 EndY=3 EndZ=0
    g6: LineSegment [constr] StartX=2.5 StartY=3 StartZ=0 EndX=2.5 EndY=20 EndZ=0
    g7: LineSegment [constr] StartX=2.5 StartY=20 StartZ=0 EndX=1.45 EndY=20 EndZ=0
    g8: LineSegment [constr] StartX=1.45 StartY=20 StartZ=0 EndX=1.45 EndY=2.5 EndZ=0
    g9: LineSegment [constr] StartX=1.45 StartY=2.5 StartZ=0 EndX=7 EndY=-0.6 EndZ=0
    g10: LineSegment [constr] StartX=7 StartY=-0.6 StartZ=0 EndX=7 EndY=8.85 EndZ=0
    g11: LineSegment [constr] StartX=7 StartY=8.85 StartZ=0 EndX=9.5 EndY=8.85 EndZ=0
    g12: LineSegment [constr] StartX=9.5 StartY=8.85 StartZ=0 EndX=9.5 EndY=0 EndZ=0
    g13: LineSegment [constr] StartX=9.5 StartY=0 StartZ=0 EndX=11.3 EndY=0 EndZ=0
    g14: LineSegment [constr] StartX=11.3 StartY=0 StartZ=0 EndX=11.3 EndY=1 EndZ=0
    g15: LineSegment [constr] StartX=11.3 StartY=1 StartZ=0 EndX=10.7 EndY=1 EndZ=0
    g16: LineSegment [constr] StartX=10.7 StartY=1 StartZ=0 EndX=10.7 EndY=9.9 EndZ=0
    g17: LineSegment [constr] StartX=10.7 StartY=9.9 StartZ=0 EndX=6.6 EndY=9.9 EndZ=0
    g18: LineSegment [constr] StartX=6.6 StartY=9.9 StartZ=0 EndX=6.6 EndY=3 EndZ=0
    g19: LineSegment [constr] StartX=6.6 StartY=3 StartZ=0 EndX=2.5 EndY=3 EndZ=0
    g20: LineSegment [constr] StartX=2.5 StartY=3 StartZ=0 EndX=2.5 EndY=20 EndZ=0
    g21: LineSegment [constr] StartX=2.5 StartY=20 StartZ=0 EndX=1.45 EndY=20 EndZ=0
    g22: LineSegment [constr] StartX=1.45 StartY=20 StartZ=0 EndX=1.45 EndY=2.5 EndZ=0
    g23: LineSegment [constr] StartX=1.45 StartY=2.5 StartZ=0 EndX=7 EndY=-0.6 EndZ=0
    g24: LineSegment [constr] StartX=7 StartY=-0.6 StartZ=0 EndX=7 EndY=8.85 EndZ=0
    g25: LineSegment [constr] StartX=7 StartY=8.85 StartZ=0 EndX=9.5 EndY=8.85 EndZ=0
    g26: LineSegment [constr] StartX=9.5 StartY=8.85 StartZ=0 EndX=9.5 EndY=0 EndZ=0
    g27: LineSegment [constr] StartX=9.5 StartY=0 StartZ=0 EndX=11.3 EndY=0 EndZ=0
    g28: LineSegment StartX=2.5 StartY=3 StartZ=0 EndX=2.04763 EndY=3 EndZ=0
    g29: LineSegment StartX=2.04763 StartY=3 StartZ=0 EndX=2.04763 EndY=12.6758 EndZ=0
    g30: LineSegment StartX=2.04763 StartY=12.6758 StartZ=0 EndX=6.6 EndY=9.9 EndZ=0
    g31: GeomPoint [constr] X=2.5 Y=12.4 Z=0
  constraints (94):
    c: PointOnObject(g0,g-1)
    c: Vertical(g0)
    c: Coincident(g0,g1)
    c: Horizontal(g1)
    c: Coincident(g1,g2)
    c: Vertical(g2)
    c: Coincident(g2,g3)
    c: Horizontal(g3)
    c: Coincident(g3,g4)
    c: Vertical(g4)
    c: Coincident(g4,g5)
    c: Coincident(g5,g6)
    c: Vertical(g6)
    c: Coincident(g6,g7)
    c: Horizontal(g7)
    c: Coincident(g7,g8)
    c: Vertical(g8)
    c: Coincident(g8,g9)
    c: Coincident(g9,g10)
    c: Vertical(g10)
    c: Coincident(g10,g11)
    c: Horizontal(g11)
    c: Coincident(g11,g12)
    c: Vertical(g12)
    c: Coincident(g12,g13)
    c: Coincident(g13,g0)
    c: Horizontal(g13)
    c: DistanceX(g0) = 11.3
    c: DistanceY(g0) = 1
    c: DistanceY(g2) = 9.9
    c: DistanceX(g1,g0) = 0.6
    c: DistanceX(g3,g2) = 4.1
    c: DistanceY(g4,g3) = 6.9
    c: DistanceX(g6) = 2.5
    c: DistanceX(g7) = 1.45
    c: DistanceY(g9,g3) = 10.5
    c: DistanceX(g12,g0) = 1.8
    c: DistanceY(g11) = 8.85
    c: DistanceX(g9) = 7
    c: DistanceY(g9,g6) = 20.6
    c: Horizontal(g5)
    c: DistanceY(g8,g5) = 0.5
    c: PointOnObject(g14,g-1)
    c: Vertical(g14)
    c: Coincident(g14,g15)
    c: Horizontal(g15)
    c: Coincident(g15,g16)
    c: Vertical(g16)
    c: Coincident(g16,g17)
    c: Horizontal(g17)
    c: Coincident(g17,g18)
    c: Vertical(g18)
    c: Coincident(g18,g19)
    c: Coincident(g19,g20)
    c: Vertical(g20)
    c: Coincident(g20,g21)
    c: Horizontal(g21)
    c: Coincident(g21,g22)
    c: Vertical(g22)
    c: Coincident(g22,g23)
    c: Coincident(g23,g24)
    c: Vertical(g24)
    c: Coincident(g24,g25)
    c: Horizontal(g25)
    c: Coincident(g25,g26)
    c: Vertical(g26)
    c: Coincident(g26,g27)
    c: Coincident(g27,g14)
    c: Horizontal(g27)
    c: DistanceX(g14) = 11.3
    c: DistanceY(g14) = 1
    c: DistanceY(g16) = 9.9
    c: DistanceX(g15,g14) = 0.6
    c: DistanceX(g17,g16) = 4.1
    c: DistanceY(g18,g17) = 6.9
    c: DistanceX(g20) = 2.5
    c: DistanceX(g21) = 1.45
    c: DistanceY(g23,g17) = 10.5
    c: DistanceX(g26,g14) = 1.8
    c: DistanceY(g25) = 8.85
    c: DistanceX(g23) = 7
    c: DistanceY(g23,g20) = 20.6
    c: Horizontal(g19)
    c: DistanceY(g22,g19) = 0.5
    c: Coincident(g28,g5)
    c: Horizontal(g28)
    c: Coincident(g29,g28)
    c: Vertical(g29)
    c: Coincident(g30,g29)
    c: Coincident(g30,g4)
    c: PointOnObject(g31,g30)
    c: PointOnObject(g31,g6)
    c: DistanceY(g4,g31) = 2.5
    c: DistanceX(g29,g31) = 0.452366
FEATURE [PartDesign::Body] Body001
  AllowCompound = false
  Group = -> [Sketch005,Revolution002,Sketch006]
  Origin = -> Origin001
  Placement = pos=(0,0,2.5) rot=(0,0,1;0rad)
  Tip = -> Revolution002
FEATURE [Sketcher::SketchObject] Sketch007  label="base"
  ArcFitTolerance = 0
  FullyConstrained = true
  MakeInternals = false
  expr: .Constraints.r = Sketch005.Constraints.outer_r + 0.5 mm
  sketch-geometry (1):
    g0: Circle CenterX=0 CenterY=0 CenterZ=0 NormalX=0 NormalY=0 NormalZ=1 AngleXU=0 Radius=11.8
  constraints (2):
    c: Coincident(g0,g-1)
    c: Radius(g0) = 11.8  'r'
FEATURE [Sketcher::SketchObject] Sketch002
  ArcFitTolerance = 0
  AttachmentSupport = -> [YZ_Plane]
  FullyConstrained = true
  MakeInternals = false
  MapMode = 5
  Placement = pos=(0,0,0) rot=(0.57735,0.57735,0.57735;2.0944rad)
  expr: Constraints[18] = Sketch001.Constraints[18]
  expr: Constraints[19] = Sketch001.Constraints[19]
  expr: Constraints[20] = Sketch001.Constraints[20]
  expr: Constraints[21] = Sketch001.Constraints[21]
  expr: Constraints[22] = Sketch001.Constraints[22]
  expr: Constraints[23] = Sketch001.Constraints[23]
  expr: Constraints[24] = Sketch001.Constraints[24]
  expr: Constraints[25] = Sketch001.Constraints[25]
  expr: Constraints[27] = Sketch001.Constraints[27]
  sketch-geometry (13):
    g0: LineSegment [constr] StartX=1.15 StartY=0 StartZ=0 EndX=1.15 EndY=-18.1612 EndZ=0
    g1: LineSegment StartX=1.15 StartY=-18.1612 StartZ=0 EndX=2.765 EndY=-8.77 EndZ=0
    g2: LineSegment [constr] StartX=2.765 StartY=-8.77 StartZ=0 EndX=2.2 EndY=-8.77 EndZ=0
    g3: LineSegment [constr] StartX=2.2 StartY=-8.77 StartZ=0 EndX=2.2 EndY=-5.32 EndZ=0
    g4: LineSegment [constr] StartX=2.2 StartY=-5.32 StartZ=0 EndX=3.35 EndY=-5.32 EndZ=0
    g5: LineSegment [constr] StartX=3.35 StartY=-5.32 StartZ=0 EndX=3.35 EndY=-3.66 EndZ=0
    g6: LineSegment [constr] StartX=3.35 StartY=-3.66 StartZ=0 EndX=2.65 EndY=-3.66 EndZ=0
    g7: LineSegment [constr] StartX=2.65 StartY=-3.66 StartZ=0 EndX=2.65 EndY=0 EndZ=0
    g8: LineSegment [constr] StartX=2.65 StartY=0 StartZ=0 EndX=1.15 EndY=0 EndZ=0
    g9: GeomPoint [constr] X=-2.765 Y=-8.77 Z=0
    g10: GeomPoint [constr] X=-2.765 Y=-8.77 Z=0
    g11: LineSegment StartX=1.15 StartY=-18.1612 StartZ=0 EndX=-3.0574 EndY=-18.1612 EndZ=0
    g12: LineSegment StartX=-3.0574 StartY=-18.1612 StartZ=0 EndX=2.765 EndY=-8.77 EndZ=0
  constraints (34):
    c: PointOnObject(g0,g-1)
    c: Vertical(g0)
    c: Coincident(g0,g1)
    c: Coincident(g1,g2)
    c: Horizontal(g2)
    c: Coincident(g2,g3)
    c: Vertical(g3)
    c: Coincident(g3,g4)
    c: Horizontal(g4)
    c: Coincident(g4,g5)
    c: Vertical(g5)
    c: Coincident(g5,g6)
    c: Horizontal(g6)
    c: Coincident(g6,g7)
    c: PointOnObject(g7,g-1)
    c: Vertical(g7)
    c: Coincident(g7,g8)
    c: Coincident(g8,g0)
    c: DistanceY(g2,g3) = 3.45
    c: DistanceY(g4,g5) = 1.66
    c: DistanceY(g6,g7) = 3.66
    c: DistanceX(g2) = 2.2
    c: DistanceX(g4) = 3.35
    c: DistanceX(g0) = 1.15
    c: DistanceX(g7) = 2.65
    c: DistanceX(g1) = 2.765
    c: Symmetric(g9,g1,g-2)
    c: Distance(g9,g1) = 5.45
    c: Symmetric(g10,g1,g-2)
    c: Coincident(g11,g1)
    c: Horizontal(g11)
    c: Coincident(g12,g11)
    c: Coincident(g12,g1)
    c: Distance(g9,g12) = 4.7
FEATURE [Sketcher::SketchObject] Sketch001
  ArcFitTolerance = 0
  AttachmentSupport = -> [XZ_Plane]
  FullyConstrained = true
  MakeInternals = false
  MapMode = 5
  Placement = pos=(0,0,0) rot=(1,0,0;1.5708rad)
  sketch-geometry (10):
    g0: LineSegment StartX=1.15 StartY=0 StartZ=0 EndX=1.15 EndY=-18.1612 EndZ=0
    g1: LineSegment StartX=1.15 StartY=-18.1612 StartZ=0 EndX=2.765 EndY=-8.77 EndZ=0
    g2: LineSegment StartX=2.765 StartY=-8.77 StartZ=0 EndX=2.2 EndY=-8.77 EndZ=0
    g3: LineSegment StartX=2.2 StartY=-8.77 StartZ=0 EndX=2.2 EndY=-5.32 EndZ=0
    g4: LineSegment StartX=2.2 StartY=-5.32 StartZ=0 EndX=3.35 EndY=-5.32 EndZ=0
    g5: LineSegment StartX=3.35 StartY=-5.32 StartZ=0 EndX=3.35 EndY=-3.66 EndZ=0
    g6: LineSegment StartX=3.35 StartY=-3.66 StartZ=0 EndX=2.65 EndY=-3.66 EndZ=0
    g7: LineSegment StartX=2.65 StartY=-3.66 StartZ=0 EndX=2.65 EndY=0 EndZ=0
    g8: LineSegment StartX=2.65 StartY=0 StartZ=0 EndX=1.15 EndY=0 EndZ=0
    g9: GeomPoint [constr] X=-2.765 Y=-8.77 Z=0
  constraints (28):
    c: PointOnObject(g0,g-1)
    c: Vertical(g0)
    c: Coincident(g0,g1)
    c: Coincident(g1,g2)
    c: Horizontal(g2)
    c: Coincident(g2,g3)
    c: Vertical(g3)
    c: Coincident(g3,g4)
    c: Horizontal(g4)
    c: Coincident(g4,g5)
    c: Vertical(g5)
    c: Coincident(g5,g6)
    c: Horizontal(g6)
    c: Coincident(g6,g7)
    c: PointOnObject(g7,g-1)
    c: Vertical(g7)
    c: Coincident(g7,g8)
    c: Coincident(g8,g0)
    c: DistanceY(g2,g3) = 3.45
    c: DistanceY(g4,g5) = 1.66
    c: DistanceY(g6,g7) = 3.66
    c: DistanceX(g2) = 2.2
    c: DistanceX(g4) = 3.35
    c: DistanceX(g0) = 1.15
    c: DistanceX(g7) = 2.65
    c: DistanceX(g1) = 2.765
    c: Symmetric(g9,g1,g-2)
    c: Distance(g9,g1) = 5.45
FEATURE [Sketcher::SketchObject] Sketch  label="fix_sketch"
  ArcFitTolerance = 0
  AttachmentSupport = -> [XY_Plane]
  FullyConstrained = true
  MakeInternals = false
  MapMode = 5
  sketch-geometry (5):
    g0: ArcOfCircle CenterX=0 CenterY=0 CenterZ=0 NormalX=0 NormalY=0 NormalZ=1 AngleXU=0 Radius=10.5 StartAngle=0.496317 EndAngle=1.5708
    g1: ArcOfCircle CenterX=16.5 CenterY=0 CenterZ=0 NormalX=0 NormalY=0 NormalZ=1 AngleXU=0 Radius=3.25 StartAngle=0 EndAngle=1.34547
    g2: LineSegment StartX=17.2261 StartY=3.16784 StartZ=0 EndX=9.23309 EndY=5 EndZ=0
    g3: GeomPoint [constr] X=-19.75 Y=0 Z=0
    g4: GeomPoint [constr] X=0 Y=-10.5 Z=0
  constraints (14):
    c: PointOnObject(g0,g-2)
    c: PointOnObject(g1,g-1)
    c: PointOnObject(g1,g-1)
    c: Coincident(g2,g0)
    c: Tangent(g2,g1) = -1.5708
    c: Diameter(g0) = 21
    c: DistanceX(g1) = 19.75
    c: DistanceY(g0) = 5
    c: Diameter(g1) = 6.5
    c: Coincident(g0,g-1)
    c: Symmetric(g3,g1,g-2)
    c: DistanceX(g3,g1) = 39.5  'length'
    c: Symmetric(g4,g0,g-1)
    c: DistanceY(g4,g0) = 21  'width'
FEATURE [Sketcher::SketchObject] Sketch004
  ArcFitTolerance = 0
  AttachmentSupport = -> [YZ_Plane]
  FullyConstrained = true
  MakeInternals = false
  MapMode = 5
  Placement = pos=(0,0,0) rot=(0.57735,0.57735,0.57735;2.0944rad)
  expr: Constraints[3] = Sketch003.Constraints[9]
  sketch-geometry (6):
    g0: LineSegment StartX=7.75 StartY=10.9 StartZ=0 EndX=0 EndY=10.9 EndZ=0
    g1: LineSegment StartX=0 StartY=10.9 StartZ=0 EndX=0 EndY=1.5 EndZ=0
    g2: LineSegment StartX=0 StartY=1.5 StartZ=0 EndX=7.25 EndY=1.5 EndZ=0
    g3: LineSegment StartX=7.25 StartY=1.5 StartZ=0 EndX=7.25 EndY=2.5 EndZ=0
    g4: LineSegment StartX=7.25 StartY=2.5 StartZ=0 EndX=7.75 EndY=4 EndZ=0
    g5: LineSegment StartX=7.75 StartY=4 StartZ=0 EndX=7.75 EndY=10.9 EndZ=0
  constraints (18):
    c: Coincident(g0,g1)
    c: Horizontal(g0)
    c: Vertical(g1)
    c: DistanceY(g0) = 10.9
    c: Horizontal(g2)
    c: Coincident(g2,g3)
    c: Vertical(g3)
    c: Coincident(g3,g4)
    c: Coincident(g4,g5)
    c: Vertical(g5)
    c: Coincident(g0,g5)
    c: Coincident(g1,g2)
    c: DistanceY(g1,g0) = 9.4
    c: DistanceX(g0) = 7.75
    c: DistanceY(g2,g3) = 1
    c: DistanceY(g3,g4) = 1.5
    c: DistanceX(g2,g4) = 0.5
    c: Vertical(g1,g-1)
FEATURE [Sketcher::SketchObject] Sketch003
  ArcFitTolerance = 0
  AttachmentSupport = -> [YZ_Plane]
  FullyConstrained = true
  MakeInternals = false
  MapMode = 5
  Placement = pos=(0,0,0) rot=(0.57735,0.57735,0.57735;2.0944rad)
  sketch-geometry (4):
    g0: LineSegment StartX=0 StartY=0 StartZ=0 EndX=8.825 EndY=0 EndZ=0
    g1: LineSegment StartX=8.825 StartY=0 StartZ=0 EndX=8.825 EndY=10.9 EndZ=0
    g2: LineSegment StartX=8.825 StartY=10.9 StartZ=0 EndX=0 EndY=10.9 EndZ=0
    g3: LineSegment StartX=0 StartY=10.9 StartZ=0 EndX=0 EndY=0 EndZ=0
  constraints (11):
    c: Coincident(g0,g1)
    c: Coincident(g1,g2)
    c: Coincident(g2,g3)
    c: Coincident(g3,g0)
    c: Horizontal(g0)
    c: Horizontal(g2)
    c: Vertical(g1)
    c: Vertical(g3)
    c: Coincident(g0,g-1)
    c: DistanceY(g2) = 10.9
    c: DistanceX(g0) = 8.825
FEATURE [PartDesign::CoordinateSystem] LCS_0
  AttacherType = Attacher::AttachEngine3D
  AttachmentOffset = pos=(0,0,2.45) rot=(0,0,1;0rad)
  AttachmentSupport = -> [X_Axis002]
  MapMode = 2
  Placement = pos=(0,0,2.45) rot=(0,0,1;0rad)
FEATURE [Spreadsheet::Sheet] Spreadsheet  label="Properties"
  cells = B2(top_d)==22.6 mm; C2(bot_d)==21 mm; D2(top_height)==20 mm; E2(bot_base_height)==2.4 mm; F2(total_height)==22.4 mm; G2(total_width)==38.9 mm
FEATURE [Part::FeaturePython] Mirror  label="Mirror of Sketch"  # WARN: FeaturePython — macro-defined, semantics opaque (R4)
  ExposePlacement = false
  FlipX = true
  FlipY = false
  FlipZ = false
  MarkerShape = 1
  MarkerSize = 0
  NumElements = 0
  Object = -> Sketch
  ObjectTraversal = 0
  Type = lattice2Mirror.LatticeMirror
  isLattice = 0
FEATURE [Part::FeaturePython] Mirror001  label="Mirror001 of Mirror of Sketch"  # WARN: FeaturePython — macro-defined, semantics opaque (R4)
  ExposePlacement = false
  FlipX = false
  FlipY = true
  FlipZ = false
  MarkerShape = 1
  MarkerSize = 0
  NumElements = 0
  Object = -> Mirror
  ObjectTraversal = 0
  Type = lattice2Mirror.LatticeMirror
  isLattice = 0
FEATURE [Part::FeaturePython] Mirror002  label="Mirror002 of Mirror001 of Mirror of Sketch"  # WARN: FeaturePython — macro-defined, semantics opaque (R4)
  ExposePlacement = false
  FlipX = true
  FlipY = false
  FlipZ = false
  MarkerShape = 1
  MarkerSize = 0
  NumElements = 0
  Object = -> Mirror001
  ObjectTraversal = 0
  Type = lattice2Mirror.LatticeMirror
  isLattice = 0
FEATURE [PartDesign::SubShapeBinder] Binder
  BindCopyOnChange = 0
  BindMode = 0
  ClaimChildren = true
  Context = -> Part [Body.Binder.]
  Fuse = false
  MakeFace = true
  OffsetFill = false
  OffsetIntersection = false
  OffsetJoinType = 0
  OffsetOpenResult = false
  PartialLoad = false
  Relative = true
  Support = -> [Connect]
  _Version = 2
FEATURE [PartDesign::Pad] Pad
  Direction = (0,0,1)
  Length = 2.45
  Length2 = 10
  Profile = -> Binder
  Suppressed = false
  Type = 0
FEATURE [PartDesign::Revolution] Revolution
  Angle = 360
  Angle2 = 60
  Axis = (0,2e-16,1)
  Base = (0,0,0)
  BaseFeature = -> Pad
  Profile = -> Sketch001
  ReferenceAxis = -> Sketch001 [V_Axis]
  Reversed = true
  Suppressed = false
  Type = 0
FEATURE [PartDesign::Pocket] Pocket
  BaseFeature = -> Revolution
  Direction = (-1,0,0)
  Length = 5
  Length2 = 5
  Midplane = true
  Profile = -> Sketch002
  ReferenceAxis = -> Sketch002 [N_Axis]
  Suppressed = false
  Type = 1
FEATURE [PartDesign::Revolution] Revolution001
  Angle = 360
  Angle2 = 60
  Axis = (0,0,1)
  Base = (0,0,0)
  BaseFeature = -> Pocket
  Profile = -> Sketch003
  ReferenceAxis = -> Sketch003 [V_Axis]
  Reversed = true
  Suppressed = false
  Type = 0
FEATURE [PartDesign::Groove] Groove
  Angle = 360
  Angle2 = 60
  Axis = (0,0,1)
  Base = (0,0,0)
  BaseFeature = -> Revolution001
  Profile = -> Sketch004
  ReferenceAxis = -> Sketch004 [V_Axis]
  Suppressed = false
  Type = 0
FEATURE [Sketcher::SketchObject] Sketch008  label="feed"
  ArcFitTolerance = 0
  AttachmentSupport = -> [XY_Plane]
  FullyConstrained = true
  MakeInternals = false
  MapMode = 5
  sketch-geometry (1):
    g0: Circle CenterX=0 CenterY=0 CenterZ=0 NormalX=0 NormalY=0 NormalZ=1 AngleXU=0 Radius=4
  constraints (2):
    c: Coincident(g0,g-1)
    c: Diameter(g0) = 8
FEATURE [PartDesign::Body] Body
  AllowCompound = false
  Group = -> [Sketch,Pad,Sketch001,Revolution,Sketch002,Pocket,Sketch003,Sketch004,Revolution001,Groove,Sketch008,Binder]
  Origin = -> Origin
  Tip = -> Groove
FEATURE [App::Part] Part  label="dropper"
  Group = -> [LCS_0,Body001,Body]
  Origin = -> Origin002
FEATURE [Part::FeaturePython] Connect  label="fix"  # WARN: FeaturePython — macro-defined, semantics opaque (R4)
  Objects = -> [Sketch,Mirror002,Mirror001,Mirror]
  Tolerance = 0
---- part hub2108.FCStd = doc fcstd_856699a5e2c1 ----
FCSTD DOCUMENT  (FreeCAD 1.1R38827 (Git))
Label: hub2108
License: All rights reserved
LicenseURL: http://en.wikipedia.org/wiki/All_rights_reserved
objects: Sketcher::SketchObject×5, PartDesign::CoordinateSystem×2, PartDesign::AdditiveCylinder×1, PartDesign::Body×1
note: 16 computed .brp shape members not serialized (recipe doc carries the construction recipe); baked Part::Feature solids carry a one-line shape summary decoded from their .brp

FEATURE [Sketcher::SketchObject] Sketch  label="top_fix_holes"
  ArcFitTolerance = 0
  FullyConstrained = true
  MakeInternals = false
  expr: Constraints[6] = (58.8 mm + 38 mm) / 2
  expr: Constraints[7] = (87.5 mm + 66.67 mm) / 2
  expr: Constraints[8] = (76.14 mm + 96.68 mm) / 2
  sketch-geometry (5):
    g0: Circle CenterX=38.5425 CenterY=-28.0433 CenterZ=0 NormalX=0 NormalY=0 NormalZ=1 AngleXU=0 Radius=5.1
    g1: Circle CenterX=43.205 CenterY=20.1316 CenterZ=0 NormalX=0 NormalY=0 NormalZ=1 AngleXU=0 Radius=5.1
    g2: Circle CenterX=-43.205 CenterY=20.1316 CenterZ=0 NormalX=0 NormalY=0 NormalZ=1 AngleXU=0 Radius=5.1
    g3: Circle CenterX=-38.5425 CenterY=-28.0433 CenterZ=0 NormalX=0 NormalY=0 NormalZ=1 AngleXU=0 Radius=5.1
    g4: Circle [constr] CenterX=0 CenterY=0 CenterZ=0 NormalX=0 NormalY=0 NormalZ=1 AngleXU=0 Radius=47.665
  constraints (13):
    c: Equal(g3,g2)
    c: Equal(g3,g1)
    c: Equal(g3,g0)
    c: Diameter(g3) = 10.2
    c: Symmetric(g0,g3,g-2)
    c: Symmetric(g1,g2,g-2)
    c: Distance(g0,g1) = 48.4
    c: Distance(g0,g3) = 77.085
    c: Distance(g2,g1) = 86.41
    c: Coincident(g4,g-1)
    c: PointOnObject(g0,g4)
    c: Distance(g3,g1) = 94.8866
    c: PointOnObject(g1,g4)
FEATURE [Sketcher::SketchObject] Sketch001  label="top_center_hole"
  ArcFitTolerance = 0
  FullyConstrained = true
  MakeInternals = false
  sketch-geometry (1):
    g0: Circle CenterX=0 CenterY=0 CenterZ=0 NormalX=0 NormalY=0 NormalZ=1 AngleXU=0 Radius=28
  constraints (2):
    c: Coincident(g0,g-1)
    c: Diameter(g0) = 56
FEATURE [Sketcher::SketchObject] Sketch002  label="bottom_fix_holes"
  ArcFitTolerance = 0
  FullyConstrained = true
  MakeInternals = false
  expr: Constraints[7] = (80 mm + 58.3 mm) / 4
  sketch-geometry (6):
    g0: Circle CenterX=34.575 CenterY=34.575 CenterZ=0 NormalX=0 NormalY=0 NormalZ=1 AngleXU=0 Radius=5.4
    g1: LineSegment [constr] StartX=34.575 StartY=34.575 StartZ=0 EndX=34.575 EndY=0 EndZ=0
    g2: LineSegment [constr] StartX=34.575 StartY=34.575 StartZ=0 EndX=0 EndY=34.575 EndZ=0
    g3: Circle CenterX=-34.575 CenterY=34.575 CenterZ=0 NormalX=0 NormalY=0 NormalZ=1 AngleXU=0 Radius=5.4
    g4: Circle CenterX=-34.575 CenterY=-34.575 CenterZ=0 NormalX=0 NormalY=0 NormalZ=1 AngleXU=0 Radius=5.4
    g5: Circle CenterX=34.575 CenterY=-34.575 CenterZ=0 NormalX=0 NormalY=0 NormalZ=1 AngleXU=0 Radius=5.4
  constraints (15):
    c: Coincident(g1,g0)
    c: PointOnObject(g1,g-1)
    c: Vertical(g1)
    c: Coincident(g2,g0)
    c: PointOnObject(g2,g-2)
    c: Horizontal(g2)
    c: Equal(g1,g2)
    c: DistanceY(g1,g1) = 34.575
    c: Diameter(g0) = 10.8
    c: Symmetric(g5,g0,g-1)
    c: Symmetric(g3,g0,g-2)
    c: Symmetric(g0,g4,g-1)
    c: Equal(g0,g5)
    c: Equal(g5,g4)
    c: Equal(g4,g3)
FEATURE [Sketcher::SketchObject] Sketch003  label="bottom_center_hole"
  ArcFitTolerance = 0
  FullyConstrained = true
  MakeInternals = false
  sketch-geometry (1):
    g0: Circle CenterX=0 CenterY=0 CenterZ=0 NormalX=0 NormalY=0 NormalZ=1 AngleXU=0 Radius=30.2
  constraints (2):
    c: Coincident(g0,g-1)
    c: Diameter(g0) = 60.4
FEATURE [PartDesign::AdditiveCylinder] Cylinder
  Angle = 360
  AttacherType = Attacher::AttachEngine3D
  AttachmentSupport = -> [XY_Plane]
  FirstAngle = 0
  Height = 67
  MapMode = 5
  Radius = 58
  SecondAngle = 0
  Suppressed = false
FEATURE [PartDesign::CoordinateSystem] Local_CS  label="bottom"
  AttacherType = Attacher::AttachEngine3D
  AttachmentSupport = -> [XY_Plane]
  MapMode = 5
FEATURE [PartDesign::CoordinateSystem] Local_CS001  label="top"
  AttacherType = Attacher::AttachEngine3D
  AttachmentOffset = pos=(0,0,67) rot=(0,0,1;0rad)
  AttachmentSupport = -> [XY_Plane]
  MapMode = 5
  Placement = pos=(0,0,67) rot=(0,0,1;0rad)
  expr: .AttachmentOffset.Base.z = Cylinder.Height
FEATURE [Sketcher::SketchObject] Sketch004
  ArcFitTolerance = 0
  AttachmentSupport = -> [XY_Plane]
  FullyConstrained = false
  MakeInternals = false
  MapMode = 5
  sketch-geometry (1):
    g0: Circle CenterX=0 CenterY=-2.41744 CenterZ=0 NormalX=0 NormalY=0 NormalZ=1 AngleXU=0 Radius=27.7935
  constraints (1):
    c: PointOnObject(g0,g-2)
FEATURE [PartDesign::Body] Body  label="hub2108"
  AllowCompound = false
  Group = -> [Cylinder,Local_CS,Local_CS001,Sketch004]
  Origin = -> Origin
  Tip = -> Cylinder
---- part module.FCStd = doc fcstd_3955753b3a20 ----
FCSTD DOCUMENT  (FreeCAD 1.1R38827 (Git))
Label: module
License: All rights reserved
LicenseURL: http://en.wikipedia.org/wiki/All_rights_reserved
objects: Sketcher::SketchObject×2, Part::Feature×1, PartDesign::FeatureBase×1, PartDesign::Body×1, Spreadsheet::Sheet×1
note: 8 computed .brp shape members not serialized (recipe doc carries the construction recipe); baked Part::Feature solids carry a one-line shape summary decoded from their .brp

FEATURE [Part::Feature] Part__Feature  label="module002"
  shape: bbox 170 x 148 x 41.12 mm, 715 faces (baked)
FEATURE [Sketcher::SketchObject] Sketch  label="module_holes"
  ArcFitTolerance = 0
  FullyConstrained = true
  MakeInternals = false
  sketch-geometry (10):
    g0: LineSegment StartX=59.5 StartY=-3.5 StartZ=0 EndX=59.5 EndY=3.5 EndZ=0
    g1: LineSegment StartX=59.5 StartY=3.5 StartZ=0 EndX=72.5 EndY=3.5 EndZ=0
    g2: LineSegment StartX=72.5 StartY=3.5 StartZ=0 EndX=72.5 EndY=-3.5 EndZ=0
    g3: LineSegment StartX=72.5 StartY=-3.5 StartZ=0 EndX=59.5 EndY=-3.5 EndZ=0
    g4: GeomPoint [constr] X=66 Y=0 Z=0
    g5: LineSegment StartX=-72.5 StartY=-3.5 StartZ=0 EndX=-72.5 EndY=3.5 EndZ=0
    g6: LineSegment StartX=-72.5 StartY=3.5 StartZ=0 EndX=-59.5 EndY=3.5 EndZ=0
    g7: LineSegment StartX=-59.5 StartY=3.5 StartZ=0 EndX=-59.5 EndY=-3.5 EndZ=0
    g8: LineSegment StartX=-59.5 StartY=-3.5 StartZ=0 EndX=-72.5 EndY=-3.5 EndZ=0
    g9: GeomPoint [constr] X=-66 Y=0 Z=0
  constraints (25):
    c: Coincident(g0,g1)
    c: Coincident(g1,g2)
    c: Coincident(g2,g3)
    c: Coincident(g3,g0)
    c: Horizontal(g1)
    c: Horizontal(g3)
    c: Vertical(g0)
    c: Vertical(g2)
    c: Symmetric(g1,g0,g4)
    c: PointOnObject(g4,g-1)
    c: Coincident(g5,g6)
    c: Coincident(g6,g7)
    c: Coincident(g7,g8)
    c: Coincident(g8,g5)
    c: Horizontal(g6)
    c: Horizontal(g8)
    c: Vertical(g5)
    c: Vertical(g7)
    c: Symmetric(g6,g5,g9)
    c: Symmetric(g9,g4,g-2)
    c: Equal(g1,g6)
    c: Equal(g7,g2)
    c: DistanceX(g1,g1) = 13
    c: DistanceY(g2,g2) = 7
    c: DistanceX(g9,g4) = 132
FEATURE [PartDesign::FeatureBase] BaseFeature
  BaseFeature = -> Part__Feature
  Placement = pos=(0,0,0) rot=(0,0,1;1.5708rad)
  Suppressed = false
FEATURE [PartDesign::Body] Body  label="module_Body"
  AllowCompound = false
  BaseFeature = -> Part__Feature
  Group = -> [BaseFeature]
  Origin = -> Origin
  Tip = -> BaseFeature
FEATURE [Spreadsheet::Sheet] Spreadsheet  label="Properties"
  cells = B2(module_width)==148 mm; C2(module_height)==160 mm; D2(module_fixture_distance_x)==132 mm; E2(module_fixture_distance_y)==80 mm; F2(module_hole_x)==13 mm; G2(module_hole_y)==7 mm
FEATURE [Sketcher::SketchObject] Sketch001  label="module_holes001"
  ArcFitTolerance = 0
  FullyConstrained = true
  MakeInternals = false
  sketch-geometry (10):
    g0: LineSegment StartX=59 StartY=-3.5 StartZ=0 EndX=59 EndY=3.5 EndZ=0
    g1: LineSegment StartX=59 StartY=3.5 StartZ=0 EndX=73 EndY=3.5 EndZ=0
    g2: LineSegment StartX=73 StartY=3.5 StartZ=0 EndX=73 EndY=-3.5 EndZ=0
    g3: LineSegment StartX=73 StartY=-3.5 StartZ=0 EndX=59 EndY=-3.5 EndZ=0
    g4: GeomPoint [constr] X=66 Y=0 Z=0
    g5: LineSegment StartX=-73 StartY=-3.5 StartZ=0 EndX=-73 EndY=3.5 EndZ=0
    g6: LineSegment StartX=-73 StartY=3.5 StartZ=0 EndX=-59 EndY=3.5 EndZ=0
    g7: LineSegment StartX=-59 StartY=3.5 StartZ=0 EndX=-59 EndY=-3.5 EndZ=0
    g8: LineSegment StartX=-59 StartY=-3.5 StartZ=0 EndX=-73 EndY=-3.5 EndZ=0
    g9: GeomPoint [constr] X=-66 Y=0 Z=0
  constraints (25):
    c: Coincident(g0,g1)
    c: Coincident(g1,g2)
    c: Coincident(g2,g3)
    c: Coincident(g3,g0)
    c: Horizontal(g1)
    c: Horizontal(g3)
    c: Vertical(g0)
    c: Vertical(g2)
    c: Symmetric(g1,g0,g4)
    c: PointOnObject(g4,g-1)
    c: Coincident(g5,g6)
    c: Coincident(g6,g7)
    c: Coincident(g7,g8)
    c: Coincident(g8,g5)
    c: Horizontal(g6)
    c: Horizontal(g8)
    c: Vertical(g5)
    c: Vertical(g7)
    c: Symmetric(g6,g5,g9)
    c: Symmetric(g9,g4,g-2)
    c: Equal(g1,g6)
    c: Equal(g7,g2)
    c: DistanceX(g1,g1) = 14
    c: DistanceY(g2,g2) = 7
    c: DistanceX(g9,g4) = 132
---- part prima_jamb.FCStd = doc fcstd_baa8a8553cea ----
FCSTD DOCUMENT  (FreeCAD 1.1R38827 (Git))
Label: prima_jamb
License: All rights reserved
LicenseURL: http://en.wikipedia.org/wiki/All_rights_reserved
objects: Sketcher::SketchObject×1, PartDesign::Revolution×1, Part::Cylinder×1, Part::Compound×1, PartDesign::Boolean×1, PartDesign::CoordinateSystem×1, PartDesign::Body×1
note: 11 computed .brp shape members not serialized (recipe doc carries the construction recipe); baked Part::Feature solids carry a one-line shape summary decoded from their .brp

FEATURE [Sketcher::SketchObject] Sketch
  ArcFitTolerance = 0
  AttachmentSupport = -> [XZ_Plane]
  FullyConstrained = true
  MakeInternals = false
  MapMode = 5
  Placement = pos=(0,0,0) rot=(1,0,0;1.5708rad)
  sketch-geometry (6):
    g0: LineSegment StartX=0 StartY=0 StartZ=0 EndX=20.75 EndY=0 EndZ=0
    g1: LineSegment StartX=20.75 StartY=0 StartZ=0 EndX=20.75 EndY=48.0542 EndZ=0
    g2: ArcOfCircle CenterX=18.1 CenterY=40.4 CenterZ=0 NormalX=0 NormalY=0 NormalZ=1 AngleXU=0 Radius=8.1 StartAngle=1.2375 EndAngle=3.14159
    g3: LineSegment StartX=0 StartY=0 StartZ=0 EndX=0 EndY=40.4 EndZ=0
    g4: LineSegment StartX=0 StartY=40.4 StartZ=0 EndX=10 EndY=40.4 EndZ=0
    g5: LineSegment [constr] StartX=0 StartY=48.5 StartZ=0 EndX=18.1 EndY=48.5 EndZ=0
  constraints (18):
    c: Coincident(g-1,g0)
    c: PointOnObject(g0,g-1)
    c: Coincident(g0,g1)
    c: Vertical(g1)
    c: Coincident(g0,g3)
    c: PointOnObject(g3,g-2)
    c: Coincident(g3,g4)
    c: Coincident(g4,g2)
    c: Horizontal(g4)
    c: DistanceX(g0) = 20.75
    c: Perpendicular(g2,g4)
    c: DistanceX(g2) = 10
    c: Tangent(g5,g2) = 1.5708
    c: Horizontal(g5)
    c: PointOnObject(g5,g-2)
    c: DistanceY(g3,g5) = 8.1
    c: Coincident(g1,g2)
    c: DistanceY(g5) = 48.5
FEATURE [PartDesign::Revolution] Revolution
  Angle = 360
  Angle2 = 60
  Axis = (0,2e-16,1)
  Base = (0,0,0)
  Placement = pos=(0,0,0) rot=(1,0,0;1.5708rad)
  Profile = -> Sketch
  ReferenceAxis = -> Sketch [V_Axis]
  Reversed = true
  Suppressed = false
  Type = 0
FEATURE [Part::Cylinder] Cylinder
  Angle = 360
  AttacherType = Attacher::AttachEngine3D
  FirstAngle = 0
  Height = 50
  Radius = 3.5
  SecondAngle = 0
FEATURE [Part::Compound] Compound
  Links = -> [Cylinder]
FEATURE [PartDesign::Boolean] Boolean
  BaseFeature = -> Revolution
  Group = -> [Compound]
  Suppressed = false
  Type = 1
  UsePlacement = true
FEATURE [PartDesign::CoordinateSystem] Local_CS
  AttacherType = Attacher::AttachEngine3D
  AttachmentSupport = -> [XY_Plane]
  MapMode = 5
FEATURE [PartDesign::Body] Body  label="prima_jamb"
  AllowCompound = false
  Group = -> [Sketch,Revolution,Boolean,Local_CS]
  Origin = -> Origin
  Tip = -> Boolean
---- part socket_fixture.FCStd = doc fcstd_b5b55a086a53 ----
FCSTD DOCUMENT  (FreeCAD 1.1R38827 (Git))
Label: socket_fixture
License: All rights reserved
LicenseURL: http://en.wikipedia.org/wiki/All_rights_reserved
objects: Sketcher::SketchObject×5, PartDesign::Pocket×4, PartDesign::FeaturePython×2, Part::FeaturePython×1, PartDesign::Body×1, Part::Feature×1
note: 29 computed .brp shape members not serialized (recipe doc carries the construction recipe); baked Part::Feature solids carry a one-line shape summary decoded from their .brp
EXTERNAL_REF file=composit-properties.FCStd obj=Spreadsheet

FEATURE [Sketcher::SketchObject] Sketch
  ArcFitTolerance = 0
  AttachmentSupport = -> [XY_Plane]
  FullyConstrained = true
  MakeInternals = false
  MapMode = 5
  sketch-geometry (5):
    g0: LineSegment StartX=-19 StartY=20 StartZ=0 EndX=-19 EndY=0 EndZ=0
    g1: LineSegment StartX=-19 StartY=0 StartZ=0 EndX=19 EndY=0 EndZ=0
    g2: LineSegment StartX=19 StartY=0 StartZ=0 EndX=19 EndY=20 EndZ=0
    g3: LineSegment [constr] StartX=19 StartY=20 StartZ=0 EndX=-19 EndY=20 EndZ=0
    g4: GeomPoint [constr] X=0 Y=10 Z=0
  constraints (13):
    c: Coincident(g0,g1)
    c: Coincident(g1,g2)
    c: Coincident(g2,g3)
    c: Coincident(g3,g0)
    c: Horizontal(g1)
    c: Horizontal(g3)
    c: Vertical(g0)
    c: Vertical(g2)
    c: Symmetric(g1,g0,g4)
    c: PointOnObject(g4,g-2)
    c: PointOnObject(g1,g-1)
    c: DistanceX(g1,g1) = 38  'width'
    c: DistanceY(g2,g2) = 20  'length'
FEATURE [PartDesign::FeaturePython] BaseBend  # WARN: FeaturePython — macro-defined, semantics opaque (R4)
  BendSide = 1
  BendSketch = -> Sketch
  MidPlane = false
  Reverse = false
  Suppressed = false
  length = 67
  radius = 0.1
  thickness = 0.3
  expr: radius = composit_properties#<<Properties>>.bend_r
  expr: thickness = composit_properties#<<Properties>>.al_thickness
FEATURE [Sketcher::SketchObject] Sketch001
  ArcFitTolerance = 0
  AttachmentSupport = -> [YZ_Plane]
  FullyConstrained = true
  MakeInternals = false
  MapMode = 5
  Placement = pos=(0,0,0) rot=(0.57735,0.57735,0.57735;2.0944rad)
  expr: Constraints[11] = <<composit-properties>>#<<Properties>>.bend_r + <<composit-properties>>#<<Properties>>.al_thickness
  expr: Constraints[7] = <<composit-properties>>#<<Properties>>.thickness
  expr: Constraints[8] = <<composit-properties>>#<<Properties>>.bend_r + <<composit-properties>>#<<Properties>>.al_thickness
  sketch-geometry (4):
    g0: LineSegment StartX=0.4 StartY=0 StartZ=0 EndX=3 EndY=0 EndZ=0
    g1: LineSegment StartX=3 StartY=0 StartZ=0 EndX=3 EndY=0.4 EndZ=0
    g2: LineSegment StartX=3 StartY=0.4 StartZ=0 EndX=0.4 EndY=0.4 EndZ=0
    g3: LineSegment StartX=0.4 StartY=0.4 StartZ=0 EndX=0.4 EndY=0 EndZ=0
  constraints (12):
    c: Coincident(g0,g1)
    c: Coincident(g1,g2)
    c: Coincident(g2,g3)
    c: Horizontal(g0)
    c: Horizontal(g2)
    c: Vertical(g1)
    c: Vertical(g3)
    c: DistanceX(g1) = 3
    c: DistanceY(g1) = 0.4
    c: Coincident(g0,g3)
    c: PointOnObject(g0,g-1)
    c: DistanceX(g0) = 0.4
FEATURE [PartDesign::FeaturePython] Bend  # WARN: FeaturePython — macro-defined, semantics opaque (R4)
  AutoMiter = true
  BaseFeature = -> BaseBend
  BendType = 1
  LengthList = [14]
  LengthSpec = 1
  ReliefFactor = 0.7
  Suppressed = false
  UseReliefFactor = false
  angle = 90
  baseObject = -> BaseBend [Edge11,Edge42]
  bendAList = [90]
  extend1 = 0
  extend2 = 0
  gap1 = 0
  gap2 = 0
  invert = false
  kfactor = 0.5
  length = 14
  maxExtendDist = 5
  minGap = 0.1
  minReliefGap = 1
  miterangle1 = 0
  miterangle2 = 0
  offset = 0
  radius = 0.1
  reliefType = 0
  reliefd = 1
  reliefw = 0.8
  sketchflip = false
  sketchinvert = false
  unfold = false
  expr: length = Sketch.Constraints.width / 2 - 5 mm
  expr: radius = BaseBend.radius
FEATURE [PartDesign::Pocket] Pocket
  BaseFeature = -> Bend
  Direction = (-1,2e-16,-3e-16)
  Length = 5
  Length2 = 5
  Midplane = true
  Profile = -> Sketch001
  ReferenceAxis = -> Sketch001 [N_Axis]
  Suppressed = false
  Type = 1
FEATURE [Sketcher::SketchObject] Sketch002
  ArcFitTolerance = 0
  AttachmentSupport = -> [YZ_Plane]
  FullyConstrained = true
  MakeInternals = false
  MapMode = 5
  Placement = pos=(0,0,0) rot=(0.57735,0.57735,0.57735;2.0944rad)
  expr: Constraints[10] = BaseBend.length
  expr: Constraints[11] = Sketch.Constraints.length
  expr: Constraints[12] = <<composit-properties>>#<<Properties>>.thickness
  sketch-geometry (5):
    g0: LineSegment StartX=0 StartY=0 StartZ=0 EndX=20 EndY=0 EndZ=0
    g1: LineSegment StartX=20 StartY=0 StartZ=0 EndX=20 EndY=3 EndZ=0
    g2: LineSegment StartX=20 StartY=3 StartZ=0 EndX=3 EndY=67 EndZ=0
    g3: LineSegment StartX=3 StartY=67 StartZ=0 EndX=0 EndY=67 EndZ=0
    g4: LineSegment StartX=0 StartY=67 StartZ=0 EndX=0 EndY=0 EndZ=0
  constraints (14):
    c: Coincident(g-1,g0)
    c: PointOnObject(g0,g-1)
    c: Coincident(g0,g1)
    c: Vertical(g1)
    c: Coincident(g1,g2)
    c: Coincident(g2,g3)
    c: PointOnObject(g3,g-2)
    c: Horizontal(g3)
    c: Coincident(g3,g4)
    c: Coincident(g4,g0)
    c: DistanceY(g3) = 67
    c: DistanceX(g0,g0) = 20
    c: DistanceY(g1,g1) = 3
    c: Equal(g3,g1)
FEATURE [Part::FeaturePython] WireFilter  # WARN: FeaturePython — macro-defined, semantics opaque (R4)
  AttacherType = Attacher::AttachEngine3D
  ClaimChildren = true
  ColorKeyCount = 8
  Colorize = true
  FaceMaker = 5
  FixNormal = false
  FollowSource = true
  InvertedFaceScale = 5
  MaxWires = 25
  Normal = (1,-3e-16,2e-16)
  OffsetFill = false
  OffsetIntersection = false
  OffsetJoin = 0
  OffsetOpenResult = false
  Scale = (1,1,1)
  SelectEdges = false
  Source = -> Sketch002
  UniformScale = 1
  UseDefault = false
  UseSelected = true
  UseSelectedEdges = false
  Version = 0.2022.02.09
  WireOrder = [1]
FEATURE [PartDesign::Pocket] Pocket001
  BaseFeature = -> Pocket
  Direction = (-1,3e-16,-2e-16)
  Length = 5
  Length2 = 5
  Midplane = true
  Profile = -> WireFilter
  Suppressed = false
  Type = 1
FEATURE [Sketcher::SketchObject] Sketch003  label="fix_holes"
  ArcFitTolerance = 0
  AttachmentSupport = -> [XY_Plane]
  FullyConstrained = true
  MakeInternals = false
  MapMode = 5
  expr: Constraints[1] = 3.4
  sketch-geometry (2):
    g0: Circle CenterX=-10 CenterY=15 CenterZ=0 NormalX=0 NormalY=0 NormalZ=1 AngleXU=0 Radius=1.7
    g1: Circle CenterX=10 CenterY=15 CenterZ=0 NormalX=0 NormalY=0 NormalZ=1 AngleXU=0 Radius=1.7
  constraints (5):
    c: Equal(g1,g0)
    c: Diameter(g1) = 3.4
    c: Symmetric(g0,g1,g-2)
    c: DistanceX(g0,g1) = 20
    c: DistanceY(g1) = 15
FEATURE [PartDesign::Pocket] Pocket002
  BaseFeature = -> Pocket001
  Direction = (0,0,-1)
  Length = 5
  Length2 = 5
  Midplane = true
  Profile = -> Sketch003
  ReferenceAxis = -> Sketch003 [N_Axis]
  Suppressed = false
  Type = 1
FEATURE [Sketcher::SketchObject] Sketch004
  ArcFitTolerance = 0
  AttachmentSupport = -> [XZ_Plane]
  FullyConstrained = true
  MakeInternals = false
  MapMode = 5
  Placement = pos=(0,0,0) rot=(1,0,0;1.5708rad)
  sketch-geometry (2):
    g0: Circle CenterX=0 CenterY=18 CenterZ=0 NormalX=0 NormalY=0 NormalZ=1 AngleXU=0 Radius=2.5
    g1: Circle CenterX=0 CenterY=55 CenterZ=0 NormalX=0 NormalY=0 NormalZ=1 AngleXU=0 Radius=2.5
  constraints (6):
    c: PointOnObject(g0,g-2)
    c: PointOnObject(g1,g-2)
    c: Equal(g0,g1)
    c: Diameter(g0) = 5
    c: DistanceY(g0) = 18
    c: DistanceY(g1) = 55
FEATURE [PartDesign::Pocket] Pocket003
  BaseFeature = -> Pocket002
  Direction = (0,1,2e-16)
  Length = 5
  Length2 = 5
  Midplane = true
  Profile = -> Sketch004
  ReferenceAxis = -> Sketch004 [N_Axis]
  Suppressed = false
  Type = 1
FEATURE [PartDesign::Body] Body  label="Body_material_0.45ansi"
  AllowCompound = false
  Group = -> [Sketch,BaseBend,Sketch001,Bend,Pocket,Sketch002,WireFilter,Pocket001,Sketch003,Pocket002,Sketch004,Pocket003]
  Origin = -> Origin
  Tip = -> Pocket003
FEATURE [Part::Feature] Unfold034  label="socket_fixture_unfold"
  Placement = pos=(0,0,-3) rot=(0.5774,0.5774,0.5774;0rad)
  shape: bbox 77.8 x 0.3 x 85.8 mm, 24 faces (baked)
